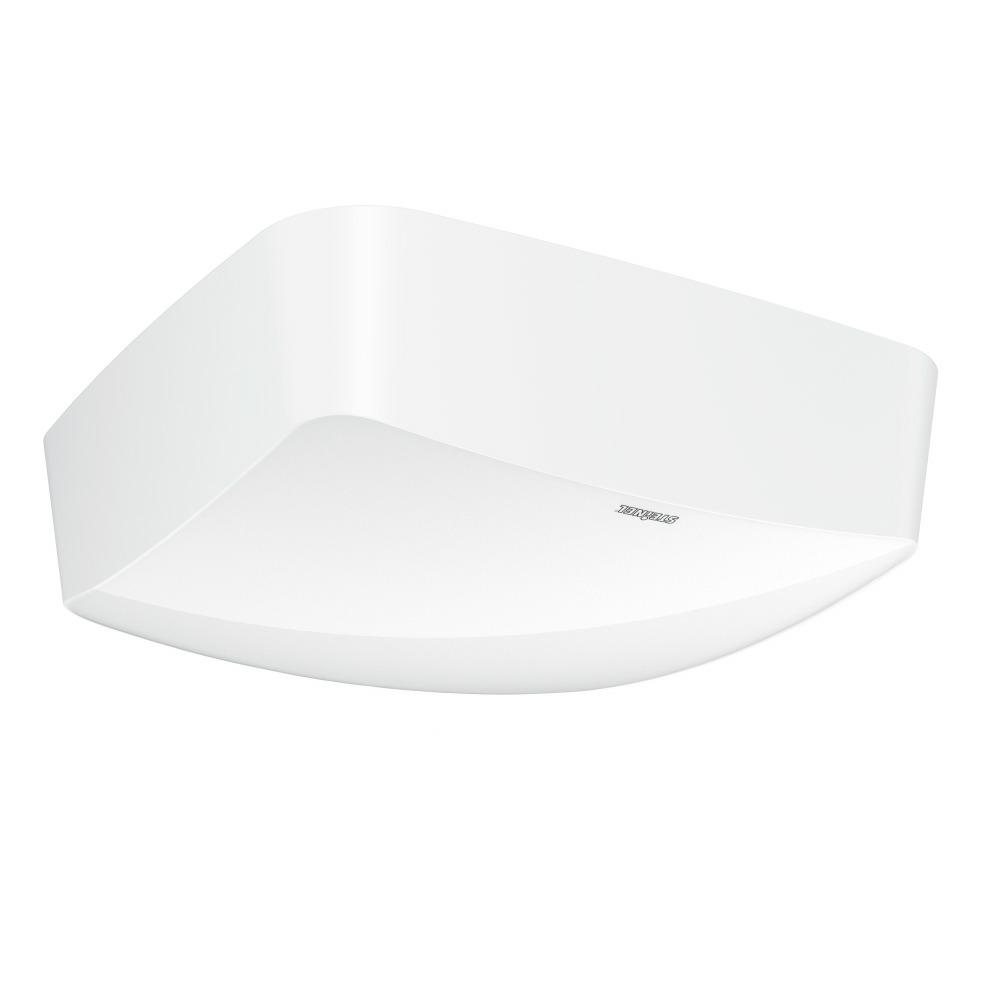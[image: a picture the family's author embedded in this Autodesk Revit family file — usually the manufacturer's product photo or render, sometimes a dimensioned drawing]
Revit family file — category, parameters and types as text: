
# Revit family: truepresence_057916
name_source: partatom
category: Electrical Fixtures
revit_build: Autodesk Revit 2016 (Build: 20151007_0715(x64)
units: mm (PartAtom-declared; Revit-internal decimal feet)

## family parameters
Cut with Voids When Loaded = No
Host = Face
Maintain Annotation Orientation = No
Part Type = Normal
Room Calculation Point = No
Round Connector Dimension = Use Diameter
Shared = No

## types (1)
- True Presence
    Apparent Load = 0 VA
    Default Elevation = 1800 mm
    Description = Type: Presence detector; Dimensions (L x W x H): 45 x 123 x 123 mm; Mains power supply: 220 – 240 V / 50 – 60 Hz; Power consumption: 1 W; Sensor Technology: High frequency; Application, place: Indoors; Application, room: classroom, lecture hall, one-person office, open-plan office, high-bay warehouse, production facilities, conference room / meeting room, hotel room, care room, duty room, recreation room, dining hall / staff restaurant, changing room, kitchenette, sports hall, reception / lobby, WC / washroom, warehouse, Indoors; Installation site: ceiling; Installation: Surface wiring; HF-system: 7,2 GHz; Electronic scalability: Yes; Mechanical scalability: No; Mounting height: 2 – 12 m; Optimum mounting height: 2,8 m; Detection angle: 360 °; Angle of aperture: 360 °; Sneak-by guard: Yes; Capability of masking out individual segments: No; Reach, radial: Ø 15 m (177 m²); Reach, tangential: Ø 15 m (177 m²); Reach, presence: Ø 15 m (177 m²); True Presence reach: Ø 9 m (64 m²); Twilight setting TEACH: Yes; Twilight setting: 2 – 1000 lx; Time setting: 30 sec – 30 min; Switching output 1, resistive: 2000 W; Switching output 1, number of LEDs / fluorescent lamps: 8 pcs.; Switching output 1, floating: No; Constant-lighting control: No; Basic light level function: No; Functions: Group parameterisation, Semi-/fully automatic, Lighting scenario, Manual ON / ON-OFF, Neighbouring-group function, Normal / test mode; Settings via: Bluetooth; With remote control: No; Interconnection: Yes; IP-rating: IP54; Material: Plastic; Ambient temperature: -20 – 50 °C; Colour: white; Colour, RAL: 9003; Manufacturer's Warranty: 5 years; Version: COM1 - surface white; PU1, EAN: 4007841057916
    Height = 0 mm  [stored 0 ft]
    Length = 200 mm  [stored 0.656168 ft]
    Manufacturer = Steinel
    ModVariant = No
    Model = 057916
    Number of Poles = 1
    OnlyDefault = No
    Power Factor = 1
    Product Name = True Presence
    Product group = Sensor-switched outdoor light
    ProductGroupID = 3
    RLX_Detail_Level = 1
    RLX_LegendID = 1.1
    RlxData = Q
eAHsfQe8HUd99ZVluchyE3Jvz71fby/Se0/v2pJ7ky33Jhe5gFxw7wgXsKm2Y4xDL6YEQglx
CGA/yR+hGpKQ0PIFEgjhw0ACIeAkOBR958zOmIux8JvH1fPc+45+Om/+87///+zs7rl7dvbO
7s5orVnTwr81vzYFTfNvI2egXIN/rrrrsc5qcpjn0GqtXAisRoT5YxLXrPnBzHmtQy6/9LxL
Ljv36ksuv+zoay6FdcmVyzfaYAZTt1naurJ1TWt5a6h1PKzlrauAy1rnG88+raiVt8pW3Ypb
BSL2bY2h9R1tH7o7ORO+NWv+feac1tGXXHTx1YsvveTqq5df2Royy5h9Zevc1gWtc36rNba0
07O2tB5a+sHM9VvHLL/q4hmbmRbMcnd+lugZrfWt9ydY+Yn884r76XGvfg836O/517S3pYn4
5j6t1mJYLwMun3v77hffe+n4nrd/a8G/vmuHcWf/9Re/+Gj22Rnj2+60/oJ9tl4wfv9RF43/
3V98ecGv7ztpnNh634cXbP/Jrz1K3P/eh+fffdddw13xIy4ebY64Nmd//Z177HDQP73r4GXL
90TesMtFeyOuTcSOsJPsD232iTbaHmGf2B+0PcI+sT/0c9ld/hH6be4Ic+2yhtlPu6wR9t+u
l4ln22y3ax1NDP23fOvbw8Wun5nP/rItt77Oz+W7XLTJdTft2HU3fcB2fif71LWdjY3Ycbcu
tLk89gFtP0qby6XNZdBmDG3G2Fy3vuNcnt1u413bkP7xruWOYz8M83P0x9i2n8Y+Zc38kTkn
XWRst18YD98IPjN+t1/op822nM22uuKN7bY5/bZ947fLNbbtj/OThy7X8M3mjru+sezqj1lH
2wezHZzt+kZ+sR/021xjsw2uG/0/WfaWR4HhLvtRa5vPumwTw7ZnAOtZ0OYRhnWW/M4TswAX
Q3sDW2fp/tHe0FZY8qi1MTAbYA5Bm3EsN7E267SZMwfYFNjMgvbm1mbJOIL5Lob2FrbOkm0Q
tHm0oM1yLsD+vABgDkGbcSznWZt12szZCtga2MaC9rbWZrmdBe3trc2SyyFos22CNtslaO9g
bZY80hO0eawmaPNITNDmsmmz3MWCtusjY9gPgjaXMQTsCrj9SHs3W2fp9gvt3W2dpes/bbeO
tN12oL2HrbPc04L2Xha097agzWWzzhKHbwPaQwBLxrAfBG0uYwbAf/ta0N7PgjY5xjrL/S1o
H2BBm7xineWBFrTJI9ZZklu0WbYtaJN/rLM8yJbkE22CdmRBmxxjnWVsQTuxoE1esc4ytaBN
XrDOklygzTKzoE1esM4ytyU5QZugXVjQJk9YZ1kCQ8D6QGVBe6a1WdYWtLntWWfJ7c+c+cCQ
Be19LGgvALjvuY+HLWiPWNBmPOssGU/uklOjFrTJJdZZLrSgzbZZZ8n2GTMGsA2CNteToM31
5bqz7FjQHrM2S7dctutiaLN91lmyv7RZHmxBm/1nnaXjJ223DWm77Uyb24hx5Ktrh/Yhts7S
9YH2Iltn6fYpbe5ngrbjBm3HJdqOb7QdD2k7rtLmMlhn6fhMm98j1lm67wJtfj8I2vw+se+0
mXMo0P3v3/5sk0987uflqoe+etPqRdf+z4Kdtx5ZtcPrb1r91EdeOjx3p8NWrZp30+r/OWTO
+Juu+OX4S//fLas/dcNOjzz8q/8aP3XPW1dfdvOxj6z+zyY3mfuWT/zk8hWr5m51w+qbX/7L
T5z1+bHxhX/5ktXZ2OnDRx4zd9UXTrtl9QOr73/0r5441LT5q5+X3KUtLvcf5o6Mzn2oNczl
HvndQ0f//onXDXO5x5/wi5GH580zyz129n9zV7a43F/9rBzd9t79H2HuX12xwrTD5X7kp2Mm
hss98cS5o8n+Jw9zubbNR02brW0XfPSsc0Y/+NUbVj/YmTn85H37jQ6/8ObV87b94qOXvmmj
0fe8/ZbVS4otFnzpw98emX/1rau/975TF3z3+rERtvm1jzzwSPrmO0c+dNVLVh97/H8tOGfG
0Oie//fm1b868t2PtP+saeetcz8+/x2Xrxhlf/5mt33qiz/d+G85+5xVT162/gIu94f37Lfq
1H+ZNczl/v1PN1r12Bbjj3K5n3/42+Mjj/xgPpf7ybGx8R9+77YFXO6qw+8cf/RjX3mEy/3a
rKFVPz/nBwu43H0/sN+qdM5HH2E741esWHXs+qfWXO6pn95v1ed3e29N/x/ft/8jn13zktXc
djfusXh0TX6TsT/56cNGuT3o/8d6s4XxN5Ya+0M3LV143uc2M/amP7tx4YcvPHIVYxC7EDnG
bplhFb0Y4eQ3LWS7tG2MsdHeQrZLP9pbyHZpo71Rtkvb9sHYrLt22RfkrqaHfUGusdkX5Bqb
fXH9Z+n6xvVDf1w/TSzbYXvsE222xz7RZnvsE23bjrFt+yaG7XE9GfObfysXzkBlPWAmsD4w
C6BvA4C6RU2jb2NgNrAJQO2hRvGcaHOAvi0A6go1h74XANQWHiu3Bnis5bnCdsD2wA7AjgA/
3+lZsDN8xC7AELArsBuwO7AH4I7R/JzH+mfCaYU7VrrSHUd4TCHccYbHHh6H3DHLlTye8fjm
jnfuGMhjojve8zjvwGOwOyY7naLPHdu5Y7rBHTJm0UHJYzV9PM7xuLn4ecJ5WO7nATdeefcb
P2WOS0/84k9GZr/568Ptk78ycvgrPjd/3r3/MjI667EFd930pyOr919v5KEj9jWff+n/HjHM
zzfCOAHNmHbY1irEMC5CDvPcZyw5XtgIba+3/4Yjn33zCaMskTNK/9LWitEvo83Rey8aZR7j
Hvj3B0fGsAz2hfnsI9u/G325foNjRlkyfiv0ke0xnstlfcmFM0cXXv7Dkav/aFtTPnrvUyP0
s35J60MjD524jclfM3qIqW92YDLK/rPOvC/8bJkpX771afD/aKT5/EcjrztkE1O/989/MsL+
suR6sH32O9ty62a9sAz6uRxuD/rZv4vhZ8ntyf5z+7JfXCb9bM+VXG8um+vNkv1jye1F37E3
NtcEWLJOP2PMdoZNP/cP62875UhTcr9d/MEvL+B2op/lqfXDC9gP1lmybpaNuKsO/Yrxczvz
c5b8nNuH7fz435YZP7cTl8eScdxerLNknduNdZasc/8wn9uN7bGkv33ZTPO5W1e37tE5bxmJ
Afbn1qt/OHILcDVs+i+/YGfjH5//2fn0vxfrehl89LNkHrcDtx23A/NXIpb5LBlPP/PJMx4f
17OgzWMn6+4Y6o6jLobHTx5PWWfp/rljLOvuWOuOs8wheMxlnDv20iZ4zGXOM4/F7jjMY7A7
HjOW+TxeE7R5fKbNkm0Q7phN2x272R8ev5lD0GZc9/GcdR7TmeOO6+6YzmM8j+Osu+M5j9m0
hwDaLHe1oM22CdrUDIL2btZmSR0gaFMPCNp7WtDmsllnuZcFbddHxrAfBO0hgDpC7XB6QXs/
gPt0f4D75ACAPmoHbZbsP7eV0xGuF/1cb2oJ/dQS1rv1hLbTFNrUFYI2l02bJbWGoO36yBj2
g6DN5VGHujWINklL0OYBlzbLYQvaIxa0R63NklpE0B4DOsDBwCHWZrnIgjaXzzpL6uC67s9i
LONQ4DCANsvDLWgfYW2WR9r6UdZmnfbRFrSPsTbLY4HjgOOBJYDvujPnBIBtELTZLkGb7bNf
k+2P77pPpD8noj9LgZMsaJ9sbZbuvOgU62McbXKYNktyljbLUy1ok7+ss5xhQfs0C9r8nhG0
TwcYx3+uHdpn2DpLLoegfaa1WXI9CNpnWdA+24L29ha0z7GgvZUFbR4LCdpcBm2Wm1rQ3sja
LJdZ0N7Egva5AP/RZg7/uXXj97KF8Qjr6xnbfbaSX72nfTz2uLiZsBjPbU8f85yvaWPlQta5
LVnnNnJxzsfP6WOdbbPOY4mLcz5+Th/r1B7Weaxzcc7n+sdP6HPxjGN9Q+vndqGPf52PJX0s
uY1Y8pjk4pyPxy76uPzZAP3zAPq4POdz/aOPNuMOABjHvjDOtUEf6+wXS2qni3M+12f2izZh
VgC55AT5wHIRwFzWNwPcZ/TRdr4tYbs4Lo/xB9OFOMY4H236uDz6WB8DnI91F08f++/qPBdw
PtoEuU0fY5zP9YX9o4/1uQDjuuvbWB/jXAy1n3Hd9SOsj3FshzGHWh+3OevcZ9RC1z/nc/3j
culjfWuAcS6G9Z2tj3Fsiz7XP/aFPtaPApjr2tkWtT2tz+XQx3Gpi2MefcsA+hjnYvayPhfD
PB5HGOdiWN/B+hjnYtrWxzgXs7f1uRjm7Wh93FaMY91tK/oYS9+BAJfL7cI4xrjtwvWnj/Vd
AMa5ZbLulss4LpO+IYBxrg+s70oXfIzjMoeAowEXx2UyZje6EOf6St+x1sf22A/G7G59rq/0
HW993M6MZYzbzvQxl749AC6DPvaXdbcv3XrSR21lHPc54xhzIUAftz2XwfbdNhiCzf7uA+QA
49bHX+fbt8s3BJtxS63PrTtjCutjLteLvv2sj8ch+ljf3/rc9mC9tD7GcV3pO8D6uM/pY93t
c3KAPtYdr8g1+lg/COB6sM5twrpbBuOcL4LNONa5nViPAfoY53znWh/juO0Yk1gfY5zvfOtj
HLcvY1Lrc9ucvjOtj9uPsYxx248+5tKXAewLfdzurLt9xBjnOxs244bw1+3H0+mCj9uZy2D7
bhvANPunQlmzgrgZ+Mt9Rt+pAH38y33GmPmswOf2K31XW99GKBnHmAVdPu5H1oetz+1/+u60
PuZy3zJmxPrc/qfvDuvbECXjGDPa5SMHWDedRf8cT+hzuZvAZhxjxgCuB/WEvjGgAzgf+cP6
wXQhznGMvtutb1OUjGPMIV0+8oz1RdbnuEjfbdY3ByXjGLO4y0fusX6o9THG+VZa31zrY8xh
XT7ykfXDrc/xmL5brY+55B5jjrA+x2P6brG+LVEyjjFHdvnIR9aPsj7GON/N1jfP+hhztPXt
aH2sH9PlI5dZP9b6HN/pu8n6eJxkHGOO6/LxO8D68dbHGOe70fp2tj7GLOny8XvA+gnWxzzn
u8H6eNykjzEndvn4/WH9Iutz3yn6Lra+9VHyO7QUOMn6hlA632nWN9P6GHNyl4/fK9ZPsT7m
Od+V1sfvKn2Mcd9Vfi/pY/3FALnLXH4nTwOuAugbwl/nO50u+PaxPtbPoAs+xvB7yrrLZZzz
nQObcXvjL7+nZwJnAfTxWOd8F1gf4/jdZczZ1scY57vU+rgM+hjjlsFl0sf65QCXsQ3+jgLL
gHMB+rbCX+dbbn17Wh9jzuvyLbT1862Pec73IuvjetDHGLce7DN9rK8AuFzmjgFc5gsB15cx
WPRdCNC3C/6OAaw7DpFT9LF+CcA4+ni8Iaecj1xzvuthM24Mf+ljjFsu+0If62492F/6WHd9
5nrQx7rb9tzG9LF+GcBl0HcwwLrb9oxxvmthM477iD7GXAHQR07Sz7rjJH2Mo+9qgHHkLeMY
4zhO7tLHuuPffrCZy7xrAObSdwjA+p0AfYxxPtc/9pk+1q8DGMf6IoD1lwD0Mc753HbmtqeP
9RsAxuX4Sx/rNwL08ThEH+s3AfSl+Esf6zcD9CX4Sx/rtwD0xfhLH+u3AvRF+Esf665/9LHf
rK8EGHcQ/tK3EngpQN/++Esf62670MdY+m4DXFzb1m/v8h0Im/U7rG/GL771q2+tXvNPa36F
uZsHLf568/ddv/z6z855/CUja9716FPfOufxN6751b27dYZ2ag0dMXf9H9ixqWmgddqP7x47
7ccbc/O27mpc+Os1c/HprLUb/u3t2NXYDNjE2v9tgI++eHCCoFkrZ2yGWZ2YrDoG3y42ZSNb
sghrHucp+CLzOPE3wGfOf9H4uw9aOHL0sm8suPf9p40DI78oH3na5m8N+HwccSbm37ZZOP7W
S19kfoO4btUu47/8kxeP7H7hEwuczXh8Po44E4PPx/GZiXE2Y6w9zlza3ErOZlsuhv6uPox3
9XO8q58m3q6LibF9MH7bZ2PbfprlOpvts4/sB/vAOZfOdn7GsC/0d9lmvax/pKsd47e5xs/t
4bYbt7fbntzeBHOdzfXi526/MK9re46wXbutjM1c9At79eltaGznR7xZL8bQpt+2aWy7LLdt
2R/jt/0x29n22cTYdTExXCb/sc1N8ovGgZFZr/rygu32uxRzUo8eyVb984I/G79xfOyqo0b+
9rynFrzjGyvHuX2f/PrMYesfp9/GjzPetjPOdhj/xC/2HWe8tUdoo71x5jP3fZcfNdJZfeP4
/yx/ijLRYhxjmOds9ovtsk34R5wfbYy4vtkY0398PsI4u9wR12frN+3bXNMHrOs41sGsr+2b
WV/bH9OO7Y+z2Qdjc/lsi+vCbebaeTx9jVn3f19SjfznP9w9fsqnTxqnPfrdG8cJ2vTxM9ps
nzm0L587853O5no4G/GmLduOaYs22jBt0UasacvZXAdnsy1rs29P2y7G9s34bZ+NbftpbNtP
Z5vlsU22wWXTRjsGtG2fjd/209jnvWH8UWCYMdZ+1NrDrHfZJobt85i+ngXtmdZmub4F7VnW
ZskjPXM2BNw/2jzCE7Q3BmYDmwBzLGhvakGbsayzZPxmwObAFha0t7Q2y7kWtNk26yzZPnNe
ALANgvY8C9o8/90a2AbY1oL2dha0Gc86S8ZzXbcHuL4E7R0saFMfWWe5kwXtnS1oU/1YZzlk
QXtXa7Pczdosd7egvYe1We5p63tZm3Xae1vQ3sfaLHkuSdDmeSBBm+c5tFkeYEGb5zSss2xb
myXPiQja3H60WXIbcj9zu3DfEbR5DkabpdvXtB0HaHPbss6S+4btkE/MJ2iTe7S5fZlD0OZ2
ps2S24Cg7bYb7SEL2tz2jOF2cu3Q5rZhnaXjA223vrTd9qHNbcY48sO1Q9utwxaw3TrSJjdn
APzH81eC/3h+S5tlakF7I2uz5HeD/2i7OPp4Dk3Qnm1tlrkFbZ6Ps86ytKC9uQVtfn8I2i6/
gu3ar2Gzb8zhd8m1Q3u+BW1+T1hnye/P1sACa7NOe9jWWY4AjCGX+BlBe9SCNvlH/0LA5XAZ
bG8vgN+FMQva/J6wzrJjQZvfq4OBQ4AxC9psg+Uia7NOe7Gts+T3hKDN7wZBm/2kzZL9nAkc
CsyyoH2YtVkebkH7CIDx5ATjCNrkAm2WjDsSOApwubR5rGGdJZfF9Twa4GcEbR5raLNkHNef
xxnGErQZx5IxtI8BuN+PtaBN7rDO8jgL2uQA6yy5P2izPN6CNvcv6yyX2JL7kDZB+wQL2tzH
rLM80Zbc97QJ2kstaHO7s87yJAva3DesszzZgjb3K+ssT7El9z1tgvapFrTJF9ZZngbwe5AB
p1vQPsOCNrcX6yy5Lbn/uB/PtKDN7xHrLM+yoM22WWfJ9hlzNsA2CNrkDEH7HIDcIA+WWdA+
14I2Y1lnyfgxgPv+PAva5AjrLM+3oM22WWe5DGDMBcCYBe2DLWhz+7D/7PtyC9rcHqyzvNCC
NrcP6ywd38ghF0Ob3GGdpeMM+eFiaF9k6yzdcmlfbOss3TahvcyCtltf2lw/gjbXh6DN9SJo
O27Q5jJYZ+n4Q9vxjbbjJG3ylKBNLhO0uQ7sH/eP6z9t7mPWWTr+cPvSx+3R/a97HnP3/GY7
53g1Y7vnQ09krnP3PObu+c2YN8y50aNss3s+9ETmOnfPz7Zzjk3fuuc6d8+B7p4bPZF5z91z
mrvnOnfPge6eGz2Bec+r3/nGC1YlW95d/+zuG35r3nn7a9euuu+ksxbsdNX1q7f85rWrZr7g
sPm0v3DNDas+89RF8+864mn/J+h/0YMXrPrU5dsvYDtPvOfWVZ/6u/vmb/lf161Ot9z44+/H
Muh/6eJXfuIL737xqv/51PWrH3zjVZ/4wTeuXcXcH9232SPvv+qGVWzztbtlj4y+von/3D9t
8MjSd9+6iu2c+81rzT5h/Ir3vNjYbOe9r79g9CHcP8D273nvrcbP+PLaG4zNNt/8zhePrkYM
4z/4xguMn/Hd8/v/++R/mv/Vf7x2lO1/+6kn6h2Rz9xv/t3c+cvRbte6jDL3o63dF8x58AJj
23UxuQfv9OoFR/990877b75u9X4LFq36r0sOXDXrS0tW7zo0ZzXt13xwzuq3X7HE2Pd+49BV
O59xnbGvXzL0yI8Ounn1QZtFq155+iGjn3l547/9J5ss/MJ/NPFHfXjJwtcf17Tzqhdft3C3
HRab9oeimxeSs8zdJUIbcx+uabewzB2+tGQhl/tKLPNDH5xj7K2xzPY3Dx01/Zm/aNWf33yd
8R80N6vZFnPv3PyEhf/82CbGv9dL5iy84p6mnQ/8YvHoKRc28V+977qF37nhYNMOl9/8+80c
nvXgmAmsD8wAZgEbABs+AxuhvrHFbJSbAPTNATYFNnsGNke9G1ugviUw1+IFKIl5wFYAz8O6
sQ3q2wLbWWyPktgB2BHYaR1jZ7S/CzAE7GrB+m5doH93YA/Axe8Jm9gL2NtiH5TEvhbOvx/q
+1scgPJAizbKg4DIgjY/p34TCZAC1PwcKIASoO7Xtk4/MR9gHMEY5hELLIZREiMW/PIRJGs3
xlAnOhYHoyQOsViEshuLUe/GoagfZnE4SoI+nhsQ1Plu8ByA54QENZqgr1urj0N9qvFWLDOf
gX1z1SeGT71q5fw3XXknN1+L5RuHXjhcb/KLEVfSP+8LPxph3IOP/cj4H9/qn0du/umH57Nk
3NCbP2Hyjj/rqWH6WdL/2uI1Jo4l6yfftuco2znkOztz97RY0n//y/c05S/OPHCU+SzpL4Zv
MfUHjz7JlKzTzzrLz3zzzqdLtjf+qttM+zu/4jbj/8iTM0bZZ/Zz79tnjn72zpmjr9rin0fY
nyXxa0ZYd+XJhz81zLjXf2e/YeZ8+2eHmO3AbcE622Ie2+H6sbxnzv7DbI+xjOH2Yzy3B+P5
OdtnyfaZx/b5OXPM9kYO7V3gY/v83Gx/+NkG/dxO9P31NduPcl9EL91h9MPfa41es972o3/5
+idH/uotW4/+9D9+NrLdd7Y168eSy935X+aZknUun3Ef/9bbh5n3vv3fOrzT52eZ+ouWr2fq
bHO9rywdZvsszf5BP7jcNrjC9q756++acvFB/zrCvvz9TouGuez2BzYYfvjJtw+z5Hp8/F1f
XXB79q+mJM8Y10KbbHfFd747zM8jxDL3S/iMbfFz9uExfMb2WXI9WHK5jGf/Gc/+kE8v+OmM
0eXb7TbKdSBvuF+euHy3Ua4befLJl204+ta/3s+U933hJaZ8cqs7nv7c7M9Xv9xsz+8tvMO0
Q57RT35xu5NXXA7befWPh0ZY/vAj2y445hu7mDqXt2Ljp+Yfev/Wps7t99pfdua/4cuzTJ3r
xDrXlXF7bffUCNvh9mE7LFnndmOdJevcTqyzZJ3bl/nfPu7Vps7txXavmLWBqXP9GM/1Zsk6
81hn+amZrzDl8Vhf5nE7sL2fnn2n8X8M25b1+2bNGf3+C54a+Um62Sj3wwNvGB95HcA690dT
HzF17hfGPzH/1cNc34vRF67f9a/fxKwXv5dcH5YPvGEE7Ywgn+W4WV+2yfVjyfViW1yfP0Zb
K9EG+8Fc9oMll8+Sy+XnXC7juVzmc7lsjzHcrmyX/WG77B/b5Wc4/LXWA9x5wyxrs+S5A0Gb
5xC0WW4EMIfnEO4fbZ5LELR5TsHYOQDjCdo8vyBoM5Y2S8bzvGNzgOcXvv1x5yTu3KX7/IT2
s52f8FyF5yYEbZ7P0GbJeN/+cx3c+rvtAdfT24nbjOA/bnd3TsRzIdrunIjnRbR5PkWbJc+n
WLKf7tzqufrPdeC6cP3d9uD2oc2S24xw2923PzsidydgZwvaPK9ineWQBe1dLWjvZm2WPOdi
OzzvYj5Be09r74WSOQTtva3Nch8L2vta0N7Pgvb+AOMOAFw7tA+0dZZtC9o8PyNoRxa0Y4Bx
PF9z7dB268DzMLeOtHmOlgPufI7na7R5XkebJc/vCNo8t6PNkudzjKXt4ujjl5mgPWJtlvwi
E7QXAmNABzgY4Dkdfe58jvZiC9ou/1DYrv3DYLMvXI/DAbZD0D7CgvZu1mbJbcHtc6S1Wad9
lK2zPBpgzDEAPyNoH2tBm9ucfp4Luhwuk+1xv3FfHm9Be4m1WZ5gQXs/4ERgKeDiabMNlidZ
m3XaJ9s6S+5vgvYpFrTZT9ZZsp+nAqcBp1vQPsPaLM+0oH0WwHhygnEEbXKBNkvGnQ2cA7hc
2stsnSWXdS5wHsDPCNrnW5vlMuACYDnAWII241gyhvaFwEXAxRa0L7E2yxda0H4RsAK4FLjM
2iwvt6B9hbVZvtjWr7Q267SvsqB9tbVZXmPr11qbddrXWdC+3tosbwDWdX9uxDJuAm62oH2L
BW1uL9ZZclu67cTtdivwEmCltVm+1II222adJdtnDvcD2yBos12CNtv37c9tyHHbyrc/3L7c
9myDoM39RNDm/rkduAO404L2y6zN8uUWtO+yNsu7LV5hfYyj/UpbZ/kqi1dbH2Nov8bWWbrl
0n6trbO8x4L2vRa077Og/UcWtO+3oP06C9oPWNDmMlhn+XoL2g9a0P5jC9pvsKD9RgvaXAf2
702A6z/tN9s6y7dYcPsyhv9mNIU5BoNVk7pvi/uOuevh70yAbdKmj/X1AfeZi3O+kmE2bhYs
xvN7Th9jnI82faxvALC+LeDinM+1x+VtCDC+ABjHv87HePpY3whgnbaLc75jrI+fbQywjKyP
Mc63ifXNRkmbnx1nfazPsT7GcxmMc74trI9xmwKM4eeMY4zzUTfpY9uMZczRgPMxzi2fPrZD
H2MTgL7N8HdzgO2eCtDHOvvgluXinG9Lhtk42mxzKV3wMcb52DZ9rM8F3LJcnPMdxjDEsa+M
5fJPApyPca5P9LFf9HFZLpf2CwDmHwowjstzPsbTx/o8gHXaLs75Trc+frYVwDK3PsY43zbW
tzVK2vzsTOtjnVx08VwG45zvoK647WCzTX7OOMY43yLrYztskzFndPkY55bPXLZDH2MXA/SR
79sDbPcGgD5y2/kYTx/rOwCs03ZxzldZHz/bEWB5s/UxxvloM5f1nQD3GX20na+G7eJ2huXi
6WOM840wzLa3Cyx+Rr2jjzHOR5s+1ocA95mLcz7XHuN2BVjeAjBuCH+djzZ9rO8GDAEXAS7O
+fg5fazvDrh4F+d8wwyzcXvAYvxyuuBjjPPRpo/1PQH3mYtzvgUMs3F7wWL8BXTBxxjno00f
63sD7jMX53yjDLNx+8Bi/Aq64GOM89Gmj/V9AfeZi3O+hQyzcfvBcvH0Mcb5DmGYjdsfFj+7
lC74GON8tOlj/QDAfebinM+1x7gDAZaXA4xjjPPRpo/1NsD6uYCLcz5+Th/r/N66eBfnfAcz
DHH8PjKWOAdwPsa5Nujj95E+ogPQtwH+bghEQAE438aw6IvpsnGu7r6X3TGJjdsUJeNYT61v
jvWxnlkfjxuMY32x9TGOfvryLp87Hh5qfeuhZL/Z39L6+D1ne+yb+57ze0sf6/MBrgd95CPr
js+sM44+x0nG8XvAGPc9om/I1kdQsj1ykbnMc/wjn+hjfQxgHLc9/WOA2/b0MY6+RQDjGOP2
z8FdPnKFdcc1HjOZy7zu7bcF6txOhwFsj3+5Dw8HjmAFvhn463zXWB8L7jPGHMMK4hjjfEda
n9uvrB9lfYzjvqXvzda3EUrGMsa1Rx/j6Dsa4DI2wV/6WD8WcD5ygPXj6EIcY5zvFOubbX2M
Ob7LR+6wvsT6HJ/oO9n6mEv+MOYk62Oe851gfY5jrJ/YFUfe0Xe79W2OkrGMWdrlYxx9p1rf
ligZx5ju5ZK3JwMvBbi+7LPzvaHLRy5z/R+0Pm4X53ur9W2GksvlMk/r8pHfrJ9ufYxxvjus
b571MeYM69vG+lg/3/q2RsnvxpnAOdbHOOc7y/pY5/eH9fOsj3HOd7b1sc7vFOt3WR/jnM8t
l8cztsllLgO4rejj928ZcC5AH2Oc7zXWx+MofYy53PoYxy8J+/Yq62NfnO8V1sftxL6wHy+z
vj1QjgEXAMsBLncv/B0D6LsEoG83/B0DGHMh4HwdW7/I+sZQOt97rW9X62PMLdZ3MMpDgIuB
B6xvDKXzueXSx1jGfRBw/WMcY15IF/rH+iKA9fsBF+d8L7I+1nmsYf0+6+P6Ot8K69vH+li/
1Pr2tz7WL7M+7gvmsn6P9TGOfvrcPpoJ+1DgCuBqgP2bhb/O92LrY53HPdavtT7GOd+V1sf6
4QDrV1kf45zvButjHI+HjHmH9THG+d5tfTNQctns2zXWF1sf664v9LFN1t8EcD2OxN+jgOuA
9wP0cRnOd32Xj7GMe8j6tkfJOMbc3OVjPn1uPcgpHl9vBG4FuAzmOd9N1sc4+hn3J9a3I0rG
MeYlXT7G0eeWuwts5pOjbhn0MZd1l1vBph6sBN4IsC/0HUsLeClAH2Oc72Hr4/GZPsbc1uXj
8Z/1262PMc73F9ZXWh9j7rA+fqcZx/qdXT7qBOsvsz7GON9HrY/HAvoY8/Iu3xJbv8v6GON8
f2l9w9bHmLu7fNQT1l9hfcxzvo9Z30LrY8wru3zUGNZfZX3Mc77PW98C62PMq7t8S239NdbH
POf7nPXxO0kfY17b5TvJ1u+xPsY432etb7H1MebeLt/Jtn6f9THP+T5jfYusjzF/1OU7xdbv
tz7mOd+nrY/HNfoY87ou36m2/oD1Mcb5PmV9PG7Sx5jXd/mon6x/yPoY43yftL4M5enAg8Af
W1/d5Xub9THuDIAxb7A+5jnfn1lfZX2Mcd8Zfj8Yx/qfA/zOxPh7JvAm4M0AfTzeON/brS+1
Psa8pct3lq2/1fqY53x/bX1cD/oY8zaAy2Cf6Xsb8GGAPuaeDXCZXwRcX5zvHdZ3BEr6WH+n
9bF+jq1/wfoY53zvsT4e55YBDwHvArgMHiOXAfT9KUAf484FGPNugL5l+Ot843TBx2XQxxi3
DC6TPtYfBxjXwd/zgPcCfwLQN4a/zvcBuuDjMZI+xrwPcL7zbf391scY51ttfVwP+hjj1mOZ
9bG+CmB7zL0A4DIfA1xfnO+D1ncwSvpYd9w9zfpY/z8Ac7kvlwPcj45/3LfO53hA7tHHmI8A
zKXvQoB1x0nGON8nYDPuGOtjzMN0wXcs/jKO9b8A6DsOf+lj/aMAfcfjL32s/yVA3xL8pY/1
jwH0nYC/9LH+ccD5LrL1z1sfY5zP9Y99po/1RwDmsn4xwPpfAfQxzvketT5yhT7WHa/oYyx9
jkPLYDOOMW5fcn/Tx7rjAfcvfaw/BnC53I/0PQa4/cZ9SR/rnwQYdyr+0se66zN9XBfWPwUw
7hT8pY/1TwP0nYy/9LH+GYA+Hp/pY/2zAH1L8Zc+1j8H0Hci/tLHutvO/B5xG3D93Xea33P6
WHfHiDOtj3XHtRm4B7y5Gfzpe8PX3/jTWx5+2NBOn/6PJ0769Zo1H1rz8V+veeo/fv2/uHn6
y09cd83I377rzL/92ZmPv+vRG84+6/E3PvHVLR86fEbrvj06913wkLlEitbNv7tXXDq24rLv
jbFyl/Hwj/8t30+nPqvh395Oz9rO2pwb4IPmFvImwn95a2t5Mu1tgaQ1a74/c9PWiTdcet7l
KxZdee51l1x20bWPxzOa5lYufOGeR40+fsbyUbJllgmebYMPPff85TMZtobXpXi36T9c0XyR
TrrjHcPd9haPz13AwG4/7/p0MbQJxrAdZ7M+eyWXgUXgNxJ+5nLQr/F9DjrTfHFXfuZnj+67
4Z3GPumO3R5lHHNhDzsbMcMuBrkjLpfLcm0yp1keFzirxXa/+9XPD9NP++zd9zR9vG7mbb9l
r7jrMuNnjLN/u631WG25tmg/e9yGLbQ97OJou2Wy/2vzd8e4dpnrbC7P/ZvtDFOuWfOjmeu3
Djn65KO4w/k8g+5/G3VV7vyvN4wRXS5slHgR67zr9tInfmGAa11jrs7PLp5BTeDVLWJZhz5L
LpoT+NdcBftNINtpjeE/sBJ4G/AY8G2AA5stgCEgAsaA4wEu9wpgJXAXcA/wIPA24L3Ah4GP
AY8BnwO+BPwD8G3g+8BPgJ8DHKSvD2wEzAG2AOYB2wI7AkPAHsA+wAFABGRABQwDY8Ai4HDg
aOB4YClwKnAmsAy4ALgYWAFcAVwNXA/cDKwEbgPuAF4G3AW8AngV8BrgHuA+4H7gAeBB4A3A
m4C3AG8D3gE8BLwbeC/wPuBPgQ8CHwY+AjwMfBT4GPAJ4FFgFfAY8EngU8BngM8BjwNfBP4G
+BLw98BXgK8B/wD8I/BN4J+BbwPfAb4LfA/4PvBD4N+BHwM/AX4KPAn8N/Bz4H+BXwK/Bnjh
ZAawHjATWB+YBWwAbAhsBGwMzAY2AeYAmwKbAZsDWwBbAnOBFwDzgK2ArYFtgG2B7YDtgR2A
HYGdgJ2BXYAhYFdgN2B3YA9gT2AvYG9gH2BfYD9gf+AA4ECgDRwEREAMJEAKZEAOFEAJVEAN
zAcWAMPACDAK8OLPGNABDgYOARYBi4FDgcOAw4EjgCOBo4CjgWOAY4HjgOOBJcAJwInAUuAk
4GTgFOBU4DTgdOAM4EzgLOBs4BxgGXAucB5wPnABsBy4ELgIuBi4BHgh8CJgBXApcBlwOXAF
8GLgSuAq4GrgGuBa4DrgeuAG4EbgJuBm4BbgVuAlwMpDWiuB1ktRAq3bUAKt21ECrTtQAq07
UQKtl6EEWi9HCbTuQgm07kYJtF6BEmi9EiXQehVKoPVqlEDrNSiB1mtRAq17UAKte1ECrftQ
Aq0/Qgm07kcJtF6HEmg9gBJovR4l0HoQJdD6Y5RA6w0ogdYbUQKtN6EEWm9GCbTeghJovRUl
0HobSqD1dpRA6x0ogdY7UQKth1ACrXehBFrvRgm03oMSaL0XJdD6E5RA630ogdb7UQKtP0UJ
tD6AEmh9ECXQ+hBKoPVhlEDrz1ACrY+gBFp/jhIw/3R81vF5PXBhJrA+MAvYANgQ2AjYGJgN
bALMATYFNgM2B7YAtgTmAi8A5gFbAVsD2wDbAtsB2wM7ADsCOwE7A7sAQ8CuwG7A7sAewJ7A
XsDewD7AvsB+wP7AAcCBQBs4CIiAGEiAFMiARZ13bbio88DOizrfXLSo87IbF3Xet3pR57x5
iztfun5xZ8cfLe5c9eJDO3M2OKyz6/sP6/z3ssM7X9v7iM7c1pGdWT88srPl947qvP3Jozv7
b31s58CjjuscdP/xnU//55LOay84sVP9aGnn+led3NnmkFM7P9zy9M7Xnzqj87VfnIXzjGW/
hflLz+zUD57cebBY0vne3kd3Vi4/rHP9Dw7u3PzB0c5ffWh+55ffLzpjJ6edjZ48qLPT6gM6
9z+8b+dTf7dXZ3TeHp3P3bBr59TWLp3N371jJ7tk+058+Lad13a27vz3ifM6e906t/PzVVt0
zthq886SlZt2fvLrTTpn3jO788V0487t39+w8+UPbNDZ9vZZnUcuWr8TnzGz8+SZ63VevWJG
5xV3tzozL1oztudXfjX26dN+OTb8P/879uP3PzV2zHU/H2uOAfob9hYQp8XpsBnq3ztxWpz2
Z03YGeK0OB02Q/17J06L0/6sCTtDnBanw2aof+/EaXHanzVhZ4jT4nTYDPXvnTgtTvuzJuwM
cVqcDpuh/r0Tp8Vpf9aEnSFOi9NhM9S/d+K0OO3PmrAzxGlxOmyG+vdOnBan/VkTdoY4LU6H
zVD/3onT4rQ/a8LOEKfF6bAZ6t87cVqc9mdN2BnitDgdNkP9eydOi9P+rAk7Q5wWp8NmqH/v
xGlx2p81YWeI0+J02Az17504LU77sybsDHFanA6bof69E6fFaX/WhJ0hTovTYTPUv3fitDjt
z5qwM8RpcTpshvr3TpwWp/1ZE3aGOC1Oh81Q/96J0+K0P2vCzhCnxemwGerfO3FanPZnTdgZ
4rQ4HTZD/XsnTovT/qwJO0OcFqfDZqh/78RpcdqfNWFniNPidNgM9e+dOC1O+7Mm7AxxWpwO
m6H+vROnxWl/1oSdIU6L02Ez1L934rQ47c+asDPEaXE6bIb6906cFqf9WRN2hjgtTofNUP/e
idPitD9rws4Qp8XpsBnq3ztxWpz2Z03YGeK0OB02Q/17J06L0/6sCTtDnBanw2aof+/EaXHa
nzVhZ4jT4nTYDPXvnTgtTvuzJuwMcVqcDpuh/r0Tp8Vpf9aEnSFOi9NhM9S/d+K0OO3PmrAz
xGlxOmyG+vdOnBan/VkTdoY4LU6HzVD/3onT4rQ/a8LOEKfF6bAZ6t87cVqc9mdN2BnitDgd
NkP9eydOi9P+rAk7Q5wWp8NmqH/vxGlx2p81YWeI0+J02Az17504LU77sybsDHFanA6bof69
E6fFaX/WhJ0hTovTYTPUv3fitDjtz5qwM8RpcTpshvr3TpwWp/1ZE3aGOC1Oh81Q/96J0+K0
P2vCzhCnxemwGerfO3FanPZnTdgZ4rQ4HTZD/XsnTovT/qwJO0OcFqfDZqh/78RpcdqfNWFn
iNPidNgM9e+dOC1O+7Mm7AxxWpwOm6H+vROnxWl/1oSdIU6L02Ez1L934rQ47c+asDPEaXE6
bIb6906cFqf9WRN2hjgtTofNUP/eidPitD9rws4Qp8XpsBnq3ztxWpz2Z03YGeK0OB02Q/17
J06L0/6sCTtDnBanw2aof+/EaXHanzVhZ4jT4nTYDPXvnTgtTvuzJuwMcVqcDpuh/r0Tp8Vp
f9aEnSFOi9NhM9S/d+K0OO3PmrAzxGlxOmyG+vdOnBan/VkTdoY4LU6HzVD/3onT4rQ/a8LO
EKfF6bAZ6t87cVqc9mdN2BnitDgdNkP9eydOi9P+rAk7Q5wWp8NmqH/vxGlx2p81YWeI0+J0
2Az17504LU77sybsDHFanA6bof69E6fFaX/WhJ0hTovTYTPUv3fitDjtz5qwM8RpcTpshvr3
TpwWp/1ZE3aGOC1Oh81Q/96J0+K0P2vCzhCnxemwGerfO3FanPZnTdgZ4rQ4HTZD/XsnTovT
/qwJO0OcFqfDZqh/78RpcdqfNWFniNPidNgM9e+dOC1O+7Mm7AxxWpwOm6H+vROnxWl/1oSd
IU6L02Ez1L934rQ47c+asDPEaXE6bIb6906cFqf9WRN2hjgtTofNUP/eidPitD9rws4Qp8Xp
sBnq3ztxWpz2Z03YGeK0OB02Q/17J06L0/6sCTtDnBanw2aof+/EaXHanzVhZ4jT4nTYDPXv
nTgtTvuzJuwMcVqcDpuh/r0Tp8Vpf9aEnSFOi9NhM9S/d+K0OO3PmrAzxGlxOmyG+vdOnBan
/VkTdoY4LU6HzVD/3onT4rQ/a8LOEKfF6bAZ6t87cVqc9mdN2BnitDgdNkP9eydOi9P+rAk7
Q5wWp8NmqH/vxGlx2p81YWeI0+J02Az17504LU77sybsDHFanA6bof69E6fFaX/WhJ0hTovT
YTPUv3fitDjtz5qwM8RpcTpshvr3TpwWp/1ZE3aGOC1Oh81Q/96J0+K0P2vCzhCnxemwGerf
O3FanPZnTdgZ4rQ4HTZD/XsnTovT/qwJO0OcFqfDZqh/78RpcdqfNWFniNPidNgM9e+dOC1O
+7Mm7AxxWpwOm6H+vROnxWl/1oSdIU6L02Ez1L934rQ47c+asDPEaXE6bIb6906cFqf9WRN2
hjgtTofNUP/eidPitD9rws4Qp8XpsBnq3ztxWpz2Z03YGeK0OB02Q/17J06L0/6sCTtDnBan
w2aof+/EaXHanzVhZ4jT4nTYDPXvnTgtTvuzJuwMcVqcDpuh/r0Tp8Vpf9aEnSFOi9NhM9S/
d+K0OO3PmrAzxGlxOmyG+vdOnBan/VkTdoY4LU6HzVD/3onT4rQ/a8LOEKfF6bAZ6t87cVqc
9mdN2BnitDgdNkP9eydOi9P+rAk7Q5wWp8NmqH/vxGlx2p81YWeI0+J02Az17504LU77sybs
DHFanA6bof69E6fFaX/WhJ0hTovTYTPUv3fitDjtz5qwM8RpcTpshvr3TpwWp/1ZE3aGOC1O
h81Q/96J0+K0P2vCzhCnxemwGerfO3FanPZnTdgZ4rQ4HTZD/XsnTovT/qwJO0OcFqfDZqh/
78RpcdqfNWFniNPidNgM9e+dOC1O+7Mm7AxxWpwOm6H+vROnxWl/1oSdIU6L02Ez1L934rQ4
7c+asDPEaXE6bIb6906cFqf9WRN2hjgtTofNUP/eidPitD9rws4Qp8XpsBnq3ztxWpz2Z03Y
GeK0OB02Q/17J06L0/6sCTtDnBanw2aof+/EaXHanzVhZ4jT4nTYDPXvnTgtTvuzJuwMcVqc
Dpuh/r0Tp8Vpf9aEnSFOi9NhM9S/d+K0OO3PmrAzxGlxOmyG+vdOnBan/VkTdoY4LU6HzVD/
3onT4rQ/a8LOEKfF6bAZ6t87cVqc9mdN2BnitDgdNkP9eydOi9P+rAk7Q5wWp8NmqH/vxGlx
2p81YWeI0+J02Az17504LU77sybsDHFanA6bof69E6fFaX/WhJ0hTovTYTPUv3fitDjtz5qw
M8RpcTpshvr3TpwWp/1ZE3aGOC1Oh81Q/96J0+K0P2vCzhCnxemwGerfO3FanPZnTdgZ4rQ4
HTZD/XsnTovT/qwJO0OcFqfDZqh/78RpcdqfNWFniNPidNgM9e+dOC1O+7Mm7AxxWpwOm6H+
vROnxWl/1oSdIU6L02Ez1L934rQ47c+asDPEaXE6bIb6906cFqf9WRN2hjgtTofNUP/eidPi
tD9rws4Qp8XpsBnq3ztxWpz2Z03YGeK0OB02Q/17J06L0/6sCTtDnBanw2aof+/EaXHanzVh
Z4jT4nTYDPXvnTgtTvuzJuwMcVqcDpuh/r0Tp8Vpf9aEnSFOi9NhM9S/d+K0OO3PmrAzxGlx
OmyG+vdOnBan/VkTdoY4LU6HzVD/3onT4rQ/a8LOEKfF6bAZ6t87cVqc9mdN2BnitDgdNkP9
eydOi9P+rAk7Q5wWp8NmqH/vxGlx2p81YWeI0+J02Az17504LU77sybsDHFanA6bof69E6fF
aX/WhJ0hTovTYTPUv3fitDjtz5qwM8RpcTpshvr3TpwWp/1ZE3aGOC1Oh81Q/96J0+K0P2vC
zhCnxemwGerfO3FanPZnTdgZ4rQ4HTZD/XsnTovT/qwJO0OcFqfDZqh/78RpcdqfNWFniNPi
dNgM9e+dOC1O+7Mm7AxxWpwOm6H+vROnxWl/1oSdIU6L02Ez1L934rQ47c+asDPEaXE6bIb6
906cFqf9WRN2hjgtTofNUP/eidPitD9rws4Qp8XpsBnq3ztxWpz2Z03YGeK0OB02Q/17J06L
0/6sCTtDnBanw2aof+/EaXHanzVhZ4jT4nTYDPXvnTgtTvuzJuwMcVqcDpuh/r0Tp8Vpf9aE
nSFOi9NhM9S/d+K0OO3PmrAzxGlxOmyG+vdOnBan/VkTdoY4LU6HzVD/3onT4rQ/a8LOEKfF
6bAZ6t87cVqc9mdN2BnitDgdNkP9eydOi9P+rAk7Q5wWp8NmqH/vxGlx2p81YWeI0+J02Ayd
TO/WrHnntzdunXj18ksuW75i09np0KazIyAt+DcmKmcdvPy65Rddc9lFV126fMUFy68cWnzl
hededRUciDr+kKHjTzhu6IgThpac1Fm6FObhi+COoijNahhLr7xm+dAVVy6/avll5y8/5+rl
V10N56Jzr77mUpRxZBaxlr/8rBumU8yyflfvrFhx0fLzrjz3mvMvvuqiFb+8eMW5l16xfNPZ
Zczk6wn+idpljsIlmwXbuvMlDDOhNbvuQujm5skANlEAJVABjDPLiU1vGBozNmZwbBbI8Jjx
MRNiZiRsOmFGwoyEGQkzEmYkzEiYkTAjYUbKjJQZqekOM1JmpMxImZEyI2VGyoyMGRkzMmZk
Zg2YkTEjY0bGjIwZZlflzMiZkTMjZ0bOjJwZOTNyZuTMyLkMw5WCGQUzCmYUzCiYUTCjYEbB
jIIZJZdRMqNkRsmMkhlm55TMKJlRMqNkhmFhxYyKGRUzKmZUXEbFjIoZFTMqZtRcRs2Mmhk1
M2pm1MyomVEzo2aG2dOOh8yJIybFEbPiiGlxxLw4YmIcMTOOmBpHXFpsd7/JjU1uw4CGAg0H
YpPbsKChgeFBbIgQGybEhgqx4UJsyBAbNsSGDrHhQ2wIERtGxIYSseFEbEgRp6bPhhax4UVs
iBEbZsSGGrHhRmzIERt2xIYeseFHnJn1NQyJDUViw5HYkCQ2LIkNTWLDk9gQJTZMiQ1VYsOV
2JAlNmyJDV1iw5e4ObgYxsSGMrHhTGxIExvWxIY2seFNbIgTG+bEhjqx4U5syBMb9sSGPnHz
5TYEig2DYkOh2HDIHsoMi2JDo9jwKDZEig2TYkOl2HApNmSKDZtiQ6fY8Ck2hIoNo2JDqdhw
Kjakig2rYkOr2PAqMUe2JCI3EsOrxPAqMbxKDK8Sw6vE8CoxvEoMrxLDq8QcVxLDq8TwKjG8
SgyvEsOrxPAqMbxKmuNLc4CxRxhyMmmOMc1BpjnKNIeZ5jjTHGgMrxLDq8TwKjG8SgyvEsOr
xPAqMbxKDK8Sw6vE8CoxvEoMrxLDq8TwKjG8SgyvEsOrxPAqMbxKDK8Sw6vE8CoxvEoMrxLD
q8TwKjG8SgyvEsOrxPAqMbxKDK8Sw6vE8CoxvEoMrxLDq8TwKjG8SgyvEsOrxPAqMbxKDK8S
w6vE8CoxvEoMrxLDq8TwKjEHp8TwKjG8SgyvEsOrxPAqMbxKDK8Sw6vE8CoxvEoMrxLDq8Tw
KjG8SgyvEsOrxPAqMbxKDK9Sw6vU8Co1vEoNr1LDq9TwKjW8Sg2vUsOr1PAqNbxKDa9Sw6vU
8Co1vEoNr1LDq9TwKjW8Sg2vUsOr1PAqNcer1PAqNbxKDa9Sw6vU8Co1vEobBWskrNEwK2I8
XqWNjDU61ghZo2SNlBlepYZXqeFVaniVGl6lhlep4VVqeJUaXqWGV80JSGp4lRpepYZXqeFV
aniVGl6lhlep4VVqeJUaXlFIzHeX/QR4dDTKhtJoDkqjASbQKIARAHMcNodSoxzm4G90w8gG
M3QGgC3IbaUzAGwEnQGs8zOApG3PplBC6osIqp82Jwf8qMyKoo5L+M2XFa6iqGKcjVVZ2ZwO
wVXWNc60cpwHNedJcNVFWeNoXNcuDwfNrCwyqFzenJolbRy36jpPC5xbNGeMcJVRWpVlkeJY
1Bw22lkEPSrLOqqbU8+knaVVXeZILaLmPBSuskYvcvQiak4vk3YOMS4T6EtUN2dOcKEO8cRZ
RnPmlLQLqCtOo3J2wxyc4KpwPoFDeRQ1mh4n7TJLsdZRhTVqTv6SdhXVJVQduUVzbgVXFWU4
WUXb9jQpadd5jq2JozGaN8e5tB1hfcuyxBlrI1lx2gbLc2h0ifMee17axolNlEd5XVZ2FdM2
FKvGuSdOPez5ZopNU0MVsxi9aE7D0naOE0dsiKiEjJpjbIp1rNMyLcsIK2a2aYoVqrK6QGLU
nFOhE1WZ1hV0L6qz5lS+OePll/A3FjLLKC8ghlhis2fRC/QfO6yq6+YEBI1FZV5B/UvsjOb8
E9sQK5NhA5WxPfnGTiuweyLoUF43Z+hJO65ACWy1DOcaZrFxG+zDvo6w+lkzuojbBciFwQfo
FjW7NgYnsNGx1jm2jlnJuI2TxjzHikP2m9PZqF3XZYSNX5R5syUw9gU5sI8iEqgZx7RB9bwq
Spwn21PZqJ3h5AljD5C+akYFEb4aWDzOeLG5m9P5qI29gdPDqo6LZpRUt7HhsWzs6gKkNkMw
LBAdR19rKLJZxbpd5FFRZTg/iKrKiHuN3VgWOC3EtkE0N0TdTrHK2PZlCSE2p3I1vnhRhp1G
loPXJgrjjLKu8PXMs9x8qeo2OAvWYF/gE7NtqnaN7YuxTppi25iTwKqNDlQ4qSOdc3MGU4El
3GWI5Cpy41TY8hHOWaO0xKY1Z2UVvlT44ufoCfamOSWq2tgyOLdEYxWGK1xtuPD1x67A6Qa+
H/ymVfj6o4sgfp1hbzTNowM4juC7AA6aU5IKe7HG4cAQFQQ2iSAV2qixx6LSuvDdjHDkyvIK
hyZuiQpfNJy3VDhM4etiThrLNvqDMzJ8pUB7c64JF79O2Nk1jjHmNLnE9xiHA+wIELE5csCF
9cFBrgQNwAo0D1eEnW22VY1448LhDd8NnC9iR5pTRJ79COFuAxzaJX4SP4mfxK8X4mdGvhI/
iV9fiL7ETyM/DO4kfhK//hQ/jsMwzHuOkR8HlpMa+XEUqZHfgI5gJX4SP4mfLnvqsqcue/bF
aK2Xl5ElfhI/iZ/Er0fi1z+XPZuf6fST34AO6iaikdI+aZ+0T9o37bRP813CnYcyEeHqRYzE
T+In8ZP4Sfye/aqnfvIb4JGhxE/iJ/Gb1uLX3GTQmzsdpv6q58TmuzQapjsdNNrrHjFK/CR+
Er9pLX7NXXG9ET/zSJkA73SY9GTPJlG3+Q3kXBiJn8RP4ifx69FlT4mf7nHvn9GlxE/iJ/GT
+En8nv03P4389Jufnm6mp5sZjdTTzcxjOvV0s/56upkue3b/1iW7GZ1q5KeRn0Z+Gvn17chv
HU940WxPjfw08tPITyM/Pddaz7XWc6375ze95xrhauSnkZ9Gfhr59e3Ir3nPw3M92lO3OjyX
EEzHzyV+Ej+Jn8RvwMVPv/lNR3F7rnWW+En8JH4SP4mfZnsO5L18v08AJX4SP4mfxK9H4jf1
T3jRZc/B+Q3u9wnVuvhM4ifxk/hNa/HjJUG9yF0vcp9+Iirxk/hJ/Ka1+E368WaZUc28zOMs
L6OsSJJ46p/wso5vdXiWm9w51sTrbaMkScsiT5K6ypvXI5VFlhd6wkv/iKjET+In8ZP49eiy
p8RP4ifxq4uyTqOoriOeO0Fi07jMcGqUZEWe8myNriyu6zwt4qqMeO5EVxmlVVni/OnpqCxK
cEmirKM6SpugLK3qMkdqEUU8+0ReVtZJWedxmkSxdeVJWpRJwrYL24cc9SRHTFbY5RVJLvHD
FkzbVZnWVRonUZ1F/OWm2YxmW/7mT9rWE170hJcsSsuqv57w0stbHTTyWxe/vz0fbUI4EjLD
lHGFm1jjKk9Lqw1JXmZFUcelbnLXTe5GIyV+Er+gxG/qL3tyibrs+XyIVa+XKfHTyE8jP132
7NFlT8321GVPXfbUZU8Opus8xzg6zTJc3DXXEtN2hMu8ZVnGSZXUZnydtuMkzhN4kwhhHIWn
7QTXH/Mor8vKXtlN22lU1jFmFaRJnNnELKqTOsviuKhrcyk5bedxgXF7HpVJHZkRfdoukjot
UwzZqiS2UWVWZXWBxAiXOZsl6rJnYrZ91C6iIq+KMsaDrGpzxTdqZ0mBPYLL7dhuGvkFNfLj
7qjaesJLr0dF06E9jfw08tPITyO/Ho38pn7Cy8TEj+c1Zbv7Te4854OHp5I40al1p0P/DNh6
pcvSPmmftE/aN+20r5L4TbsHujxTNCV+Ej+Jn8RP4qenm007MZT4SfwkfhI/iZ/ET+KnOx0w
LSTFLwFRlKT2HpAySwvd6WA0Unc6aL7L75nvosmemuzZP78dauSnkZ9Gfhr59WjkN/XiN/W3
+fHsR7f5PfP3s36sS/wkfhI/iV+PxK9/Jntqwkv/jNDWlbBK/CR+Ej+J34CLXy+fbqYHvKwr
MZrqdiV+Ej+Jn8RP4qcJL5rwogkvmvBinkXzm6dZ/8bSc631gJck+z0TXnTZUxNe+udyqkZ+
Gvlp5KeRX49GflM/4WWyD3jRb379I1Lr6nKoxE/iJ/GT+PVI/KZ+5Dex2Z6/+3SzyYufZnuu
KzGa6nYlfhI/iZ/Er2/Fb2Ijv15OeJH4TbVIravlSfwkfhI/iZ/ETxNeNOFFE1404UUTXvRG
I7wmqMzqMouSMk7LvOSFw6qNd1r35YSXXo78dKvDuhqJTXW7Gvlp5KeRn0Z+PRr5acKLZnv2
z0QaiZ/ET+In8euR+E39hJeJ/ebXywkvGvlN9QhtXS1P4ifxk/hJ/AZc/Hp52VMTXtaVGE11
uxI/iZ/ET+In8dOEF0140YQXTXjRhBdNeBmsCS+9vOypkd9Uj9DW1fI08tPITyM/jfw08tPI
TyM/jfw08tPITyO/yY38NNtTsz0127MuyjqNorqOeMUB48s0LrOyyJKsyFPOl6Iri+s6T4u4
KqPausoorcqySNOno3CnUVGXZR3VUdoEZWlVlzlSiygyD11O2llZJ2Wdx2kSxdaVJ2lRJgnb
LmwfctSTHDFZYZdXJLlGfhr5aeSnkZ9Gfhr5aeSnkZ9Gfhr5TW7kF+qtDprtua5+N+vndvWb
n0Z+Gvlp5DfgI79eTnjRfX79LHjdfZf4SfwkfhK/ARe/Xo78JH7dAtLPtsRP4ifxk/j1SPw0
4UUTXjThRRNeOKWnzvMqT9Msw7Qe80Na2o4wwacsyzipktrMuknbcRLnCbxJhDDO6UnbSYxK
lNdlZef0pO00Kus4K5I0iTObmEV1UmdZHBd1bSYRpe08LlLM/InKpI54uou2iqROy7QsI/yY
aaPKrMrqAolR0kw1SttVmdZVisXWWaTf/PSb3+R+8wtV/Ho58tN9fv082uvuu0Z+Gvlp5KeR
X49GfqFOeOnlb34Sv24B6Wdb4ifxk/hJ/PpW/Hgto2pHVR1hnnqWV3GScpgHF26XKqsqK3Gh
pJb49bNIrau+S/wkfhI/iV+PxC/Uy569FD9NeFlXYjTV7Ur8JH4SP4lfj8RvOlz2lPhNtUit
q+VJ/CR+Ej+J34CLXy8nvEj81pUYTXW7Ej+Jn8RP4ifx0+PN9HgzPd5MjzfTrQ661WFytzro
sqfu89N9frrPT/f5xSWeMl6auw2TNp5EXmZRFpdx3NzMiKeRF3jueJTyfsbUPrM8rvCsc9wd
mSVlah5QHrfrmA8xj3CbYxbx2BrH7QJPTY+jPMMtic0zy+N2lsZVhbsbc9wFyetSiEqiKs9x
g2Ma5ZVpK2rXdRnhJsuizJs7HqN2iaee417MiE9GN/dYRu0igqco4xJ9sXlZUuDOSzxQHfdH
cqZ7HLUTLj6uU9xWmZuThaiNuy4TdKOOi9g8g71u4wZLLBu3dBZ4WjtvzqyxQHQcfa3TrFnF
ul3kUVFlaVJEVZVyFWvcrlkWCe4OzSNEsxN1O8UqR3lRlil6x07U7aSMMtycyce344HtxhVj
lesqSas8y80tnHUbj3HH3aHYF/jEbJuqXWP7xhnmQ2LbFM3kSHSgSrCli7LIEzZftcuMuwyR
XEVunApbPkoyJJbYtDX3WdXOsTGzHD3B3oxDFT9d9pzqS4r9sDxd9tRlT132lPjpsqcue+qy
py576rKnLntq5De5kZ9uddBlT1321GVPXfbUZU9d9sQFanNxFNe7M1yBTnGJtLDXS/nUvwjP
9aszXIRurqriumuKK9cFLsmWeXPtFc/bw+s9zXP48Hw+0xaupaONGheqo9K6/G9yZ7dKXJfG
ZXJc4q7xytDCTuOs8jrH5Wdcfm9eBFpiVJxgPeoSF79xLdwkVhEucZsrxDXijQtvK83xIlK0
F1UxzwL64crfdO6jrnrqqqeueuqq54Bf9dQ97tNZ5Na27hI/iZ/ET+I37cRPA79pPzCV9kn7
pH3SvgHXPs31XNvgZzr7JX4SP4mfxE/ip5/8pt1IUOIn8ZP4Sfz6Vvw4++S53+mgkd90HuGt
bd0lfhI/iZ/Er0fipxsdNNmzfya5SvwkfhI/iZ/ET5c9ddlTt7jrFnfd4q5b3AfrFvdeXvbk
rYa480+3+fW9WGrkp5GfRn4a+fVo5Kcne+qypy576vkuer6Lnu8y7Z7vEupvfr0c+ekBL2ub
QNJvfo38NPLTyE8jvwEf+ekBL/0mTFPRX4mfxE/iJ/GT+GnCS9//hucrmBI/iZ/ET+I34OKn
y56+wjAd4iV+Ej+Jn8RP4qeRn0Z+utVBtzroVgfd6jBYtzpM+je/ZsioNxoNpDBq5KeRn0Z+
Gvn17chvYo83m7T4NYkSP4kfZ+8nRVHFcZJWWZnxtIguvOYxxiso46zOMuvSrQ661UG3Oky7
Wx1Cvc9P4jcdfsPzXUeN/DTy08hPI7++Hfk1r3b3f497pff5DeRozkcAJX4SP4mfxE/ipwkv
004MJX4SP4nftBY/XhKseiR+U/+El4n95qdbHXxGRNMlVuIn8ZP4TWvxozD0r/hN7LLnpMWv
SdSEl4EcFUr8JH4SP4lf34781rH4abYnTo0GdSQo8ZP4SfwkftNO/DTfZWA1baJaLe2T9kn7
pH090r5Q73SY9FVPDfw08CuKiDSgVOo2P26GKqrLJKNwFqXdMlUVZXGSZEUdVzwIIKrO8ypP
0yzL08I8NSVtR2kRl2UZJ1VS8+QzTttxEucJvEmEsMaVxKhEeV1WUWTunEzbaVTWcVYkaYLb
KZuoLKoT3FkZoxc1f/dHW3lcpGWdR2VSR/zGw1UkuNssLcsIT66xUWVWZXWBxCiJbFtVmdZV
isXWWaQHvOgBL/3ygJeJzXdpNKyucDdyhq8UaD/BOx30kx8OIhMdSfVbnEZ+GvkZiZT4JebE
I2rjPC+X+PWL+Oknv8EVp3UtphI/iZ/ET5c9ddlTt/kN7AhvbSIq8ZP4Sfwkfj0Sv6m/zU8j
P4381iZuz+WX+En8JH4Sv74VP/3mJ/F7LpFb2+cSP4mfxE/i1yPx02zPNMWstKiKOQZe20FX
/jC2jcRP4ifxk/j1SPz657KnbvOb9tos7ZP2SfukfdNO+yZ4p0Nzi4QebjaQQinxk/hJ/CR+
Ej9N9hxIgft9V5glfhI/iZ/Er0fiN/U/+Wm+Sxg/n/0+kQn1M4mfxE/iJ/HrW/Gb2J0Ok37A
iy57DvC8HYmfxE/iJ/EbcPHToz1DHX09n/2S+En8JH7TWvw4uOnV2/ym/rKnRn667DlZAZX4
SfwkftNa/DgqkvgVmvCiCS9RjNcQlOZJ/3iDQ15mBV5SUOqlDkWF58CnUcbzZJwx6KUOdfOa
j7SNN1ngTRJpVdegC7cO3lxR5lWC+3yjOCvNqyWSdok3VGR460UZx82bK5I23lCRVFHKl1ek
abNZ4yqua7wKI0vK1LzMIm6DfXldR3inRRaZd2XE7aLA+y2iPMP7JwqzP+J2luJNGniVRY5X
Xpg3V8RtPLg/z/E2izTKK9NW1K7rMsIbNYoyb15vEbXLusBTrCV+fXvZc2ITXiZ92bNJ1K0O
AymMGvlp5KeRn8Svb8VvYpc9Jy1+mvCCs9LJXlYMPU/iJ/GT+En8JH667DmwIrc2EZb4Sfwk
fhK/ARe/ZgA3iXfZauSnkZ9+89NvfkYj8T74vEjjHK+O129+WVynRVo2v3RG7ahOEvz0WMdF
HPE3zLpd40P8XlQlRVWa39Fr/MiIHyvx+2SdZs3PmnW7yKOiytIEj0OuUv6sWbdz/MyeZDl+
D0U0f7Cs2yl+5sS2L8sUb9rlxb66nZRRVldpiZ9Ok4RX9up2jJ856ypJqzzLI/5yX7fxO3WR
pPj9FZ+Y30Ordo3fVOMsSlP8HlowcdAnvOiy59pGP9PZr5GfRn4a+Wnk17cjv3U84UUjP5wa
DapASvwkfhI/iV+PxC/UlzrosuegCtgfsl4SP4mfxE/i1yPxm/qb3Kd+5MdLziXudcI17rLI
k6Su8ub1SGWR4ScBvc6vb0aKEj+Jn8RP4ifxm/BsT4nfHzLaCilX4ifxk/hJ/PpW/Kb+Pj+J
X0gC9of0ReIn8ZuW4memQsZ6xEvfT/ec+uueXKKue/4hqhNKrtRP6jct1Y+HMIlfr+91CHXG
i+51CEVwQuqHxE/iJ/HTdU9d95zwj34a+YUkYH9IXyR+Ej+Jn8RvwMVP9zr8ISIxqLkSP4mf
xE/i17fip9/8Bvcu9HUtuhI/iZ/ET+LXt+I3semeGvmtayHpx/YlfhI/iZ/Er0fiN/UTXiY2
8pP49aM4res+S/wkfhI/iV+PxG/qH/GikZ8ue05WJCV+Ej+J37QWP46KevVah6kf+U1W/JpH
ktVpEmdFGdfFhCd76ib3yWpNaHnSPmmftG9aa990eKXRpK96NvcH4rVURVnXZVIkZaU7HUIT
scn2R+In8ZP4SfwG/Kqn7nGfrEAMcp7ET+In8ZP49Uj8Qr3q+bviN+mrnhr4DYoeSvukfdI+
ad+0075K4tc3bx5aV2Ir8ZP4SfwkfgMufpP+ya9J1E9+AymUEj+Jn8RP4tcj8ZsONzposue6
GolNdbsSP4mfxE/iN+Di97s/+U3+sqfEb6pFal0tT+In8ZP4Sfx6JH79M99F4qdb4yV+Ej+J
n8SvR+IX6mXPXo78NNtzXY3EprpdiZ/ET+In8ZP4TfgBLxK/qRapdbU8iZ/ET+In8etb8aMU
Ve2oqqMorrK8ipOUwzy40jQvqyor46yuNdtzXQlIP7cr8ZP4Sfwkfn0rfhN7smcvL3tqwks/
C1533yV+Ej+Jn8RP4qfLngN5L1+32D3TlvhJ/CR+Er8BF79eXvbUyO+ZItKvdYmfxE/iJ/Eb
cPHr5WVPTXjpV7F7Zr8lfhI/id+0Fj+Oiqbf2/wmf5+fxO+ZItKvdYmfxE/iN63Fr5kcWWVp
lZR5XZRFnjSzSMqsLrMoKeO0zMtGIosiSrIsSssqz+vUqGZe5nGWl1FWJEk89Te5a7anblaf
rPhK/CR+Er9pLX69HPn1z03uk36pg37ym6zWhJYn7ZP2Sfumtfb1cuAXqvb1cr6LrnqGJmKT
7Y/ET+In8ZP4Tbv5Lhr4TbsbG56pkdI+aZ+0T9o37bRP0130S6HET+In8ZP49Uj8pn66SzMz
57kebqYbHZ456lEdh72knZAZpowrzOWKqzwteU3AuMqsKOq4hJ9XzekqiirG4/PwyLzMJZZ1
HacJpnzVWWajMGesTqOorl1eGpdZWWRJVuQpL5qjqTSL6zpPi7gqI7vAtIzSqiwLPJXPRWG2
WVGXZR3VESeXIQ+z0mrMSqvzIors8rKyTso6Ry+i2LryJC3KJGHbhe17jnqSIyYr7PKKJJf4
YaOm7apM6yqNk6jOIh7Cms1otuVv/qTtsozyIo3zwu3ZtJ3FSYwdVtV1kpvMtB2VeZVUcYmd
UVqSYIdh4mAWl3Gc2t3B2YFVlOYRpg3aXRtXoESd51lSpmaxcRvsw76O0gjp/EUpjtsFyBVH
OegWNbs2BifiqorKJE/izNArbicRJiSWaZlGeWXaitp1XUYl6IXpiSYoapcgR15J/HokfqH+
5Cfxk9j97kjXKFyjKVAviV/SLqokTtMkjqLmAbnYQmWWQvJxdplCNpuNVUV1mWQUTswMt64K
x/YE6l7jONy4cBjHqUSaZZB4pwsQexx/46RKaqPAaRvikSfwJhHCmJi2E6gQRaGsrL6nbRz9
6xh6ga5lNjGL6gTnGzF6UZuDedrOoUM4C4AM1JGRnbRdJDUUAKqFFbNRZVZldYHECGLXLFHi
l5htH7VxnpdXRRmXEGIrmllSYI/gpAvbjUONOMIpI7Q3rlNs7kbyozb2RgINruMiNudpdRsb
HsKLXV3gjI4buobaQrVBkDrNGn2v20UeFbjPICmiqkrJnBq7sSwSsCaPEM1O1O0Ueo8Tj7JM
0Tt2om4nuL0AZyw8xcNJnXHF0Pu6wrlpnuVm19ZtcBaswYkIPjEnBlW7xslFjPsVUpwYFEzs
1V1+oYofd23ZriucHWf4SoH2uuz5u2Iw3QRS4qeRn5FbiZ/E7w+/yy9U8dPIb7oJ20TWV+In
8ZP46bLngF/21MhvImIw3WIkfhI/iZ/Eb8DFTyO/6SZsE1lfiZ/ET+In8ZP46YVG0+6+P4mf
xE/iJ/HrW/HjFK51+B73ZsiISUuYYIwpbkWCaVBm8kwVYXaTeQpqXeWcy1S2MZkdM6FTzEqL
MNMZromMPhTz/G0niZ/ET+In8euR+PGQX7UxDzYp8LhrzK6EZjQu3OmEOccp7ocq7POwOQk6
wjTnOsONJ/xRrsL0VdyIxJnPuN0mb+7gw3Rk3PlkpiVjurKJwv0zaKPG3U1RI0XPLX69vOzJ
TpRtid/zJ1q9OmGQ+En8JH4Svx6Jn2Z7auTXP6Io8ZP4SfwkfgMufprt2avR0iC1I/GT+En8
JH4DLn69vOyp3/wGRQAlfhI/iZ/ET+Kn2Z7TboKOxE/iJ/GT+A24+P3uZc9mgmbNhwXiUXY1
Hh9c2CEdJm/meMwcnjHbPBQYk1s02XNQBnvd6yHtk/ZJ+6R9A659uurZfdCX3czJkfhJ/CR+
Er8eid/U3+nQ3PygNxpJ0PwnmUr8JH4SP4mfxE+XPfWTn17npzcamZcvmZf5POOPXuenNxol
GV6FVOJNifZWddzLHmc53q2ElzPGus1Pt/n5j8Cer1GrRn4a+Wnkp5HfgI/8ejjfRc93eb60
qtfLlfZJ+6R90r4ead/UD/wm9mTPXs53kfj1WoSer/YkfhK/aSl+zfvrI7xXvcBr26V+fat+
mvDSP5cZny+VW9typX5Sv2mpfhwyxBK/KC84LKr6Vvymfuhn7wbUSx36foKMxE/iJ/HTyK9v
xW9iI7/f/c2v0k3ufS9eaxvRTdQv8ZP4SfwkfgMufr380U8jv4mKS+hxEj+Jn8RP4ifx031+
024kKPGT+En8JH4SP4mfxE83uesmd93kXuFZx3hJeG1u8o/aeK5xEidZWmW6yX163eTeXC/V
g60HUhg18tPITyM/jfz6duQ3sdmemvAS+u9vz0f/JH4SP4mfxK9vxW9isz014eX5EJfQlynx
k/hJ/CR+PRK/UN/qoJFf6EL0fPRP4ifxk/hJ/HokflP/fLOJjfwkfs+HuIS+TImfxE/iJ/Hr
kfhN/chvYr/56bJn6EL0fPRP4ifxk/hJ/PpW/CY28pP4PR/iEvoyJX4SP4mfxE/ip/v8BvJ2
ht8nwBI/iZ/ET+LXI/EL9Te/Xo78ONYs25UebN33Yinxk/hJ/CR+Ej+N/PpezH7fKO/ZPpP4
SfwkfhK/HolfqBNeJj3bsxky6gkvAymMEj+Jn8RP4te34qcJL3qZ7bON6ibik/hJ/CR+Er8e
id90+M1PrzSaiLD0Q4zET+In8ZP49Uj8pv6yp0Z+GvlNVmglfhI/iZ/Er2/Fb2I3uU/6N78m
Ub/56Te/2ZTKoqjiOMHbXcqMvwbTVdZ1nCZ5nNWZeQcMXHVR1mkU1XVE+iAojcusLLIkK/KU
hKUri+s6T4u4KqPausoorcqySNOno7IoKeqyrKM6SpsgvFqmLnOkFlFkl5eVNXqRoxdRbF15
khZlkrDtwvYhRz3JEZMVdnlFkkv8JH4Sv74VP438NPLTyE/iNztO23lcpDgLiMqkjsy5Sdou
kjot07KM8KJCc9qRtku8l64usjiOkua0I21XZVpXaYx6FvHiVXMOYU4kfvMHmWWUF2mcF+60
Jm1ncYKF4oSkTnKTmbajMq+SKi5xJlLaMyScrZRZlMVlHKf2XCQrcG4SpXmU16k9r4nxDj2c
1eRZUqZmsXG7jnmiE6UR0vmTUhy3C5xZxVGOc62oOa+J21kaVxXWOk/izKxk3E6iKs+x4mmU
V6atqF3XZVTi3KrMmy0RtUucGeWVxG/aiR/Pfst2nYIveHdjjfPrgrzBDXxVXucV6Vw3Z81w
4X2OOMEv8VZHvOSxidJtfn0/GOS4zY3f8rgqCr3LVu+ylfbpXbazK5wh8XQlKeO0zEuer1Q4
64im17tsudoSP2yEyQ6uQs6T+Omqp656auA37QZ+1cRGfhwYSPwkftgClEr95MfNUEW4CJJR
OAtzUkxXhYt6CX7TrHEBrtlYuH5X5WmaZfhh010QxE+cuPAWJ1VSm98d0zauGuYJvEmEMCam
7QSXH3k1sKzsr5ppG5f9alyhSXidxiZmUZ3gV9YYvajt9Uxd9dRVz7rCL/J5lpsL2nUbP3CD
NbgCnZe1uSJctWtcVY6zKE1xRbjg8b3qkfhN/Z0O5H3Vjqo6wjWrLK8wG6FZIaxdXlaYmYCv
S90M4OoKcwIyfKVwsV/iN5ijOZ+RpkZ+Gvlp5KeRX9+K32Tnu0xs4PcsVz25QIwF9ZNf318J
lfZJ+6R90r5pp30THPg9i/hpvovP4CrkWImfxE/iJ/EbcPGb9FVPiR/GuSEL2B/SN4mfxE/i
J/GT+OlOh4EVubUJpMRP4ifxk/j1SPw4qatq4/bLpMhxc2YV4+64xoUnXOCGyxTPwShq3tJZ
4QkXmJKDiV51hnsuOcKq8LAMPICCc79wp2ne/JiH207xxAtzOypuUzVRuHUUbdR4qkVUWpfm
u6ztAC//2keuEj+Jn8RP4tcj8Zv6yZ6Tne+i3/zWLgrTRTAlfhI/iZ/Er0fiF+rIr7lbbxJ3
OjzLb36a7Tko4ijxk/hJ/CR+PRK/UEd+mvAyKILVy/WQ+En8JH4SvwEXv16O/HSrQy8F6Pls
S+In8ZP4Sfx6JH7T4bKnxO/5FKxeLlviJ/GT+En8Blz8dNmzl6IxKG1J/CR+Ej+J34CLXy8v
e2rCi8RPr7LVc62NbOptfuaR5VEbTxlP8FLBOi5i89blGi+Lw2sNMzzCvMD7mXnDW43XB+I1
hHjweZ1mzQsL63aRR0WVpUkRVXiLnInK47JI8DT0PEI0X0VYt1O8wBBPoS7LNK8KHoBr3BYX
ZXgFI1/YjFc0G1eMFxjqudbmUdfdz7WW+A2KYPVyPTTy08hPIz+N/Pp25LeOX+rwLLc66De/
XgrQ89mWxE/iJ/GT+PVI/Kb+VoeJiV8vR34Sv+dTsHq5bImfxE/iJ/HrW/HTE170pJbJCqLE
T+In8ZP4Sfz0YGs92BqvQ85T8+O80cUSb4Gu8et7EfHqN116kbte5B7neHV8w4i0rQkvmvCS
Y+pNkSTx1F/2nNjIT7c6THZ0NMh5Gvlp5KeRn0Z+Gvlp5KeRn0Z+VRKnaYJ55UnK38lxeoC3
sWC8i9empDi/bVwV3rSiWx2MbGrkp5GfRn6zy3ZZZHmRpnhpU1TF5MQgj5oGYd008tPITyM/
jfx6NPLjIX+g3uenWx0GWMQlfhI/iZ/Er0fiF+pvfrrVYRBGar1eB4mfxE/iJ/GT+Ok3v2l3
mVbiJ/GT+En8Blz8NNuz16OmQWhP4ifxk/hJ/AZc/HTZcxDEqtfrIPGT+En8JH4SP1321GVP
3eqgWx3M1H2+SyB+xp+0XZZ4s0Cqm9zbSZ7VWfz/2XsPOEuO6mr8rVarHFc5j3J+6q7OuzOz
86RVzjlLK6GVBKwCWuXEogASUZKFEDmJYDDBWMaANLv6YzLYxib5M9hgzB9hbDAG2UYm6Dun
ukp6LCs0Nd/bVc3Mmd+cV7fuu7e6uvu8Pl0dm6zEixt0q8Pzd6uDnu2pWyomOyLUyE8jP438
NPIb0MhPtzroPr+pI8YSP4mfxE/iNyDxW/O3Okxs5KcLXiY7OprOeRI/iZ/ET+I3ZcVvzT/b
k1OsunWCNxdXZWFMUxd8T7Ge8DLlzhlK/CR+Ej+J3zQXv0Fe7Snxmy6jQYmfxE/iJ/GT+Olq
zyk3cvt/FWGJn8RP4ifxG5D46YIXXfCiC16assI7EBL/1jfTzdIqx2PPTV4WGU9SQ3UzXCre
FFmZ1lXCo+Z0VUlWVxWejf50VJ6YsqmqJmmSrA3Ks7qpCqSWSWKvxTfdvGpM1RRpZpL28nzT
LUxWVsaw7dK9iqFA3RSIyUs3vdIUEj+J34wWP/446gGJ35q/4GVi5/wGediTWy+d8/t/HXXF
kK+Rn8RP4jejxY/CIPHDDnbpZA0XsBQ1drDxZ3eboXS5wc48XmJWmqrWOb8YhGsQfZD4Sfwk
fhI/jfwmLH4a+Q1CeGJoQ+In8ZP4SfymufgN8j4/jfxiEK5B9EHiJ/GT+En8pqz4cRxWd5O6
SfBgxryoU5O1x3ETXDdQ1XVepTkOX9rzdE2NiwLyOkkSg4TWlRm8eb1Km2c57NmeLNRhz2l5
JajET+In8ZP4TVnxm9gFL5MWvzZR4ifx4/WYpizrFLtX2KXKuVtEF84FY5eqwC5W7q6+NLra
k0umKYq6yLI8xzWt9unHWTfB1a1VVaWmNo295DTrpiYtDLwmQRgXadY1KSpJ0VTYTbWLNOtm
SdVgJ9VwV9Ul5kljsMjTtMQKaBOLFE9aboqkMk1iV0/WLU2TVRmeSI0ndruoKq/zpkQidoFd
W3WVNXWGyTZ5Yru60jOtXS/0YGtubdNED7YuGl58XXeLCj98/2DrNX+rw2oe+a1C/DhFXe05
iMOOz3cbGvlp5KeRn0Z+03zk1x69nMRhz1WIn875Pd+iNajpS/wkfhI/id80F79WwwYjfhr5
DUp8nu92JH4SP4mfxG+ai9/vj/wmdr2LBn44xvt8a9Tqmr60T9on7ZP2DUj71vwpv4ld7/L7
2jfBiz1XIX4a+K0uMVrT7Ur8JH4SP4nfgMRPTzfToz2nzkhR4ifxk/hJ/CR+E37Ai653WdMj
tNU1PYmfxE/iJ/Gb5uKn611Wl4BM5XYlfhI/iZ/ET+I34ZGfzvlNZcHr77vET+In8ZP4TXPx
m/QFL23i7zzgReLXLyBT2Zb4SfwkfhK/GSd+k77TQdo3lfWuv+/SPmmftE/aN+O0T3c6TJ2L
MvsFa5C2xE/iJ/GT+En8dMpv2t7L/myCKfGT+En8JH4SP4mfxA/vxCrwVgA+uB5vayiqvCyb
tCrLhBcL06V3OnAx1ElTmZzCWVZuydR1kqfG5FheNe/1RZTe6ZBXvGIAi6LCCypyLKAqTdsX
V5guXlBh6iTjuysyvh8AUWmdNg2WWm6qzL5FIu2CfUXTJHilRZ7YxZp2yxKvt0gKvEIkKe3C
T7t5hoWON1kUeOMFT8qkaRdvbCsKvMwiS4ratpV0m6ZK8EKNEq8hsEFJt2rKEu/dSPKqMbap
pAuqFzVe8FahLy4vNyXespHjRSa48oGt650OxSrf6TAT7nHXbX7PNpKaan5scIzbPOGNRDVE
TuJn0gxvDcL7Lu1LMbnhzjNIPt5+mSW5VzqJX7s7lHWh+HiLUlY3DfaVqAx4a1NV1KZOqySV
+EEua1PWld2hbKC2UG0IdZPlrb433bJIyjrPTJnUdUb5aLoF9jcNXoNVJIimAjfdDHqfFGVV
ZZBmboAbvEksyfEWqgr7EMb+iptuCr1varxvrMgL+66qpgvO4jVYWBf4xu4Y1N0GOxdpjpe9
Yseg5M+/nuYjP/5qq64ea63zfP0CLfHTYU+rV3qbn0Z+BmNsHMgoDLW1xj4fB+uQyawq7OGN
GmPuxORQzQqD6lW9zW8mjPx0tWe/gExlW+In8ZP46bDnNB/5tXfr9Y/8dKfDjDvFt7JOS/uk
fdI+ad80175JH/VsRfN3bnHXKb+VRWSq1iV+Ej+Jn8Rvyoofj0HWXZyOT3CxQl7UaXuiHq4s
K6q6znFuE1dQ6ZQflsBUFanV1W+Jn8RP4ifxG5D46W1+eqHR1BFZiZ/ET+In8RuQ+K356100
8ps6YrO6RnCTbVfiJ/GT+En8prn4TfqcX5v4O+f8dLHnZMUmtjyJn8RP4ifxm+biN8hzfrrg
JTYRm2x/JH4SP4mfxE/iN+Gnm0n8Jis2seVJ/CR+M1L87NNP8JQyPd5MT3jJ8Sy7ppyw+um4
Z2wqNtn+SP2kfjNS/bgJk/jNlMebDfK4p8RvsmITW57ET+In8dNxzyl73LN9Ettz3eg36Ste
VnGXu8QvNhGbbH8kfhI/iZ/Eb5qLn0Z+kxWI6Zwn8ZP4SfwkfhI/nfObcY+AkfhJ/CR+Ej+J
n8RP4qf3+dV6nx8vBrHvcV3pI+tWFd4Al6VFiffL8kQKXt6n9/nZtxgm3aQxBu/UbdIyTfhy
3qbb4GVAep8fn76JtxjneK9wVqR42TMXTt3NcrxysDBlk+PVwuRSjRcUFhneR1ziXYNV0Z7N
M3hxJgiXoEzq1oWXRKKNBq8fTirnWm3n/HSXO1bMdD30qZGfRn4a+Wnkp5GfRn7TVuSeTbwl
fhI/iZ/Eb5qL36Sv9tTITyM/vMGZNKBUlmWd4sUheFlIzmuo6KqaJsXhCrw8JLfHyeDCG6Gb
LEn8wTHTzXDcoypzk5dFZu+xgitP8baRrEzrqr3nGK4qyeoKxzmyp6PwLmncgFo1OOzBwyWY
Xp7VDd453RRlkrjp5TgGUjUFepG0x+tMtzBZWRnDtkvX9wJ1gwMrCQ69tE2VppD4SfwkfgMS
v1hf6yDxe7bRz0z2a+Qn8ZP4SfwGJH5r/rUOE7vP7/dvddCb3GfcUc6VdV7aJ+2T9kn7pqz2
8SDSanyZre5xx/JdWTSmS13iJ/GT+En8pqz4TWzgN+mjnhI/iZ9O+ZU1rqbOcLKwPVdY4wJs
k1M4y8q76gQX/eOcZpPWPPqD/YqmKOoi4yXdOP1IV9ZNcIqzqqrU1Kax5x2zbmpSXt1dmQRh
bZRJUUmKpqrdWc2smyVVg8vETWZwarWNynFtPc6y4jpxnHNtXUVaZjj3mVSmSewZ2axbGlxw
n+EWBdzC4aKqvM6bEom8gLxNrKusqTNMtsFV5nStdJODrepOB9y3wIWTdE2BE9xpk2FxF7rT
oajwyzAmjfWU3+8f9ax12HPajugmOjLVyE8jPyvKEj9jdzySLi7tKmo857+q08ZKftLNTYnd
EVxnhZ0GiV+eZFVdFO5uvaLChW5e/KbOKb/Jix8JUHXrBPd0VmVhTFMXrZDicj7cApthDzWp
7W7ARDfCint+Dq1K/CR+Ej8d9pyyhz1X8zk/7hBB6bD3gyvaK+wDYZdI4oclMB0EW+In8ZP4
SfwGJH5r/rDnxMSv1bCmxq1QOc4k4Gj/5Ed+Er/pIHycB4mfxE/iJ/GbsuI3sQtedM5vugjW
IOdD4ifxk/hJ/AYkfjPhnJ9GfoMUoOezLYmfxE/iJ/EbkPit+cOeGvlNj/Nvz4cISvwkfhI/
id+UFb/VfM5P9/lNk4tbViWuEj+Jn8RP4jcg8dNhT93qMHVGohI/iZ/ET+I3ZcVvYiO/SV/w
opGfRn56woue8GI1Uu+y1U3uM/wmd13wsqpDiFPRp5GfRn4a+Wnkp5Hfqt9lq5GfRn4a+Wnk
p5GfHm+G7YDJ/8DIbyZc7anHm03FUd6q+qyRn0Z+Gvlp5DdlR34Tu9VBT3hZ1cZ/pvskfhI/
iZ/Eb5qL36QveNGzPXXYU4c9ddhThz112PO5DnvGequDRn4zfZS3qvnXyE8jP438NPKb5iM/
id+qNv4z3Sfxk/hJ/CR+AxK/WC94mbT46WpPHfbUYU8d9tRhTx32nKqHPXXOb6aP8lY1/xr5
aeSnkZ9GfgMa+emcnx5vpsebNXjzcZYkTZPwiAMkNkurvCpzk5dFxmck0JWnTVNkZVpXSeNc
VZLVVVVm2dNReWLKpqqapEmyNijP6qYqkFomSe5cVWOqpsC7KpPUuQqTlZUxbLt0fShQNwVi
8tJNrzSFxE/iJ/Gb5uKnkd+qRj4z3aeRn8RP4ifxm+bip3N+M13oVjX/Ej+Jn8RP4jcg8Yv1
gheN/Fa18Z/pPomfxE/iJ/EbkPjpnJ/O+emcn8758axmUxR1kWV5jjOb3ClOs26Cc5xVVaWm
No098Zh1U5MWBl6TIKyNMikqSdFUtTutmXWzpGrSvDSZSXOXmCeNafI8TcumsedRs26RlhlO
fiaVaRLu7mKKpWmyKsPrGGqTuqgqr/OmRGJi2rOtWbeusqbOMNkmT2xX7anTlT6yrt7qoLc6
/IFne8YqfoMc+enZntNlxKiRn0Z+Gvlp5DdlR37cnau7Sd0kSVrnRZ2ajEoHFy6aq+o6r7Cv
2Ez6nF+bWOcGF/A1lSlNVUv8JH55lduhheniOssG11kWYFnuLrU0Gvlp5JdWuPS2ciTB5blV
nuRplabt8NZ0MYw1dZJxhJu5C3nTGhcAY7ycmyqzVEq7TcorexMMfPOEA4s07ZbYEqVJAbol
7YW8aTfP0rrGeLfAuNgOb9OuSeqiwJA3S4ratpV0sf1KMOwuq6IdAyfdCpcCY3Se5Lhc2I66
k26ZwFNWaYW+uDxs+zAWx1XGGDFr5PcHRn6xnvMbpPiRXlW3TozJqrIwpqkLHompuriYvcB1
6jg8k9Qpl8R0EYnpOh8a+Wnkp5GfxG+aj/wGedhT4jddxFDiJ/GT+En8JH6rfpntKg57Svwk
fjrsaXIKZ1nZw2Wmi8NueWpwF3+DI3A8PqcLXnTYs8IhV1zbVOLJDTw21uA4K47XgiBNlrdH
dptuWSRlnWcGR8vqjMxpcN1SVRpcJlUkiOax16ab4UhvUpRVleGgLI+9NjjfkOS4SomPcsDD
G6wrxZHepjZZXeSFvZap6eKRDrhMCoeg8Y09JFx3GxxWTnH0MsMh4ZKJ9ZQVPy6J5z7np5Hf
dBGsQc6HRn4a+Wnkp5HfNBe/QZ7z0wUvgxSg57MtiZ/ET+In8ZP46bDnjLtAR+In8ZP4SfwG
JH5T52rP9gLNhnfN4sreBo8PLt3JPFy8WeDwM646bh8KjCs7++900Cm/53OwNshpS/ukfdI+
ad+AtC/We9wHedRT4jdIAXo+25L4SfwkfhK/KSt+lCJd76JbCicjohI/iZ/ET+I3ZcVPF3tK
+CYjfMyR+En8JH4Sv2kufjrsOVmBmM55Ej+Jn8RP4jdlxU+HPTXym6xAS/wkfhI/id+UFb/V
fNizvTleV3tOy7sgJH4SP4mfxG/Kit/ERn467DnZ0dF0zpP4SfwkfhK/AYnf1LnNr9Z9ftNy
NBci1hI/iZ/ET+I3IPGL9T4/PdozRBRmSqzET+In8ZP4Sfwm/IQXPdpzuoijxE/iJ/GT+E1Z
8ZvYOT+N/KaLYA1yPiR+Ej+Jn8RP4jfhkR/lVi9yH6QIPV9tSfwkfjNS/Oy77tIEr9cry6KW
+kn9pH4z7goYqZ/Ub0aqH3fgJX4z5WW2utfh+RpexTxdiZ/ET+Knkd+UHflN9i533eow4wZ6
K+uwtE/aJ+2b0drHQVE947Rv8vf56WrPlUVkqtYlfhI/id+MFj9eCTndxW+QRz0lflNV7Fbu
t8RP4ifxk/hN85HfIMVPV3uuLCJTtS7xk/hJ/CR+01z8dJ/fVBWo1dlviZ/ET+In8ZP46U6H
GXcBjMRP4ifxm9HipwteyiptygmLn875rc7R2JpsW+In8ZP4zWjxm5kXvOhOhxk30FtZV6V9
0j5pn7Rvxh31lPZJ+0zXcMfPamBal2WS1kVWkRnWVeVl2aQV/Dw2QldZ1mlqsjqvcp9YNU2a
mSLNmzx3UU1ZNVmSNI3Py9Iqr8rc5GWR2UdrmG6Wp01TZGVaV+2jpuCqkqyuqjLLno7KE4MD
ElWTNEnWNp5ndVMVSC2TxE0vrxpTNQV6kaTOVZisrIxh26Xre4G6KRCTl24GS1NI+6R90r4B
aV+sb/PT5S4rD3pUdwrnlU7iB3Uva5NmmUmTxGRO3as8g+QnNeQ8dzpaJ01lcgpnWXlXneSp
gbo3ac23mqGtpsBDI7MszyHx3C6kWTeB2FdVlZraNFaBs25q0sLAaxKEtVEmRSUpmqp2+p51
s6Rq0rw06FruEvOkMdjfSNGLxu5QZN0iLbHrUiSVaRLb+6xbmiarsqpKMGMuqsrrvCmRmJh2
tyPr1lXW1Bkm2+SJ7ardh1jpI+uimaLM0gJTbHdrsi5mGhPFDkljCj+TVVGbOq2wJ1L5ZYiZ
ybGAqjRtZ9J0MTOmTjLOZ+b2a9Ia+0NYarmpMjvttItdL+zoJJj9PLGLNe2W2LNKkwL7Wkm7
X5N28wwLHXNdYOnYmUy7JqmLAjOO53fVtq2k2zRVgoVfVkW7JPRgT6xNrqDpfpcf57HqNjX2
jnP8pEB73eK+sUZ+GvlBOgoOQN32V+In8StqXAFRQYidaOamxO4Ijjhgp4FXO+CJoIbamzag
TdVKftLFroiBBjdpmdqDFE0Xex0QXuznlDicwT2WBo/RhmpDqJssb/W96ZZFUtZ5ZsqkrjPq
e4N9mKo02GUqEkSzE003g95DqqoqQ+/YiaZrqiTHHguPb+CIhnWl0PumxoGZIi/sfk3TxQ4b
dpmwI4Jv7I5B3W2wc5HmSZbNlAd7Svw00vt9sbfHNvGzsaVGfhr5aeSHI/wSPw4Gq5yDdcgk
9Z2HJGqMuROTQzUrDKob7i3W3QLD6LyADGMcn67597hzmF93MZBLcMImL2qckWmHspD2oqpx
dgYHShr2flIjv1Y1sQODgw041lMa7BLZtuoEezpVWRjT1AX3a6ouzurgqEiGwzMJjnrAJcGJ
exlI/HTOzx6O1WFPYw85J12Jn+HAUuKHA/D2qDpe3Sfxm45CLvGT+En8dMHLgC54WfMjv1an
n2vkN+nDnhr5TeMRrMRP4ifxk/jNOPFrj1Q2vHws7A53HfWcLoNAaZ+0T9on7Ztx2jf5iz0l
fhI/3eanOx2sbOpOB3t/hy72fF6ud1nNRz3bC2V0ym9aXrujkZ9Gfhr5aeSnkd+EH+ypkZ9G
fhr5aeSnkZ9u83ue73TQyC/uuwliFkqN/DTy08hPI78Bjfx4ALju4u5/U0IU8UAV3B3XuvBw
QzxrJ8MtgaW7P5DPPUrwZKMmx+N22rsITYVnD/JhR3jIUNHKGp44hIcd2icR4QlFti08NQht
NHigYVI512q72FOHPXWxpx7tqaebWY3U0824AdYDXqK5x31iI79WwwbzdDMd9ox5NBfSN438
NPLTyE8jvwGN/KbdbX4a+Wnkp5GfRn4a+enRnvE93UwjP53zCxnt9cdq5KeRn0Z+GvlN85Hf
pA97ruIBL5RbPPBMj/ac8rc/SPwkfhI/id80F79JP91Mhz112FOHPXXYU4c9ddgzvsOevPxk
Nb7UQeIn8ZP4SfwkfhK/+MRvYuf8NPLrP9cluz1PqsOeOuypw5467DllD3tObOQ3SPHTOb/p
Ip4SP4mfxE/iNxnx4wvmp8i7bCV+00WwBjkfEj+J34wUv4RPHsHN6hXeV1rUUr/JqF8Ub3Kf
2HHPSV/uqZN+Oumnk3466WdFUo944dZWj3iZYo94GeTQT494GeTw6/lsS0M/Df1m5NCPmzCN
/LKkKCkM9TQf+U1a/NpEvdNoyt/UtyqRlfhJ/CR+Ouwp8dM7jaalwK1K9LxP4ifxk/hJ/Ka5
+Omcn9/gq3zmeXASP4mfxE/iN83Fb9KHPXXBiy540QUvuuDFaqQueNEFL3mSVVPsgheN/DTi
e2bE55eFRn4a+Wnkp5GfRn4656dzfklaF5l9/7LVxSovyyatNPLTyE8jPz3fbKo+30wjPz/a
UfnMCFAjP438NPLTyG9AI7/K3jaRN7kpi6rAq9NLux9dd/O0yrMqy4o0L5v27vgsz4ukMGWT
F2lKdaq7pioyA1eaJ1XR3r5uEgzJsjRBmdStK80rtNFUjUkq50rqJsFue17UqcnaezcSTKyq
67xK86bROT+J3jOi55eFxE/iJ/GT+A1I/KbOq9z5hJ+q22QGalylTamjnjrqqaOetUkz/CSS
pN2FxN4B9llLHfXUUU8d9YzvqOdqfrC17nHXxZ465Sfxk/hJ/J5L/GI96jnpU34SP4mfxE/i
J/GT+E1V8dMpP3+aS+Uzp/50yk+n/HTKT6f8pvkpv0mP/NrE33m0Jy+6qbp1YkxWlYUxTV20
5w+rMi/KLMM5xKROOQaW0MS9DCR+Ej+Jn8Rvyorfaj7ntwrx00sdpouoS/wkfhI/id+AxG/N
n/ObmPgNcuQn8ZP45VXOI+lUz6ppUtyeg/tpcr7dma4G9/dkSdI0CXkHT4b7fHBcwORlkZE+
dOUpbsDJyrSu2leLwlUlWV3hvp7s6ag8wZ1AVdXgNh/eHoS8PKsb3EPUFGWSuOnluOenagr0
IkmdqzBZWRnDtkvXhwJ1gxuJEtxq1DZVmkLih4Wadesqa+osxd1UuMWKC8cuxpU+sq6ebqan
m/2Bp5utefFr7/zTbX7TRZDW5HxQqIqhDv6WrViLRWfZAn4+tfLfb5/idyuIjfq+Zyz/ZgH9
KW07y1Y8ZfNsyO99rOdy/Bc770uL02/BNglft+aEPo7vYLrrnty5urO488LO5fhcQg+x6VWd
CzoXdc6H94LOZfjm/E7SKTpVp+mknZIRG/iIlfy+BZaze50MebDmLkUbF6KVVWV1Md2L0AvE
bXJIp9dZuNLUup0Xda7sXMLvtzgBLVyB6Gs6L0ZG+uyRjF4ZW/UwpSVoiX1hT67pvKBzaWcp
PEs6v3nqUnxybq/E98ie42tLfTuzr+9c3xlibS1XrnstMq7C0rsCbdm4TfOOQUzVyfGZYu6T
vrLwLcVSzl6Kpfj0Wh9Yr2bZljbtzF4FD2etwtfv8t9v0++E/SP+4t7x0fO2GPvdL6y/00le
7vw/Y9zz+ncApj43oAcPIrYH3APMsXljY3fYst2S4Je94mrUV8HoP+izTbgP5j7X32bPFfAs
389Zh1/49XZaX9RR1n5mW9W/jer2xVlzp5UdqM/CX7tIUJm9rDO0Fud4g6vxq7t8pd/+GCKG
AP5xm+n/ZnfW6sxZNmuTlpNjcO/qvuqPmvX0Gpsof4Lifn78a963wvdo1WXb3ub2y+/s0+kc
CuvlwBVzb9/90nsvG9/z9u/O/5f37DDu7b/6ylcezT8/a3zbndaev8/W88fvP/qS8b/986/N
/+19p44TW+/78PztP/3NR4n73//wvLvvumu4L37Ex6PNEd/mBt969x47HPSP7zl40eI9kTfs
c9HeiG8TsSPsJPtDm32ijbZH2Cf2B22PsE/sD/2cdp9/hH6XO8JcN61h9tNNa4T9d/Nl49k2
2+2bRxtD/y3f/d5wuevn5rG/bMvPr/dz+j4XbXLebTtu3m0fsJzfzT71LWdrI3bczwttTo99
QNuP0uZ0aXMatBlDmzEu18/vOKfnltt43zKkf7xvuuNYD8P8Hv2xtuuntU9/at7IRqdeYm2/
XhgP3wi+s36/Xuinzba8zbb64q3tlzn9rn3rd9O1tuuP95OHPtfyzeWO+76x7OuPnUfXB7sc
vO37Rn6xH/S7XGuzDc4b/T9b9LZHgeE++1Fn2+/6bBvDtrld4j4bQZuaRJvl2g7cxPgY2tyg
sW43bCj5R3tda7Ultx7rAxsAzCFoM47lhs5mnTZzuU+4MbCJA+1Nnc2ScQTzfQxtbplZZ8k2
CNrcWtBmScVhf7YAmEPQZhzLLZ3NOm3mbAVsDVBrCdrbOpvldg60t3c2S06HoM22Cdpsl6C9
g7NZ7uhAm5t5gvbODrQ5bdZZ7uJA2/eRMewHQZvTGAK4NffrkfZurs7Srxfau7s6S99/2n4e
afvlQHsPV2e5pwPtvRxo7+1Am9NmnSU23xa0hwCWjGE/CNqcxiyAf/s60N7PgTY5xjrL/R1o
H+BAm7xineWBDrTJI9ZZklu0WVJ3CdrkH22WB7mSfKJN0E4caJNjrLNMHWgbB9rkFessMwfa
5AXrLMkH2ixzB9rkBessC1eSE7QJ2qUDbfKEdZYVMASsDdQOtGc7m2XjQJvLnnWWXP7MmQcM
OdDex4H2fIDrnut42IH2iANtxrPOkvHkLjk16kCbXGKd5QIH2mybdZZsnzFjANsgaHM+Cdqc
X847y54D7TFns/TTZbs+hjbbZ50l+0ub5cEOtNl/1ll6ftL2y5C2X860uYwYR776dmgf4uos
fR9oL3R1ln6d0uZ6Jmh7btD2XKLt+Ubb85C25yptToN1lp7PtPk7Yp2l/y3Q5u+DoM3fE/tO
mzmHAf1///anG37qC7+slj/0jZtWLLz2f+bvvPXI8h3ecNOKJz/2suG5Ox2+fPmWN634n0M2
Gn/Llb8ef9n/f8uKz9yw0yMP/+a/xs/Y89YVl9983CMr/rPNNXPf9qmfXbFk+dytblhx8yt+
/alzvzg2vuAvXroiHztr+Khj5y7/8pm3rHhgxf2P/uXjh9k2f/PLiqu0w+n+/dyR0bkPdYY5
3aN+cNjo3z3++mFO94STfjXy8JZb2uket8F/c1V2ON3f/KIa3fbe/R9h7l9eucS2w+l+7Odj
NobTPfnkuaNm/9OGOV3X5qO2zc628z9+7vmjH/7GDSse7M0efuK+/UaHX3Tzii23/cqjl71l
vdH3vfOWFSeWm83/6ke/NzLv6ltX/PADZ8z/wfVjI2zzmx974JHsrXeOfGTpS1ccd8J/zT9/
1tDonv/n5hW/Oeq9j3T/tG3n7XM/Oe9dVywZZX/+erd9mks/2/pvOe/85U9cvvZ8TvfH9+y3
/Ix/njPM6f7dz9db/thm449yul98+HvjI4/86zxO99NjY+M//uFt8znd5UfcOf7oJ77+CKf7
zTlDy395/r/O53T3/dB+y7ONPv4I2xm/csny49Y+o+F0z/jsfsu/uNv7G/rfeN/+j3z+qZeu
4LK7cY9DR58qbrL2pz97+CiXB/3/0GyyIP32Kdb+yE2nLLjwC5tYe+Nf3LjgoxcftZwxiF2A
HGu3Yx96MZIrblrAdmm7GGujvQVsl360t4Dt0kZ7o2yXtuuDtVn37bIvyF1BD/uCXGuzL8i1
Nvvi+8/S943zh/74ftpYtsP22CfabI99os322Cfarh1ru/ZtDNvjfDLmmb9lC2ahshYwG1gb
mAPQtw5A3aKm0bc+sAGwIUDtoUZtAmwK0LcZQF2h5tC3BUBt4bZya4DbWu4rbAdsD+wA7Ajw
+51WgZ3hI3YBhoBdgd2A3YE9AL+N5vfc1q8MrxV+W+lLvx3hNoXw2xlue7gd8tssX3J7xu2b
3975bSC3iX57z+28B7fBfpvsdYo+v23niukHV8iYQw8lt9X0cTvH7eahzxMuxHS/CPjxynvf
/Bm7XXr8V388ssFbvzXcPe3rI0e88gvztrz3n0dG5zw2/66b/mRkxf5rjTx05L72+6/+nyOH
+f16GCegGdsO21qOGMYlyGGe/44lxwvroe219l935PNvPWmUJXJG6T+ls2T0a2hz9N5LRpnH
uAf+/cGRMUyDfWE++8j270Zfrl/n2FGWjN8KfWR7jOd0WT/x4tmjC6748cjVf7StLR+998kR
+ll/YecjIw+dvI3Nf2r0EFvf5EAzyv6zzrwv/2KRLV+x9Znw/2Sk/f4nI68/ZENbv/fPfjbC
/rLkfLB99jvffOt2vjAN+jkdLg/62b9L4WfJ5cn+c/myX5wm/WzPl5xvTpvzzZL9Y8nlRd9x
N7bHBFiyTj9j7HKGTT/XD+vvOP0oW3K9Xfrhr83ncqKf5RnNw/PZD9ZZsm6njbilh33d+rmc
+T1Lfs/lw3Z++m+LrJ/LidNjyTguL9ZZss7lxjpL1rl+mM/lxvZY0t+9fLb93s+rn/fk/LeN
pAD7c+vVPx65BbgaNv1XXLSz9Y/P+/w8+t+Peb0cPvpZMo/LgcuOy4H5yxDLfJaMp5/55Bm3
j2s50Oa2k3W/DfXbUR/D7Se3p6yz9H9+G8u639b67SxzCG5zGee3vbQJbnOZs/K22G+HuQ32
22PGMp/ba4I2t8+0WbINwm+zafttN/vD7TdzCNqM69+es85tOnP8dt1v07mN53acdb895zab
9hBAm+WuDrTZNkGbmkHQ3s3ZLKkDBG3qAUF7TwfanDbrLPdyoO37yBj2g6A9BFBHqB1eL2jv
B3Cd7g9wnRwA0EftoM2S/eey8jrC+aKf800toZ9awnq/ntD2mkKbukLQ5rRps6TWELR9HxnD
fhC0OT3qUL8G0SZpCdrc4NJmOexAe8SB9qizWVKLCNpjQA84GDjE2SwXOtDm9FlnSR1c3f05
FNM4DDgcoM3yCAfaRzqb5VGufrSzWad9jAPtY53N8jjgeOAE4EQgdN6ZcxLANgjabJegzfbZ
r8n2J3TeJ9Kfk9GfU4BTHWif5myWfr/odOdjHG1ymDZLcpY2yzMcaJO/rLOc5UD7TAfa/J0R
tM8CGMc/3w7ts12dJadD0D7H2Sw5HwTtcx1on+dAe3sH2uc70N7KgTa3hQRtToM2y40daK/n
bJaLHGhv6ED7AoB/tJnDPz9v/F12cP6Y9bWs7b9bxp/e0z5ue3zcbFiM57Knj3ne17axbAHr
XJascxn5OO/j9/SxzrZZ57bEx3kfv6ePdWoP69zW+Tjv8/3jN/T5eMaxvq7zc7nQx0/vY0kf
Sy4jltwm+Tjv47aLPk5/A4D+LQH6OD3v8/2jjzbjDgAYx74wzrdBH+vsF0tqp4/zPt9n9os2
YWcAueQE+cByIcBc1jcB/Hf00fa+zWH7OE6P8QfThTjGeB9t+jg9+lgfA7yPdR9PH/vv69wX
8D7aBLlNH2O8z/eF/aOP9bkA4/rr2zgf43wMtZ9x/fUjnY9xbIcxhzkflznrXGfUQt8/7/P9
43TpY31rgHE+hvWdnY9xbIs+3z/2hT7WjwaY69vZFrU9nc/n0MdxqY9jHn2LAPoY52P2cj4f
wzxuRxjnY1jfwfkY52O6zsc4H7O38/kY5u3ofFxWjGPdLyv6GEvfgQCny+XCOMb45cL5p4/1
XQDG+Wmy7qfLOE6TviGAcb4PrO9KF3yM4zSHgGMAH8dpMmY3uhDn+0rfcc7H9tgPxuzufL6v
9J3gfFzOjGWMX870MZe+PQBOgz72l3W/Lv180kdtZRzXOeMYczFAH5c9p8H2/TIYgs3+7gMU
AOPWxqf37dvnG4LNuFOcz887Y0rnYy7ni779nI/bIfpY39/5/PJgvXI+xnFe6TvA+bjO6WPd
r3NygD7WPa/INfpYPwjgfLDOZcK6nwbjvC+BzTjWuZxYTwH6GOd9Fzgf47jsGGOcjzHe9wLn
YxyXL2My5/PLnL5znI/Lj7GM8cuPPubSlwPsC31c7qz7dcQY7zsPNuOG8OnX41l0wcflzGmw
fb8MYNr1U6NsWEHcLHxyndF3BkAfP7nOGDOPFfj8eqXvaudbDyXjGDO/z8f1yPqw8/n1T9+d
zsdcrlvGjDifX//03eF866JkHGNG+3zkAOu2s+if5wl9PndD2IxjzBjA+aCe0DcG9ADvI39Y
P5guxHmO0Xe7822MknGMOaTPR56xvtD5PBfpu835NkLJOMYc2ucj91g/zPkY433LnG+u8zHm
8D4f+cj6Ec7neUzfrc7HXHKPMUc6n+cxfbc43+YoGceYo/p85CPrRzsfY7zvZufb0vkYc4zz
7eh8rB/b5yOXWT/O+Tzf6bvJ+bidZBxjju/z8TfA+gnOxxjvu9H5dnY+xpzY5+PvgPWTnI95
3neD83G7SR9jTu7z8ffD+iXO539T9F3qfGuj5G/oFOBU5xtC6X1nOt9s52PMaX0+/q5YP935
mOd9Vzkff6v0Mcb/Vvm7pI/1lwDkLnP5mzwTWArQN4RP7zuLLvj2cT7Wz6YLPsbwd8q6z2Wc
950Pm3F745O/03OAcwH6uK3zvoucj3H87TLmPOdjjPdd5nycBn2M8dPgNOlj/QqA09gGn6PA
IuACgL6t8Ol9i51vT+djzIV9vgWu/gLnY573vdj5OB/0McbPB/tMH+tLAE6XuWMAp/kiwPdl
DBZ9FwP07YLPMYB1zyFyij7WXwgwjj5ub8gp7yPXvO962Iwbwyd9jPHTZV/oY93PB/tLH+u+
z5wP+lj3y57LmD7WLwc4DfoOBlj3y54x3nctbMZxHdHHmCsB+shJ+ln3nKSPcfRdDTCOvGUc
YzzHyV36WPf82w82c5l3DcBc+g4BWL8ToI8x3uf7xz7Tx/p1AONYXwiw/lKAPsZ5n1/OXPb0
sX4DwLgCn/SxfiNAH7dD9LF+E0Bfhk/6WL8ZoM/gkz7WbwHoS/FJH+u3AvQl+KSPdd8/+thv
1pcBjDsIn/QtA14G0Lc/Pulj3S8X+hhL322Aj+u6+u19vgNhs36H88361Xd/890VT/3jU7/B
VeMHHfqt9vM9v/7WL87/0ktHnnrPo09+9/wvvfmp39y7W29op87QkXPX/lc3NrUNdM786d1j
Z/50fS7ezl2tC59BVy4+nfXsRnh7O/Y1Ngs28ex/6+CrrxxsEMTrOO0VoJ0x+HZzKeu5kkVc
13Gejh8ytxN/DXzuBS8ef+9BC0aOWfTt+fd+8MxxYORX1SNP2zzXgO/HEWdj/m2bBeNvv+zF
9hzEdct3Gf/1H79kZPeLH5/vbcbj+3HE2Rh8P47vbIy3GePscebS5lLyNtvyMfT39WG8r5/j
ff208W5ebIzrg/W7Plvb9dNO19tsn31kP9gHXnPpbe9nDPtCf59t58v5R/rasX6Xa/1cHn65
cXn75cnlTTDX25wvfu/XC/P6lucI23XLytrMRb+wVp9ehtb2fsTb+WIMbfpdm9Z20/LLlv2x
ftcfu5xdn22Mmxcbw2nyj21uWFwyDozMefXX5m+332W4JvWYkXz5P83/0/Ebx8eWHj3yNxc+
Of9d3142zuX7xLdmDzv/OP0ufpzxrp1xtsP4x3+17zjjnT1CG+2NM5+5H7ji6JHeihvH/2fx
k5SJDuMYwzxvs19sl23CP+L9aGPE983F2P7j+xHGuemO+D47v23f5do+YF7HMQ92fl3f7Py6
/th2XH+8zT5Ym9NnW5wXLjPfzpey19p5//cT65H//Pu7x0//7KnjtEd/cOM4QZs+fkeb7TOH
9hVzZ7/b25wPbyPetuXasW3RRhu2LdqItW15m/PgbbblbPbtadvHuL5Zv+uztV0/re366W07
PbbJNjht2mjHgrbrs/W7flr7wjeNPwoMM8bZjzp7mPU+28awfW7T13KgPdvZLNd2oD3H2Sy5
pWfOuoD/o80tPEF7fWADYENgIwfaGzvQZizrLBm/CbApsJkD7c2dzXKuA222zTpLts+cLQC2
QdDe0oE293+3BrYBtnWgvZ0DbcazzpLxnNftAc4vQXsHB9rUR9ZZ7uRAe2cH2rs4m+WQA+1d
nc2SCjnkyt1REvTt4WyWe7r6Xs5mnfbeDrT3cTZL7ksStLkfSNDmfg5tlgc40OY+Dessu85m
yX0igjaXH22WXIZcz1wuXHcEbe6D0Wbp1zVtzwHaXLass+S6YTvkE/MJ2uQebS5f5hC0uZxp
s+QyIGj75UZ7yIE21wVjuJx8O7S5bFhn6flA288vbb98aHOZMY788O3Q9vOwGWw/j7TJzVkA
/7j/SvCP+7e0WWYOtNdzNkv+NvhH28fRx31ogvYGzmZZONDm/jjrLCsH2ps60Obvh6Dt82vY
vv0GNvvGHP6WfDu05znQ5u+EdZb8/WwNzHc267SHXZ3lCMAYconfEbRHHWiTf/QvAHwOp8H2
9gL4WxhzoM3fCessew60dwUOBg4Bxhxosw2WC53NOu1DXZ0lfycEbf42CNrsJ22W7Ods4DBg
jgPtw53N8ggH2kcCjCcnGEfQJhdos2TcUcDRgM+lzW0N6yw5Lc7nMQC/I2hzW0ObJeM4/9zO
MJagzTiWjKF9LMD1fpwDbXKHdZbHO9AmB1hnyfVBm+UJDrS5fllneaIruQ5pE7RPcqDNdcw6
y5NdyXVPm6B9igNtLnfWWZ7qQJvrhnWWpznQ5nplneXpruS6p03QPsOBNvnCOsszAf4OcuAs
B9pnO9Dm8mKdJZcl1x/X4zkOtPk7Yp3luQ602TbrLNk+Y84D2AZBm5whaJ8PkBvkwSIH2hc4
0GYs6ywZPwZw3V/oQJscYZ3lCxxos23WWS4CGHMRMOZA+2AH2lw+7D/7vtiBNpcH6ywvdqDN
5cM6S883csjH0CZ3WGfpOUN++Bjal7g6Sz9d2pe6Oku/TGgvcqDt55c254+gzfkhaHO+CNqe
G7Q5DdZZev7Q9nyj7TlJmzwlaJPLBG3OA/vH9eP7T5vrmHWWnj9cvvRxefT/9V/H3H99s7vm
eAVj+6+Hnsi1zv3XMfdf34zrhnlt9Cjb7L8eeiLXOvdfn+2uObZ967/Wuf8a6P5roydy3XP/
Nc391zr3XwPdf230BK57XvHuN1+03Gx+d/OLu2/4nevOu9+8dvl9p547f6el16/Y/DvXLp+9
xeHzaH/5mhuWf+7JS+bddeTT/k/R/+IHL1r+mSu2n892Hn/frcs/87f3zdv8v65bkW2+/ic/
iGnQ/7JDX/WpL7/3Jcv/5zPXr3jwzUs/9a/fvnY5c39y3yaPfHDpDcvZ5ut2yx8ZfUMb/4V/
XOeRU95763K2c8F3rrXrhPFL3vcSa7Od97/hotGHcP8A27/n/bdaP+Ora2+wNtt867tfMroC
MYz/8Jsvsn7G91/f/9+n/eO8b/zDtaNs/3tPPt7siHzmfudv585bjHb75mWUuR/v7D5/owcv
srabF5t78E6vmX/M37XtfPDm61bsN3/h8v964YHL53z1xBW7Dm20gvZrP7zRindeeaK17/32
Yct3Pvs6a19/4tAjPzno5hUHbZIsf9VZh4x+7hWt//afbbjgy//Rxh/90RMXvOH4tp1Xv+S6
BbvtcKhtfyi5eQE5y9xdErQx9+GGdgfT3OGrJy7gdF+FaX7kwxtZe2tMs/udw0Ztf+YtXP5n
N19n/QfNzRu2xdw7Nz1pwT89tqH17/XSjRZceU/bzod+dejo6Re38d+477oF37/hYNsOp9/+
PXMNz1pwzAbWBmYBc4B1gHVXwnqor++wAcoNAfo2AjYGNlkJm6Lej81Q3xyY67AFSmJLYCuA
+2H92Ab1bYHtHLZHSewA7AjstJqxM9rfBRgCdnVgfbc+0L87sAfg4/eETewF7O2wD0piXwfv
3w/1/R0OQHmgQxflQUDiQJvfU78JA2QANb8ASqACqPuNq9NPzAMYRzCGecR8h2GUxIgDf3wE
ydqPMdSJnsPBKIlDHBai7MehqPfjMNQPdzgCJUEf9w0I6nw/uA/AfUKCGk3Q16/Vx6O+pvF2
TLOYhXWz9FPDZyxdNu8tV93Jxddh+eahFw03G/5qxJf0b/nln4ww7sHHfmL9X9rqn0Zu/vlH
57Fk3NBbP2XzTjj3yWH6WdL/uvK1No4l66fdtuco2znk+ztz9XRY0n//K/a05a/OOXCU+Szp
L4dvsfUHjznVlqzTzzrLz33nzqdLtjf+6tts+zu/8jbr/9gTs0bZZ/Zz79tnj37+ztmjr97s
n0bYnxPT146w7svTjnhymHFv+P5+w8z53i8OscuBy4J1tsU8tsP5Y3nPRvsPsz3GMobLj/Fc
Hozn92yfJdtnHtvn98yxyxs5tHeBj+3ze7v84Wcb9HM50fdX12w/ynWRvGyH0Y/+sDN6zVrb
j/7FG54Y+cu3bT368//4xch239/Wzh9LTnfnf97Slqxz+oz75HffOcy8D+z/9uGdvjjH1l+8
eC1bZ5trff2UYbbP0q4f9IPT7YIrbO+av/qBLQ896F9G2Je/22nhMKfd/dA6ww8/8c5hlpyP
T77nG/Nvz//FluQZ4zpok+0u+f4Phvl9gljmfhXfsS1+zz48hu/YPkvOB0tOl/HsP+PZH/Jp
i5/PGl283W6jnAfyhuvl8St2G+W8kSeffvm6o2//q/1sed+XX2rLJ7a64+nv7fp8zSvs8vzh
gjtsO+QZ/eQXlzt5xemwndf8dGiE5Y8/tu38Y7+9i61zekvWf3LeYfdvbetcfq/7dW/em742
x9Y5T6xzXhm313ZPjrAdLh+2w5J1LjfWWbLO5cQ6S9a5fJn/veNfY+tcXmz3yjnr2Drnj/Gc
b5asM491lp+Z/UpbnoD5ZR6XA9v7+Xl3Wv8nsGxZv2/ORqM/2uLJkZ9lm4xyPTzwpvGR1wOs
c3209RFb53ph/OPzXjPM+b0UfeH8Xf+GDe188XfJ+WH5wJtG0M4I8lmO2/llm5w/lpwvtsX5
eSPaWoY22A/msh8sOX2WnC6/53QZz+kyn9Nle4zhcmW77A/bZf/YLr/D5q+zFuD3G+Y4myX3
HQja3IegzXI9gDnch/B/tLkvQdDmPgVjNwIYT9Dm/gVBm7G0WTKe+x2bAty/CO2P3yfx+y79
+ye0V7V/wn0V7psQtLk/Q5sl40P7z3nw8++XB1xPLycuM4J/XO5+n4j7QrT9PhH3i2hzf4o2
S+5PsWQ//b7Vc/Wf88B54fz75cHlQ5sllxnhl3tof3ZE7k7Azg60uV/FOsshB9q7OtDezdks
uc/FdrjfxXyC9p7O3gslcwjaezub5T4OtPd1oL2fA+39AcYdAPh2aB/o6iy7DrS5f0bQThxo
pwDjuL/m26Ht54H7YX4eaXMfrQD8/hz312hzv442S+7fEbS5b0ebJffnGEvbx9HHHzNBe8TZ
LPlDJmgvAMaAHnAwwH06+vz+HO1DHWj7/MNg+/YPh82+cD6OANgOQftIB9q7OZsllwWXz1HO
Zp320a7O8hiAMccC/I6gfZwDbS5z+rkv6HM4TbbH9cZ1eYID7ROdzfIkB9r7AScDpwA+njbb
YHmqs1mnfZqrs+T6Jmif7kCb/WSdJft5BnAmcJYD7bOdzfIcB9rnAownJxhH0CYXaLNk3HnA
+YDPpb3I1VlyWhcAFwL8jqD9AmezXARcBCwGGEvQZhxLxtC+GLgEuNSB9gudzfJFDrRfDCwB
LgMudzbLKxxoX+lsli9x9auczTrtpQ60r3Y2y2tc/Vpns077Ogfa1zub5Q3A6u7PjZjGTcDN
DrRvcaDN5cU6Sy5Lv5y43G4FXgosczbLlznQZtuss2T7zOF6YBsEbbZL0Gb7of25DTl+WYX2
h8uXy55tELS5ngjaXD+3A3cAdzrQfrmzWb7CgfZdzmZ5t8MrnY9xtF/l6ixf7fAa52MM7de6
Oks/Xdqvc3WW9zjQvteB9n0OtP/Igfb9DrRf70D7AQfanAbrLN/gQPtBB9pvdKD9Jgfab3ag
zXlg/94C+P7Tfqurs3ybA5cvY/g3qy3sNhismtR9W1x3zF0Ln7MBtkmbPtbXBvx3Ps77Koa5
uDmwGM/fOX2M8T7a9LG+DsD6toCP8z7fHqe3LsD4EmAcP72P8fSxvh7AOm0f533HOh+/Wx9g
mTgfY7xvQ+fbACVtfne887G+kfMxntNgnPdt5nyM2xhgDL9nHGO8j7pJH9tmLGOOAbyPcX76
9LEd+hhrAPo2weemANs9A6CPdfbBT8vHed/mDHNxtNnmKXTBxxjvY9v0sT4X8NPycd53OMMQ
x74yltM/FfA+xvk+0cd+0cdp+VzaWwDMPwxgHKfnfYynj/UtAdZp+zjvO8v5+N1WAMvC+Rjj
fds439YoafO7c5yPdXLRx3MajPO+g/ritoPNNvk94xjjfQudj+2wTcac3edjnJ8+c9kOfYw9
FKCPfN8eYLs3APSR297HePpY3wFgnbaP877a+fjdjgDLm52PMd5Hm7ms7wT47+ij7X0NbB+3
MywfTx9jvG+EYa69XWDxO+odfYzxPtr0sT4E+O98nPf59hi3K8DyFoBxQ/j0Ptr0sb4bMARc
Avg47+P39LG+O+DjfZz3DTPMxe0Bi/GL6YKPMd5Hmz7W9wT8dz7O++YzzMXtBYvxF9EFH2O8
jzZ9rO8N+O98nPeNMszF7QOL8Uvogo8x3kebPtb3Bfx3Ps77FjDMxe0Hy8fTxxjvO4RhLm5/
WPzuMrrgY4z30aaP9QMA/52P8z7fHuMOBFheATCOMd5Hmz7WuwDrFwA+zvv4PX2s83fr432c
9x3MMMTx98hY4nzA+xjn26CPv0f6iB5A3zr4XBdIgBLwvvVh0ZfS5eJ83f8u+2OMi9sYJeNY
z5xvI+djPXc+bjcYx/qhzsc4+ukr+nx+e3iY862Fkv1mfyvn4++c7bFv/nfO3y19rM8DOB/0
kY+sez6zzjj6PCcZx98BY/zviL4hVx9ByfbIReYyz/OPfKKP9TGAcVz29I8BftnTxzj6FgKM
Y4xfPwf3+cgV1j3XuM1kLvP6l99mqHM5HQ6wPX5yHR4BHMkKfLPw6X3XOB8LrjPGHMsK4hjj
fUc5n1+vrB/tfIzjuqXvrc63HkrGMsa3Rx/j6DsG4DQ2xCd9rB8HeB85wPrxdCGOMd53uvNt
4HyMOaHPR+6wfqLzeT7Rd5rzMZf8Ycypzsc87zvJ+TzHWD+5L468o+9259sUJWMZc0qfj3H0
neF8m6NkHGP6p0venga8DOD8ss/e96Y+H7nM+X/Q+bhcvO/tzrcJSk6X0zyzz0d+s36W8zHG
++5wvi2djzFnO982zsf6C5xva5T8bZwDnO98jPO+c52Pdf5+WL/Q+Rjnfec5H+v8TbF+l/Mx
zvv8dLk9Y5uc5iKAy4o+/v4WARcA9DHG+17rfNyO0seYK5yPcfyRsG+vdj72xfte6XxcTuwL
+/Fy59sD5RhwEbAY4HT3wucYQN8LAfp2w+cYwJiLAe/rufolzjeG0vve73y7Oh9jbnG+g1Ee
AlwKPOB8Yyi9z0+XPsYy7sOA7x/jGPMiutA/1hcCrN8P+Djve7Hzsc5tDev3OR/n1/uWON8+
zsf6Zc63v/OxfrnzcV0wl/V7nI9x9NPn19Fs2IcBVwJXA+zfHHx630ucj3Vu91i/1vkY531X
OR/rRwCsL3U+xnnfDc7HOG4PGfMu52OM973X+Wah5LTZt2ucL3U+1n1f6GObrL8F4Hwchc+j
geuADwL0cRred32fj7GMe8j5tkfJOMbc3OdjPn1+Psgpbl9vBG4FOA3med9Nzsc4+hn3x863
I0rGMealfT7G0eenuwts5pOjfhr0MZd1n1vDph4sA94MsC/0HUcLeBlAH2O872Hn4/aZPsbc
1ufj9p/1252PMd73585XOR9j7nA+/qYZx/qdfT7qBOsvdz7GeN/HnY/bAvoY84o+34mufpfz
Mcb7/sL5hp2PMXf3+agnrL/S+ZjnfZ9wvgXOx5hX9fmoMay/2vmY531fdL75zseY1/T5TnH1
1zof87zvC87H3yR9jHldn+9UV7/H+RjjfZ93vkOdjzH39vlOc/X7nI953vc551vofIz5oz7f
6a5+v/Mxz/s+63zcrtHHmNf3+c5w9QecjzHe9xnn43aTPsa8oc9H/WT9I87HGO/7tPPlKM8C
HgTe6HxNn+8dzse4swHGvMn5mOd9f+p8tfMxxv9m+PtgHOt/BvA3k+LzHOAtwFsB+ri98b53
Ol/mfIx5W5/vXFd/u/Mxz/v+yvk4H/Qx5h0Ap8E+0/cO4KMAfcw9D+A0vwL4vnjfu5zvSJT0
sf5u52P9fFf/svMxzvve53zczi0CHgLeA3Aa3EYuAuj7E4A+xl0AMOa9AH2L8Ol943TBx2nQ
xxg/DU6TPta/BDCuh88LgfcDfwzQN4ZP7/sQXfBxG0kfYz4AeN8LXP2DzscY71vhfJwP+hjj
52OR87G+HGB7zL0I4DQfA3xfvO/DzncwSvpY99w90/lY//8A5nJdLga4Hj3/uG69z/OA3KOP
MR8DmEvfxQDrnpOM8b5PwWbcsc7HmIfpgu84fDKO9T8H6Dsen/Sx/nGAvhPwSR/rfwHQdyI+
6WP9EwB9J+GTPtY/CXjfJa7+RedjjPf5/rHP9LH+CMBc1i8FWP9LgD7Ged+jzkeu0Me65xV9
jKXPc2gRbMYxxq9Lrm/6WPc84Pqlj/XHAE6X65G+xwC/3rgu6WP90wDjzsAnfaz7PtPHeWH9
MwDjTscnfax/FqDvNHzSx/rnAPq4faaP9c8D9J2CT/pY/wJA38n4pI91v5z5O+Iy4Pz73zR/
5/Sx7rcR5zgf655rs3APeHsz+NP3hq+9/mc3P+LwoZ0++x+Pn/rbp576yFOf/O1TT/7Hb/8X
r8/52uPXXTPyN+85529+cc6X3vPoDeed+6U3P/6NzR86Ylbnvj169130kD1Eitbt391LLhtb
cvkPx1i5y3r4EX7L99OpqzTC29tple08m3MdfNHeQt5GhE/v2VqeTHubIWm9Zdd+KZ3VZi9b
8KI9jx790tmLR0mOOZ0Nls3mF0/xwBNvJ/37K9tfyql3vGu4397sS3PnM7Dfz9s6fQxtgjFs
x9ust9PAJHAShN/5HPRkfJ+DzrG/zGWf+8Wj+657p7VPvWO3RxnHXNjD3kbMsI9B7ojP5bR8
m8x5Zp7mdNjuD77xxWH6aZ+3+562j9fNvu137CV3XW79jPH277a1Fqsd3xbtVcet20Hbwz6O
tp8m+/9s/v4Y3y5zvc3p+b8NvGHLzZZx1a780q31+mLu/K83jRF9LiyMdCHrvJ32ssd/ZYGD
WGO+zu8uncWNPQ9bEYt69Dka0ZzAX3t465lAttMZwz+wDHgH8BjwPYAjls2AISABxoATAE73
SmAZcBdwD/Ag8A7g/cBHgU8AjwFfAL4K/D3wPeBHwM+AXwIcfa8NrAdsBGwGbAlsC+wIDAF7
APsABwAJkAM1MAyMAQuBI4BjgBOAU4AzgHOARcBFwKXAEuBK4GrgeuBmYBlwG3AH8HLgLuCV
wKuB1wL3APcB9wMPAA8CbwLeArwNeAfwLuAh4L3A+4EPAH8CfBj4KPAx4GHg48AngE8BjwLL
gceATwOfAT4HfAH4EvAV4K+BrwJ/B3wd+Cbw98A/AN8B/gn4HvB94AfAD4EfAT8G/h34KfAz
4OfAE8B/A78E/hf4NfBbgEdEZgFrAbOBtYE5wDrAusB6wPrABsCGwEbAxgDe09jZFNgM2ByY
C2wBbAlsBWwNbANsC2wHbA/sAOwI7ATsDOwCDAG7ArsBuwN7AHsCewF7A/sA+wL7AfsDBwAH
Al3gICABUsAAGZADBVACFVADDTAPmA8MAyPAKMCjOmNADzgYOARYCBwKHAYcDhwBHAkcBRwN
HAMcCxwHHA+cAJwInAScDJwCnAqcBpwOnAGcCZwFnA2cA5wLnAecDywCLgAuBF4AXAQsBi4G
LgEuBV4IvAh4MbAEuAy4HLgCuBJ4CXAVsBS4GrgGuBa4DrgeuAG4EbgJuBm4BbgVeCmw7JDO
MqDzMpRA5zaUQOd2lEDnDpRA506UQOflKIHOK1ACnbtQAp27UQKdV6IEOq9CCXRejRLovAYl
0HktSqDzOpRA5x6UQOdelEDnPpRA549QAp37UQKd16MEOg+gBDpvQAl0HkQJdN6IEui8CSXQ
eTNKoPMWlEDnrSiBzttQAp23owQ670AJdN6JEui8CyXQeTdKoPMQSqDzHpRA570ogc77UAKd
96MEOn+MEuh8ACXQ+SBKoPMnKIHOh1ACnQ+jBDofQQl0PooS6PwpSqDzMZRA589QAvZP22dt
n9cCF2YDawNzgHWAdYH1gPWBDYANgY2AjYFNgE2BzYDNgbnAFsCWwFbA1sA2wLbAdsD2wA7A
jsBOwM7ALsAQsCuwG7A7sAewJ7AXsDewD7AvsB+wP3AAcCDQBQ4CEiAFDJABObCw9551F/Ye
2Hlh7zsLF/ZefuPC3gdWLOxduOWhva9ef2hvx58c2lv6ksN6G61zeG/XDx7e++9FR/S+ufeR
vbmdo3pzfnxUb/MfHt175xPH9Pbf+rjegUcf3zvo/hN6n/3PE3uvu+jkXv2TU3rXv/q03jaH
nNH78eZn9b715Nm9b/7qXOxnLPodzDvlnF7z4Gm9B8sTez/c+5jessWH967/14N7N394tPeX
H5nX+/WPyt7YaVlvvScO6u204oDe/Q/v2/vM3+7VG91yj94Xbti1d0Znl96m792xl79w+156
xLa91/W27v33yVv29rp1bu+Xyzfrnb3Vpr0Tl23c+9lvN+ydc88Gva9k6/du/9G6va99aJ3e
trfP6T1yydq99OzZvSfOWav3miWzeq+8u9ObfclTY3t+/Tdjnz3z12PD//O/Yz/94JNjx173
y7F2G6DPuJeAOC1Ox83Q8N6J0+J0OGvizhCnxem4GRreO3FanA5nTdwZ4rQ4HTdDw3snTovT
4ayJO0OcFqfjZmh478RpcTqcNXFniNPidNwMDe+dOC1Oh7Mm7gxxWpyOm6HhvROnxelw1sSd
IU6L03EzNLx34rQ4Hc6auDPEaXE6boaG906cFqfDWRN3hjgtTsfN0PDeidPidDhr4s4Qp8Xp
uBka3jtxWpwOZ03cGeK0OB03Q8N7J06L0+GsiTtDnBan42ZoeO/EaXE6nDVxZ4jT4nTcDA3v
nTgtToezJu4McVqcjpuh4b0Tp8XpcNbEnSFOi9NxMzS8d+K0OB3OmrgzxGlxOm6GhvdOnBan
w1kTd4Y4LU7HzdDw3onT4nQ4a+LOEKfF6bgZGt47cVqcDmdN3BnitDgdN0PDeydOi9PhrIk7
Q5wWp+NmaHjvxGlxOpw1cWeI0+J03AwN7504LU6HsybuDHFanI6boeG9E6fF6XDWxJ0hTovT
cTM0vHfitDgdzpq4M8RpcTpuhob3TpwWp8NZE3eGOC1Ox83Q8N6J0+J0OGvizhCnxem4GRre
O3FanA5nTdwZ4rQ4HTdDw3snTovT4ayJO0OcFqfjZmh478RpcTqcNXFniNPidNwMDe+dOC1O
h7Mm7gxxWpyOm6HhvROnxelw1sSdIU6L03EzNLx34rQ4Hc6auDPEaXE6boaG906cFqfDWRN3
hjgtTsfN0PDeidPidDhr4s4Qp8XpuBka3jtxWpwOZ03cGeK0OB03Q8N7J06L0+GsiTtDnBan
42ZoeO/EaXE6nDVxZ4jT4nTcDA3vnTgtToezJu4McVqcjpuh4b0Tp8XpcNbEnSFOi9NxMzS8
d+K0OB3OmrgzxGlxOm6GhvdOnBanw1kTd4Y4LU7HzdDw3onT4nQ4a+LOEKfF6bgZGt47cVqc
DmdN3BnitDgdN0PDeydOi9PhrIk7Q5wWp+NmaHjvxGlxOpw1cWeI0+J03AwN7504LU6Hsybu
DHFanI6boeG9E6fF6XDWxJ0hTovTcTM0vHfitDgdzpq4M8RpcTpuhob3TpwWp8NZE3eGOC1O
x83Q8N6J0+J0OGvizhCnxem4GRreO3FanA5nTdwZ4rQ4HTdDw3snTovT4ayJO0OcFqfjZmh4
78RpcTqcNXFniNPidNwMDe+dOC1Oh7Mm7gxxWpyOm6HhvROnxelw1sSdIU6L03EzNLx34rQ4
Hc6auDPEaXE6boaG906cFqfDWRN3hjgtTsfN0PDeidPidDhr4s4Qp8XpuBka3jtxWpwOZ03c
GeK0OB03Q8N7J06L0+GsiTtDnBan42ZoeO/EaXE6nDVxZ4jT4nTcDA3vnTgtToezJu4McVqc
jpuh4b0Tp8XpcNbEnSFOi9NxMzS8d+K0OB3OmrgzxGlxOm6GhvdOnBanw1kTd4Y4LU7HzdDw
3onT4nQ4a+LOEKfF6bgZGt47cVqcDmdN3BnitDgdN0PDeydOi9PhrIk7Q5wWp+NmaHjvxGlx
Opw1cWeI0+J03AwN7504LU6HsybuDHFanI6boeG9E6fF6XDWxJ0hTovTcTM0vHfitDgdzpq4
M8RpcTpuhob3TpwWp8NZE3eGOC1Ox83Q8N6J0+J0OGvizhCnxem4GRreO3FanA5nTdwZ4rQ4
HTdDw3snTovT4ayJO0OcFqfjZmh478RpcTqcNXFniNPidNwMDe+dOC1Oh7Mm7gxxWpyOm6Hh
vROnxelw1sSdIU6L03EzNLx34rQ4Hc6auDPEaXE6boaG906cFqfDWRN3hjgtTsfN0PDeidPi
dDhr4s4Qp8XpuBka3jtxWpwOZ03cGeK0OB03Q8N7J06L0+GsiTtDnBan42ZoeO/EaXE6nDVx
Z4jT4nTcDA3vnTgtToezJu4McVqcjpuh4b0Tp8XpcNbEnSFOi9NxMzS8d+K0OB3OmrgzxGlx
Om6GhvdOnBanw1kTd4Y4LU7HzdDw3onT4nQ4a+LOEKfF6bgZGt47cVqcDmdN3BnitDgdN0PD
eydOi9PhrIk7Q5wWp+NmaHjvxGlxOpw1cWeI0+J03AwN7504LU6HsybuDHFanI6boeG9E6fF
6XDWxJ0hTovTcTM0vHfitDgdzpq4M8RpcTpuhob3TpwWp8NZE3eGOC1Ox83Q8N6J0+J0OGvi
zhCnxem4GRreO3FanA5nTdwZ4rQ4HTdDw3snTovT4ayJO0OcFqfjZmh478RpcTqcNXFniNPi
dNwMDe+dOC1Oh7Mm7gxxWpyOm6HhvROnxelw1sSdIU6L03EzNLx34rQ4Hc6auDPEaXE6boaG
906cFqfDWRN3hjgtTsfN0PDeidPidDhr4s4Qp8XpuBka3jtxWpwOZ03cGeK0OB03Q8N7J06L
0+GsiTtDnBan42ZoeO/EaXE6nDVxZ4jT4nTcDA3vnTgtToezJu4McVqcjpuh4b0Tp8XpcNbE
nSFOi9NxMzS8d+K0OB3OmrgzxGlxOm6GhvdOnBanw1kTd4Y4LU7HzdDw3onT4nQ4a+LOEKfF
6bgZGt47cVqcDmdN3BnitDgdN0PDeydOi9PhrIk7Q5wWp+NmaHjvxGlxOpw1cWeI0+J03AwN
7504LU6HsybuDHFanI6boeG9E6fF6XDWxJ0hTovTcTM0vHfitDgdzpq4M8RpcTpuhob3TpwW
p8NZE3eGOC1Ox83Q8N6J0+J0OGvizhCnxem4GRreO3FanA5nTdwZ4rQ4HTdDw3snTovT4ayJ
O0OcFqfjZmh478RpcTqcNXFniNPidNwMDe+dOC1Oh7Mm7gxxWpyOm6HhvROnxelw1sSdIU6L
03EzNLx34rQ4Hc6auDPEaXE6boaG906cFqfDWRN3hjgtTsfN0PDeidPidDhr4s4Qp8XpuBka
3jtxWpwOZ03cGeK0OB03Q8N7J06L0+GsiTtDnBan42ZoeO/EaXE6nDVxZ4jT4nTcDA3vnTgt
ToezJu4McVqcjpuh4b0Tp8XpcNbEnSFOi9NxMzS8d+K0OB3OmrgzxGlxOm6GhvdOnBanw1kT
d4Y4LU7HzdDw3onT4nQ4a+LOEKfF6bgZGt47cVqcDmdN3BnitDgdN0PDeydOi9PhrIk7Q5wW
p+NmaHjvxGlxOpw1cWeI0+J03AwN7504LU6HsybuDHFanI6boeG9E6fF6XDWxJ0hTovTcTM0
vHfitDgdzpq4M8RpcTpuhob3TpwWp8NZE3eGOC1Ox83Q8N6J0+J0OGvizhCnxem4GRreO3Fa
nA5nTdwZ4rQ4HTdDw3snTovT4ayJO0OcFqfjZmh478RpcTqcNXFniNPidNwMDe+dOC1Oh7Mm
7gxxWpyOm6HhvROnxelw1sSdIU6L03EzNLx34rQ4Hc6auDPEaXE6boaG906cFqfDWRN3hjgt
TsfN0PDeidPidDhr4s4Qp8XpuBka3jtxWpwOZ03cGeK0OB03Q8N7J06L0+GsiTtDnBan42Zo
eO/EaXE6nDVxZ4jT4nTcDA3vnTgtToezJu4McVqcjpuh4b0Tp8XpcNbEnSFOi9NxMzS8d+K0
OB3OmrgzxGlxOm6GhvdOnBanw1kTd4Y4LU7HzdDw3onT4nQ4a+LOEKfF6bgZGt47cVqcDmdN
3BnitDgdN0PDeydOi9PhrIk7Q5wWp+NmaHjvxGlxOpw1cWeI0+J03AwN7504LU6HsybuDHFa
nI6boeG9E6fF6XDWxJ0hTovTcTM0vHfitDgdzpq4M8RpcTpuhob3TpwWp8NZE3eGOC1Ox83Q
8N6J0+J0OGvizhCnxem4GRreO3FanA5nTdwZ4rQ4HTdDw3snTovT4ayJO0OcFqfjZmh478Rp
cTqcNXFniNPidNwMDe+dOC1Oh7Mm7gxxWpyOm6HhvROnxelw1sSdIU6L03EzNLx34rQ4Hc6a
uDPEaXE6boaG906cFqfDWRN3hjgtTsfN0PDeidPidDhr4s4Qp8XpuBka3jtxWpwOZ03cGeK0
OB03Q8N7J06L0+GsiTtDnBan42boZHr31FPv+t76nZOvXvzCyxcv2XiDbGjjDRIgK/mZErW3
Dl583eJLrrn8kqWXLV5y0eKrhg696uILli6FA1EnHDJ0wknHDx150tCJp/ZOOQXmEQvhTpIk
yxsYp1x1zeKhK69avHTx5S9YfP7Vi5deDefCC66+5jKUaWIn8Syf/K4ftlPMcn5f7y1Zcsni
C6+64JoXXLr0kiW/vnTJBZdduXjjDaqUydcT/Ei6VcHi9/N9e4Zf28iGPafJr+jm0skBtlAC
FVADjLOTSW1nGJoyNmVwyuiU4SnjUyakzDBs2ti2mWGYYZhhmGGYYZhhmGGYkTEjY0Zmu8OM
jBkZMzJmZMzImJExI2dGzoycGbmdA2bkzMiZkTMjZ4ZdUwUzCmYUzCiYUTCjYEbBjIIZBTMK
TsNSpWRGyYySGSUzSmaUzCiZUTKjZEbFaVTMqJhRMaNihl03FTMqZlTMqJhhSVgzo2ZGzYya
GTWnUTOjZkbNjJoZDafRMKNhRsOMhhkNMxpmNMxomGHXtKchc9KESWnCrDRhWpowL02YmCbM
TBOmpgmnlrrVb3NTm9syoKVAy4GWBC0LWhpYHqSWCKllQmpsruVCasmQWjaklg6p5UNqCZFa
RqSWEqnlRGpJkWa2z5YWqeVFaomRWmaklhqp5UZqyZFadqSWHqnlR5rb+bUMSS1FUsuR1JIk
tSxJLU1Sy5PUEiW1TEktVVLLldSSJbVsSS1dUsuXtN22WMakljKp5UxqSZNa1qSWNqnlTWqJ
k1rmpJY6qeVOasmTWvaklj6p5U9qCZRaBqWWQqnlkNuSWRallkap5VFqiZRaJqWWSqnlUmrJ
lFo2pZZOqeVTagmVWkalllKp5VRqSZVaVqWWVqnllbEbNpOQG8byylheGcsrY3llLK+M5ZWx
vDKWV8byytjtirG8MpZXxvLKWF4ZyytjeWUsr0y7fWk3MG4LQ16ZdhvTbmTarUy7mWm3M+2G
xvLKWF4ZyytjeWUsr4zllbG8MpZXxvLKWF4ZyytjeWUsr4zllbG8MpZXxvLKWF4ZyytjeWUs
r4zllbG8MpZXxvLKWF4ZyytjeWUsr4zllbG8MpZXxvLKWF4ZyytjeWUsr4zllbG8MpZXxvLK
WF4ZyytjeWUsr4zllbG8MpZXxvLKWF4ZyytjN07G8spYXhnLK2N5ZSyvjOWVsbwyllfG8spY
XhnLK2N5ZSyvjOWVsbwyllfG8spYXhnLq8zyKrO8yiyvMsurzPIqs7zKLK8yy6vM8iqzvMos
rzLLq8zyKrO8yiyvMsurzPIqs7zKLK8yy6vM8iqzvMrs9iqzvMosrzLLq8zyKrO8yiyvslbB
WglrNcyJGLdXWStjrY61QtYqWStllleZ5VVmeZVZXmWWV5nlVWZ5lVleZZZXmeVVu/+RWV5l
lleZ5VVmeZVZXmWWV5nlVWZ5lVleZZZXFBL722U/AW4drbKhtJqD0mqADbQKYDfidjtsN6VW
OaxwWN2wssEM7QFgCXJZaQ8AC0F7AKt9D8B03d4USkh9mUD1s3bngF9VeVk22H0o2708uMqy
TlOIW161u0NwVU2DPa0C+0HtfhJcTVk12Bo3jc/DRjOvyhwqV7S7ZqaL7VbTFFmJfYt2jxGu
KsnqqiozbIvazUY3T6BHVdUkTbvrabp5VjdVgdQyafdD4aoa9KJAL5J299J0C4hxZaAvSdPu
OcGFOsQTexntnpPpllBX7EYV7IbdOMFVY38Cm/IkaTU9Nd0qzzDXSY05anf+TLdOmgqqjtyy
3beCq05y7KyibbebZLpNUWBpYmuM5u12LusmmN+qqrDH2kpWmnXB8gIaXWG/x+2XdrFjkxRJ
0VS1m8WsC8VqsO+JXQ+3v5lh0TRQxTxFL9rdsKxbYMcRCyKpIKN2G5thHpusyqoqwYzZZZph
huq8KZGYtPtU6ERdZU0N3UuavN2Vb/d4+SN8xkJmlRQlxBBTbNcseoH+Y4XVTdPugKCxpCpq
qH+FldHuf2IZYmZyLKAqdTvfWGklVk8CHSqadg/ddNMalMBSy7GvYSebdsE+rOsEs5+3o4u0
W4JcGHyAbkm7alNwAgsdc11g6diZTLvYaSwKzDhkv92dTbpNUyVY+GVVtEsCQ1+QA+soIYHa
cUwXVC/qssJ+stuVTbo5dp4w9gDp63ZUkOCngcljjxeLu92dT7pYG9g9rJu0bEdJTRcLHtPG
qi5BajsEwwTRcfS1gSLbWWy6ZZGUdY79g6Surbg3WI1Vid1CLBtEc0E03QyzjGVfVRBiuyvX
4IeX5FhpZDl4baMwzqiaGj/PIi/sj6rpgrNgDdYFvrHLpu42WL4Y62QZlo3dCay76ECNnTrS
ubB7MDVYwlWGSM4iF06NJZ9gnzXJKixau1dW40eFH36BnmBt2l2iuoslg31LNFZjuMLZhgs/
f6wK7G7g98FfWo2fP7oI4jc51kbbPDqA7Qh+C+Cg3SWpsRYbbA4sUUFgmwhSoY0GayypnAu/
zQRbrryosWnikqjxQ8N+S43NFH4udqex6qI/2CPDTwq0t/uacPHnhJXdYBtjd5Mr/I6xOcCK
ABHbLQdcmB9s5CrQAKxA83AlWNl2WTWIty5s3vDbwP4iVqTdReTejxDvMsCmXeIn8ZP4SfwG
IX525Cvxk/hNCdGX+Gnkh8GdxE/iNzXFj+MwDPOeY+THgeWkRn4cRWrkN01HsBI/iZ/ET4c9
ddhThz2nxGhtkIeRJX4SP4mfxG9A4jd1Dnu2p+l0ym+aDuomopHSPmmftE/aN+O0T9e7xHsd
ykSEaxAxEj+Jn8RP4ifxW/VRT53ym8YjQ4mfxE/iN6PFr73JYDB3Oqz5o54Tu96l1TDd6aDR
Xv+IUeIn8ZP4zWjxa++KG4z42UfKRHinw6Qv9mwTdZvftLwWRuIn8ZP4SfwGdNhT4qd73KfO
6FLiJ/GT+En8JH6rPuenkZ/O+enpZnq6mdVIPd3MPqZTTzebWk8302HP/nNdstvRqUZ+Gvlp
5KeR35Qd+a3mC150tadGfhr5aeSnkZ+ea63nWuu51lPnnN5zjXA18tPITyM/jfym7Mivfc/D
cz3aU7c6PJcQzMTvJX4SP4mfxG+ai5/O+c1EcXuueZb4SfwkfhI/iZ+u9pyW9/L9IQGU+En8
JH4SvwGJ35p/wosOe06fc3B/SKhWx3cSP4mfxG9Gix8PCepF7nqR+8wTUYmfxE/iN6PFb9KP
N8utahZVkeZFleSlMemaf8LLar7VYRU3uXOsidfbJsZkVVkY09RF+3qkqsyLUk94mToiKvGT
+En8JH4DOuwp8ZP4SfyasmqyJGmahPtOkNgsrXLsGpm8LDLurdGVp01TZGVaVwn3neiqkqyu
Kuw/PR2VJwaHJKomaZKsDcqzuqkKpJZJwr1P5OVVY6qmSDOTpM5VmKysjGHbpetDgbopEJOX
bnqlKSR+WIJZt66yps5SkzR5wjM37WK0y/KZj6yrJ7zoCS95klX11HrCyyBvddDIb3Wcf3s+
2oRwGDLDlmmNm1jTusgqpw2mqPKybNJKN7nrJnerkRI/iV9U4rfmD3tyijrs+XyI1aCnKfHT
yE8jPx32HNBhT13tqcOeOuypw54cTDdFgXF0luc4uGuPJWbdBId5q6pKTW0aO77OuqlJCwOv
SRDGUXjWNTj+WCRFU9XuyG7WzZKqSXFVQWbS3CXmSWOaPE/TsmnsoeSsW6Qlxu1FUpkmsSP6
rFuaJqsyDNlqk7qoKq/zpkRigsOc7RR12NPYZZ90y6Qs6rJK8SCrxh7xTbq5KbFGcLgdy00j
v6hGflwddVdPeBn0qGgmtKeRn0Z+Gvlp5Degkd+av+BlYuLH/Zqq2/8md+7zwcNdSezoNLrT
YeoM2Aaly9I+aZ+0T9o347SvlvjNuAe6rCyaEj+Jn8RP4ifx09PNZpwYSvwkfhI/iZ/ET+In
8dOdDrgsJMOZgCQxmbsHpMqzUnc6WI3UnQ663uUPXO+iiz11sefUOXeokZ9Gfhr5aeQ3oJHf
mhe/NX+bH/d+dJvfyufPpmJd4ifxk/hJ/AYkflPnYk9d8DJ1RmirS1glfhI/iZ/Eb5qL3yCf
bqYHvKwuMVrT7Ur8JH4SP4mfxE8XvOiCF13wogte7LNonnma9TOWnmutB7yY/A9c8KLDnrrg
ZeocTtXITyM/jfw08hvQyG/NX/Ay2Qe86Jzf1BGp1XU4VOIn8ZP4SfwGJH5rfuQ3sas9f//p
ZpMXP13tubrEaE23K/GT+En8JH5TVvwmNvIb5AUvEr81LVKra3oSP4mfxE/iJ/HTBS+64EUX
vOiCF13wojca4TVBVd5UeWKqNKuKigcO6y7eaT0lL3gZ5MhPtzqsrpHYmm5XIz+N/DTy08hv
QCM/XfCiqz2nzoU0Ej+Jn8RP4jcg8VvzF7xM7JzfIC940chvTY/QVtf0JH4SP4mfxG+ai98g
D3vqgpfVJUZrul2Jn8RP4ifxk/j9X/bOAzCKKv/jmwoklIQSFCk5VBSE4c28mXnzKJJ4gOgh
BCGAdMIdQlCKgNLEBPCkSLEjqORAA4bqHe081KAU/xpQCCgihxQBEVGaCorw/73ZjXKIGuMS
srvfVXazb6e+nZ3P+/7K+yHgBQEvCHhBwAsCXhDwElwBL/40e0L5FbdCu1z7g/KD8oPyg/KD
8oPyg/KD8oPyg/KD8iua8kO0J6I9Ee0pbSE5Y1IyZXEgfcl1YQrbNEzb4ipeSjWZupQWt3VH
MOlrEow7Qtic/7gUZRrZUgjJJOPehUzuSGHRqjZj7qTLhmYKaQhp6dxguq/JMrgtDENt2/Yd
g0XvDYuWMW3f/mzDgvKD8oPyg/KD8oPyg/KD8oPyg/IrmvIrqakOiPa8XH6zQN4ufH5QflB+
UH5Brvz8GfCCPL9ABt6Fxw74AX6AH+AX5PDzp/ID/C4ESCD/DfgBfoAf4Ocn+CHgBQEvCHhB
wIsK6ZGW5VicmyaF9biONK4xCvARQuiGY0g36oZruqFbBrUajBZTMT1cM3R6wywpHF9MD9c4
E1I3bYMbuulb0WTSkKap67aUbhAR1yzd5hT5w4QhmRru0rZsQ3LBhWDkzPQtJUzHlDatyAxv
qBHXHMGlw2m30mTw+cHnVzSfX0mFnz+VH/L8AlntXXjsUH5QflB+UH5+Un4lNeDFnz4/wO9C
gATy34Af4Af4AX4BCz9ly3A05khGceqm5egGVzKPmihdSjiOKchQIgG/QIbU5Tp2wA/wA/wA
Pz/Br6SaPf0JPwS8XC4YFfd2AT/AD/AD/PwEv1AwewJ+xQ2py7U/wA/wA/wAvyCHnz8DXgC/
ywWj4t4u4Af4AX6AH+CH6c0wvRmmN8P0Zkh1QKpD0VIdYPZEnh/y/JDnhzw/XdAs48LNNjQ0
molcmMzUha57kxlpNnKb5h1nXOUzct+c5bpDc51TdqRpCO5OUK5rUleTmDNKczSZurfqumbT
rOk6s0xKSfTOWa5rJtcdh7IbLcqCVHYpWspgjmVRgiNnluNui2lSCkZJlrawvBmPTBM06znl
YjI1M7qbY8k0m1GLLXRBx+JbzzRsyrykCdUpP1JFuutMM9TudckprdJyBwtMo6xLgw5D6rbu
zsEuNUqwpH1TSqdNs7Wr5ExJO6QDp2OV3PSeotRsi9mOyQ2bOQ5XpygpXVPYBmWHWoyWVgch
NU6nzCxbCE5Hpw5CaoZgJiVnqunbacJ2t0mnU5aOwR3LtNwUTqnRNO6UHUrfBX3i9o2jSepf
3aR4SOob2xscSQfgGNTTtrAtQ23e0YSpvjJaUp2i6hyHep4ZJq0oqGul+s4czaLONC06Evo2
9ZIKP5g9i9ukGAj7g9kTZk+YPQE/mD1h9oTZE2ZPmD1h9oTyK5ryQ6oDzJ4we8LsCbMnzJ4w
e5KB2jWOkr3bJAs0JxOp7bOXqln/GM3rJ00yQnutqmR35WS5tskkKyyv7ZXm26Pynu48fDQ/
n7stsqXTNiQZqpnwNf3+JHd1WILs0mQmJxO3pJKhti+M07GkReZnMr97C4EKUsUGnYcUZPwm
W7i7osPIxO1aiCUt7zZRtVKLCpHS9pijq1FAIFj+QvkYYfWE1RNWT1g9g9zqiRz3UIbcL507
4Af4AX6AX8jBD8Iv5IUp2Af2gX1gX5CzD7GevyR+Qrkd8AP8AD/AD/CDyy/klCDgB/gBfoBf
wMJPRZ/8dk0HKL9QVni/dO6AH+AH+AF+foIfEh0Q7Bk4Qa6AH+AH+AF+gB/MnjB7IsUdKe5I
cUeKe3CluPvT7KlSDSnzD2l+AQ9LKD8oPyg/KD8/KT/M7AmzJ8yemN8F87tgfpeQm9+lpPr8
/Kn8MMHLLwWQBFo7lB+UH5QflF+QKz9M8BJoYCqO4wX8AD/AD/AD/BDwEvA+vN8LTMAP8AP8
AL8ghx/Mnr8XDKGwPOAH+AF+gB/gB+UH5YdUB6Q6INUBqQ7BlepQZJ+fVzKiolFQghHKD8oP
yg/KL2CVX+GmNysy/LwrAn6An4reN2zb0XWDO6Yw1bBINVGZR51KUOqmNE1fE1IdkOqAVIeQ
S3UoqXl+gF8o+PB+7zlC+UH5QflB+QWs8vOWdv/9ddwd1PMLSjX3ewAI+AF+gB/gB/gh4CXk
YAj4AX6AX0jDT5kEHT/Br/hneCmczw+pDr9HEYXKsoAf4Af4hTT8FBgCF36FM3sWGX7eFRHw
EpSqEPAD/AA/wC9gld9lhh+iPWloFKxKEPAD/AA/wC/k4Id4l6BlWmFZDfaBfWAf2Ocn9pXU
TIciWz0h/CD8bJupy0ChEml+qhscJoVhKnDawtczjsNM3TBMW+qOugnQUtKyHItz07S47c6a
wjXGbV0IoRuOIdXgU+eabuiWQa0Go8W8TYZOb5glhcOYmznJNc6E1E3b4AalU3qXMpk0KLNS
p6OQyu9P27J0mwtpMWFIpn7x1GQblG3GhWA0c41vKWE6prRpRWYw37YcwaXDabfSZJjgBRO8
BMoEL4WLd/EyTDqUjWzST4ou+0JmOsDlRzeRwiqpQFsOyg/Kz0Uk4Ge4Aw+m0TjPAvwCBX5w
+QUvnC43TAE/wA/wg9kTZk+k+QWtwvsliAJ+gB/gB/j5CX7Fn+YH5Qfl90tw+612wA/wA/wA
v4CFH3x+gN9vQe6XPgf8AD/AD/DzE/wQ7ck5RaUxR1ca+JduumgvGX0D+AF+gB/g5yf4BY7Z
E2l+Ic9msA/sA/vAvpBjXyEzHbwpEpjcLChBCfgBfoAf4Af4IdgzKAH3axZmwA/wA/wAPz/B
r/hdfoh3KRnus1+DTEn9DPAD/AA/wC9g4Ve4TIciT/ACs2cQx+0AfoAf4Af4BTn8MLVnSVVf
V/K4AD/AD/ALafgpceOvan7Fb/aE8oPZs6gABfwAP8AvpOGnVBHgZyPgBQEvTKcyBMKd6Z8q
OFjCtKlIgUBRB9uheeA5M9U4mUYMKOogvWU+uEaVLKiSBHekpMtF9Q5VrhCWY1CeL9NN4ZaW
MDRBFSpMqnohdN1bucLQqEKF4TCuildw7u1W3dGlpFIYpiG4W8xC1+jqs6RkVNPCZG6tDF2z
bapvwSyT6k/Y7vehayanShpUysKikhdu5Qpdo4n7LYuqWXBmOe62mCalYFRRwxaWt7wF04S0
aRZrwC9gzZ6FC3gpstnTuyJSHYISjFB+UH5QfoBfwMKvcGbPIsMPAS80Ki2qWbGkrwf4AX6A
H+AH+MHsGbSQ+yUIA36AH+AH+AU5/LwCrgi1bKH8oPzg84PPz2Uk1YO3bK5bVDoePj9Tl9zm
wuvpZBqThkGuR6nbOlM+TKlJ+pD8RY5hO8L1o0tyMpKzkvyTkptet6bUbIvZjskNmg7Z4cqt
KTWL3OyGaZE/lJZWDkupcXJzUt8LwanSrjL2Sc0QzJQOF+Q6NQxl2ZOaTm5O6RjcsUyLKc+9
1MhPbRuc/K/0iesPdTRJPlXdZJyTP9RWKwZ7wAvMnr+kfkK5HcoPyg/KD8ovYJXfZQ54gfKj
oVGwAhLwA/wAP8DPT/ArqUUdYPYMVoD9kfMC/AA/wA/w8xP8ij/JvfiVnzI5C8p1Ihu3sC3D
kI7lLY8kbJNcAijnFzBKEfAD/AA/wA/wK3S0J+D3R9RWSVoX8AP8AD/AL2DhV/x5foBfSQLY
HzkWwA/wC0n4uaGQOqZ4Cfhwz+K3e6o9wu75R6hTUtYF/UC/kKSfuoUBfv7OdSipES/IdSgp
wClJxwH4AX6AH+yesHsW2ukH5VeSAPZHjgXwA/wAP8AvyOGHXIc/AolgXRfwA/wAP8AvYOEH
n1/wZqFfbugCfoAf4Af4BSz8ChfuCeV3uUESiNsH/AA/wA/w8xP8ij/gpXDKD/ALRDhd7mMG
/AA/wA/w8xP8in+KFyg/mD2LCknAD/AD/EIafkoV+ausQ/Erv6LCzzslmeSGbtpCl3ahgz2R
5F5U1pS09cA+sA/sC2n2hUJJoyJbPb35gVSWyhZSCsM2hINMh5IGsaIeD+AH+AF+gF+QWz2R
415UQATzeoAf4Af4AX5+gl9JtXr+HH5FtnpC+AULD8E+sA/sA/tCjn0O4BcwlYcuF2wBP8AP
8AP8ghx+RXb5eVeEyy8oQQn4AX6AH+DnJ/iFQqIDgj0vlxIr7u0CfoAf4Af4BTn8fu7yK7rZ
E/Arbkhdrv0BfoAf4Af4+Ql+gRPvAvghNR7wA/wAP8DPT/ArqWZPfyo/RHteLiVW3NsF/AA/
wA/wA/wKPcEL4FfckLpc+wP8AD/AD/ALWPgpFDkacyRjumNajm5wJfOoiXNLOI4pdFNKRHte
LoAE8nYBP8AP8AP8AhZ+hZvZ059mTwS8BDLwLjx2wA/wA/wAP8APZs+gzOW7EHYX/w34AX6A
H+AX5PDzp9kTyu9iiATqe8AP8AP8AL8gh58/zZ4IeAlU2F183IAf4Af4hTT8lCoKvWp+Rc/z
A/wuhkigvgf8AD/AL6Th5w2OdEzuGMKStrAtwxtFIkwpTGYInQtLeBFp28wwTcaFY1mSu9S0
hKWblmCmbRh68Se5I9oTyepFhS/gB/gBfiENP38qv8BJci9yUQe4/IrKmpK2HtgH9oF9Ic0+
fwq/kso+f8a7wOpZ0iBW1OMB/AA/wA/wC7l4Fwi/kEtsuJiRYB/YB/aBfSHHPoS7wFMI+AF+
gB/g5yf4FX+4izcy57cmN0Oiw8WqB+/ptmdohroy3FfdoVgu3bG4UDYBt0mYti11Qe3Kaq6a
bNvRafo8mjLPLFhRSKlzg0K+pGn6lqKYMckZk7JgPa4LU9imYdoWV0Zz2hQ3dSktbuuOYL4d
csG4I4RNs/IVLEXRZrYUQjLJVHAZrUdRaZKi0qRlM+bbnymkIaRFR8F0X5NlcFsYhtq27Tt2
i94bFi1j2r792YYF+FGncs0RXDpcN5g0mbqFebvR7cufnrgmBLNsrlt2wTfLNVM3dPrCHCkN
y12Ta0xYjuHogr4M4btI6AujwEFTF7rOfV+Hig50GLcYhQ36vlrdoUtCWpZpCO7uVtfo6qPv
mnFGqyuPkq5rNl1cOrPocmPer1ana0J3HCYMy9BN9/LSNYNRQKLggjPLcbfFNCkFE3R5UXii
uxDTBF0clgP4+Ql+JdXlB/gBdj9Xui7hvEwhegF+hmY7hs65oTPmnSCXekiYnJBPo0tO2PR2
lsOkMEwFTooM9zU5dG83iO6S7sPeJrqN01CCmyYhvoALBHu6/+qGY0iXwFwjeFgGtRqMFlMr
cs0gCikoCMfHd67R3V/qxAs6NNO3osmkQeMNnY5CujdzrlnEIRoFEAYkc7HDNduQRACiFp2Y
bylhOqa0aUVGsPPuEfAz3L5nGo3zLMcWuiAQ+6BpGjZ9IzToon5TUkNnNGQk9uqSU3d7kc80
+jYMYrDUbd0dp0mNOp7AS1+1TSM61dGSaEvUpgtEctPLd6nZFrMpz8CwmeNwdeVI+hqFbdBV
YzFaWh2E1DjxngYeQnA6OnUQUjMovYBGLGqIR4M6t0kn3kuHxqaWablfrdTomqWrhgYi9Ik7
MHA0SYMLnfIVOA0MbLWiv7L8Sir81FcrNOnQ6NiknxRd9jB7/hwGoQZIwA/Kz8Ut4Af4/fEs
v5IKPyi/UANbYc4X8AP8AD+YPYPc7AnlVxgYhNoygB/gB/gBfkEOPyi/UANbYc4X8AP8AD/A
D/BDQaOQy/sD/AA/wA/wC1j4qRCuy1jH3SsZKWiJAowpxM02KAzKDZ5xGEU3ubOgSsdSsUxC
o2B2ioTmFJXGKNKZmgqjPrDMlesnwA/wA/wAPz/BT93yHY3iYA2bprum6EpihreJMp0o5phT
PpTtmw9bBUEzCnOWJiWeKKecQ+GrlIikIp8p3cbyZvBRODJlPrlhyRSu7C5F+TO0DUnZTcyL
ot+Gnz/NnuoghAb4XTlo+WvAAPgBfoAf4Ocn+CHaE8ovcKAI+AF+gB/gF+TwQ7Snv9RSMG0H
8AP8AD/AL8jh50+zJ3x+wQJAwA/wA/wAP8AP0Z4hF6AD+AF+gB/gF+Tw+7nZ0xugKdVkgTSV
naTpg22fpKPgTYummaM5Zr2TAlNwC4I9g0XsXXgeYB/YB/aBfUHOPlg9L7zp429vTA7gB/gB
foCfn+BX/JkO3uQHVDQC0H5/kCngB/gBfoAf4AezJ1x+KOeHikZu8SW3mM9FTyjnh4pGhkml
kARVSvSlqlMuu25aVFuJijPqSPNDmt/vV2BXSrVC+UH5QflB+QW58vNjvAvmd7lSrPL3fsE+
sA/sA/v8xL7iF36Fm9nTn/EugJ+/IXSltgf4AX4hCT9v/XpGddVtKtsO+gUs/RDwEjhmxitF
uV/aL+gH+oUk/ZRk0AE/ZtlKFjkBC7/il36+bEAUdQj4ABnAD/AD/KD8AhZ+hVN+P/f5OUhy
D3h4/ZKiK2w74Af4AX6AX5DDz59OPyi/wsKlpC8H+AF+gB/gB/ghzy/klCDgB/gBfoAf4Af4
AX5IckeSO5LcHZrrmIqESzfJn2k0r7GhGyZ3TCS5h1aSu9deiomtgxKMUH5QflB+UH4Bq/wK
F+2JgJeS7n+7EscH+AF+gB/gF7DwK1y0JwJergRcSvo+AT/AD/AD/PwEv5Ja1QHKr6SD6Eoc
H+AH+AF+gJ+f4Ff885sVTvkBflcCLiV9n4Af4Af4AX5+gl/xK7/C+fxg9izpILoSxwf4AX6A
H+AXsPArnPID/K4EXEr6PgE/wA/wA/wAP+T5BWU6w68BGPAD/AA/wM9P8CupPj9/Kj+lNYXm
YGLrgIcl4Af4AX6AH+AH5RfwMPs1lXepzwA/wA/wA/z8BL+SGvBS5GhPr2TEDC9BCUbAD/AD
/AC/gIUfAl5QzPZSqq4wbYAf4Af4AX5+gl8o+PxQ0qgwYAmEZQA/wA/wA/z8BL/iN3tC+UH5
FRW0gB/gB/gBfgELv8IluRfZ5+ddET4/+PxiFCpt29F1g6q7CFN5g1WTkFLnhqWb0nRrwFCT
tIXkjEnJ1OVDC3FdmMI2DdO2uLpgVZOpS2lxW3cEk74mwbgjhM35j0uZzLClEJJJxr0LUWkZ
KSxa1WbMtz9TSDoKi46C6b4my+C2MAy1bdt3DBa9NyxaxrR9+7MNC/AD/AC/gIUflB+UH5Qf
4Bejc83SbU6jACYMydyxCddsQ3LBhWBUqNAddnBNUF06aZu6zgzvsINrjuDS4Tq9N5kyXnnH
EO5A4qcnWlMwy+a6ZRcMa7hm6gbtlAYk0rDcNbnGhOUYji5oJCJ8IyQarQiTmbrQde4bi5g2
jU0Yt5gluW9co1MNPRrVWKYhuLtbXZO6Gugwzmh15VLSdc2mkZXOLBprMe+4RtdMrjsOnbVl
6KZ7krpmMMey6MQ5sxx3W0yTUjBBYytheXuCaYJGRpYD+IUc/NToV2iS0/VCtRslja9tdd1Q
Ap9jSctRl7P0jpqpieo50gBfUFVHKvLoXQppfgEvBpVuK9Bvlu7YNmrZopYt2IdatjEOjZDU
cMUQOheWUOMVh0YdLLRq2arTBvyoE4oqrkryeoAfrJ6wekL4hZzwcwqn/JQwAPwAP+oBhUq4
/FQ3OIyMIKYCp+0OilWTQ0Y9g3yakgxw3s4i+51jcW6a5NgsMAiSi5MMb7rhGNL1O3KNrIaW
Qa0Go8XUilwzyPyorIHC8Xk1uUZmP0kWGkPZaXwrmkwa5GXV6Sikz54JqyesntIhj7xlWq5B
W2rk4KarhizQlpCuRdjRJFmVdZNxThZhW93fHT/Br/gzHdR172jMkYxsVqblUDSC94To7Czh
UGQC/VykV8BJh2ICTPpJkbEf8AtONfd7lCaUH5QflB+UX8DCr6jxLoUTfpeweqodkhaEyy/g
LaFgH9gH9oF9Ice+Qgq/S8AP8S6/R1yV5GUBP8AP8AP8ghx+RbZ6An6kc0sywP7IsQF+gB/g
B/gBfsh0CFrI/RIgAT/AD/AD/PwEPxXU5WiUfmnYFiVnOjplx3mbaIYLSrjkNA+GLVVKp0Mz
XFBIDgV6SZNyLpXCcmiyDJqAQsV+Uaap5XXmUdopzXjhpqNSmqq7FKWO0jYkzWrBhK8J8S6/
dINH+y8rV8AP8AP8AD8/wa/4gz2LGu8Cn98vQyFUgAn4AX6AH+DnJ/iVVOXnzdYrQqbDJXx+
iPYMFjgCfoAf4Af4+Ql+JVX5IeAlWIDlz/MA/AA/wA/wC3L4+VP5IdXBnwC6ktsC/AA/wA/w
8xP8QsHsCfhdSWD5c9+AH+AH+AF+QQ4/mD39CY1g2RbgB/gBfoBfkMPPn2ZPBLwAfihli3mt
XWyimp87ZTnTaJZxg4oKSt3W3arLkorFUVlDk6Ywt6k+s0p4k1Q+kMoQ0sTnkpvegoVSsy1m
OyY3bOZQFTl3KUsXtkGzoVuMllalCKXGqYAhzUItBLccW92AJaXFMZNKMKqCzVSi2W3SqYAh
5rV2p7q+cF5rwC9YgOXP84Dyg/KD8oPyC1jld5mLOlwi1QE+P38C6EpuC/AD/AA/wM9P8Cv+
VIfCwc+fyg/wu5LA8ue+AT/AD/AD/AIWfpjhBTO1FBWIgB/gB/gBfoAfJrbGxNZUDtnirnPe
5aKgKtCSvO82U9Zv1YRC7ijkrltUOt57RXANAS8IeLEo9MY2DL34zZ6FU35IdSiqOgrm9aD8
oPyg/KD8oPyg/KD8oPwcQ+fcoLhygys/OQ0PqBoL6V0qm8JpfOttcqjSClIdXGxC+UH5QfnF
CE3YpmVzTkWbmKOrayKYVVMwnBuUH5QflB+Un5+Un7rlB1U9P6Q6BDHEAT/AD/AD/PwEv5Lq
80OqQzAoNX+fA+AH+AF+gB/gB59fyJlpAT/AD/AD/IIcfoj29LdqCobtAX6AH+AH+AU5/GD2
DAZY+fscAD/AD/AD/AA/mD1h9kSqA1Id3NB9VUtAv+iJa0JQZQGOJHfNsExp6pLbVLgBqQ5X
LtUBc3sipaKoihDKD8oPyg/Kz0/KD6kOyPMLHBgDfoAf4Af4+Ql+xZ/qUDjlh4CXoqqjYF4P
8AP8AD/AL2DhV/xze6o9Cs1hVLlY2JZhSMdSdYoxw0vA+QwBP8AP8AP8ghx+/oz2BPyCRQ0C
foAf4Af4AX6I9gw45fZHIQz4AX6AH+DnJ/gh4AUBLwh4kbagGgisoOqboXFdmDTtuWHaFldO
aqIup1BxaXFbdwRTVnPVJBh3hKC50X9cymSGLYWQTDLuXcjkjhQWrWoz5sbiG5oppCGkpXOD
ecPzDc0yuC0MQ23b9pVisOi9YdEypu3bn21YgB/gF9LwUz8Ox0/wK/6Al8L5/Pxp9lR3L/j8
/qjqKgnrQ/kBfoBfSMNPgQHwowG27cMaBbBYDg2w6eEOm4l0pkGDeSpiZhvCgc+vJIDLH8cA
+AF+gB/gB+VXaPhB+fkDPCVhG4Af4Af4AX5BDj9/5vlB+ZUEcPnjGAA/wA/wA/wCFn5Khzka
cySjiRlNy9EN7rXjMoobEI5jCt0k86Xrp5MOBQWYDmPMoBW8TdygyutCl79g9vQ6C2H2DMpI
UMAP8AP8AL+AhV/hAl6KDD/vioAf4KfiMQ3bdnQaXtGQylTDItVEvmAaUlk0xDJ90ZcGoj1V
z0jLcizOTZNiWt3Zj7nGKLpVCKEbjiHdkFOu6YZuGdRqMFpMdSnXDJ3eMEsKGqa6Xco1zoSk
Qaqhhqq+FU0mDepyXbfpC/CuaOk007K0mDAkc78ertmG5ILTjNQ0Y7dvKWE6prRpRRoC+7bl
CC4dTruVJnMP9aI5rX1HgYmt1d1WZ5jY2pIq+NrRLEE//IKJrYs/1eEyK79LwE/tEdGe/jA7
XultQPlB+UH5QfkFufLzWi+LYPa8BPzg87vS0PLX/gE/wA/wA/yCHH5ehvkHflB+/oLPld4O
4Af4AX6AX5DD7+fKr3DxLhB+ZOO90oy6XPsH+8A+sA/s8xP7it/lV7h4l5+zr5DBnpeAH4Tf
5YJRcW8X8AP8AD/Az0/ww+xmmNozcJQi4Af4AX6AH+BX6AleEO9S3Artcu0P8AP8AD/AL8jh
h3iXywWQQN4u4Af4AX6AH+BXaOUHn18gA+/CYwf8AD/AD/ALcvgVOeDFu+L/TPAC+F0IkED+
G/AD/AA/wC/k4FfkTAewL5B5d+Gxg31gH9gH9oUc+5DpEDhBmRcCy59/A36AH+AH+AF+cPkF
bS77LwET8AP8AD/AD/AD/AA/qollUVUANXE9VWuwhGnbUhe2zVSwsGpCTQfVDQ6TwjAVOG3h
6xnHYaZuGCb1l6NyfWkp1HQwhYoYoK4QVKDCpA4Suu4tXGFoVKDCcBhXtSu4qg9AS+mOLiX1
mmkI7laR0DW6+iwpGZW0MJnbrbpm21TegllUQoTZbufrmsmp06mShUUVL5RTRtc1qthmWVTM
gjPLcbfFNCkFo4IaNpUhcBdimpC2TXU3mCmk4W6KaXSpWw4VeBN0LL71TMOmKhsmFTKhyAe1
ddR0sC5Z0yEUctyR5vdLSirQ2umGY/huT1SRyCHIAX6GzqlqENW7dItiqhu3yQn5VP2SM7OA
dICfdzjENSI+VVHijpQ0VlJkoKpNwnIMRxdMB/wIl45hO8IdUEqiLVGbQC256eW71GyL2Y7J
DZs5Dlf4kJpF402DymBZjJZWBJYaJ94zyxaCE5rVDVhSJTFmUhUqQWMIw/0VS00n3kuH6o1Z
puXWqpIaXbNUBou+C/rEHRg4mqTBhW5SsVcaGNjq5+8EufJTv1qhYVpr+PkuBDTgB7OnyytU
84PyM0hjkyHDMhRbHRrzKbFOmOTCcs0bDmluZphETUGi+lLV/EJB+SHa80KABPLfgB/gB/jB
7Bnkys+brXeh8kOmQ8i5+C7mNNgH9oF9YF+Qs6/IVk8vNP8nxR0uv4shEqjvAT/AD/AD/AIW
fsoG6WjkjmcUrGBaju511FMT55ZwHJN8mxRBBZcf9UCgQupyHTfgB/gBfoCfn+CHan4oaBQ4
kAX8AD/AD/DzE/yKP94Fyi9wYHO5FFxRtwv4AX6AH+AX5PArss/Pu+L/+PwQ7FlU2JS09QA/
wA/wA/yCHH7+9Pkh4KWkQayoxwP4AX6AH+AH+BV6djPAr6iwKWnrAX6AX0jCz539hGYpw/Rm
mOHFpLnspF1o+sHuWdIoVtTjAf1Av5Ckn7qFAX6hMr2ZP+2egF9RYVPS1gP8AD/AD3bPgLV7
emdi+61EvyJHvFwiyx3wK2kQK+rxAH6AH+AH+AU5/KD8igqIYF4P8AP8AD/AD/CDzy/kpoAB
/AA/wA/wA/wAP8AP9fwc1PNTwSBuHdeLnrgmBFWA47plU31Z5Uih4n2o5+dWMWQak4ZBNXWl
butMFeeVmqRiQKjnp2bfpCrGJtUV5pZOxZ5V5zgaN6nkoGXY0qTSwupacqhAocWpHrFNtQaF
5fXmGVQ4ky44Rq/M8TZRkUjahqTyw0z4mi6bzw9Z7vTFBKvpE8oPyg/KD8oPyg/KL2gh90vw
BvwAP8AP8Aty+BU52hPKD8qPKjiry0Ch0rYdnQqHULEQU8VQqSYhpU7mCioeYrp2MmqiitCS
M1ZgHDM0TnYPYZuGaVvczbGiJlOnaiPc1h3hzTmmJsG4I8jOwX9cimpJUwKqkGT2UOYS2p/J
HUk1p6VlM+bbn0k2ECEtOgrmtdcZmmVwWxiG2rbtO3aL3htkWGFkevFuyjYswA/wA/z8BL+S
WtYB8Psl9RPK7VB+gB/gB/j5CX7FX9ahcHl+P091QCX3kLNyXsx5sA/sA/vAvoBlnzIiXcZi
tshxp/69GBrB8h7wA/wAP8AvYOFXOOFXZKsn4Af4weVnOxRNzclZ6PUVOhSAbZgKnLYoaHIY
Bf2TT1PqjrL+0LhCWpZjcRXSTe5H1cQ1Ri5OIYRuOIZ0/Y5c0w1dRXcLg9Fi3qUMnd4wSwrH
59XkGmdCUpi4wQ1yrXqXMim2nrysFCdOPldvk6XbnHyfTBiSuR5ZrtkGBdxzSlGgFA7fUsJ0
TGnTiiqA3LuiI7h0OO1WUpS5arooycF9i0wHyltQncM0wyIHty45dbeFTAdL0C/DMPSS6vL7
udXTgdkzaBVdYZUplB+UnwtlwM9wBx5Mo9Auy6F5/oWjSxf5TDMNm4YjFGdFgwbAz2RcOJbl
y9azBAW6FcAvcFx+RYefugCE5jDK6RS2ZRjSsbwgpXA+SoHlNEJljjsMKOxNGMtdGdMq4Af4
AX4wewas2fMy+/zUgIhIR6MfimgXNAaiIRHgRz0QDMAG/AA/wA/w8xP8it/sWTj4eRkmHUqF
MsmTQNb+ois/wC8YwKfOAfAD/AA/wC9g4Ve4gBf4/IIFWP48D8AP8AP8AD8/wS8UfH5Qfv4E
0JXcFuAH+AF+gJ+f4Ff8Zk8ov+Dwv10JCAJ+gB/gB/gFLPwus88PeX5BEtxyKbgCfoAf4Af4
+Ql+MHsi1SFwlCjgB/gBfoBfwMKvcMqvyAEvUH5QfpjhBTO8uIxELVskuYd4kjsCXi5lQgzE
Nig/KD8oPyg/KL9L17KF8oPyg/KD8oPyw/RmdB8wzF9RfqEQ7YnpzQJR5V3qmKH8oPyg/KD8
Alb5FS7VATO8XOrmH+ptgB/gB/gBfkEOvyIHvGBuT5g9YfaE2RNmT5g9f8vsWVJTHaD8Ql3l
Xer8ofyg/KD8oPyCXPkBfpe6+Yd6G+AH+AF+gJ+f4FdSA16KDD9Ee8LsCbMnzJ4we8LsGahm
T/j8Ql3lXer8ofyg/KD8oPz8pPzg88P0ZpjeTFLlY86YlExZHAixXBemsE3DtC2u5khQTaYu
pcVt3RFM+poE444QNuc/LmUyw5ZCSCYZ9y5kckcKi1a1GTN9TUIaQlpUq5LpvibL4LYwDLVt
23cMFr03LFrGtH37sw0L8AP8AL8ghx+U36WUT6i3QfkBfoAf4Bfk8IPPL9RBd6nzB/wAP8AP
8PMT/EpqwAuU36Vu/qHeBvgBfoAf4Ocn+MHnB58ffH7w+SmvprQsx+LcNMmzqQbFOtcY+TiF
ELrhGNJ1PHJNN3TLoFaD0WLepQyd3jBLCsfn1uQaZ0Lqpm1wQzd9K5pMGtI0dd2W0vWjcs3S
bU7OTyYMydRwl/ZoG5ILTuUYHEP3LSVMx5Q2rcgMr7eVa47g0uG0W2ky91Bd1+lFT1xDVQdU
dfiVuT1LKvz8qfwwt2ewKEYoPyg/KD8ov4BVfmo452jMkYzpjmk5usEV6aiJguaE45iCxoqy
yD4/74qOaVAAnxSGbQgH8AP8TGG60sLQKM5SUpylRVeZ6Qu1NKD8oPx0QaG3wneRUHiuMJmp
C133yltDIxlrOIwrhct9gby6QwHApJdNQ3D3UtI1qavIXkbC12RKWOi6ZtOdSGcWXW7MG8ir
aybXHYf0rkW62JW3umYwx7JI8nJmOe62mEb3L0ay2xaWVwMzTVAoMKlzZlK4sKu6mWYzarGF
LuhYfOvRvY+0OEUZk2KG8vsV5VdSfX7+hJ+6vITmMMPgwrYMQzqWssQIjYLZLYpTJ/MMc3TV
E8ECiWA9Dyg/KD8oP8AvyJWfP82egF+wwBDwA/wAP8AP8Lt0MdtLmD0BP8APZk/DVOC0hWsu
MzQyu5m6QVn8kixwyj6HgBeYPQWZXCm2yaaZG5RtTJKdley1dIFIbnotu1KzLWY7JjfIWuZw
deVIilsStkFhUhajpZXtVWqcLL3MsoXgZJRVtldJ/gZmUpSSmsqBJm9wm3Sy9ErH4I5lWm4s
k9RoSgcKkyITNH3imoQdTZJZWSfrJSeTsK1WdAIWfqonftvnB+UXLMDy53lA+UH5QflB+QU5
/Pzp80PAiz8BdCW3BfgBfoAf4Af4wewZcgE6gB/gB/gBfn6CX+BEe3oDNKXKmqXIXknTB9s+
Zx4Fb1pkfqaoY++kwBTZeWGmA1x+V1Ks+XPfYB/YB/aBfX5iX0nNcfen1RPw8yeAruS2AD/A
D/AD/AIWfgpFiHdBSmFRIAr4AX6AH+AXsPBDsCfAVxTwqXUAP8AP8AP8ghx+MHsWFRDBvB7g
B/gBfoBfwMIPZk8ov6ICGvAD/AA/wC9g4XeZzZ7e5HhEewZlFgTgB/gBfoBfwMKvcMoPZs+i
qqNgXg/wA/wAP8DPT/ALnDQ/B3l+Qanmfg+sAT/AD/AD/PwEv5Ka54epPX8PFEJlWcAP8AP8
AD/Ar9AzvGBqz2CBI+AH+AF+gF/Awq9wPj8ov2ABlj/PA/AD/AA/wA/wK7TyU7hFIXd/QuhK
bQvwA/xCEn5urTudUXk927Yc0A/0A/1CLgIG9AP9QpJ+agAP+IVKMVvkOlwpeVWS9wv4AX6A
H5RfwCq/oma5I9Uh5ITexRwG+8A+sC+k2adEkRNy7Ct6nh+iPS+GSKC+B/wAP8AvpOGnIiGD
HX7+tHoCfoEKu4uPG/AD/AA/wC/IlZ8/4Ydoz4shEqjvAT/AD/AD/IIcfsjzC1RAXc7jBvwA
P8AP8AP8kOkQcgEwgB/gB/iFNPwQ8GILXdqFhh98fpdTjRXntgE/wA/wC2n4hWbACzIdQk7o
XcxVsA/sA/vAvpCzeoJ9YJ+hGWrg5zJQd2yb6Y7Fhboy3CZh2rbUBbUr24hqsm1H1w3umMIs
WFFIqXPD0k1pmr6lpC0kZ0zKgvW4Lkxhm4ZpW9ydWsPQuKlLaXFbd4R3qilqEow7Qtic/7iU
yQwySAjJJOPejZvckcKiVW3GfPszhTSEtOgomO5rsgxuC8NQ27Z9x27Re8OiZUzbd4K2YYF9
YB/Y5yf2ldRqfgh3uVj04L2PcAWkA/yI7rZj6JwbOmMG99FdmJyQzxzCuenjqMOkMEwFTlsU
NDnM1A2iu9QdVdWMtiUtmjSSc9MkxKv7gs41RrAXQuiGY0iXwFzTDd0yqNVgtJh3KUOnN8yS
wvHxnWucCambtkGHZvpWNJk0aLyh01FId0DBNUu3aehiMWFI5h4912xDcsGFYHRivqWE6ZjS
phWZ4R12cM0RXDqcditN5h6qO4a46IlrtBnL5rpFe/QOa7hGJ007pQGJNKyCkxSWYzi6oJGI
KOhDOhmTOkjouvckDY1OxnAYV+fJfeMa3aHxEPWaaQju7lvXaOhFAx1Gp28yt1t1zaaRlc4s
Gmsx77hG10xOnU5nbVHvuCepawZzLItOnObvctxtMU1KwajzbWF5ewITe9K3qb6gYM/yU+co
NOnQ6NiknxRd9khxLwflB+VH6LCUAPXdfwE/wM9yKAJCEIh90DQNm4YjZHGgQYOKdqAZQQ3F
Xl3SZSO8yGcaDUUMYrDUbd01UkiNRh0EXhrn2GTOUCMWSdNoE7UJ1JKbXr5LzbaY7ZjcsJnj
cMV3SWMYYRs0ZLIYLa0OQmqceE+oEoLT0amDkJohmEkjFmXfIIuG26QT76VDhhnLtNxxjdRo
wEZDJhqI0CfuwMDRJA0udJNxHioTewJ+UHo/h71r26SfjfsK5QflB+VHFn7AT4lBYSqxTphU
fFcmCYc0NzNMoqYgUS3VaNHRLJLRpkUYJh2vF38ddyXzHY2EHCOHjWk55JHxSllCuyUc8s6Q
oUSqoy+S8vNSkwYwZGwgW49t0JDI3ZbDaKQjbMswpGOpcY3QyKtDVhFO5hlGVg9qAnBKdh8A
fvD5ueZYmD0N1+TMNMDPUMIS8CMDvGtVp9J9gF8wghzwA/wAPwS8+CngpfiVn5fTv6X8imz2
hPILYgUL+AF+gB/gF3Lw81oqpQof+30Z7rB6BosIBPvAPrAP7As59hU92BPwA/yQ5odMBxeb
yHRw8zsQ7HlF4l0us9XTGygDl19Qxu5A+UH5QflB+UH5FXpiTyg/KD8oPyg/KD+k+V3hTAco
v5KdTVCSQQnlB+UH5Qfl5yflpwzAjkbZ/4ZNUKQJVSg7zttEkxvSXDucUgJtX36gmveI0cxG
0qTpdrxZhIaguQfVZEc0yZDlxRrNOESTHbozEdEMRe62aNYg2oakCQ2Z8DVdtmBPmD0R7Imp
PTG7mctIzG6mbsCY4KXE5LgXTvl5Geaf2c1g9izJau73HBuUH5QflB+Un5+UX9Cl+UH5QflB
+UH5Qflhas+SN7sZlB98fr9H7V24LJQflB+UH5RfkCu/Ips9LzHBi8ItTXiGqT0DPv0B8AP8
AD/AL8jhV+TZzWD2hNkTZk+YPWH2hNmz5Jk9VfjJZSzqAPgBfoAf4Af4AX4lD36F8/lB+V3o
68LfXj8pzJ4we8LsCbNnwJo9C6f8/Ak/+PyCBZ6AH+AH+AF+RYGfKjAfILVsAb9gAZY/zwPw
A/xCEn5MzTxCyeqC6pVaDuhXFPqViEruhbN7FjncE04/OP3g9IPTz4UkpnhRd1tM8RJgU7z4
U/phihd/yq8ruS1IP0i/kJR+6hYG5ceZZSswOEGu/IoMP++KqGkU8El9l4Is4Af4AX4wewJ+
qGkUlIC7FPQK2gA/wA/wA/yCHH7w+RXc8PH603xwgB/gB/gBfkEOvyKbPRHwgoAXBLwg4MVl
JAJeEPBiMi4CLOAFyg+K7yfFV9AXUH5QflB+UH5QfvD5wefHdMfibv1ll4vCtG2pCyg/KD8o
P8xvFqjzm0H5FagdvP6kAKH8oPyg/KD8/KT8hJs2YUrTsC1hUel02x1HO5qpC5MLzi3dtKU3
O56bpsUsw5ampeuKTo5mCIsb1KSbTFje9HWDkSTjOqNX5nibdFPQNqSQBhO+JuZIRsN203J0
g3tzNxjtTDiOKXRTSvj8AL2foFfQF4Af4Af4AX5+gl/glHJXM/wITXKDaCx0acPqCasnrJ6O
oXP6STDmHULS6IDGrDasnrB6wupZ8qyel3lia+S4I9gTLj/AD/AD/H4LfiXV6llklx/gB/gB
foAf4Af4BSr84PIrcHPh9SfXH1x+cPnB5QeXX5C7/Iqs/Lwr/s/UniroRmgOMwwubMswpGN5
/YfCNi2bc/IhMkdXGhigKdl9APgBfoAf4Bew8LvMPr9LwA9FHYIF6oAf4Af4AX5+gl/x+/wK
Bz9/Kj/AD/Azhaks6YqeQkqd0nMon8ZU1Z1Vk6T8Hs6YlExdd9TCKc+H7AKGaVtcXT6qydQp
AYfbuiO8pUWpSTDuCMrr4T8uZTLKBBJCUpqPSg+i9UzuSMohkpbNmG9/JuX8CGnRUTDd12QZ
3BaGobZt+47BovcGJRIxSjXybso2LMCPOpVrjuDS4TplU1GKleoctxsveuIaZjfD7Ga/MrtZ
8cPPm/mHNL9gAVJxnocClZXooUfGG+HqxZPRTD2fv/hx7rz67A31r+wFn6tl1SOM/l24inc7
GW+cd9dzF/nZU2nfOgUf1Kyr/lL79/5T21T/vO8vfHUbf+WprYf2W6q9Z5jnb57+noH0fI9q
Uf8qDPP0ppae9K+35176pKeHeSyP8EiP7rHVEjEFS1zUXrAF9RqR7OG0Hv1VcShtI422cqm1
NNrvX+kTWq78nz3JnuYX7U3zpHsGe+5Wn1dK8dznGURLD/cMoDX0X15SLX3xvyrJtKd7aEvq
WO6jMxvu6ePp5xlKLfd4fjjfj57V2Q6mz2ntqIJ3Qwu2EzHCM8KTqN6F+15L3U9r3Ee9N4i2
5S5XwfQYtIzwmPSs09mzC16tgi2VlNeIodSLP37rfjuqMHdLFTwRl7j6wi7RdmFTwedVL2yk
vz9Tv7isZT0qJf3vB267x8P+7ms/ppa7oo/6tPeKv+MIZtKyyfRvBv2LctdLSprgvnrvJPTL
fmMYvb/EFf2rbe4mfE9q3d96xP3WAr/weVS0+qDge+t4wVK3u3//dK8quGepZu2C5dw/a1zc
QO/D6OHtkh8/LOz3e3mWq/zjcZw/fziivOfW+wYNH5zS+77e9/5t2N/uu4q+wot7Wt2/Cx4/
nUopwkiCr/nCJQqW/N9XL3P+t+2nd9XdPy/dy+qjuAz13fzacbkbKHi66Ee7Ka/1zZvy8poW
fHzxe/pRJnk8ifSvKA911N5H1YHnd5zf44m7veVtLd3v/aawm+ioP/b82RMRrh7qOYIekdGR
6lE6OjoqukzpmJgypcuUiSlboWxMbPnYMmXKxZcrXyEuLj4upmzFShXjKtHfcWojYWrNiMjS
tGJcbJlYav2dj/O5nvjSEZ/Rf2HxnvD4sIj4sPPrPNXdQ1WXacH17wkLj4iMii5Vhj79S1wY
vY2k/UaXio4oFUHff1h4fETkn/SoisntonsPqZT52D8q1zZeWbulFL/lz3em7b32vsffPHZ8
3Nx/VrnOtFq03/rXJ/aVbt5n6HjaWMKFO/H2WVg4tV8V/z+7V5/Eh/1JP7/TUzYijI40It7T
zHPe0yHXuw6e0QPoAfQAegA9gB5AD6AHfk8PhNVJq33Szhi6kD8z/2ifvRufMSMqzXnn1q8G
HW793p4yp76o+Vi38543Y0+9c/c91XtOGNvrwYbnPdnrz3ueORlxeMiHEQlNt5zJPLXL2f1o
q/OeCRXm/+3VDzuM2tJshnV13qLDpyZf+8E95Z/8sMWoLR1SD4vojN9zYIVaNlrXBx+bN7vi
q/2nnbRLza406cDhrRNz/n1iyq15NUedzm7aM23yjdOb/rX6TZsODvi+89ffZ38yWN7x+ezt
4oWTCxokHklq3G514zvLzyiTeKhj7v4UmTow94CZ/9rcH9bmDHnls++v2vHYgU326YgV1W8V
bb5u3/Pbl89m7pzWoNZr726vOWzT2s/e2nd167aftOBndz6451Tz9e1G9a3TOPfGQh14IReK
2DRz39X3rNnEOzUd8r155OZzucf2Ha++WXuya8ycBnfvq2DmbW+yvfX2pgcHJdIWl49f7Dma
1Lj9+zVqh11X/fNS1TLfyRo646+epOsqPjvrhlmTc7JH59szHqDDzmv6ysj9K4Y89HmFFtXT
+ny9uuZ3Nxybk1fzuZuvf2Lpbes+nXNwyphvSs2d9dkSuWBJvWnH/ffVhb2rP7v2nb3fdxvT
KnvOc+/1K7Uh73i3MdsPv/V6+Vr95iy++V/5u659OD7+xZjD14RneDzhW8svj1jh+SpJeB4v
PzxiatKBFPneTINkd0aGJ/LBuw5mn3pvxNbkTyo0nv3WxzX7Nk5d+nWpudMaTqqWtqf9zcM2
vX5nhZa1Kr/T6ZucheUfmtUscdTg44NfSTvd+ckPa70ronOpy/7wY8TpRyqufTv/3WY9ExZ8
t7z52UPLo8aOrqVPnbX+m48mn8k5XKPutC0RDbYsW32k1ZLHlqmLo36E+y1tLZd73fjne+1P
cbaVbZP7tiejVWKiOpoI+4Pj1Tam3P/W5r7HXt+Q9u9p29uK3RXa1Lpqw/QP9rbr9DwfpL6n
Bk8uvf3gInmu39nMz9/a8Ob6KXvT2nd7qP6ua9Qm/tBjzJLrN/TPffbdTw/WW78z59vJzWTF
12t8vuTldUtezsnJ/jq18duTyy+PnbZt8v9+Q63UN5Q6fmr35Hey0u6PTvJUTHYFZGQ4vYbv
3C2mZX31yPOb9j743Pr2NXK++2REU2fM3Qnm+rXZSxv1/SRx1LLTS+58rV7OIjln3/QNYYfn
Va2QIJcdr7ukcf4f+6LC6uXMqjvrSE7d7Jlr8jY/5jl73lNxf+rBhpmP5/R7c+eiO7KXttly
8PoxOybSY0fLrMq3ttYX3Z/Vqcv9yrQR9WKNfqXSw3bPSRpoR864b1H19FL1MjdnJYV5IiPd
Tk5KSlKvK+bPMmceqdZq2umRZw8mPLl/U7udbyz+IfnwW/tTN8zcEa+uxPZnJn/d+3i3F+o8
0W1L04Xq55Xz6O36tbPLv5r+h35fQzb1XWaMaD915rrJ/ac/+l6/aVlnP4zbN+Jsy4V3fLZ2
0nerH/hk85Jzk6ebtdPHp8Rcm33V6qOt8hc39v22nox4zfNVK3FNeAf11akf1+bcDE/p0l4D
TkZGuDq5xNL1wlpv4pvo3+46W+lKrLh5771T36uxcMp5T8qoY6t33Ts18+bld5y7s0KPqvH/
t+/wVVtaf7Pw8x/ojrhu/b5Bniy1jd/7qFA1ft/M6jdPSf36ePr0hY9UWnSGbhUHh8pFYw7W
3993wJpTE7fO6rP8lnlxE7eFq/MaMXrKtG1TG20tRzv66Z5xTXgr2bG8FfFU0qHEDE+ZxMd9
5/XEQe8fpZ8YmDEuw+OxHpk06WHx5rqc6V9uyvz8zX0f5TW9adaQa8/MzT9Ramns1F6bZ+5I
3XKoVpdmzWY0HXHXmpU3z+x8qvU3r83fUz73956Yp8JT60dsv7rxgRMfLNU/XFHz9bFJZw+k
dprUvfPqFZuGfyhyXt7d5a9Tt3SZQJditYx21eYN6X642vAXq9F+vBejKDUqeXXkguoLvXf3
BXHKXuMeBZl/3Nf46zoowyuZbNPqNNAHD39zU9/BD6VO767v/Hb6hIlf7z3+3PpGaXvbdXtg
+sLar43o1qdu97mvj6E7Sf6nFXrUtBPMob3pVvJA9sByGe5WCvtUYfz61V9nL1paYWn3heun
vdDhzJlFt59ul/DtpoM/JK+4Jb5LpWpTZ6SkR6Z0EVVrqFNSdyo6pRtLjQrbnTFQK5N4oLND
l2FEFbroEq874156HrolqqMI6x0Xl+I9kLC40t/9a1PrvNbDp649/Oa+u3ZdQ9akjelfn/mS
Lr/q8+8ZU2Z6ozrnPXVLrYqd+Nfjy+fVnPnC9v7N9B5qM4V89H318FvZA5YsyJ6VdpLbEzPG
3j1lyDsnn3n3rwdzmJ3z2vxK+csfPFLx9b+2mPv+gmXjFmwbOHmuVfpGyzO3QeMp006dqjY8
y3dudO/wfl0zhnhvHZMzyXhZJjpJHUhcxWT3eMIqJSW7DfQunm4sVfJj9emZ3z2X/tmJSfl7
l03vW7Va3pbsBpXTbj3915s+enjDfU8dnrTpkWabqk5/NOab3vt797nVTrje2nhi09pl7vZ+
86n6v65+tHp2uc5nHm01d/IDz5Y64MypunHf8Puat6nZo86pLR8sbfTG9bdObhrZvwVdhx06
t+iXEF8to3N8cq9O6aNiiGIZtIfl418iKDd+v1zu9Un7OzvbfN+b5/Ey9EOjn2D4KI/3JzYu
MYveq0dpup3EeBL/VMl8jyJc9A/MGaMGr37hgdh7Bo442q3nodUrjq7dv3zzzNOVag6741xy
j13Vz7WvueWR6XccevFwszJVPvNu5Fefww69d/c/zzYLH3Kyyk47e+bul496zv79oYl9nafF
io2z27f+obXzfN2zhzbdNfjhBDM6s3f0k53/npp6zYSEsOYp1w7p/tmOTl1aKLcEXZV1S40q
+KENUD+0heMrrU70hIf5biGJ130y2Peja15gQA+LK6dM+/QjvHrHnckflpKzcvNja+akNepx
/NiM0ctGfNmgUZ89+R0emH9bzLe9jt/ztHb6hc2jO81/r9fS7lb7Di065LVu27lK0q+eoMdT
8+br1504y0vtTHvPGt6/ZfU2K9oeOFjh7b4nn330XJOD3Oqx+OWJOyceLWcciJ4akRJTLqlu
dn1jQMq8VvUjbvEkLdl2j9Zo600LaCcNEg/T11f+1PjBZVKcD9x75Lov6SvLaEWDK3o87rlu
nPvHpET61ryP0ollVidmhYd7Ho/KvC7Fk3zNW+vXr529Ny21+XlP/R01d9W0Zr+VX/WZhCb7
8k8kvLa6yaCbJmU3sHq/91yPm5N7fFH/nur9Dr65Pnv1idmTd/i2eMmXiEPHB+qZbx47Oqj/
9G4PtnbmPPdNxtg/19Knz96wUH923azj9XaPvrXftBn59XMtT9b7N9ZP3Dr1lljP1tgamf/w
JHbqErUxvcWwqZlJHk+X5K0ZD2TV+KxUq+j0UtXWbsi6b0H1Q4Nppz5sR85IoqXo0bKF+6Ke
kj30c4yMVF9lpCfJ0/nZ7LScvml9+k9de2Ttvn/vqtF0aZP7l/Z8YW+PL2rK8R1nnk5t1/Tw
B1FLx5Yf0HDmD20sa2TPnhlLsn7c3MV/VHhqw4iDtcrN37HnxL6+6VPrHm7+wMITn1f4v06T
Jk2d1PFma2iP64eOynn+wKK7U6pFZ9HvLip5QbveVRbE96qW3Ktyi/Co4fOGDPkgs3ufXnQ/
TAij85s3+IEXr8m4PfPNZUMW0Jhf7vJ4IiPe9t1crvbEuUdATCg4ksjksJS4FBrCJClHVBh9
HpFXc1HN65/P3fpc/5zGnZZ+ra7PnXW2zFw78+TcQfRNnpa7lvRpXT+9793uT5F2cKlH2PER
h2rOv3ZM9p1pi/I2/GtN741z5jzz3axmda3U7qlpnVJTO3XYnZPzQd/Rb0+JmVzu1gWWZ1tE
UkRKbJl5Kb2WjU965bOY2uNyF29Z3WdFRJtX1EA5tlWjlPKnaIRy+JqIKveUt9wBit44Q91e
WiWqQ1Av9NbjqT0yxn1Vf0/0VKrZ6211mWa0Cp8/wxPuSVTNnlO9Dp0cUWvhxpz/zu985uHR
x0Z8cXRm7rdbmk04l/bhf0oRK45W7tO+UtN6W8emveZdw13tx6cKj2xcffavc++7q97cRXk/
5Kx69MazZ1+/edjY9nc9m9O3b/rsvLzdfe9eROORN+fmWvE7qmWkhy0Ij+/ycIsJHSd0Ts5K
90TFZXadP3jjqJbP999BN42ojGHq0hw1KmLIjqsX9hqyJFldn8rh5rkt8lSku98k+prUo3nl
GUnuH/Tdxr0fV2aGe4l6dhAUwzxxUWrhKE+neQ1n5x04elXn7c0fKnuklufB6uWtth9t6n3i
vKdpo41vjTgz+bvOI55M21Jl74d3dNicX2lEdIZvmz++1Co1/fQ4Y8xH1ae2k5O2vvrtoyT2
GyaObdOQq4d49tk1ed+2Wx2/IPqphLBe6gyzOp9skdryH1EZ6XGdo7MqJyVEpYuy97/Y/4Pn
M7MuuD5rNIqoEjGVtI7sULbNHtpdRkQiPashmffbCS+txmHex8TSnsQsGoWGh49e3zMxyXuN
RkVGeTq+XPae9hX49CeW7jxwZMW57fyb9K+nr7tj/5fHvrx2/LrB2YuaLexerVPzzcvf218z
7bVevs0VvNDAf2KTFlf3uOfvt6x+bsP2D6ttqPXMt6/vGdum0e6TBae2IHpPy6xqHTpHz0uh
06kWNSG1Q/rVHZ9KiNvunlzjydsGll8+tfGdapi5rDyNnivSBfriPWU7qKuz14EURtekh8Il
1MM3evZkXDeu4AbqCa+T5UIwsbQnPIuWSbwxwxNTerin4+Fd+j+6vZL9Pl8adfUXA2vNni/G
L9rSrMucffMX1dv/7VVX7Rj5aPUmY+otbXm93p1G4Q1LuxRWu/E+Krw3Yvo6/uTBvWdizntW
zTyXX7HZAzXmnXn9wNozN07fPLAc3Sm3ld4WcfsU+tGlxHrer39LuVumlJ16y9TEbjTKDOso
okqlRz/fPzqXbpr3l7o9bPcMum9e2ysta/AiGmnWjaa9hIVd50lSr9dVTPJenZEXDFxoPBOX
QgNRGsBsa989yRNXOa5yWFiSJ/pw9MNDNu5sOfwEH/rq4ek7RqTl5OwZ2T9n+LQR37YY2qfL
gz/el2jTHs+YWvGnx39WefNfru/QJn31d9sHXdXukw+Xj/7hz8dfGfmseqzJO8KbHmi3usqC
6HlJ6ZHpWrl69SNSyhHrYksvrld/ZNa2xGXlkuqXzop5hb6h5feG/yflpl5Kc7+U6I5XThEJ
YtZuWDb0haxc2l9iRZ/WeTuR3tFjEhHO/YOeaoe38qghS2KZfhHJSfVrx3hKpRA7wpIrdzwc
VeVQXpvHjdNn/v3fTrVW73HGvjv+QN2vHqkyZvjZ9qmnCragXsOON2mxL8bpUWvLP/Or9D1+
bavdbP/p+cceXnv6hfQjOQOUqj40Kyd7EJ3WXelNK63/esEpOrmX6Ue2LyyVAKAokEKjsJZZ
CWELFAM8HbM8w+b1HrIzszttvjN9Wzun5Z5KKZfLUxxSO+OfT8ql9kSPT+3kZRDW6dFq0qLJ
Ge5f9BSeWLOXkj6J1Up7SpfK7RDRyxORvSeJbrrhceU2vHV7Ba3vsCeuHnPPrvUHUn+4pu7D
X9y32mn2/Yhh+ccmdKI++PFRq9a66g9VmNDr+yZal5MjHvvh+Uor9LOpIx8kkV3nyLEV+9L6
pH04dWr31H2dmmxP7XiywZ/CV8WNT7kppdyGfXRF1iNNGquuyJhyze9PbpEe2Tl5QVRGu8ql
qyzw1LhxR7f7X+xEh1QtY+CMB+ZlNd5abkPupqS9arQ5fLh7Rf6kwn23yWUvH/zx0BLLJL6w
J8qOp7sjXYyRM5pGhdWP3hee4Yn97E8DM1tVWb0jdcaIk+1fXGKcGfLI0ZMjOttvLF+XPefR
HZ1OTbjgFMNOjviq2to9/247IHXhhnVrevf+5GjbkSemZZ0bPXX61FkblvJn1z3Xutttr6W2
7Xn40/zrIoaErypdP2YbvaoTpAHKB7nbErc/GbYgakK1CR3/0Y5uLBM8mV0812R1IzMD7cg9
vfmDH8i6JqPvYi/Fc6LptOnkvDf9H0cpSRVz6SvzPmq71+6NiZ4MTwbdLG8kkb5Tqz2w3sTw
KVNzX/yiQvn0Yd3+dmBv57EfT/3bjUenVBljnY16KOmnYY6n1BOTjtdfVeadTs9tSn2x/x36
a8OHTSx18tFv4/KOt/7vyLztnZYsrj1z5+RR7Wks2TZn6pvl3rxpcGz4KrqN7Ap/c573ayuX
RF/m3DdvukXJnxrrUqISq2WEvSqq0JV5ba+UsIbXjGvTJ3z6qqnNR22Pi5JnX3zo++caHt94
sPyOkV+81D67T4WzKRX61tRqtBs1YFLG8Cmt+yduStrfY49LCTrPcDJEuCf7xKe+P0qHt7pu
sq8DSFCMC8+i4ai61K+nxT3qNxpDF1j4S13vWPfhe5ve2Wftndx0fvW3Fp73DJz8+Zmux6t8
P+ynb7b60LsWlX26ZyVr1rpHm9R3Dua8XOrkWGvD0OoDpHP6MbN3uxFr33rjo2knDzUdW65v
y+H7Xrr19pRhGelRG95Pj0qPHBi2IPof7XpVm876JcT1bzEh9eEWE19tOLX0tsSsbeETY14Z
m5sVbbXZR3ef1P29967/fGGvEUNOb06osb/8CyOnD6tfs2yPhs+tX7Ol03UPNTz07/gD69Zt
WD97377UDmfeeXR9pcZHBtee9n7sF9+Py6+yRWS/+vKpXTUf1a5fx+7+vskHN7zUftO380v9
J2Ldv19t1vPhNtfd2mXY4xXmjd/4Tzl9Yff2D3c4taTByY+qfH5w7uqDcxfMfD47bPMC3/UU
6fZdmyzfneGi7sygDlcL0BUVNjCX/sgKu2bK1A37XuraataZf//f9nZfHBtYS8Tl9XmofNWG
G/qcqPLdqR97M3rAkkcb1Vvnaua+fftuid9Va/OYv+yrdvqDuz/q1Tr/ibULv3c+3pl6dujp
Ww9+kNbp7ZfafTBj2PykgTOTV7dID6O7+bZqmdWmRKQsWFYuot0yK47u5vWm3lIvVw3sVX8u
i/Gs3t54vHNm1uB+uzq9ndd3yJBDR7u88G78xqebdkjf2XXgZw2v67k5+d5PUmrPbvFl5Ib/
ZqUe2Lql5i3X5dfwzBr+eZl3D2SJh6dMz2yyw1nRbv5tW5OPvrl/5GRz45vzKzbeuH3O2yRe
6j6xYfnotnd3St/3SdPHeiz4oPaC2euO6svVL26Wr2cS1c9NPSbVznJf1VN4Io1HiRJ0QdK7
DLrBZFX+slzuon1txg04cPDQ/Y9906TKI/c02d3weGqLZqXnbLLmH56h1nMfY289lbl+wLt/
O3H2ppiXJ23K+3CKfrbyx23HvPd/Q6zT73RpuadG3TMRLybuSr9psLpt9tsVkXJtikJe0rbw
XDO2tDn3zXK3Zpnjzowbpzoppuz+Pu2emT/r5de6J3b6v43rl9Zckj6/zWRe+eN716bVvjdr
od70/i9rrxvQq+5U8W34icPLqq/8LLJ9v8w2PVbGHch/Y8id+ax2XoulH75a775vnt3ers7E
r6OXvaIfq3Paeapd05F3Hyv1r9hH+2zR29g1nMd237zoXKulAytUfCft3MnHR3dKOPNFhdYD
4jvcse/+mR9cV7nAvBFXxmcqjUz6SYPQiDY82RNZWQ0o4rw9UaV/9J5OTe76bu6ATw/dcP8T
tV46NrbWDTE5//7hoJU6Zm6zyO0bd/1093ro5h+u772pevtH+pxaGvPqteeunnTeY+wbcPLU
F1sb3Vn+yfEv3Sg8u2KWTd7VyqoavyAjPaLLw649LT0sOS0uPazP2zR2jUtpVzmsS0aTTP34
gne2jFqx9MX7q5x4ZYDqspeaTx61c2u55mOSDhx+P6F2nUH2ypWf1638cc/khD7Jne69Z9x9
3y/dlnDti2/+fXbpO1a2aHDkb7E9/3L7n/pPrfPd5C4PMTn8tX+0qzNz0szl3avIa8c+Pq/z
8D697jg2JH3umOw3m3bu1pW3nLl62L5bR0y768zYJDLINcmu89T2jtXPe8z+xyd0ypndqa1V
pUWHb7MHeZ7wXnBlyT3gdtOEca0WePtLPSdmVCztWZB4I32orj0aZjZI3HXPTU/bT05a+thz
z+9sPfatt0aMfW/cgXlrUjttePnp4fPzf1y51L7znttm6rJNrWdX7di4sPx5z+7s854D3e4Y
e/vU/n9/bGvY1jkjGrU/nvzqg8mrv5y8TRHtffqNTn2mUke69SnjZPvW6WEpdPdLD6NBSeXo
uXX6bqkauTGv3VPZW3TniRNVN+YtefWVhbMWtqvdIHxF/7NxDa6p1+Cxjvn3rgqf+UWp+jvr
NBoYGz9iSpvcLqPCu+x8e4r+4MN1GvXYck3YwJWf9Oo8ceazq/4SFv/Bnjua3rstdmSmvuCG
BkerRh04UjVy1qAHzciciYcXVM7vUX1959TU5hvyK/UaNfj00wMnfXeyTYNmm6qd7ZOijEtd
3vigfQ/q1slhh+cuatL59fLXW+c99w8/PTC2fwZ1BDnG3O5Iqjj6pyE6DfsUUehnn+h+SNbh
Vtb7ncqOfP/unrVE4yVLmo1+a/AP08u/s3f4/OiJc7rectNW33IeT4W8czOO9an61lNpH399
1ekRc64+4F6Wx0Y02tJm8bUrbu7138QjbWYl7qLOTJn8vgg3y92yL10Nzem3TLaa+nWmJtVP
fJ8MieGLze3dTuSH/f3mtEcX85bVP6m06JtqYz56dl1Oes4gY0GLpt9Ez2342eSVazpXfX3y
w9k3vPPZS6827/l+ws57T0ZOnHgy6sCqnoMrJcxoNWn2rqpLltX+OD/vzvxGLbO62MsSPmz1
fmyr+PhFrRpq/xm0q3zXrm+XnvR5rH5N3pdl/q/quYyuf7k/ataDA8ueaL75icF3f3RkxJrO
NR9tcnBojLXu0LTtG8V7gx+YN2lv3rq0PaltR2YPqlXm7NrP5tVqOOkb/eU3+m8d2+uwrq9p
HR4+0EdsT2LZn4Dt9myCR1ly3R99WFK6Hf0quTifv+7untfqrfeltazReLvdvdtDLbNrz5yc
1iA+YULqj51bauPxsaW2NrHW3bjqo7XPtT2Wl3r6qlnn+j89e+9b/b7yHG7V6BYaotAoeHGS
iB/SJD2sdzsaSyqFGqWGXb2jMxckJ2e1S5hc59/LR3/acah8dXDd5+qXOzTq4REW6fcHvsx5
5Y7sE+Pb1Uxa88rx+D7Jd25ZMT8vIf/BlVHL83YnN0hcuXJZ1KoZ3Re/X3pqk9wV340Mm59U
+/iI1zKHkRPkT/13RzX48kTUxJn5IyOXfzLo7YTcril1buhVu+GAB/esfH5Q1cgD2xK2Ri3N
H3zb3GuX5l09a9Ci3EqPvPh5bIsRp8U3nVe0j9/63Ziw3c+dM8euipm1Zv/n731aftvd9339
FSfLmjk26WgC+WFzlB+W7prqERZXIfFHozGNFJM8kZ47m6sW+p8+XrCj4/xeIzkNbvnS8m2m
37v+vtX3r2ljVT31+tw3smpnqGXcx8kh1Su8NPjsB13Szn0cvabxqHxW4VNZben4mlP/+U3z
+0u1Sn611zWZXSbQv4yBZe8gg8ZTLSZUe5h0yJ83PNk5KnpuXD+9d1R05pomcskDy1ueuOrA
zE3r2jtOo/Yf5vX/dHKdUREd8j2vVFq+o+rTvRLy+0c88RBr0LjlnlcGhPVbdk16mTf+siOh
9s7MDwdkDtyzcuJnUStem/9+mYknl9V8MGzkg43D80aGd70rvPbJhwY3WH5kdfXXu47M7P9G
18z4rf8NGzkqN+FE1PL31lS8tnvT3JWfvHFb+Mdtslo0umOtHPTSivD+a3bnPvFIm1UrX8uc
uXZW31N5676dGvbBcxv6Tj1CF3GLc6PHvyR3Dv9mptXi1XxxJmKxc7rK0SnxTXPyvyr1l/6j
Dyd2Ub3cZMJtyr5S8CB72ftxHtXFYWRroT4fGHXXjppNth2+6dHVx8o2G7Dxvu/6t7Xaf5n9
0DUxP7xzY8FqHk+zaVvGX33P5j43DRhdvcuxc1Vajy1nfBUjPIdb117l2UU/+cW5lroTzN0w
fz7ZbJU4r70iZkppy7N9Bom7G9eMvv3Q0xM/j39Ln/Vc2y+OLc9uFLO/8uFFMSsPJ25fPH/z
ni7f5g/u2nrY56W0lRHHtpXv3iRj1V07EvpP2VVmfkqDETM6T9yZtGLl6xldbk5s3baX/W3m
u/lvJyTG9hwZvrtrps5bD1hdo2mjsMpHF2hPLx+zNq3h69+G79ywZ+Xq+KoRnbfuuXXxiwn3
H8lKmPiB+CLq1eafR+YvmRU2YMCCBtnfZZpHR57cUWba82Gy7ux+ZTeXbbumIjt+47PPNcqZ
tzV5K/X2nBXx3Uauf33P8Pmi+eFJj3S/eU7nGnWXxla6Xe//7NHRD+7Z3nl4+zWtR+Ve/2Jc
88d+6mm6O0SSxWuZZ5TvrtwwK8O6ZvKKeypE33dv7KP/GdFm2tgGk7pteLLXexv6Nssxf8j4
qbMjzrS9eu13zSaenlZl1cZZ5z3rv34j4ZVn6vW+9faB41+M2ZW4Ld29QYTXj7id7rVkOEi6
sf4DLfq1oBvFizVefit78oNLzJ0vPLar28bZ+sylCfdWa39N0qIWjY42m1i/xTdT1y4c0KtB
48zKHy9o2LDzHFa7YaPNWe2rJcXHr0qqXef+qANvfB8W/9DghA9vmyGT0xptjcq2ZocPuObz
2Hu/fzte3VuXJnVtsfRg5L07B0be2uafkS32D+7akoCnN94R27pL/dh4q8234R/3COt7w64y
8Z/FNmrzfNj9R2pmPT31u3Hfha+742jjcZsab1xXMTFhy8qM+86E5/XXPy3z7oMN+ket+su4
FvrSF/a0qd62190f9fguqYE+5eFmH6Wltr4/O3krv+rUuX9VKP9G4y5jO0bP0zM77Xxr3byt
28cmbRtd7byn0/Tm7/Wf3TYvYVH129PO/mvgD2FTWiX+2KE0uC0d8/QMZSn2REZ1Le2J/Spq
/pCOizNPDn1i7v6G8/bkNd53t37v8natx3x1ulyzlIwf1/Q0m3V6Y+yO0/Or/Wfsf2IrVDrw
7rmOrzw/5rsOw14im9D+LVVo0P9FuaSpuVa1cTmWZ4EVQ1p521X1aPxfifebkvXVuy27zOk/
ZXHHrY8NrXlPty7Hc2blPB/Vt+7pt0V804zJw7ZqsffefKzB/N2xA947GFtt44zr1n0btTKj
S/7oHruTmg9YktvlRGy/HRV3Dngws2+DGrkTT+QPrh+1+MEGYlnC7uSRg3bF9u/VoOmq8Lr5
bSeM2/nA1IyJawZ4Vh65+dhf2ialfxh5YNLs/ssSvij11Jexr6/6NuzdSi8tKde158zr/zMm
c+SYc4n9X8+4b9P87mv71vFs/T58p+fDJVkrT72Q1aXx55HNu+xZ82p6mXeXZlWKr7R1z32H
V+sdWqw47xnct9+kT8gds6bu6zWvy296eHbE0q36/qN3WBtPtq81ds+2PntTXxpRpf2h1ucq
xp73PLDwi/3N26bPzf1wy5GZryUsafZ02tg9Q2fVm3/blPAuSb5Obu4Jq/CnlPKqz8NWJ1SO
21V1Af1OnvqiwjPPPb/9mf8eG57wdp+0zV/3aT167rUnW84Z41tNLX661tbyZdttMO6aMvZf
4f3Oe8p1ckcq++7c2ujWWeVyRenFScTRGuv6VaOBM93vM1IGJpZOXhieK1pUSUt9t3nrvPHb
b37vhmqtU6ecmNDp8ZdzXs1+9evX/zN5W/tFu2Kbr/9PRLfnX9vz9FaC36dVexAs4w+srnbq
y8hvdyZNvnfx2r4NDkY2z+tc/q45t4XnV0qYdCJ8y9Y9XT+NfXf+9s+ivt5V9ek6vcqcCt/S
6PPIO767p9SiTHvFvj1d3o+tvOGH3Bdy//NZ1LzdUStXJ6zpuiy+xg2DGyz5Jnpxpa1JKw4t
q1Tj66jJo48uu35e/gKr2qhvwnd+Fr2KODFuXdf5b1ds9ElKz87h197x12ozp/TIbd3/hzCZ
vFE+u/btA6/wkTln2LL9s15ecbTmnodq/1BnxBPX78v55+qaNY/3GHrt03uenTVk9YamV+2Y
KbvdmLOlTfkb/jlLPz60SguSxIOPZA/qbnV6vXpq+57j5516a98X8ycev++FipsPDfmnta9l
+Z5/P16+9Td90+rS3eiVaelDhl61on+l1ml3XDVsfaclAw7OL1Pxjay952Y6B/+87tm2MXc3
aZa54eSO00OPLtg7/P/Ze++oprZ1bzgEYpQoiEBQpG1Q2CgRkV4T9qZYqAKChCYoEHpVehLY
SpPmVnrboIB0pARpCRpAqVJCjfTeQwkdvuX5vvvecu55733He74x7h8uBoOsldX4zfm03/PM
Of2Vmi3546/ROSeMjHzMaB08mxc3tdkkpDskjHiaSurjj27t3pA0u/eC9lJr7EyXm8Oe3AtL
6ecX/3wTY6chonLVhz08VJun+rWuEoWD3JFj7XUbif7ss8Y4xXUC+uDTcE/RPsf2piTHpKmw
OLtMmjg7+4JgPU1La1gGQneHVywp43uutRtUIQxmHhB9xCvzbZbG9Q1Xcv7c+AYb19ma1F8v
2GAcnKAUXdzSfb2wg5d3cp4MT1zjPiLNSVEuk67+6JXnQedRehdIoFMk5tMgaDUHyCHuIXlY
beBrJ6UmB2kwEaCicy7EmEYxt9zUCjrduwRc8i8b8vK+RmMDF2v7yLL1QCh2TU13z5jdMjHX
HsMrqlrNWQ38AlGIRiPg5W2dKvwbicgEmM3owYucUxQHr7BRu+xrW8aRoQk5bqXSGcN5fC6m
OQWdm9VFHibw7y4wZ2fq6Vx015fT0b3zMEfAhRNU8N5mCiNmIooUvMHD7aYk03Ethipc+egI
fsBNKkokjy2XOA1zfNoH88JZWCTsBpvua+EdV6xMcmzQ+AWQmj0sZ3+eqSUWvjvIUpWeWbUA
KuNKs0GJhi8JYPqLSIREeKn4jfGqCkwmfBmS05+Oc5XIQ1TUmcEHxr5xWdCrr9Ycgio04nfA
ZMy7rVWY/UI1fA2LY4PPw9gw384xrO8S8QH8LbQySSWbzzyy0knkrMJr5dJP8ug0dcMOaTVr
Nc9eP4fEHps7bHs1J6DfGrjbbAySx3nuha8HmN5UidIRhpiYVFc8MhW0z+bnZ6lzkpvpXbQ2
sB8eRghtyGO/hUYpSeqyZH8O+mXC9+XZG0KhyZNxOizC9yTJHlva3r3xqY5THo+aPLU6OHq1
jAPuFPsWFDuwHR6QLz4cO79+43qzHMLs8vOZst1iGTvJxnVJlbEwgEW8WKlxpZOfUsLPbZuY
yxwxx3JzUiqLFmrOFJAu9GpKyb/po8slHctQt1Q+3qjw2E8lp9zcJG691o80JhSnipnZlwwO
cHQYTVmP1tknf7SJbzD9vNMAp/HZ8EvHktZjIjapmuwvKMi79EvDs+mi5kgHOyhfoemthwqu
PIO9bEZPq3iRpuF5SKNG5O3jm2SasGZopyzL1CUd0Tct7Y+P4u8XFs7aseQL1pnx3C0TOV7S
rMhSftstPQmkxnilDZS+mdJ37ba+h06qXH39dTpAOZxc6pmU2NqMZE5tRsgZaVnkl4nwM55K
zElMTC4yMuDGFJozHxdwLEaUh3J7Z6DufMqxuc308kyuqVeG6KmcQp+Yfm394Tzi6BlJ/82Z
+Qy5utuSUlbtSxpXVdwdiAJ3SJ+PUu1j1tRIIt3uIsumJauUC2eNQsI1h7PyA61JTW8BF58J
xAkaBcRDD7SDA0nrfCqLrAgviUlL6wsaCHl0cIP9de4JaDKn5KUlTd0f9S9iBALxJ9OOWSvG
9YFirfLELGLUwt8UPc3Er5cvIrqsanwB4KulbxehpEHU033/L7FEZkSVRmzNfPgzkq/3gq/b
lO/avP1SZAy7bhkp2kyuVyevWF8NCEBF2krZ2AJXYW05KQxtReNwm4exgjReVBhRT1gMmgDo
ZUAKrHQIEMJDsJC54FPwcCcBBLfJE67HW++D1Uxd3dAWqIEqUkM9KnHB6p4aClFZiSPUlopp
9jPGb8AcTcdduQbPEPVkEyGJ4T2gsAE9tG4iHIfg9V6GOX4RF7+n6UxKsQggJYIFv2dyaW9D
NiqzUFGApbUSRNQtAtTCCcgU3NUAKhUzkPl2eoF6OroU5jj6tBS+BprTQJ96aVr2npQlcS1S
O6CsQ2JOoPnZi2m5aKaZ6vh74smNaXas/Cypd+2+KzBuDsV0hwaXlbp/2AviDP9cKslDi3z+
2dNnSExMx3/TUz/EXIoi6Vs/6ep7ASkUcgJaGPtspsgOZX1ul18glNCuYYN43TWho8L3IC8x
WYjl1xKWdFNn+MvbxWOcb7Gq63PP5bChDl22N93LNn1XRaIuvaQ/k5SQ+xgxmZiVskE20Jbq
ZmPTluAgawwkJYWsmIqJEnURgB8KRDmjepDaFhSiPpPrlYLZJbpXZ9W3C4X1krKQXNiFjPJw
Q8v2My/vBfpklZjarJ2yY2UJ6rdATuRbXUptYNom536/cLZTJ+lArg9wkrVIEvJirkPTBT15
p6612fTSSx1j3OQ7ZKi30e2Cpn4MmOUzVgwoEMd57txHZrScvi/Jux+H+r3MJY5gUNYhq+7n
hxxNyNPqTv/a6xhoh+YhK4fy6VljtmFkwL/QNx7nPvbFF/MiPqydBtwLIOYhnD+HAiKfvNII
IE/CBxCaTbPOpxJ3rB4vfModsa1Y4vB+bWIzRYnKHcp2sGYziQgczey7D2NzyazLVDNhQXfQ
wb32keAvcAjhywUMeGAkE74Zi/BJAZNR8LCFb6fDIm/DwTKrTCv+TjBHr2r24l5XPcH0dUhF
NfvYOiRxE/x9CzyQjlPzDu9ncB4FzSysMsYfW5XD+4VVnQ/MSWul8D3wocDp6Fo879tzXpWN
eUTLMB4iSGoV1nqGrSoeUmFULab2hZ0bTDaDgYdlSvky68qw25mIii3gqTBn6WFVW/F3eEHp
eRhmydVHzKBydp3JgLYBmRkw2WF8sAkJSyepoReDAb/+MsO73FKx+zAO8g5Y6J4JXMicsACq
KwOpaTG05RDPW9weJulwYHLjcV1lOdb94Ju2Ku3t/o22L++MFuwvntU5a0QvLZ07vszI/vpT
2rogstaQJPFAE/rW2mAt/JAh4oOU80WKZhGy72JqlGV5lNr+KEPSV5utCBGgse1Ek2KoRipx
btaFPKYq/ZzuS9p/WNOGUXXMVCeWS+EAGTvTq1nVZWU1sjLZrdtszYFV/VcSFqhGshDFb6Vf
Smk7Aa2OW+vTcqz42279GXAxPskPs+bmBTAHDzIvh5VKg6VPcf/IhQE8l8KjRwNRxsK8kpK/
qkTzwVk0BPOLLGRbmcs68wuaCpI/vjaIZ7BOwVg5jKCeP0c/A1sLirvGwkvh32COPmBB1xIr
obZV8ACEUMcqx1ShNRpkVcaFAxEy4dXwmG0B04F5mBUCS4cQ9O45lt4YJuOtEP2gCG/gcrhg
t5W8rR0KIfm2KxFRUbnP4OgEsxIUyhRT32Kqiq9wgXGNqjo748JKL29tQ5K9zkf5RQAmeekb
F3rBSjA9AZIYjSvTqXUBYgqY9w6DK4LBFrGHZ3P0DW7RVsCzjUpBwgCCI+GeNyTDB5HVX5VZ
NgcyFe4dhH+fZrEo61EI0WcbGYfUkKS5wILKfnjM7mHj+7AUBpfeI1VrZZKBby8KbUpj84WE
xeDgkCoCeBRVR+gnlfGCZqLjrO5kKQTrcF6Alub4gQO5E9MEWG0k6A75ylcupV6blS4O3A9h
f9Ow6+O5pMbIr5ZFT2UW6aHtMEYjz7VN9laaeI4K0zahrW1u7Vp8sq/7r2cPe6rrz7Ajg7O3
v2T+q8iCXTORr8YnOi3ZuRDImuJ8FXbbJD+By39rQsDXGtf4ke4C4uSFtsc0T35TofjoyrvX
R7RNfDgOxCocFSn9+iYRtrabhcEjmdJsznhnZwQRhRhbBXf3wUwZrIUPwGrqs85WaCAZIzGs
6tzjFYtok7BC9J2OJqkBsW/xuOl3VwGPwXMrmfCFH2QP4P8TSTBtOqRiH8/mfISK7odUkHjK
+87hnYsHmAgmPUCEjXfsIFV8ETPA3jTJnaPCHKtOQDcFRVpBS7dgmDRS+ndQYu/DUkQWLSfT
FFEtpr4dxWAtPTB6BlONqBwlVUUu9cH7IxkwdZazUHE9S0XwoRe4FzAckkV452OSI7ubxUMC
FYqoV2p0vjwIH1hgn4VUDKwCcktMRGQXgofHgRrxKJE2+1JewfGqkTVIVS2eDQkyFyfoIXin
uQku/WAgc3ATlmuFeJcJR1ihMYV4V4GHOAZUKXwVxjYNywQxSlPUJfxmBQX4nJxmOJrycuiL
rGkxaeT8nfzuYeFPiusvFcokjgpXtLTGBnTbJej/VvZA2JuTPhafo2lnxY+zaqaORWcPTZvN
pvTRf1yOagJSaoBz/Jd+3neAlndm45vh10R8nmJJbO7E8P66pPL+geKkNSWSTVtqo5v3F87E
LEHgf7SvPwHlIYryEHW4xAWBcvhSA0lLV08BwxfL1DQrDR5Wx9sE4ggAwzG6swUecWKiN+DQ
R6SKrVIxhrY8eCk72zykmKm5ITMzfuwOJLrMDTGWB09ZcjOJ9AVr2cPq7CEVxK5SMTUST80K
DSz17dwPVGGO/sFk70iGnA1I0Ywb2jko04O8BIdUeEWRqug4RCDeOQen5jjSzvWaS+cYF8ee
A8ggEFNWgOD9UVLg78dWdZllfFY1mKBMLwgVLrivmcmmNeyqyMD21h4mUZQDivCqaEmUdpYC
Cz794ZRT4QLnhOwhYXV4Nl4gni/l8wQBxJgQOnhYxAdCQCkwlKBMohicoCiT9Ex/vDXi23mO
M4lhdcMIKs9i+6Pet7pSIS+EXeqzfFVnyM1ALcqh6kSHnejn8LCCbzwfkgKa/S8AVJjuwxWq
rmVO68x864QGJ/d20ppg7b9KGZCm3huIcKtPCPeUdB3QD7U8LOMPeTjp+BlE9cukMrpXF/2g
RJijhwKqbtg2aHEL2xVu/cFvABPHx0U2lUnUbsWomd3Nqbv7sSApzjTsG1zoHd5aCW/3Beaa
CcL0K5MaxhFFuKpMNa21PKAMrkbNIpCE1v3cDkI4V5byykLCdoI9Wh5CKmuX1sDiR6iZlDUa
pAJjJYzIhNfX4J1lwYIjQCcVKq4FD/cOnhkhupk3CgoVFcPapqGIyX5Ar8rboEQ6QRGu7LwB
JMJDHNqVCu++CRXzAnq/A6SishI8jHbcBmwc1gdofFA5bwMKrS10B9xtZbLA3gfvHpiEOZJR
V4u4AXdvUmpFIZjsRczkqbHoh0TYYOu48q54VQCyUXIPTEbrobXG7gWPtJ/BoX0ZnJ0H4d3v
clStBY+t1NC6YQjgBYcd9xiUgUlAzPfnIXX4wPFMdC7K8mkmuiEWJPaUkQb+/pi7D3imr19I
2sOX14RtkjeHGVoLOzyRDwQTodwFQDFR/mOexWKg73/mkuBoWgPtDb3cNjK+KMcm94ZSKQHa
fizHckNZPyY1hZ77NsgaqYpP+NTW2xaqXdvlDlQ4/ZsNOhHg+fxr84fBI4lbh8SJfOzeDeEG
pV+pgpWXQ9zOkaI06NBvrW6tZUIjtiJDE/Ql4UVb5eOeiF/p8g7yvx5051hHl+dJc4xlwk/V
u85D35qiKrwPcGFV4+p4Z5dae0huJjydUC1Gdr0ATUAhfAl60oOwZ5AFZxIBi+PJ9Dh+BiG0
uN2uA3fIxCICxWXB1kJoE7gNYRSSJQMWbfiOSlwDoe8khYFdQWWFFiRTBNDc1YiSNaa1TUhV
/yhqJqyfVEfoEXdFIbjtIQ2o+klQhT2TpZuFuQxOKND5PFNzZlU6yXQMJ46ggwWH24E2i1VW
dX47BtgzNV8w+Wk1QhkEFBnqQSoBpQwi2G/EotWCyY49isFLqzhBIWId621IJaAGK9/Chx2/
wa13qkhq3pCwClPUsPMFGNuAM4PzjJXCkkBVTz9Y3E3wO7BbKn6PhCgSAMEuY1EKwSPV8pSY
5xrl5nNfeAo6jA6kNlp8odcK8t/vU8wuNiQHG5k9g16j2Vj50DYrHo0tOc+y3oDzeUYYO13u
Du3/GFOtOTZBvSz+Kveuq+FRfu7DOEsNQUHEeSBd+m+3w5iYdeLGYcs6JVztYFJk/Q15YE7o
Cfffkh9+HkNmTpSAaimtnfRYoSWrxx+GxIvMy9yD9ELeeRtFyhYHforTiS+VZgN8CCtgDKCY
YxGustHP7DT1dGU90Dx5VzQABhdwQvky1dS8IMtMC2/B6FIxslrwgpYFg/B3VVvpwTNhI5m/
Xq2I0UNj3BDOgsrjZVwp+Nx7eLY5kK4PEEE9Ple1CMk2SceVwWOFe3vvDMJ09R6G7fjhZ0bc
EPZEK7RlJmBXuDtIUaQKgMrscYbH6AkLbrrg1Cxk+uACp8OWBEyFXd9+QdSoUbmoTGqDcJkt
SOLyGUdf0o1eWZwg4kCgYV0ol8RVCt/6Ycv4fRC1wWQM9fQG7mHPqJUroFJ7UBVoPYtM9Fuv
WMGjQFJ/iheVxYJUswy9RwWh8d+4RiH4Z/0CF2yTvYvzwjZjPUukn+v0YlEeJdJmR4kRNlMC
c+beWo5mx6CO+nE1soWqsPP8WYBAXGRVkbGNsLZ1wAXUmdFlHNkHHy8kLw6vs/71+RApPcIu
b6yMHqFj85CqIQmfSTmiWYmRjP8mC/63RkTKT9XdCGINjeSvaTcwrrG2oT0nD0zbD1/VmICa
iYlpmX68OZ+c+8WYyCgS/ylfRDGyqq7i+JbQ/MTs+rXcoSfCEb+ucN+9rq9DaKhfPYdGoR3d
TPbLp5kwDeNVA+aoiqeQSkIlbgMnC5apyqxK7B9Xuy2miT5URQA0vD0kk+UbzFlqESp2m423
MdDqDFPlTiw6QNUZA4gcQFKy+1TDB77BA3AVvmYsJiC4NTBkFgOpsCD9yT4ISERJHcyxGl51
pGorNAmpB7rCKpM6gc250P6aeg24PfAhpBSeMjpu+gy4aKkE0J+64zA2xy9sgbmWblyAdzMA
qdxh7BxLFDsgVej2x8pbD/TqyQ7CpRe4DxudAbe5IbOMV4yp5d4qpH68zzSgUcEMPmxyOgwg
lvrHwaOK+FUIwQVnCoQsVkLfuDDbjN8uFbCzxFSaqeNbC78riyYt5Mnr2MGL8iNsvvDM2to9
rNvDszvPWZBS7CFT/o6zkPELjpEmPBISk4K2dJyPpNndl7yCroZbUY0vCWe7aHcn64KcxOQX
+rECQZFCnzyGFASTfw2D1ggCBWL/VvqAz0DMiH6+UodMCRtNzCE+10fiXxDZ4hvJzTmCEcJe
5pofXlaxcFjyNWBWLjMvPPAQzLDD85RNC8VIGzkaUi9HCfW+Danis+GL9JjUfbscsTVBu5a9
MkHe18bPZysnFDsbdsiugRUNLHjded70Gr+NWOBeyuMzEPDrxNUsrDPFkOC9zqpOkJp26pmN
NLxz1Ti6VRD1wwkB3LdC6KfxqlVoiZvFAUMrpMZrmckJRmMiAHa0DrdFIMHUKyEVJmfCGr6D
wiBhsQgZSGUNg7Ir8qawIgqBI+qJODZnahaPV9XjwlaZentzxqsADtVUZh5SuwqbsboBs09z
gepJh28z3ol9GDY6DHgjKDSQfdj6BmSFvsGk9n/Y5f5oeyrQcWQWQFWE/UFWUUgpG1c/qpIU
BtkGhjqAv9uqPk3DBz5meQWpoHLpIZzx18hZifsUNf/G1sJRXsm32hbjngXyFlVZQp2qrYVO
pscUzzwJnyi8C5OW1irkkAS27cYAmbxJ4V4qT0Fz5T5jS9LkRRMJvyVCHR+PfBfNdM+jopOP
85h6zNsXOHp5Yvls3YGZSTINGVF0AspiLdPgvejuYE36+4EdLJeW62w3fPYehmU4hhpx75GQ
rGlNBSJHL3vbnIURjteU2KKku4Z3fl3QaqrEeUVUfj/1sVa7QQ2+k0Ie5A7Hm85Gx62xWbtW
hRX32Zatb+VesKvfhmazhg3wu7KI9DixbNltbJtuGknOgdZ0rnIevbz7mBvSx2qBa9DvA5n7
fwF5DZ6rhFRmd305p4hi0+p6g/dz3mDsZPDzW4QQEsEjZqcjV0Ae9FiTyI7sWai5qnMxLtkR
DhZyQ3v3wbRL3NDqK84ogL3tRxHQ4GGSmsZmprh9KRx0OjpTvTYYSAS+Ia1dNoEPzDM5quBc
uRn6Sa58KeDmI6U6PMAj74GbR3FV0bgqIureU3A/0Hir0HGYs6q1eJ3peDyEACjzajjhDiTm
JkJAY4SB7V0jkIJVEegwSfTCPLjiZ8ZT0PnIgO6qgpt58OxCUIcE11geYAnDH2x31t9gebYJ
CV+xEuB6hxd3E+cjgI+EnQO9GN+OrIEdS+UpUVoaH1hVbjikKtg65I9m7iXW/X5ZOnz5lom3
tZGyjf32G01iqI8jOzyvZZLT/y5hJqOcP7Gkx+qJW6mgYMTTbqjVf5DOH7vQtikz6PXmm7kp
B0r2MQXh/DEejYc7EdNyJaE05Noup44F/aWfuNTBgf/wdgbPutwLlqs5qXcdwqvKfrFolVjI
F3c3F6xOYQzojw6T5kRJd8B3mMsMTbgjimQIKPTe8KS0l1F9DSDEjtwx5eHGdbzzk3LdEh3a
khuxT3PDJjrfTFB0MxW6U9uMZOjxC5hIxkrpbuOh/GtbKSQxNc0DvP/8qSNVFxg/1k2osgqy
Gceqm/iuHrUVa9G9E+znZw9zLmFfg4xUs3ONeoH7B7l6vMCxCDcpwPF/GNnxlj3oFaQK4G3E
QWidzKq94K3KKrDK+O1EgK0UlAEP7wOPGO7H3QNEPfoAdSOBsXN/EGA8Kxhc0q7ApQGnzYnJ
tYLBWRYoCxuH5U4zta9Ca/UsffhWGJy5GOsYlPHW36B5YqirOfudaY1OZ+Re678zaknPnJMv
vNhzLWkLmH9B0RnzmVgY8uZhnUNJm6HBzHkWz/Bw4+FiB6IvU28712qseO694ABcA6ECTP8G
GxUPRIWvWd1r9w3etD8jeYHFe7L3cki0sG2yuKTKegC1hSO8ZOjJQurdudsR1kvQgAyGThp3
NpeyWbfmusHuF+SdVxMPzd6wacA5JVy+hQw5AmWL/8nGKD3RHanVHa5mpK2PCY8kk5CizUhN
JX5lo4fRl8MtWdp1CI0DLHadwEDFJ+/5/+zadWyiXrDN35DIIOU6mRVXqvl2KxzeqBRqSpjy
kR6Q8zZuC9d5o2/oQWGfu8C5VVpe7a0J1AovNOX4hRQa+1JOfZxUOGjMKyi0UGQekDJF0Nhc
zql1EAba4deiP0RQpqxM0uoabZzx1sWESjxQz6HMliNt4LIfUqT0O3dGJQeFgPITnTRcseAg
72k39qTSLWxMc0Q6r/Bi2q0odHf73RD3QgvhdRhfZo1riRui77fhCMJxJkZSJhbtCBjChXpc
j/UNmEv8IgQXFmkPyb5dwSC75CYN0M1LVK6j1TNsCuCRt8EHuEo8ClDk6tthe+BhVYUfXB9j
Lgp9m417xFkBz4t3riRVVVXirUXsYxHFuFKgUCSnvyATDjjIMMBzOxLSE3KzSDE5swtuarxW
nOzq9z58GyrfYWVw8GwL4OjoHBgOigB5bo5+M3tMoOlhu0MN2Q8lT4kMtxwufr+RNHipn44T
0t1hRImzC9R2jif0ooNHhxmCMhMGZmH+2pPSseJW4r5MdWBtCz/qpYILot943D0luFJC5mx9
iqSMlkuz3K8n9QjKmkTN+MhemPT2nLV1c5uzMEmz21Diz5o4hInEZfU9atrv8jLuibBOrFDH
o/6TjvG3Q9COyQbe8VSXdAuRz27us/0RsynGfG80ymjQ6U3AKAzbJ5HHzWwuM1bBrZXf8SX0
5O0V3d6V74ROsZyTlC9mf+DInDE6c42esXFU8oqqU1fNgxU39wwNtywn597Jqp7JV7b+rSEe
jmWuDbTyE22OqMpnMxesBZJbnMVuDtd7evvgySVFTQ7Xw5byoppQdV8KOC2+wXyj1qqj1FpU
jRPh9JTgJv3ePARnuyO7hJVXrmSURlmkUb1qfyrdWjY/ud6K1yZsMqifF3neKzes+y1FXX8h
T8Egva3zDZCqWT8XeF3ceA1zgK9uakwTgietbONrmypSSPBqRDHMcZnJ1x+3NC3YPMyshlnI
FP9yehvs6q92CCQ0RlFVdXiXjDD2C0w6yeC9ZpwaEIyhEEU5qk/HbjOWsnPPA45YFePDNBnI
gpXUAleMwBW4jbZqUn5YpLZXS2GwjgoTRq7iUDUm58mkeJfvFlPqKofG6wGVcWuf58jy58jz
1p6D5ZVSZD9G9qSWfGHfueI4+Cnl4quWDu/T/IPV8D6rkGn4UeMNCKm3jgEJEvQLAlnmiVHe
TaqKKwaPBZESwgl6wnmx8nhxGk6+rjGizAroIFK9XEmlKk+RnDkOdBOOzquelVJN/SxDFmea
fF43+UbMMbJgbdPIQaGh62ejf0uc+RxeUNi5EbFv2KstYR/J+A97yI9uwgq9MK50+aX+V/Ku
i6XEsGOWcN5W2hSVtXXuBKT+8VKDCNNkUuob81+LA4v5P3n/6CIPicy7XX+0U7aUxI55gkZN
iUWuqxTMrrmLiKVCuvzFi0TNzgnrJ2U2Oz5b2pwBV67Pj9N4eG5HGoO2umO09d/9VqNxxShP
lnMtH8apXXTrnLpndZEnfed0n1HFQbdxMqJaXCaTashkmNenDezaiuSJGb2rCW6uwfvWNxaM
5PGM9QGyKmCSBKiLqHBujav6M+3nml350my4SwJC9NPbHbezDyXyZHXPN0dNxrrIRYuYXbMb
hZ2A7DsTPsXQGA1pF9PWsbOnssO66028n1Lhci/41yn8IMvcce2KYmVSn90HWk4ZbyHsErUu
qK+rmmvhI3Zyj2GLWr/SgQSppOEl6bnjsK1lWEt/hhc4UBYscjd3HNr7gXaZsg7Zf8rkVWAp
oJs7vsYxsI670zWx9tW47oLPSzUM0DOEwsacrvs3ioRZ6/TdPyN/6Ih+lX4A1nkGlPk4JG7h
bD19Ng86lDIv0ncprpGW5Euz+d5J1Wz+wWNu90bXYUHfQb0mSThhPyqXL2M/ihgIqkN/g+3h
/YM31auqr2i/PZMhID5mD6YVZ3qqN6DBWu1LbvK4ap5hzDf2ZG+muSUJK+tCkyhb1c9cstps
fjmkdWt3gL9Ujn8QUVYm8k7CO2x7RkmZXP1Hs7A/3C0vzVd0bFJ//wY/aUOeWfBmKYb4sGq+
5C82NnjYj2qj/+3GMNcxfUvpd2Y3zyElnmae404Em2HAFf7kruOXh4pJSSVCW9H8Ztsk8j5A
xtDWP/TFhKQe8e9mCPlVP/VHZGQhbWvHB3bJh48w/PySMc1y2lOR6wGjpkJ+s9FOSJqBD1uv
ePNG9dbmoykDY3Ph08Y1L0d50VoB6k9f2qfXhLibaVfelr5Y5uhyrsl8Gn59+CCirhvoZsZL
NefUn57KKtiCzEYOjxP6N91M8sfLjHXGywDz728G36RBGghgh01IHZhMBpPbzU4nrrkKoPG+
I5niMrhafCDgPRzVBDfdZ2rfrso0gx+JQSYPwNvVPD2nkjHVbAJlMtVcDbgyBdPHMPwqlWuV
qc67WswQMuWDQ29n6IkXLUOl8D5pVbHigY/PpCHc5CuPM8tke1TlSwb0LOzrszO5mGYr5qGy
D5kicBFrinhpDVLqvj1UdpSJ0ovSsT/lOyl059T1lgibh318Zi1snz+PVuN8Me12nhSP6Q/b
xoHyOYi75ECljD/K5cMjduOtnRW7dWL193kSTn+Zto9wuykaoyhYH/+3KW7+t43348srZJ0/
uaDkySDm9RZ4Uon0JzcMuWCnWn95abcXk+HXF9NlC2iHTfXF8UN/fljlpWShC8ri8MS91zFx
SevEKDnnWQ8531Yh+ofqMslj7iIkrEinwTvAjv1q+LJPPJpf1HylLea53LOtauMSxogZmrW8
Y451wCrCL6/jEYXbiIkX0xwedW0vxD2SnZtR3yJMuqN4vCzcF0h7GUu8NRTStyiFdSkw130R
l9pOATcZcOFM8o8a8/IFZRnTVfMK0AwdgeJ54jKAfXkAmYVE1OB9ADr16C1XMoNvrSYJfmzl
6RUOqc/yY+B8BklKeVrNpmJ50yT23qgspCHTQga8AxSgVYKvwGmO1As7ffCdRahsLOJg8Qx7
bqK4lP2Zjk1IRI530rcz+ajZCob2M9KYah4gvjAaRiUX5Vrp2KfX4jsCXZgG2C4He/4ohy/h
qsfNpe1/uTLpGyIZxQbUCwDVa59zxG+xsohzZKe8iqQYLnD0FhZqmhHPTqXqWNs30i96Hhit
rcup9P/eOKR1KZdd3txku4XmZBS4zFN1yiLdTEwBE/Orat9/2Yz/cgJUyewsTxP785gQjavs
9dK97OyrsQE8Ozgl0fSkfB+jS35z9A2KDsehaEXAIwdNckdQJO3mrMOEikBz9p6knHs4P7ev
3Zoo/3WJCV1ut72k3KsJnd28Hrvd7OvFY1er01o6mycvjfJv+2Sc65hRork5AMP05jlHGKOe
uE8KvzR1IGKgxS9nefV9ilWuGNu3RFSGJ53K5jK/cvmlzkZwszjKMV1hkJte43LOcyH/2iYQ
7BV7pezli1ljqqU5zSER25zFgYK2qFminkk+g3XxB6gSFX6tF5CZUVLdGEi+iEiCX2sYgMz2
wahc6YhMnuHgsU7Q7CZjSgW+oyqzrpvKYr+Ux9OtTJo9AT1gTPkuUGbI0A5F6snXUFkcGaS9
56FyPPQoKcZU9ox2FvtVpgE3wY+VjSIX1s/IxZ6R3sbdIUfXButc0RjxY5SMZOvjWep81FtB
Ukqk6kTYUke8TC5eVEKHdXzwVdizoxf0sAgtPVG6FBUpEU4u90R+1Yg1CjxMYJoYYnbGx2eJ
1DXnKXezcav95/78v7TX3/09I8EOT6xWeeD/qYFnUjZ17FSrseGa2aMmaWwEAnkrjlaOzFY5
Y/GRZ9RfRFnwpYVfECe5q8NBs709KHp3lWnsl+YPu7RDuUHvR13N4jsIoTmbdV2uaVu7yyFG
UVpB/ZYXko+NIxrUdepMUu/XFelrYK9HxaflSKwvZq/hinfNdBHhmFy4NPOWfnJWUUE4Z437
5NNYl1THJWzSqfriXp/dzD7rLjfHYQwG8vJ2eg1K+mK6VVn4PIwzosx8vyv/nMaVE9B58Yrl
Xy4m9E9WdvGS6Liy8KJiqDK+2H+bMUPbGjU34GZhZZKvhIuYHAk+0MF5krcZ0xUXocq4OQg9
9gxQQdo1C63o92NYEe87UywTq4uZhlYwpd67zdfzHZWKuk3exOlizp9ZsdG2BtGHXfvYh8m6
w0ypjr7Ui6lNEgeoGQuPZJsVMc0U9ojujuX5guT3ALH7gGUvIIFnkn834I1XL7Iy/C0Pv/H1
8cLmq/mTlxbClnR40LNvLF2vTjSwxVWa+Jo6FCMdiEW/qryR6tXy6NVS07x9Cvd3DfVfHzjl
+Dn7QlJWjWC+nU9i3W0VHddPfJc62ykxjR+6Ddce8Kp0lkTJvIqjbQJNymY+J5TRNWP3VuOK
se6nvCTA+9pLPAFlNyDxvl9odVVSXrmXmfNV3KUDm4Q+R06UcD8RWXKrE2vXNDvrZzdjLFak
U+dTnWopKim/CstoDBt9T8rHxASoN1jNPG/54E1pW3kfviKJiXEzLmANs6JUXQm4bezgadi+
YNTkIMlGvfzS51Q9IRl2sb9n/9eBqgrHX8WsWwIbA0tSGfWjRlEvTTa+cQ0HH2CGVW3gUozD
LXcg9PiGhgnjYYvewF8gLx+m56fHRbqqPpDw/xJaGYWjJ1ANhnf+YMXUbRkqF2rQ0z+lD5So
qdGrRtUfkqPH/4w8/5dctwtN8MqUI1vgN+UKZ29DOq1PLdUf436nZfOUnUT/pAghbPFsp0Ni
VW2cSeqMBNKex2ESmA9Qv4bseEou/plW+j1+rk7RlAAd1r/wEzrI5AHuQrF6yUODDuTpuyrF
xqSka84P/KWjEtMHZnKn76uM6oa4tf+Bvv7qU3an6MBkBF1NzRmU+V834T84A2zCI6mE/CU1
2mz0HiOfovWjJksfFQtkcMD1xAMzdvHQuefsz09Aao33VZ7Kzg/gjGXbbCX3XFdtNjUPafd7
lEyI2WYd/LtItkk1r5dOdUabEe8PIjRfEcE+2bBt+eUXUlipAWC8SS/Sr8exy/JFgGUIvdqW
D1EzMdV9jAmeGMjgEpoUIyztwp8dn0ViTkDa5KWv4WSHNuzkh72XLMcDQEfZZfo89VBMFyg0
CyjmHE3/JQSIoHYj0dnymncnA8e/y+ctGLeH6CfnvkMR7wCeTFIf14LyDdgWTiUWtpW4qmoj
MaqqTEyC7KuZsb6lp6H2dbp5QfsaKYtntjJmwZISlaSX7Wg3lQTexqQOjZrYOx0ttPN3Osjg
QMmjpwLtc0J5Eg/8MiZLoz3JbpPWyjn1gvsRKyE8v0vat64vj4o9yz31PiaqkPUpNFRJNznt
FhuefeAyXGiG69XEQDdpXYSNPCBPXp+PLgtVo2ymXBVaeHII++S2Ip9q1mxts1swE/OHSQEg
wKRdDZ0xzYldqXbvZFfkJQq0RjQsUu3/VOH+Z00MZrCHpvC/cKMOHIuEzpQRj9uvORyM84lZ
nt61ubziJvZa1++mddKeyVtfCSXGCSdtm9AfM+8Iq1zBJjloZrBveZIciOXNXY8sd93XgOnR
79yesJwfuVpSNnVpEVsvZXRsIspz/YjHFus9yZ2FzEBgN1VvTxnPb77s3i+Wji85GJQ22P0K
HMHV6epU+3byGhd5t+w9wUh3BrBPtgo5Pcd+by6g5TBrKtRdnRyW+TI+cET1w16I9vZxbNo6
Ac2/MVpI/HQCmjZTIK/zww2CXBhiVps+ZdRk5ZrN/eGTLFWAsz3q1jq+qqALo4lYQNNOQAwa
2OUxNssT0C9dWHpIAY8s2fME9Jcd8cCq7JPSvQdUmCxfRcvsuRYGmjbaTQkb6KU5pq9To/ki
4KHxcZSZ39QEdkN04G6AyGTrzsSWwdGyH/KMaP/CunGEw9Ho/Zg1myC9+45FKow0hP72ppJK
xgmo5yMwMdgDRf195cltTXqqMUJr7xHFePq+osG+XIfuktyRyusZ7GFP3GhMd7PxDtVG2hB7
Vap3h/rWr5SoWccc0w+MdSASo1z3rZk1CYyNo9xtR+mcz82JO7buyMUkUf57jKHTHmVOVbqM
zMg/WUQP4sxXeP8xffKfdYGfx/4nIsDUx/E/8bV+vtNPBH4i8BOBnwj8ROAnAj8R+InATwR+
IvA/HAGGk6GTE+RtCOjfLQ4HVL8BP//TFoeDVbNm/rvF4fh+vCYTIzDP4//azpyCnmYG1ocD
/1g8DvtjeThGMBMD4xkWGBszMwMnsDzc3xaPO32G7QL7LxIccqr6j9yf4uM4BW/J3/d49VdZ
eUVl46dLQpK/eT/7M+vD5z74xSuyBg+MrYPfxGe/fUfu7uW6KvW7iWfI65weYYASNbSxf141
LaOuYfT4jwmRX6Wf2Nq9aPYKvdM0tU4DXgCYc/J/vdn/9+HHUWBe7f+w/fvF5N7c/A9f/9z9
icBPBH4i8BOBnwj8ROAnAj8R+InATwR+IvATgZ8I/ETgJwI/EfiJwE8EfiLwE4GfCPxE4CcC
PxH4icB/BwE1ceXUY8/wTzee7Giy0B/MRb0hbGF/cdVq3gt9/qd81TWCtn6CrIcTNfnQW1uf
70wEJsI6ffSaQ9JZ7BGHjh+xPOEoqfsE9Iph/9fUbayd+IFk9gnoCuOWvvzicacl3U7z+DZ0
PsuTcpRKXO6MOYxl7VabKziQxw6l8e8J8GeFdxnTPYB5QBWQGyikOnt6yTKwQIWtF3YaFxQh
omw51HbcPn8C+gr6v3+WuLhI/e973ZNIiRGhRy7aXTq73dsrOv0s73J1nofEyEhczxekPzZr
LnOpCXhO5BxT6pDkaNfynbQSNvzvoPjznH8KAjyy67RbtiIi8I6h3G7pbs6ne6pNm9fvnYCW
XcRXpYDZ4FiTTIHqbBt3rHvuESqgtecEdHA58iAKucg4+yDhBDRItaQC4wD0+G9VEI+bJ4+n
dPdxe2/enYDoslw73Ni+c1hZ3gL9vgTDcvjCBnZ1IigD6pq2fjiauDIyfIqE/QdXQduLgFUn
y6qJ1b3HmSpPMNijqKaj5oxthn/8ajNlz0OjDClR4bYUA94cewJHewuZxeqfgtHPm/y3EeDe
d0HmGOQHjQJzyfN/kYH9ty/8J57ovWo3PnRkLNPEb+4htBGS6+/lnOq6qzHZi3i6X1frdTQE
zYgjN/BYP9u2PC/zPX00QzR/MHe1j/X69ehD1sa1xdFby05BoxnXq0vnDwgM0489tdv4rlqc
LbbxsbQtcZhd613IIPjwWHbZtLYcvqs2Or6EGVvBN1rKpr4f2b/xePeRckOu9zhl50ZIiWdq
sYFzINctHrmMIqpPZWBrI6W2c+3X+KCYRGD1bnShacGqFvB+GTd0CgP5bx6oBJXfcjyIE5gf
XeT8GhgDzEXjottvEEQcH4n1cvUWmn7V0k1bu5c+pp9rN3B4+QLL89Xcupcm+yoKwxmFI8OV
2MamWPegCKQgdqjruH2J/4cODwIGh5RnHCX1I3/Yi8OIv9mLQuwV6NltnWlrZR67ehX6MIX4
J+OkX96GNF/0zWnd+qpK3enxvfT81GjN7MgkYDjG8mjuYSo/OwUdB1iG1gYnQAXIvseWQqe3
H06HHIjOdQHPSI45OB9wHDFwBTmkqXcCgkqz0gWCIsaAXaT+P9r9cfLv/3LyUXSBUiz2idIu
oDo8gUusWfMWS74Ag0pm0ArIo5Q+4iDjokK+h6JKOmJWE3igX8YBKFDT6IbGXG/z2cQd+uh7
4B3dKci4pC1a/KH/gaPRsRaLqcJbj+tGynPR7FoHBlXe0ScgRw5+y6yYLxl04P8qV2j5YQP5
45DLwDwEtt4x0zhNQxd1YX9NnqmulZU0a2Q3w0h5X1fcyAlItSXg9v4Ru0H2rsk3lu30bLPX
lvssKvPd27u+r7HM7Yy1jnlcws8aQhKVy/gtjYZVVs6zrBT7yyvXb/GQnb7sH+7mrpIZCY5p
6frFR6wStadUatHlut9jnzpvxrV6d/01+/sL2vbInxcyak0U4Xu1M/enyQbtubApIsWlnTlo
5ZsnVjnmOv9G/ITx7pNcbBX0ajRmz7q1oDGq3RW2ZrSC/r4faEAvYexvnhpglPT3i3l5cOEE
hNV8RTXxDmzDbUvs/vVZq2H03aTwUP1Y9/R2gF/DjNWW0+r3938CjUMd1h49AemnuJR81FOM
39a+tbOoEI3Aov2SDjOXyU367MA2F44Lwv0ThfS/utUnnfzDTzRdnBn3iLGcbvWqPXf09IAI
7Lp+mUtESXeMesRSMqJDX0KNYhxar7/ZzUEPj944vTiUZrjXNyy7Qkkiv+Rti3LJOGu9pHAD
4dVVKyvW7bLVRXTj6rX1rp90OReeHaZ0dkTh++ixw1agrpBWLqFWe9jDv6sFRPSXLeJC+FF8
dkdqn7imEfzWFgnZXPyS8PaDypFaLocYvwEybO1DzQuPJ8RrKX6a/DJ0zlZ/n/f9WfQ/2ZDm
Ceo1Drs5VlyfHdfMU+q39qWdE2q9zLGnViSMLilYBBYWGKntC18nGJJbmlnt/ysU/qnfOy5U
HyfpvD/wtTzECgyK/VPv/Xc3Y9iT5CC3t6tpptuqzs6uOhNyyJS81XOycKFe2Q8r3SMzsfeH
ifw+7ITJ/MpVaSdlGdF90Xaqz1N//2PFWNZTO7JK+YMxnAGtbjU2B9rf8ZbrLl+UnH9Pd9GT
Gkz6Mnv9sTEgk5p988Qd4nlRZc33CUI15l1X/2x5qbC49ay521spbM95ygi0sfFDrdkQX02x
aGi6Lvo7GgIq4EkMaL2SpTgg6ZFap8wM9eNR/ctA8DYwi6jXOjihfUmzNV16iGBnR1O8kbEY
75V6MXdn73XXMDQlrp8Y32odeOezxVVqhk3ro3H9nVvTfMJYdAPbSPheQqP2WJxKS76ku9PO
waVCjgZXszrYM38MtfyxJWHbmBAok78nxFxSw/JC06xusXY/IR4NPyoRrRMmfnwOom36ja+N
xCElqyGZJhk2bUvPio/avIKT+2qGPFmfEduDuNyWLg9va6cunYAav2byPRmt5Omj5n7WaZlw
/khf6KkElu5zlVGde+L9enZMUBiBMVNp3nG2H2I/VIrAT9hte8wp3hKW2FEZblw7+h1Vrkz0
ooEziBTx9MgB4doAR4J10tGT+vK37ZpD1u1Hpd7i3opzwFIlWH7ekhZs3jepfGRIFGixt088
PdDjY2Vk89HnOLNjArsOGVhykcuaoU2pbfs8Vf/oHJnvxlhEPV9Wy9fs6Q1DlNz7Ud670gqH
RVFN7W+GCvZfaNSy0dQlB3lovDrlB+2aUpeUpwDb0cPc2GjRs2iQZwxfW1l9cqPDklJWOTrG
Q+HFf9UV51X3HjxCPqLF70SegO7VJ2m2zVzHBVCn72UgniKzfeTrbgVYZBjNDUUfn4Be10HS
k5XWLTe7SU7za9t+zWma6x8EeNsCxX0XankXxs3dAR17O3d1hvFVdDx129jQwJhJNEtkm+Li
zF8RkGQgsF2moLNZHjfS5rZ5u2ntyNj9ka5r6Uc9Zaeg2ICp0ZUZqaJ3MScg+eJeZGOO6vzD
+YkOylh2x6BMA9G0HtlYJrCKnm/qeI5V/+jj7LpUGUD8Gi6wPDJf0qHtLvlgd8KZ6FFkrHeY
eJ+V+M1wNmP/eMJ4Z0D/+DcWp6AIpQ4jZLeZxkQUca/u6DdibShoq9Dr7lSleb1BU32o68i6
xhPs03ZGol2WCNzhyDKq9m5MYePXglU61GPs9+NfdBep/iN9Ry5RQSVTArwpgSw7AccF7TIx
uv0rS+WHAYxlmr9HfUZqtj9N46MPFmN7VNt0f3e2CIpJMpPbqUozOI5nuT2PydhftXWfGh3a
1t23l8+bf+Jhs9VpL5oTmP/UEru1Cx2Yv3gCWlEHTDN2bx2JagEmlBE/YD8BdeH3TyEP9LGD
GccBrN8kTkDDkcfkE9DmeBA+5rjPki5yAspg3DqLpWcBLj3ycJc/0+YEVMl1BHSeOdIRI/9R
HnFZ9wSkAv0/vf9h+gvJ4QClb+SuMvYP/tjckBd+3LZBhKRaybXlhWNT1oga7kVs0awlPPAo
2xCbwxhd/GJ/OhB6y0RybcV06uhXHukteSptP0PCz9ziePgj/8IFlvrO0JRh5P1Z2O8FSxWX
uw+9QgqeZUEv2GzzKTrnN9Te/ZK7aiSwMDof2cyNHT+0H6o8ChI2QnokQX8DBl13Ig3G+qgP
Jo669lo37Q/ir/B5r0YEdPUaL/D8NuHtvjKQt8jRNfwpNiAoOBcIrQZ2mIkNNTEb592/z5d1
aDeM8q59GslA5y/yJzAzDHzsjkxhVgn1WB+e61/cwyZcYOit7yampGBV00pdjmwr/VRWwqC/
C71llev331OWtR87AaUMYGIm9AGlV6O1WRQz9tVJmUuEsI34HMp73FmjOm2xgOnSzj+Ucrv/
fX4/X1Ymju1gOS/W3ahnLb1GlKbLKFLhj07QTNoTEuN1rL+1N1W5ZXa6LaOof6u1Yfa23K8L
c10ycYYDUaSjRusS3QBnzQt2Own4Dp48b+ZvU/uXX1D1yiZOQN23VikbvoqvWK6nSiyqZvkW
rahYrdCB4wiHHZUdKk/8VnpO9evdIkxd51COcrLTKrO1yjeki8N37TLMiv/9Wb92g9kVo5VG
Lc0RKGfxr9v83wJ2nrnelKnFLiRI+2cErrLc/UhaPEPI3heP4NFsiQhUKfqcXwy4L28qBaYI
fZHpPMw5fbQxo5z8gF7tFXHwxxhsi7Xq90oKY3okUrXl3p/bI89uF6xOflH0CTSUn2n+OFXf
rBRQvZ8y4ng3DFhnVpLeqG+1/Wzu+gWhtqVatCRhO/AU9dlRJwZaGdWPTkGz8RlrTMwCtiRZ
Re3ZAU8iNGjMNNrBPrcSffl5gshIwd0+xaPCQei7XO+yWeG+E1ADVXyiUwtLr1Lxjpl43M/8
J6wYen6FHNA9fuM7UaUrrl98+KBqEVoWM3DdMJeQ/xHT9HFlT3nEiP8Zi+r38gGZDmOgSNqq
ODKow9BVLt9mMvXiQWZexTHhULqWbdMYr5jCHZhhsFi9Uxv4RopxrGnpSVuHO1/RhCsbQrd8
unCcevCRI+Qbob/kTU2WUg5pMk1yFZPsRcbGh4z1KnzewGewyRvUb60eJ37tFi0grBo7QjTD
Kf6vlBLD68lFulzEMn+XuS7X0ko95euB9+U5iwXtorb1JZeNqryxXyMHOU8l9Gm+6rAQdJc7
AWWiaX7KRnYil9eq3i8zJ7CnsdwvtxbukjhUyiVuOzdGOe56o5SvKw16EIIwOV23zBD5+bmV
gBjIcGN9M/xbdyDaOe6hfyRT1U1lOapeBBjNp5q7cq9hy4pV9a2XTFW81E1Mq/jUdLOcLbOI
HwVWcX/ncvxTDkR1Eix7sKHIM67HMD3loNcBUhMtbHuKxBAyAk+QVVG+XKu3PtzvVXCpwmC4
X6nFvhag6LBy4umbC4SvtrtEC1ssk9SKpHC+beLHrNnHC329q00FXKKVY2NZqo9kc9WOmRzi
b10fTL0/WnPKfCipcnG3uc995dmWGjonUprCtkpdWw0mr1mEK9n2FoRP7Fx8GlTvorjb4DD1
eCEB+TGH+thAco0CKqtNyYlR4lFp/5g34ZYrop8LLhG1Q6IoNNcBw5aMJocIlybAGm65C9AW
phL0giwWCWnFrnwSK/4SbC7f67vsZOrs6VkpD7eMHKffcvE/2cbNQR2nmlVqkypkvXZrO1Ys
1SKNFZ9taeYtlel+HPussuZm2ZEywNJh7GRDgyYMzxNGtg47LltE5K8dFSuPSNBXgw+ciksO
01djOBz3Dgh2FDX6WsH8G4ucEtmcpE/5h/SdSREqZGcoddqjiDjfnFbWchT3dNWMbNLcSll5
ND0gOR9WFidltrbq4x+8NvXExnYwW4RVkHIgK1TPhTDmNDD0d5eYjfX4/6nJ/77fDPS6H91K
M6BvEHePVUtN/v6E/9sji7MOybZpWgN5DnLVFS3pttuL9mF7jzmefmxJP7USvfnRp6vMK30U
s/108nPZyPIqSrSw011ej5TjQGxPOOcQdpz9cX1N96v6Vwh/sffF6VxXtU4sf8W9euIWj1bd
WN3DQo5RSyMVDdr7pPKm5cL3MdadIxRBu2XaAkSoaDtshvFOzntSFK2w3U8IqpYVnuHf9r2K
2fF60TMEh4FK1kQLuwtlWZ3Kq0INLKzB33NUdt11tU7OdXUT8pil7A92UAqtyQfHzDfoEAS2
2FbbkN48E0Gpqa9NaXWMeXXTimO1qP8gPOF9vpQKxPnl3frwNsqtW4KAe31O5iA47suSUcfV
1vyXgc8/LUlpHa4FSurl58VgKfW509DQ996RszsKSS/RaC7dJLp7BfqNVtCSX6n+fqjRDV9J
V21qkPiUlT6SZnLgei85CJ24bURvnB5bvNclXGQG+BS1xblGz0QqpaYw3IE1OYFdIjEXWFNS
gxZFGzBrz4lylATtLrUFqbmHa2s60lJHmYHPFh0Luhdmn8kkAU7d7RuarlWsKWanFxH1C+uz
Ti4yM01BmKgHRb91YbEUzvuQ4lSljSVjEeGGUw47N8w2O3xNqyA1uWMpSWwCW2U1ppvdcR7J
18ffwUULes2/t72l546FtSYdoPIrOgHfcY6s8yChwuuHoh3AAIrW8AFzyOWsHWnCpPDqykQ8
Ems9W5Si3NDCorqESWP/GFFr6WwXfijXlE3M5RJSFPT3p9igDzLz1xX4XB3j+KX2grsl5oY2
uM8tjX2qRylHKp/9cC2mdy+doHZg6AR4hXMo5aLrf/X3lrNteiZGWd4IzLjvPGJydNx6RDK6
aH5hF6am2cEitra0ubx36VPljlMf6/0xdRVj6/SB6pCma/n0hb6tRZvpbY6Q4Z59OY/IXLKG
hctRX62f3XXTcl0stVCPOYX17dyV3W42bOhws6WrLX2iA4isHnnE+sXXPNwQd1E0bkQnBA7v
3Cjau5XJl57Sa/Dq3DX/yfXLuiWEjH2RB30eKgdxetecbqh/RJLCInlqnfJrsQ9639cfqoxv
L3sEtkYrPSW0uZ6dI1BWnK6dgJ67qFLLWgnXdwcE6bIIYDpZjwx1Q6cjhaSYaLHgv0jjA6el
8sJ6dg3KSyeV+X7/rYkwsmyP808cMXCcUNPgG+lZVvNTiuetCZpm7K6MsSY/LbP+Xk3PyxFa
ZYz9P5RlKGSZRyx9My7Ueg2rG0012lGdnXHqyEhjv1RroPllbWGjWqbgoCLkc9d4KGTbJLFv
9/cP5Yr7AQ34cE/iEDrWR1b+/ozHtqfHGqJOrLimbtMIraiTlBHzBeAB/1w1dG1x2HOeSA20
7f+UvSszzvfATogn006t6di8ShsQobyFiqFjqJVBcoJ28W3g7q3jwkma2KPL97taDij7/oxf
P/YMxJlOVSqx5Y/V6sxSTkA3DEO6WhfUv/KpaZlOpOdGjQ1VVpfPEYa+53EcZ3fv/Nk+mNjc
NGqKxdrxm9GeHvV8t8ot9nowY1GzmJ+23aToLjmbk2asu8J/42zXCPR3kaxnN7zV9mPCqbcr
VVpefyV93JHAQEPytgD/djAjScn9u0nvsl+2dgtxZNkWZ/CQ9yxtsVYysn2l7elRhIvTl+K8
3SkFlXGl5fQXw01sKtmzBizLB3zGDsauq0/6WBnvz4c2Oeojb8mNVWzYDW7rnNIGOpXNFEQC
m5UhJUXNl9gN+TQSPzVvW39PL+f9br26BP+vStSGl9ShKXJHmn+ovHl9pGmz4bMDJVNV7cW0
K77feift2DHOK7qELAnvQz//4yUpcGot4PCm6EsbkVrzw/bTvr41omdfr1aQ7G1Lj/r4jGJS
xzZAW+3dP+TVvVDTIFoZ9BhWx70oW16rH14utxbF0WUfdUtasZu/Wht1kN+QU6ONVLaUHPQi
+0tWI1pcK1hTAgIWRT9g1pIadgfCtfmSKJiu+pGx1AiHA6uj8r6QdG3u6SmjFu0HkfGHFP03
b8fN8oF2FY25xarLnm+ntDuA+fgsCv7BPvf4Bn24p05yrUPu/6HuzeOayrK1YUsb7RZL2gJB
RcDGKhAQEMOgjFoFYmkAEUIQCFigzAQZAwSCQ1tMYopCBMIQhTKBBIIIIQQI0YKADAExhACZ
ZB6TMATC7Hfsfu/33X5/t7qr6vb7e+/HP5Cz99nk7LXP3mut51lr9UG5cp64mPtTCrs1z76q
g5cazRQWKbQIZXpP9giqBwowRNc1eChJRYAlVH3bm7YtDt39U98GL4LAALQr4+PHh87XbMy0
0HMzFCVxc42Dh900vIp8U9HQJU5KQhL2ZKMuWTjRWqYuyOGcvEiLqqN2oVBfNQOZF9MaAt8W
C1bc63am9T63qcTvIrlomJxzbj0Qv+qnXqjXp3EbdRcZBws6D+mkOVQUFbTOn8M6dDW4fe7q
sno0Gzos54eLCR6vsc4rrJypCgJ+d3LXIWDUhMNN2WJDaaRhljFrR7RzhTBVa8ekEF24Quz1
VfSTw6jsXry2OduYndJt+o5yOMEKmnOuZpExGzS/P0OjAAV55avFOZtouLyhSePes93KgaXJ
eZZGhD+0SMeEcLcchhOKTJIOjMy5c0qSJHKR+ws0QIoGWHUDSEH/BpJL0kXX/vtQoUtTnlUz
Ni3Yv1I+7pIrOyy0V/AwcPpZZC8597rnLlB2MfuQq4OJLdgJ45v0g2fSVJePYeI3dAQIuXDV
b+48onyBk5vz3A+SzeXRPixlLbrK/6mpwTES1lAtcX4xnxkScsubEFxYpAp7iynPL/64y+KS
A7SyFZllH7h6QlkvQWozdB6RiD9Yv0wKih3VlhaF2NdgIS7zqHz/RnWNlz+4h431FWCs5Nlm
q3Vjg9wCdV7vD5SAa7SMnAQLpLE3WbkcG9XZjXxWe8MSu7z+OrSq4JihfFxGyYSXyOGGxVXd
isai0qb29ErziY5UtE1x4utx1vnZqa4HR326BXgGc+Rhjq9vYx4Sv1fgb59CLynvIcMG00RG
M+g7Knj/Fdwk6DLdV7A86Kka8V2fU0iNb5vjQUjH6tZPMBIPaZ1xoZlrWDl1ABRI3O47p9Fg
HDyKdFlWcW7vLylbneq6ZBaO7JXc3woVlxfmwCUuN+iMA0X03ByjQ+iK6aHYxMJVKTQ2Xa/G
iW5mgXxG9wSQmy9G7YQu8wcNQ/kMlKYW8Zg/NTM7tngHfbhBD1O+9uHwu9+4z/+u7nt8HNql
nTFO3M6Pu8bW9765iZeR4Duv31d6j/QMcTcmX5xXYiE0PDmGQW461SNEBswsdPQ2BBLh6nzI
lpuaRyhftP9e89na0HmebS9Lwhu1HuBilGPMmkxPT2NWtt3YsU1Gy2wvWkqGMWRUon6kpEx0
yNrQJnD/o9/1bf/3m9T9y6mrA2l2UJPKFlyQlCWF3L7NJR+SrOE+uzib2BfZV+pTpeI2qfp9
Xq5o+3ABt2p3QdZ2N1+yeu/bucKNyBhKGWEy+Qz363mXmZWDXpO9DGUdUsConGIu2yKrMNif
6HWLnuOKqgOUUd/kpExw0kvnhI+73JuvSZM/7tK+IfSQYCnSvRlwNHpDc+XZ9Qa0p4G3vgvo
pzuNqVQT5KFsv72tTu2ODkn3vgnmR0YjoZOZ8k+7u4lWeHI3jeNo5T3Vw0qLtEnc7+M2l0IL
d3YN9GqezotBKuZWeXekykYLTDe3nj1fTmBHXUyYQD0ftDRqI4OWs9yKsJENfnwiO0tx9cx+
H4/Z7R7TcjvXD7Oe39jnSyEPn7u4ttMm5qgap051k/C85YlWls9xsTN4U7luNSec0u542om7
z/F81ey+1kYfib1i/fNyZ0Sf20PfFdKOdNQTL9ozGzj7HclDYrxsVuaRt0qRG/a3HrTRnThZ
pvCFvoy9BmtlXikozuOcNfCQSNognahBizj+mfipTpwu5XVjLeBJc+WZO1DR6RVlP0A2zC7D
I2OuBBEt7IYxlr24Qn5sOg44QP7i8FbOCd0XgCnoO+wt4BlWixgJpMTupMdK7Vw5n9Lor0dz
NoKK3rSrER9C50oVHDs6U2U4Kpl32MDmG8v08rTOyVj+YaTbaihH4/SUPQ/YUaMvjjxMD8ps
abfqK4DO4RXA7Yw0WQkVOD+szewMbujg63wOxWEjq+ACFNY2MTvlmm6SSumUdgPMmFWEppmk
ocGTc1lgtmRdPnbnnW6Td05T5hjrEPLB+nkXdSa/g2DbO3jr+v4HdjOMDtMH3H7LPX3i1eWP
uy5N+U8m7azcJC5QjSdAu/Nw7fpb5wknN+p4DJqNfvRlKxroKcrL2FNQ1kdNHqmTE84CSt5u
to++aclF96BNUMCMEsPcrb9voQRr6/dhmHJo1fi1VcKpEr6RXYMOLk9qax+47//AVrBniRBE
ysc1+JZhwWDE3fh8LjQ0OMJ41jPqalealLFlgbDYqj7xUwwKtp7MUxzl1Ku08K8gZZL8ujNV
8YDlQj6xsBRvM2FvoGWwxG0xR37cdX140O3jrgfwzxyC+TZU44FyQmGPjymtnsiavWIw2ssw
DcG/1AnZ1qcq04Qtb3Qrwb0oKRzmI3Z0fW2p7/QT/qt8abfvPBPpmC91NP3QQfCTeRDlNAr6
onLARDasXWDp2IJLUq4MHjRxdhoaYUO5+9KwfaC7Zjp579cqWw8k0NLeVu2X2g8OPlOKrXwn
vEhDNKd0f/83zeCbXHLZW+IEXlfI2/eg4J3QiwLuKep+/PkGLZVODiFrhOg+c97g2DZbuWO3
1EZ73vQAWtza/OToOr2+JlppNeDSwZBFX/+2mRGcV3t1ALQbaA5Iu6yjFv4T3RzjCjmnqvHN
ABKwTe/49gkFSyuecia5LI1iL11/Iu9PHcBaeNr4go/98VH+PjmvmhX5ETZdVpNi6fW6hFNS
9IUYIhZIfTnQ4X0iqHne9NMd1BQoT3nUKp+nXHJStGeJFLpxb2FUuClp3dEO6veQskl+/EZA
PyPGJL2MrW4oXu7NcLovVAuHaGww6T/xsE8rbgBvnSEUFVlLCMJbwIaHW9txFfy9fBCUPq7F
S7xLMGpgRTn762Rsan9/9JB6ftWV3rS8namzJ0W7X/U1CCMMGEptIx/chpjEFdZDwi3AdO6D
mSF341vn8tV1dXonfvQFjnYbWNGYwNeqM0C+d/VCZe1jynElmh2o6g4C+R17Y7qVlpZ9SOIA
1Qd8ZPiYkgmXs9vKkatoxTM6xGmS4P1LAsVJHB8D2XwHPRbgdvDbqOn0V/UZREDjwkTWiWNc
NKiepM9cpmlXzmtyquIPGFjODBBWl6Np3xzEvqL5pm7erFw4/3bC4nqJXvuk/fdSgDEA5dU/
1R6nws7ur7kwliJH8bLz9ASezz2dpogXHwD/zdK76O7n7+vvrHJmqUJYkrijF8NwXnp9/u7/
fqb8ls9/gMc07GRvnV+7mrzgcQ8mvbNSMr5l0I9afnRg+n+Nowa7euX9SuGVBZNMMxUL5fFY
Uo8DBs4lWJXjyvJ+uBE29ZZzCilTn7SmdwmY5IlgDLHxxc1LuQkEHLKbyfuW7IPamT7tJp2e
6vSeoM8WUXNosU8YIKVBFjnYcDAfa8s+6ibmFQsm7sjLNzWoz8WWdbwdkZw5ch4C7h7zDTFX
i1s8NG+HEMGoQmGGs2R3i8Q7izchuoyrVA0TVfLBvb2OGaTh0jdqNNDRLN+A0TTsHaUvQ72f
J9JYbnuLShYbgz7MLB/unjGZNcK7HLLaQasHqJctx481tdftzw5YcZjy8Z9wdkz+IsLs84xD
Hwqtwu0YJC2/WZJHCX8Gi/pgiOueQzIOyIOc/hynRl5ppO3E0jRc3r4fozSqBHVIbI4jX9M9
LSq19YeZ7oNcup+kiJogwYiGgbrSEaG9jTAVX5GzxEMi3r0VSnrOy5N0Tg5ktdP27J2wanKd
cxW8L9FKQqvDlKex6f6fJZrWyYaQU06lbkMWdFveETNN3VLtK/36t4cJVvUkPsQWwK//U7Hn
3yLnX9/330snQoFbbbt7A9Hg+0WcenQLkwgncktRYXx1vnoCoZd92q8VuQy7tl/eptDa1Zgb
hdDOVz/GPjSToYo9uO3zVWPO5VP6IeXJXx47aDs6scjdv/324653tZn2Bmk74gErV0Cd8XxA
pGhhTBqILMreaQ4Oa3cM9SA2jShYsR1GP734TbBa6Pk7FHjAlRHsF5F6qydPquzuBjQaSPId
JeVqzsnL5CyIavLT+W6iWnOs2H8Wr05/nG4Et5fcuxSyHV6fnwUvG97azz2WFCUFYQm3/G2R
i3amyK2X+zUsKj7uMlmPnXyUVNkC1hFJY40fdeRtswzKNi88N2kmWopnOVskFSXjbXX0rLsF
womAfbpSkJP0Mk6xN9na6+tGt735bVZCbEKVMbcvetMUbp8c0l8XlLdv4jztKkKfShqwP7uR
QyyaIlM5pD6r7bLHi1zBvvGlpF6JUiBOXPMz6eQsypptv3wxG5YvEbfd7vS3PpPQgLjqHQ+S
ONv1HOC2UHxw4kuj70cxSWt4zeB1HTnEi2j45Ni1Er2u/ti9+aAZvN4Numu7GEhBz5W78Tz6
6pjAriOTyci8d88+2cRdsSDXijY7P7z5rPLlxrFZSJ9iWZRRpj/d/7ToGKm96/yT7dduCSq2
BspjfWA4/Jy4YmNsGr/Hsa31byoLQDaA5Fkpn/dsp9p105Zb56sOyAh8j2I5JajYKUWBseS6
f+rbGaMOxyI748lQh3DXPCk7tz5yJl+2lRl9QTdJG4c4Oay/1tH6wVFteAxAoQdiThNQP4vt
XLefQY8htCxfzESzLpkZHDcn6UgT8OF+t5zazU4R63UzFXLFu0XpTciQ+577viXSUWsWIftb
ZTujvN21P7+vpZnmlTqyIiKC0MZ2GUCN96ULFhd+/bvx3++5pzIfFzT8EHQJhc3MBq/jDD1w
9dinn9nPNf3pw/fTaZnMN7RMIsM7r4c7GA9AiLz7ecxxSc7nX+fjPu7S55ngtDe+H2ypsdFX
/qDkT2Wl/BjWAs2wuZtgVy4RbuyzMdtvfVWlTM4I+77gxwOdWoUo5YAP3TuNGhGzIKPNF7PP
lByr+7BPmI6ynDec+oyfWNtOiu5tBOziIEdbBDAfNr5aOChSPGambLaj79064ahsa89wyEiO
VrIufcfZ37jC+SnKEMXEDnh2DBvFlsnm8Gfztqd1kvyeA2BjtZ0LZW2dshy8HeofSFksSVov
megRnjhV2JxxnOWOwasm3mnRystfaA3Ol7KNxK0jgN9B6TH9PaiQr55OYNX1DHO0sHbnjm1j
tKqQbPUr1teuHy0CxU+wTnbBPrgBCbStFNGkoFwCOkF/vPvB96Q/rRwZYbqOBRXoPU5IdJnE
GTthoGUAoyjDxPaCTbCw6Ns62NvuXp5X68yiv9WxzITu4VRZIE0AzPWKX1mvlYXv/AfYGKrG
f6XKxG1Z+kiVoyPbqrNyWbqPf2deE1VZ6pRkjwpskGDpYd+EAyXWk7/pCzxM0vBwDK4exUSa
hh94VWKBIEzmFDm4aPAmbZOeQc21vQ7+xb0kj5f4By6V3d7neLAm+QttQbqIL1p6qyvSIF1C
IzRPcdbh3YzqeV4L33Ucunp4lIsW7m5ibQxGTsSmFkG/t7zcVjX0KDFUvk9D7YZr0ms3JJIo
ATwzDSH9ZCv+MwdvjInafsIkNrmfzUf/eOswLr9/OYt5feXIav1YMKOrOLXjXYyFcTsd5t5n
m/isqrY5Ov7KwCncpLYRz/KTXwdSNTbm1K4SjLt5uJg/FrCXkmTk9n5U0DUwWmXsWFTlO966
MxV50f0G3U8ztRGdkFHrVELQTS9Bndt34nes/ZNRlRwpdqT3Z8+Pu+7375eUplSqaI/ElsoK
bwZc+E/j7Q+JW2ClWNoyVg4C7GbV8Cg/RNqSeVuO39nHi9PYz4eD77rzZ1iIH/mLqArmN/eG
/QuyjJlG3hm52TiWU7K/vh8P199Lt73/c7h1uqUc+/S412CTk4CbrDvfPfxI4hIMwPUbmvqM
Rqhuqgwuk130RVTZPjaaYbtAFeLaa01mLXfOsasjozs3k0OUxzS1kjZKhXKPeNugeOHg0VzQ
Qj0U6VK6t4waYnMRgPvYIPU4Ar+e6rCz+HGX2RcKx84N9Z/MpVKwleKds6IQpVgKPLMrxLzi
8vI6gPf1sz/hfaq3V1BTCiGDGccmUX18lpCeM2B8mRxFSbZNeNyotFXb2yYvq0kYYZkZLa49
6JpnhVOkl/wzqxB5WPgjZJ2fiC+3OgS7ed6arwixeABChP0JXxtHDvsi3BlawAKPcFBI5KKi
ePfmfE/kuotwdZHItXwdmpF7dlKzzdS/MnyfFhVrZ+SnGUgV8hZkch8YXYye6ktuyg4VGf8L
7WP9He2L+k8y+bf/aSLlJYPxrttNVTs2P4Qq/77xFVS9BAUWoR6EnQk+xjQbjraCTAUMV4M/
KRHyMeVR9zqLsx1i/KM0WoIwFgzXId4aggiYxXFhPAJys+heuAkJx0NPxx8evRXRpaopOiSs
U84oG++zXumKW7bd/kF/Z2JOoXPvQ6taqoCb0cttLihxsQUMwz6z0PsPOA3cBSd1tkvdOSva
inyWhoVjEg9sHiDEGHiLli7ri0s52hAqnBD92GPRaG477IbFK2LfIsvxK41o5c0bc57dTx3t
op7fGUs5coQlNR73DbgFw2/Wd5Tkb+665plNTDY/Ng8OQtbARYJlYXPBMz8Ol7eTnvH6p/CY
P05REr3Xc9LaKhk5WbGWA9FFhl8whmSlxxgmiXfHMq+Wu4koEO4Nr87gunAEkZzPgQ8X77CN
t+btaWr3Np2+TNxctG4ArcAPhRddGV+fqfJhljDeSj7uWkQEEazPuHooXLGOXckQONl8j4Gn
2a94bTPuQWy+yqDobl6oumNuEAXJcTCZCD94dMS2O66cSphku9rXSI9kK9oc0RMpPhfL6PB8
XuLr6Tgz7enyn99V3bZFsmBzsJ3LckGUDTXR8ZBsC2JemN81ipDpiKVUftcbjmqUNX/Qq1BP
L6y+sQDBth7UGmeDW9lKs0eUp4m8vJUve8MTLvoE8rXidd6LWJdiWwdW4tEO8Y0pBvnY5LdQ
uPU7PbU9+H1fcoPH+ay1fT8JCEDy+hFsQZGGlt3smGg39ecJxRyYtc4juGf9bcFjlgPUlPR5
Z4nf0CIEHlCvR1NMadwX5okb4A1uJl8pQZsYjwQ9DbVF9tmdUUBp6qTi8lJTl4FT5MLvW6P/
vrs+W4xlE/sdGgemqeCNIILmTaVm2s/ww2KCLoW6FkQ2SddbhjiiMjOzFCWM6MunmsRO56/1
nypAAHDWCyPr8PemzWr562HcNLnPSdFD4+g73kvrPDlWKAegi5kXo9Rs/Hy3lbafXTdv//bx
FbK5bqm871yCbW9JhVVL7icHHJGqEaikhbDzdjdkxnyQiLVGmS4gB1DZB68SbKTmnVEkcmm/
9h2p1eCQzbbi5B4Yq+njrm3ndxWT6/Rp8ZCcGgGgeq2GdU8XMmbiYzYP5daR/Fq3ose9Nu8+
izFIb+oZ41OXQckLrLPdSX/glAV4UF2RtRs/+lp3XrQVG/x4fDrwCdMD3s9t2GovMRahGIo2
K/m1++218YZWFh7zwcprf6m4QQvodWDauL+hRebvcN7egkDfKqSb5l7PzIG455mbGTXcVrbk
L+gMjPYj2cPrHWs/aWj0Ovcr/rU/mZ7oMIrLcVCc4cVWCZc3awrsLqxISeWFizMUEY/Wpnd+
tUw61MltuMWC0iFHpJzND16fG1b0msYpjz6i7Usxf9IaP9fZt1Sev92lm7p5gVQ35dmj68vF
mYXvWcW9iDw5RWCRDxQewSYYxMOFp+9T+8zHpnNfaWZ2dH0fq/ZYgKy3KHmE2dy+HVc3Jntd
Jd0hN5G9cVhM4rlRb5OoYe23IzeBj48jZ7C18veerwSOE93IDt3bi6RAMmSm1CJ8ggOx/rjr
h5LxxB/3z4WtKI5XxTilgMd2HvoiAV0ssXqp9uOun8M85ZJ+irLvukRDCQwyu7U/rzlrsC2X
YYHfSyQj++N9VIblfmbF0FRvkFWkmT7y5nxngV7b2xIRSH0b9JvIPn/kzcVsa69FLTz9uOsD
eXfj9MicXccarGx76sjR/93xp9CRStDClGhpM41OUCx6n+741KehJv3XPhS/HVgSs0aIhqCv
26q0KVTkmzF0+jN3h6n3yT+KOL7bx+CMAdM6u3UMXvsSAEa5grcdjpp4k8FIZ6VYdOAncObC
4BBCc+pg/SJpxtXWCekxkBVwDYMf3D7LjLW0+e7ES257qbbxsePjwuFGrB/cC5m09bAxXrZ4
tso+3D+jroQPAswMI/H9d7eWEL3C3WebwwJ5eqPqmTk+wQHaQbd7YIK+6UUIHkZ1tY3ftr6Z
NNO0FDXzxqtqMsp1VLD8prPGCBaHJO591P2Yv604uwnhp0rbcVY9r2mqZpWGRhtWc8qyp62D
3Iwv+FYkZkXio+PEbNH6FTgbjg3YOaXCvb1CGykOM7E/dE6NKk0oQbqYG7xAl9s5i7q9H4Ur
0ARJCz6ZBWybH2n8IwNL5wpyKa9e4TSNyEWqupxsbHBj3TSJab3FE4nvb4c2Wy3YpMpoDi/j
3tSYHbQPJERI+VGqmitG1v8vNPPh37dL/eNI/y0ezx5iGUDSyfaPjIHZqxxkGgngt7xxfKNF
ttEuyjGOMa9G1MWJiOm5uRaRkhWwclXFzFolBy+kTFj6BCpz76zojqPDbvVoIdRqtwqqFY2W
bcC9zJLkmdPuBEDL5opR1cefTZswjoHDk9oVrZo8/NPs6tGIDV1RvmhxN0+MohTqtJJd5wV/
FDOvzyd9DmyRpnIAGEw35I7/4FmJIGktvK2BWATkVqrunm/vYWPr4RMsRTHLLsPF5vRu7iwt
IJ7US4E06de0JJnRkz+P23CExbA2SRBnEDD87Pb18yPsKhhJePTUa3JUn59C+Ewty36A7WbJ
WWKfWJoZS3b2Ps00/z6NVj9S4RxpwbJAmai6EdJ2OAcxgdgfNLK7wq+RzsRVr4jVIpKhuACy
MzWkqxrc+3EXAgp2alYIt5vx6d1blWVXUfyFX5Ab8fFOGZNnjriPRRUg5qpkz+ox4XY7wctB
JU3MoRavP+ajD5uRvTrncFZYk6YrJQFja28ijB1TkD9vEwIiluVLP/Dy1mfvxK7wGnyTOkjb
JCDedXczF/bnc2EZtpcWx+om+mdXA8Dvqxc0UXo5PnJJz6P9J2yuvH2UedVnVKsGbF/c412V
aUfdbj+WTk+Uv4ePfjUetftUQZMarQCmqHh4HG7liOxGRjjaGQNY/UsD9YwOjVMNcoSwm0tT
L0ksJ4y22SVyPrTdbJSKfXR4gPsBv7fulp2FzV8LQF+nFi8egz/IyAACiEopuyrChin+qRR/
vrGzUwnGr9a+VeHlPy7J/xGfPpsI3nQJCVmdrSGJaHrXKVAMIXJBJEiTjZb94Lltn3MQSg4W
e/efjxopmqME0BABwR8YnXgupoSTQW/brxgRPTmOj+KomBh8Fljnr03f5Ofm39PQMpk9oWRN
fe/5I82D7bZg6thYwoaWNKm9yYG5bgq8iVlLr/V3nvfZPyX2Q5YNU7eutpGQq0tD9Srl6HQj
nWLhkVOfhz9vy0BqElanjNbrn1okiipEVZfskraHpzspGjS5fVRzzYhw5XR8wGJVYHDMTp3J
6dPAqYYKY+wAtr1VQGm42bHbBNJ3wZY27Fm03ZEE5kYwUbA0uDo28YMn8ypOwRJziwPx+jM1
C56Wl75IFp2VpJ8cSvfTZiy1XjaP+NmgNPEMyXj7ZGDE2JUSXnzzd1ssqn8eWrToTzg5sa97
2bBf+6+HzGIEJxcRl3H5EhA1sJMOBojrCGfXxAurUm+C5ULQeSVYx+iAATE4VTSbyKfh43Rl
sxTfdOAYlE/DxTyfJO7HnGIOe5n0a2pZxsDe15wila0mSm+zwE4ymz8bWGdwVGIGyWC4NUxa
OFetYeWmPEbNAG/2eVsJgIN7JKyYUqjdWWPn2XXfk3K10WhZOpO/NiRt3czxWlK0+XL3qKi4
2ut5CJl5rJK2SNHUpqCv9wVSwZvVs54cPKVVPvNZjP54RsS4S1pKu9fxELI9amjD7XmKLVJm
6I4DtqXxIOD9f0OC2NH08opVfRqjpvUvTf+MG19v3P4DL735na6Xwdk7KS6EU6x6Ys0SAWvr
zjEKyV/Xk/v2QUWQeZGRdwHB9zbLOq0aVZC1OfQD4lcs9kPUgbkNp4WpEX0gsiVYDtHXMpCR
vdDovNlzBvTsv7j/M3Z/NNMM2lq1x421WBNBsg+eH/fATTSUDmOC09LkcgWJj5cy6BHiMfFB
79XbdH1XdqQ4F8/CeRPKi5dBCMUOjiBgaHE3Q+L4uOknMQAjcnNluPd5aak1uFmpsAY0DwTf
w0VRXB7ps+8Qud/wvfnnzx+3ntyjoOXvH1FtUrSfaPR3BKCKTlcuFcilCIpOnu8crmW5ZVJW
e8Rp2OL1DBK3JBAN9zt7GrwFG1dSurNZ5mMY4YbFBXqFDce5q5Eg5lYJKd0bvtr02TyWqS7a
rNiiG4n6wRX5DQFqoQoySAfV56KrBtvSKG7KlJJRXloelsOj2DWyjLiU2bvNSFDllNJLfQfL
rz98P8DRkyyTAzceX8pVow02HrWaEoiAMqSh4tqm+jnFTHRTrPo6lyJer4JR0OiCjAA+ZgaI
cysVkIU8ubUhmG38GSFCqye7vXIfEKCmrhtDREjLHu+0ow0yop0YrvfXRLCVV2YCuWOktwJz
9ZGfqeq6Z6Mrv+6BEUq56SKIq1Onwp3/Qkj/3Ut7mwvQM09msZScj7valz6///pXDign37Qm
eaOu5rNisDO608WlKioaD7JNeF4h5FjpaknDaPnaM+XwiBjDcXTohNebrrGn6rDNCGFd0YuA
SWfrFa6bLsXmlnxEvTljKaWEPcIKlVQmWKwuBm3oN5wU7qTSgi868ec8u447zRy3GH0Ysd2M
xbNkoC+VembmkD/PX4WtOu1BOFZGMZcbSC/QeNYS9xG6Xt6nIUEYYWjAdJ0nyYUV6c5vf+6B
K88qc1HfNp1pz1+/qdweufL91B5YNazIgJZNCSFY2PHNbAkN5TIaJHbF5jRgzTtdgyPX7iUY
ezkawy2bChaHC8xNc9KAWJ/KFf30kPXPGMsq5dp/Li9VOSmfRwvR0E00Ou9jSmwv3uFDba6m
yiZPqFUcxDQti69swywP9aa/0l2EImw8WfNQQZIJRCVSk57M5KmctJ0eYjYTfQuoG1gFaTDO
glkh8t+GuIidfminanx5f1zUk8K78Gn3aUQXJDvQjJb7gxr0t2Z9kzpJXjWgpQsG1pzpBy3g
K5pmeDWEKRGabDmT4GaNVaPNAWdyGzfp+PlL7yTxMCgIBT9SLHwxa84kRtvTZkOUCZs364e1
wcWXjY9nxMdtHWzrAEjviJ6BmOMYbSElSjOsd/D+2ExiyVJVafx51nrkCNlkOA9j4MU9goC7
GE3nkRqjoMmIegNrNHm1h1/jaC3kNvjnB+eJHI7EPZ1nHRLbHfqzwrVfuYb+r3bbl0EKrSyg
iiB+kSJ9VTeyVyzh0bw8FMD+9HAX4WRrJ+p19jTpkcDrXJi69TLEzbRHLX0ygGWtFztTvCO5
41kZgDM8OczfzIfW/yVAeaUXPDKX8NTKSOJZqnkKXS3XyAOEYD8ACMHQAiVaA3DcFzMbzIIn
TvTZAhWAoEjxxJYoHIiczhsqjOYfg6BaZzH+1on2DDgR8BvNAda10H0gmBgcAYRD94fbJorM
H6cg9+djY4mIcHDij/LhBGnAJMuxlJFGujPngi1vHTgbhF2s77+gsyXO4k35Opv4iZIoBUYb
3GPbqfnbrJZdL2rMv4tiPnSA8D7c5j5hCXsD7gRBtfy4qXitANGeFzsTRXZrF4VO72Pb1aSq
pjrS6ZjgKLSt/U6NcjlF45QFRvvaTkIcLP9SCpbBjCTmmdh6v+EleFtDZkQb3JxbHgWLwrnR
pHc+RSkDrEcNEBf7Q2vf1FLUynCaae9fRRoTadv5BMK2M3jL9foB3AjW3dpV9iLaN9wcYd3a
scAapZbP7BAYBOqyg7EXoyBnFe1PEPWpJye/vM1RWKtqUdebYc/yQKMHBfxzT3E6jVHf9ofd
jj+G00w000zHBRJrAb38kHXyBd1/oQJ+ploEp//0cddB1BfCLeVn0KTjVoFUG3myRtPYHvNf
Wo6fOYYfVF2QpLoXPxNy5eFiLx/jdTWfq9X59gV9y5Qgwmd+ZnjHg1cRzPWu/jjVF0FDimCW
Q4KBm2OBg9U29it0ZIaL9fYXAMq9oXNnH4ScHeW3CEKKtog1oODCjrZ+o4pNZyW7/89JbVZl
izoTxHLwshoz6OMELq+NubV2vJ8TcVeq4Wc1A4R5sjd+CCfwY0Sd+u1unoGyF7tyBKKiHzDt
0aY/gyntPexJmdChC2wmR5OexWW1eT8/TnOgfePJL/Qfrl9t9KBcGicXuR2P37S1qxgOJi9d
l0+rMW9eziDPx6uFXx/2bEDKlhp6UpTnUlfpzwDF6PRlQwFzLgWK1tBItWxuf/Bx15HuPrLE
Elnrx6+ZkuEkbZ8itN9E3qPOEjLfZDeu/pU1bOlRl2FWRpwLONi4EiubQcepcP2jnnd+D+QB
QEeFRe15FVJl4Ht6bHK2buFsSL7URfmsP79nZyql3lBZy18dZXU07qhbZKjXYymsxgsKmMKt
7ZiL3b8knt95/ff4pXVEi60OD1uslCvbWx2mSsIqDfIXNqogPZSM4OBVnXQS2A7iVA1G5K+e
OAJjiKstyaGB9ActYYbeo+ql8PwlhFFFDxbPjLBqMvGhq7tZN2SYsIymf/iOrpTAWP6mKfgt
Y2QHWxerfDimdZCa9vDoer/LJMBFiUx0I0imlhmYgNr1pp07NwBEsFdoUst05TBEKy/mDjNB
H1ZuTS9bNS1OLox64JnbFQjZxTux0MviSBnMBFohYpJrg9LWhwZWumKYEVzWoRSVSauZVOwd
lYLQaCthftwTaNPa9rOZGyANm/CrfYYBXFxSGWmCq2jjt6t+E1miIr9Y0ec4O/Z0ph/emrjt
gSpAPwT3Uh06aEYAwpWhpkT1xdmUxKUx9k9tOnzjVCoeeWu1XdPX+8RqnyZx+MW2rH46X6JM
tgrmKwFnkKcpsPtRNwNwsi83XU6yPRCf1VYU0ErpTMst/tdpom2c3ez0+gkVG/gSt6utrwNv
FrKgnTLs5mA0fPbM6oAakdbcXBAB0LR/bme0tZCVjYxE7hSnkoxoO+N2xq6J37kY/m/eFj8s
5nG5pbsnc6i1ahbQnxsVHbpD5z3O6kMVZ9JK6vOwPyjvS1WziDcZPR0H8PQDExw2gjBhAu5y
1LcLiNXEYn1XTwKqIf1eute1aXRt5HSV4QOvAHY090mfF+sB9Yxo0jmSPtBOOG1XTgHHj63o
ZS/FtyispbHmilAwEw8z76yaGIcrxp2jk9a06mWD215k19ZWtp1p0/nYTXvUCpPgq5lk/YMr
T2mWzHT6o6F7H6L5eWar/skvgqoRKnf6jIHV8njRmJVva9dBBc0QtryxZs+++Mvrg+W86sUS
o9oiZgVvpGe08ZCDO/L7CePvOD6B+Us3qjdcWUKmIqID4rqhs/e7IVqIJltlHlYyQXzCiAbe
eGM2uD0uL0/a+mD+n4nmd23nnwbcN94KBsiDadLX+oLlid67lnZAOOH6B9Jbzlmxi3GPN/xh
ZtTJ2k2oP/p44nWAK75xbcmz8fQtF3yovmfI+DiYfd7DgJp9GAjP7AvXJNaVy06+4fLk0gW0
P5sqwyJ8DtZLqmaM7VGr5EqtnucmSOexGm+bFOHC29OmS9OMbnGKm8M2vqHOdKKNMlVtd5Sz
eJbU3mjH9XbMB9SEPNnFgCWq6ZTk3g0bM2OU0uI++04iGZRdu2x1A0mpFkTPUQA8c+udQqVF
0U5S3FfZWz2zTR6CYRSEushOa1goZ74VCYdWkghiW6R6nsxi93KooDbx7TQn1ENgoeEHt7wa
MSxyW3x15hXgtprQaYQ0JEcCAYOw8LiwgsP2h+KOUqPj00QOHgZ4dHlcKQXnK/WLSxIvS+5v
zgsIXjniWaOyzlE3OK+zIy+1bSDaixgFDxgkiQgGN4AIrSLaO5/K3PadvRHqH3eVmyocWfUe
6VhguGTiQ+o5Epbi9KInjkrCPv7M+4H0n0n2t7X9HiPmBvxm/M8Tm08TzfHpqpJjA1WmTSTr
B/fUCeyzmr7leHJ6AK0heAFyKBIQcVPsYut9EJAuZ8D+kcX7pkyVu5sIxe+CXFxZl/D5Dk0i
twkjKMZXL606gOGECVoA6F7LFM3ED9Wqe3Kso6mdHP1wZIPy+EDorFKfYoMMHtblzvJFMk08
aSj/xoFRf6RdekiqZDp1b+idqBJUL0s0NuuFGCU9r7gdS4mczK0TXTIwOdwqI6W/CneBdPU7
ldJM59lceknSZxiv0+PCpwcPbBRLFNb06qpBEcEFT8nHm8KhU86uG/6FhfnUWGwCpsQqNfWu
t3tqqujQ8AmNZ79tcv9H9Za3byO5xMdPHmR2jGLlpZlO10jpgXi3GnhEzDHN4p0jj4jeqjVg
cDfjMMQ4fkv69mRGnnrGZlf48FtOfKSgj7pYyTJpe1gFCVe19j3ZF66Vh2MM45LSZ2oOqXc/
OFrv191+7ngGvGHViRBTdKzncJTbpV7+OQr8JhTM9un1rPFiuM0QyglVemiY+nVfrWAC9sxX
J3N6yrz2Te5ucqhqrHJuYU5kQUzLWCtgTID82fHe4KC2rjxcPqEc46vPS9fLJ7aAodx60Kl/
Nqv/Itbln926a5da2DcOLHKox0IM+EBid0jWcON55XIqoEQB4TGt97vDrS+ftxfWy6pl+wyR
Bml0V07kaj7eBefzyWnjym9dQlh0b1obfKj25JRSTm1iJLlcssSq1EhxeCC/wgXV31ttcgnW
yO4Nj6yX+14AU4ixiMjOahHfjAiX5ReGOgR8TeAEiibTl/S9iXTs0N+Jm45ZXuMiD52qS+9i
mz+5bTJVYBRbljqv7bapxSe3zR/ujJVBDVFWFle4W6HDcXEwEtRc/5PbJnF7S2bkHwpRD7dE
YBHv96cErlyaCvgUKVHUyjVfeeS9OvtmQOrlmQVS3Nh84gkkvYgD1GSn8HpDHJDXheElH+PS
avCnMFgk4Ma2cEOX3QpChccatDnFyxoB+qaqRaWNAYZeXi17+lpoEbs9k0qLZT4KnfdUDwdz
HIYN2Oor5YCSNHc7RnG8JYm/Yp3Tnqmwe97WwXXOrWrGtT3Zrz0HzldchJxotnBBhYatP3AE
xip+WP9y7rF0PMg8s7DRRX3CjUCwHrR698+F9mtbf/tGJyffpn7uTtXdAsdJ6WjP0mvuRii4
L6CLbeLdST0k7BiscUqQQLm9IyVavhbdq6n5fwBH2bGn0i2v4g2DgdyVD3JemooGCyDBFEJJ
ZYhW2mPWMMGfYGQF2ihke4FtGW+lu/lLyyyf/Mf+oJMJ4mHDUCadACMa7NCpp6je8GhePoFY
V43zFc0S8tObEFr8w3aw0YZ7p7yao0cmMu4qjQIxBV8XCakRkwVYU9lXxre9KJFauukVQ6Lx
UKaJfUIwDq2jzoya2etsG7v8PwCa/7WC+oV+13heH1L2n5PUEYYTbwwO+4+xdhLCEnDCkEE2
OBYz740nd5msLseVEfJFk9LdOtSKGXl6ffIluHSi10YvIVC5hMgxPpCHLjhSa2u7WmPc6pyr
YWdVcooqNWaoaDfd50fi+0szt17OKscltSKPbrb4B8n89q+iyzmmK/rqp4C4icIQcnu6pTr6
LwjaoQ/pQUuwyWfglN3rfx0BMoeaCmQj1jM1hJH1sq42gmWxt9zQx13pb2tsrOBVxqvY54ST
NBAEpPiXiNe/8HTA5f/W1vVp2M+c4DtqdzZTz0Xhw/kZFIrW6Y3Q4I3bj7qS/WIxz5RBCdGj
45Qkn0La1XsJjkVZI5igKruODpYOnl4zXk1yDg74lP0BgbVz9CF7nIXPP/5SkkTPjvUPc8nx
NkWZYIM10drwCWcJ/1Pyh3Dv1C1v1pbJneVHm/YwPL23rSol+wWbS5nz5d1q7UUJgj7Z2mY+
YEeEqQEs3j1Rv8h34LBzrCA2pcJXkE/QbnJojIos2B711bK5mrZ6D8jJ0gDk53zs3VT8vBJO
AonAnmqVnvgIz57CU8urqRnxT9j+iTvoIrmfh4q819uGV7V6yASRPt+1FzNZ85wFL0OHbOxv
ilv3q/+byZ2g29Y+qmBYCwGvvwIZhyX4+vFL1UX5EonDoOwNyhTqbn0NYeUSfkcoUP06SCSg
Qe2WBmY3hlpI2zDaxk0Vzu3l8s5YgKGJRoYty73CVZSn1qCxBGf8OBRQupeOWjtOJUe18FTQ
Cmbyzu2lhk5dNdm+44gSUUEW7LA9RVE9aN+5Xxb0r235rWb2AZUpM4Khwrl93uEKa3aOe1eF
dQQqOhtmlpjgj44tXjRCNWjT5mrZkwXG4Ng8gh4pDf35xaMFoO8Lh2MURp86UmYz7aOD1UPi
N1PcCKFBHrD6ZUY5Kd2yKG9dvOjLVHSVEcpKUAkX9XgE6bsPUAPrUv4x8VeqksRBUaRJ5vXW
BOzBqbjitbwakB01DadlABmjKgpbIEagy2f/jQrrr529f3u/I13MqhOFKpM1u1cry0Zc6igM
ZVyhAxM/iO/kGDkFB3VRBCe1eLH4aZwe7iTZhKVo9BcFbntK03vp1JiperXjJTchW5/hjA/B
JDJFhu5tEkUYacVFiQ/wFkyGqGAImHHYwWg5Z7cb9atZvRZB0JmXq97zhVaVrcOndwpeOEQ5
mpYbuwga602gINBkGiEUAorMS2906AzCvMk78YtP+1uIJr84yK6tPOD4Uhu9GI7AG/D2jOpv
LJtx5FYdG3NgIPBEQKA7J1JTmzU83wfwTz4lkLnieBUR9iiVtZZMCHtUmIbB69kNLAUReL01
dk3ppCE8D60N2Hxpn2y+vbedAZtPVG+M8aMjEwZy/JwxtLLFIaJGi2Qt4BNwBTsSj+nTe0ur
pcS28fIGtlYDH3HX4qFJGwYeS9G926c3P9RQC/OWV153YwuG7feb7WTlWJWvOLK6V27vCOZn
OHDoIcn6M4364/PLojcHsJNIyGjPOiuyHHt8VNx06pPB93FXjzKRemg+IVHw2tCUOWfXjctE
qA8sDAFBwaPcxxwCkNxCXlfSOHHq7wYfQCwNr48qGMWnNsnzMDZBIocErXK/64vt4WBWQmGy
ApZe0LT5oXkTRKj6qqBOYHK+0L6XG38DpNRmWlMy4Ww6mZQuHiqZwCStU7l8uY2hxDd3tFM5
Y4rfReTehh8ox+kWhtnA2uioPKw90pVjwlp8rfdxl1PxZxu/LJ9f0/LbaCZ7XlSGeFhz34MQ
e0fYEcZMQ4dqbzd/+O3Z0MH2GjsQBGEAdWUYu4Btu4H0iba7NdZnZwtIi8fEAfupwewaY1i5
IizTPtIzvWJytm8qrVSDHrw474QLXoZVMTXOO6VjWjrHs198Pzv2+ZHjDpO7e56TV2/HOCcr
XBKZxuj7C3G6gAp8jOEDMZrQwzexlGz7Ir/+ztS0ZagQNLxmoZeyGeD4zljfNK1Udc9uhmml
p8RqllibEAyYCgQCkg1xAQE/J2R3f820/E/vo1SlGOfzMq69xuSgxqJe6Mhcg/IL++93DOxA
y2RU3UTDGNlN7CKkmfQZQUBA+tOvncwL7y4qZvODe7+oTyYEYwbelJ7ld+tH9jOPDmvZP9Zi
nod4pi44oVuUfEp0cMEitTJCEO5ZtwGW5lh9Dpt89QP6zEbmI30h8k1aidiiWDVug4FKD72V
oEPOhpZgmvph2KJ1bjbY60/qvzhzvxUt/8WBdqklimz2uLZVybu8ae9qp6oRa1Bss1P/EUdX
NNWhoWOxyphTTcll5oDHISYwGm6mNogySwhoYptVJxb1LFv3ZtSfdluZXuw0mKSq1EmWb9f6
5xUP1NJ8DYfzd4bPigQklO4zZdU4qWVvKfsTiL5PXRKf39YyEH2scvWx4B/MsXDHrOPjYSHR
vL5oB2JjY29xkYpXCQ8wxzZeFaKAJJPxcvTHR2L+NCFpxwepRmV6uigqSodn3xH7rS46YenF
k19B3LH2xRa9jTNyF2sbni+TX0XpDzFHk2iRPdrImA9zGFN9IAprNY80YTpNF1iAUeUimdzy
UBK8vhrfBwGQ9OJ+jja9B/JTwHhQFJe/1FwusZaFx6mM+a+UTQihj0JUe1Map8JveedlcE7f
aOthVE8ud3NUAgGa6EDj5l26p2EZ5atNsaS8ttliul6lRDMY71GT9QKICPDrvO1JgaN0f1Jp
D5Jsp9HvBPWvGqy8Q6irOQsKM7Wv1+TCk2YrIa57hL8srH/V8hvD5NStJfxNv5uizKvxEqso
Rfs+40cJr2qiXpHi9G9QnHD+SflSW1tEfn5qan7e3YsSy8QNSXG4md3xMyMkA/y9ltmosEGW
tEB5tpCJ1G4/FCzaOCUxQVS1mM7bx6UtdK8RRSMH6ON6LyazW5zyE29N6jlUl4s3NAsrDeFe
C/zWvjkpK3YrfoaW7VStnqDfi50ipgc/+/L/eCzhv5rEf1N7jEmY9hVObRNNwYsVEfO5xbVq
b1NvLQgGPvS2BgZyiJ0rKcME48ry04Bz/4s/3pxVZT0wuweNiut6Y3mgUKzOJ8GDzcNAEO6w
HMQJ3yQjNHkvD+sWrzhPpuP8yBeak0wT0JBGwvt1xKS8t6TK6YFCKBzc1Zx0JUnpu9tQm7X2
En0+lp3YD7GGtph97fD6F57qdzup/+vxlHZEI+I3wjUXnISGpsiAdOkFx+ryA87yPu6K+mQh
mSVET4w3JnmvuOFfV2o40ZWYxpyS8VtB0Szh0FIc5xQFJGGdeNnYVVJlmEA+b1YHPURpE3Q0
gkzLOqiZ2MyA4dSSME/gXZMhN5+93OSUmClL13Ak9UV80FxzMhbgC2sDadGH1w1dW3vpRpL7
bfCevOOi+cSu/CNeBpnBA8cZ3Phh9ZoMBM3ZajSMS5hQ2WwPxPZ/wiJtxFX92rlV2mVzFthM
VRcVVSlBhyOa6jnwCYts6gyusR5fld27UxcALY5YJeeTKwHmHALci6GFfIPju7aTt/e5WTq1
Cy6i6sK9LAnBfzOOBohpy7cmA4elLCNxHzq2WybDzSM/0FX1KgxPITFUcj08XK3UeFUSBelr
ojXgN2+0kFb+bh35R1V1eu9U++7wJuVvx73y1yH7XeufZr3SIyQpMQqrtKPo1BGxfNdD7INy
P+d8vL97J7B1Tzf6jn8CJBnOkz9E3f2vBfQvrv4mDcZS1FIfbfXiebAqNip4sME/+4WfVxeT
2UlVFvkNleQTGuYIiX2HDp39o8EUsUg01qO13T4iPGi0YoHcp2D9KEnxcjvZa3wuPgp6X2DH
dd1aiWGDhtkkljHw/RfZJ3ofF8Msopthtd3e+hFRe1SvjaJisMrWlkyzUFEXhDUc5pkncYgH
gbu9GtVG8/Ip8ERrc/H3Mf/iAf//0zzS1drab2R4M2B0uKOtgwIpGAh3PsxthJeJICYu1sEl
vv5/o6v/tfgnrwe3IkVV0DZ1xZlc8R2ue0fq23ayoqtovmF2nRvjhDOaIyA9SYn9bCN4eVpB
lPttGXgHVRnRYsf44KNiUgbku7Y6eczvak8HdZn7ACCCT9FcpDfcptMwY9PEknzqFAYO3pv8
SxP3D3ky9Zofq9d6YR8OowUR94p+6ZZ/ft1GS9OvFmCISiem7vIu0d38tz70dHBeEXBBK26o
h5kJW7YbSBjhP6Avl6UbjWG3ElJSME+HOjvyCZG1sHAtTGX3prEnHcI13uwLp9TLH6IlnFiQ
nQ0ipnjF8Dxs7eMJmSFXq8vWtgSB6RVs9IhsCyTZ3RpukLHVNU05aximNlZN0dKvl/indb9t
6WwUOzQ+xf2NiH+iJr7padTi63lswYbTn2STOTmTJWfrim/5+4iEXJaYRzoplO6RyRc5os6p
ZW/1zvLchRhvVwQpAuF//FOf4X59qJc9bVpufIgWeD63D+43xN8084ODPSOGV5zTslJyEPyl
J7ACwOpSAhAtEoVn2Y0pHzXcTVHOOjSsU2XHPh1sbWOGC6I52qQIFp2a5UU15hWRwBT4JTSm
Jnyagk+wVy0Yo0sBzUMjGWahLAmzRzBtKOiaVPk0nY7qLWOmf5tOvRWDvY1/m06LYRz9eOId
+XuKioAB+tttoN/iRdmz5K+TRigHYpm6e1/+0XE2pDd5swmuV6g0Yt0ISbR4F4mcPZpHsbnK
WQ5jTxIZGvaZwWXbBtbfN4x1Jkrtyn8624JDnzjHO9x3pl7EECnrjh4kooFs3Da6QuwFBtUJ
F4R93knKX5/BWjX4By6DeeIv/vDPl9vvabXR8s37pBVJu4Gs0JD38/GSWfe6zSTYrJ/4reVW
puTVwuZGFWK6ziIhEfc8GNt4zfJRM+gOcg+dWF9VU92YkEhqzLAPf/oyLj+xd4l1D5pikYc6
OuZUShZx8X028GlzIJf2PxQVGaD27NM1bc7INzjaOyAu1G2eeB0tiSJ22gG1QSxSWCsYUfrO
xPWDD3cSz1u0SSbOpwyxuBvF4eg1oxPLkeapkZ4Zws7lz55BuBtFhQXYN+QTS68SMEvn04Sd
i0JlkrC/1spxaiHiJzWfPvtxp83zH3cNFfmtn7AOns16+8JY9vicg4vo0tCAxXbTtTts9jdZ
hKTjvm+JAq4HfqJ9n1yS23kN/HRcOdZnQMS0Xxrc591cYfljn9TSjk3c4DcWrYe9NpeZk5du
2L+TOCTQK7nrPk/z9nlPQR3B0xtqDOrcBn+vZAK40lzFK+yTmj+WVM1F62yRX5uvrKRM7MY+
LxL5DEw/2fF89qGqIvlU7cYZish7NSNgSbjvMOw29Qq+rzTiYBXSvm2LemKUWCHU6ZvmNl0m
Ct4b2eQA5Ux6l56rZ1a2UmW1j2wmbq5vH1N3Ta601kpOOEN/+tmGsSWw/3kkgnek3yWf3tcf
g534OsnCMw1gtjWcAXJJP5g174kssi6itKbKpI+cJi6M4yvoOjEJ0Y6aLpLpNWH2l8f7V7Im
jlU5YukzMmmITfaJ4/0x6RN7q0pKE/sk009QV19PlVYoaOdsK3svlc7V2qx4/RB7anaxg5xs
VykmWDdepK7r/hDVx6b/uLGTEQvXtW688HYr68S8M7vgR8xOBirENSlW0L315LKFUgxs/HFV
yag/3p4TBihUHYHHpTGQ8dgqJ+UaHaDuCX799B7M43LeI4jUy59mT68j+3Q8Ohj+DyI9xFbN
+rZYKP6PMicSvxiD8WQ9yo9jPZ8D2aMIgRs59BG/11aWqOeFueOrS4mvRdOS7esCO/qI590E
0/OicdnJFWtf01uIjSbJvoWSz4TkHryOClDuRKxhz5mrO7VJvmARu/5m4pLk3fJXLec2RKyH
Tvz6g+3Lg0vVNutdd4hbZ1l07p4CDYy3+7LeUlxh252ft31cwhEzK07DDQohio8tD/eKZtUN
5wsf76C/qjfSkyx57atEt6o9yOf2Fwgv0D+VLbEwSeq8Nz3EqbVEr1nXPEDQ+285Q3k/IPT5
5ATsYeITjhMFLLubdPf3vNz/7J49PTxPxNf84YPPyTLr7MzymWN1Jt2WPMuCCFgFQJcy5ti5
9uK0tG7+Wb8nQA8pySKd+yBOyijC+oVMBFwqr4nhmnTzW4EjvKqfEyyapAWT+Dgko9PSJMG/
4dSfgsd9CmgaBd6HhjlnpxQVEqatD1gxcTeITLuZtIVbXFzior/UxcRFPflzZ5ja7ELcT2cv
/Nff9d+s0//HP9m3F7734ItMb/XSh3566kDGHfZmBOCLJxv3Yi76U7Bfbr2QzKnMw619TF0h
2YDhsoHKv1SUBXOZIYT7rlsUTXEXEZ9IKOrUb3hsBp92aXEY5IQakNICuriAmwB0iua6Bbnw
iYMSnwseH7+zmacK1UxcG0zoeWAcK9N7S05Abi4GW31wD5t6r1qYVBlsMN1g3c9ngaZK7Tg6
FIiRCEga5oIWjkpOUIRil0/KvHpRqajYWAQGh7NCiBeo2HPG65vdzO4rhBrreYTsjVhkjd/6
ZB3ErTc5A2Z6Cih48iC11JcvcXUKysjVodjtLA77rVyWXUwyhXoW688sfnIQ1LE4iUDpB/NL
sY65VvQ6wEOQhk04KQBIKrRgagK7vK2GFhfTbLpqN5RK8zZpCt0KseYxI2L5nX8n228MJV2K
NxBCaVdxERx7loRhBHENcV8/BjOWrVriHBr0uzfZlw2fvh9VBswo5/JQB8kzuOUVmoq06ErP
berOLBtyQfc/JPLrfv+Wci9/uLPiNeVPUptWoQaNoMh2FljvNiBos7DxsIyKC5KdkjieBid9
PidlK1ptSYew9jO17MsexU8SH1+a6TeKfz7almGXYIpFMmqkWxjkRpVuOk7busHfIt4ixmWY
g9rRyzJZL+Erul999uu++i/32lOeQ5xxNzIJCI7LW1TPb0zAWCS+2u8HHbPZV/tHQiUifdPC
IT0JlEsaHRJJ1oh3XcyodRPerQgqUEwpUcCwoDsRUJcbFFSvTWU80T+rVVHsW2eSRJcmufE/
7qKt3bs8awWmqr0Xrx8vtvyOA6VklszGK23nVASXih50dM7i305agodHxd5O4b4D3P4x+tDY
+/0I19n1jrY/gEeDuZTroulHsP0EIM8sZBfOMKZ8wp8PcQnxjbgiCbdzfjGz6OBjEJ5cqwAC
VeYaPrHdePCw8BuadftT8oMQ8S3X/QGucw//H+rePK6pa9//Vql6ioqlTAoSLLSgIFhkHgK1
grRKQAwhymhBGQKEeUogOJyqjNGiAgkQDTVAIkGEEEKIURllihgiQxJmCFMICATC1Gd77n39
njO095zzeu59PffHX9lrb7JX1l57r+/+Dp93ZVjjZuPwHlYugJKhtVtubTfzXiWqWU8KcGjP
CQwOIZ0ZLBwbX/lMrqNjNqsuNG1lr1EdLF9qWzPOSJgPeC8fAZ2NaNlXaW9ce7qyEtDQhXV0
ZA8FRPfZqq/3LLn5gMv66k8UC7MMLkikSzdEE3GPJnsBXkywwLZZMjfQ/TGI3j8OCPFemBnr
ig9zDkCm0G8M9be8OwHjr7oeOs5nXWRMM6LJU2PhqsQUZbea2OxuSUJT/saVaT/ApAM5AALm
yaWSFXVQvtNC1OMj8QyRiBvTsjHUrCnKBRQ/Tt9A2GwMnuvYmZCZcnb1REJVfe0iClB3fhcE
pX1MOnQ9xYtnjZvkjlSVLoExOFZ6BFKeiOmziwgGO5sErOucnURuwlYS17fc7E/ISbM/Wzkk
cFvHtI7FTVF+2wGpuED/KPN8rJWbpCziRLYsJ+xNyHaHTa8gU0olEtn5dwcpYBPZCFtUfF1W
ubLehf8LGqYO5RPT62PsHnkK7UpnxCYSfol+zW+Y9uLoukvZb/Z7u8ZLx9+L1g6ryAkapw93
IZ0iDGukXSdTZ+q28sVS0FFU39YRRj2L33Y17LzWEo7Xv30gbS+q9ywozCgFNDlSXkHlLdnr
fn2L5uSIRBhkr0RQVd3mYQDiI2fP6bcRgKox1Ntx8OjCC1wKkO/SgyDk9Fw4CFUj+oEo4pnB
E3MavkO/FPAJ8Z1HV4zXv4pyqViDHzEvZ8tYNrps5rcHv+ec6ZyFz2y+Dn6QEngrvoKJ2smn
vxvyI/CS7nGn14UVPn7TFxSaNA+Yfb5u9wntMqDyCe0y9iRTilUzdVOak/YDPBb71L9iudya
HzpjYGxfEmPv4yaGvhglLE/vje49k7LLHj555kLFrDlLeUtQ9gk60/lQixKzt5y3UneAnJoN
kMyWvxtpxFBast7CP0yb6yyNH1mOPTPinqKlseq9MYAxlcMV3a3XwhaPuSwS0Eqq9qZHHiw7
DbNna9+yggYr07TyDtZO3X+tFZSpMZoye4kw93pF88tEjblFdErKba2No5jtm667ftvxYn5j
44i99DvM32xtFqXZHpBaAmm4DQe37tkFEZ0+A2eflBAEC4BNe2sSpbMAX6kPGOyW9DUSOvZq
+ijW2tifaU6ZAG0bndgOtiRPpb0JWVcwn+9bBcxhAAtzeqRgu6QFwnHtDUlckr37hIXhy6de
HJOyXXuDHwWt9e31kJwpL7cvXVIic1f4SKFfjDbAZ3nXC6GsKASeCl7fKob4xZza+eGP8DbJ
3lPX4rVtc02WYYAf/Vqn/fR7BXlA2SpqnXBqrUoi1i/eOnW6l/FuLKplxrt5mpYS389wXf8E
C3wyv16yonDFVH+bfYblKmAenfIDVLNR6PXcLP45EW3i21PBG4WvJ68unx8Ta245NWG0hNL6
8ss12xPpNybh3a44S7L/0BeWl2F2jbyyGWN7vdKrR+KWPSaJeRKXjZFrMeKzlFKM9xdx1Ngr
ky+xT4RHTBkrdS+DJhqvx1YsR07O9M4k8fesfgiFF695HAUFwgE90qgNmaEaYly6/bTCC6gp
CYIcXYxBXVxiZQy1RjJdO8RbTlHTi0NzkosH7ZeNrOa2XxOkeKdtDwXWYJ7gY/9S76uCtHUh
+jxl/uotCpBTPP4+FF+7eaAX0CKlNvc8n8R4nmy1YhdCSz1uaL2rtxh9ZAv9bceTCV/K+MeE
r4/AIjfKQBnuXlU0WTrNeGrFMAtRKwtfvR5z1gJa8Kf0spbJVJBOt/HZ4cdH4AlOFzvkiZMu
7A4W4SBhea4QpTOWXvLcbnrSovQRHztVuNWsoei6XRhkxM5t6z46Ril1AqsfiAo9mcXPANUu
JcaYzl0mLD66qkkBu8gmK/mvW7yW+DPLB/TZI/6tNnksaJKohalmtFjUBbF3SwgPMXaVGJcR
auSxchS2VWKU4v2K8LD5Id6yRtTQqtWvoEmLy9nhJxwchQfvXNZaqrNz/g+gTDbNtgfqiqgB
aHcEZGz5GfZA114GaaVm7GkpFn9Euy8fOreOe9auud0mvlK6sD6KnNEG+7U3Yz+JedciAZyM
/t6yUGr4Wsny9qVgakqdRQFXK2LP6dnplKiapvkhc0YszxjMvjjvlaT1BtAdLN5XTt8175Dc
PQLaqLTj3KMoSITMH8Ch4FCrK2QCdy2pSV1vANApm8HS8Tuk1dQXtsUIY6X8EsnWSXYJD2WG
Y2LG7l/SzzQC3v4mHCDb2jN9KVsZGwnW6JSf627MDAAvk+WtaZSsFa98qT7fkz3eNCePPTdz
+C2mUrlL71ub+KGM7hnyKWOMnwGy6FVZlFXbhIW5dtjSVw3pgNoNTJBYw77jLcdrmMQ+8vl+
OeBKjErDETwPZdgvHEiJc21SQ998xk0E1PwCtct1MOGCKUq35cDTDNZ2c9leVoCBmj6g/Q2h
9GzEz6YXi+Ue/LFp8a/s2V0DuFP4Ovkg5dkj+kOJlZa4n0FQJaN0/4gQ2QMH2RE8dA7u0LGa
vUUmhRLRXJjbV7sFloPJPtP9ndcG4p5p7Smmn9oORB6wE0LNzcKNxrt9fF3KxIP4R5uFfFiH
E4Io4LniyDvt0ftSwjG6cyy1uzYnocUX3q3uUXm2eQTnH9CCqEO3pOcvcd1R+iT0p+xJIGf8
j0JH/33Rwn8Ym703mOZ7Gob6zELws9eCbbAKpWIPu3JSfwfdXiAkle7OHmRZW50cSmBByZE6
jq9YisYQT8O5LCMcesPOVXVCVTRGAjKich2RvmaJb9kv1u68jJc6TudXIbcEf8l1NHVUQmQ8
dGInsOv2HWRZay8GuJJwtehmVhnVNZVQAn/V+l5EZ4yzoEqA9EhEsurJ+FiWKPRqoDf75wZ5
s3bLQqpb4ZNZSzqapzSomxHnTfyUham0TqD1gT5bPPMpsfOAE1xQgBjIyyM8dXNhnn1iqSzb
SCqf4MLSlpNKqjeK7nkfyOcNFWSVI8NnPT/whEJRpwftSTcyBMiHUngGxCS1knbL+oWRS6UF
YZij0Vv+c86Nf3H684EsOcDr3+mzud0oxCarAVC+OxNqMd54m9sJj7px/jYCnmkiGxG0cbmR
gSpbm75+9eB+xusJbOblNU8nhTVeDQ3selFyCBfXkdbYyTZWMoEcWh3NqIIH5y80gTccOBHf
nvziH67HHzUcSLHQ4h7n2UcAiQ7YcY3d1//owE/tJ1osjrROHXm24HppNJ6CHPR4qvk81tCa
TNSzcWMojZcut3RBFWFtk3r1XnQ/5NLA11/deWDnR2eD61snZmwk7p1d78snkocGBzq7Fn34
cYL8j8o812DixDoxmKhT7eZoxnN29lq4mbIMUXLie5rvEfIHAs0Ln04nfni+8HyxvIlpKTXk
KnvRHY0nSbiQu38RPrJ59V/1+A/2yU1OtMeX4eYFpPQArplr8G7wsyi9O+j4dCrywBbdtC1k
Xb/KzEvVH3B9aF6QNzDA+3p8u+l2vwO7X5us608OEdaqwJRAANzplLyfl2gpJ3wXjtI1qYQQ
ArgxIivmFOZYpWOM/RfHNovKAAAvCUFvRjOUtMppNbRgwlCAQ8rzi3VD8G2XajKCIndhUL2j
hVigqRCMY0lO+rBr5F31yhNOVEOHDt6xdWHCaQlyrnStE4Hu8nCv2dSGDGWeTcz1jRzr0vVD
n0g7DhtLjmroXQ/fzubnw8DPZVerEBXIyUXc2Him/mmAzYNco2NwxRGRrsEjMPszVgyGlRto
082cefNB6+z5TthMsrnUb9+cKz3iR07+ljTsZgFv/WUMtgzq/tMM8/w5QBta92cIFLT6iDx8
fH92afLyVYjP2pj5dH5+eri4U7docNy1DL31PDZYxCRoimGX1oMOW2DiYsCkQoNdnSqAVPC7
ywAYtrt+/cH8+ZycO7VW2PaPRc2aQuQxAgqfUgYA5x+GUZ9qPBoPCAyfD3ixWVKFD/VK1xsi
SxCYy7tE2t6yiHNl7LKFmMQgmF0ixR3IY/L5bce0xOGVTQ3KL4aLyaNm7+5VtIfXLqcHjRdQ
h8uqs4FS0hl3rhXeCxkCtctr752DGUtkWsfkCUrFB81kxkromIVegFyWAO8oGvop7QI4xYKY
atyLlH6wxDcke6XCsh4SMBW/PPO0m9IX2z+ZXGEoLkHzwEqglLyWd0aDYim8dG9l6JOH0yWs
+aApYgWiMNfMid913d0Tfkb8c6DOpEiLtsmQBik5VGGH5qiCOXm8EjHipLIDip1u68gCmG7s
WxHzY+4Hz2sRW/SlVKiPcLFJo9uVlL4CyIBR5iKBVxr9LItfLXT7jBUfFiNZZ+hVOdReAKtT
9hi0bXGO6hTm4Dj45eTVeCkSCXGx2cpa21ucxd17P/N8Jap3VzkMZtckbKB4l8wh2oA6LBVz
QutJ3fWrDgHRK9WzgDPk10sVOpKH7gcTNHKyoZX+2r2GAnMKfQVCS4tZc//BRsqATsQ3tSH7
J+g/P5olAYuUjY1LGhbl36pvaH/L++h7bZ1zIy5db9JTQCXvKsOlG+pHQVKjfn6im+LP9GVB
Itbpl0a6U8QvO6f4dCTPbp/HNJEAlFrv+HfjBztb0Fpa2jZ+lchxNIyr9AmjE65Z9gmjE/Bj
a9qyzNsgblUWsvdGaeSZm+v1zoj6r/ovV8JLeOp7vukCGK7I08PwNqxBgj5uPrr/TR2QnNTR
1cUlBW3+YG11pCC68KGSmhVypDphu6SmEpCW2HMXkDdvddJTf+B8NXqpuhRQnCsegwVI4i7K
B5kANdNWvcm07c/6SBWILja5v2Qu+C0gpLX00RoebYZm5wxLHQG7tmfVqAz8sl379KhoGTve
AABVpaSx15K5sdlVEX0+58Lx5O3MI6WBPh/zNihpiaZbjll+CiG/7Tic5r71PClfUzkphMIu
s7zfyMf0Pujkzm7kPbjV0IPSXrg959pRZBaxP0QKdruTkUrva9rxNMZa/Sc4CvFqErGF922y
qEn2oUxkDgSI5TrapsKfuSnNGF37dp5TORH/NH570ue7kjiXuwXeNKUltSz0Gf2Uu21v2lok
UuNI5ab5dMH7bjNIuewN/77S5G87UswAtR1UJDPledJloQajtjGtIMXpSqBUeiLUYow9n7d8
M4dX5xbDIHHC7NRDcBUEblrt8+MbK/wri6dQATHtGUoWiUr34REzKOnDmDWrUwr7kvExW5WA
Nx1VC220lQ9f1/mxHbeBBlZAzDvVGtFF4ZcIekbxkmGa6ibX/MRsTzdomTsp21EIjCc+zGfF
JXBi0kA1eHn95TwNpijhJrDsg7Uexog5mC4q0LNMfoV87ZKjdRHBv47d0p9/L+FZ3BkRqRGq
2KJPIemxEdLJ+/DU6MAo4CEFQznBs6OrB0IyOxNCEVWg/PZ34VwTiexwjXyuRrmW2aPj4oSg
hRbtFGadS6yrJOaoCijjw1C26vESGXFkT3MXoddFpaPjEgHdEi25AqtNiY5DadsFR3+i5ORX
Mf+TkrOd1asRNlRRMzzBdX9Twi45GM1vAyA5iR9uXL6y8mJidMLYOndfbYZ/ReAJQAlOy/Cy
qdzge1THR3yp8GMSbq9iNTmVfG1qjQbd1tNnbHxXbrpNqb8/yVW5umgCfZW/hTwr5ORjBWJ3
+VvnZn5qlVahe9YKEt/Q/ei5xTOXqrceClAhgGC76Xys7Efe8fRFRvaIWNF+/SwLi7X/pq1s
t+OvS8fbSSx0z4CWVmJU6eB2SVrd8wjYR2j8VRUqgRE/WeEMf4o8YGGOYylhc5Hjrn0dt97/
wSr6XzTvvFEIt3Iqyaw/8duO+M6HTyFC0fNKRIW+MP34R1w2VsnMh26XhnuWQF1RHJpKphmr
wHyMd2ILtawqKMh552yPVepTvw4hRiw8g/Bm+sDO2sVCzfwa04oWHdVCSEiolg3oIm6MA5v6
jPn7nfjvyb39/e8GWuUDUqJsbm8ac8t4iVh2vLSvgZps6stbMbB8ICCUlbTBQMdXdepvyclu
iNpJ2YGOAzRf1RBvT17Zx0dgt4yqRdFbnpJoO72DxPM9nLdu4GtJMG1JXLppbtnb7LJbUs+k
W8LaSIN9pn6Lne08pCH0AmsUqGQQ2nnwMnxelryFaT04ln1kwS8j2ae9wO5QJD8amQ7ItuAf
TuPC+dJnvWBmktcD7jANlFi0AhC2CbU2A/O8UfiJgmsN71drbiU4CDdMLnBXPBdE+sI4T4Zi
qH5jE98M7pREosQM5hcJN1xD0u4eyF3e3PSBymlAX7MggrB2U7+q6HyJSrcPkO0I2nSW+yei
BX81dv9G8sjmZ/viFCahFye5eUwv6J3ekwi+X9h419DA2loKtfnpw+gJU9+3dOXVxc7Z+46q
G86rdGRPI8B4j8wFnWNcfc/wGA7MeT4qxDOx1jpQAePRzGLT1tkJ5aZYrrtUghA4eBV3Kho7
ZVTDfHzebF7/qz7+k48KNYFPS0I+TM4/KQ3w7wYlkVcGgu+uTZ4+E1rf+HGLJkERohe5dwYg
Q045XYI+D31COvP+0eKVokTZ6XfhvBibvPKs+ONLnFKap4neaAbI6t6FfNbFJPWGRa6reuhb
aloeLiy80wPQGINadjtvbL12RIIqbR9PsbYDuS/NJPYRq2wHIoC90QWwN+oEAHsjdnOfEpwY
BcFSyzMpl8y1U2Ql2qKIe8q6Zb0GrnRMnamv54uT/VvXBOV8CPml9fEGKsC9OQ/Yj43J6fpZ
9Fcp9FveW/tFiN6Po+A1YobP9gU3q5QQK3IrKaSyqjYgY6gbxjKwJhfPVenavTvWmUpxssZx
UvP5Y2feMTmpq+yI0V7+diXk3UUZ+Mekyd7QTNfVmB4yIz7ZtPtOcYg0lJxS+vHSov1RO730
QqfVidYO7mqQVtVo7VLyW4oHHemfSmu5S8J8p3cH/MNqOcdtRiMoz1tyXGsLWnyJKGjciPPL
KxHfmmlx8UVZfNPfyXy15S+efYmiBiH6zCmE1ParDpuPS01dHtjOI+i6mfPq0ygzY3B9EjNj
VykhYTmDrifeVfMaIG3f9jH2ODsxUqPMqUyFtwPPzUX93a5PYn8ce+QUMYnP4KvJ8Vd2H85P
baAFq9zWO+Nzrs4/RpbbXAWvUo3PggdMFLSddp/yOVijADZtnhybH+aQ7dIjY70s79stw6Ml
ETXyTDUi9sQylG9xdxPChNNDbQBT/etRd/mSM1Orb+dzIKaivkFcD3eaYuOdrluR2upFl97w
8F+uGA8F5ZEke6NPBYLxzFxYGuH5219VzO9w2b90siGmVyLlvmMqr4N90HrmGCt2/EtAvkJf
4OLKcHtDOl4FUA9n7m6X055TORJxqz5Y7br353wfdn6X/BzYgF4EdqR/Oxe/sS9Snr3Pobu6
Lz1WrLNP9fiyYybqmBhQkH/8T6b6v797OjC4zvyJM5fw68jVxnX/lXSDNNkV5SLaK+qf5s8h
SqIiYwJm7vt1n0UONrKVJGvi1uMdRRdk0LaShoRHXYegSluuiCt8wiP8BflQ+Pi+HB8krqxz
QoLgp7PsimkxX2KOV/mAb/w4NB3eylojHPxstsoEvMEX1NEFBWXYavlU2LTW29vFEPcRsU/L
0451PSU/ABTAmiA9d+v3UZFdZvnEjUmKjgWslbBMoeQrMEc7EWFf/Wb0QTl3wJ1s09MRXP/T
4NpDtNLDICVtnVGS8OVwsQlKPYAXX1c9H0j1oq+3nQxbo5auzmT2bf/p+BYUEBGucu7K6FC4
8xBeedhTZS6RkI3v3ekYFAudjOYNbAct7rttpRowFTj5hICoYzNWNN20rsqjYVPiTinBmZfm
0dIzCVYenY3jmmyU444qe0ScRyY9n+91PKJarJ+u1xndPPaehGNNUXT1ZVdA4bYZMaLnFIrB
+eH5j68YoKQKJw4tmkHYnmSZHPV6V/dI/FJaGdt17flxGpg5xu8tJdqgYW6ThPTTMifQenrk
jD6rLOKl2TDUqajswzSHpShZJ+MeH+krdJZNcIvfeo7VeK8lc9WWwaeWNzFQ9asqvrd4zMID
oPSQHgukEJC5h1xe3wNWgrNnEmlaR/U3favre/pIxwGXzE85UxJYp4G1PqGyAzCGy0196Zvn
Kh2Na2uVamLIW7EjCMahSuBGgQwOHdN/psBIXPEhZkEfhT4SY15O2knSZ7Co9OdAiGwX433d
wAJoRdFa9HnC/DeYDn8UVltnjLzCrpUvcZw1bPOgoN8GTQnOdE9vl+GLx3pd1zLxOdIb3lfi
3McTjO5SdABRKKh9ObtmxSpviwMq3R1AX7/58RojmDRZ2KE6UKWybhecFPb52pi2UEnrkMF+
UCjDt4dCD92bN3jY59Mzyyur/4YKz64HaoEGgA24s8v9/JvpyCmbqrM9pZQpRCOHhtIbxCHu
oY/+izfHf9CeiHX+ZEQ2F0ieuvKFCod+0pOtV9/ZTQ37nPV0Sr3LG5n1JBer6Fpq1B1vUAFK
u3s3rYU1suBEoNU9Ayo7WnX9HmzbT9t2RBqEL8J3hQ10tVfNQIK+FLQsg56G0izEUgkgbwym
EPU45vNe+cs3Jdd/r3O7LKyFqT9uH9n8hr1m+B113RLVHY1RQ9gnNe+J/b3j/402uTsnT6rJ
qc8j4yHPktHKkHY6tVfZDXk3ewkGc8Vp6/TfC3BVqvslOubNuhG/bVSqMN5JFAjod2oMeWRg
TpSTViqmUIhVA+YPxlrpYORvO0YOeasOE3DBWOiMV7FNN5zAxh7U4IKwZ53ezt3WlyCf2C5E
idy3A5cxX4Vap3g+bM0M17g24qI5Tbbd1oD1pbVRgHoXJjxRMieH94+dFMVkWxOWzjyb0zzj
lHWujHH/WYSt5KIPbktzfoBhdq2DQx8v6ZbIGdT6dCudoyO7/NRre3MxdeVOj7jSlyrmRCEn
qCE3RyVxenUOah95OK7BrrC+KPJFcOt7S+NfZ60qIcoABITE8iADHJeoCG0EzdFnc0vc7Tpw
/aqHLkh3j1n9if1eln3SkHTDgSoHN0flFqJ23pID+tXtbJqGwnxah8L7IWmlmN8o2Ag0RlB1
RNRrPw1RjZw3PlSMOTV+rjNun8IfPam3qS8whUWT58I3rMH9DPAMeX437Kde9w6ZiHVpCZ4a
xI70e/yvXrV/pxJ7z9E420lP6o5oce6TcPHZqNWEL5Kpd552Mos0ate4zqgq/SKuikM3spSI
KytaFrCRFf6nf04BWQUWY6J0oJM6scPQBMe+XvAZIjQ6Dxcxq3YsjSwq2dbujOWElEx9NIQB
xtvR/G//edf3jncAxQbiL+RjIhcN7tic5cFXfX/bwUcBmnss2Ix6eSYiZHVywq1PeU9JF/x4
HaSM+bDjjgJQCVjfbD7W9JYyTvOBHqXX0aEvnWIzVo2piy8/OPIxeY3vaDbLHJbPoSWHTdiu
W4KUn2TfvRNtzRVKapO32IPCL3F29lP4mtNnZn3CE1X8hVB6ohPbhIqpKRh4vugPEEPEg0NH
DbdTvZ+R62Onk6sG6CLC7iSNulAJqLETgMJHoJsWb97sresHyAu6qymVb6ha09LkremuYotT
7BfELYC9Q6QNPi8YAUL2xa7sF8s/Urp999wx67RbJRv5YB/t/D5wxUyU6479KiY7331ts/vQ
ump+YIV9pVKEup74VsX2rNDJEutjNeAhGet6qtKCnzwx80gMU9qinoA6b15PrWW7ZX/D8wBR
XqxNl0H9cKW9diGedHiq+AUJFzSxN2Afyd62Lss4vnfXx2Pp9UsWK2Kjns0oX2fXgd1xT5ZT
RAc96JCkNaaFI45lGhRaZFUy9FF13unt0WemyLTNpvGrDqGbkJGuA2l3ZZvOmXMA6LHz0gdA
Hpy6vA2ge9u043yvfbs4Kw3QQsCBIBrFCFsrz40A4qaPzJSbZ8ZIop5QLLHQ/nzLG4DAU1cR
L7uqcpvQHfrwmVe1T+egwLlzgYMq7y0b7kayUxvSVJIf7qp/X+fyEVLiBjlcYMtb+RELuYzO
MP8ksS8g2r3TZ+0jib7Gx48LXw3r5qLKigAMwnp2fFhyrqRXK1jlJVBnXjrspjoXDbDziDr0
6Q0/+eVNGj9/97XHCxl/3vAEnJnZh8INtdNte7g3iGMA6Knb8Qt5UmeG5bIjUzWY7oA6Tsy7
Kzt65Po/n6//PUdYRhsbn5r6mJRYUwGsbQwHmFaYchHrNUbhPwT1Xavi0kPX9WOWj3jfJaS2
ONz8pXN86eH+dd2MzZqF93mEGRs/hY7Naq+03SrU2KHx3MjeMc4wKAeBXt2+wel8g/2lCRDj
rXn6PuMX2xndAt/DM6hYQEs/vIkAMJboodcv1JU4brsvVfDQ++IWDVwAEGDlSpi1uGU+7yFs
Y/jiQK8Dcv8QsZQvuDaYB+O860La6bo7sZXdQtlt8lonn5AcEsmAa0qISVrgooM6wcV9aWST
oIk5eYvIWKcxD1PXJYNmcE4pp3Lp+2ZftdTnxIXjB5yKLcwTTSGJA6sKtM+xjpYDzTAT+7rR
7h1PzJAP6xem6TO0rDfOPueE9ot9eCwkPWgwI3eKsvp4MeAXUEptOCwJ5/qnhObCaDsUedl2
wKgXEEgX0BH5cq976MjLS9CO5vxAbOjkFk7brid+V1KfaOx2zFndiqbOVVKv0gipEK2A53Vs
+HXHk/PvoVH2gLPZtD4dOREVpOROd8W3ToYLzY8BUsKXiOxPDJy6zqWAn5HH3vILLDh5W5iz
93OdOfNJ7k4DuyPodYNRcHWhcd3aV9Ur6gBmyqXnVCQxZYoxwQQykXp/nM0hCVqJWQmP6gvQ
mi8x87qzpJVUFRV/N62Xu1NIK5UTXeLaQr/btk7NFfQi48rnEY3JcVe7V3d6h89X2OJDPaYr
Ln5Y9bhhhgruidV42GkHKBaRmVpftxqkqJXd+Vp93tGytiC+oTK6VLKlUTxjWe3E9hGggjeu
VFRvR8ou9IibOpBXE0OdYVMZGwSFJr9v2h+0Goj33q23E3pMs2irg4MfDHtFpPoDF5sdXFmm
sKOl/v4B9a6J9zD/ZOrvvzJzvP1n2+boofIrIYdAfnHiHyh+73TTbQSMeJ7SRGWZWEQwDG1x
hk7h7yOCpk5r+YBkdyvubAZxhpEsgulU8mn6hOl6KDVZ1QwwJtzjJeCyjzXEOl10Apl84jvd
e797W/1PRjDHORG2N/cBSc8i++QY16YwquJCu729zp2B+Kcuub+G4ILQObUxx5nDJboh9MGI
pgSbJHlbQLFlmHw8feaed7Zi7KXRwYnXjbxadmO5WiAXkwEnc2M3ETTb9igwiQJHLHpVIWuX
WlAGTNdU+4LDtxoUcrwfL6xTkjwnhR/ozeGU+/F45q2L5HCouxPxREATJQ66Vd4Wurx+9TDs
RW3cc8sIUnLTyHzLu/iuvanKYyHqcQU2UEA/KYQGMTaxE8heXwCuWPZLGlN+sOpVeW6jjWWc
sI1v88sz9XkoKNSS8UgfN0MR4Gv7ljdWvgMrZDBXAfevETrX/6qoSVBYxqDCAzmp4Exbpvks
fREyc6pk4rObv3sRfq/x38j9P6pFeHkqtIC3lFT4eK6VSQ4ZcIkrz6dFnYApHYYfZ43PMJw4
EBXIHI6CC80WimWHCE8++/Bx6DVEIzf783A7xWCeF3Np3x5cTHRw2t32ToZJjO5vOxCkQG0m
r9cdamKnHogL6HTeNQGMxh/9AfZ6GTGfWgdIsnNMTAaOKsdPjTntjXdIpJeomiNvaG4kfBIJ
9rOnrV+L3BdXy5gdXw29TN4u6TjbzoIoDga49OhcoIyWqBs5b17YF/Mszns8w7kKJjDSnfGk
uYFCE9ExdriSwY8fygF4HYNnzYtuz7IwnPaSS7PiuZko83z3HMDHbVSaPDRzQC+vru5E0rpq
1x2fpZeLqd4mp57Fy/j9fGIBamOjZqqJocXeXS9gha/xcu3XNF8Lc562pG6X+bZzioaW4/p2
76y1fhNzq9yTPIhHX5syg4FCcZg7ZjxX1kwGPWDi+gWrlB+tpgRx0JKWI3HW876E3aoLsT52
gHj7QEnrGBeemnjEuK4uJ4INCgSVdwRSQnU4xjeseR5Bg8TeLgf0u4NtSadEsxkmETaXRiy+
iDsnEpVVRE24gFvzpehAAbGUkKyiOzTt2PWBhn4rWuCffzclNZrRuLOHjDmvhuRJb0SaDmbY
vr8GQ5afQUdy5QUdiaNxJ2Zzj2OjjzcudPy2I25Hraf9mcJujNCkYknl6U/eBGLJwXDBWwBG
XJ+Rsv0d3CuCuPdAZTDJIlWTblQCcIchgKq/P/B0hW0PHTMo1yhW0/dEOlqp3xaN2lGcUWHj
M30PvCirJzwNthYMtuyf+unUeoxmFn0ZGMRTXE7SyIGmEQSSbsBEmL/RmqqHRwrNq+d9zeNm
gpccRCOoOoxVK24S861HnZpR8stw9DaZ7y0/Mv8wtXMdqdr3ptKv3w35tcogqLBk+sNoF+EG
NgOpUw0N5Jk6JLvtmPsvJtwfTcT/tvaDHFfc6dFZG51r8wZxngKNM449U5ROmBUuhdJttwl3
vnmTM3HyYfm5UIpJrsJhuM/bfGrtQJ5pLxBgNYMiAMDeXQHY2uq4YCWRZrRj6lEQG3D6GZzc
Zecc2rMr84O1S7RrGZ+caaQVqu7MIdaDG/CfXC5Ub8AfI3dhqrx9jyOs9wY7MT/NzLnTtKv4
VnQ6uDWtcTF+dWb3vloUKEyA2xC7/GRWaJ29neX0HQ0PZm0kPNt65eYJpA2KP9naVjffLVGd
3nHxjweb0lYnM3rRydcfm6wDfKcMld60essgvKLJCGmQggeC0y24+h/uEjKVFZjvcwo7Qb/t
+OX1yCN8udfSduENIDZVMs6OF/oFK4u9H8UsvWFUWDiN6G5zDbBFZBYrV20WUC+ct6HBTCRy
0riupzbmuFPRMbL778svyaYyy3qP0TRZdaGyfizGRi5Ho7QEjP5+bjp3jV/exw7qhJW7/vCG
HU+grpwFw5Ifl8f3fsIAG8R2k0P5XlEwVxLr/Gm6A0+y/iis5e2OiliFGts3gFiNQGA0Ml+M
1XwZI/8B+c1b6TbqWUblxjtvTRMqrI8sVOcYmsKUjCeMRuf70+5KA49RFNAbg8dWX0fFYmqS
2X4059lNg1FVza4hsItm/QlcwCDuo+GqbGdk/BDc13ml3V3As1AV8XkwEBr16FY8oBO+BbEo
Hs/f/YoPpJgfFybofshvEao2uYFLJh/p+hI0t5m6nbUEzNdqSg6T6EfCt/cjDn43KXfHSmYR
wDq0tlEsz6SlRqkB2BI1pb1Qbtx54/skxKH+eJJNU7wRNzofi8nP23v1j2auOlDhy38D9nqo
EEk7sYWNLjdQOmndvDLAUA0pWVdqQSEdTaEjC1zV6HAhMR3t2uWGBN5oXex3rVUUR7X/WeN8
hvV+fqZPJ8mzg8pj3vcOGI9fGKo0cyJREkIYyJSBr1Xe/d6Z/wfjP3KH1rOj6lblrC4IUTW5
hb5GDAaxsPJXbzrMHe44R0Zk0Lp97FAGxaDM9Gmyrg3M8Sh2O9uWHRDx8ttQ2yjBIWiCy8hW
elhIVHTagjfvVAjZNsr+jPtAlZpuSF4Rz5cGaDLuNLn+6UftT5hRqiy+a4tbPO9EYu/uOKAa
NwBAzIxn9j24xgNCof7klJlfFZe6LVK839f2v1xL8LuN18CG83tGyyjVnXMn0kNIedgg1uHc
ko3rzpG/N0y/1ybnB2lZbotz5bf9tmNMtuf1ld876D/bntuuLHYlJU/cSZQkHzjTg5sPtOjw
2UMOJeHvl15z4BMn2GqJuHK3iZNSMXi046Yx6rtI/aKvYw7kNoH9VPF1Tgeej+n3ZlQ3oYqc
4RHqurq2ixDlcW+JkhIkXuz64vPa3zv1ziWfWC9SKLWUhEteMgETd54FHtiRQdc6mhdHJ9vf
MV1DZCUVo/5Swvr5e/KeAPVwsyzANbTg7UIbOhUqvAQDYv3jNwsE9dvR4dWLLDg55nNaRLc4
JJeKMNu6bWgBcORqbIopWF3rPeCE6sJuhoVhbEsi7emUmrgXzgCRP5puVu2osckoZ39m/Azm
8X54W9ZTAUidq2d1OOsHpgyUCwCB4R8MHzF6NWLHL5EL6e3UhzdQAaLQLkHuqem01ZBiUA+n
bd+1Z3H4SbYb3af+AKOh8GTTUIOvec5Dn9iWynUqLBZYCWMWdw3MCF0Zox+o3kRLru83TF6y
uMBwL4Q2LJmDugesbXuSTr8ruQt2WsPDPB/l11rd/BB+1SGpmoDbLiGD2xMXVbcI/jtob+H2
R7zIg2WUSCwGkYBY4sZEX2s265OI1+vEKk7N8i1hsTkiJz/Cam+QeIv+F0tnE7VtP3W5fl8G
fV0v5vPc+4p1lk8axBbq/nap8vPIa63SjW5Yhvv2mprGD1PhDj60GN/Ji+Tyxm180EFEIiJv
+8PE5Rj+GPF01PLLtE3GZbpzqC1k1M6ndf1489vXLSSMfiUlT3Y6qhqUc+RhsDSEXhoWHuNN
zlsScARWsTDA04wSO73dUWsTVMLRtTmXV3xuYjXc7y7wSi8hPOopmWhjRJ+ONFXwTkINMBTz
ayyVGoR62to67T+FFxhY2A5ii0gCV/7ulLRbP99AnLgyermFDgom8mqJeWuPjwz/3oz6/61t
jI0N0BUMvAU4ikrTpDr/UsBr7zBvJxdpkQhXs4jYE29E93ZNpLjxa5NMlMSrDOTp0/MKjlZ2
ghpyVelHyYs5rnd8Pnd57RVllAIKzlv7VXUVOu3Wup1SRs94UyA2L8vujlGLmoHBtOqGqHbv
DAfLuyMe1vPpJ6eZnDTrBOxUuFvZiDfNiaUy2hmz2LMPXVunKbbFDxo+7bArL/Fc2pwsppcH
wuyFXuxAnbnTEXQLBzv9UT45PkJDSiqLtrtd6Or69hWwPA/lfoJKTjK7W/Dl2p1w003Wz+U8
56Ty4Vl4MBkg5KoaOrUfpScJTWXAuoSibzUskSgqiaWMW+XTvbNpWAeu6gvdCppAM2IyoEzv
4Gj9CYhJHgvUZd/VMbw5QGp0YviULTij3x/kJ0uXJhrOjTn0rLXUm24sO0XoUIcvs1Or0TG5
geTtbxMM474TETnvot6Pb2GE7xEbtS/kq8JX4kUnz5BwceDU0PnDJVzrR7cQaZShFdP+je8Y
/DPlLYe/DaXI6oc/dH4IX5X1vY8GUkSY6KroZ3fz1x6rtfuvVAwjKxwzvL8fCVzkJ1kg0pGw
EkFLz2K5w3ZdKO6ZIA8bLeDU7s8babETPIlyIYeFF1mLBclkqltggU/gBAoyMw/jNzgqT3Aj
2pw7GpNFGZzJ5Ztb/698NPO+ipuPigPX3ZXoH8DdsfGP8/EzTFzOMM2Ge93TXm15zhPRk4gu
g56FYY6nyfB4mCo1iWiH8t/070hYhlro8eeV2Y5IUxg1cikx0gDWuXg1PLPNjKWbkauNWAHB
uwbpjnZN5hI3lY4tjwtfP/vHs+3Y8Rkyrm47Z9Nq7XzqgucNn+XIFeL4plEPZilz/9TvHf+v
t+38civCMgu21d7g8qX/pJBUcOJIZ1MhVuu09yBD1ZhCiCd89VBxHm4nkDux7rnQNaSQZDGQ
BI8s0bogXP1I141Ikox97LUtAkeJHcYuNxcNzt0y/O7T2TUPpDq+EtSpFtPjvEwH3/CiTv50
lU8GLBRqtynceWOZ9+2fdo+7enYN37HT0DgnqIrR0NGKuio2/L6zjhRSkJmOHG5SiV/mqs27
2aWWpUl3Pv/hX/1N/856efdlzZGfmGUR4dhX5Tb6orJYZ/1VUImjGdR8/uo4DPYMhcA6w5FC
Jg+tOPIW6/r8cMr7pVuxCzkPUmiE3CzVFZ8VHzTlVLKvkfSjdl7TXYI/GOKYzkSrwP1q9tf8
Q4d3vuuN29oXOm1lLZ348Ny00EQhjZmDL8xxzFANxgJIDao/zh/MuOefqlpX9vHOm43cBdPO
IcLLOAMVmXWltFmPbOgglSjN4GlelT52Aj7De+N6w7bOSs0o5ins0uax4XnBu3DHOO5MVoyR
9Gl8ne22OjHD93t8HErXP3Dcqch2+17ASzoHC94M41CQ07YwYULFBMysnyt9tPtQwnQJ+123
Zfw021hz1HbFeSPm6KznhE3pXs2KZiSzAaQ7mxvOW6LTAx0FCCanCuL5c5vNxoI8Nzz2nuiM
b3ETORzMpAexIxRKKsZ6AR/Y8onB3X5BRI4ZPGQRzqr1CUwhr4TJCIMjP4A76d0G2bLL0LOS
0Q9vuMabQmrIy2dd1NRaRmAjZk3NPnzZmp8nM45JjFEsC+rLy5bGChkRX9YSgpbb89X8Ma/U
bCKWr064/tharOchSP7+w2iebPawJ9WMYoYZy3KMkl5h1Gk5G/1gavDhRfjCxcFrs77pVTTW
2S2zlLi6CpnV2vTuzm6Z00TQaTwspKBuYVTYbqLixfTtb2DG52MdmuL4OOYG63V0dSH78ZT5
8eZ31c4HrDuNB/CJeT2XSTqCdP+joOv/cG3/NzXMjk+vHb5vOjFyia00nfFomsJu31GcoLXL
Uqs+eYN+C63llVe0aJ092Pg2jxCx3B4j2l0xqGnL+HZwCeLJ3lGz/Y07BxXkRN3OHUCjjdOi
Ba4s42/3HWSjTn4cqlgv0QuIAItop5DcdUfyixOikX5CxFsB8SQMND4o25lp6zLF6tjTR081
ue01FipJRptPko0BOQGPuJltUroRJB5jXcHd8Rx2SVT8y4k1asionsJi2NUEiXNvzFk2qlSK
Tlx4oScgfHEq4qZPSGLOY1jWr4uiO+uYmQbSMXqMR3fgtzGj2naoifggVgbPFS8K+ai8fvqr
ejlR0KPtAPHY6CfCSs1Ke09j1w2ytAEIFzeM4kJo3lLWCBbigWA4p1w4Wfr312rXo9GiV+/X
KA0+3AYfRFnxvtiQwyjI7H1FM8+MD2SiEXRopafTzR1duePmYBFzFT7x247CzkrivKcRoHOL
sNLQ8WomE1TchWy/+0SeD7MxMeZYSz7BwVFpLum1/ZW/P9un7X+Vbf57//tP2v6kPMNgvqDb
WzPpLixvWED4lRDU2RONqzLORa9WMrirNxr5Su/gz3gbrTvJxgM2cl/qnggv3yf3A30Qzbmj
BcpwG0zJl72CfTrL4qrL4oCNxo/MCokP99fwrVMdCQw8OXCgqdKJHT3h5pz8uGlQb8V1fPb2
8njASES9UFQaAFN2AQ28qtDWl8xx7ye8HeMpTueT5ja4dld+6lVF9S4aXML3HTk04ptFN54k
T5XYe7F9n+TAtMqpePckm3iyFA2zCBjaox7ZHr6k1AIy6RtVU6ih0hgJ2UhR8WUW+afpnJlQ
68KOPLaFhIcEpGidHlBawJvKUFfaFwd+uf5Pxub/7P439Nf21Nf79pxKeiViw6t+vdbE15hF
979bOLUY/PG+epxacEPlfUXNjSbLD6UM93UbB85jjT9N45AKWaTR4HVfw/owWw3Vxco5fnbP
AM3RGGLaiFYE/iRyL/5PV/7zgyFbPSlzuOKkp6H1kFrtLVKwsi8J0dTI8BZ2tIuNlcajypvg
yEaIOxDK7IAO6pbdXbppVgugBLBxiMWcJ9FjleFTl3iO7tAKpPqx1g6xMb8pVDUfbz6TttQI
aNQ6o4Kv+xflVjIEogq/Es/MA+JG+cCJttKeuH1VQT82UuodYwcY8cFNVXbZUrE0XwwuK3q/
v3bkoAMrwaAVcSRuVGq+W3MSOY0OAEUAhc1JbKKkybTbHW2sGopFnM6rN56mvG3ZJ+5jBPy5
Fk+w5tXSfZEilsdTCyamjqLy244zjr6A9bvHacomJiI83PxDVo2poc0PryqdoaFqcqqZaPNR
sCJE2QGqKPkO/MXfD83/0u0jCYtz1y4xsh4GCmctQnBGXoBwLSQWkJXQ6/x2P2wswbkIWstR
W5qbS53U8WIq8t0GuC4q4NFADFqtwXIlAdC++RjlveWexPwsClAx+XXIeFOTuD08IvRIzH0y
5vTgIw6Me4aIJ+rU8zyUeTBY0ma3aijTfR39nfUR1ordZEBux3o8dbuVzZZuHxio/Gha3hJf
F3fiRxIivZSW7w4ZAGr6tUNYQHrusQUuBJT3uf9ERSFyV8yPtyAvtZDYi0h5w86OQgZ5LWpF
w1jLEWaagItwA0UQaDA3zbGmkfy5fQt/P/BHtcoUmjjDbBt0hce74xTnEs+3jYPqsA2zeKrR
0F2qeEpKXrlWD5Qm7LRONhnssz030vVhVDffoTuNsRxmCMgmT5MyM0x90oOEdyuqN57L/15t
3/+QJsZffkqosJGSOl/VE3qpeyW/RL+Z2TSUlwNkA9X74SozHO1WfyHl7XlzdMc+laauRAZ8
+CG/z0aU6Xmy00ZNt7PT5Dy53OmUsDV7e9+jylFGFZhNTtThgFJt5RTWCB/GAke4vnp7LU0o
QAIkbjpT2JIfIS+sG5tCZKjalsOPE1yLJhibN9JsHWdSASxWRBf2qQRt49mVfNbMUsPVJRP9
sNdditVDlTFyIDEmiqB9lSIxv+ugVlj0GQ7cGNWI9Am6w2RqSyHuA6zyCOe2SiNHUB456FQp
O/quZJqIA5DS1w7uR2nPn8BCA6NysnCY/Y4xVurx/FcVuuSpJWl6dIXMkljhwEGrOJEAQzBw
r7x1UDT6De7EYMltVXr8E2Qa8ZmwN2ES+yBNimgh62iwmar+Ke+uSvcQbjz9qZ9b3XEi2dYb
5Z/hccKLJGTGtgCKqQDpfvWo5vW/nyZ/tP1vJLt4gYIS02L+LKhfVLub1x+/CKjoMgrRuyY4
TzIHyiGHuu2G0Dyv7MEpbblf9RSmBr0FY/PJ+ITA5tZ3VbR0RDqaj1/VLjh3jJyiuWkFN7i7
vEof6rvnEvx3PbM9sMKuge+vaQ5cHlWY4sZv3ykB8vqDgsahCJ6miGa6SiCSy8TKXM0ZcqC2
dqD/TtVkblzmhxXPJfNUA0+Ip+8RiAdZiKOCza4K7+ZjVY0Mo0wHSGiHpoRkmDNsvbCuuNYY
f9M7N8anK3u4InXSqyeEa3a+MsYkab4DX3XW2QmBHiCzVQRl6QHVidrBaSUNZu8+N5tYfepk
eORIFbZMEq6fmFtbStKddGH5578iUYUlb4dX8ZjD0gpIf9qys9ypysrK55Vi/5/GBir9OxWR
Qoq7o6mbs1Mw4Gc0dXCq/L+LZKVqkDd43nJnh1Slbe1OlXhsdtDFcGze8GRDVtllsWZZGlPR
GJUnAZcyIbEtSWJFu0gHP5NCa9nNCXvrl0fFYQWF3OplSnc+lhFrjbzczrUlIKaZOYH5uMXJ
/LQ8piOsG3QoH8js/lWN+wBUYT0voOz7KcZ1YqVQX/tEn7CvxvZybfdQNYraqbieoqi1+MDp
oWwIbIEgB+66ZP5ymo/mRwzPs55Qh2et7UoQJ0dEV4ZIKxnLrlWQ2I7GDeN5Z2fXAtDfmZZ/
ws2mPi/vE9ieHMWYH4D6IkGYW/gcxcm7VT7Mvh5Xpp2ffsDgvWvY85BVm6FftvD+28kTk+EU
2YCqc0cLGnNeu26OTyhvYfrrCOb2V//d7P3L5v9nUsLvfelf2v6S5UVwkPMDOQM1UXFITDyo
Eh8YyHJN9BPAoPAif6Yv3Fw3pY8scG08cOt1gKxsculn26dzs+g7mAmfTh5NS0Xd7sbPMJP8
UrgmsSx7aUBIRjf2RleYOuG0ySSc/p/ixlrAyT0xP9fq+U/BzSAWgAwZtRnUORBfAfe9pkmR
tXORutJrUIfNFZN17zVbN+Q9b+SB5bhJC0x/C88yv3wq2ZorgZqYR+tNZhe7FjfYfd/phtAO
YOMoyzxQWgkb8zq//tTUShu1g5zJEifERHRU7Db2YTldKHD+Abhn3SJUDQVAlRjUZ2CsU7K6
v2Zkdc8a5E0yotLyWkM4jTbFUFQLOsc9MQZHV8enMXyUm2CciMCy/N3+O+xO+lZhA+szM6o9
aQggTD1LPk4C6oQ7Ojif0iz3fLn0DQ+dO3+A3/YuMeS+65erjrUL0LO595WnPQyAOSUY5EI4
ZlBjVW1REimETNbj7PT8eKCrcel+dcI3W0HBl/l8bPD4mCenKg1DqaXPjUOjw4R0MweYQ0c/
y7nbBB6x22SUoHb7Xtv1P7x6f7tjZwVpbP2adYl4InVx89aV53+796+3Djl9kEPDaDK7Vv6y
21jhSG21UJvK1bJxZFSYI1aZI1wt4XeGWg4HsB5GraOpXyITESXuvMhYG3sbETEqrBclImxE
eHhu/Omzgr/+VuBzs0tkknTk5HFc2PRl3m87TPEiI86DN/w8ONGArqQ5zcyN4RySlnTy6yFx
CbKBQG1y2Z9SBRtjeDtivWfL+/rsJ4wVoyVfELYEam5aqN7BKRLdJtcXptsuKsWLoT5+Ns69
7mtXvvyxLfXHl8qR6YMgyVhuae0tZmk6kvtztKAr64bfHQ7EPBQ7VZaGe4lZsdN6kkeHuI3u
QQFFkZ11Yf10iLKbMxRi2hJM0ulWBDXKTf3dD/hfvqmVo+gOqAs4AzgLwlVFWZffOZ+MJrJJ
7a32lWcHCPWUfPb9XzuSDPXcKXRCA8SYrzq3nuzulEMOEJWlkSn3FMWvsq/JsqY3GoWuwUHB
sry1Dyb+FqodH5I95vzI2tpIfp5knApzgA6zI5og7jKrPKYDdAce4y3LH4GbaqgProw8oqkh
aMpuZSFJSpDDdddmiEFvh+hKYKaU0uCdQKRyR4DXipuzfzuM3wY8C+Qwaxk/VlX0iZVoCS6E
UiHhYBIefoyVAehs2aXqCn7bEb0voXtfohv+zfw3cwrc0e6VTYg/4BfqaMH7Tdkjd35z5W+/
8y9b/4PxxqVVhbCQuj0lpTxwsZrCyjShnBj0cddnKO8x+H2O0wESTpcc1lwZzVjPy9I7pY25
jH2gJMHj00gjVxFWMtW5AP8B6sosXY9mLuYqmcFM5hwcnG/5FnY/i5IrtbBc7n/Tzo4wSA41
ufVr90M7/dgs7d50csDrUfFAF1hFSMXp2sKa2opFlKIRC2/6R8LrIng8i3XwNh/RgYCHQ88+
rbjmBul0ukC2ScDnohMAqOKgYfdAespdickptcwdOxdRWwWhFqdOnXRD8MiBdfNwdyhEuRGQ
DicA9sKL/TqT9hStk/WaK2dvNZz7bYfQIpovGxzwcHB7eokiwmAtaO6CJZiJoj/+vokzF6CJ
FyjimxSCktgiQiy/bynnWahqTGh6pRTzoZEZsQfnHyybfVSKIzMhZo5mSc7pswsAUs39ldFW
0S8C14HkPYOCgLE9s2+AalcG3SSuHkwvWYuWQC5Jdee4ORi9t93gUrKteX0JZnFpcWovo/t8
8uB7y0WW+e6EYyVqUeI8TvaSiKJzUPsuEYiqLtdTlrZadS/9zlz43aZ/WWztM6+VJkG/Ryzm
yzC+RXFPf5L1y5L7Ef2L/cXqwjLZycHd29N6tCiAOsVMhTfTlQWC9WYKedwZUzdx2MzfYev2
N4qLcqeu/00fFHmcCnfNkz+r0VwOfFzBZ5Ejzpv46lJqtY8z04iCZRiiwxUVMc6dW5UAOkU2
QISHfGy/zoTWfRfjpScMatTeuJm627kvJCJ4Alzo+TBusL1nfq2kjZsxYdO5UQVPJIuhw8Rk
qAnMXWZ9M8xS55WvarTkxbM5O+XwUPWzhQ4y5wzWJsklXBIIKHjIZmkcJrgsu4erzFV03v36
bzr6f8PG7juTLTlUYN5VIboTMCdC8Fh5nhtx3tnLlPfwhh/pONl20LOR0+1J9tfVDcwnUnmv
vp8c4R9pWx4a2zZKYa5Mq3/QSn+m+X1L+nx+xRWI2xgRLc2oQYhds4U+FGIpCRNdF0zeFSiz
E2ncKRDM+eGtd7uHeBU7E9PjhOz4OViCwris/imAnG5XcU09EAWacFNxuvJ32RfN28SNQBb/
LVx5uT0OYhYwHR9ntwjC9OXHRwdNZJiAlm/J1X01jzK2rGgszDfblFLolXE/lPAzvQl6JtuX
tY7p/p427v/gm7JyxOEl0blh6XrPtGToYDgiYYwuzaPrb17/Oft+nvJkDL74KkxxaO8Z3qnj
q5OcnI3cr7/M6glNvRopyTH6BpEI42eWw13ojz1JDPFoifXKoV4mujJQPFA8e/r6ltJa6B3q
YmrKotMpHBJeXe2dYqOaXpq2MMhheHcOBPWRDUe9izvnfO45X9oxxr4foNrU8YzyYa6/yrk3
eqKNiAPW5/qODhlRG3zvp73GwssyzMhesqmCGmejBHk+1WbIuTUDBUl/mcDxjUAQJV28Qduf
LY7nA3ZWnV7XnzijESa2wzHddeFz6S9ogNB8eJSHHWegL9dw2M0Z5sTpDQQWwwdcbyj8QSuV
rWdiogLd0YbxQpkgD8B78Ph8FndJQz3ZIjW/UGFFLZq87HpL5yQHOUSoh5gTRYkEs7arX4a8
QX4eWXwDHV1IeROe9jScZU+z8zA2xBTmwIwHDNgo6upJOL9zlAGDzt+kfKguMEx14gCVD6bC
hp4o6uhVr08xsnkAXaskaWw9uvd+lpfFTdu1OcjJ6M5EmSU6Vy9ENEB377QrbSXN74faCY1R
YiUR9kPjxo6+E//q7fqvP/tMVl70vohO+nO/hn/Z9m1uTdzhniQgC+WUSXRwhTjg3edfjZ+P
uMS3LVrIgbTQlaHosNEZJUUtalvaWzLg53fevPJy+K87tcvIGruiy/jVm2eVPDHkh4spWxyZ
h3DuJHCwdukLiwZYR46zN1ML0AvIX0wg36sG29UhRFEvC0Cnorh7DVz7lIzR598HIqruVzig
DMgBNI/KoJliGlxnKvC42PvPHcF1ulk1y8mGbHr1M4jJeW6YW8adn+8E4s2N57qdoY7MWKgi
xJT7yQE7oL1T+Ncd+7/ks5fL/0Pdmwc0dXXvwjihVsUiowNgpQUBAZFJGbUVqEqgNIR5sEQD
BAlzEMLg0FYGMVpESALEQg2QQBAhhBAGFZAxIIYwhSQyj2FOmPE7/lrR921vP99723vf/sNe
OTmsvdc6Z+/svfbaz3ORhuqlnugxaOqt3TePt/XgToXu0muBBxZNpMTGndAaT8HvCeC1DgN0
FYRsLMzjyz0nY6sqLi77zwER/5s5PdUtz2h2Vj+QoWxSm8HQ3rgjRHiGZ1F1LRzRSYR5YdBG
1WzaN5ZvRI4eYl+x8l30MR9nU5yZC6IY6QmE3CekdLXSKDMbYyIaRtc30gXR0+iWAJAuPJuc
smvyQxfuAjFq4gLD7PqlSnOm2N+Ns6pRRa/diCY9p48kZoq5QIO+y3ME0vx+uHJ7RWsG9p39
0jXc6Q///zf579v1dr5zadbn+WBHXNiDPiXSQTUXuqV1Biz1IHNp0941uQlmKO6NiIq2lh6y
+JELqrC/0Hp4y3GDtslPpk/5dqOims+y8yFcPQ2XDGXBBTv/WZhHZB2ZDp6q3oLOeMCl/tCY
Pt1DgTJkBKD+UIVaHeHsgyvf9YO0JSaq7cMnUGvPPpOZ6npRGKSoJJDOcyL40AKBPOcPh7W9
J+Qcw6JfLwDDmixrfZT9gAcAqJSHafmdK7BvXpP/dVz711lYNfcy7elwfgi7S2pg/AAnt6Gv
LBJPmdFwZo7EENF4MkMCYq9CKCHkq91zjbKCwVQJm5JciudhHbqm3yKiPPXtm1LDpjnrMB21
Npd6ICN19+1KY3o0mUD0NYvsQ9V0X9rn+TzqE/+s6/TAtJznkfHAuGZgZPJt6gV3wgDEEhk3
xSWVN7IA0slJCMRtRO2iiGhFxIQ3LXXXMDtibAVVY26XVlqwgJACkIJN3I+ow+X6VxzoSChj
hM/uFH3q5PYoNnc0BVuBR2r0DTtQEz0Gtblq1HfIBn8Y+fiD9+U/wM76XuMJJj1niL25JXpR
qZk5scKZPUFanb7grlrC6p0FgESdixZ9KI/nP1FDw7OBmdjKxdJ/eUMTorLWTgeWhPpoJ8vv
9DG5EDjYhUPhnV/Q55Yh2P71nR7Z85fsLRfIFWt8sJbk6pqb2hmogW8wgGKDNErVMJyhWxD1
NNR5KhkjCyP8OSSAdJbXiV+1w2a2vhE5aGsZudXSTkILxkhF6UD7uzNYJNsaSZu3+0dMYOg6
YgQsUJ+aPP0DD/y3X9oEX/ppkHlrtcW/yvRH+sK+IxpnecwQteCzA96YexKS7hRtfigfYrwC
sWRoj05tEu1Wyql1SzV6aX/qKjghz0sf1mxnDIHIOq0nBuaDdJFLK/oeMUQsPTSjVLHMDDmU
svP1a78DxRbHI463XiVVrXbne4fXpAsc6d2avQPgITo6PAUz3ZNBnjEmeESwwNogW9Znbtc+
cBp19XkvK3t6V2x4pB6RdsrQ1LFQEiw3lEP6ZAIZI0QtbD05H91ETWhW0sVOMs0cUT7gwrOW
QuyQUVpkJju9zXL1253NH6jbEP++MN22J0PR7cya/GvdC30rT2PS77jR6bytAoWK/hsLIfUs
ROjroVuI1ZrKhQUNfjZep2VeSm8Mj5qvQ0edAc3S28A3XQiBocVIc9H4bAT3sHt921zgfOrV
VJcrTuNNNOlhRaVSmEk4Q28shgKq53erTodO7ob26+uVtc1RSh8LNeyQUXZ6pHvSwXxccW4P
NRZZMWN7NQ+s7WZmu3ikUmqMNI0kek9b+F+2Vk/bL1gDt+HwbydRCn8wiSqUAGXnAwebaJY3
QFetn1lJTmv7MiknrQuC86hZFrcamLE+8z1xQAqd6worlBZewfWTaiCSONsQgJd3eIyDn2h6
rT73VRf4ycdp6St1ZAFbk6CmXMv4e4GeXGq0vMnhc8pHDLktn4aZ9lq9LoSEgBLo0K9pkMhV
cKgovIrsWZmOYqFtF4CnvG1p48H9ufAf7Gic2W7HiJZxHL7g7704Y2v/88iy3bYl/NkOO91T
8n5BVfesa3sk3J8xJJR9/eOh/KbOmLpXxVzMD+GKrVLdNVQzdwRm28UPGrNFPDx2LvNWQ8vu
NyKYtUw8nPw5ogf1oMg5AKSvbFUwrzvcQ/DwXurCxAezJKR60Ga2rYGHFX2yhr9YrtRf/ZrR
t32f3zCn00ksOrnjxCSX7DceJrB0Tf2art03ZR+nVh6oXCvZIS4h5UIo/TKkiG9o3Tq/6qp8
7lnBDzd/gN2OuHIFFYBg4WzBkq1mksxuFcIRIOGTIf7/9ojFB+75D0WtaPwdK530K4v2kLwj
8bK4BV9wkBpiGCJu6ZbOGX9ebvtGpMaVL5dV2WwvCRmZYX5jVmk96avL/eYqM/FJSezcV7su
+ywVPJoEGarGZuQp6sWtpsJApXSQVDdRKb6o1hsXuVIDcc44rPyAMX5Kz3cAysngk4rezvNt
gS3jptDYWLROde2TvR8EZre72zwryBldMkBAtCCpdN1OmuWyEjYnJWXpcyCDf36cQS9Ymuit
SfDAvCj3tG15pckmoq76uT2vr41TXv+pBB1x8I/WjH9j4slmztxBT9ah8oCvFKjRaoW6pSYu
B1/uCB+ZC3rWvE3njYht93KSaUWh6V2pfGdQoNBCAanRTSzBnTxoop2TVWXcR1qiSQIj/9Jq
Z9sSHSXfEn0cqv/p0oWORevGKObQ9ghEgh625Po9tDn75fQYdqpZHQkvd7MzCzn79mex1Tox
s8Z4qlUbYrKf8JWugYq/6S6lvNEmk/xYBH/CuYAy7zQ2x8AS4jRh9uImXhhCGfxI9pwQVzCC
2Zp77e3boojKK64ryJ4OutVzNj5Ute5lqBxfSSl9LacQlwBgP+VDRx7nVVsCW93CM5B5T24H
da9aaTGzsT6DjrMPHoT2s9GgMmdhLi+rsjK8DH13/8RHvoL/wZyloxIXn3yyq2V94eWMGjke
+2KRQvFlsVukHGk+1rF31vn5x/X2EoCZ5FHCERWC4dv9v7UPWmHj4tnHffXafrf+XilqBchu
Pq38lh0IOYKNIINafqZ4tEG0JAIHg4BwYJNFeGZZdejd0xUJhAB0doeuoPUexgXOztIou307
Lps4qXH9Fyf8WbAc3akQ4Z2RgiEggHRxLEDMnrNzqtd0l57ftqthGf61F0fvvx7BiumeFB59
OzEcJfPrY9BSDeNYEjEfRiScsf+gdf8kcfPR5YrZm377Bo3aJ+T0qxACpD/1gXF2DAE75ME1
ibAQMl8XBlEL9Yh8LsJ2V+Irbdz5xYTH+YGD5QJNlRKk3THXlxo9U32NrTlY71njIc/yqwII
SGtkTZUeIG5ilbM19toH3uiodJye5uWIma2SQr7rH4mACWzPttwq1jVociFEjlK7I0dFn39w
+4b4N0bAM0sY8WPcvVO5JpzViu42PnJ5wvne0plP1hRPRNw6VWpMXisH/zz2oHy9PcId+0lW
3hdTagwYN3P5QfXTzFW6SfRRFbeHB4s56xKBWVVY9Sar+Oeu+i7EfA9PEwYusnxRsLtl4fR9
E9yK/NDzgcofS/ZLOt9Os98spCFLVfj9t5vik/lAeqo0wimrUviw3v+txaJaIWpd+tSWL8rM
q6sKzJrylGUOOlN0LV6C4xPh/LFMzqwkF31b9lzrLpTjsz5NiatBgcRVcmFGr48dtKU3pqoS
QlyrwwhCgLNqt3q2lm048c+F/yDTWHdqsJ1Y0tWmCUfsdiJOj6eeIwUt9bfo8Yfs02wtrakg
WuzCs8fXPqhvh/0Ym3FpBhxn67/Xa3hRWLn3CTHtPD0EDNlf2vGjN204Fq9nrGvvScV6DNr3
eXio3PW0AFl96z1YeKN9QX6CeaR5nSfN9xyXN5lzE9NPD3hcNiO/nwB0UkVqtIqrbRNL0uZw
0wf1/aPETYOTkZSf/YxpRF+5FkJXm06Cj5hQFPnFyJTZiowXVi0jsp4A25RfK16c/OkyKui6
RZPzglpj1/KjA+QfklEMq5xHrjNm4i41WhIyxxiNMkAipOpsEdPE6671rU9KkopP1lSl0avX
cEmD85H11/0MD8A84NQ+NJ7i7p0Sf99eysYldA5iZjOxmfSB13yW2lou0KhhA31Gfa1B8po8
ZtBEh3U4DE7LgtpDgltWBzqGhX1nTIA1DdS51V831ymDZPCjei4pxCLDmxxDVB64G3r6A32/
iX9fEOQqjifDYmu6P0+ZGkvQVO3wI1Nso745o3++Z6zg1EAnAFEGc2g/BpkyT05052RschE8
oA+eojBHgOOTDOYIECRqxDfsUml266fmTWpIjep0cMupz9aSCS5ZY3DSBWpSd9SxbPxtidbG
9R56YcneqoRHUTDECP3C18xJy1pvLP+77gzPQcIZ9/8xVIWsdKXH6sh0f4j/iglMi6oXm5bJ
TUlnSl5yILc1WRcYk+Zv7F528jtUnthc0cKcdAEYfn98kfkzjBmopExx6NBwzuzBVHo0bY74
Ax/+3qsiIh+9J75Ns0ad6Qn1bwz1uxK3Kl28fhNPtLengG6HT1qu3r+xt/QbX9zyGxGDlQs2
lOV0LlPgajWPnOJiqmhohcr6jKjD1l+/r3/zs7lnTZfTHZbCOhaEX6wETx7qTFBEdBMNFwUH
21iv84uWCOo2oEamxFAKpXeeJRKHSDlEcR9SSDnXpzRXEGp45crBdkG5+dBZljtJYEDCFlxh
Acna9B4CibUwc7Ymf49N92tl2/f1/cMkUdGQoMHSdBV/g479ekL8oL7CnlXH/dqIO4IBrwUl
YxtL4fySapl+hicDpMPlD2dL3wRw4rX0NWxKljx7HOdsneMWpNnxSU2L3lOSQ1AmN6KV68t9
iyl+SurrLz54DJt2ysGKfJz89A7Y/QzvuDVU3PS0gWbvpwthJiX7MPmLvjbC62o9j3x0EWL2
J8+RXOpwC35X8g7gOpRQjFCvKopZEICXhr2OPP17//59/TVEsMsk52l9LX6Rrds6yzy+Y+vo
deSxudaqA0OR+rrwKFflE6ZHNbY78Fw5+BvhobzATQmpLwatSNUTBhPVHfZznxXO5ABgYLrO
7O6QCp764S4L6RrZkvYCX7C4GS6YTVDsjLnzUuyb/zHpgCDAFFj0dGSb55M8u1MtQY+qx0K6
fbumhp4KIk8h+44Yl4WPTslP1KYe/ORsde3/PxrJO0d9LPbo5uo5Fu2Kr5V1CZV4qSfuaGXx
iflODL7jcrUHU0HOPsPkuDnPbA89EdOkN8/RsrTSSy6c/I5lXDYTqqh9gGiKQgdL6LyrEyhv
TuatPo8uzT9+f5r+VXM8PfrHByTm2GxIja0rC7EIbySVWeOf9VKhRbXhPpTQsetHD8XNzvk9
aHbRa69nPI8/GG9DnfMJsKy+WuF1CWzJAvhZU/BfnHUu5CoXLWmsN908fPqDyv5ZYkiIq6ZV
h04TQ8bheSHmerYDLT4JCJQROeP/Q5RnY4KFYVJShL8cECBcDYNmJZopDcFjTzQ6qjj15m6H
GAH9La80kESsKqmKXT5hWGFFi5kDhVSH9ZfoibFxNy04uGhLjjPKpB2ZlNvb1XY8MM86XLOf
C6T9BGKEAB5fLDpCPua9x2LdgDOPtyNZz0GNIHGZwvk1d9HScgyhpgk+io4LhC+dSUnT0m1c
nvr8kD49KbqBW0XNucgyBYPyLJRwwat2fTGi4PfKNqS/cTK8KlrhajpKo5wa730hdmUR0edD
Cw9pyScdPNLi9+ChC7dgHnSIA4WY5ncbhNisFFtGnYaqj9+fTNfzPRgKrTG/wk91RPOhEmI8
AKH9SeevLT5MJ3EbCym0mub2iaYFzgoK1I44u3ykVCV/b1GEQ4DJ6g1oWAiXuoh+aiLnV9Z4
3z6ZzI/UNlT1Sp/ZL9Vvow/to/WhY2Q+3bD/T4WPj2LJAhEyt4LMWevS+RVKje449kHidbiy
gAXG+ShSO/tZpp9qMX9+8cM9v+23D2L5KbMykyMp0hqokNb9SZysARo86vh5r/dNoa5G9zXj
nlbsmpJXh6ebE/Xak1AaNSTWokpdQ8o0tHMGJf+twA5If3TZLGGAnE4GD1mnuqq5cVgubTM6
h3DsDv9LPAymvhwxYe9TY0yHQJpIDwhET2pcDI2P3Lp07X1N/zRpB2Hc8xnWl9sZ8dS7pK02
aYYPcqs8tIDNUKurSsmi+p2FmUHCI9r7WyZEv5xP7lePsBp03us9FpaIsuudjOR8MnyfJuVC
Eou2qsmnFljauNp5L2gN7M9+7wbFm3kvegqSniHkJ8fyqrnMUDOOQVx5SpbyvsGGzP7U81Gn
IZz9C2JW+Q1ROY8uQSSsbpUFTU9YRJsRZ2b83oiICZ56ftBnN/T+5RzTG5p1Z3rfiNzvjjwX
HGHk1haOvt3mPTeBzAjBK9pGJny7i9IeVe00VHmWxhb4oq+7L8F8TbG7wZ1RUacAPrHKNyKX
hLzpgDOFv6k7kk+WbqJpPU//rL+39oaJ9wgNI99kubSrcz4yF7P4y/4vXkWHO3DKkn0T9FKJ
+QO+vhe+bQ2EEekMqfCMXOzRhYxmUHaMUPGx9o6N9v2p8PEdTLy3vdaBAk2OTHrIaO4ICk0r
K/UG0vubxSC6kfT5tYehpce8BL2BtTQBqnMOkWeBumxWOmRqS/HbJZaSsnCERpNf/frzDwJ/
5lNOZE3XlychhVe1CAM9GUJ+2yS89LYz2dBK/hBY0plsbEwqD4/r57zA3zZuvt2jkOU1vcul
bxKpqzPst+ZEcqAeoZEq8Dd1uzMZy10CM8fIlXAPrOHykcOfy/6pyf/dXzrcCSuxMYINXoih
ayvID/K/5Ca65RFa4SnEwbCrQfv18lp5XTS9svsrycovdzSOtNac63Z5MW6k3dhI4EqvvRyP
1yPgjXtWVXDtZevVZnGFkQCqxQsJu/dGH88iASHC/Fm/bDiLyUW29zJ1zyt3Y0kkmcr6pMOF
kXv1dZvyMDW+OFtLZ6YuSBOcgVoiBPq6U+39UG33Vx/vNHiva0P6G7HVRCuMbONx27PX6dlD
EElzfM0oa2XZSG+cBT2C57JEyjjwiZ5MrDopyislY+h5FUFVqJTdpis2MwucAayOjJ0rCwK6
ZzxjfYlPm1tDHNW7+GujRfeFRHe5MyyUac43cIlmzqYB3qVlwpilZQTETZJpMhzR4MkjbPIK
V5hypqGU44wMaOLS8+X21u25S6sCSBJsEJfuF9SGrKjbF7jhhT8VPj4is+PReCKJ4Rgh99KX
lzKLFDTRi/simH2pql5EaM90T8zCwP5zr/K/phICTQsCvSmv88H1rNnJ0DtM7TmLIz3Wnd1Z
fRMfHvH+VItlEZO8mNwMe9362CM1NTLz1g/F/n214WM0V50wnyIhusPcHDRmaNF2Wol+vUz/
xes3Itv13HfNlKW5NzXfupXlSkPgd7tVmhE9+FwuJ9QopIVue4P2p9b+d3+pkAQGBTOkmFJg
W2RKypzlFjffT6D306O0JszGS90wjxdvnaRwyu3DK6DLRF+WbdOKVG+HNjcybuXmdw83LNt0
R85MyGD8mjoH1rIzSfYET8mnv82cg6/YwUyOX/Q7a9zqJxF/6FxXkH3LGD1UxjZG2C+jXN/S
e2/2xsXTG5o2hL9vgbYpn/rtbaciq7ASnCwFRBxlMJ+MEvE6NaE6E87l/Zwpe/9LFs6uJpwI
817EEFW8tw0pdDOC8GtI8x0K0SsXnyZoB3SmK/LToqrNSnVWsOrabMZcZ3uuje1aEu3ulelf
Ldh1qtmkKTN6Nq/GteAkGIMUsloaagrEuT71tRT9ibMW1EFfGzZnYkf+CKMs6rugcyT+lduj
VGiQryVdbyL0TseTXLfC8NgFGM52IAJ8GHd8wy9/Knz8gdkvh53yEOvuJ9jWX85yj/kaXoZy
Cegceqi+Zq2pnB4/4lpi1Ll5Q0PUfcSnr6GtksxQL28aU1zgqOddabsa4orZ9n7nZLu0ldlt
IxQtTF+FCquRcqG5gocIKXfmtGdO684MovcqY8Si9Qj52U4ZLBQ+ksfBPICjpbRBpI6Qg+1Z
7FgCy3b1Yqfln9r1X/7l1n0C/y4dvkkgJRIWN+TNWVbC5NUYZxyJJfT0NllUngyyr7S94XVy
b7nmjMINwy3RgzVa90qKmzHES2AJrko56gAnVGUKSMmxmdlcumEqwInofKaeY1QaYOHb2yo1
MIbSd6opkJjg5H/C14lavii+rZXt79hKq0gz4AeAnCZZbUUrAQII2PX2HZ6SMXhmc8C1DV0b
wt/Yq7YaOyPnvcpGJvecV+HPoSxeUXbi/aoSrEyjZ6OLdpFYOAcq/SSoYVJQaGIQwshPw0it
BAQdvEBTiLhrsdWyurpamDJX/VTvUWEgrt2r3HIhbjQOCC1u/3WtJXYs12d/ScfjWd+aRn0+
Cz4oMULEZhZVr367JzLsdH3Da31TnOJZ1nDDoBf91fqremIKX/7bNfvgMSJ/4ixoFB++6fHV
DSf8qfDxO32HwcTJvrqOU93cA5G8tvlDcsCOvvHK6sDr7jo8b8Bu54teQndh4ckAil6UbgnV
58vW48Hs4LPIOO9Cj/gAhS8O55x+15BNXrQyju6VZrvFvJK8y6z4aAWvMWRBPtiYSL0XKk+3
IxjzVFzlyl+a6ZsnZPm4DJFse06dDArksrsdaXZ+IOM+AJl7UagytyKhN+m+mHFG7+k7zf/E
8oghWbqruoZ3SIWr40Q4QQGpgZka9uwWSJlzu4aNguSQ/Wyd9lcEWG9jT+o9/w41g1XXyltQ
UysMup1dgL8HZ5lKEX2fnvh+w/ZD+zsfUHYfur1rvrq7nuKK7YvEwmNjV77dEx3ud5lVfGq0
95FBkoQHv2zNwppmFuVN4HNMVVt+jORJBYh0fr6h5r3w9+UJiXya1565echUxxlqcqzJqbGz
M6CfP0Qs1S7MyF7oUwLgzb+Z48RDAeLThvZJqjjECSEqek8K5aauoUI0cTEt2tGXX7fou2Sq
EF+17BlP9ZMJm0el0SMinxUpiwmcQiYV+AmBcWW2YwZ60i7WVJljNvbRxZ/85qkDy0EthEF/
d7zxSg7AjhH4OFRDY7SKnJ3Oza7LaI5gTdYm0e0zu1OAREBYZjxptARbvKeTloDz4Jph+yJY
Nm/zAGeqnxoefu+oP5E+vp/pTg0RoLfTTi8QfrDsWF+ZGkdBu/Gv8tnP5qKGh0SfraN1tsxv
VCSbxLoASdC/t7YEbQBJjZ06YK4uIdHtuTZbS9OaYSLy40u0PH8uTgSFlXl0qBWYqNkVHbtg
r2QcN6xHHI1d7+tpqd7pvKHsHyhsOlDuF3zw1CH1XsIwsQfEMfW//Bps72cEvpcg1RQRlGBd
tyu+tcWd5DgoNplm2/TiB7qunEn6ejXER0GRMTPwtfb990b79D5cROp/e8Ul4kJFVuEvAflt
iTpLdMcs59kQ5hRIrp9794r8+7vfSbvVhjOzy2avVxZPiRVF7WeW6sqBL2Q5M+iJ2c1fkE5S
3GkwjvSq3jiWDIHEMwEkwpS4CNZi1nPZtLYpnPzOOcVnGvtr91B9U8tht5dDfC9YYOECcxxo
wtSYREFOg4Lt7W/k7wEPA2BTieWHjL1oprsoCmX9W/5oKfauSR9TnqW6uB7hpDGfG4eroFUw
WeOyIcCcD5dCqY5G4+9Leu4nNveUHyrRzOmwdc0354b68khjx1pR9gVnI5Icr1mk6NkOWpwo
/ypp8lOYK01fw7UTu7uHHKlrP7bLRGUJdWPs1zZslg5/dWWl1PSEs89V5+r4q7hb3l1Ufei6
ttrBI2v6hivt47VLZ5R67k4dilxoMN0pWI2Iy1/Uq5DHIAchIAgkWgz/rSsGM9e0dEFqYeFM
xMcYJiLy8bNCn97nn5D68m3StjgwiYTBA7XSUYiF+Ro777axxvzBjLjrH/6KPl0vNKDwDe8z
1MR40WI55TqrF/DOsrTkCj72zNfzFkz17tf5n1JSCEZhzhlcXQgqwGcfx0ahH8DDRn9cu/9L
70JHUdr7wry7FlBhozyHttrarOHo7EPlkuNTjaITVF5rZZDyIHPatG3nlvcGHFgK6oBP7aYB
CAZZv7DjNEdXkmXcCuXRTER3AYbXTxyOvn1wW6ur/lHCoAQXm6EaC2xBvx/U3unZLFHaatmi
W7oXVaEBkHAVha0HLesbMoaXIridx9wP0Ew6SlSeyh8K6Lfjphy4Y7pPHXrpu9GSTgrTTZ3e
WZG9dmIQ3A2PwXrzxbtRAJs21z+Re0e+yAX/QzeaG3A97V01/5ul4ld5651Zmj/2HOdGKaS/
EjTxTyj3NNRmDC/LHrvDbBvllMsuEL4Ito5MKs+D2gA8A7mM53Su6ficwlFFZiWO6nf7oEQw
wD5gR7VQSlVuy7OXYnqeybLCxK4hv2CnMBUku1IWr989/WvrbnOpbI2gk2FV8kfALtXeB9qR
8a5a4nPc3AKzMVjk1Dcs9vgvMhaZ7XM0Gu2rLD9OVpWhReCYAaRkapjIqaNipFD3+hrJprS7
nh8XHfzokMWW5h4nStp2gMhz0swGlGcoJnQNMokhcCRsW+pFrssnYyEM+3SNQ00OuAeP1+GD
nJR5G8lRjNuBrBVahvHSNevF994HXrSuB0cHszxHBfbi4cLlF+VmJhwd76VW21VwIP6+gqtk
Admm0WSygZjexuGd0gGb8G5t2VU5XTHyjw77iYhKCCK6kQsyyvu7awKMhRV9TF04yrrQFdIX
tn4MIPcs5OwNhfTkJdW4JtpaOgGBOW0I1XhN97JTOTz/J62jSxc/jEMdvkWCdS3dBKA9WADN
wKJF5qgTHr/iAg+I4Am+AXmK6usadtxky4SBtXXG2T6WbX2ezOUodTo+9ZO690/iN2krQCRI
LqWRX2YQCR5pCdclq1syjJ3TjDP7MUtn7Oem5stOOazdZppKvtyNG+kdN6tfdM1eG5bd//J3
mv6jC1u2ldb50rt5KrKleXgd3zVO1phMBC+X3Gyu7/ekLnNAVCEw4SSbR+jQOXQSm0HCftET
yYDIN5np8bmE/GQQ/q7s5p380XMkhzbaZ10OSJ/Y/PMM1oxGbbQZONu9nD3hBzaVPfHbel42
knXTEzqZfkHf/FHQPr8B3wQLy3atCJ1FQtwa2Fw3pJbS3Q7izk1Y+EM9v2LwAqHxB3cpahil
RjSwZo6hwCbZlKiSJa3MvmvnH36UjR/drza3BV0mdmTM0msYVoylQmRzXftqUl06E1T/nA6S
kJ+Kuyhu2Io7T8kO8iRe7iEo5WlfHttvN9xNDHzMD13SaGnY+UGUTtyxQ8GNLul/06e7PoVi
O+64MLESYpFzlGK70qqf2X/3Uv55ddEX6HqNlhYK4igtb3isa6GMQyBmGghiMOtDNQqSp098
0FE/ytL/qptEjUO2dd+f0rAsyf8FwltW+CrNzhB11T4PwMz7dMfiyL1SUlW/56d69j9GpOdR
8saCTGrjJTQ4Jejo4svun9+Avrdl63EB+eWsVlhCF/tHr5gXbXquqU6ebLqnvqrPGn/84k9c
CwrbOf6+hviYtE9cDoVy3F8JOlaQ98LYZgaUc8390/eafpM+xbXfwGRh+Z/AoMPFeltrvWPf
iNQGZbbww43v2nFOT7RCs/JV22x4RSPLxlHRiLwDHLBwYL9Ka1V7fOI03Wal+bj2w98p/Y8u
iB4P0Xp5IlTmcxfLmiqqFLem9mmbYmWBWcJX8vz6tea4Z3JpWqbTiT+utvqT5Etuc5hVdAqU
OZounIA5TrF7SCfQ92X37cwaycthJTVKjzI13LBjz3n7g8y0Tc8gyg6pxKCDaqRaag/f/c14
ZxNY8Y/m64MdsTj9XfK4pfBiJktrRp01kop5QdOLfmG2b8eNEUFZgLBDv80rTEYJw0F52rzK
BfMYEHaQj+aibLJJp/IfLVN/b/XHZlNtul1+PmQ1gVqvIKldADMimMtL40f53Nupqyip9dnB
08+tbq2Et1t/evVR6VAMrhSZkOU9z2K3WoFWqEomp2qyBraWXtuofYfTuE2+W/MQ1MdL/F7f
i1dCmG4dVSCTD7sMoCe3muXf3RdSb/4DmnrKolcMn3AWbMb5mTDcZMEa6Mw6krM4Rj+xq31D
1z9Q2BzXj2wnRUxDo68QYR55z4p1QRoYtCVo1flBH5Sz9PrLlq/XWKstQfgMb23eG5GdRa7g
83PRPlBWVPRyVs9W/geO/GU8Kctsf89B1ijFeLK7o4BEVmTI73xGTMGsT1bwZE/gHyEemUcr
0kVrdBdJT+tYM6S5Bb6pzizibGRCw5kH7zW9c+Nn+nnbQlgM5A9SEG3JiSs7CEqR4mM9o3yF
Qy0Nn4xnW79aHLQXSpitnvPa/9lf2MO25Q3hv6yk0Tz7Km7Gowdng5BuhX7yPJabQK6LquAp
eUMx3HAsxSG1A26gdIXJ9p9gWFtmYNYilq74zClAPfLvyl4geWOwSiRMJlyvLN1N1KzJeT4S
1KCKhaPjPM6ocsR0V+O7TWWKKY33BrROBLt+yZBvucM/FeyC/4nx8PzpX8038cnA3Ycg3rJN
xsa+xelyF3Maq3wq9pBu7VdTT7fj9EkxspCDQUCy9xCIYTIYNAVG5uCvHtzxez++8+eH5cdS
+RzHkYSDmV8ODAPQdWRmyYI8hgCW72FCwlwrLB2XgG03eT6xAKkvFfr9Aj9nrBuGk++I8NEn
W/cGCK8rvd6ocfPm8CyfJQOeIXtOnj9Cg35d+Ogi9GzUkxjmhAsRz9HoWTpjiFPz6+er4x7y
Xc4fiT+gh4nPAtLJGCBpXzBCceAX+f/DacpGU/6fCHsbcgilsLjMcl0LbzRiUz5aaUHt9ZQp
Ssa8TcM66RU1jV8YmHOHqa8J6tlLhbz8MHKhiM8jx8PfiGzWk+/HHkFcnJyyAQOZo6uGgqbo
RObs5p9HnuUOwI2IPlikWSdRJ288De2Bz6HYKcnxentoh1v8f2fwp8nt0R3uGRHbn65q60hV
fnNw5h6zIwl1z7LWV+HrzJY1cgICX7c76a+cI+Zlv+5sm1/N01dKITa7YidcYoXeREws+qcz
InIG2uQr6eGLAZ6OhFzndorRmtJa6XARM1wobWVkYzJ1n6zI2/Z4KNOC5DenW5MgHzDEOMnu
cCKwJOQqz6eyCxGRoxneKQuf77/eahh0qTdoU7nwtqW5Xl4RvJnUMowr6UqZb5WroCpN1e1M
/s0VB1aC3oJl9loY95xuZt+3kloxGJIfqKZLItG2lxwKMJA64RsRK5p7GLDONS01yYkle8sa
cLfV0eKzoU4NBQB8P5HT4EH0HEjZ/nvv/s7dwIWPBUuwsHYGwVl3Nk+A6Lq19xmc9TwCHoGT
tR8BDrofzRrcXt4abVHHXLLrCDkUb2MJx7H11uIqyCzZq8iVtTSZw/un31euO93Hl6hpzlgW
xhPN9PN8IhwSNkOZUv3MHGbs2QjkyC8Ht197f/c/UNoTcZIGcVEa08r3MUhlwrnxNSkd9OUj
OCl48GCrKa3ja729760CIMm2+4LJs2H3iBDLJj6nkQC3mQS5gWXWjkrjfxYOCuye9qW3TJlO
wQqy4G7D8xBcMUA2afL689+POlu/EOAFHSP4TdOmuxnboC2Vr6YHoUJty1Xw6RN+mbfyZJR7
kZkLqRc9T7+v/n9L0p3qkZc/KDjcUFdHHTOKlLjNJcVgpmtOto1rBcYuEHjeC78c4lwowupo
XL2K86jJzoinOUX5Go8CTL18wwN8cHcEc47FEj77Zv5hzwLwQhusWFtRu9URcqaQV1NNLYi2
F3JNMWvruuIzN8J/a+tWdQGh236efAlZMZkpjdXSXXsE60gCjsCmRuDme6aADAv07A3QKQXO
Irv/vpuETwlNIlydH2F8YrCeVMaYMIg8F1q2oj14zJ7H2fbBu/gn5n909E/8Qoeazczlab9z
hIn1ZD+3OtpZa2wE+CZIW2uNEVm+JPptMImZ93rW8PGsVxbFccngBShq4sWjRITyAFWk8eJG
E6IgEB2wLss4h2DYtPLNnogwXYq7bNhyJ7Y5Ex5BJpXlT/rcb1pIocEQw5HEvMiHHw7FG0r+
QcJhGaJVfLTF8M0YfZ+CgYkxW2/HYuWxUZJVLYFYGZwxEHE63TULgJekO5v3XGXVIENcTRX0
ODYjWASbUIL/6WH4ww1ja9YJ4Rrm9Lo3IhIBAUfjyP39o0sVAumQQz6Ulk4bh+O1Pw9R4S/m
+l70YPs0PL3D7Xx1VoI76ffOtiydjXj44PWGonfCv/4QoQHE/wtVSehOhvYMSKS+4i8M/ol0
AISazehQv7maaqfcrnz523QsLDJudIkn2cMsIBJLYaaCdFNT6r5PmKR0PWnrE3RUmPd8aAG9
WCkxN+xrdBoZNmSWPbdiegrOq+mU1k9UZycW0ai9JpVoaT6Dw8nqdeHPFbV6qs5DOXz+WZtw
4BSlyW9Wiid2bIH1NHamavTtkehOULNv0/G5xx7J0mDQi0LxQW2Qtfs3+MFRXDCNZlz7kpjh
nZZZIlBXMmxpBQf6Dl3N7JnC2AJn7bX/2l+arzSd94QqKqdEJhUPQduWoxhUjAV+/cQ6AqK7
VD6BuviTm9n8QWe/xPV93kKvOO9yyvTckOLYE2/B2ZZafdiZyNPvnuEm84AsIC56fPUQD9XR
sj7tmwa2nQuP/rqGFsQQHv7B6idnt9DtBgdEScP84iJfe9t0HhvarIlfpyxsMnz6Tsk/sgTi
3S+9tW4yrG5m28C8s77tOqkPz6diSfeHYDZaPHacd+bgtfPJyqWUAx2qLodbCBM9+CE1iwLX
IOMhH0osghM5zJ6xOUx/vWF84WrvqFBgYnv1WXwgXhL8RJc0o8B2rqIF4qlnN6sta4yJxzLs
KmNd62MYnUvtANcGFkgPek424vaY6UY+Bl3bUPRO2HFh3HQ8v9Vky+uo/VhgxaRbqj6/MOiE
C67RMtBIsPcSDptRtE2P1Z248Ff+bn1mnSfNzQcN3fTzKfIASesm4GK1UVTs4Iqjo629/KrN
QJTD9viWlhyqwrGezIAt0qqVbuYv6D8PDiyNTQWJtUvJHyAKV4OimXzb3ZovBWsXEJN7tING
k5h+hucaaptqyEdj4hCORGx2eiu7Mj1laqKlYk/mdOExuKzD0iKlBhnoaxP+dvyCx6Tgfzrz
G5LGbu0xXlEAVVnpwGRhVPqCHrnwEVxo3DBeKRu00tPw7DsDecREfLe+tN4XK21Luy3z1AAY
vonFKZso1lj5ZPux018ceufTPy0/dp53xt0+od7HZVj5W6Z6TxyRzY6+wPQBYGS/gtiN1fNn
L1WvXsTc2ezbLYzevBhSNGnJCNdgvtIZI0Rq6/nzbYzXq6Veb7TjmLIJDtv8amA83iBv5Z6Z
vnBw7YSSp6Ar0Upda4axiL4t3tiqj3Bv7J9c4txb/jG5yHNzNv+NyP5EjEep58CL/MGtDdc2
lP0ThR0p4wmZjgW0q2YlKhlGZIRY4S2IWxMTNgRwvDXes2/YXTkanevWHibfWxMmM8TvOR9i
ZECIdgaVX1A6mtVHfX3t8ukNs1XWPxvRW7B62sP2EIi7lrtbMJ6SgRMmfOxIytr04dpHevR7
mXP0J499o7Jye8c6ZcrWKgKPa/LQvM6HEj0bWt4Jm/cttyyPz1tfW1T4EXajbExivuIUZO37
1uh9TqJfB/91/EsiWx0ENexTUr3+6KtdtejPPCYLCJc4Qo/SfulBbNSF0OG+bdf6TJCio6Pa
z1NTo/c0leOqU/n7BK795SWV5khb5qxrwdDC9e8XNLl0M1IoosNVz3vaOS6rzMY6Ds6Xbwsl
5iwMnXmCVsW2W/UPor9f5iIsBy5fnsiTLosvNB4a5Nl0x43hkfDYyV3Zv9q+6wxjnZUw2tAi
JeSfDEoKF7a2TUEdY6Z0BxxriYIUdGiDcya1dAdxhFGaaTaUacfumB2Kd77lDYOyC3lFrnWU
aHmBNrsrhWr2RiTukoTXO4/+afmxMQ1dwZhhYlDQHLO6VGdMSTBeegefxc7Ag+zVX0Mdp2vp
fZmP9bbV1FJjE3yk25AZDEk2ATiYz/8ACF1UXgDtODZqlDjZtAs4w+Lj9CDxJuJ/zrAAC3W/
n2rAM1vkDA6OYKSnrz4rmXREfxY1GXsTNkx1Fce41i1pOC2dUXn4p6b8t3+5Wb+0h88+ZXSg
l8t/m8ihH8Rl5pCo6Sr11eRBm5nmL0wPq2kkGN5UdhjUt3k1q2RkID3T8rxAbmU92c1EHUjz
Hp7qEQ299s7MLbMeSoaWobFACvmDpulCfNqtzCHXlHxLzoJwLQQyhCFPuFUtwUhpFcf/YDr+
dt8ZIsFAXBc3HkqLvy4xVyBXmRlUnjK/MjeF+vSTRvy44FLw3KDbYIC41i+jOmHlxGBUcG33
tUuVFnudNKyf8y2mTj5t3mjLuzb9h+VFtKMxKZE8i79OhtpY+1Lp/tpPVFPmanAPArVWLACO
6RX3w8dR19r6/dIxRs+v+MjaXoY7GwaOHixuAhkPMfSJBXD6/ZYCLU8JJePRFOGZ7zlZ1Cju
xSvbmQcDeEAq2fSQ0O2sW91TarY3q6WN6Wl6JN521S6j88RvKTGH9pdcXf5RbnU3KcD1Ng7i
CEC9qGZk/w/Uy+qsMQZ1M2Llyh5tf2GmGoiz3xB6RLF1/37pqdfItVfzWy7+fpX7B9Z/dHg+
/844IZT6beRXu04MJ1NzZoj+Hp5dhQa8nzKMRzJU0DEHt7/XvkMw7k5shSbvScsMs97TxBiH
HlGJXVZVvzhYvTLD5Zt6HUqT0skHB7bSdeETDKmhqSu4YJYWuxbBFVMAImlGkI63p1Vk3yv8
J0rf7XUwLjiwoEwNcWO+EbmJwoHaVnlssx530zUvadLP68O3K+RnLGCh6ctuhVljUUB4Iv7B
G5GX668/b3pvrk8/kXHQOsfObGUehHNyPzi0ambDppTq8qS0p656KHNFnz19f/Nv0meauW9E
yJVnF/deX4R5qclHriffUlMowHr2YTclRv6F+UtvU/CRSZzRej/JIpJE95BSko99LJ9HOemo
94S05FVoG3Hx9h0My52z4ocR2w4kFF+espIdGvBYzCzXipbHPVBfWIgIm2+pOfzsJcjarLwq
9NtBdKDXqf3agXkHwy6b4YB4npTHpJJ6gPx8zyxzpk579TcLfXgMOZnFXW27ro4Lc8gCxvZo
Z05x9p1WbZl8dptXhjFaxzUG4Jp5HCLVGhiHcCaqErLjclLmLb82ufY7b/3+wsd3iWiVKDH1
EJEuA04DrIQVymLUdkNbuCw2pkB7ClRy98rh98qP0MlWBeE4I7mX6rwUSmBe6AlBJYII/SQ+
JMIG0rn47KfIo8EoA8/PUfp6LHEp+FJ3xeV6NIwYNOU4NetIMDl8+eMiL+8r/C+TXlg9Chc1
7x+Ij110uCcRqiCx3bRFbsUGjUeHV3Kdc2WtX674O73gldl2U+zFQ21e6XC+xEaWBky5Znj2
pRKjvrmQ8t6gjpZsdRJbIZ2rCPNOy7vk4ePgRMkRkntqautiV1RXbl4kharQEbgi63Afwv8i
ren7isL10jWJ1ybbezEPc8MWlt0O5Ua98MbHeYmC/kIOTZFtCi+MMw+d7pVe6AzSVmDI97QV
pc+MojUTAjuuLkRFfIp75RnCotJa2N36N2t8QrwPkNGhZUsZKS9IqoYrAuBAu6yWX+xB86Gn
ffIjnaFkSOAQu72wKI5EYtr28wD4i5XKkzvVRwJKVLPU4tl2k7ZN9n7mbVoTAAoyQGCowRKf
XMytXnm50/E3533q2b7LG+pb4T81Lq3CdxtjG8DyURwyWu2WQnnVLxK7GpETdbyI8mnmVYDw
c8itoKgotYmYg9dPzpfu4awBs7ZNAU/fP4f/pfSxPSjsYJUDlVr8gJrPJatQCd5dp5IgJtXO
FEiQqdenZ15VnatrW+rr3C+dV4MsYhtUuC4tY01gA+zYFcP7EQ/xFzfq37TH+Ap1zyrZdCKS
ZJrtTf8ydTnijUh+HaMuI3tJK3vpjGLqLd9GQ/vEin2jD9RrJLnsq8v3qy3GnwzlYrP6cUxT
Wc2P+rHcqPC/Tiha7fYO8THKmwm1osL8XOhPdGkUBEAQFpiqRrEB3oKMTRJr+0MuOBzqgpck
q8aQvu1y+lG9RDh2O9ewvOLCtx/yd396ioVHNMc2k4fasip9o8+/CpGdWiN/Icv1W36sxP7e
OY471WvSwHlANgv2QYWC2ryJypVxmlBnmsTKa8jDf/fMv0Yr5v62/V1gO4bztAH+OvQbDvWh
d3kOhVqCt+vCS7mWnRR4sm4GwiIbQ9r2amcrtRY8CWP0VSQkSEhe8kkktYStIUNwYUlRK0fO
RBicQHwSTIZTEuQnzzLNKYWFV5ypfXP24QDdUGc6t6lG0nWRcEbv2q82blZa7vNFIUMmJfwu
OBQOnpjR9dU8Mg8GKHzcjBttm96IMLkA3/DDy/kXIlvsBgeSv2uNPhF4IhiFfYAJh0HLxf0M
BHbZ60MMZIZx89OGjxrePzISIZ2JU/8yTzOpQtPTma5Hdu7sHk4kKxcxXV5z42DG3DmR2Mnb
pb5lk1coV4AM9DTTy/D9OqjEUw7IisGurR8seHccHRunZXfQmlhFpapThkFfvppvyOzG5lnZ
+yWqmnxjubAZyXLWvnHIuGtBCZa3Fz5q4As2weBOPshriS7YFvjvr8I/67MRg/GLU89BP7uX
gSpxeXAH/Rk1QiQWmExggP3NzRwNXedSdyMXw4z4OUR7iAH5i5HlUjjzBAzruVLqhY+R+CBV
6zNwnsm2q6ut/NQRipafJvS7VWA5CQDKpKVJyK9a3ATiiaZKpQnl9ve5ewcAWMijXU7mOkIh
34NNMUXEbhv4ndu+dHd8I+IaFTutsGW66aV92pdRybWqlY+xmn0XTteL/ZUB9i3uGqjpSf9M
vMZnnvxOwgsr0f7qHqSSImP/KekrniD3UlfMXZc7j8OlxbbrhkcNMfNqf+KgTEEsH7plGLlD
RrO/ekHoWd9JmUFuKx7NK1H3rUAuQjH3ony765sYzLGlyVZXR9lT0l6EyEo8zQLHnthz89qv
5opuEjzsXqBEOejsqUmIl1F7qR+l3rhgjLu6UPDEt2k1VKl6S/UIpjRg7qpEhdAzeWZg9CBZ
90Aew3Uo3tHhgRdAE3CWFR/aP7lT5nfu+4MLH3sM/+2Ed2GPM/QnsircdmEKdaEgK6w8N5cu
yxTmbwGIGvjjYUZ2fXYTuABdgBZMxopA5sbU188mKijkQAe2Pn1f855Igxu88oqlyT49+UTx
UEVNp+evjtVGg8YdSha5Ck+AUMWOQoAf0KsAnt7mDKA2/k+k4g/Yxt9r/AdIPr1PHQDOHkSG
ofvZ55TXmV/3fc/v9kbr/8hpWn483Bfng7/74fb1jsTx2Ex2AX0RlF+j1d/EDLliQBT2MXrC
+0xrWxp2N44mki75GKH9GxVVS4iD8QceKJebpV1Q5YgLJV/t/vl3/vjXXmOXutZDnrLWsFOl
2YclqF3IqqQdMBNXgB/er/UXJh2JiHy511GdCjUb6thrVwCtMrzpNbrUQQIOn3AyhOamWV0p
GTWV8Y+NxTJteZzUkll8zfkcktL6z0+yrNoKI7gRcVqPiXGwSBo50LMvWza2kdtX230oord4
vJE+UDDvy8kc5pI9i8zojg9IpEpaN0aUcfhXu7ccMLjneyxhsN5aomjVwBu3eFK2m6Ktxasy
V3JNjS8v5ynDByIuPiPHGFa8kJG4intMxMx2N//wA6l1CGCin1Wl2ON5zb/s+2AQ+50/Ny58
7KmqLXtLC+DCee45KkIupNqKlD16MtiCqoWDL/j91NRSvTtoxPfRJeen/fI015JZmSkvhwck
4TjVyhdSWx/Ia9gJ2qhQ5MCi6yyqKsfMlqXrXkAKoFcNL00KSR2oiHuWq3f33Hz6/s5/pOTT
W6uSLimQ7Clt9m3ZdsBast8fBB6aZud/k3UC/xP29b90kqrxWOpYfdeqMseGV5U1Fk7Gm3RE
xDsIal8XCp+Fh5/1EQrSQcHlBnF9OS8pa2BrsuHablbgCcMIjLiprLblvzto005jT6Osuc6R
9ZNZ1DnxrEVDlBuJMb8auf5SyyLSeejg0jW2TEmyXwy+ybKbatVFcr09hXGzrrdIvK1Svmx9
qx45vaSpf5Pqd/wLXqbtJQsVg+95RExG6IOf9TwUWyTD8TJl1vS+mQiwSPP/6Yx7k6RxQPGE
M+ukBd0XaslYjYRaVYYDyYlWuc4PcjALEY9G0eFnfK9ioIqRwRG9yEKPStuBK77j0QoGg2Au
yU6tEm8mCSDHeFj4+TxWXD1oPhFZH18mtONxZfWPDOnRH/XB7eCxU1I24Sx9lZRF4jXUxV+d
lXmSVTjWJ7Ndv/15Rg4hr7aYYqyEzWSC7GcQzrFopFL23S+zzhnz3LqGvzr9SoUAS2BljmGN
Q0LnwJL9zS4AhUZIrCVqTiTt9b/7/o8+f+SMT3ZTe6bJkL4aHSrKGc1koYbF1Aim7mYnTzG7
I1tkbkQd3Y5vNQRRfZIj+blmWv313OQAIh6hfrEPohCFv7/v/ZG6vbhkFQqCRGmBe8USPbtj
RCvKbjqVV2tEXA3FE5kyJ7RDVhnwhcJl39yI2+Q3Ipf9SvR2/1G7/0HXNuUDENTqeuX66Saf
hxbq8QetkhIRMCNWjRNMMy57fVINHfW5RP9DOJJSvgvUfgUi5dxSXZh0thag9zSzWTjD2zB1
a6Qg93l82RPfY4tUXQi6osALE7N8wOdp8xSv+848U3i9qvUrA06zM/UBRkLeKHImarWWFrRF
LGWl58aX1za0/Cb8axYF3lTH3i8LrSbZYcnUfjQagkwRKn+d4RF1TtTyr4xWiIgDvOGJCJe2
pUts1E0FmQb7jKlD3uWBpn25bjX1GZ5cXLq5yUlRjcCW+PURObWwmE7ZjlVHerQLlWakbaJC
9eCctB8uQolr3YwyObU1cgtUwyzUSmN6YOV7bLFcHZlr0ln9iuAR7f6DRKxLBMSBaHLY/eKv
9kZtcZvcATbaPSZHDZY74RFvGBQr8M3BEpcPwQvHntG0TQZLx0Sfn/715j//+5E4goqaZLHe
277XnzOy+tKX7xRkjxmXV4IdKH5rR2WgmUJuptnAnMK3hDvM/ElXaxtiJC2rvj90SSvD5DDs
9UYDjk6emHRCeu7Qb54m5+8xkGa3CVRShEea1Rvx2B02oyrF64i5R1SKqen6XiC082honX0g
18907ZJExYaKf6aw+dPSBm/pIq7vdJA6U9yOVFg0UTrMJp44kbuwdKy2bueVQSiknBzY+NzV
XXUhqTLpiY5hMmmZlHjTs9b0co/M2Q2rZX1Z+WZU4qxzSRApQyk40v08gxBFgNcTaqN/Wq19
sWv7y37nyujTfes9JMGhYwwZPR6Qp5fdmJFP8bh2/uiGmt+Et7tGINoQ9XScYtGLmqczYeXa
Yz1TyMg73I7yiTp7479xqSRTiuEDRMP1mvu0HueCQxU3vxDLsohub0WneQx2V6jZ9myNCiYU
xpfrUU8cEsdxD5VPFRg6xixr7pGeBXKVjMcK+auPd6xsnZhP4CD1ZZQM9O7ByAJ+ZJDtK0Qt
BRJabs+eCBxdOoN5/aupW9zdov01/SvxYp8N8Sc7u2RLJ+VfvyCrzJmbraL2J7rTl30bsniT
e64VrU5EWm85+G01Wa0gGRYvJAKMDxCAkrj+8MS/e++PPn9kbzriQzbJMuNUPd8jr4qW15Cm
JGrxzbpnVNBlLXW7y0ZRWRzm0oFeAIaGQU/ut6tLwcOwAksaIQqgg5+5qXr6Xc2bLp/qbFf3
cskMQOnxbUD6ej8+uiVhColi2HmYON/dUTuS88ulS3Pq9JBsCk9h+6WBLmIlACBjKOaFvoML
NTkNkn2n6B9a7ogYDy0eqekbFtOPsOkut0ZcGi20p8p2gQMVV8lR33hSrRi1hlk/NUvBg3jz
CUqTuOE3InxLUiev+qbieyfejrwQ7PwWCPObqhfLhidT9lcAWSiGUJsX5e5Tvm27VUZQua3Q
yAB7P1C0Ke6XUUyBNVVa0y3DczXD5JsLd//ddf/X8h1EpOdS0kiJFVe3VKfhfgBpJ+Xx1Z23
KNTI9Wm6VNNANP4kRKfus5ZfxCZq2WV9fV4dWRRnku9YuFk2f5QYQ8WwJ/zHRFUCQr0cexek
FgjPa6cGitt724LjDFvCpvsHeihyw11z3+wEj9yi+8L882Od9ylFEO6VaOmGZ1JxVZiEgczp
/VvvX/vV/h3nxrWpR1+dyn1FIZ1kmh2YbHlWTwut6tZwo95LhEErC7XM6O6ST7/wue9aa1iY
VCExThm0Ao2vGJ6n3gv3LOuI4upKTzatVBioTk3emPx3n/7R54/saZ+h8hCke9EY158zGc2L
iyhF+TWdFXuNYZiZO5xTeXefT71eonl8g/4Ofz6zNx5nYdXIn+QVAng0DwZuCDfq3SJZ+gtc
13s1YUYaFwrjNBGLUsNhykVNEKIHw2aGKWVRtvv8iC+BTc8LiLfHQhugHiNX21ooMj4MYpRA
4fAXMRua/pnCVidBXeusxmiEfI/0CPqzhHvk7zikFdT9XvuzEQ/IWz4rBfnYCazO6xXvkaoG
5u/hxVIBfJBjsqZwSRNI42o6vWG1Izdg+mgbzapf1LjBwyMhMXcgAlmg4YIGkvvUw48NWZnq
rCRKIyzBSQVB3nEAlB8x6DE8dqHvSP6DM7rXNrT8JvxrsLwRH4sZ7W2obgJiyeXhlwB6RQ9g
d+qvzDASUdBtNWtQpQamELF9QBy/C8jVcPmlp/zpZLTQ6gcMBMJppTI4OUgyN4woaCyNAAJv
qDoDua+ExRotwxfiSq3kSjK45gV+tikxa1EI3dTS4X7iGnjmptLykcnO533D4sLPqxfa9Yb0
8iQmos8M1OQnL+tP3rj49Fdzt9oKXrCTjSKOcNoDYF783FGafn8nfsT5gRc+en4JWLwluqro
y6WhfvJNu2l+llP+M2ys1HddEAqAc/iy55kzzpV+RSjX68nXfvPenxUfmUW04/gYsHVuQwqK
T75uFqXSiuRibtpGWrJkfnvwGDF3nYM4+2upumwZgPFe0curU8pyGUZysMtOfyMidzj/6btG
bLpRfil0G+fg/dsgvTbLF3T6/MSutKxWkF5goOHaA2PTo0etYnBRXP0dJejSjJh47J3+WuYY
iUrQmvEoQcezwLM3zp1+p+sfWlpkOe8x4QBA2TCSTu39Wq5QaxQP17gIg5iGXwuat22ZXS2Y
LDchFUIc6MOqJQTPEa/8LbuKLChyo8B+79eHN6wGJtn8Zf23k2wWzeJOgicw5EfatoxnCNUb
lEwjgGm2comi+fAFP2+mvR+u24SUVUvvfUFSXDv0B7Ps/1v7vsB2VC8jjd6zZ2xTeciEkw8t
1IxnR3UlopaGSB2+Y+KWUePiIjRXD6RQHs1gJLjvw6Im/z/qvjusqWzrO6LiOKKOIkUUcGAG
VARFetdXiqMUGQhRaQ4oJUCQFiBAQL0qRYgMIp0ojAkkFBFC6Kg06YMhBBISkE4ghNBC9zuO
CqNz516e93G+5/Ufzjrh7LXPWmefs/de5be0nmCYvlDs7CzJS1JEelw+AxW+qd/7VzrBrcJb
UVQCAIjxdqJios3r0iSS/RuBKV3sB4PKE9sZHxQlvKfDy3Vg7GDWSMmEbLjLwq2yE+wBiHbi
Meva+nyt8qXYrhAz670q2nK2W1Rv5B8uNhwYDcBFGg+KLnPcZfaSS6T7k9VXf9oStab3/0Bs
cK5SWmB6Jei7a5YZl+tZ90VQrdFRkcf3hi15v5LmGlWlm5DyrsvWQeWz2hziUXZAqTDt3j8h
OUXtIoqwypA7Jqddmz2EFLh63YsA4u29wPMPDJdtMlEPBO7qR367GtPg8CSDsSjq4g/dX1jW
k4U9IFg3mWXBx/4Pd/81/GvT7RWrmR2IVqnLtenWe8xHLg/FZZjqmCnZzOoEx0jY92+9P+JT
JDfgZiPLgqYFpqIznEVu848bXRKccsJPQpEXflq33apOHWuLQfmKDfhiWAKm5gExojdyW42S
E2fk/IuuMUscyA1ehIPqo/hmRYqXSQOBGsSYhfO+OPW5lj6dnCjoRqXO0eGGciEJjZaYJ5Ch
OVzbSPySGage+SU9UKBvjjOXCrLcKjzylSJMqdlkomKzzXApeB/lLvfE6FaT9iWp7MGXqRDV
yhhoQruKRXWiF8xsODQnQhhSBhgN/CGlgVfqdhkQr9Hjmnu2++BNGbCJZNmTuTqwdgcI8/Jw
H2a5tXrnxzHPq+AjRe3SIP6KlOr9pc2w5+XLavKRhKiVjJqmPOTA6jAMMJq/3BV6IFd8d+jy
hU4yZBGZm3YF2m7GagtDloJNGpNMGrb7fa64f3O+0QAJl/6mrabVLWka2HPluhTj9OqR3zEJ
Kz7K05nVLDa8cM1dBnSxxdSnoTWt3OAW4ipkusN1jMLEVuZZX1SsBuIyM/ZDXlfyJmvrzwcj
Dk+SEwIuVtomEf0XMmN1Tep1Nx8L+Te3+DX9ZC/+M51f0nbgbti8X57Yz7VSvO7plVAgeYCC
XxksuXFba7dPKVyFIgAfoOyxgcdgHGq0uy+WI8LQU6ELp+VOrYm62VZMaMHobvutM6TJzHDJ
zff2/DY3o2uJt0hGVAaY37rSu3blB+LTtEH/dunRQE/80va01R8K+O5/wVRboLvQliJLS35+
5PVcRBssvp7sHXn+fLGtuyatutxhcA/H2C342M3b/bNLSZTfuCAu0so/kFVa4ul9FI9JXTUQ
k76QFpowJ/kiMhIoZOV+XVjtGVfZppEBBPA+x9bEPGL6laTEs2nljULOxSZoAHm5wA3/wIao
NwbWM4cYgg3r8vlH7geF/CE1z83+ifbyinmhaqPYiKHKXDdrS6N8rdK54oC9g/tM3D1xaaf5
Vr7n+pQTW4yT0ik9FczflYwkotrG22DJrTo1d3Wc+HEf1PefDhtGaaE0QiE2LKYZ1sGubTCz
XZVi7Do357ZMm4o16ax+pbxzvZPvmjvqrCpjmpTraV6Ld3iB7CgT9Cx32jMT/65i+Q8DlmeI
xGKdN1JbcRLxpQSOAkaSVo9tbFr2gl8Val9n81VSW9HD/DyM9Ia7wh4TJP59rkHQZd851ht6
sTgsdMtFb6uWezAocZcsREryuL2jJTBmnHEK16EzAUGAcm66PF+TGQjmNo1I2p3JW5zhAOCB
bxOWtmCPhBJtsvfvW53L+DfhqJ9OG+wMLXMKqT/WGZMRvxCRbpAYFN8mq3vrB4Qqos0TKQTV
8a/l9V7r7H9LvMuuZ9TV9xq/pINN+YON6fnYNkj+vqu/9BSbB3pFGLzic33j3cMQFVfNw/Rg
ySqFdxbq6quIhr5JytBSDBls2z/lWEnoFt6yM0HNCwispsVNiMCWqZl4mUtUdX24bjUXJeu1
lwyRrCw2J4OKQt7f5zIu0QXjhJNwxmkYmuSDKFWxIhOTGhm7Gn93J1s3JsotlxLkwEB8DCXH
edp8dUzhUOepDQi40diEQIq1oinYx8QJI+XI4K0o1wLAwjXnrvcfv8DyXLXIT8qko2GDwglC
Q8iGqN7OE+s9n8Ze1IIzclsEWNrhy2ZpbikKvEWLCTjYAHzhpATyhKGBXIkAK7eRzVfYYcKk
Gre0Pc3xL/XNYQjgji55HCq6ss7pq6SORB12UuZC+LgwSqkuRD/vsWMv8L3DyPVTdOvYN7bR
pQlLiSoaGudN0qSrcpyphWhbd7sjL0ujh+c5vfy/r4sM5J/8FGlzu1WFX3pXJsHzHkvnZHjm
DMm6WUeQ7TfPnNh5I8saK1FTOmOCgJkK1JXLdx8MWW/9B/WppS1vuGfUzzNvaT8GeeTRfpUv
Gpaw6a7WpbkhbWK9xXA72zIcT1vExGR0JaAe52SVyGPsl5IT0/t5d89M50r7eKKa63aNpZP3
WVK9mfGq7XUIXP2smK8/yrcGhaLRtyBvXclJPJAk7T11vsqwrLGAErzjgIohnjjmVNdSCW1H
Duo9vTr5QVBKZeKi3KROxq4ZSt5ozmCzUBCVDh9FGTaPdcx+E7rSIbHpaZCSmbW8tQK/gIFf
/NwV8UefqejfnG40/gA7fzvLlFi4a5AyAXmDNWybVjiKp0bAXXIrqVuEZ560uUOT2a5ZtODT
v/3CXCBq9mSnaK/Er8wyT2s9X+t1s20qZuEB8+AUR51VUmaqx5Krhk8vjLzmHI5fcL5vMpFw
292YlOe9ZLpHXzYC7hw6J5FoJzmx+dkag6+T2DxUcqRYz2IsaobMzy/WqzQ7uuI5Vzdcelf1
8r0aIY5SE12Knbd4rcnqnj/qWe7TP7uEv1MhJ51eQLUUjrRrmCwtPBlVWw1mecj2L1Qye5NS
+ccewJCCrvRGWKWoemEPKT8TT4so6hhjA6GkVz7T1f/Ht8NebYh2cSn3wS45Z3+LvpJjbq70
cxL2s/MPELiweVw+P4fnJJBkppBQZ73y9CQT482qy3vmsFK8EgSfyhvBaFdJTJ7gP84vvfno
3K5riVk9dcVgfCEziqTn3QpNC+qMv28E0Reti8Z7EnKc/C/tsRoJqDvZHK6VBJezt6OHzk9A
EKfRh95Lz/MtotTtqHKPGiInzwC5hD39ehZR2pqvV1w9DZR7mnuhEMhL9/Xt2VzkX/5MksAK
ho5eju1k9xB882S7cdpHcFcEOj9T47853ehSS9ZA2d/nyhShlg8nZ1Qy0pk4Y2pu4hyO5Zkx
k+c08UgvnrximtD8MDcarDW87SpTaJQr5TnJWmn8dTtxvVeRec4zaJ+taVD9k2s0jlmmB2To
IEk7WEBwVsRDchAT+m+WEOuNvw5qs63o3lBq+TmOfBZE2W20zP2ef/w0nGhc2ovTGsWWbf7T
PmLT9nInj8O1Q8TT5Ybw5OyIG/BcuL2KOqpYlwfsf7ohXSFWexc9LaBGQ+gMgdN2CwrYTm5O
hHymhk+XWLSMrSizmZlBm56Imp6zr13YNGaBiw986Uo97IvuzL8NCE2yFw+4/hbkNd5U6uFZ
W57uMBrnFA+EzCBr4EPa5377zv51uufVEU2Wa5kMuEbZp9sIYvSKrZ2odQYxK7/0JOLKs8DW
kejChV/7cm4ba3YRb5cr4S0y4lnUdgf6pGFAjMkd++74Lf/yVu1WwfQIFT4ZT53LSDlgWpfP
AmvjifDcKImmQMCf80EbezZ3cJ2pVX1xO1XI8tpmkN8VFBOxlUlVYdFC9pNdvD4zfXQVbvCP
mnLtzwIpHt7jkUftK5HtfdcYtench87oe/ulPlPrvzvdmOGLLwjwy1mlu3s619xbHJusofOW
ia1OGFGP6QZ6+T6VJKXp39p/0L2Pd3iyNUgH2najhzqrb40DsGluyD9a6xUIvt2/YLTSfle3
/TpGTj+9VphcumiHN2eSoq1Wbp/ceevU2qVfKcFbcbDDX1tgdjMjsckgBnu+p5DLNzen+WTM
P0ZHtv7+n7NCv+dmM+7q6wgWuRfbRZEdWU3J+4GZYr+ClcGC4fKjVlhKyQxM+7wqOEPP5rjk
b/Tn7LegyS5I3lJwOK/+59r59HX5J1MSQLzl3UJETRGmNLFAVi7R7dLvfpkacMlKp3SxbP0s
9dXzPu27kBh1WREhjW6jOoIdEBf9ijTtjN7tlOPuPE+RwWlVonGVAILJDgA3xPJV9RAE7qRt
WRWZMZ4VQTadhbgO9flJ92EGex7wf5RS0j6b0Z6f8NLmADs8c0Xlp+5L6kYKLLO4SBUoKu5b
9H0Btj6rLTpnKjYu/SqcRVSBPcZ2Rq0M10NcxKUri6cXhLRPOV74XGN/Pd/olCGvgrsDFl6O
9PiWbEb1dHfqyOQ6KFldXh3cywcecY7Q8192aI5fGLOAr2SgPUvyh4JvgGKfr3Xncc02XUhk
AlzP0ks8Wmy+FC06ILIyQ6nBWw0n3TGNM6fnZNGB7QluGoClJD3L4aJ9y7VePD271v5rJULE
MoqUeqcbq8Nw7W36Bk1Jc0PB1vxP7HzjV5lHUaH8dOKsiFLkNiNyNrkvXWVXi5GCWBNEFyzu
LRayJrIEOsfhuMuyUHO49HBGtzIOT0xqVg+sDiqp6DwZ8cTCbb9V1LjGvlb/qnqgkvOEIdNf
aaWhd7/rWvsPxGfJpKmP4pzKSbRYKKvVL/KAQXo/Vo/IDwCq/fol80qBrl36WwgRZeLD/Ugm
Va8oYtGBVdfd4QxYqMY4jjqkCYpvZe2OzA7I2boXQ/lnyZzs5SHis5nlhhxdf3xOcjLeBu0Q
KJgxX8qDGj1TxB4JHGft1KYwEXO82Vib1JVSM2GIpyR3foYHEfJeTF4hH29qocpuwNqeC4+a
dYv0PU92M3kXdvNTz7gnE3VPUOcxY/jVK9rBS12+UhK1aPRvzIeBq/65Egy90lR3T/nswEcP
vvugsv9w2Ohm/gr3YiRCMeqCtmOzdYXbRIoKjyRtsi1AkrigQ92aP3LrcRuqSk4adjadcGlx
QpCPzKq5h8CHzpeb6Rz+oWCt/32QA75bNc7f0uD6gCF3FN3ycEx+7fZL1cW2wYybgggD1qJS
qteM1jmcptmjkZKcx4YrhmQ7j6XlBH5xYem/jIQ1tl8LcXr4Il0iUiWpUe2BGdXHGou9Rtbu
rumO0Fo9Lz/FY6N2jZw71k2cxFo24muCda6O+Ktg34Iu2exMxC15HSq+siZmZAXxspLQ/Jmq
yBeKgXOCA6+qwsszyiPAXuIDnCmekhF6DhjviYq7AUFSldnt153ZLLC9yFtQUn/loZZHa1ze
E5u2Bzmu+CxKPw/cXaVw+uI/ht8N9MazA1HOsrQMSL63YkPXwnUvBQDViU2I4H2QsJ6B6hAw
3dRz2HcSG1shY0ugqXi7QnENOM0V3L3AHYz9aM+sJLSr8OCrhyORj1uEtvs4sxeRQzUkzZ6V
4h6h+UlXuw9yvcOpsajlvMOp0dcTO+oB4NRYSC65HsHKJczj8vZ+MziSUjx1vWipQjnwD/hG
R+1cHcyE8rXww1E9lrFeAxuCqdmY855HC9HpQDKQpamYJCyMLfXVjKA87/G9QlecUls80q9X
cdHXwYokD2Zx4wyQjHisyXPWHPP+WeG1B3SsR+3ybRHHI2VX6oshTrnXoPOAR7/b8mE/iwKK
SA2fB/cMobwcjDKT/EqFFIaX/DNzspaFQ+f7a6bOSmWscflaiTMqlrJ753ROlEp7mDAv0ZQZ
otrulIvNDbhcQvTZH2KirR0iA2Im9jpa5tYIFlZICQX7iiXkyXOMikNs15cLV7ZdvneO7Vlc
eDKbllhuUjGJKUZ1kCx4A33RqCpxYc3VsK6Z7kEaYtQD0mrPPl/MLzbYdPCcPfvn7X9CdXyv
wU/jn/9JFDkQ6Pu3oOyhduLdGhsRdmjYVGJFT+NrHNq+UMokFlV1dR9F4ZI3GxlbVsxOxnsw
sw9YlxMPJ0w3K2eTUhxZtVuLFzbdThbpLoQ7Cs0pT9YXC7KcLGMM2ycgCtQjmBZwaYzOj4e6
ej+MC7ODptRCXwofEf6qPr3G5frIpUVwQ1CJez8Faj+Q9V3A67teA26rPnMPU1wKLnerI/FP
ehJS6Rn3NBL2Lb0F6UTqBl5Jvf/fx9hG5xl9ISsjT4851HY4xZ+FzoR2kVjIaBcR1Mx9m5bo
y0rqtlIIYx9FeIqtNVnhKBrmXCqosfxQAgiBXo//kr+beScvWHcgOGzBj7R4bdxNZzeJNuzO
VC3Er7B8Nu9AiDnvs2EsW1AwKHTV64IyVcDoRsmlyK9KaJ86H/LfRfk/fkXYarGqomWHqlpm
jY5O8AHrPIUJS/y3GUsDt46VXB5cxEenHiSpSJXkMTuOkRW0hjSgxV57OLrPTxatySXsQib+
hDUdIF53AJv4vyZEysglzGE8nfN7Bsp1Dh87fibSgbVSXrNSaW4SU9Xc5nVkcaz9WpuO3297
1x/CB2afLdaiHsGd8gAQYOhhNtU7SAzYSFhEwjKXPPkefFnXJI9iSY/bOQVVxyrZaXltWWnr
5tf2rUOsOJRR1/K32p3H5KgN6YEzrvSHJ7N98XeT5sjCJG0kAyItmLsvwHb152KgGMv8gbOs
nZ4tQ1SE3EBtjkw+3rmzq4OJ0iXByUrVy7GbKR8kFOFO8iYWybRruIwIK847/V6UZNHFUqBV
OZQxJ6ELh4s35FPZoPd9jwZFWj0pkbLNuxOdmheRYxvPlYPc3sMt5rX0JtYkw/RV3ZVMFcEI
n4h8ftFSLvnZkkndHlDD87Un+0udRYpNpMqv5Y23wdZYC3JBsro9Lb4h7V3C23JI3eqdRa0l
9ePCPov9M8ll2UCh96TZjoymnFwCIuSc6hqXr5W4xygS2bpfU/MNbDRRg4wdU7+DFggwjbaj
A+umvCke5kwgZaRDTSsfa2Yb7i3bnDk6a9DebHNeklgfzc+5pXLqo9ybwlcuXJ8YmlKoLjlG
SxwjGMcEFATsI+H6jMw4ZgJn5bc9rn1sVF5Ts3IUujB+T1ZIQrKb6CWXsDTOcynkI48Px/+P
7vrN29Wfu53ttkoZGOPvqaB0JzrgRSuJSfGpwYs93bxCnmZwBndgR+LE/sHLnMu/zywdSIta
Dcs5ZlXKLzZunKC7HPL8hGt0PSNbn9CA+kYho1RFwzVbXKwEE9BEAWpalZS2EvvSTvt9kAsw
pPTQcm8ur7Ij3XnpZr5nGR2+eiVArFkpmdo6Heh7+qnPB7eKkSlDSit+28hnivk3pxuzdH0D
HXPMBgejaEKw1uBdu1qxylo5gEf9MPpF7161V/Bo47D6nu3XM7BVQsod2o7u8LegAJKO7HPb
9TnM4C3o8j3quCfgcJelJwaZVUwue9eNZWA3qweYcG32z99oGwHiJt3j3MZwwBc2uhzW37Tk
4b5tb8bS+M0zIf/mxr+qn7YgfbJqppLz3DRfpTngNdh7w+JRekrOC/RV+oldlbrLVDnPnrKC
EeD7U87uiefKPK8KfZcu9vyjkJvsFoZeZ3b4n+ob+tF7Po3R0QSEe3dhG3WXC18c0OInBBSq
hTFK+JBPEp5NDJJnO7zynFEE5CPD3z8y+Hj8JDAyezGk515Uahm+O9xBw2lRTyyY5e3ivXrq
au6XBFcDgYRZ7cehxlMDVeElhobV/U7tzPJ+0spWZIfVCh5wsigtGpPd4dBk796UJS9wCrsq
K/dgAL8gMxnGWK4NXP6V75stb0EzFR1yYwdR14ey7oWV+u5SMlTHBCmS3H+uDz8ynz0vyeA1
D3kv4zc/MvsJ9rDplGxo27uiFzNGx8HTb0Euju2p7otY+pa2SQ0fSEWRzFMVwqv43OtuQTLm
OGmSgG010dMOCInj+ZMP46PSPj9uEPd603ZRh+nMxqHGn/IMuclasdhOtKejzMnh7mLQQzEz
D1zVoMutztk2RbBx1e+B5k3weNz1Y03Vy16HSp6v9RhpTCxhCS/LvUmlJi6B0blDjnpATFNd
uBTyuHldww5UG+XUAqpBAIFyRiUl5f7cOr2kfQAuD5iYXySHrDH5SonNfIiikXZocryLP9mU
4R3pDuSMBWUC9vP77Cnb+PkX9oiDY3HHWUg5t+KwySvDIwvtS9ZsWkNa8LaQc+siyzoqxfsq
7YLMl9926O4uDbBzaaelab2rnsgQXgjg+XFR0ZF0tzknHQXM3RoOUGHORNPVPqulhwP88HUm
76nP1l3/HOIa0J2p5nVqLLtihzsrGuYg033A3vz1aPxMzfvsY9/yU7dzopdylLlqJXLR8lpE
/TCcs/ZwS+esLXo1gw/cZ9yx+ktRRAnc3LB1Wifb0TlYa3RFYgUOIJLYbX8w0pw7wFzOgCba
6HkojiQ16uyt9p25nHtAEDCms614/ULeS/uN95g7AVfVD9lNzPWfhNJshuL2jPvlnZywSuAu
ORjUg+7boA/gVFBSmkfI6ZUz2mHTMq1vQVRIjl3wd3x33vP4T383+hbx0C8q4Qg2cCKSj8tK
H13U3+c7h3tBCJ7ouW8szTcTDkw2O+cwt/S0Rbzpu7ftPTKXRg8/wpq78fMHOQATyeHFwUFT
m2De63ZIBDnlBdy+OyfrG1Tv2ZP4J0hZwGx9fW5WnuqZ6yIEfWe2xmkPfsf3tfvyga9uXjtQ
eGTi8SvKXlYnsT+nWQS8yiArQuNjwToC8ua3di8eZCpe7k62eS2Vm1r/ou2ZnVYR4Y8VFYD3
fn3tyZkt/8/rTAp812CbDLbG+HH6kF1TgIdns/fc0pVbYg9KapoVUlgxd3VN7lpUkSfHuOkm
lQETXSEm6ww+cPpk5vkHodhAoE0LYEUggdrcNyyKxD/+XIkzwCgpOt3KqGnLz2myelevhWAN
9sfAbJKKtIOR+ErXfSiNA7C59qGeiETwW5ARnZ7B3LdQCk8/OjPQJm6P2HQoZbevkr+ldDhN
Gcj9UQCTlNQdOxPq8xHdc29BOLOp5z98RO/RF7fSyguQdrqe7t+mle1c8hCPsZpGQOsJdoPi
P9hBpm7OeN+lKxO3SZXAYmA5s24pweavx1BQ3IRZHG2gMcTh0Zra/5bY2IJtZxAi7lrg6+GY
MO6xaoo2jpSla5Dq4ETycJtbcOZ93jmXWZcHq9lDTfLW28PWhW87tNbf943ZFeWA2/LNaifH
BHBbUtC0d25Lqk7bje8DQ5y83SaMVE1u6IkJlz5qS6HR60utF9BRMC7v6TUOXyux4/uW1Vj9
vAZxIQ9gqAvOpSIh7vDm4lL+KdoWJ+8LZPfOoTN+I3k6vzm4Ji0oGQQbwfOfjmJZNln8mmsi
744oHC2HloLrAExCZzTiisjSTNcrvMFw3B2bTIwbxRj2OAKsMBqOJ01lzy1Ax3fefL7W9D3x
6d7Fp12QLlgSMJVtVGIXnyKkjy8I8EqjJgCG63q5L+rlB4EodaE+kCqb30QKsRkkowiEgTDS
ZelBZ4rNycPobibm9LiP8e9T3khf7oQeTV4vxaIlNgUlv8iUNq4jmq+OwoZf7WC37faiVvdh
9xZepVCH8ESO0jnnuX4hKTcgse2hQcP24A+iCn/fYQm7OqaJBcLstORppxnC+4nDRHQ9BBVj
P+/LWg5JR0jCXPZbHeiTasEMGLGOe11qH0uvTD3SUJNGV+C0iNoe+uFfn6nt35xuDFMDCHR9
boUNFdUlGqOt/Eab+3zUFauX5N3V79n0lP05SIVnL6LF0SyuOQpll8BWtZQ2yYMUK8QleU1Y
hZzjHrlYkT5of6tzWrfN3NWIF5cZz5I3772UwOY03Rz/N/f2df20w7FpIi7YcjA/fFFbVltm
gSZpXUcQp1FuII4seYFCU6PUn4gEq/hyjuILmJbnTWswWsURRdyAwIe/8f/pOSlxeoNah3Zn
VFBfEAxJwlbgBdQesWqrdmgta8rizykO75Xz6Yvwj8bcg3YGqyePEpy6pzykZC1xZJWJ0QQ4
DqUS7kLygOIyVtk1w4Dv01O92tRFJb4ZXcKRDT7jsqxD8jpSumeaQGZmFU2b5FNR0lPP1ctF
fbemHEiiFoy9gxYvNfuZxKpeLcG55EXTBupwyEPGhz88+poWzKKgfi+Qy3BxHm43OH5eHR6o
u1oYoX5HqTE20GI0S9jld7ZtHqpMNZ/AzJGYe4wZVZsxG29W5XoexiGP1AO1rgtD/usw2mjQ
JKVRpBRRZ7YDokk2Tao7B+X2lb94C+rhffForQuerYjcMR9mGYvNJ1I61/ZU8Z5IwBL4Slfl
0Dz7lfSBO4laGr53NSDubQZ3UhR0X1SFB2UQ7cI1gh593JitcfrqiM0NdISbegulQzF8lGOW
ciM6Up5VA2dip27yLl5iCj0tHnwzmOSrqehA65CfqCObTR8/WoR6loa+zz+1LqvSVDvMLG32
RH2lfG/6jqhYq+mFUjP9yp6JU3/OXXh//adekVwdCvPVuxyshjQJ+59eO00HmI/MjaKK+OK+
rH0X9M2ZMZn0LpJaIWnazXSPRXa+93JjjFizaXSsY2W9A1Aiu77d0/5ir/hhWsdKj2wSbnK6
vUsFS7KGe3gzcewVOnP10taMUTy+q02N8QZ+bbEvEebgaKfbSrYlTbmSxK95blor8k442OU0
O7ac6+H+Uz5KhW3bpU6JJuwZzmGp+kLTJOkcvUNhjHuLNSkqSVomvKwgrEVX4p0fi9gzYFJM
WMC8MnRLd8i6av+G2vjgjz1CrBZ7RFMwn7bCXugh+sSjTYK3jiXI65RN/Dn+irci5aeTMh0L
Q32udiQVGCQF22dqpJ2ITzepIdAGsX+g+SUpZ+TrwjF0ecOANtDXDuUHAonH7JGX1wbyxQP/
pdcc03p318x4w5L1y+79CHA9WqWVggoWn2j/VEdWDIj73ZVTvoXZQ8CcWj4+pqAdxVBnXW1a
XSr6b0P9n3UAAlNV0QHPluPfFVmWOhP3+P7cRtipjiv1H0p2mZswE983SJ66GTKkDaXTZf2v
9+wvMFO7rFye4bYIZTOcCQJDbYaB3r00dKhwcUNttrqQgqYUuaysC3sgwCm2O0eaOIrMJgAB
/4rNptoDt659GJ6bXnfMNIowItHpV0kCl1prSiM8pdsUKbok+amzh6Qx+lgglUB653J5w7gZ
cg57Gx72R1WrZ5mYxPSxZTF32KEDm77YQFf1Ok6KCAs+mskySvKxQiMki5RWR1GRxraaZScI
5r7h7tA4pLpiWUn6/KHOg+vvlEt/zSKuJ8hAhZfXSOxwc1/3qCi2lRGudLYWRdD9c5DrepOv
jBJZcFOXoYmeK+jWhJY9+MXj2b2fWOOWC8UDTFReQoiryLo4SotMH5Txcc1uY4IhPDxnFKKt
PpN1DjtxM/ip55HGl3WNmAASgiwkEVQfim7Y9fke+DNsSs2lleO7LHTsFVtrFDdLLX7R1CgQ
j4J6r1to4xv2DiIaXRGXxRSxLV4RsKO3zugAduLaqQBueqFtVEJikXu136ThEj8cp8nhQGNA
L9zEwc2/EwJFvYyLB6ZmxpMuwWXQHd1EAExoOQ9EdRRbKUsSnHIl96Wx9lgrsKrr/Nb2jpSq
a9WT/ZmCKTew3fcCLqvs13bwRempcrKMwvu5arj1j/+6Pv9CbWh3yxPXl5ptfKtqZ0/Ou4An
1rYLjQlzaQwAfG/p1L/kYhDHoMljLCv27uD4RYfsJLbf04mLq5r8DeudKU3RhI52p5ybWS5D
aGY5cEruZbLG29TZUZlLYlN//pqtN/nKKOClRbh0iRoQxscTy7TT+maY5cPN1PDZi6+wXMJz
5V3r4gA44Ol62PPDEC9HPVHsxdcFyV1ABEB1Wl0wR7TikFHddgLUZ1VgnA5PLDPNYK1oyB2d
6xtSKildefqX1I1PTDw5i//SNTCJAgcAnh9TRdvqhzd+1fqCRSkAATbd1LoGnwM27A4pOPtq
P2/ZNzeSEAG+K3JlgXjR8lZ0JZAAqDmICPclGsKuzQfZsV0jhcxedseaicWnJdSW9zDiSXig
oPp3OxPVArvjuKhNqm6lnsGQjsIoVIZ11MoSxHcX2ceg0fxm7wdtAQUn+wi+t60W2StmPxH2
9ZCI+spvCIb+pYxyWIt7cFRpyuoJ1/163t1A9WcTBDQUJ00L2/b7uqr/htpY3BNBs3MAHNFA
EXZvs2oDa+y2nSTzD4dXODJC0Q/2aLTFfZuc40qwnBYd3n0NKpTendBQlT79QmW9y+UEFhBW
uzAlCQ4YRsuJMf3NfYtTiqYI0L7AFRymeRlFULy1sVoy6zz/L1IiC7MH8oFika3VpfE+/hqF
hGN8NB+gcp+fKsUOebn01hWcDGZwXzcmoMaUX2zm1rqL9LvoDvddyTBX74g2Uezxq6NcLD2+
sSl9etOxg096kqMsVDXg0EQMXPCGgGGrf0KkdpMJLcT6P3/i/0nQbkD3NcgMET2WffSEZBvK
Dkavxp5vwkjOFtDa8zAlFTJItS2ImXZMtu/NwC7Xg5edczWs3wxC5LNbx/DEiAxLVM9V06lb
PKfzdpsEtR2ojNm1j1kAGGrOjMQ8WegHjpW+QvMhVz/GJ9zUzjlgo7jLa7bZQiJ4Mk7vNeEn
to6ZnXxgz+wFI50tvppsGJ+r6LDW0hjN/nz7cCV2Zvm8r+Zb0NVv/3tG9QYdARdX/XxEvCsu
FBXHgK3TyjPRkRw6UblSc096m45haUD8ymCWAfNiqcSqko07xbq1CqdNxt1QeL42Rqe5u4LU
bW5kMn1aoR4n2LbAlBEulfvqm72jHhE2EM1l5US3ZvOLkXYsL/Hs0NeefVLBJYn2/VtWQ9Y4
fLVECANXAtQVThXlxnqNKB1zkzxKSZrNw/RT0T2XM/iz8wjqPuUxxNnEoxwz9JO+a7pLHtaJ
0OVH3DWBN/EFuSqWFvrf60K0r2Ljnrn2kWY78p8x0QTE/Z8gkomx6rmHNSXrMTkcffKLWvYE
Nb0eeeX4/bX274nP/GfGSCDAGxsnI9CNL6uNfWLG0Y/WNQCwaA2/KPYVCLQ1dVjoHDFr6nHN
sszDZaRobNZVMxPYtBK1uhieymCHh24xm/Esd5FMMKIUTuWY3Kco70oPUx5CwkvKwXe1UQ52
8cVTr07ol8gQrS0mzBTJhk1A5rBz2Nxv/ITXZzwvUdSO/17QCJHAFc4RcKNECekRKF7CMyAw
QbG1lq/5gwq+I3U0wnqqhzZfhWWunDHrmuklDb0F3atrepWTyWZfbZviMfDf3f3QFyId+GP7
uFX4aF5hXkFXPJpi51sLJPjly3N4lkM+U+dfTjeYrcFnw3TLYLxeONiH1AtbWHqo2ORuMgZj
+hUyV1iefCdHfLEkLz+OPXhygVPQLCMmTY2I8zy6enST7PO1HonJNS5KrBZbv5QiWS5nNEnl
chOWiC0vkyHUdW/RmAl8ndnu/zI/AUgQPE9TT7UyISgoA4ihxwHYlMY1Hl8tsekb0asFzOvF
RVX1mFQSOn9mPIzrcHyAtiq3Se5g9jCDrObwRupJjG3UnEXN7+7WeFpO1g4FCG1iR+qayO9A
77Ekd9/JJEDLU4p0SzFHWoSvB3NVcX8sSfxCeaanStXBiGlGKdxHM3jCDZoAH11hneBLW2Pw
nvjURvoPljMHutN0G358iX5Ax5qmtk8PTghSkOEtcWxTpBPA/OI/nrop91CEYYxqWX1ZR4Af
zsd1kZ96SgRb6452CR1B0WUtFzbZqXIfU2kHvfuUaXm6pu4/0RMrdu6ryzPKaizQDXxw0wLx
45iF++SOILcGl7DSW2XSyrigeMyqoNa+1kYU5NX2fR9E32NNkT5bDk7dNTY37kvQuzwhOpZK
BusLwEfn+5LyOZt/WLwwJuijfXYOJlDSB33tRQjUiBarMUMjgGi8GZNavorPVPjX0w0G1QpH
ku1PJsMMuDVhqaS4uPQuFNzetC53etO9IL5xcE+kmpnufPAknK4EnzZ8C6pQkOdqXziXsdbd
Mbba/ge9nim1O2ZNnPBXxwSRGvFxh1FveGRLZPoXbJy5SqNpDsfGNUc58GndFuQWA2rCFnLI
WvOvlrjNIJQEjVk1uYkaO7Mcpe3tL2GCSljDQ8220EFQDOynWREfY9OiMzFG1n2RjzH9y/As
Eiw4ZEfnmsDf4McSUBDYjmt6/G9QQ+F0cMAeHbZ3dfCOAQA0EdOElfl1Z7SddFmfA3TOsTuh
3VNmefLa52vw71WytwqQmuG3lczkBVxdt2MctOSZ3SNs8YMmr/iMe6wqOXF3LXe4cQyCxsuy
j7tOjFnIOSXeHk9Sqr1W+lBiNhMT7pLYJ0WBptcYwsNCp03i93K/KG4DIKxLTyNLZ0ILiIB1
ughfVnTqNkoh7qtLqoIN+fiZcfRUpAe26rQiu7DO03drsuXi4yOW4qTNppf8U55h2b3NyDsJ
jIM5J0cJVmg08ZEtEHToNNkSpGRowDVfvr9WJmzPaEfleWJAnGhC1rxGdzWjw6MvhxEO6x0k
68DIh4ZH8DgE9qEb5QkF4ZK7I2CAYqSgcxo2tEvcCQXVNKdoL7/64bu1x/J3xAYXd1eGL2bb
KbZcyHyZuGScXTLTrYpyJwixgdgO/p6+rUUjt5+YOd5OPt+xrB1Y/iIsQoFVk+WMJ86zC7cf
XeuZV8Vnf0f6qYH08AQAIlAGY/8muEPh2MVVRWHpth1nMdx9qgm5Rjpadx/90qdn027zKhGj
U23wanvQGoOvlti0Z+X6DNXNHbbPZY9J6zXnyxjFVqJg7kX8PAAlnWitQDhPrZTsPtFQOWPB
IRy0NRlzZV6yyFxhfce3PiVtcfEpez1a/jJHZAwpri31prEmbC5tQiWCOI8u2BHWRroYafJA
I97U1v+1r8OTu/IsXyIqgDg/8RYkrPDgM8V9h+6IGoA0O/QAGDUv8k4cSV1Z7mnrmh6abiWO
w7nlCd/2/4P1wYB7celp0n0LKmJfaKbkDFrFp+v3mQNFx4Mt9ZqoCul94TCDV7uDcTl3gWrQ
5RUKcqQ9LhdrXntlwVFG4grjlxKWNJRuTnqf6xbo9+hBujmxe9vhcfhhKhuVYBe6LIXslNL9
IO4vrRaRvB259RZD7XKmAuDHzBLjoOLFRFxjunhlfbQ855Y44qBLglAB8jgLH1t3v7q+zSvb
bKWc6jlSrPNj0pUHIZ+p7a+nG3JhbxIPcnHX08xzO4ZcRXCHfvRYaUGjxZN3aYertpnIalQd
J6YOLdQTFWZLkPtW/X44tNaNcALZQCrpYKQHb3srWmoOBdXqijQTzG3mPeatkGd0KdCpAUjZ
hc/NFqE9M9ulp6/sXU85XOPxtRE8RxeH7CHyLwIb3Frv6CQeAIPHgaFSPm0YhKs4dZVyzpXq
WXyoS1AioEXMIdcuqD5FfyU4la9kTcwtgT45deHFTl0LQWVz3A6lInQOaRo7vWm27dwMuFFs
oo49nI68RtGhO8/vWXh0/8Jaw/fEpxbgf9g8wMNTgh0hzqT6qUzoNXoYZf9cG5NkT8w3aRoP
8DHpomUJ+EL4IhCtYnAxdl2aQ0f/m5zojIWzqJQc3LOTK/zjy2ygZpmX93Uya7Sse+ANxVyX
WWpgWv3Oud9JKQ186DiwpTfkvVh8vkz+Qmd6WbyH5XmcVOCdCBF0Eq2q0kVmPsSAqxvUzDRW
4Ox2BJCNe4zyXMy4Oo89R4ircdzT8ofet/8PfzdmEFZZ7GaautzS1HytaROY0hogJUmbuhhL
WnaS0Y5UN7rse+Ry1FUuC+cue0ZOA6hGGuY4f9/Raa3XE0n4uTzjhPoOm31kqo9bHeaX6gAv
fk+uO0fHSTDm8VykUeSNGq2q3oVxur1xVWJ5UZ4dK6iyQXpwS+Iaj6+XiMwhIsAqRQZVke5V
051JKGlBYMdXlA9x5wDps2UjPVnL7YMHZLaVtTZF9mS8CWDIqFLeglC83iEfRd68paRhVCFj
KhY7ZBDMxfs7L3jR6HUN+cvXD1eEUh9Y91L2KKKE0Ae8uurj58pyZIFyPAJzN/70IXrP6BPr
cb6V37C4TNTB8snKkK6DOsTfzKoMXa1cENnqv/Ukj+TfFV4Zaqdi67mTNbYGEHcD9Ovt8l/Y
GQ76XjKLkeK+I0lUUircTlrn6uiCwFL+fv+Hq4NF28wy7vy4P5l38IAvGPLgVbufiyPvbNd0
sxcq8pYCA1myEnz4sHbcJe4JtcE31WYIJ2LMtKXYuMFYn3dZZih6Ii1h/hH/8gf1yVaeLBHT
HxokhVv67orHS5p1JXb8GBrPXrzmB3FO55JAoWJRVFa2ZBKzYCkWiCkJgPz8PE0b9yGkJGH+
hurzjw/ib48be4mOIQaHbdJ33FJ3U0LGIiYqkUWr1NDn4Uhyw43ocumn9vy/uj2J3kMjl0Rl
I4MYXUS3tyBBvhdrnb7LcSjfN/WigLO0MOHerV4a4CGCDF7sPSjKzzmS/pA1mEJrDQi0JShM
mN64q4M+dP/RWtOvltgz21FYo+RZV+AZ4M9iN52TZOBNWtHNIYHepoAx7LLvHfFgrezpGCDg
GG/yEtW05V9rkgJl0p721tr+QCuVcGYzZQ1+qhQbDqRZADYhXjVvxeZyG6H9BVTcytFmeiUy
dJVa1BpeQd530yxkjcEfxKd55v3TXo1xvH6/1GNBRbl5hb5NdHL50xPuLsVvQYoncxE5pYk+
Kni0NJxlweIWK0BazEzcdeGoEwox6XezhaTfwNO5yVccT33aw//qLHQXMQnBUBFQdS7pCw2f
Fa2Mw5Ih7ob2V2tevQc9vzH0kK5RhxmW6T5dbLhgJCRjTnvQtLRvfoLGWoVhB7ZGDJy/TipU
ewnYUcA2wuXFed4TqxPmLYoG871rOenq1IcC2eeNG0i5JH73ozVwmbA5Z1xC2NKjELGErh55
ICgnxV9bxszCGBsBVvLH1ngZNRD3NQX5mA7NvXj60a799+JtzCsTxije72FDfDEuthqgWjLY
hcrN/VbnxH73133t1AHLO/mKzQpWY0qtfm9B0xWOzgsam48+/9jlpgMrMCV1t+v2dxNVIlpj
S+QGqgM8XPYO6tQFPbWwFlFMnGH8PHusoXSO7Jv6OM4kGCqfd2yFdpJv4iODr/e46Rb9lxmE
j/YFaWUntrr+KMlLIigz0f0Se1WDWLvDuW2bBYbL55f02K9sHjEnaEVi6Y0jMtmrkiye82tC
bwpPMWUZMfSKYuUNyYrGkVZwFFD95A0XHVMkL/m4wso0m3N3W2XqnNxduOSYTDOqdUveWtv3
xKdIc4ThqWa4uv9Urt6rqOnfRsEL5bgChJR2+/OTtl/69YgwLgZgFJpVbpXM7jO4X1eZ02f9
R1EK8LuiFDz17sXFRYtak0NZF8PfghJsfrhqWY/OSBtgKgXvONrTwGc2WPUzMd1r90uWHVA7
R1iDpFuPc+wMV8gi61w/cPKjjEqcN+2Qqpbf1LWTsE2X0s/373PWHlR2hCQj+sePAr746x8v
/Nvjxl6Au1FE9SybfuldMyZCaH5XRgOL5W+FG2WvSrN4TpUEOXukT117ee8stmpQUQcMbOdT
yz3ZwT23vj/1sd9NgqKe0+6mYS8i1RPfgs6Vel23yUHDcJI8R9C/llRcuHr3HN+31xd+oO7f
I4rVuEBmt5bKpyB6OFcaJz9y+HqPwtFky73JqQZE+mjUdERsOgPl6fhzHeC3vSfKlwsvrk32
xwVyiC6hbFZgWxiaCIq9siarPeWCtZxSlGFRbhhY+zDx8SKeuNw85huwOrlnqe0AOELTvk8q
rG96kJWkZl1e+WOsntZbEPBhMfz8w/e9RraAjZyL9zdTseQ3nUV7qLl6Om3FJKrmKkon2L5V
gX2zmMk/U6EGXvlXW/Dey7xnv7BzBrRnsKPOmOgbZxSHN5Lvr2UUemS+Kx8B2KAQqPvC2JdU
ZzJChxNOXhwqKTCW+GWAGoZuHy22iXFvZvlPWC1cFVZ4wlS7rI29i++l9L56Ueku1WxD9gYL
mOkcO6WcQvRMKhwt1eViisLTgurXnPEAQunubd+U3HKXhTngnF/73dYfSJhp8rdKVHAIrt38
y5qW/5bY2M782xSo3PxCBk1RdxX79Lo9sXT6zAV0I+hBqrG8/e4HE7upoay+LnWlnvxqou0w
D2etNx4pRP9QTXPdS1GNytRaQQLSfmzCzgAY8xNxRUR5f+E3KUJOiUdzUmzYznN22ZYnndFR
CWG85mvtv16idhfmshvdMpoh3X9pUcaPCjfhKhOOWRKCcD8I2/4+fSHCkhK+CIlojXky6r9H
rCemFInuPy3buyZwfll/X63jke4rBKAK7jOfpMpfwjwrm7dYekNKe4fQXrSEaatOtTYaLb5d
cWH51+34tYbviU8dKr7tYjiXUU5DAcncMLCmLb1Zu8npYdrpLx3HAuLdNxtA65jNMZqePcqq
MXsEE1UwTQOq4+WUwd6CpAzravkODIxVlamBhip/sU5zST9bTSLy6dYl1RgCeeQcYzT/1OYt
p/Pfgr6dXQrA317S8b6cW6ef92h0YYYsnhNRNAPhB3BWD72XkGfTIsZZZabFr+gWYjB3a/b/
dMTE2SFxCSSPDByyJby/bwvHTdaO8YZaolzpUIRjPMH2DwHFJOQ96UrVK08Rz99z+fu/G5s1
/rXrmVpebHPLj6Gpq+lUEZ8wrgajPnf6BeA/e0MnFV97I4ZGond2u0U8ohaLkc1H5+yQ3TzD
IR+75TmAoLqI2aIs+U9xgp/P3cVrBLc69KTPh5yt/B5xTd1A2kqqBoPms6I9PFkaQMTgy9+C
kDvmPrb+eo88ddMvsLXYdxlKOGyZacH0lI4nUUXnBBACcebnUpeEnYO/GTAvWUqsGtlau+gA
JUch0C2ta+LyUKbP3/U1HYyJiBc8wrF+1Zm4gvdgkS2ASFDWK4kz6XBXu2mPODtHIl75TrqD
FoPCwS8/N5pfa/+e+MyJ/48mwYJ45WZVXnsqRRn4JaEiYDLFdi1JcWxTl59riq2Wzc0uSGIx
1d0dqkrNd2pqQnOPW74pp8XPmADxLZEpMJ2gaJMGvt289QdThi3b1S70zumVpNlFotI651lv
qEQdWMLW3g+ifYfqcDEi3mp+GBurJy8A1ZAxqc8JKr6X1Wjr2c5z0d+o3YXsb/VmVxCNBB+k
Rz5eODcU0Ayu3ZmBc6RzdG+OhXxg87eHjW2/ty4+ZbZlTBNKny5br14bpepLu7tU7MT31PFc
n3fE6kdXBWX+RjK5c6JA86AfyuWFXXjwoaMX1vr8n+DLGpyAxOZKmHSrvd0VS/TiXJBt8nbz
wW+r7T2xL2jedU4pYY+tlo4dACMvWD9fa/fVEoLoJEvTgFikPC0eQAENubxiKjbuzMVo90pE
pAua20//ktWVwGKmRKOhWowuP/DqFan2NVn3tfIXjJDn3UoVEzM5+rC7aJQ8a54zBiR07EYY
M/OwXvkFT4dyepQUWZZ7JWms23DAFHgoNWSt/XviU2OuxT8azgvaodJik+QOHlS5J0x0DgtX
tsiNEV0pvUiUq6OlbRIIEnWOPBMfxCrMtUJ/nzXJ/rkW15NnbRZ3e8+UmdLyM+A1eEFX8ild
fAv6wep48yugWqR/pzZQykwDlXG1C8stHOU1+iDcNzfGAojZ/R7n7yQ9OxxanDGyH+EDhs/U
KhtaAcCDYJ3DCkSs3JtcrynTl836A4ZGKQqSxtNLF4vjOP2sSyFXQz/T0V9ON5iUobTMDIYf
92qrZvZ35v6UPu6drLocgs5WEZNXHLe6bF9wKV+vCIWID4Gf+tjDJl7rK0qHW4b5pQWPsqc1
3JzjSWKU4CO+878buh+/bDCt81xOxEmrNLC5a1FZ2nlOM1UAF3xI7mPrr/j4rUKkurlL98Ee
hKj5fLopTR3zQx1xUB5mRmMB6I/6wHCeTkm3M7KucB5BYI4ZEKmtsazVw/zrCe67Cp+g9iPg
Fsfq/MrtSr3EVhRAITbxQnatWgflcxxJNrkmXc5q0Qunnwp/pqXPpgJY8LixjokxmNVsI7eo
H2OL7AGnW+KJNN7zX3rPsC9OqJBV3vPSbaxgok2gLduNft4Yl4BKAxwTsk3I+e9iX9t6GIe1
5HSR7Cvdgs+RC0ZZKzk/+msHLz6VjwinIRhtfVEcKjwj/HCbz8oZY0w86nGEmgAtdGVEivYb
hqCPr3egv0irmE5nLuYImM4qWBhBlgLj+pAnHM5+UEEErFhEW48ufYt2M9z+ld2AS7wvdJXB
UvVpE/8xKeSVcYx6c7nZrym5t/Q8FH6DJn5WV3L9s/2ZRj+ebtBr7tLf/m0i97hWoMHLPAhi
itBk+K2DNk4+jxXUCaTurXzkBtqy2cewqTS2VWWPm1VuuXDhTIDySgPymh1Yfg5svn2AGm+K
YbmJG2M09OXQKDtJ6iQNo3NI67/e5Rr//7OEqKiXoEKB9RneDPZ+YaKbYQDyqJTO4UMqT+g9
P7aa8A3XyAsY5+kurGjN3Gtt7DywLsfmSZEF7wXMEG0Yf2fen586pExIuGVLMZbTA4DV/pKs
+qkZ1sZn+6LtQdzqS6fKMNnNP6h/2cQO0B8p5rAPKebxQGJqbqXJeUqho1ayak17n+xVe5f9
VOtO9kipF7+kmP04fnxHcAtvTHSaF6RmmS/JQ8+snJAcLqGTSW8qhvewZX7bi2ozUZabqi89
4TBAttBebMiRcBxxzt28jegO1SBBaFtuflDLN9Njv2BpxY1RTWSHeE4/20V1BigVewJADCw/
paEl4IV5Czpmief5o9LjmBzOOWFRROb5C9aeCd9wbP+fITjX1fwJtdGpYapfq5Oeok8UVLLV
2n/w4kKKvHZrTPtoHo0b0qm4ztFluB0v4SPmN48GZyQyZx3QdhKa0wr6KREG7g/vuwrAQomw
JO/FI6Gh8zdm1lt9rdTmKTspKem2Q5RGrA8EsLNpLivWNSzQCpVcu4+ulmRpRpiJy57q/JP1
x2Xwxfm8gpJ7rCanhVd1fZVNnSiXBij4Imtp8s8ZT3/o41Mo9eGMH6nHvecGL5d6MST120bm
R9vcqleK7l9Ff1nYKBCIt0J9p3xBSaydvb1VkvJMi3KtYrM2rCOToilgUK7IRd0TLz+vyFSs
8J1Pj4TFY2Qan79iidHpGiIDKyUD+5/8zr4OjskvyiM4Vt41aZ/J/h+tnAXBZwBo2ZW98A/P
+QQe39IDxAa7ZTCV2gSMbxcplv9PGFAWqSTvPT7yMcqZ5ioL46a+ivbUVVEN89eEb+ZKBy5X
woK3ogq2q/+30bIxCELeirhRrCnT2RNlpKYJj+f2Zb9Pvr6yxn6zrbajQ8pwu4LvldXM/cln
CE+aEAHzJ2U741fYV1w/n5fXmn1NhNJU7+3OLrq+MkNWR024G7yQsEes7kE7FHitez95rUcj
9dR9zc6bI47U9hPk2Xoat96Cyv4CpPHpJ/kfRWAGtEypTEJv+1btLYixSMZJhb7mNmfXUOOn
uaWeDNfWOhUp5AnwyuWCb9oWSN2IewbuSSXGsRm+c8uqBUCmRfrNJW91cnYXPdnyd0wGZ8iZ
qm9lxqpJKlYE0jFQqAd7Oz48Rnn3zI64YIsBr7CH8m7zE5cIGCD9KZOQ2Uf5YzN8YvhxRzas
ZayPcVfJAHXc5PXJPq2ifC+pBDSHM3Xzcsh/GwwbM2nm3t19JNfDR7Lt5LFW/8paF//ylRLn
jsCsFdzVA9vW+9gZSAgwxfmcaKpDp2JlouJklzgWlfLAGnI96uK/3c//4f9TXrebYWYV09B6
qmXwUG5aCvC+MnhfXFm75c22O9+ChJTfgn42cpFYnneoE5Fz8J3LxF+eKljJDPlzxYs/mnz6
fa1DBz9501A37pAwjwm52vOlP6pbNs8avc4dLeN48KzQbHZcvp0tebR6BayjIJ8BxL75LIdk
q5cOUjtU34LyVGRRWuXudxL1AyFi4WX+lypay98sneKqy0CFXL1Olyi+BcnKOx63v0ZWDBCA
6MN330EeTly9tOXjRnuHfMudBP3sBogQB2bWF64Mw8fQ6PmR1p1L3qck3oLSch7D6xRoeOOp
fEHPOWVrL4M8cIPCZJkCRw+8/Cjx+po2/4bY6CJ5uB7c4OuoE7DbdFG1iV6sfs+ESD1uw567
8fTKOmdKnQPYy4Zp+ttAJ+rgAOcZw3ypoLZ48Cg6L+zPKDDrDb42Cih6etQSD50Vp0zByLT2
ZVv8BbZ2NQSvN7IE/nMW96ZctBr3CDVwlZ19ZkRyt589VEGbEiwZUEkDsBA+E/rTj6yVD0++
3js4SVPdpuqRRT1kMCxbhG42N7D/yJeOjt70jfXVGeoJf+KLdykYGa4sDanMuaHjg5eXHj4S
NU6/GDs0iY/VGo3W1kyxvQ1k/uUEgS08OC5oYjSkYbfCb8g3WL1hnTMkaG7B2KIcHmsm1k2y
A1J24kk6361VRLjQ7UN7C2p23+J3mxBguNxFLSlEU7V0sHbW6dM3+LQkCIuKSM+ZFHVcXwLF
W9TMBKONcybsF60w9EeH8ud8pqm/nG4sV2dz36wHlOwr3aanAKkHUYYxNppXp+uqdniJLl2F
QrTrDBvwU5uv3F/jDjw8qbgjjINvQa5u50f6VfwGoB7aPXcbbdlLjE+qQa61+OoIl/7W7IZC
rNaybrusmbyF2JuadkkiUfmYzfKjT5a3Y+2NYvLFfX23i6LoU95j6GsYOzIw/2jh+gZxcgZp
JXYZ8y8+cwl8GhBQ9s/6PUFnpC1FxWaj7OAW5TqZDuOlFx8sVFo7ahzFVZAXTxtO11vTfWO0
Tbg/JtrhhUvdf349QWFBYIydJc5vQdLFUzxd3qT27FEr9mTp0UHTPTYOSJVg+ERKDFSbfn1t
f7ptF0xpf5Hv5IQB4jgVRzadAPPzc0/nsg27i0hAaFpkI0fRcIDpNy3gjzlajLlGC12A8q4H
dP3d0NiQi0ezuTlWWMPdojmBJTyvMsFdpPmYDGzZ4V2YZz2B8HMDK3IxZPVmn1aC+EkFycrG
E9s/xsOBQNtqlqIdmhvzR9IScMjDvJVaJzn9MqnawpZA6WLJn4vnRBysbe8f2BLyd/f3Ff2+
E7mYeini4DRHPRRlRD9a+ez1U+byI3S3TFvMXXsJ6TJrgp4Hp/qs2vOPMm0CWf98jOKSmvoj
GKywx1MROoqGaV/9pS74ofTAlllWWUYzrcTiqolf5W07dnAOkX/h9OjHph+On4RZriMAYxJC
I8XPpreu5ETC0K/4Yr90NCUoLKdoMUiZu+0bpYvY4WcnZrP80Z50Px+DnquC6VGC0j+PKjQO
ERGVRwJMGCIYtIAJ5kiupHk8dty1bWrzQX8d8jNFGxfV0ymRVqbmbLcDYsVopq+XLC2XS2jf
+WvIB9lE5ictcEU+7fYw56ICP3sTYFd7EaPJEJGDgu1a643+arj5TDfA6YZWwabdDu2SP/Wu
LpAdcvl+YWWbSFYSemuKIQNbZLwjSf0KySwhKSCqbyc/+BXKqxwlvXxFen3dK2bMaorUgY6p
TWulHzCpL1dg+bmRde5/p/a6ce+EieayeiksdaaP1iHXzT2yEBtnQs/ZpHPorzf61f3Cs3kx
y5lwZfpFhSe20s2A36AehVAcD7Ct4fEu3OUNDeCHQU21+o//VFXZQ+NcwgQf1updk/G0OGSn
9oniVspJu1RGbpt3Vhg34GJEcM1NFz+NDP3sl1rROD2bw020RJhBsHtdBCy34duytcZ/EJ96
9v/ZVEkQz/GSfqfYHpqmZLdHz4tb6KxfwCzfSnfBomWx03bEneghfHpFVw7dS6fJdy8M7CnZ
yWkxh6MXZxWmNu9WVcvWp/VN1HWbAdAm2fUYB+5c2UNwCRDCeUAz5INMSlOMWasu+k8Eq+4G
u/YrHmmAaaPRLNsfKj0u9cMB3o+Xfbj6r4cNOSQJyR22uf+Pu/cOayrrFoeDIFZwEARFAV8d
G1JEescRxHGAiBiRjqB0CL2ToIwFUCKjSCcISgmQiJQIIUQFRLpIr6EHgqEnEFL4juMI4rz3
u977OO/z8/IHZ+2cvc4+a5199llr7VX2xkyduGqaU2GBv/lCPCMEBaR3BbYVDpXK27zRVeha
tFNdTrQjC9n2TkdH6pJuQFeH4vhldtjontD1Xu124BWxdtW3OmzfPXOlLweowiu78PvHd+Tu
9vhMQpYCLTNalBR4FAu8I5+N66tX+RGBU4TLLrsrSRtyZkXwZkULPfNTNBSVMPTqhDnWySvP
k/K6zwbNmi+2DH8AeGRhXxUYj258s0on1798HlTdhbnOuFX6Ug0aW9AMFmbUkB76qBziKXVt
jvB6e06bP9qi0wxWSupBeTP4NV2EvuLaf3aiq5V2Wrd4xUrGZusFU+9R7CrBJV6cUtmMXk5B
JX195T7RFy06tRmowv5/XSFi+TVP7TJvHp8PibGSCON07S2xG1V0NZbr0DGEyOtmHFbfyZNF
MY8sHseB14tn8vPkfznRWkk54cpK/ILTw+ROlXvZlPESS1H5JeTznBcKW9NK3Qz1a+3x8tp6
4JL9y6v8/C+Ab1rkTXndoW80xdWulMj2lL9pH2dIHC9kn9dB6ER6WMmrPspm2b1uzGEOZlaP
crWHfh5oQ6uXo7nZqNVdHzA17MXB0ZZp4PR5b9vqSGbnpJCd5gDjyPkSwNO7TByuxP/j114D
yP7oQBhX1OB23VyX3CO0AfA1x9gb0VNjYIZuVVMQJWVzcPqVcbmQqI1xzFCc1mc+gW5KFbYP
RTkV9xmugPY8e+a0ApJuPTi3wYiuiReiGw5QPNQZLq47Efmvi8AjG/tX0f4E1qudFj4bsTro
FGaOEWACPqLTjKKI9o4XZ8B635787Xt77nJyq1Q7GOXMhduep2hOH6a0FJQRe0zf5pNYvbu9
avUFsWB9tIOCj0VO8kmaFFYuyFJY0iKc7l7+7sRPe3Vd8n5JtrJ3UMmT909X1Kt6G04bwl0E
dBLKX9Rt5iMXpVu8p/f3l2A1bhtXvJd1pRPMhEMiZRmT8hu8XgTlNL9Q4O3uyMqpMniaPjim
Y9lrXqATwu5cC4Fdz6fV1reFtG+MJCFPngjQHOqbSOmXzIu3XzwXLJa0uQsozBFgaeOHzuth
8zyfGl5cASU1VuYsfVldQqJJmW4YXmslNFVPm3VpMO3oGjbWJW2QDhQ3QaMdFiHT2xsEabwu
egwjoDxMzxT47Zas1Zv7gYGf8O24raPl12iwdM1sYueLdsdlsvz2CWSRJ8fh4OixM35Hyw7g
+YkVhd6TmiXdEZpyQi9Wqf2pur0anBj8xgVv3NRz8GpXNatJUwozfOqQ2r1rb6BANpWPiEXu
uWySbtj8qeCXq4h/Aut9T/7hQELQ9nPkzNsG4IOJyyzDfo+TckGtjAcqKfJiniXcoAXKzKgn
vtEg0TgwA3/9jI4Ao3jGx3FelyAXtuH6c2BLcDm5zzmWV2BSaAUEaexSEdWHW1huTMikvJX6
/OX6HVZwWeDK/LWnQF4Wx8Yu05BlfBfgfQX37N1wuQRch1GNadwxal6ieLwkX05MxEh9DJW+
oR4iO1t5Y3I9V/7e+iZdVSYnWzBd2P7npAs1CTj/BaYevM8rn8L2P+H3mL3PuNLyKFmkjOZt
vk2dXc6qYUvsXIvA2B5E3pJ1Jr4mdtecHbpfnddjBeSDdyOSbmiqHHSc9bsbrNMWrBHsWmAr
RigaPZn18aX5Ygvu77f7o/xyRwPbyQcNLzvZygiYk9vXI7ICGps7lrP00t7ewPWcvOU5f+OY
XX4zjn6zOMCEZmdVRA+tWaNNW9GMeTQ9fN+JVtWA6fEAWhDr2vIRAFfRQOQXeY1fX5g8+Ijb
dXkFVGI3YsZ8eTVuDfcjtN5c3oOcpF71nh+1BMwgMk8m5ALwKO8g7+re7+92ArJFGopsTa6q
sd/lvZw9q5N3oB0O9dsr3qgLn9WK4v2DatohqzRdkZOMYjsshcDsiG1G2h12wURWm9jRE5v3
HpiDxu/pzXSHUWX7j3WpqCN7ZyWb6all1p+o27BXpdvBC1GdF16ixiqg3c6y7Z62VWDBJ37a
IjQibZJpMUL6vavQeCjSzPONGFCXEZVbH2wEfSY98An9v/z/jZZGgeUnbQJzxyuzkB0G98RI
wcrM0Er0rfYDebZ3TdTLaLOF4qosn4ACeuqjn1aHsqm+uC8yrjdyVgEH8XdCJR8gVl3Ku63H
yr5/ZfF00mWMl4efIjalnfueM6GjtxZZz1W4ivoDA5tTJh8gBCbNReoopJJItNk0tWgQTAqT
DDQzHhoxvpVPHLc3QcyXX2Wfv2a9SuYBP7T+nUzTgSljqHq9hScRnofZClfa4/q+Pysn2lK4
urWxQIx0t4aZ+kVhuT+R1+eC/ocT5IK26TSwJZWTsj0iGjz6j3WWjhKj7gJJnXqe8Bk2/zGK
IT3tjfML8m3oNL0Z1U9ccOMxomXft75We7zI4hLaCMhr2wBkVOm2sW0BdTpn2hUY4GqsthY4
ArVECxNfhLB6g3Pag4Itwc9OfnbTAGLvzZPEXcnMfa02GoFsBZydfW9a7jFE+dmTTU/RYJTy
7sEqWfM2SEJRpFd/EG0FFPJ87OBIHPel0FXG/nvg29b9g6iipaK3NAaWSHXJE0XMP5K3Sthu
PX5NTz/YGdN9r0RMukGaugGyOhhHePJFaBX6zNJ1N3uq87K6GEnPlCC3u+hdba8+W66P5pju
1jLXmM5OPffy39/Wj/VrBLqkMHhxoxTg/jmcYc/o3p40AY4WKhHrbB+CD9ADqwixhm9z5q/H
7l8lKyKlpFDbfOAprE81SgMcT5jkPu+NIggFiHT6MtjpD3IN2V41AMajl6sYfwJfORL+sz7l
IAG/PYUqfpqbFtu70QgRleLu1hk7pJvUUG86dvr6Voufi7q9o7y9eTRQTNm88W70RhmqkYHa
iC9dZgy231Zst9zHikOCi8WfKg5VZ9voaLSa1ZSAoYVbaieuwRLL7rqTe8EpDQ124Yts52tt
9Jefc55x7A7xkNO86MLmdzNoYXFmO3WqsxAtFNsOdtS2tvdHLmcajbSce52Bnn8y2Z2xr7pI
1lcaGEpE7KjsZ0lpPdvWWt/kZ8JxK8RsjqVfA8PZE6AQZ1MIEl6sbUwPzbfg9V7CFvvjUP7w
wT3LCppwaE1Pbc7Su3ObV0c40ZNjedXW0+RF7iKFjLc6VzBNq8kg1G+8MQ7NDJDcdlcF68gO
r3s3uwLySj8JSLFHX66i/rjABpnAwYlZv2vu6R9z4RXpG32U4iSBrDqpllHRyvmxNRkxNkcI
WVTKhWp8/wdz9ok9T1aJ3Vw2icisasC95jGuWAFtamjPZzAsL/QfAsydTO8/6qjgQz2wJhj7
abu8meVicEIOc8bu8iryn8B6KWc6S1vbe2nUuBBO5ddh/uqw5+B331OtSEScsRNhnhvGK1Ig
bra9cXHM1A5GhoGFktrczGuKV7c4IbtrnuEzEeCt25MlSEhI8q8aC4pcagY7FBHklw+ov22V
pnFVet9rO9aqLNPscQA9nzGZkCEBTOSgWmDtFt7+ORYFSDxVwZtAd+9K+L266XI/TaKSETNg
p8ea4ugaz44eHoX7DOt7yTrD7CB8suMRhcwddTu3bFjPnb+3vsmoY51pAmQlNZyLvokYopAp
w5m2DFbuNXO2hICutsvZ9LAk7UbKcvFYgT2h3aZZM2XLgdVxuLdS/2i13fYwWA0qBDWe5lEV
I1JsD5NmrR+XHhis2ic6JPW4pwnu2VlAnJRxRA5z/Gy9ivrjAhuUA3tsdIJ5OpX7ymh+1y7h
WDCRCebLi/jdsjl1o6fNq4HqWZKzSBtkoPsMOqTnj+3UVVq53HxKK2dn4LeVWQTDXuyHxWWm
KZAox8Ib2kS1P9p1mS3Ffty3fA8RhE9yRr7hVNFaxfwT+M8quCD52dH2UiWPVk0nx4e6DzI5
w30cPPg+6NTXztpowjtFxTSBKtlCyvtMXmcgtlv0KnqpBpUIGAbaD88lvzqEFzyJthq19ews
MW/bzZhXiThIdkzavhUXXHCRad307hNdHDeSry6YFhlcOFGQTnAV83fsKujpRr2BIIYHBDS1
LUwTe8WGFG7vCqYdHs2PlWMYBgkm2MArAUPJwfV8+Xvrm+a97qJpKc4TW+RIW2QD+VcSi3ZQ
wzKbVSqN6lIWaijLGVS8bufAEJi04bTW5xE4xPqcxe+MejkZUqY/HKPLUU6zrMne4HyBueGy
uaCAKahzO4Plxr2P7f7zic84P/JRt9p0UsZYgvHLCgiqvndSGBELbkQ2bCLqHI9WezbVY8G+
DQMKREwsiZFXPaKB0oJqgZ2dESU+XSbqBKP+4iyGxL4S5ju/UnEIMSavDQw/A6i/yHnflC1f
cWa9CdPUa9EX16dWchk9ajEmlyeOjJCLOKDRqnXS9nsbMEE8wXNO6efI13xLYb53NVTaZKZ0
9n50oOSFZcYtDHs1VU4CkWKJpZCmqLzjvNmM1Cbe8ICF3gHR5fdMy+AQojK/6Gi9RCA8gisi
9BNJ23XIBWEGVj/v7WdWB7yufy9dXSKb1Qls58jEPk7R99rnUIEaaeBTDaQIMPhk538RRxYB
k/riV+z4W/PbJjXWlIEvcelqV2WJLlVjRl42IBo3aeqoqHricVJBQYyTGvqq4BXQ5Z/X5Bg+
UvtrphHgwv5mejmDVmDVOWCnS+LENhvERRkrWsDqpz90AjNdk2V9f03L/dvN/TA/cIRaOEl0
eMWEFHhGBFXlMcIgRhTtieXfQ7pCAyz4T9qgrfzeHIG3Lsb4qYb4CsrBrH9eEzT56O3Po5gY
iirSiOA+QfcGXn+tofHHfgRJs9fV8FSisjzzxW5DIMdZ6Hp2/Gf1VZD8/Bhvn6psVsp4PctA
xj/RIFt2nDIq6/A2nrUCcoeomyw4eZf7+Cl4G3b7hBz/tSGeNpZ0TsJvBcTXM8QNXlBqy8Gn
esB/SWFv12vglwKqWmfVZ8BmQQ+1PlHFcVddzxtXCmRPBFflA9kTCz9gdIHsiZexTizKzu2S
4wHZRs5BHlZnZ4NpBjFPP2ZwcaIuw6MAr92B9Wz5e+ubNmGjLIu7NES5XfYZAJUmp2rRvsu9
qs30gWwV6cG2yNqoElgQrZ6ovJjef1dCGMg782F1mM39k16xAwNE3pkgdl4JxpJCjSuqJt0o
Gu+4vjv4Cemqf1Agzp+sLAp4igWbwavCVFcxf2CAewf11qu75WDyWwqx1SxdnzDtl0ElDHO4
qvzLbmnJorJBk0AWZotMEa0QMszLP+eukrqbrz1yZ27KxcK9rcsyiu0byfiJ143pUx2gzNJD
V5de7CJ4qLIzcTYkKLoiXyxuy+5VxD+B9Yu5yfy8zkXv2VGb40AFyPhAc1oc7cjZNBuY1tWm
7+3KCxKm+4gWeZ0BynwWDYNvjApH8UL4Rasg1rbm03Ot23LabQUj93U67pHTZcoCBQ3GQgjj
ubWaJ4TsH6Mhck5lV19Pk3CI1L47i0dzVDTVdpb/RZZErGpgiAryaJnFG1TK7JnmVk8N1Ut2
I3AQX2yz7nm8c7zF4FNt9oMH+XPQNtE+3/mZNGDHI1V/bZVdz57PrW8zRG6QDRyw81cKeP2B
dwWU42x6c4poYtML372t6P02/tbepEFLSk+bWaQRfpqGigCm/LPPlwdtJkzeQwrSsJsXmoSY
B8+3SwM6RyI2EjybWh5ycFZdv+bW7SDsR8U3jwgvogOFHeJTV3F/XICTd7nAVod9zk+nv4+l
j3JUDJmiP5pgDthWnzbvzmnxr8sEw3kilzeOL05mahyZdt+ylkKJeycVXkEFHzExxvlRD4+0
SAf1jY2KpWwzauaUra6IOmrtx9I1e4nvmfxgLFZ1Q+8rHv2HJfT9m1DqER/mWyqzUeEZifnp
HXoMj/mDvIdhl5H3hU7n+kTGm3sMtpOm+xszK+rFjwIphE7OTX6sT3CRxVcU6DIbead0R2RT
fLGLHVBB3aQ2I2oFNMzuPLzvL6pMy53zAZXG7+7u9rwGn97OQKahXqAdJn4Rp1vXySfbjFSQ
CShs/aBHS2qIzTJB+BUbHILHbSn9iid/a36THKODMK9HjVcMvNkXsrEHd+MDY+ENko+pzH3G
O6l6Tu0BRTWZYNxa5IwcxToy39mtCSYHctA+VuqvzoVk9XotFe5RfZ9WaToCtzUHNFjLfCt6
9QFkA7f5327pB/xhux453bnWU7Fy6woo26p5cgWkYlM9yi3pfRJTNCVvtozypVj9TNac5Fpb
0Tl3qDy3pbudU4Q0EmdCwL+WsE3ckI3cKgtydagyXllAL+vCY6eqCRbKs5ovQ885rOfKetvL
/D+brhjEJUD1aznImYQ3Ej9Gmf/t1Pu5jJDy9oyOWa1clWzLTJOupMLprfZV8/bWLVaRPYhD
4Z4aLNqrV812C2ZjOZ6Gssvo141pgDeR8cQ8nUM+9RMpQJGsR7EGJRWSfWlt4Ah5nk3nq4Bg
0bLACQrt1Wb1w9Q7Lcqd3S+MjKEJ3W55t/kotIqSoKX74BPrGfG31jcu4uIqYx39ixsdaNm9
RnONyezUa0fO9ViCo8vFOlgX2PnG9BZxzf0n61cvz3e6Q3w65LewS6qsjfdghEe5m5nvriF+
M1VTi3Tvx+TkmCCBDRWY1rWvntMq/g8FVBlkCyyOGIV7UQzuaZLu7rfRPB3EFvG7q9THRvBr
Yz441yMaufJDP9PEuXM523Qu6d70MgOWCdfNYU5Eij3cXfKuFt3h36aLNehF/uEjRr0BefkZ
4dNx/fp8yZyp19ZSHROOsrMfs4wXhXcmcDyw+L4FuYBxfzE2+eCQ33Ar0vcgFuV7ZmPXYpCd
XQs9dYQsKdA7GvRALSFE3p2NM9I0uf5Ed/S+f59okYq78qt0QSeKSlRHa36aekl4gd9SqsH5
v4iZJA2/seQ9I2nYL22K7q0m8INCNeL8hsVSYLt7UUF+Jahmmumla5oP9/639sFv2hI6EITW
71+u3iTht7zd1ReYh0eBeYj5zSnI83iFyXJ2uz1zNm772irDdZZa+XYWKsU/5McC67W5+S5P
vpilh9Y3xi35WM/JV2yTX3YqQFkuoZ3ifaq7s/Z8Th2+/kn9YC2ZzGzRHQ28vyo9tcXCubmB
vf/e+dkpmMMJ+GO2cdidYMPX08voyMw+CjV2CnAKtQj9TB9HRMgFx+m3mJ2ZZPszwAu9W0b6
cVF/N3b3B79lNdethD9yx5kDa+LJJ7T1S/E/HBsH+ujRAwYyKVkgUWCyyd69olUa0A6zpoaE
8rbaUxVNCuoqhH8xn06dRQgMjHfIEYWKiPyihzVryt9JQn9T6+lMmnefaitlyl3raZewQLgh
4018KkNiBG7AtP7igTDdU91JwUqjh/M3lB3y/FRSsnQTpUEo15c18/faqJ/59vn4TcKENtxc
DSFIHTwjDW9dwF8AVBa8jabcnsct0rzuAfsGbwJpMqpbMbCJ7NEO+ssvaiKe7jDLJYgJLXld
J1JFsNFB2I5RCCD1aamE2ARGPpASMKH0VD2mQwvwnoRG7l9CP9/TD3zctqUpRTpHWWWoDd3H
VHVjEZ8lODPf6YK1c4mbRLBTSCI15KkQLsTu2h32Cf61jQCgfBI0XLns3qxGPaz4TXzQB3m9
c4B39u5r7+YPVpQt5UcSqfrS50poip4H569LvlzPoK92Og3gEh32mbHiC+ZRLSoGMVZVlxDa
1d1x370EFlAskc/CHdjlIyyZoJaC6Soa6QhZCl2VhmLLCRjLKGsqqoA9KXlt/PI2Uy54jcMh
KPHWPMBGAioQUfDKbqH3Dbouoyi7SHadS1PWV3uYAy6r/OiottVpwLUmnq2qpjcZeaD6xfDa
kzCDLMae+y6fhev1PPii9U02kNvlWBNLDamZ4R0Eshn0wDQUXRvHfGm/CL5rZThn+zrRAudf
CD5O85sypr98a7169V8WTT+U5oxZ2Q/Aihur3uBFWYG3vMEz+3deq+HVzC7RHtxV3oejSGqQ
ukwjCEel/VcRf2CgYN94J1X3mLkVVoZY3NDmzNgXSGaGRvZHxLTtez+VE8L2zQtLlBX94KQC
h+L2J9xfJdWWcD7X6pLnlSpnC9yS92UcTYhiTE99aXkn3pJX0uPgNgIZ5yc8Dc2tucOc0ftp
Fe1PYP0K/Y8Lyxeo9QUCozNWB7EpuKBbiPxkDbiSIDIypood1btzhk7aeyfgEal32sssZ+6l
TN0feTbeGq5LpxP5NTOgPLI7GgD/ZII+sD+Xv/QXFZxWkpYfHEP0ZE8eITlWDT8FdkSMMPVs
rb9lwVhPNdD6ptl7S6p4T4qGbbHdJnirr35iXzlB86RmJFfMnLJtKzN1Joro1kdD8zQ9T6+i
nwoO/TwGx9YQJ/FZL8NiW7Iv73Z4kvwWZurDRgNKgOhFJXVdqEF1sxNDQtWIfur/xLTd+GRs
ivhw1OjuRYYZv0XOyCu85n0+42Ynwib5oAhkTmfAwgoodgCIH+xYZdCGN14Ntm1qqR6eRDdW
cbFrUz7AQA5hFv9z5r6qafOPtiOXHCywevv+DN+9JfEzXz8d1xvsLKibUAmlwZ55cm38YjLe
DvPgAuFDWfevIr67uY4P3rH317kes98Dp6FLhx/n2gB26BRspPEs6LlKoRHa26PZfjwT6rGz
ZLkLRVkBjWq67E6v49ZXMq9zjz2ZTRFUbAzzte/N1Pg4O198JqmjKT4r096Ht6+EcGp3knZR
dv2yqv+cKzGetej+36cG+aY5fNOyyIiYEIIRbX/5CjEflbblzEh7R/SoYtiC78KHvAOYWMFe
9nlLrc93BAJUD0a5UQJrJ2Bkyf4QvBVeJ2s/d8NY+VxmRS1208EV0DsRgqYU0u6U7yrKDwxs
zB6rVTPP9YhShVOvv4ALWXEZeNvjR0oKW8cBQbiu9egK6Fhlzvwpxf2rRBaYj5nO9WZ43Ijq
vxeb00FTKmoa4bLwhqT0tkzdodG4/YZFlPi/2iRbH52cTyJO+HvmM/ZkwI6l7lH83s4gIC4f
n8LXkUlcnQkIqPo9oqAqCyYIeOsJbrcYbDOWl0KoGWZ8WLx3PFyJDe7NyH4PZIIgl5+32bTR
E3/6jfrtRCI2e1Eh1o9QNFiL1by/d3V3QX6O/KsdXjZF6kjAnoTjmaqcB+IRNqhCphODWcRp
XesUMRGR3izTK5a6yqp/C3yjFUJA5b3x0BgGakTdy79Bs66ANHcDoqyT/qo2c5MjjSYapim1
MZ6ZirNeHSNsKn+RiVG83A54qxV6kzWrrwLuW7Gil/JRFaMPfr8cw9p1LzzVDAmTY/DRObxX
0X5gYCNuTJZ/7LZ0MPglhdimqmha0NMza92PqN0cME6NHgl4lUaEt9HKn0IpXcAUVtZaJbUw
qa95+POSjXzAvcDW0rHSQTHV2qaOLuNvI8VGl/gBa9TAKsKfwFfy7z/s6QcC3B5wllLGCnmd
mWXNBPd0QhF/JlmMHGqjyQ01CnoCFpNRpc9i38TDsUXDb5snmF3cAi69xHgc4XSrXVBg7AWg
Snj3TF8GfL/CqqiktemimRc0BX1Y95aNeLJo1mLQxG547IsjFadq7vbtMKgPnxaalegLXyYf
gB9V/Yr69bwAgb5xGvMtN1jMJXU5XlwBGQHREZqjJg/opyTMM6rdLikpirFDXSdWQIqXN7av
Xp5L0CewZo454iQIuN+/orFjof3TOhCY+2Gv6y/KHw8gdzzD+VI12t+7+tLKlB6lz23ArqL+
wIAAUjAfb/I6jxTeQ4jt6b5XTrS456l59F+KT1KMs+nve2g4GtUAgepeZNhCrMY2+IV+ppXD
KaAgipnr8YcmC9Qry3Yr35wyXuNVM38tx4hldM0J8JeJuQKszz2rCJ8Q10fSA4Fv+UosdWVj
rLw/bkJYP4QRcumeG5roskfyuy/O3Hw+N95PtCqrEWLlFpMVvRzjDaf06GZWb8I2KZtR0N7E
sUg3PX+8zoMnTiF4dIdrB5GZSOHkPoZCiUdMxEdkp8zKfDirkBE+zSfzIWzhLzac2nSpQeFE
wPteZUMwNEFYI+aBLIX25qMVOlGKj8yX455+jZxvHCHrS0uO5gfS5eYBoWv/nR/2t6X026w6
KRRUOx/g9lFccFVXQMzGkgFDULWEf/nj0YLflyxwgUjbcQVciNvHIMKStcdw3S13j2UWCerX
NU1sLYVFO/dPh9kRmriG3YlirWVq3Ut4XICIEDexxubOxjN/kflDH9QsJm2BRdryDYVYOxF/
MbgYFXpK6Bwzu5oUe7s4HYikLMg1RUaeqwXK0GoMrFJabN40tIx9lCJ5hTY9SlPAO38oZDTT
T/Gp75sOkIJKNROprplZzWxFUUwD12DoKtqfwLpJjlH5nSUdBYFfkbOqfHT9D5Hvbj622QRh
wiVrDs+U9FB5Tp8tmYbrmmTOXw9Vu9WNOT/CSHLVwKgLFmckP9ALKuxqRcUDSbZAr7RcT9/0
qrvSiRPDFOlbSWh9zpbBtZ/6KZgao+1LvdTUgm7CdbMhwPa966jV4TF7CbX9dXjjiFHK7VRz
dEhpJjhflvbKW2s9+V+3vi2SkmsXNYAwWlLT6rrIOg2dAJy4AyBAMu6UAZhmttLxCqZBX1lU
+/s82mK+ZPXIRpfVQTZvIEdbQLzaKl/ETwucucc3pVsfrMwo2J+SjHF+65p8oNqtH7xJFPFH
34kdn+3jq7g/IuBdhIOZnWkqoPpjHekO97XsfyuZmW+rOLboE7cCkh0Ls14j6jzTq5pqxbUU
Bizuj7q7i8r72Yc6mam3DO5jmQhl4ZByQOGjUC4Qp48BYorKF4gfL/GV1JGSGuuAb+mJcaK0
fUxgOfHPJbAE7U5uUyEiolMOQHqoqqXyViTzs8xURH+yh5CyFUmqkqGmmUbqHCC/376V+32i
KeDjU/wmOoafWGcNpFSY7sk4Rf6LA5svTILdjo7luLbxLWe8foWCTy7/DtM6Bz/SkX4wRpS3
g59Y/Kb5KGPf8YtsLYuBv5D+i8O3BQtwqpucVMOq7kUR4UsaiU966O4UQBZOEt1jQlXkKU7R
dOv/7fTL9JHqNI4LoZ8H4rSayoL4l0wMuayAXNOra55ceXlkWC+9xvHFo/K0qlLYOWuRVTnq
M84PeOSoitFFCFPEIG5ZDK2OFVDGIRhvwAtbY6wfBBF7rg5Ry3Nd6zNZHHqzGk0of2ecB8Nv
rlQ0RExK3X2z1oQ8IFp3dANqBibDqR3wVBtXjYE5HHn4GevT8T+aygG0/RI53C2nLGL25NHM
skoHarBhzmA9Cz2AaIxXms2egSbycNsSGnhF26BYLFHIMHP+Vah11wroZoAlZvBWU2P4NPne
JjCOOJk/jqzd+jkQ4mOSKxVXr13Pi9xaANtMni2blBxrPJv6B+yM10HVh7x8/eHTg92dvnCv
zFf01PLQ9Qz4uvWN8jJHaQYxEdiTEuxdAVWaNedVL2buxDRyzXzosTzt4OAbBMvMGDaaM83g
+LA6AKcVLINKNwhQQhoXwfUyR97PHpzjtDaTW5I0BBfp6XZv6lzt+gMDzLhpftFeIJlsgp9a
rCpTKoeQKa2BjDWoAaZsmNZnwjiGoaqWVvaTxap+cwluEDFJVOpPp95XH3CZb6jAARHOYs4m
WM3+3FKCHP/MZ5xPx/+siYJbyUfwNf1xjfEuCd/pwfe5RFaTVAM8YfPkxJGek2j1cSMS1bcS
00ChzRUCVao3L3PXB2NJwS2jwze7H4LhkA/4nSsgOLQqzA5+VOroX4TcgWGXPHT5Xlhl+bLM
tJuAYA7pHsBYnBSiWLS5lX5o0E0PQnyVOTrMHk2Ohs5z/JG6ngFft75xwoJU0ppggUuJGlP3
lpCb+Ycfm82ZHkY6k2VcjeYMQdOrV+W0ZD8pamD7vUiXo5PaOi/qVl2/J3Z/76bqxPod71Z7
/cAAN56lkcesJ6Xf6uxHHMwb7VwBHXr7ZO+aZyHnY4wZsIymO5NnpY3mmveHsmONelLK9wQt
Nw0FvwMvrad9s/7kKb2WBt+bsjLzPXs32BZWAk5fJc0kGl707XG31EsO+S0dMU5H4+OSxc5i
miht6WYoWG/Yoe+dsR0Eyg+et1nGPOSVMo0DlruuWNhrpNjYDZllZavIXochg5uyKyCewalr
jf3EMGlhoKIVsLLqPqwtM8+ZcbNdftkzO+fYzuHz8hNxXGCfmvyP4cc1n8KPGcIzgIj8CC+J
iijZNZgbojcpw/avR9Z+4aawniufW9+WP1WYTdXKqWrS5c9khBzQ0D+ynX/xOjgMkEKzi7RD
sjYpfb4aSH6OVItIMF+a3SHWMooVPISYVTgGVCFYPf8jA/LUkSkNOypnl4K66G+BVzvpdlTA
5WTjKkmcGCQYwXkYgSowh9FOgfDS5Jn5loo9bKIxIvZsPfdLrdWefwL/MssTzUP1jzm7ORgX
qZUu9Koj78UibkPIGVWJi8+fO+J8I0OYch0WChItEEMRcuSloaAl22eX1H+BxVaLE54lSA/9
plXDGyVaaI682Y3o97ievP76/8uWxKJSezDhGPNKGlA2IzoXMEvHigO7h7x3+XbNa+IkmpjQ
HT5bNesWZqyVFM6NLE8/GtUNa1tcAPL0IIE8PWL3hfz/GlgHbN59QMr9AsEtuVrsSD2RGnZU
BdIfWRb1QVz1/ycM+Ovb/rbVk9MqKoO6RB8ZCl4BTS68pcuVneV++ci2wikiBGWj8U7j5efL
cmCwCtHzulln5gom5hInRatrPIG8e3u5Qj93+KGPHR2x4fTkVmPnngV/pXjP6rp4C7F1U3Ro
wT+3A4zVq+7mJoScFJ/xqqnYsgLqIHvMTQS481x/uZ76r7zHWFrQlmhgsQx6WFl5BvHEkESb
aM5r0XTfc/y7G7c2Zo21I8XEmbbh7Gd+XMyEEDrX+YUreEE6pj0rnmVmS2pmm9zUvL/7YAzC
i1+cdqiTYpEYY5ZDDKcA9U+F53SjyWhDfx0vApz3fQuFdTMrc27D4l+0bS6ZjA4bldPY4RRC
AALYRwF70/zDK23My9KLv5pjLnqaYCX9psmuZpCiab9aFKaR++p6pvyt9W32LZ7gwJiOUWXi
0D3LdruNmoeTP360uSt974TCQj9fktPKQL2pgTd97yNiZnXVVglmfKsRnePZ5c/nf+gjT7CS
rVU9+4kwjwZix+6sApopIWwuzHpNeoTp+YWHOo+2XCAcaVwBbUPR5mWBkKMPQADylzl9P/Jg
nU7ELTW7KR4mPat7swcc1kN0t3Xa63zVyKn/tt0Jia6SSLc+5EEdfs8+uYa3M75R1KXMBn5i
S+8h3HcPqtsGrS/e0WBg/iIngzZNxj9AX6ZQO4WymalA7fYujdOJE0VEwBsS/dSZSLGIABJG
wCuDpePLTvcJe+tCL0yaFAcFWe6lVo9wv1TXmGOZ1cRulfabHnw31DTlhwYirN6e//TwOYT7
oDJqwccG0X7QVj9eCHoFZHWPOM/hsaxqF5jzcE8+kZCteOmpPWDrBwoHq+2p/G/mzAGC5QSy
2qU82HmoX/BSpGVFPVGsAd9gWlbqiHOKKEiXKvu1mnXBrcoIItDGJ6fni3LKLGvh+C+SjXFa
TqVdDMSmSB3uQiw1mO3soIuq7+/UXrsFZ2KlE8ui9bZ5ZsvQsGSdpm3uErCt8tNahx8Y4sDA
utPfUsXf57F09+UazTnP8Py+Rg43vk9lIknD39/WLkSBao6zGgkQCLvyFeXrw+Y01bsNYm62
TD8SOb1Dryo/Jj7D0Ssa1pbgWBJU/AAMFQGEAkp/kB+QWv2377/+Hq8KBifsk+xX4hdhGaU6
CQYFwSQCh+du7FQ5N7Ycm6xfYkuAXnJUyUPAiyV92NYyTYi4/rThTL5nQ6oBPD053RRqSazt
3AbPZdsxSPLbju3SkImMxmz7ISzqWrPYK27DvzizeXLS3rbqJc+9Bz1U9UF9wvPXNUC4LabZ
kuqnbNxbPJky6wwjGYFLxGQX6IAN9HMg9Rpfvw1yJjUd0sgjEeHdC3T9pkhnpkXEqWfWa7gd
BI/m0cAY8iM2Jsp4eLRj5AttY63XDwh1tOhl1vjIVWaSlShuGvqvQJ0Sa1Q4k942aKSReqxN
FwLUG2KcmZDldVz52POj9iQAV/e9OYiyg8e57BDyp3SHmCWP05h9182oq0kXU5pVFBDGUF9v
MyNNt6t7jnz3CbkptlSGZVzsE2wSxTbjPECsc8vi2rZQjLNAA4nE9eV9Iwsn5SBT1fV3axj5
oAJmk2nkvtpZu0pdB2y5D1lDj/FuC2bC2Soy2m2vbmtbbjWdeBJ+9GThX7z4GPUdQrfvFgoK
4V1+kznaMk9o5TWIgCyOhvn20LBT5sxS2Kbl6/ut/+r/Pzx09CRixhtTGY3AV71chsJmN+zv
/HntGs4T2boxZMcYcNts9wu6H1eY9bO1kz8wJMzQnbAwOMgwUGU1vOS5obVKCnd57+PqrOUw
FxwMwb1YU8RgtIZ9Ub/gz34/JbbfKCWP4X6JQMVH+CpwGfFr3KG6edMQUfajG31aj0wEe+Yw
tqSxfy7cfv+7pynnvH2S+KiS4AS3ckPBLnOBFl6XjJSQBu8Zfehty6Z7J71lphaVtRsNjkXe
lWOYMdyr6W+WDsOfQqaPvZ2qTCeQTVSqxEgSgFdJnfsnooE0Ck7DK6AqqFMbBcoEfIEUnUAT
C4ChNFZywpbwDurcBsRRRwNx1O9WmfQ/Apwp9cgFK0P1Nt3MqsqgS2y9HG/AO2zn2jXkaZiF
xsxdcNfqAEZQ6P8ddUclONbIJXw5SrWDhuUKs05dpRjQ8yTh75K1i4GUXjv4MGZ0TzTgKPns
7GqHP4H1Xqufkggu/CeSCHLQZfpVgWosSfLGmfMVFVulqm+Vyu/rkdctkg17oAst3hbQECNv
2KC5ewKlCh9kDyIjfPbOg+LQf5RoWP3RUOJMYIpdanNllkCA7Zj60E9EcVy3sJ9VN6z9GOHK
FAq2tqC7zzswZ4wsdkKXXuwlzOJY3B8yCM8rCsQStgiv58O3trjLk6BIiM/eXu/lYHNIBrEm
qwXQYjb+dQPAVXhC3Em1Por5mpDqQPhS6BfWkW8d4v/Jfh3VFjk1VOnW48spKhbIB1brvNrl
FwaCl2Oz+nszmweHnl5iW/yCgh9V2LaekPXepv90KTLgOShLZZwIYHe2Z9E7sbi5PG3dfBGM
UaeArvJS/9OxjkgazncWqn6J1DXSYTzK9WzBv55qfJTPlgC/4JZ8rgnfnyjP9pf9LL9e2XQZ
qJ9bQ63DEwYYSP2SuapuwN26KU1QN/ImU69qejmFcNsL22FbD3P4Ip5+PQP+m5bw0qwG5iJ1
f0d6C/EupHnOiUXYr8C7hiRMH28ZJl8LM27zaG9dAXVv5n4Vunb2B4bkKX1eCqUPnHc1JVZU
b6PCkaj7Ll8IB/KzgyGWGeRTqdXp2N0O2DnyPGDQ2fQVvev8M3IDFpct9+XC3jgiIxy49Rfc
qWkjTKlW2Pzd7eNf4f3vmsDnGwX/hbq9WyBQTZXGIsx2WAs0aQiq6zceEcyjUYieI+YMqTbY
+V+ROpHUvlEzzx50UFUyI1lHYyQwDJwz1ba/6eWnkTluWZhL0C315GsZsPQ8RwhQ6i4CmFiK
j9vBkU6zUH4C2fRWNDCxzGoQ9VzI0P/V7XJa9o3KwrNFi/g/zBazxA7jTvD8vnYlbjzDCSN2
IU8cgxqOCV8Bab78P6ON3uaboCpeEPEMEXlR50mINZkGPn+fbbMAJzuwduD7ZN20yqB9rvm6
dehKziv7gZ+/+FuvjRLP37kzMVtbqK0NL0uQoBOuAFVtA79zVduPzpCWFqRWvI4vHjAS7Zwy
o3tJ6Y5uetB6suk+6XREq+/CpFwH7TINxUyNbvwon9/27VlOpsca12UOwLN2bv7r7k8AfiAb
McdqpKYwyymPn0DYFk6aR2Vwj2O6M5qEc8Hvmi/1odXp984cWTqx5bMm+gXh3wICE+cRUuhC
3iUkFNAYmSug/Z1aa3jOPc+z51hnF0xoS102hAfm4czQzq9Ej7XOPxTEXR58FWFEFekFMuxU
IcXqslv2d55Yo8CZWJz+qjXnXCbZf9RGs2mdCeTPXutNyv90znJgmjeFGZEt0wHnQd3bkRrg
0VZy5lxYWPYuzMFGokAWZaJVRpzu7gH4hJ8KPGIeP9oR2E071o91QiA28bO07g98oowjXASS
NeupXk5evpsnipl/JAc7b7vp9B76lHw1dq/XCmhKK8b6U9f/6X/nUYxuZHZUOhhbbda8AnJY
V7mFJ9j/iqhVNneYRgrTJo3wwBiovhf6Px3h/8n+zpPV43MiZxTlLaN6wWmEWBWgwKLW6p0C
0Vi8aup6cku0FxNOH2fRml/Cpz7rZ9GlJFYfehEsdel4iXHAvePnMofuHbiDKPppe9x31wxB
PEFLAcbZgffHPcYpbwBNy8K5gn6qobWR+IAUGSHACBB2tZKKj9R8uGe+WbGdimfv6WVuEtj5
OVBSRhXloyF1xv+2ppEfEPyM/hl23oZwWoWQptQCxp7pQ2KzVkC5O5+vMuJ/BPCE+NyZ9VFs
RECjFm3Z784qbF1DF6bPOKlhDfvwGkTBYKvDmRfDrF+unf2BIWGG1/FlsKFkm3FRpbM8PMbs
/jq1d+F9ekVrC686WtVsBTQECI3W62n9yinwnw5F4MD4dmTWUI++d1hOUepEzLP2T1E1ogAv
JRVNaoLeCijB/VVKCH8I1Iw4mNz00uPUgf2fbpdToPSpLkznxQONNlO5FVDyzKtwFo8TJWv2
EcLtzXXNQybAricXOnQ9bd/Y4rQKuaBKVa1DQBFCmku3Tj3TWkPsaAmdHQ28S8mmLaVbWI1S
336t1qx1/aEgwDogr/nUh6ePGmS2XGU1nHdW4YvkjMLLA8HTRi7+tBfTuiugn7S+fJE+krle
l/uY6sv7Y6qvhIkEO2+8VJBeEP8TQxnNn8MO/xPykeRO5JHWig3I7OGnwGJR+BMv8eJuShOY
H0Y4yzS8tX12PHEysH8FtH0Kxhmxhe+vp7I7u+2AJlNHKXbK4N7S8Obd0e/60d3E3Q60WW9l
+nEgHPbyoTv/9gGKhXZMJlh6LNWUK98kJt6+MpsYMLHXDW9Dk4qOfOq2PdflcmV+d0POQ7Mi
z6OZtUZuUmCH+Tbz+sV4btiC7xCQWG5IjFfpdjxhsXGgt2t3Qv+h3KDSN5lwBZycfnh8RgS6
7WILvwbs3RaA+xzzFt6maTmxxzMijoajUKiUZj7R+Hju7V7/aku/Xra/vqabKf0KE743TNQJ
6zslqHf5/eyUbmLhyJLTXItoSns2Kn6+Ourn3UKVGrlqg9NB1DfhpQsh8bcvNrmE7DhXJDtI
O+A2QjdLZnU7ZfYjtCSmnjbaK5jm1U6NeolUnhNHB9Xbuu1L8l9Ka/OuDNYiNZd0jBF/wQvN
lNwldjhlNvHF5/XXZX6A6nto7pcmblN56fXr8zmXbmKrw16GQUR6bUvizTO85s2iVUL5aQnH
kL44yI2zARbkHS/dHI4XYBeSz0x19ss39/vSMBZyfXgZUbiRBSLp7Z35JgeKlUN8wgG1gZqX
IJCIvtml94UissdNO+QlLFTBr4ogzNyynNbuAps2mX7UJDo7wjHjYJOsbDeHSG+lz/3BqYb6
2p5gAgU81qJS31DSThXOedNyDK2e6Dtc1HuHprpYxD+R4YRQOoEI8VEnqQZfNUdFHWvBejgD
1QUdTF3vOkkyoj0dUYtQ2MiNzlEveIPdtS58ULzoYaOLTbB2rIErCnZOSpuzq4dJnb9eDDWC
64+JBfSjgKCRLPvGEE0RZT5zcDXobflOaszYJqernVVD5Z09jEmD8Dv4wDZMfPz8VJVvmgvT
8owqw32L+Gh6ssFGL/0wOXeGe8dtTGfRqCeNli3Q2SrRIpowkXHYEa/tt6zqA+HrV7Pck/KS
sH5K8sB8Nk+3Mg5rskKMAZ/OkzzXQ1c7cJeX4djxgONDE7YSFwN/ZH7fRWD15I8McFq5ucF/
I+8oIwHvKxXGrv/SUs6BKVZMzMZjvKIWVkCzoC/XsI80r1+nLH22LFvtQ7FfOxDCAd3t+/u3
cVqZ754L0c8fJvt/WjdV1c8ze6keipOF8Krd1kAS2XJs3vRMI2lAKTX6p08PhSMCb8iySQI+
fb3EqBPX76jzOlFKXuB0sWHp4Bqv4yzrR6GfOn713ybWsNG+cMriBQfKsdvusb5qXZBtf3Oh
qoD5HZxdwvgMsZ42JGlonABHQdzU+dVvbDglbcEHfwoHvD3tnwGp2O//Cqhjm+3Iuq1il4ce
DbQp8b1KDizTv5dhkcNv3DqD0YNgLDMbLF6gkcxL8dPAomYel5CJ1/hJN0s8SnQGd6fXpMPW
1b3l6qRqolFcBKq6xeM4QWFiwX8ywbZIAPB7v1gZlForiXtvlNTgxZuUy8rDFornRM3aG3a4
NLxF+EoEnEUEvVDjobZsS+q7d9My3XibY8ds3uJs482szvoSUWocSqqN1bBzu1Vb4T0zrdbn
3q5+v9W1FG1XfeB8hF+q6hLUBK3+sWbeLiMZip7fJkFRO0tkrL0mpzhNwUC+FmqCtytJG815
2BTolJE13yIjw88v6h/HVef9nswZ/2ZS4cWuN64XEhNJm0Sdm6lmRb45ZtVYvQZvc9qca4vo
MeRS7QEnZEpGdtbP+0DBvSVubaXoPnTC0bTDwLIcpCMDLMu0/T/Ztxqn9EHj8KTECg0xZyGP
F7aPrzbkeNiUZMj3RvoEzKFpy8cNL8JitOk4bWNNdRmBW7s2DMwgY6fkPZoUykT53TvMex84
ZaVRmeawznYnpLb5W0yFUy/L5/z2P94Has8jsobOnLGLLPLGPRAZe2OJ0zE+EIKmOaJTVkB9
G6KGdujzer4IuOl1sWZQvcGPt4Hfwk9ue49yW6VukV1EWZHVrp3bbesr6lrmMNakof43NdXo
HOPc/jQHdJ+HekZCNlJND5xgc6qvRzXR/UMDnNPHVd1Z9my7HG5hZJB0pR/VNil0bAGib0gK
ZyYP8Fe3TCb1wlyUnIP4vRo1FH9SKFL4MPlIstLwzLVSXFVZz8UggY7BOHTcvJE5OOEYKvSr
FGUdk6pNbZwHacuYFdCdq3s3rM1pnpASZzo7LehSSPlBS+RcTuiXG4NfzfkfqQmsx0NM0nl1
ikb7/Bsk9uqXGwE8IXkBpUmGUx79msAOAdcaM/4kcJ0t8x+PNePAFGk+pSohKP5A1YppkKq6
oXpIsP7iArRySauR/e8WrEgLsCvd4IxSMrgI+mvOSNsz0hwnz7JIW4+/hx0Cqv/efgQXzX72
m8O/eVqZihi+pYAKl72mSD7F/v7upVgyKtGYmmzQuAsXo+0Xl5FTZLRLzw8hF+S+bU/ZMmLO
9rlrh3KSa4v8b62LM13N+c9lx0poaTg5YE2jow72cUvMJuZZdlVV1rQobXvNZDJrsxIknXr+
KHW5XGTVdkY+AYX6ELQoyXi2uW6IuPtFdLX6RAxh6WmpZ1GDs/gBYgyuO0GiO4q991JeC59O
jkd/kJGetl88Uq/+rWFoLPoO4T0hHF7QCQ97+/MTEFD1Ro/+e+PAEUnhe/iSeHJINR6YzLKl
Id3iFC/RvjofyAMY0h6vkI2KQ6ktdPiG0zg4Bt6iz9JP9e7r8/glj7BHcaHh6eMWqLSHU/FE
OLoNlWETKYirrH6Ek2sTWJw3Eui4WLkULM81P5MexlQcuNVU1Vkm3e1vKhgdydffry6WYYXB
OuICR5jUngc9TRZesrPaG56DBPkTyvWVdBvc2nDXcXI4U9+x6oKLjqoPdrbJxIZ7YRtbzOll
RSnsRB+wWx9TVt8CFRqacmImNmBGMVyYuM2PvVGptP1m9IjbkvisKV67EuJGLSVYuJWKZ5Ta
F4Kdymb5+/er6aeXLnJX9qkYzHcnxPRpXm6WlbQfGDVNaTPFu2WhEvBEtYCh4BaRoeCXXcdj
p6QmggMG3jQP9T/QEcybUlfo12EIQIbuBqOCmqPtCQUDeJ1aVYbGT+b7bXZchKlcm7GPaTD6
7d28U3WH4piOqtdOnI8vul29VhwjPgJ/1wwpnyWF4/UYoOupdlYGBrq58/q4eT/kT0ffFlXk
5cEiTR6aolw7UGN6Oh7hOh6kjAjHBKeSi+CIY+gIR4r8UvaWim6GscuHe5w7nF1YnJw6zQuT
HvZCmzhFEwUlAGFVzoiPj8IokN1P1eI+4EV5m/FuDHrVaS/OyWGpFM6/kOSIz3QSzIo4cjGj
T1Yj/S1lDFPFN5hWQieLz9CZGuJX9zuxIpewU7ZXu9BtkxB9IckOvRbILm1aXNzH9fXZNvpb
hLCX0q4GwZo+w1hIsrRRY/qpdsfp7oQZT3JGn5cxVnAy0S+EcZ4nfN3rwk0IQOoDaT4pi4Cg
91OYtdbqWUBxk7BSbz3t2AQYSlRb2Ibuf1tAVvv+WEBHR9J0Mpmj/Eh3/+4CWu76vewiUbdM
PkYwnLHOj+JPAr8yhZkzIRALtYDLCRl2sGsT0SRa+tn0Zyedv7u3I0ieWgcoov0LLLAIGVDz
QL7L6YHLS4lAuT4C/yCnaunh5X4soUIVGTp0Q1vr06PglvGRTq9+uyhwjJbvTafLS5hw71pQ
z1kB8SrlgbFPJh6wVRaXX0nt/9T7y/8bZJYH4AuyN8WeJ2D6czccAs791qFtNWFVSej6oPlq
ZOcFEOi2QVHP2FTmG/y9ip4AeeN7qa61VPG8SiZFaG7ueAZ6lrIk4wrGn9hM4qIvVAyKim2l
63THt4QLUi0md025/kKCqr8lqOeXsZHbbY3sG8an5cEF++uAgfh82qt/Nw0ex22LeqH0KM/O
rL6kiHq8sLqJmIbzGbFZXG46FAOkP6RGi1ZuOHpKtk8IizbA1r0Z7wrwyyDNy5fkYESPsKXF
DleVDgEBrU/SqFZ9G06d+kndFfv0Q//xmcnb+b7BUQjsnHx42pGG4bq3iZb+NMYV3bqpGwrX
n1WDDUSvuBMf9O917OxcaIabvnfoVfY7kNJmgUuWjd4FodSbofv4pgzPngT8urjLQn5RMNix
g147dCsso3vOv0u4SBgvAPgY5yiKtlt48FF0/CYRd3bP6/j0oBMfTSY4ZdignDKC9PSCTvA8
LlYo8vJ0SSa8wPjOJWTEhCdaQd0oCc7IQc7eLx8F8G7C9bcu/ttX83gK7HHPb7RXhEVG6v8Z
QSaJHFDCIlpty4eHAWJM6CoveELSG1oBpx5SNVA5A/Q1uetclDf+w6XmQUAFhPYjNdSTDTlk
/0lPOIUrDNe2t6OjkshqAGLJ9vT9W1s0MlteQ+rs0lMxVvpNzcOwEyciHwNq5OAKSGCCthCi
Aq/u4ypdI3eV7q1iEfv4BqWFPZ6dWMp75p3cbPsberRXXH6bxgUJiLm2sRyd2SKjr84aACyu
JL6RRTZYVZX9dAVE5KRXBgAJih80At7d2fDFV+F4gwCL0enfyzAjblN73R9AXfvskv04RWXd
PcqEbNq8rCJSWCz+bg0t7ROHJtOkFzBDVh9oYgNzW46BQFokCAvcxpycqrcSgseX+j6I7Ome
vuk0DZ0luOyG8aT4G2EprhpCLpQcu44H2HQHYRhSR8xI0GM87eDQzA0UoBtfT7bzUdtuACl0
1TzgkJREGb1poC67YKV8LwYC0cWLOiIp6T1cR25YqPxroiPPfTJCuMhS+tCDPGvbFop/XmcJ
xErMuZCV+qv/Qd0s6f1qFV6ywDRYPDNInFdUkczbsUO/iMwyyFEM9iWXQOCqApCxaa8GErcc
O4yo2N9ew2a1sd/yy79OxsQ+V7IoKLZ8LJh+XOudHEtqBfRHTpXuw3yETmmZ7IfqQPvCP+8W
Q7iQ3HwTp9w+dMktOTDx0YnnzxbKF5pgHTLPck1wokwLrKfGfluDw1JnfCFJEqryFoRoz0RA
rhMNnEQFaeviZIEXnAYLV3V2dEj0zM6wP9eS/yzDcQH8R5G+KNSLdGryywfNaVVGyLgdRGMC
S/OdU8/2rz56UEdPDCZDpBDusg2ImizluaG1duoHhpwnGrGYxRCmZBWb576L4Bol8kDxgOUk
OHMJeLT/jaaSp8wssEhJMc9p9lTVm1CBwHeZqvOLOVnvkfnurrAg4cWpc2VIYO+ZkD0cQwec
Ft6qS2XNyjRZ8R8OQca1sO1fc/su6FPxUPgtP02OKq47oZ9I2u5MPiVCPzSUBKcThGY+uFuT
TgPYM+FVu4EQGCnkIiM01n2N+C+gK4rGTSZjxq/1Zad6uYRvWJYeWAGdYx9iN11h79j/x33Q
Jt0jvzTLSkMexKdbE/FW0F11cQuQi7So5n471eUDHFXMelfMZBBg5EEBa8J5dWndBI5loGyS
QGCJ18FMD6u7pfDNtJTHBpfCKxKgJvV4pxeJflTncjFpPb1AmzY5Q2gvpk63fLfAlrmJ66/1
GvnnIovJbfkh4KzpvYtYAx1+kYyjbyOOVU9PD3fnG0Ntq05sz//z5m2gyslaS2Z1Z7paC0Vw
aEcGIlzI1die80wVTij7FV6mW9quQba7Tc4voiyp3tgq4cCBw85P9jtfbqOqv8ohOXe3u/Y2
6F6owcXHPvBFU/vxntnoUjLSzgnInt13/xpCL8W0SENlnu/JFF7XAO2L2PFcYjIwRceX0Y2L
ccMISkmA05xQozLm1emv3MrZcVP89V+wFFiyGXXLDn4EaClh6fcvE1cDJgGzeR/ebs3ijSsg
Qh/3q/3r0H7UhvwCybipaWp5ySySuXf/Ojd0ygQZiCifB76l/aAvd+8+kro+mryMzL9Qrgxh
/d4M32nKfdb7+/s2lSSF9HYUb1IzP9Uf9+LhNcse5oVWapDvcZRjBuWSj1lsWnjcfKVeSw+h
dKtxHFuJzHzrgbAclsI9HhynL7OUooN27ByFdGFHZPJsWwYTytiBLpVNcLurO+P/i0+whs7u
smiPc6NvUTa5+47DVUWYVNKwkZib9W7Z5m3iffsMh+wEqiwvTF2/7RtPmcdnvY1LmacwmSEE
h53MfzsVth8m0yfVapd+zQjpCQ07/zcxGUDiHBut881r86V4N+vwyUMgRt3H7izUNz3b3EFq
QR0OK1ro+y2MWTjZXqT+Klr/cmkKuRJ9/E1LdhwFUnZuuMF3MX/UlnSU5dJm/I5L27zEk1IL
WAeBvQm7j9bBBiMNwDp46o+kW56JOfPgN+YSPKc3LLiE4HzbfcfqoxZaFGzsHCozMOTYjPjM
BvUhhIhVHuVfz85ISSnwSiZJSAT5ysxSWpwaci5WyZmlxVH05SoD0g4Afxy1wGSom4+tVB98
HXUZC+iFNF7MvLS7Q4KP0IysOthpBRSNhvZk2L/yTcjKITkBdysr6n76sJWRgX+BawOu17cm
Q3yhIW/bb0WakrubT2zzw5eUjPndietw94OLLGa4iSzbRb546IT1mJ0y0gBKWOvLQUSZZyX3
1X/czbKYQ7bY3jOvMcp0o9hF+Lq9qruDF268quM3L+k3/0ZKDRyBZlf5LDlQSOE52Fu/OCsd
eSUlMseo+MArPFOnnQl+747rLbEwGibEwrLuYA6wQsphoxbpZXSAtASbY3fubJ1Z9zCdF+MX
3mHYRB/47GYFrrVTwgzPV/P407SH8OXXeLFRob85NK91/aEgnpCAJvoUfLE+KIggqNG2bvNG
npbZ1DqkCUWsgPw5/ubAbTCpo0BK6NtwNKplrxBn1dhCU44XvoumGmS5WPAvc5/NfyV1rdcL
rmpOb6C8CXd+cVL3H9CGh4akYjKnDNL2xp5qf0axs3Yyt6t7XVuNExnH2+HdUMfTsmg2jvHh
iy/JuypYMa8b3RbbXw+O9VW9W+ART5aScZdJC07OLskY6sNgA+LnOzxLy+Y/3Dit8u+0aAUf
UQpzpNdoegXU+cGqwuNVmMVPB1dArxUFjqyA6uPE4C+2fOHn98U84Ob3CaamXAv+uUWD8vJU
1t+EaqCrLUZWbXFmWwwzaBk20aupsAiR8ysoXojIxsf325LsFhZnbFtI4dOeNtkIdbm2cS5t
r9OtpxFJ9Y2XwmJQ8P+PuzcPaCJb+oZBGVzBQVQUWRx0wBVkV5ZER5EZBSLDEmWLA8oSIOxr
IEG5ioAQHUQEhCiM7BCRJUCEqAgRBDIYQtjDvgRCWAOBJL6tIyh673d9nne83/XlD7pOcqq7
6/TJ6ao6Vb9SsVSZqVfGF0YWmeiNoprNWOoBMmOQa/QE+b3h06ESx1Glxv3tEdyW8TI13sN0
WrrrPe2ZxhyEQbYJw0oriGKmFqhTNE4ZLDKYm35BVaOAdkE0BefFKiusAED6SiPJEZPIdFs/
wq1bvrY5N8YSUuSeRM6yMVtrCfr5YmJihspbXpz8rhIQ4ru4IaWwxMoIbr4bX8ZFZPdgWnfz
DOPghd8WUqiYQwAutikpmmnaCGmgqHZlpeg8vVa2YDNN0VO1mtBA6mPrS70DsL+rXP4FUXGi
9Hnr3SJ7ZysignAng9WbpCkTdcoJWCurD0Hld3cyW7ZpnqVMz9xrX0Bkh94Ki4+yai/H3IJn
+x2CygDGdUZ4ml3bTWiH5KDsjQ4B2l6aP4Q4ayiK2yeh1GtJUO8ZQMblM1iIocT6riwkKV8Z
5G6A3q17yherZuIcRhjaIOHqIUdNyDOJhGfeOGQRsbvcp7feRN3ESj8gq95EVUzcTNVUz+b7
uu6PHrGAIK7ZLzFLGEBpXVgEHLSf7TY4chpSLH/VzZPrwkwl/j+029AHJP4D2w0yXdPVmM+3
GxaA7YbJf7/d8B8Inda+gt3XRPg1nVEyFAgmT206kQXGFYRjF+MmQd+r4lPcckeRXNXSedG9
e06+f6x20F/3TUz9UrUPUJFQe9BxdqFrymQBY/MfoL2AEzTeG1ASO4QIH8+BZXr1urKKQLJK
xWYnrG/3rqbNs40SC9BJJTZy00SA0O0Q4IUa3UuUKPF4JpIUS/RPLXs0I71TvF7TjapqPZqU
ZkvN9p7LY9YwdTNS5IMouoSTL+VOJPBzrU73YrI13ARyBl2s872q4OXmWb3qN9p0S/Li71al
BWd7qXOIptHTPx9eraCwW1Vu3MZ6MY5Fz8uOQ3RkwfPKBpH1ZgacQXuHJ3Whra2WEgGTuz1s
mdKhRYDWnTMIcT5igVKH5lFl6q0zMerKdLIp+zpGp+7YHmJsXnTpVusXXVIUeGEjQkfTsS3Q
CBKYxacp7Q9nijEb7R1aeCo6E+vAbdpg+Jg0IbTQ17zr6Z8z1hr03188e5ZvmKiROUOGO0V3
DtrbO1BUVVW7Lso8/WuwDtKVrR5OQOI7Ccife09R86dPH5p3Lxrbv68o8zez9no1G2ZXVjDB
Zz4Da588KS64SqrGc/FJ6cXehuzn5SPdRL/N+2qeNhQZUJzPPs9zqLloLD7M6smSx4KvlTmn
P2GzfnBjs7ub2cmE9PFgfNZFp7K82Bg31Q1KMsAubWQzIyIjLx5z8sWLnzWODkCij3Cr3Tc5
edgnmucMMkpinE1IeLC2g1a9F5ynLHM3zTkFnqZA7sm6aX3/r3v/67/zdEZAGfYiMCVwWW8E
3sZxHf7wNa09DvJ6IYIJhDTF+mKnCDf/nzHdmfXkkaTjc0mgrnlS+hz7wsfbASLB+UE8Qyby
iV86sBJ+rjucGQWP4hpBq7tROxLWf+2iMgJAmifpNsMpTtaM5HzrbaSvdENGV0WFPBA9/G63
cfyf7Tbe6DwNn5g6UbUD2Aw5uJ3js9FRePMMCMPV7X1o03wrjTQ/ej/uo+f84YkL/DubXQAw
+hvWHOHqDMheNMke5UtbesNvQ43C8GOdEYgBmoxTqWcQ/3SVansVzImdGY49vAuLCaqatIvX
HfAK9DDx7CCXG1CNtonksScKF010uXd0k3kZGDU/rK6ZLxC+ld6wwScsLD5joPUpZdLt4sDF
jjRq4jbHhHHrvExAqQccU2n2tnK7ybtuRpuXnfSQuF78aC7scGC0EelPxDyiMaUlLaHoRoIu
GNwbnrpNHpR1AEcR1wPdPI0V9l/9XBTGHnNN3jwWDD5enbVvVm/U1H/qMQNDgxGhyDgHSnuV
6Qs/ppjY4HfPlwZEcGe585FLoZkTqRc9ENW6GU1q0vDcbbyX6UU+vQMWef0AyteWDlJ041iA
BSHw4vfcdVeH4wkqqvNHX0jH+mZl4VMR2lpX86bplTvONZ6kyDT5VcXPMW7+vEJrV59vGsKb
PClll0wDIeHAm3d1yNLlgXws/zULUOOoIhnalgPp3LKSj8Odl3t9g4Q6ezB1pusBoQLrhm5J
5/pkCD/btSwGEBG0KZnhGgWiSw//FX57bPm7d8Qn4bcI9JgRGGJkxqw31p2Jkidqstt0y4h7
VSy/gsLOLl9wMIm8NWvlh+XvWuOcpYTDhVfw30Kv/Qt3eWjmQxTkVoMCldk3UsgtSz6IOvub
34laJMvmAJXpFGiFjiby758JWSng+9bhxOyhnOkDPfLxc4hVIv8kFmlVSB9pBztdqWNvh9T5
Lqi8u5qOU+kp3a16mqoq+7Ei95DBbwSsrb0At7pYl31Q4y4aNOqePV0H1WuUXyX6A9zsEjyh
qGsGsH5f9p6L5kNk6lVnNIbT68VGsDp1gK74A61n01q/Oak5dnwlQnLYT93Q2QRXpEZqaMuH
g6JnGbxtTGPxrqz0jussVbEfjkolefN6oPsX7DWIcRhM6fxVT9qMTXdNQdc9iyxMMj5MD5bR
OHR3kp8JC2Api285dgkIpgLcCjaKu6eh9dGUXpnhtvw6qNih6qhc+5FJ/ekTMTKyu1Fl2sGy
7PslVve8gutAmfWyG2esJ0mHRnKGE4q7SRTPCR8ROG8MOXmrq17ZeitVjTo9t+8ua+zFKt+n
gLv+H9YXHk/mlx7Lq1+wdX7VseCaqAqq8pDIjseMO2YPCEldgS5I28FST/QJX7JR2u2ndKJI
v6g37UZNNhMKaRNKef8c3h1Ww1xtkD5H6rHO0XPg+SsrbGga+UpBf2C0awu7BKf2RuBeVsi/
r57x8bn/a2kgjvDiGwEjhkIZEMuNgWOmst0/1gGEKwIN5svie8h4kjOae1zg45yetzKt3M4K
+Mr598BymYOKb+qlszv8MMCv0yFLAZcN/Doxb3+d9H/qSYNlbSUrvMSLwzH2STLYOGglpnaj
zrAPJLi1KouXq/0z5s44ZOHyoQv/9AE9R+CSC+pw/0hw6CxZqy5U7q3Hj+We4SVXcmWO/7hL
YG346AmSQZRdEBMF875XMytMr06HUZkUEHzarcq0BTDtma2TZjKDkNLBta+FpmZeDzicGXgj
cFkLMd6s1gZODF4MdzCjqhxIn6lzsegjRYVJc2eq1My2QmXqa4FQ2i2UFpX5d/cFgMTo+fuh
w6R6JyWEc9x+jMplKJd4wJltiYX2jRLZWbqjVOu04LaL2zn42Xp9F+c2xEAjq/4eT0GlwffQ
S96lUbMqb7NJM4OfNS71SIhrAFDg/nbF/qlF43oWiAFKzlBbepW4BjwLbFAEBQra5R1IwTEz
bpp1CwjIhebCJAu5PP2LE2t+qZ/Cz5RldyTUlwHxPHnQk20vUtD4CbNbpi8W9pWe5JeI+a4r
G56uzElKrW0wmmjINyO009wvObQkpOIjN1ep2RnzVagcFtNMoOHmx6PtPJQHCcu88wBaRLIs
+CvT6cPXQKYTFHQigx8qQ9u+L3WAmib4yP3Dt98wBbz450AZDOVSJ/b8Az1ZeZ/vRa6ELMsj
XKG1cX4hboSKDPIuAA/NCz97uvzdO+KTF2TyffxK0Oo+Pbw4u/f478F/Owo7ABAdDzLJTPsR
BuirgD7juEs6L8OEnpwsz/PFzKdu3NHzT3+HJlngHJN39mz198riD6p05yQkRtmPCs9xEJfe
CGRsXrkHsiTsv3Na0zbcq5+GiXEye6NH74UT4eMDryqrS1XpVZhIWGZOHTLZqF76spO3VS54
w7mnddRH+xue5cfAx40OaercoxcZeqi3RxAgYVUGBn5MXcLCns1J+laGcp1b2vGvTgG6KOA8
IgA+WHbqwkZZWGoUsFddk32Aeyids132b2mpascYwZU5T3oQqS/qgm95OZukj+JnfqnEnb1R
k+faQiIM6Hgg6Ah+BrNngo8nosGOG6bWtoz++CrNhtGasEnZ0sEoj29PSR88RewfYUHr2mPr
zd0g7GIc1Fq1veUlCwS3vyC3cUcNBZ9x0JN8y+vqPdN7TxqkGAGqtxzk61V92WG3YI0daden
abalTPVGSLJCufeLOqrhcVXkmvCdayKQgQ2jPdUTr/1kYtD1RjZJsXoMOaAaorq/Q/lWUoGh
8Vb9gu/X3xSw3aTR+fO86qviW0kPXEVgkK72xSJzF6cjO8T8ZNez3FLryvUDHSMcKPD4qRgQ
oulFvfv3XkS/rtFe3ynqHH++2Y1RNl4aa26DsB6ZplktiskAuQxy+9LuMrdQDE4Cf6tbu7Fr
NR1kjqTi580eT6YNPsRdojjU1qtqTLqQyNYvS9sb9crksoY60gsDBnft3DMxausopdSCRIdZ
Wsq4jGh7GeWn9ZqA9TSYxluqzCAFZtZPgP+qqmNXVrz+hSt2RuM2/Vr/K8452m/oXeauztI8
FBBw7szfPwv+9dBm3Tz186kDzb3gvRpLWTQfen2LlCAuTmKIqquPFwpETro9m4LfegtAGLIs
igiyuMoG9FDSEPjB7xTnowHE3Q9fvuu1IjT3P+Ar24nC7WvCG2YDvjJ7NHlClGW6jgVg0FYA
mU4m/zLTKZ0qB9TpfUH09XYjbT/2ouJa01zzERKsKOqB/itzt4XLB5cFXkH8f6sAq7Mzh1pf
F3aUQ+SQFpX5njy0pZ6qKS9DOLe0NV4yGnHqQZynMzHWl0CDYw3NqKqq4IPvE3WFmmasZrPH
IWHx9BCnbvJ9b/XOTfodC/Ko9g4t16gTZ6jKeT2DvbDUKgQv8na9enuWAkXcoM4Aef9KHvKo
YJfVI4RO/UDBhEpR8naHfsNzATN+BL/TCUP1UXFjJCesiITDkDNmU0BE+vONx9bkF2tGj7dq
3YAvqvo4Swr76BIuOQXQPNz03fTJwImZV8YvTJPr+Un2LnbTYuXOaXaVXfxUswVCsE/DNL1z
fD0E6aVQJyE2waDgaZL4tKKrMP9scSWLl9kyefxOnARQwNbS3UxHvQcFACiLjj9vuafe1trG
xydBnf1bihfnnVhimopmYG1Ep25flbXJFlLB4XXk/hO3cgm1pxrLs0Y184uifxht3pcKbWKe
rM9xtu7NeFEdf/0uXhzYhFQW98wIv3s9LcFpY/aKByPJHh9nl/3urA7Jr+ZGEMlAvvk7a+Ov
Ts6dxfsmfD7Kp/wYbXDFeb6thnB5Ox9n5iPX3EehR0m4chOaKAAQ6PUPQtAIthRG8h+BexaQ
k1n15BjLtxADSy7j991WKu1fPwaN2cpjze5pzEqf7UDkwzjsPdJd6T7+nMFewEc96p3BUcv5
WTjQ+58Fphgz4nRLJXp1kD7DjXzfSuF93mrpFX47Rtm5rvMcBzDvWOyjD6J/RBnrwLqJIkdm
C7JadM61wzS9JadcL1HDGXU3bOZy5ybM+vKtt3II5MSq9vaQc+Q/Cf3QRWEAPMbVjnNOcU4o
wL2bpGhhk54y4WAPxLK3BFbr7ThfzHccGOBYFpr0pOVxJBCGuqn1bfHXv3slIG0NNXjePPOk
fqdJgaY7UOzatt8ygpHijLdWNTTuTbPNYImD/O/eZe/Z/mxBIijijcAF+qJhDvrA6hlFzlb+
MyI78RzffM2w9dQBXiiaqZHPzdm04oZkH/i9xLFFgJzONtLUI/BPrFuwsZ1vBJyKMAMXUFfp
csQWTT7FWbb2KW9DhR76kRsvrRkce3nFpb5jdOMF501eNVBrWnVk2oiH1azqFhOSxtygFwfm
HzvjEZ1m81OKVnnajfYdvuFAOMGiX/z41nmBnrrKyiYPpQvw7cWeHp6uVPhsYpOe77ixqW8W
kCmj9uJFHZAsczz0ScDIjlfkLZ6Pfbp2Dg5O0M69zMqObUxvu5GrkpVOVmWcZqS5Lt6CD2zR
bwoVxeNOJTt475zLbtuJuTR+47R9UFyo1riMngeviFDM3UIu9wyesMyJvqMz2VK6xaKbDTpp
wJMur3n4Qr/14knefWS71x9+RwM72w4xkF4uzAV4MsXLmJZDMwSNLSTWkms2b7zZo3SSeUBC
rvoBSVSpsyElPLz0ITMHttvQujy8ligOWCvycvWq7Y3KY0JX3L1C7v3QLdrFt/c/k+/NJEZa
mTAiix0TpjyzMHpQFk3Vc4wzhI/IZNILfTGHFT+aYQC5Gia6h8JA/KE1tqDt8fsAWjGfvgK3
VhB3JwwSw/gtnTKr410k+1aLv7/yDN9oS328o4lj9FCrCHBZH5jkozM+1ghEgkp+gWSVYYbF
RyY9fBWDEnKowArluFLUlfhqfRlbIzwWAqdyEeHx4Y0zEVx+p4V6WTrzpYrJV3DwAcBJoCwA
OImcTtzuWDoFn4b2r2H92p4MTRbdS2Ve6jaZcmrJ5whik/5Zvr24Vga1p9/5uvIstND/jYCW
Lblf+NCMCoZSAgANGHVi8BlXzJ6ulPULW4I4rOTupnJ9za02mE3b5IZeZZoAKPLCH7gBCLXd
NbMaJExmX7nYW7vr49ypD92+PYpGPpde66NSD+x9jvqCrJ+tBI4Zfbp9FmYcVQAFEAwXxoPi
qW+n09mVUq6cTl+7yLSA5IK7hq5ZkzPCDJjiv2Zj5R+YwW5KK6ZCg/BaXBMcMdWElDrmPqbf
L3RtBlLUM0AIgDFnkF0AyJSwFN99z5Kmaatklpgs+rNmORga/4cJ3yMfwC2v+bNah+uCDUW/
EfAUygpZKeYXtgCsJNs+ACvJTw8FYCXlWnE8geJMxz8eM1r7LChd1pKELi35bPfrCy/y39ZN
JPjx7tpZzVJZ6GdIlkDgpAX/BmNnofPM/PxlFKsGxYR9juy/wojJXbgMS9+djts/ty/8epTs
z6lkJiXVMg3VrQL9CisSeyB74UDGHSqO0turPoqVN6tZE9a0HoiKPVrXW97AW3QuMmZr5AKK
3p7gLSPM2vFRXDu9NX/KqQ298GzXsb+exGrRhQLrqaDb4xHgLEaCoezAHSD/UHpB0s7fe1zV
3pdnzr7sNuZExpKF0v53jw5wFLsQH2hddduZjBFeJJUCzrxjHyc3OI9iQWcyi0/y9KWzsTHu
K1Bm/ndX/K/gEsTlqXFs0tjpjHkWpL1DoGXvh9tyHqkJWsBjeVF+lAFNlBm9KPD+x1Hibzuu
DFP92nWZBYA4QAxva5OsPXRkknUjEkss3/VHaf/LWYhmh1UpnehKTXQbc57gHzu96ZTUvqqB
ExZE8PzgPLlcdpvMVtm7G2ffy7b9PBWACrnVTzHF02eDkWfwfA0498/zFWElfOmoKqsKeha8
7VLFGwFL+xm+/56ODyPyP6EkF7zwoNShUZQ1gDJNi/Sbu7P/Yxie1TCRZ7DfGZaZ0Fkpr3Kw
PHFXy0fumP/Jhf7L+gpXWEjbWGZew8Kok6+buGXc1Rf+XL5FQVwYZIFnTYaJKi0EpRHi/LgJ
vGOfCv6ftt+m+o36na04E4uK9GQVTXlzU2TXaR765haJI0dB2YOEG5rIuQlWEoLWYt+ZPn1c
MXjXpK5hTbXIeGe5WUmRNjCT4Bmp04IJ3X9JuVo4sLqfI2p80IL1RmBdZ5kPDl2UAxQ+2LLm
pKWMjJiH7AE8IzFGho7OrQrndv/y0e9teZS+gFBnMcRhGaWDvWYs/Zhmj7f5M31NK4H328fj
nzP0cqkgt02SOGuOT2n21GfI+19wpf/GLpJzLoEO2pkykWaAL7yaoInaS5PDvRT5x7GlmxWc
F0EuuDQOBHT2eEOwC9oauJjV8kDJhU9cmiuRQqz+k7ju9T7+e7My2XIXJRdm/izYITUxUREe
zXtctJ5PMqzNnlrVPg3T5Tzsk1pEvhFw5ytXrIsZ0cb0B8i3QbVRuAwGDfwKQeHcr/v+L4kF
Q4KdWFDnWNciPdVBAtHdMbuLg82AdF5fE9WoSA4LsRzdjW9krQPUtvyh6cty95fG6X92pBEz
9WQgSV17KczBHrOpkXkKoHcFBXC7ecvneYuUnD6INi4nwVKfVZ0rn2KovVXOzi13+JYJkeAj
0pB6mVRLTyIEExEL46ivzwbcT0sKr4CArKZCJSKrPCNemCitMjw5TapcH5wTdRplqLofmHzr
Vsq+cvJ9dZgaBiMu6Fp8PMoBH5PvSfw9/uYx/TNtOkEzE7UKLdnnsDE/1920SIbDJ6fBVQv8
bNQ4UB/pCEzo9QyuqJ8j2TOLpio5b0UnqaROrT4Y8pcgQqjZnGz8gXYjjBv6N3JNOlx2dM0a
vQ0AtEeXJio7qN9k6sJv6JzNm1eK/aUtkeCyBOPuIUz4DIAu6MIts98TegHp1Ys3tOlU3gWk
Ub3/A1B5KW8EyjtP+AXT9WPobCUuPtcMmHE/L3X4po+Abn8WmxD8U7EPCxJLj5fgn8E7AzNu
z7JQUkdj/ZWVaLMaDGzh2lUjoZDIZNR2Er/AHBvzS91Nl4/s67csK9W14iE+t9/7Le676QsD
J0kgI5LpjQQA9C/i9TdZKEKeM/VZR542hCxf6/+CkJGfr7lxKLZEVR4ZIKKkyELnFgHFeo9r
nq7b/7i0r0Wij+iiE2w7s0hJu9jI6X6sUwObhShbmdSEswb88kphr5ICj2vwDvXh5e6pYRE+
8UCFH/vQ/U//uiGhQJ9HhPY7vEQ7YiMLuZV7d8ctzlOmt0k6/kBiHs4NbU/iECAA1Nseof+d
AJJ8H1B6JbABk/pG4Pwf5Fd/9LxUmFuPk5GO4GdRVdn3pd7fB3B2Gjn5dIX9NIvIWtC5M1xF
5CtWHfs0pOR/dxP/v3MJV+hcg06bYEVlLi4EFfe+evlGQAz1yEVq+cZE7xR51Ti2zqFSJZmw
Hzev3TjiJ80Z7bmNLKsDwrWnj3/qyV7p1PjaYahboDu9UPYTDiiGqm75mWJ1y04eTvTHGm7I
1fFb21GZQ0pnytuJmWrSv86VdzUZc7qr+GoDgYQbSJY2EW2KcP2VBRRLjfVE71VApjVsquP/
PG9puxsfuQaINRmP52iCj+w4/H4gdsflFuuHXSasBlC8E/OykyrwojMo//02N7Z7RdZew6PQ
k+WT2EDQQZ394MM7GMuj98+JH+YAh3tdbvQDKNtIfi5R+8SG6/Q6F9dhUtERn27jjFPSJmDt
vsSik4bkfb2Tej6+mKTrf4j/i2mu/kaAES5dOtrrgiwDQrziJy6DAg+hoPpPS2f9m7M4jiF+
x5ZuQhDnZzycLZ7E32umn5DlI6V9i9Ugqgu7/bEfdKnvN3gEyyP10Y6S8zM0/EBpV4+P6hA/
qgHXT5lymFr9UV22gJ0VrJttgZ3jQNr+SKt60J2sm8foZ86oWw+lhm2lDBecKrBapKt47Vss
OqYwtnIY/rMWzAbreiO9OptzR4ixcCTU4bfx9SNYX7XFaYFwmagSvmXijVdJQP0CsHEpHyyJ
bRDeOt7BSkjMPt+UksfPblJxm2Nzofvf2gaon/KD9WvI63LYzN72O4q8JDMo5ykx5C/RVqkG
dtvrSen0+GLps67OZ8vbRw9aYvoEfcuO2wYmxtw40EkIxHnA/cr5VGP9wdUaKwfks5ZwRSJm
5DYDi499I0CaErny9LMebz8QEpw9XWRWEegfY20TeXuYasIKelmJIWxeN9gGDSqmNuL8WANq
3MAKS++XuheWz+DMfIdLjPkYl3jn6nbs1jI4u3eP7LHljt8usRojh/suMpZnKA52lOTPVKfW
er0CdM3stocw+dg48M2dq5dlW5XYa/1GwMS9z+fiHLO/0IDBP7P15a7pP8Y144YcnDqZ9KYF
RK5XF+uqL7ZBaDpkme8d8Y/xQpsznFHvTQp9k+jDJTImVe34SGppF8YL74YpORD9QEyM0hfr
eP36G4EAtfPTqOdAdvLfXnlB0CmgtLSfY9onbTI2phuIjVs1gzqrp/82WgeOF6l5IxDREjD7
RiDugv6AsBCQQ/dS43h/GSmTc7rnu4pOwljnfuJjUgqudkPDe9nkKvPsDWs9/JXCxafjFBE7
Y5Ez1Vgx7lFhfe9k0pTU78yd5cQeyehcLzozyRdbL3zhk0FZOURvi79oylL2UcFuB4BCDv0f
Y6V83HPtVgYR03+0vUsCiX6uxpMbqgm1x9YL9bv3zmX5BxRNac9NlSluRR+K2LP1vVEHcKvz
GEDB4eRoBX32wklumZHUFdSjA1N3j9BAWdStQfkCn6w7H1/v26FFk/O9Xo7soFW80xxU1m4Y
8QPU2Lwd+oQcCAertvODJKvC+65BMuYPEKcW2VM7YWal9FEPRUi/0OGZa6Spjv4RvDbqAX72
DLZ3BKgKrRXygfEt9UlMYcMD8Jm+WFiLocTkj/cvhv3tKu82u6QN/LSBA5Fz8ki/1rJcYBLm
YWvXFg3Xq58fhAReYmNFkqXh4qpMSPaEPKg/dJXgY7e9d7hx++9Jp+kmhd2nTnWfx9ZuKH4v
hFxi3qWX9/I2tLFmNOZEYAdHgNe5sKn3I8A629EzgKYqjqqjkzz7AOvs2HuOf3H4wpV3i49P
fn9AHTXPlwf76fU4OiIBrSb+yzMXjNmEl+0lYN0tbojzIhIjEcfPhyxdaZWAVqo+InAe0M/f
omGtQhYP0JXwha94ixwD7a3cwpOhjUtdv+WjjMY0keGKzet/u552ZPHPmP28K+zhNXUoZ7Bn
oGXGzqIZQS7XMrcG31u3VHwXSM4tGEQeaNIp8nDQUMBnsjXK/cbclYCpe2LGq2Ag4AkB5tbk
m5wKm68LRB8Rv75yeFaYbaFb8MTvSjor+dKu9awKjer0tDEmxfBGrrg827pscor7MJ6AKNub
VnoXq6AKCrS1IzoxVVs2T//tcCzfXRlqV2qyuudhP0N229ZZ7jDGSMM0CMFngou2dxzvHSSA
3M6OSUUE2dAieGXECCH06ktGpq5Uh9gG0bY8rIipizRxq34RWDXH77um9+KKKdF2yu/v4O6u
ZA0VXc6xYs7SlO2mBe/qKuVYkfph10yt0ovMTLI75rOo0/Kgpqcq91aO02ct55ESfrxR5mIA
jItegb3xcc/jpHORoDOJbwRk3ajFxYkwFsuEc/+uqKVKueUr3AZV5Nzsqdo/x+cWxnaqco57
PF1iFVwlbe6hC2ngz5W347MezUQCGwau2jJAxZ5hdz6wuVUs017Dor9y2u4HslT7WXdiie8b
Pgr+Mums0GS1vysgRvfJNXoTYm6hwzmGI7guac9ksHHDHfpbG6ow2JxVTpfMAuuIVyzLusGk
/h57wO5GzBuBYeEezLTPxMm5U2dsTBIP2RAZSIWz2VycKHivfMcywzviP6tGb7zIOI+d1v5d
dG+/AXuyp/scj2Zcjed0Y2xuU6uFWwfB1ljNDI2tJr1s4pna7PlH+t0art0aEnVdwhMso+tM
hnX6H+eZTH93pn7/d77vBflhOrfL26p3SFStgR8UXBqDxnMHTSncc6rT6cVCTh133dNl9jH7
GoEwrHH8eAd34uKRlSPwWYtG8eCpJJmwp4jz/H/pVv2HzWP2E6xGgmsw0bQ1IRg2cNSDI3jw
XjoEZX5EE8wPcWVVNQv6hCydXFCIZ638JOxoQnkXfSJqwxkCi12kxneUT7zCAeV2j7+oA6Yx
Mxdw2uRV4cG3t95c4vuWj3gr0mBQw8BQhNY/yG6/jtUj5tDOlaGB6F0/sFIbwHeGViW+tZlg
v5ZOUe0Bvbg/ZEnYVY3TAbCYAcgNMyRS3Dp94Fm57G0xy0Y4RkLdMhqX0RJA4cMuy94Wt1pi
+Ou4Ygm/8nhoMCFjpK/2BdTgBffV66FCUr6Wnris4w71v32ZFt43+0t25Uvc5lRG+inMdLUU
/5g+zbBt9MXA6D2RX2kJg0qiWQkKnbOimcrskZALxzTCegY1M4qFWyuvM/vVgg5YVxRXiXEE
z74fgLUWo+djPCsciu/soS5Y54aFe+5uy8o9AVJgmvy8h/X7vXOVA7L/0EjR9i9GxfuNjZnA
hlYt7bquHJAPrS9Un41G9fVDE+pX4bJbSrai4xyA8JMcTwwME2sjCnj37lsIBd3ddkHi4vJ5
v/dpViTdGmR3NtCzmYYaQ/OvZviOP47eMSAmSBVPYMGAX2cseP1c64W3WtadZbZvmDgE0fDq
WbnIsk5ZgqCJuuYV9EyX3J+IUzlagHbhvizjBtWGYNYPtTCJUVZ7RR01Y/EgfIR7P7Ih4nbd
tGEZnDkYdTlpCICn0nKX/2OZ6R0hpOCTkuhVj7i8Rd8pKvJy73SgA2AWji1Kl+OQrTfzAv/B
U4o2Q/+mBntx5/Lv0n97lo4t1Ey768ytep4+muqpFghu8KeiHAEwmPSHLaQB6L1X07rECQkZ
WmsPo4l/9sIFjfg/cxYST1DygSrdB8+oBd0+uXrp3fSDdq7IMKEeEXoSwtCWWIWZ6mAQj2zG
1eqWFNXi1uzDOPzmqB5Uss1h6gpz5Qh81vrCeWw6agJBwDVeLCJXC6MbtEJ+VIhJTIbe5m8y
Y7pESWJjNnegjtnsWj77T5Dzr2wgidIyQFTCWBKIOPXkJTcklm+yf9IT96z0jcDMajcSp+yp
YskyxzdMFFrRraasMj0AVKmkyDyTqe5OTO1a3HCBfmRCbg20yeUgg/hqZp57P+HPZSHPRSNV
dM/UsLaNzwFeqx3m/AY5wMrqHo4P6xtcHTTE5uk7mDkQaYN9kMkL8ReW2d4RKyv9DZ3FPpys
xY3JR87//qfKib89EGrjEQYldjs3dtzSRLfcJNtJI7WTGauHvrvxu/5k1MUp/fpBvKryDgv5
2MvizDpKPMRt8o2Ay/bDIpkHjfvHLPGyuSm7+0M830uwVnN0U+IOq27D68n81LY21/A5bWog
kSz0zLM9rSHqFX6Dd0SKrbuvTXgUAD1a+KwA0v9d9UrhP2tJLiDAaSZZqC4AfFr2X1Y8+r68
mbDNcRDmMLgo4auonsHvO9sARF3Fe55AU6VS3COGULziO1j9lrYI9C4l/+WL/HAmV1dGBu7b
wbN5/gw7xfsJvOtH8O0NydBYRVEq08VaFBuzvgl1zLp7mePbJQQvHaW9nNXcy7UppeODsZnt
iwe2mnCOby/fMgaFqi4WyO8eOjR2sEw+uK1o4zpM90v528uybu9rMgGMqtjJX98aVTH25NaB
86nTl69If5//JOhsr72DW1OhlLY1nyDnMC2odH+Z7x3xiYNDEbU/Ky9ZJ8fQzIBcV66oMz12
6tbJY18BE3uj2KhSVgO21iYxXBrAu9UdSu8ll29v9UNHCG/zXDQMhJwxuljUbsrl23Q3TsgH
lwWbhBrwsqc2ylRW4zRVqqVxqUTPRNPFWYjj4v22JdNXcJWuuc9R8hAaaVtHXuwM+8NOn5R+
jsB1VNAOa1FOczlUlPbC94ahrCjJzbnS/jo3JGPlYHzW+kK/h7ZPadWER2JYfDnRrF3C1W+h
rmxo+tkPUiEXF3AxNuKdLHrlfWPnMUUoZDB0KTgRyNPfoOt8EApRXYTI2w0puhzUkgtu89nI
wfYcA5SiSH4GoBRpyiHZrQuXiPn5huCbEjmf3d83+IHdHLjV42oNbpsSYDA5bm3lvR7YgnLf
TU8BSWCipH5qArxxRczzrFmO79D8I4MPO/LKdlkijDHPQy/amGSnBLUI0P6iIC0HpkHopkDp
c5OIZMWLbB4E0sicWxiNB2zxO59YHCuXbQzojcCZylhMS73qpKFATUW0TKEV9mobpsvjctLf
Mqa7h3J95tPvuD6IopO9gm07FqXBWuAj25Oey4pEYzrcCcP3knd1t8xxNb3hxOaNh3uqZetF
f2AGrYvmZzY/ymEDuyvDmFqRByHvb+btdjJBonSo18cDFAlEstr90UPqF+J1n7vhIuXiGN0I
r9+iXyX2bz27X6ht3BgNxfTQnxx4xVxIu5VpyZrF55CHVmtowe0DCb+LSsDCWT2V5ILF5NQY
/cFQ+afv71FAUDTJdYIr5dzDftA+65rrSUbnvCoFV6/6iSNUO+sg36FQLk6vxDPbFtePpk4f
/+T5LJ3k2zqullhIsG/AvhwSZ1HoQ/kz7bJlcP9ClPth4oNBTQzSA6aKZ1iYxzkTaTZE8N11
H5Ro4b2zZ3CVL4liIwtlM3B0Q4sXRzBCV+TQHLlPnZVZgB/hwMkASNuPHzjeDcxK54YTeSBr
bGZqwCbyVpvD6dfZM4tbHWcMgjNDLpL+ds+0WGnzqHGklUxPc0zvdD9QbFhZhh5TlYXtOx5F
sJNRA0W3l/VziAkyeyxKZVjXAJOhseJPZdkQ/5gMD1rYkS2kgJrOMr27GLeqeKC8sIbr0mN2
7iPPbh1HIY9EhdrmzQ6MltzdUhdsaneuaO7CZ5W7l3iWj+ozHWiDdFPeExwfvAKLerkHQMh5
5elhRQnPxqLp+uG5jWz1HmAuK2pZklF6R5xkmkaV+f71wmYhSyyrdgf22Plr0tcXaKOy/2D4
Eniuo6qc7npEwlG62lHZHpQ+ir/R8CfSeGC0GbFe2GiJ71s+bvyVEQsLu4XYQ5n1cWzk+1Vi
X240Gna23980/wqN//Pcn44ceAOw7YRbFnK1WFkOfcrqplskgLVj/ur1XiDuq4/KuV8NuqbG
macBwNII/b5dpz95va6M3vjaKSlC52Zf1RNOSQh7M+C8/bOdzwJL+G3Xn0agqD6r6lnZMane
3j2daidJ9V27YWl5XeRr5afQjd3b8bVJWFOvE88WZXZkHaATUPLaSFm1g36Lx1qX4hEFcRgJ
RAOToV2inB2eTZWyStIuXFQ+lbkNfPjvmrPAvo30Y/9DXoyMDlNuTDo6Z4fx6+dDmFvJMiY8
o/ECCIemiN6r8mL5eYjp0uTJYee6B/XdUqtpjouSj4C9rDvlh7ImPQ9UnluIb7bjTsYDhXaX
RFhm/BYJ5Z1ZVfMFNcLzQCB+ULkcnUOSwdULK88op5OryxaROz213wgEXd5/f1m2SsVcjk16
P9G6gI7P8sndTyO2yx3gPj3XEHYEBHGe9PqVuVCBwtgRuZ1PMvmHN4csM74jVnrhCAwxZSgk
2iwtPhxzt+xgwFeq7R4+XnrU2KboWYciH3mubKCLDrPZgrpwCL3D/uBMYLdefDTVhl5KQyKD
caMedObTgwo/aBlq0Y50yFdmYbdYdph7LiKL92XNoScvtDx6L44g7qGq0cOm1woUI6h0xbls
d6CsxL+NsV0NMyTN1PpA2muBPHbOx7kIHw/SqgOBg615ru7mXP0GE/PeFIfOu5Q0YHvyR62z
9KmO311GgVXiLJnKBPbbu7KnL8c9XWaOiC4tZBOeWfDK/KSCsKqALpQyAkXWTh19lMFauHMq
X59Dlsc1CFuELHN8u8RGJcZQ/PaOeOdt8shAnNXrsUUeDsiXPLwN8qBLyLKVe56qA56IOvML
icXkaJ/fipZcp7MsrPAGn1sNN4yM85UX2bMIFiUHycvp7+Af3KJ00gqyZs18VBKgcr2ypaFz
qtLQOptPLTO+I1ZO4a+dcSOk61NGlZuTKPFKmX8yT3DbfQAPFC/NSifOYwvXIxNGvYeDlUsd
2idldtQ1lGf6BxO3PkmMAQ/IumxDpp1SPxo05f6caty1j5jZOT/8eorB/dNFdEkc2qsrGqkB
PtvbA7zJ0Sr+udO/yuvexWdQb9HnQlrUlnr9iyOA0tO3cEkrnTmAnuSGXlj6XazsLbid5/6I
i5S9qhXm1uTjakRG4wrs0ZHfDYyIxTGiDb0JuosLcTDqIWTnuB46eSNlmVvIyqfmaWKC0hof
EH0iKNeThObUHs7i75UA6hgVm170hBYz/VgMV0vzIpZfbR6RLPzB67x8jm+P2CgyqplhJLGv
7JQaULJCn+UKlkEdNHiFrbpye/hW+Bb3M9ePdj6Zw5ttQ/Lsf8zkTvw8vCwj4HnNtbYutWgr
nJthcZWq2kK0dMVz/AN8u0p1iaZdca68aNE9QGrokWWOd8RKFfhrAzWsBTyvvs6DiS6WkwZV
5VdDpQmcFIezTQq8Y/MMwcBBbA1NIfBHsbZm88byRCjtlEyi8tzC5ePeDxqHTIa8HOxJqDYj
YVy8bnnHhmZ0tNBsyF+ybKq5myafOXPST7giWGuYUHJ0qOchF4clIM3q60pBnd49FzvjOU7/
PjX+C+25nlGPqL5u3CZApX1YhrBgzbbEKUwLQr3tG2Zh+xLSwCh+SlfCVQyyQlGa3CeY/GG8
o6Lx/iiQ+ET7WeZCdG9tAX10kvBGYNuGsEaKlgrnp1IMnZiBt3lo18VCVAGc996L9+EE3yC1
CqzVbHV9AO3UxobTS3yCEnwf8B+5z5wt2DJFe+KpHSzDeQlkxBwG9Ksfdi2Lh0EUzT3RKRob
QwE/ggqP0UWpjS3cbq8Zk1Qg1eHxENWtoxZlqP0uoHztMtM7YuV0diXzwkkjI7XlpVkKFbf+
oA3y2/Xx0AHhM3979Q7BtboXC+wOJN7QFtPl6RfMjKqO+xFjYUOhxKboxLtWTzyDU+gYkTFF
Gf3b6W1Z7t5lDszGXSPe8GfpSoku3PDo6asFPhsmxw36bdv5h8X93wulw6uMl/S9nMnYCnGs
qiwPdGibaFTlAG45ReVRIllfxD5BPss1qKXUimdwKiZeDHyQVLuOv3JAPm99UUCGPtZyA0jR
ytde3+1+V7Pj4sGNNdw/fRf2Uemx9TT9ImKBwwClEKg8t+rYsaUrCErzXPJ782x8jaBuTXNJ
hGA+Yc1+tJoMRs9iMM/cT08cihbmN1zHwEEOToDmUqLKXeL8lo/6bpY6d1Pj6jFhdLJfgLEf
vrm7nzQU2jSMsycE5SCQsRRlCb9xH1MyXix9ZJI+EC6MXhZ31VGt9gE9qe97+BJoqp+1HzLY
XrqFO2Emvf2RgvhtnoMckHd2ihW0ODlp+5sl/+COwWXOd8RKNeRr16cRXMU75+PYFNDaWYIC
Uh1VCpkK4vgi+noqq++yexkeeioR+zQ3CZLgHXwVjlvTVGVmjABNgneByvb12JTWDTLJEdpt
+fkquWbQIuvAaxsp7IzsfqHX7yVaL46xeOHaJewh4W4GvaZWn549aGhDi6kkwNBdVyS1fnLy
yPC6dTlObY4Tjy/SycA6l2+xYPE1mVe8Q1aOyWetL9tREVtsfpzMzWOe5uXywmQVkzLQGdKo
CIknVni3g8AadLxCicY+t92Dc//m/eUr6A9Z1MoFwNr8QOmoHsrUSFvYwuXKxp9mzF7ZTJJY
MzuH5IiPnz7H1Av9I2SZ59sl1jaOBmO3zTtVSitVDb2keT3WRqIgMgnoqO8ahxfTq2UV7qjY
JnfhOtqS9YntNW9na9mysGurR8Ow29jQ9WpECexuU6oKwGtEjQB4h0bErzJsDNWyeYTAAhuq
EpKXVwUkiS9Ni/dnWJmlB6SIEvS6kjuyzRB5k5IaGAhJ8lAJFr95Y8xwz6hezbx1Bm9o+44/
l6/+f0GshlWk01KATCeuUZ5Co9cvqWPe97TQuxQx569HSr0a466HY0UVNqmNGkPQapBsAFlU
4QK0c1NhLWJyTYQFOYwcmerU0ghqsib64npRf/64FGNnAXJT2VcNxK9A9yc3aotb4yepoYF3
F+9H5EWWzHQNFsBKlYdILaVzu+mzviJABGP+vxPhi5b0C27nn2wy90z846LvG4EQlivgs38V
Hu82//TXpM0qT4I294pKoJvwZoTyCuLmJtSFPd7LV92+s9kNcq/BpPDGXRZPsLyQGz4/qXro
jcD29dCUU1bQZzK7LvhNt3aa2jBn5+8Aadi7Q5ZZv11i1YGywYtWaaTv8uVwr0dx7h1ZuqVp
asOYHtONMSMnIrdzATs8X7rcBJvdObfo0AWI/bEdnldaREattwxPps/rq8p20fnzKm4PNXTO
94detALcI/Y4L27fLWD7SvGTofqkpK7OIk9J1Bxsp0auUlstv3AksNETJQEHB1QLf3g6/zdD
TCNhN3gRSid7ZZLgmQkFfjKKidLlJQW25M4/JBRyzFON3DQL7fSshyBtCQg1UpGqJw/QS5Fa
O1rTcqLV+n2nG091pugy0o0Bb2bOe0k2rCZX5xpF1ZC2ee3PrpTQYHYY8ZkLmQVi/MNi7Y0H
TkVyfeiEsMqh523GV+ltU5w7zoCOt3gs/t+J8WV7h8LbZn0qbyQbzDp3EhZibF6zAMOyXjZ5
g9Kf0yBFl4oDI8lKIFDmQzrgOzkK54GrrhgtPwDBa9JWj1IPxEgDkYAIfipNjdA1h+zaRP7u
1rBPRlXnw6pchaqh6ibvG9FdtNtFMZDJYzF/yyLz7wT/yt8LbtH1xFVZYIXzCRxmCy0vOPac
Muf+K9E7d3qj9UrcTNHV0BwqmB4EhLzUdi/fi94aq+xJ8+xnTxB8pP/CLPqS+UaUo8qrh7li
ELknGllgmHkBlENXAe9SKVzmeUesVNC/tr0JYDvHmCFTM7eVRqJ0bDL7fvSXLtcdST83pczO
DEHqmvrsbO2YZHGRMV03NkiCdIm5SaqS/fyFgWN1oLAFPQ3/gCppdOVQXXMh92h2e6SGIrSd
i24XWpqrG00ZUbfMwXLcXyagalS/Qd2Su1gDo9ywLpBR9wvUtXlTWp5H2FnmdLOymrYyaMBn
EDLpvs5u5Xh83vqixdxWwSwHfahGlF3aPruxXm6I87wKfG+j/fAlK6AAizNeFYi98szAsOLQ
L9eZLl9CeI+POSmyA+NGiJHNuOQ4t3txIAoytHq71g6omFeUN1J1pycKkgAbFVoJg7nM/20R
a6+PXk6SOBL2nKlaNZSfwpBYRDfA8EAIUoNoYqBDXTSQPxrZwxw4rKpC9CW/JHC6a9yXBTwJ
sdrYgrtudYiyyBlzbLs6ToehOtDbNnaNFKRVx9bIbvAAlB0dqQ5sp9cUgu+vcmGZ8x2xcpJ7
NK2vOsLTDTDHn6x7Mbygh0IjciU7Tdj9O/b9/aGmFRbqLbSyONuLbWkIkyTSfqWAJ8BSZ17e
G8/RfgkKjHUwyZgur5KKUHhiHB9q14dP77PE4n/eI56C+lHNs/NJASGA5YZkpwXXHj78Nubi
vWCrRRaK4Le7Pc+XTO7PLmRYFMdGijHrLpn44eczv7s87PZHZ8EDj1Dr7FmdJ+Xim7F5Bacu
mcwtHN/7dOW4fNb6Mo/L2w01fQywoWY2u9WRik6a6JsKFS+T7IrwAan0zU3T7I7hxuANQOLD
RztqW7VSG9WnDryoaFRVa4iCJrJhG7dj/qTL76P5V4YDQQTiJ0vbR53rMGSh/JDPbuvb+2Dt
b6O/ZUD94kUSH0LQwhov82/J8Oq4tQ6ss+sO9SPXHz76U4/09eiuQ5mhyLkzHkBE8Pyy1Kt2
BLYwVP3uRsX84Ycddo1zVsBzx32twVWrfimVqLwhCpn/5W2etXNPF+81VnZo1cIno7MC1Qyn
9XWjTmVDaK9+3z90XWpxTNqCJ25mcY1R02yvQOlNiWzV5e+7v8VNy6I+kKXRAWvAEZFIkmll
NL8ZpOdrx7QMOR12ylV+MKnWPjPeiuxqEgjf4e3HTpXYTO4s2kV+L5RgSJKTl5udZy7eIxfa
c6N8NhTRH2wmFpoEc3ucFj9/uW/GgDKCf8XnUG2xyS+71O3qFj3cNkji+i5ulv9kXD5rflHe
QLXiw4UgRhDG44SkNndQEXtr8I0AFX4ODz683ezPOcW9dCuzp6yh8j9G4gjBl0YBoIa4XcsX
sosz1tVSNzo9nx2lNjfhpPEY7Vlb4DUteLnz+4Je+pb5uDT/J5yd6M1vBNzcavrrwdVXYCHL
zN8uIaQwm1ouEZDTPnOSn5p/eC92gR0Mu7fObGBz3bkBk9DCk4G+MqGwv4LMi5fFXPvrqKHn
gcFsV4rsJHKDMJAvh2OIc47v42JbbqBM/bURu/HBUSlQ9jnzLO59wtNlvnfEJ2F+qPvQkZcj
o7Xltba2u/Vf751e9B5uHsGWbIz9203S6TnhYC3z0Ex4LBnuPsGCxbNTIuRxL9eKjXiF28B0
uEDGSb3pOQ4usHThbtQBpULynIlB0IWCe7WDlEyvnVWGp8JZRuZsmtLJRQ/zYCDQPEE0pmVL
z5RhoadcMiUpg9EqPl5n34kH0mOE3ousr2npapRotaFFC6iL02r52NMWiMsOC4xfnAm6n6l1
eMRv4qhx87SSfgPDkg6WoyXO3gq76jxvzhAODFk5aJ+1vijg5KAS6Igxtoa+LcfAb4L5JJJe
Wq/Od9ydmGKTuq1ktmIGK4FVcAxMxeP7pz1G+GriH36GGxQaGvbYT0VVjapKc7VP/FrO3gbH
TR/fIb3l8XhjXfP4s3CeIvtFLcEU7XrqQagYOztD/JONvs/u+Jv4YBc9R8P70vRlcx0I2tg1
GAhzT2KUe80/NZA41HbJQkGRe6gxi0VffWn4LoVO6bqxU41/zOrCsmQ/bTp/sOTlYJ9oHQT9
6xhPq2kxiTUA5XTf6TIH8OI9q55LaTfNI861BH5X1teWpbYoBnaROLnM/Y5Yqf58ZR1/Vee0
dE5H+71yjxPu58MTE+zrmgv2MkcmLZ+VmwaXCOnMBL4GvJbPUlWykA2xRbMHyxza4hM1kNy4
9AFhKTdpN87DzrbBvvh4TnbmxcE5LGQED0ySy7q6Sh55tlPKlacR7Qn7SyXLuyhjVRbFFylg
adXNG5cCccTsaAfOEoGYmMKsAzz52U603ACo0/TUd2rkGs9HF/1+4Wnck/nFN9pMjZ104ix1
CtjHbyA4j1uE2K8cr89bXxgn0DCNwezQSfe40kFCtSucL2UfidvPDYlERFCrdJoQ/liai9Qw
hnUNC74pbr58kQ2G9VUZhFrc9hGs3W/Os0F3JdKnVu0rU4JFWjWPNg+izVtaZ/R5fsK4eqHW
ZaZvmFgrwsjNhCaRRRersomuYAn96vQuoJouq5OwK8k6PFTShtRe5qLv+OJ1/sGTSJudagAI
6njIkryr1iwUMYyTGpJ7qyIIXPJrtRwnjHOFuiY6SqjNPQYSpXDVUvV0BPKUTBclfxFps9EZ
wG4yW+b+6yyfvCxkgvlxYQdk8xMcehMEY/726jlAzrvIT0mqt/OU+mlQR5w9o+SNgHQHnElq
zxFzaCyDPx+UDRqdbVw4FV9Z/tOAn24EfBaxhdSWQry5fYtIZMDG1yOvj2r1KP6oNm872J4f
295Zrm7NWpyAPfpLGMHNuu6zpxVZIPHhfCjZdiQwz5RUJIHoo4jz5VHH7P0M6hX5t16yNio/
3l3k5zErhdMfdYOfhzrxmN6he5dG9V8dv8xZvy09cb9O+gEpu5TdTxqedUindnKwQWLajXFy
B70uZbUBb/J/AIlW9JrYMOjgFcTytQQRnBsUkOvU3AveTjwaOlbvLIGndXelT12RCdQdOqVw
RGNyEBmId4GbA+WVNfLQ29bVLvN+w4Qkd/YocYfU1CSoH4KiFRLQdg9tTQB8a9Ef75KqCjAy
keYjKaC9Y6Jnl2U8tsbUMsYrOU8eEmG/L0nm7py203Z0XIlC5fHqG4c2GQFJiduUD7ZdX2iT
A+/S7l5me0d8MteT7xdnFFHaY+GulDaFU42M+SE9vCp78CsUjdpOaiJAy1OmwFUbCbL6fhKQ
FzP8Yn5qFBzX1XFTH2KgTQcgsERLH9BnTFT93CYGZ70NAoPYqopsDEYGdOzCzxqGA5urjnCz
3H07ldsUbB2hIK1HLlSwt4TLewF/olvULdJKE9sCXTpYDjttezvTsPCy6emUzPneCNCxX+g/
BvpoQfdJ/VCdktxo00BRQWkX7yOAEY9sbq4cos9aX+bZ/E6E5KqlHr3WY8MvCUE2uW1lxZpu
bqRwXyDT6tLIBuz2e/1O89NQN3Mm81cSsS0CAczfD9E0a65WTKSatO4MM7zL2hFobh0ORA7b
Z3CBSi+xFlH+OpMuBnAku0m56Aa8fJjiiQhud1839dl9foMfSHK8yuGaGNDiogEGO+vLqKbo
dA1sc/HlDWuIfBBHkuOjQDR/QJYQH2wy9DFCfHcdqLNOSe8zbp+736IYYRuxL0UXKPC+evgD
y1tqpZrztQsTvpDJbos6ovO7mxQ8i6l1DXUrCkJQxtqzOop2PY0+llZ+4LaMh8+rpnmXfheu
K6gT1eljyzA1k+3L4By/HNJKvGyh5tq11n3OjaIP7K9m/9FTBaLFvCjSd+u6UvperO/dmndC
U38dWpWjBWdpmQPm6n4M3D6bRgiKSx0AstroqTbtT564E4695EENWhPkpcmabsn4UPv4RfcN
N1YOzeetLzJ+J+ei98B36ls9BWapFsIwuYseQTXmHBeSPqiq2DtdX/lKDdIw0NZ8kDab//AS
dM4xBFKyfKUjXgerT/3IDYie9O00hZCkLwtIKyvpRQeU2FmR08az9Vudznvzz7qsX2b4hgn1
STrKxGP2x2ZlT1Cgpz/Fa71u226LKVM+e9fHIdMiwUfTJ8bHH1hWrhnuU0K3Uux1iSKL5tqo
uUcaGz4Rf+VkBgJnOC/fBs7UZl6/+1otQYfeNswe4YbUIP7u1J6NG0Z1s2BPB07oVRaAtTPd
XDY6V6CbTcIT/ebNM4VlPZmeg10j5+t8B0npMx28ynQnVVD0jJnfqnBMfm3G9u0iaYUHj1Bm
DMGr7jK3txTnvEDaSL59LT39SzwADSdlEBpH1tyM7EjIyJ+WqxdTnVGWNFfwx4ynZc4/A0kK
fydpfjXdyXdkghIW7iBzFzCn5bAvRec/GZ5Pm1+moK+O3N8EqybY29V7dppy81sk3wh4V5dv
OzrQc9ULlNj2UPbSw0tv8XsPfzg9jXRrJ6wOC9LRpWTHp7nPyZsn6fJKC1Bkt2KR93W9PnT+
FikAm9ywhRp497d+fbJJHOmMn04XatKcKD63Z0VFuCC/raXUsjuMI7T9CTwT0s7iIABATWuG
IjblG/IR4uVfI7AyE+Ir41gKec8WNmUWPbUOT62H6cYSeCZizKqcgxEOrMap0G1skVcJm/Qb
9lSf1FMumY/DIEjsmcZpDRwhCvZyo1TjTHtbAy70Dzt+dlKMsyQmLy8jDdQR6vQyurFNcMmx
qj45JJPgH0ceXGhkUtW5lC5fNaUkLDhQvnkP6ZX+hc+k/2wWfNnkFBAJChAp4r7y6qms1yq9
e0+3KjadjEa40IuAGen+4aQ00jV1WtHCTcdzzU5MBkrZOJ2NsU2YDSgAwzM/Kxr6ge0bolbD
QOZPdrZnmJObds/Uevlf9jMLn5mbgJXeEl/s6v4YPNa5D49oyG3CG9Xgxa0uTlZ3sjSbGsq3
GnCT+j9eeN/JvjI86ytHiQtuC/YsOsCe4YuMbDFbMFxsYxvWoovxRiLvXBHnuuQscfojq58z
XKDdHMKLJ4lzKeC+fSnqWjqAcZgA+ln4wNTow3ba0Ss90ZG+d7OiTgQ4lhSdXFS2cc2yB7Vo
LPsrnPtA+jYMa1BELlzHez4tMeGNwMIfn0n++aP/orf/apiMWCf/Ulk0kxto6zQlZR0FLkSK
2WRroI98fAmRYJX96YYMJ0+i3pEnvvFzKUnPAHiMf5VL8fm9/Dd/Ml/uebAtj2kTsS8hvTfE
eZJyYie1Y3LieSdaVzk2oyuZ3ymJMAOyPwJXVvK9l1GvTco4VU9eOFJHxxcdwULQIu34XjSy
4zMkxJWzEki/EYMA6Tcpd6+/Tb/hfJ30Gzn9PPlMw86B58Hb9nPGrFXNaoHXLLMj0Bb9gvxy
wy91pwzrV6fpH2w/IZ8R2ZZWkOe8hcJsNDI3pYDt4vVrN/z4srmL78Qh9gDh4Kr9fkbbUoE9
EaYFz4T7s4bG0tN07qupMp3UxNZH5linOHPSn7BGO7MwYKSXn6JCb4J26IXupZ7/6vhlzgcB
5xHEPspCAkUmwqOEKcbS0w59I/DkY/BU4Qor3yKjesah0sdDQ7t3RhhnGSzamJxN301kLYZ+
VIfjX93Hf//n/gTa2fRfWsvY2WY22yspKo/lgzNSqGaoY8eVTndqsf10kGvk6X92n2tWQQQQ
LbXsDUt4s7XHQSHLks0TrCzx1jUzxgZU8PfqcyOpGMa4f8lvCGLy3domNwganBylub8CgJT/
/Ff9H91t/B7fXHC2HBmf+zCtvoHtUaxxqM2JnV2KTdoKIW0xnlqVNNRcn6sdG200g/QQM9u5
W1UrAwi/iLTwCeYfHV8v8XBc5HzH1ESzzm2aXjgVR1OWgdsmKb3dk7HZPt+9jKm5SdML7u1I
8DJrVqT2pK4W5huagF4YI+Dxi8cuI+60BXeMB/j7WG9LI/j/H+7eA6qprGsfx4a9IFUUcGBE
QIp0pcUZRSwUMYTQUVB6kRZKgFhelSJEBhFCi4ImkEAQIYQAoShFuhhCSUhQOoGAtNDxH18V
Rv3me/2vNfOuz5+ulbvPJfecs597b07Zez/7AXNe0JHpHKUgk4B8jkmYqwBcWsX0L4QfsrFw
tdeEPwAXBN0fIQpiPo7x7UhGSIRrm1Z+CObRV7+9wUGRxv6/DSaFx084VkCaMm8jTi2CQLej
IIf7M/ZzV1ZxEjan2RcCTvxFb36i05ahV/GaiYflrUBtbiuZN577NSTqFN3bT9GjXT+1W89a
QzmwFCvpPK4RSml9LtE1bh0Jq17vdf2Lguv6PRo6yJCCvAyKdrqg0SuSMivAnQK4v0f9Tf2u
MbBWl0axR+p0D61NwWpWej4uXt+oE3zmcN+Xyz8fv2ZZQAPiXUnk+rigMaPAqCPn0ltGgekt
POy0dbF/O7nTHq82CTAh0wfG1DgSgT5HLfI45DWjrMohF+wj8U7camKehB7WIx+/9q7NSt+a
1iXSIm81BYFLeyPw4JpuPlG0nrYoA93Y30UdGtcwJLf6SCNdHAa0Uz9wHRqG31ul1pSDq2g8
XeZ9mCrLnIvX2icElbAuc8hx6T+mjkISOnj2t5SdSzceGDyiVARtis9XPfDRdEOKciyrDQq9
8J8jxX/Mt4SLM9tOG5+SaEbu8ZOxf8mUa4zMDCQR8XazsK8WXBu5/HTz1AKHe2yDHMSJLSNw
dXRpzN3BeejNYJUDhc2vp0eZjiVXesyLeVlzGeFLj8ZXH4Vv7ulPVMzr6r1Kvl0HE/IEaadl
x2RR50YqiXqD6+U0ZM0nk1s9XGONEtteNGEOUxGtKnNLz7euMapsWtcgmj214XryuXaHnN0N
rMdZ/bPsklR+atnBX16mryTt6+qx6zfQXnFkkYwktZsmPNonHiW//Qab/64zrOoSMySFuRIY
EG9llTiUZxNnl4AY55tTKTmTAHcdTMuJvsLfDa4bNRuA/f7aa1FXQ6DyTf74jlDCS6hkIfyP
vvV5Q4hH9Npe9nzXhHJf/jLSdKcxrbHnVWMNTqdN9QTi8/76ukvzM+3urCbDgLwMK5x0ZLE3
ezPMXxLj1aNzvHjPlqGh+Efg2Jrs2SJxxwo0S+yCPlRkUlkWLHbrjKT+N/B8V/yxjWQu4WU/
jVyhpSkvjS49j1lfzEr9uUrs5E3YhMLp03JJ080BRI/E3t7otwOrDWzknfF902s0qAyuj4AG
k1/nl2QiPfGZ+O6lC5Lwmxb5rl1CHRr9qgHpxjRhUysQa17/vJ//4qXsE6s1/LSCfc4Fll3K
7j/GZAYo4DvyTtOXZ2c9+6h5tKVLR/enScYYjMlNSFi/n3/PHlD7FcTSHU3AEubg+VtvrWq8
6cnA2JL9ZGb1kTgjp5RwXAvbTD1z6VFEamSB+Kxq0XItvFVNPuQVx//kEnm+PGnP6oWfhG9e
AqslMkhEK9AsYjgBiQiyYiewD59Js2dtkCz6u53DVd/3cngHb8unWaafqSWokjMnflfZisoB
REQGTr+rqVL0WDc6Y0RRYB6YmNggygo9EhSSIiHQTDRqaHCNFXPk2L/bT1rJHGk9Vp/RCNB2
aLrhgJg9gtVxAARyxZV/Um1deIhJnnvPpHrZKFiRFwHTy9UrVsTYtc9K3berOakv49rYK5+u
EjyDtdiU6MIaBR2fUlys++3IpU9X//Xnj815ro9hFq4GHHjvmYwpZrd6+QYnhgyRvVghtItb
yR3mE5hR9+JMMjig4c218crFUM2PObTGV9v8uIyyqwaoLsh1RDMyO+YEHeksRJLewHrT+TMc
ZiHTt/1e2otucuuR0Udla/o2/T9gSF8XIQL0JLvGhEpYIqYYxHRj0Q9cjW7nylSE0l+3CyfO
iCoNQKaouY8swmdlsDowpXVHHq2ilXuAzTR+6g2tKknEsPhZyVkeH7imcgXKtHjKWpTPJnVV
eEb557NfduJ7oEi0Qy9o6YSk1erFn4Svp0L/ME/gBlt5YYOmgzO/tPjJirZLtxa+FCbA9EEu
KRbeR5DPUI8CrX+boUEjk8eOuAhgIzLx2dUbm2GOwlVZgfAId/0NgAXxIdOJOe1K63o+SA7A
u6MikVSYG2ngJdavPHnzTPknjbi3zDxsV3DWejpMDcl53EZ4iLzt37xQ5zWZ84FrW9XB9CAJ
J8jEnHKldi3fKTCSOPq20abLrDKtED6JmP/t12/g+b74Yy/BrdTcYzx3G2eO8xh5gt2t1ZYW
Sdgyz7ln58flNOKC2uWtZNrkZycG3VJ2S+JWUmfemmNCh+TPrLb2Czz7DsK7WbFY2RzZOllg
kOwSWtQWag1k51zcKtPncyHK6IEoTx/nLUp3edu70q8Xu1Rue3D16p9WELpMaQahjfrqzSsT
iw3ROOeAXNGuqvEjtKULsndPZgu7uRvKjYmSl/dnOAtZL8PfyPW1r9zfqrOqL7fcjFYj6car
Zl5PM+xLa0g+Vqyri+IlhdGpzuQ+MK1REZmUExkU76kdBTiTy8vx3/aRzOmpkDuxWsEn4b+5
Ft68y8OgRFZzPt5BPFIAU2zSnMtX2bBc7rpINtrrhwssvGpoDYRk1rc+Z2JytBoh011Y0iB9
3OiaBc5ROZuZXDthfxEPjrhHmsB1o0IKsTrTNfSNeF/7lkkVhonqvcXpSiBm3GoJq0wjeyTr
a9q+wJspN3xWV2+zZZQ3A7BpDlowUBgxNavbxXRm91QfqpOE1dn3b7rckn6y7Kk3ItNFsPSu
OcPiztUc9RHp6srcpSOqt74Ygr5B7k/FHwq3WLdN29mtqtSloN9LDDOqJTy4UoYUu7/3ce3K
qSuTTytoMZwfe/dd3R3vLDi+VH8aJX4N6nGe8Ay8hgS9n59UaQSLOtIm/b2YKyr7kshHjEkY
7+Mvd0R+4NL1qH4aNbzsnm0kQweQ0tY9OPinDv6k4tHN2acNIIEWNKFpq8Tg0qUXET0Aa/1L
js2e8S8Be7TGwgtNaP29UBfr0qCVaaKdYxfhViSg+syvWqv6CkVSHJWSbTjZy8NTyfGIJ+Zw
iL1xru3Ahn1B+3rbeaqTM9OClZeaaKgcO8flCQScYFT3p2CXT9V8bda82twIApNr4sJxmYj5
+Kc1gUg7lQhxndd/PyHno8LlwiNUq609OkwCr+oQ7bxZq3TY9Cz+LqSQxT54J/U+dWe2bbKb
yEUWD+Co2lhmBll5oRMT4bW4hOAVEzo64uVqrgm/5gK9q7zCg3GwaSweHJ+aPZLIXPQ7c/jW
U0Ok5/YYVmSsriIvMi7rCmiswcVcYKW/kPvLqLklfSQuxSBwSZgsnTOYbd4+TjGC2RU9c0bB
AsE0bpNpXEX67pjGG6GJUFASzKzMthigMpkRPi91/WrCKvx/IfzgsvqX4mxcrEDA+LOZ7t1I
ZaeF2CrW/IH6GU7oqRi7QrzktosxZtLnhRvGZfwt7aEihwajgQLKadi0tNrqRpBfY66O/PYr
Vby0gp40THEgJ/dfLZln9rdYkoyydG0fzN48fPwYwqIKMSvpJxvBidLd9yer1Wo9P5nwkRPA
xYT6FlLeMpCTWkf3u1IJ9XLdNaMM6E3v32TcAj9PQk8isxysF0TOQx37aFOhBYpHWbBtlBPN
R1dVvdRu1min0nSBddkgBA2mJ0IO6BGoDN2x7h7o0glCyp7pIrf36HCL7rvN8YVeXg4hhfio
HtaKJuvmudUqPglfR16bTY1Plxw3W75HBvC93pH0d/u2y97VpDaStj8wlB+gf1wZG114GY70
FG/tCJsb6DshnveEPpIEDbey7DnU1NrjjhNkEnDtgKyc+l46KrS6qvzSK7VfhxcJ2axo/Tlj
FC29QjBfqlUTSgR7XGlY8gly7OX+/bN2WxxHruK6awd2X3HPXNYz6mx1IA8uhyx1Jcosmk2v
PxPI9zqb1WQUcBZNTeN0w15Qx067JCE5HBnt0XBz8fo3EH1X/CFb1/pDC72XdUmNL+T0CKkr
3HmOZW1WVcjej3lWJnH9HL/jI/HYCZCuMB73gYvagnUA6ofcO/GnXCs82LbZs6jZ7QHOuIDg
uaRbCnsPUyM7WsCeE2JOgmLpuDzDzDp+M0XbwDfqNk9vK7IMTMzKOLGLsHv7qr/r8E93Yr1s
UL+LYMaLt23xBrAnjOKcPrARu3XN7ZqlkSzPcbs2+Oh2bUyZPPzR7dpzrpD70qqm63WK2rpR
qeZq0Qow7cbZSG+JLrQRJ4Jsc7PugSDnfqR/P3uqq9tcbSCkzndpH4dn6djqpZ+Eb/wcDWFy
YEd0vMy0VTRZwzTOFt2B5eyDs/Q3SGr8zctyTixcDPKYVpSXQKJ8I38f5YkZyg6qP0tRdMiY
G45IZ2yE+M6jqsXkrN6NEKC6pgFQw02qsKXT8k+NPKOdngjJ74ybNyN7Oi09vxZ7vhbfN97r
FrKNTtVB9V3qnNCr71p15f8NbrYzlJHXJGmYousFshCgklUWesteNxr7SBBqY3gnbtoHBrxW
cDfkukZ27Qscd94POF1BVBYpbnfdRuEPKboi+CV85Bvg1oo/uFvFY96uLEpE3+w0PjUn7s9f
hGGLOw74VoZgSk9cqTln9aq27+6Vzo8DQSIJMavJFBxZen+1Y7UVid5siLaqd3O+0mIgazzL
1Uun3yLUd+XKhpG0h7qq3rXFudClGdJsnHcIM39JaKlz483rq9f+tEK4YWFRlLq/41aVBOxg
bj7LVtKeGhnvlQknnVGWQMkjYQZ9nndMlaTet3u3ZcaMk31M6nGIReFMbuNV5derBdGZDzrf
Hd45bSSIVPDq6z/FGYaEncdXNHQugOkHVDwRyWl9A2zWlK2/y3HOxv6dJlVkz28p32L231yi
cO+YiepSdSpJMyc7j9NsOMMeEuzpkmS+TxQGF133Ly2CBRFf5DClSpqQCivLcilSuwWyiWb3
rGjz61UZ+vlM3OKuyEe1vWENQR3PtMgB+VrQb+17yDyjusW+ZB72DeZn3XaGLMT1L3UNIsPx
l8nqrsmN6nsTnaOnQJw1jyWQZ2wuY3Tn9Wtecm8v27/tDIsMYGfg9fU4i6VTIeU+q/B+C9OX
8o+NHapFDGcv/9tWqm0lOsHWFfGRvKxAK09BzwmAk6BgOipHOF4K9E43ZPAsPejhgRo8gx5J
L6vxn6tIXmu/IjW3SNYlOc28KRG6VEMvgniSevAx9nPvLRlhQXj1QqPKlN1VUx1JkYLynGen
g8HZ7Ok53LfxwZeO/sTHO7vwC09Hul6NsoQdp5MNYuwlkYCRscEBIJiKP/Pryz92KqUcfqDD
Y9didOcINWCfNonW1jO6XFQBLf+i9Dr+FB8l14gAhbsGte/1x/bHAUf1axrmUKF0Wyklx6fy
/MdK7rslTYiglZXBZTqj1emh8AZu6y9Xfz5+54jxz/Ogbhkccc2yzC1PuU0YyJgYGOtsQCE9
ZN91pzkuBQc/qjJ4GjrQPryVlH4EL9Z4l0+2o3qFEQl5j2Wxzfx1TlwueEnrboTM0YqB+c2N
2Za8RlNBMEOSQVkTd8v1zzrtDPafturZfFHb0qgZo2CM8frDt3AqEJMnXGmWpvNC+nvHvW8w
4RR/cHkh0Z0NUQHVGzbXswYJpV7ZlcsQZBIgYZdhBDgNZ0bwAMC090/JE1dGjMo5DEw3V9vZ
wLOAfQeMe7UyX6bIuDY5DW0Z02ce42SHVox8nKprPUeOVG32oAX1q8xOnfrAVaqovMRZ5mNW
L/9phfV7gmqZKgNTnrejDDh0Lp0LEG1jln53HXFW/sSh4ris7VRb2WQJ8nOn9zbVHUU7sfmL
oOpNCRgdm7drNE6cXMaFiZxxJX4rJ+iy2d45EafPCf2R7yUvmdxSLrrqTMjH6R27HBUjBvAR
u1gLVx/xYAaCpZdZ13Y8+ga3r1fl/3CAYEQqMXDGoGmnsy89ASXdPt6VXpboEPKbgTLgEEz2
Zp2X3b0QzSeOmxQzWYJ+ob+47JsSbbQ5RzJtaH7/W5QV5lLT04bZLc/sWrsii0d+jxgOG59K
zclTNSLxMH57/uyzXhtsVkDBWjbMzc9naiMwUZYwq67c7hKjYfCYox6sq+LZ9W/0/774Y7u1
FfLPi3Qt4qUtQq/4s556ygHkoVAgPN5x7q1xCA9exuO9a1giILI5kjja1wA19heIgIUvnvhj
zaJkL3aRLjmGr93Mpyg7O2FZWV4/FWIQpcdJFu/SdWtbkCjTl9odDGpBcRaeb3wbMuAecjYk
I9hEy+RNq/+swvdK/R87c8IRZGC6kt68a6mqeFrYQy0m0rV5oZPshWsex7Vu7ehYsNYQraMt
yPHNOZOnS/TN4C5SeAPt0tfaX24zF9fJzRbL52bGrrAhMcoLhvI1Na/QzQuLxPkHFHb2xa1H
++4aos/38/7LrJVMPUK1CDWqgbRaI9/dnP0Gva9++2+JHiM21uw91lyRfauc1ZLGKrHefFdN
1n7YXEiofaieZJAVkKvfjSmmtJg08vDqCHOiy40HNmb+3Sme97xro12jxNbI3cJrrYhoOlMy
9PDdh5VmeOdkQx5dKOk3J+bPi/WLXbVnp++/8EY1KmiGZ7Sr2FSV6TK3bO7fvwk3TE63bA+k
vLPhr9MydgWVIWj0msqyoMM9SV4HO5w+PwsBSd1W+AI1mzKiZzuf5RvfkiwmE2mXZIrBOc4+
uhkalyh5OrtppbIOfwrkeraGksfJjC41nxLjcnh07PXWqf/4QP3gmkLoBgW2Prn0rPqdUzWB
L1pVIjnMm4PmhKVLimWPUe7MiYBmNMh22BTnvtgKZIFMHKuAk8ZGr7Yarba/KW4QbIQG9ktE
dlCADKnOhVS9GpcqsMQc1z2biMD2bB/1Yt+5HHxyVGQcBBNSNNRcEeHYhyt7wLtmOlmt62cT
ON7SaWAFj+iggDj4LdGLM8uWm40IovS6oxNZlcH5bO4KE6ABH1BXkSodFjZ7Y3pVvS2nRuRS
DG3ViiBaRoEvODkxw2clvb3HYEJbnfqN9g7sPrJ08CXJw70rL1dlmwdQJ9FlHulYEkyq8C1f
reLfwrqty07DYQN5ng3GKnMFkhsbGpVFFYZGOft/gUsr7QGsoVnNV5BAGmfpAgFIaBV6LGc/
K2DH5oxpK59/RcHri2hQkrOYOGcVawQJkmiHGXDBVmkPQCmD07cU/m6CtS06I2JZlq3zRTUv
0jIQbyDRKXetoED1556QeQW9ut0KGYyQZQVn7/qXWkWS91KKX8gdll/WqbR6RTDAlIXcPTgZ
ZOwE9guFsCEhROSu8BtYx65Z5+T9bRKz7cOr5MfbTzZxPzWMq0MKKcsQVfw7hSmJLuEsResG
zYJhlk530CMe8xaYAVo5keSvVOyjeOO5Mo4M9lRVpSBunwpcJkYwFy9953PwNeAfSz9mJYkU
ueAlf3VSsbJOtqUXR9cwYDBagdjLjcAJ4N4dgCGvFANSbRVLvSx1ZVdUqEQXwUcecO/6+bW9
Fbl45QU/lv1DnOywWetcjoNbCKQqgz2CXT8NZA+s4wk5oCpzLbDoVRUGR85wF9ET1u6M7GiH
Rdw33PJ9j3+2MzuDC8P71eMvGjhuVsCHZvcesvD0NIL6jvDYJSwKX/pzbMwWXiYxC5w5RSx5
jxmnna14c3R4nGW4KakbMn3Tu9DnKfDxtVnXoQfAd2ijlme5dtoZBLsIaMgjkxPfQPIvRj5/
O1iVygcyaQDmPhNPQEzrYX3Q+cE+AKkjuH80Nfu6nEFgyLlsx1TDXxuT4hioRpbyLrqi9qIB
SV0gMTNsYQ7byGq4+ZzZGx9upFIE6XiZGLzf8uqwht4dgDnV0yZscf/00qPZBYXLxnGNHsWh
HP9A0epmkv4i8HihSkhdH++Vz6oqQjNx+JjHk4DKhnvnc3W7koQhfP5sJ1JGryVRTKQIy71v
WrNF7ornLtmxs2mSY7uSnrwlg/EGi0T+huDC6aXrD19/g9n3xR97My4T378Zpsxr9rQdMplL
Y1Br61hjnSz/svF1B0J4VcNza1hThMVmNzrS1JG4YOihLVZz8+qJL42t6/XUVktxdBwp0vad
y2wie+eitAtxFJOVC7+JnWOdY2/Wgm4QbWWnX8jNsreedY5SluwLXaAfRF74UsHPexSevzZY
52n4JEge8mtVKK73kEY87ONbwRuauSh85c9vxc6QoIf9hujmw7wjebzWNlhOolHpqYZGYQ+5
0m65gx3CVRg3M4JdGMugSDxsNk1zw/1vQPnKwUT0rpaW+bs77D6fh8vI/GO3CDMp/h7DGgZR
tvovWt1t6iqIp2M86L4MvIGNjJYqWaU5YEofwm3zd9OKC895Lrj06F3cCTZodUUtk2zv2SqR
RF2ygtvvBUnMHkOta2wlX0w3GYwM7xTATgBdJQyq4YA0d+fCAib8Oeq3P0T2qBwJPHCmJ3Qg
UbP9xuO3l3RtWq/Y4ohweGvL5HqbE58g4N7lF96Fd7J6DHwK5Dgb/MsSa0B2YbGAuktIQE2U
mJNAe9quznTBO8GGDGOjZmbimABCmVUtrw0WB9Qf7t/48Po3SH5X/MF4tO3nGykR3sdNekWK
0ktOv2zHzg2XczhcynXVdZcwXvO4dnd9dnJKFNJFu/NeFyeU8ijvalwS1+7E4YjhRJnoCRPI
fdcR8vN+Vh6HH91rKr2WkYsZvGQFdyl6/9ytIRgP4a74j/39ToH/ayd2J8WRXejgI6mtLbwm
i693hhT5mhcTiUPvskeHJ+NzXBDzszJIh6Kjzz31l/Jn/xxEwYmx0ulCh4lwUr8jrQKGG3v+
5UTmFU0gIA0VPBkbvguS+dr+Bz9g1S8WfkDobVtFb/RQWwHD9Falq4CSSlbwjqSZ/k7UmJYt
SoFsnSiFsgsPQ+70m18unLpp8jdPqjZMYtISHTDo/FP+CO5SLQQtVX5qJlc16vd2aCJqoox4
BJWjVVWv7K/JArkc7tm0qXEsLybHB1hFPy85aoVgUBsjZOBM0+djnGyu/HxAsT2/ij2uvhVn
/1sPe5CoH4RUV9Atx2uX2drdKxpZNBeokHr06eavV9ege2geKxF719SC6dOln/fubs1El6U6
V1dh6MAJQ2vOmBkalRS0ElVnCsmEDfmxujMcLaZgVWT7/WKETrOcfm7If3yMfvBF2aYcZaGq
GXkLOuVJ0YtIMXJjJvgYEQQVPTiEBeW3o2OKqjQcj1Pl+dqpfu68oJdh7AHZQI9/235TPmvD
6Qkn7dZOh4EGpm7apZ5KY6a8IhkFmYYQTHPUZJZZF/9fiDXmG+fxi1Ab303QeUu0vZOifLqx
AZPjIteBK/3A5bTH+Q1ctxgzVZynnIF4PzRnUereDEGUl9mPdV83+rJa5cDUXs/dL9wN3C6Y
CRfZ1+WLKlNHklRHllf6vg/l+vpl+WeN5dvORxanMmrf6cww/F3etzxisc4DOcrJ2lsRlRdf
/653NgVvU9yE6qRIIyIgY/FYF79FIL8dOGpwbtIuVIpb1pNeazrZbQn3b+cPwDdaKl9ECqJJ
IxSrqeX7kuppbXD/zXGsWkx3rorhU9JzJp7DKlttkb57Vxgy6EhkzMQZ5TkONB//nSqzcrdr
XObYscsMvPqvPfNLrstk2yW1KzqhQq2CSk847NbfKcqGv5rdOVSb24frJ2cOgHhHyT4XazER
pZqhW7mB1/9dz//y8YMvxS4cNtIQgkDctvJHi1fVA0W7QPo1/Rs3+JaXGQK0DyjiMlm8Ntl6
NaaxCP2Q127cay2qTjBmrKghZ2fcuors2jMKyTa+0IeDFpP5zR0NZ9R2rX3xZ5UsQt2VBjfH
pR69QvZ2wqSE5+iqnmInYK4pnNIP9uGKEL0XoHJ1yp7jRyQyuP0KU3CYsy5/z1qu/2NrwZrG
wnOTftYHTg0u2rvM6D2I0guybUsvY8dZ14YvD177PiT9F/XsTcpGnLVFQ02zm9vWaDJnYhE9
qIekTkMPZgfdMEOLoXNk2MOIhBSxMznNLEq6JcexVAn8Nyf8lvXX0lhOIdQJCqrun6lSYVAR
HTzKM+Zqg6IJcwOjJ8Trn6SAWGOHJyzD/UtU3rnbCLuAcV3INrD6xBgn9hTuKySzdWrY8qkx
ahLwbFK8tcUmPQbb3zUugnIceKhbiMwlGFV17HP5DNIvJ7N3YZkMF5WdOpFkkHDoqxcEkMhS
a1eOshIxldFFBon9uh44r/kmo4Vo/I6bX2AJGRKX3sd5SJ0jxnosieAA9hLolcIa4n8l/dhW
MWegP8uqfjHYe9lZlaKy1ExHCANSg5eZKDbA8yGuvGNt0c3l2t8qkEQDpDZJDLytNIYKWr5s
ZS2KAWzkteeQDx+57TMwBimClBmSmuWAE3/VqZ/lPLf2zIb2DFoywsv2Aq5sh/Vr9Iay4tgg
hpZejbrdOjERnuktr3pt9/jr3W1Gs1wDRJZzTK7Scgjz6tSNVde/KLkhk+OQgx42L7rtQ012
g8ajQjJQCOSrLVuGb0Tt05p6XxeROc4Hxloh1dNfPhnQDym87vadN8THF8SP0gi5zQ9S5ht1
24KSDOFhdg2zxA40120byTB6M9cPZvPqLp112vfL38wSLQSn2ILwaO/fSr1cc16aouOe2FlO
LbhE6YmO1nRQM3jmX+2ObZkHDm736ae+p2GvmL/JoiNPtcP2G6c5h7MX2137r1+6r6bdhzyV
R5g//W7XpgjxRA/WTnUNOx2seKM6899+UjOf0dqyhZmU3ed6YHx8RNBTF+JbrGG6S0tvxClK
U7TfePFpPVLqMMxhCAKpfv2a3abKo5t92KC6gqAfJJ5kmpkm0fdEtPwL6n95/NEXQm5915D2
+Wte7iC14Re9twW0GB6tp0nvEuY1y//MBrWHn6KnX4aeqiqblCdTo36vjolzpaNUGlx9Fkf8
1vurOWQaEvKm5VwiSkwGhwuJxjpdYJfEMintbxeUf9nf/6t/+BiOM+VU1ecD68BADR1Owx2Q
EHtgdc6Y8cGq1DsJMaa2+6ZQSO1iaChFFbKQ2YyAM8oPrU2V+MTEVLsHbG9Yne4iDehcYcnZ
apYEwc5xcvgM3BQO+t2plcmhKJvnpCL0jSJlDpB1Wim6appL8QM6Rw2/g+4rtxGcxg1btARn
vGiXCg+LEjuT3szimBpQoV0bDv3N3lXrAQtkZvvR+Us0Devk8DS/nePhglLwuXqTyw4gRZ0+
cN9gdxj3L++NKh5PJ/S2Ee3GY+ra/HEpT+aGpwxMjH30cc6zqMh2ewaCe+stJ0Nhd6ym8t39
YMdey0hIvhzvZgPCKT0nVJKaFIFn8uK2L0q7dte4AOi3MqIHXuO3e3kz8FVCtFj9+Z5iFUfy
baN6XZ7JW5f/8yPzQ9kYubiE5yYcIthGxiyYunjO7oy5Yo2cwClIGslUSYIF5vrzqMDhgZXj
0Je6v3+eic5nagIMazEhxMh509L+jI0Eb3yGDYV49Z0kOtanBnrE3gnsQWG1HxNwyOQExA79
597+H//GDv6RQ7iuN8fPvCQPhbOyx3dqcpd2Aw3uJa3AoivX3x6KTDO2/5fW6S4vPZcpgqTO
Dgqr6p6Fa9gHLinkg71nVpXbrtmk464Bk+66XGbFjigwzLPvJYZ7hy36rZcLkrUP9HCelZtP
c0jav1sjA0tIlEle2gLHK7MrVK+v1vBJ+MpcePOfZZLh8Wnfb1ub9/jaXVdLjNYdB5u8DOvo
FZhIoqIUgZ3TtSmMoTZC1T6oJncMaMBLmosLXbGCqkvh9+X7z2Fe5E1u2Fnoif/AlRQq7u4e
zwkfhM1kiSgMhgDQ3WndSaM38qU+TyHWzQ9NvVJ93+/zgeul+gXrpBw9+PJcz04okpra9lze
cf4Dl8/U3/nYz88I4/09fZoriwt9+saorc983CmiVX5ve63D513Gdt7MwCU9AHojxvlP6UPL
vxAxcSj+lGZyW3LMBsSujG1dPq/uYPkSPZI1eBUEppad+TUpJsQmyjN2Za+DMThCjhWsxUl0
ExF8r6beTfD1N3fw5yvqgS0NLkZqre8o+pUyNQ99oZTGYf2+HaPfPDc0/9uYrzVZ4Z03Nmeg
m/AOfaF7X3tWM8USvX1bN+x5WuHcDeTBVYWrcU8s6FDYHzbSji3dJDqAd3Mj64qjfQcSD/nt
VsgelSCFCbGI/Ted5kfleDfskmGnzSyMJHASacHv7/2OgfIbp9t/lEh33a4U91mV/gnsXZp6
M+08dVYV4FNqal0PG/Ji3zg1BTWAit0XNQnwcUkseZgXhRlzWWxOwwxEtkwuteQQSrZvqLXp
KisiFrwTiINPm86GJiFNIOMMhhzT+wg8N++CGuAzQHw1fOraKbEvDWglkx66xRrct5EYK5xj
PufHJmhMf+nBzd1BF9yLF8Y19+sZ4xdSb6CZ1LghVjdJ+ba/KAAWc2rpROqXcWQV8u+EHxwb
9uyjADnRBVMvy5RwNU0uZgs6IE4klb1BNR5Qir9w2N6e6TsCVTjR5oStMgyND4/jZVVBMrGT
t2irDW409HtVnsYormBdlJ4fvWfgI8oJ67ERMZ7t5LbyLWrAKsek7g88H2sNCXXtRCCmdTVw
tnd0ZIKP7vj5E87w2LZzAroMAdz5ifJsvDcJJtkvSjep3qRiVGvNyS1//ukuxOnNv0LV5SOg
hk9TsP0gna7qkBHrlfMXdpSu4sct7mfRKvWi7y7UHgR2bm54ozg866C6XVCnn8itPK3yksg3
gbyAaa0qQnt2ppXZOeg4GRhP+Kf3Xz+XsFrHZ+HrGVTQTWpau5EHKJPACUHfr4ftTRHoaqYh
uM/+zV4kG4VmYF0Ffgwv7/xisDimYIxGVqHF8E6rggSVioMRJs3Vu7qBlu1qDFp/3r/2qfrX
UbXky4tDNSHzi/mWucqcPHgXpEofWkiezm1aqShzabDKe0ql+DyXhJmfcu7kAwKKrAiTN0PK
P+m4KXrw7jUzmtZjL5+Lr3BSaezWJnKPI/N5dpO24gQlSKJ3o9P0xddKPsejGfvhtbpmRQ4N
pCiQLTBoxUO2ZZLsMCQZ/C1q35d/yLzHtfHgzB/kzBcDvbslE6GGj/OmRxGzDgr9livy6+SW
sgcZlEDOXOlprG0027T6tQcdS8NlbVc2WSJV+HzWhbMfK0S6Ni1m4lbK5xFNXpllJuI2w+wX
xCmcwKaWG4FBJ10fuHQlORfytfekCF5zSVDVa20ES5fR+so4fCyqJ77v+M91ZuMJP1L70Kse
5E61EjCDBPDsH2zUab1ypYoHIJaJ7uP2nx6gTRUQOblEU8Chs/nFC3eRH7gKno/3wYR3rP0A
cnPPJFLGnUvQzsfUSu+CGIVCBA5tZBZaUGn2ffbFj9kKY3VTt0xssI4IhSr7GYcrs6qSz4NO
weCcadufNkQ+QffNaNP0jxrEXUdaNSXH2IOEsLkFAx1LicPg8jduZN5pcPblXvuA0Kbo8pyi
Mlcz4hLN4vWEDHwXlRpkEwdSXKhFkGJ42Mf5mqt3+6eNxR4vIY/tPF2sDBKG1DbiklJKPm4/
7QqLXukiqy79sTXn80MhdJvib5H7dFKv5JknmMcmN+XJZYvwZT+Twc4y2qgbCLBHEf24NBwi
1burtxiu6JL5+n2WNZsJNwV7IyMkW5eubQX+56frB+nU1u0QcZ0uZgfGdBY11Awfh4pXq+p4
tlObOVv1eMj1s3d/FX6qUSYVLF6flsNnSQ0QIi3T1Hpaa+pPKASs9uFjkMch/smWvCmUTlDT
QjWedwyMHuQkUF/PNZQerxuc77lDCInMK33u0QCNG55TFCu//11Az2plP43A+YXvbJucz2lR
HEqdup37XhY0pj/g0LUYf3BvXp38gUve2RWjnhtbAA3yd70xDpr6IJudGHRZjclN1vUvOq7X
0KAyH5i/1XnZIpmTWk9nYMLYPW0iCw6wGr26bbfSVhCwzXHa/kozIpmt/qUcEwKHlk+Uv+yd
Zda+sS91fDl+87p4wMab9IwMQWMGiiL5UZJwdXaRdhHsoJLl37zFqzqOrR33eELm7anNzfIi
EPLAUNURpLcUMuLgricLVSk+KQypgQ6cDIrhIXCgIQQUBRBuNJ4wIF6/Cj4ZJd7IqqpaDsLY
171751ToSxmtUsddbTcJLpCeXydb/kmz9doa7a589t69eflSJBV6E+Oht5aidglk9G1/lfVy
YQSuRecD1yXvaVAL6Wy94WgbzizxSKs6TrfINYHVL2fxopKlyKoEWb+a7fnt4OcqP1X8P37+
oLGDS9wSp5ZikN3yQtuGM9NK3mkv7EiLBCu6wEub63ZUDt9FQo37XO/4e8sHjOA9QTXjLKCn
SX1a2Fwm6v5VqdWWj2KxTbdP59QWPM0A6UX4GlQ8HQQCgKpWWLGy2hjFiZuNvlrtgxIOXrau
s8jZMpM3ecvNQ5HgIU5W6o0pq5X8rMIWHmZedjeFSGcUgkNv6b18c9Q98AOXpUZIJHlxhLLe
pxCaZkmz3OzuXm8S4PQmP1hLxhluJ2eeFgZn3Hy0qvRG8Ex9qwIwqiJbJhL51JqY02eVTsMk
lKPC549wbL5nfR+Tpcr74I5XgUbOrT4zwYloWkIz6WMSmKvvVyv5LHw1Z8sKnF2wOZAVWu2M
jHDiNvh7J2rrXibFO27YtQLRNTbIgoKscZlsaZSkQ+gZ7rIQrQnceCm00CcWSxF8ruR3b9lm
BiimG9QmamgUOcqa3fRsINZ0vrihTEA1gKTuVMeg0uv99GeXFSjtwTyifUCqRNf1s4OnokiO
+29anaD7tvD4G9NNnGdAo43HOh7igGJ8/aDJm3onPum8Eej3qg2VlbrbfSSQl0eX5Kk2k4FU
mU3WkKMojgV4VEInd6QNg9It3xB/6eg0oSb5q1plW6qNB7BUjRq3s9NCNeSMJyDcltc/I/jX
hx+MK+GKjCYKG4xQFTbjqbCLlXXtikemQotYQn5AdlbrjuvDChhyxiSoIFcaWzKciMsON4EC
j4PorElr+IN90aut7wAzb9/wB8TgDgEdWrtwDc7qPRIdqCjwXhdkBJLv1p6iAy4mFl1atm8k
c5C1L1r+nVHLxlp5tmP+N9lHq7X8pAKHPAfqML5nfqpHAIFu7yEhiYq+lj6ioe1ynbmRtB5M
dHmHUqId5799/ilI2Oa13UJxsewVvO6KxLUyj6qQkYoW5SkHpItCd1oYcjJwfl2ytbqKZhL0
D0OBt9aIxJxLVwcDl7OSRyMn2LhyJbNvsfqGNesfzaNcoPXaY0dUZr0nv7oo/1xeHHqU7rCi
WrvsPvSyuG9wdOlgmA2cenqXo9q+ohVf4DuapqYJxQkDM9cBiok6jnrLwO8JGWNczBOb0PFZ
LoIOY6Z+iwj1EWS7FS4Tkzk3cIU35g2vK+31cfVyihM6f8z6ZSYzrpmg0n5aARYrsC7x7Sfd
1/MvkF3jfYjJNI1Dx3lNdRDPJ1wmbaoEcQNXG33GG/mo8wf33qj1CLf3nIx7IQIQDUtLStI8
34gR1wxeOa2tzlye6dy0di++xXO1/KPTOhG6Wz7TY3L2uaozejCXECc0odNqVVGHCZ3hmtGQ
HaDX9jt629GJqqclFxrTukIM+C+9pdBGP3LyIx+tNvZca8xZxdUqzct/V7+OFCEfv6OUwYoE
Bh3uJ3DdY0RoZC8eqPXcKSDDsle+0ncFJEqvN+/wMqIWm0leX63jZxVc38X0EdQvFg3jcqQd
gb3wW83aiy0+NhzKYch9N9E1rX7Ry5a0sh1Ac1IwWTXYu+kLS2rOp2U2NWHHQFwPxgzfZ3By
K9xqk6txwtoPEVY0EyBYJMHk5ndjz9cU+uMZp3S1dY6bRtiJ69gN5Q0s/yt/R8zfy/ewQXAB
4XEghVArtnfy2bhu8XzCnLCf9gcua92lJSiYk5kWVK6nbnDusMd7bGK0dI+Bioum411Brwl5
oxHXMnulUb0am0Nlf6y7ydVhj9bp5ASnyLxzQAQ5uLx6M84MGdBafj45foW8SGsR26N04jNa
JwAmpNAVYhN7Jc97ySr3qcWb94q9TGm0UQ2uCOZL9A49asTd9FqRjWp5zS49xKMbJWZQXY7X
D5JOo2CcwualNz9bg/2vpB80Rm4sqhsiqNpczF9a9NHOD+lHD7TTmC41dbmznuVSpWHUKsE5
9UqD9UfmR7UbHZWc2WlsOT5OQGIY8v7eLywWXFzbAxtM7/r7TC5W0gl2DvLMYk2LFwRF0Qjc
O+s0HfqJux7wRLow+JjptSM4cb+UvMx3QDGQyvyR5dLzvIA9h4/+lQo/y3mxWEUehmP+CdXJ
PmRV5ViomkAOwsWBdB5yxZVCBqfaFfsy6heBerCwPzMYbznIbC+UMB887+XcAoYlWJzmJD0g
9lSjJZYP8tpWNK6PynwhB8ezWt6m69GCHDapsKd1syx9T4VO81//Fpevpmv/bOLbS47mKTWx
6ZNPnzrNtYtLWDOOHYsfZrvkndYBcaJULfJ36PTjAAml8cGvJjZvoysicCNm+12KitmJ2QHP
WA3+s9Kt8s2ekN9uXOqEPczecNjVe/gFi5B0yjgW5UYX3Luklwu5d8SkfXHovtX9T1quy4Ht
dU6V9ROmTGdfxHjLjpRYRwm2MGSq57FCbb2zMs7X3Q5+i8f/UP6heHauHXrM7FunbSVoI+Kc
JI0CpvBQpLfjxRrCrPwZxbuPU03mDZXfUryh+u4j+eTuRrGVCxFoFnnyxKG1UV/EGrwt6vz5
BjKuJkgpd8wMc7gzIjMBWbRl0/BdhJDV5Pu6ftCcM9EHlKcDM4Kfq0dJ9Cdwl1//H3r8U516
788meLqNWtcQFcCcaLr85AYmBslZo2CISMbN7UEmTghhgiZNTKnhFO2NomowjeHZZogMbQhd
meFCrim6LifnolUinhFYiGBqOLDq8vJHNaTRzapgT6MqPFWbMc3mLu9gO1XX4OEemkCXCCeU
9qvo8r61Cj5JXznQ8//XyKp1262sa2Ptf3sn+RpvxfHfVTZrzSF3N/fmnVYt9pm8Yr0prl2S
UTHUT8isyqPifp3Y1dfXqOOxcm5Mr9mIMPCGVfNqx44XL+tafWSd50xdSDFxkCQ1d/Iwrggl
nmjfjQjjJgcce/jsaO57NyAftRqvixHXjnAOC1u8sOvaJ729+mwJUXYDBsy0JEhG4giCLS5R
8kp1tk9PeJxvfuodOx0HNOhKXq6JL/RcVOwfNS9L6u7BtRpV7lyjiP0WyrXyj063okV088UG
4H/gZJyXUcHRcfaARg5xUCdECRDBvdn3ZLtUTU/O3oKudmrWMik8hW/Ry/5whfJEEErnwp9Z
hdtfxndGC87soRbpRkhG+DZJNt3gIy9QPRzB4TQG69r+zdfXevZTSutbpgKRhkl1aCElVB9n
a0yN4JKYBuVsjfFTpVkTFK6I6HtCfFenrHFX2o0CKzrmZ4eQLpkNLwizR+4bJKxp3F4fXgoM
nfmlbXq0I6L3Qu+OYW2SotowJV00YXHbV7Fan6/5ZnPsH7VcntSz3Fkfm9Swq5YKVDxGNX2N
1kACUuX7Bq4ArSALXa62UlqpvjJ5uRqh3uiXspY2+4PGBE4zcwjpNaBEBf3mYlUXP84ekkF/
+llCjo/IC9LemTJpV0DQUMKsNMfwyD9oHlEqTz7Y+cV2Yhl9xV/SsKl/MJyWs60w/cjZzoVq
B60GNlzutAg1e2VBeqOOL5QmtPCB65jajCW7B8NmdLTizysrTqtS1HId7BeTMem9G/vXwP1L
6cemVutbfGDhpz1lrOzyrPwjIPJE/970bSwv9vBG0LR1XbpYIj20EUj1hsiHYEI+xpGs9O/d
mrvWpvC8JwbnFv2kCBfqruigMqYMyqhBNgqgzSdbjToMlHbeOrH23Z9SWnePfnZmZNH/Dx0p
R/sQkSVZ2d1Gnim1zTW5tuMeJjvEh2CPaK96dvMRtFp4fYxa8ke3ubCG7kXOuibMLRuIHTzU
saa1a2/FXE4Y6TR7BX3XNlpVVC64MyK9uYdwGn1cNTi/5eCf3Yk+XfW1i7y5z4SByfREv51M
ePh8PMoISU0Rjy6vxf29OeYOgjHsgVddB0Y9WBrjznjCM5VspcrK2fFT76ivsIz5pYjenk0h
FJSbuwj4RglPdZoT/vmxEPhbdEeEB0ioRUxyY8gjc5tkC5GUl001248qtPADXS/WNoUhMdUv
ykIRc6jWM2oCnzERqm3FevexPM4GJCXdtQJCFXbvNoieopH2HW+T7YJ3jZnu+HUIhp94Pne7
Sm4EVJi0YBqFHvYF05r5rnYTvTPmBndx3B5G1wD+S+nH5lXbjCKD+Pen39Yku1ul1xhmE/AH
hDPZPWOqdZqhc3ti3tjbzsObcJ3k4obgrjd4t93qee8qcySWD/BWrzWsOsMERPm4T7VUFr0/
kqTuzhQO9SsaniZ7D3CrjvNBS2UWb11yg7Ze6SDEeEBbIGE4BLvHvuS76Lq1Cn8OiVtwxqdL
YNpDH5+i0e9lYMEmPh2e1qMYqJOMaX01iLkbVzRE3BcLFy0joZhM5KEMF+HTSL2kFlPtEg5H
p7nK0vXY96uKXnPoN759F6Y0yk7jRC5TlFlAXuXZdTmz+qNnKJxUgFEl4YmDFI2HpxptAhOz
hxH+4qEWvz07sXr5Z+FrJ7ASJu906XHQ8r9aYHstuM/8vYGHnMm/WAY2yvok4fSNFKOIKP/w
fFZqi/aSqVNTOjfyYeS1bb1Y1Ei6lw8C68znP46fllM4iy2Bqlokl6lXxXONTt+gqfmNeXmp
Whb0YAoGulpnNH04P/cggQnocjTIeOLmF6s39+aZh11EDQUZYY+oKKtTHju7b90NRSC1Ogn2
kh+4umWpm0Ra9rva211zDUtqS/LaJ4wbzHvabuup1RIeqVtn35NMXblwdsu3SH1f/lGryrHx
znTxqgZoDCMp34Bfj6jYIbw0Ta3N+X0w6Y4NFuVuhdY0folLLCEb+KssYa3R9HHwJTe+tfYO
xmLv0NGnBgFWnNiw/JEF+biMhkUfg7Dq8Ul7vVdb0W9Te9D+7x0ve1BdEtMtacI26bw6zQ8r
CT5TNyzWavk5Jbh8gUZcsRVxlCTuApeOJWX1kUW7LCrqUaHLYlKaIfz5zNx5O7pGVL3yqQHP
e4WoTHh62r0DUuFwnyrVmqqD9w+uqn0hOaiLN79wX6U1xSh0QY1MmdnCGh533cWCJW5xGN75
yDhrKhbFVG3hN7xNmDH4HbGAwNCPLa/oh3NSy2Ss1vJF+O+t0sVUKQZ8jX4Nuio1gQj2QeF5
7xCXUhWfxVx8yYJMZFHBDKlIHtjdLCjb7g9oXqY8CihZ8Si2rE9OlXVhYxBosWtWb9BlhNse
984uQn7d91uLmGuT7b7CuyQdaEFcgexw6mBwFkY+uOy1D7tC8TNa6+U1esaskjQOb1ULwcYw
gxuybS+W6cEA0Y1CbSyj2tD3CoNn5XKiHnlbE2ZcBXoSZ+VzMcx4lMQQFi2ZZYZYGRRImLuB
uPQFq78+/qj5hBN2ImjQeLsVdpL8fjhCYsM9niecHRQ1JgUtmsOgfDUj+L3ZIluJDVBOAptM
Wmc5uAVbetlSrAgpST3wiETW0qPYsfN+lkE10loH6/EmIAG2R3yksig9OUhOP7igT/DRX/f1
p/jLRrOZWsp4y90K+jZ69xtP63bvMU62z1OXgR6h5+N1LlzxP7ss2oaolW9pJJzStSh4jB0A
69CNUyDNsD8a9Cp3lK8quenBoK0pIW0SXjVaH6er6OPINIvRYS3ym4fNe5yQEEtLjYdJIEJo
2KrSuTmomGQjaNmgHtEB1A/2pREn1zutVfS5xq+X8UiAKsXWSNRUsgiVucaYLdHHrf/3GiQv
dEHoYDWFjQG3SG5kVavXagXYTBrqcD4FlHw+XlyCjkBxHEXE2U81I5MbJcDYspXtQxaobBF0
IwNrHM7xM86+JRhQUeQ2nirn6c6C20a3ve0Keoj1yPFImleXP7UUd9N4QYwlk3sspEpkVlWf
jHXVCI3Rh/Iceyhvncr4wIW177t+9ssC744oPin2sGYC6TG+JB8U+WSUM6C3iCZ69jlcqQpZ
XpDt3Bg3qVrgVRAvdUDiTa5cFZ8ttcMiuVJvZEpqBuQzQQnlGDGCv8N19YatCj+4tufiRDlf
nEzanLFSnDFA4TuNrJqnFC+IJ/kxW2KMxl2+ItUTd8TpxHk09b3bReCrgStsNq/CcMidffZm
wCfIkxx+G1sm2E9H75i7je4w0Uc0BSzsEBLh1DqZmaYjI57wA7GYq33/vyncNSxY/MO7sP0l
6/EgC+XumhhPXOaN9+5eONy18ZbvAs3E3VC/0Pgph9lRYQimUgwl+uOu6i8Rbtx/tKpPlUeG
RRRdM6b0V4rdNI0YI2yqpQ9VacfYVXlNtPRctxM7GaVEp7+sWnZwnl+ykhMU4PAu4/spgEDO
zL1utZYvwleDzz9q0bdHG+9st2nqK45IxBcisIfPpJ9jiaZ2EtVyHfsip3Sm16svnK3WaaHM
9VYvFQ0kaYrdnV16sshjUIeWdOwrRxbsWL9xcPoG1YSTmerZDCfxVRFBFI01grFk0nc3jsF+
D3nt8OqzUtejM5PgEtd8iGWyVmWCXtOuGjZJUTwLddLlud5FMD+if//GMbcoQlRegc2N/KPZ
VUILovGRqE6URD5QN8mEhpLoQa1bc0H6gtT3xx9b7nMII4se2FHSfBorOyox7mBDj5R4XZN5
VOKYcwcBWlPMwL3t4BVe3neM/dy9OUi+xcC3majIWLd2q7Y0j8AIUnXvarbP+pKnqB4EJPoj
S0ZHWl/N/K/B14tERP0PuCYjySh/5JIoXfhh0uAKNem4jufCK+Xr33f6pzqz8YBfeHu2y1L3
aaRHISab12W4kL+mlQLyn9QMRvAAhA594HpI2i3h5j3ygk5E6ANjUG6NHGvBKciy0hdzwRoE
l3ebGVQZhtfO0JVcElIqiNN0De1OlHzfB6709ZRpAC2/99p4hOZz6XnWeQvy9DDSQzHLisiz
AgJI/frlyVoF7+ttAgufWZdibS2iWVq/Nso3WyYnwjdCUqe1XMn+b/Ul27AlqGKMSOtC2rT0
SMISQxpRwz60jggtnG3gLOCxRP/1y/6SqecvTc8NYMPn+RuMcT09rHMhOfwQTK4IaZ4iDb8v
tGNnROBGqmkBWHLpcMtoZdVxzVBGjvZgWbMj2ObKckn4pg9fVBSe9dy9W6AoavAtU1DbPLLw
WIWwZyi9J+ssJa2Kk1Q2A6U9xP3i4Jdv/y/HH3xLtogz6YThFuLrdryMM0uDHfXUhVeniwwX
WuYkVejt20i5ZnnNuDjgeK46qGjJd0TT8XyrNJYW2VEwMr741vTSagfKQ/OFT5+GyRTtegx3
kUHrMzrUx0EzasyXDYTu0REC1/ugQyMC4+8FQ1hzGC2UwPjMVZNFY+g2jhvvR/rgyNV6flKh
vTcT4jaSPOWllHUGM2ODIXtJoZD/TndjCdTXI/SgghkdhxcNX+BRw3NFfhF2cj2daY08olUq
ZB6xayKfbWsc3fU8LbVN6am2EJ1wVb0H9QyTqxy+AosXtSjHJd/gRzNFcsPxz+bNu8zbswPs
AcEOXXgwhcYJr4n+wHXVwGtiA+A7+L6etf2T6bHWKxd1j72qfNe8Q03deRzrGkglEEWf5Orm
AJb9WWcUx7dlvGvXCzlZT7Fq5guAG6gFM8LyQETWOIyk2ozsvH/pktqtdw9bc5/NeeLVdORE
92v6n6x4k01mAe2qBNJ0zq27eP3fynFirF3MqGpxSZyJL59ZRQ0xFpI5rcsHVAUBfj1zcDda
PgkWPEV+iV2ogSuxLB6G5sZCMNBZkuN28SUrLHVZLSJ4patcbfN3QH1/4gejY7h+R1sEC2f5
nC3wEW+tKsmOvD21XEIBG0J89YON381f2htTi3t8Gl3nuXnSncKhhLTQAdS4CtCJi75nFIRW
W1UUw5QmeWrGsGbirBVVnectdAxE+5qewl3HrO/bbz5pfTqDVG0tWZynCNLg1i0OWWpRPN7a
rjjZwrF2Wq1W8nMK3KWaPTI9ghe1jYyacQo0SmH9lJI2Jiu4I5JPb8xL/8/kQ+v46Zxs9q2d
bxlw3eFIECXnCp3AouhfIp9aMgY1P9gn/QZ+joCe1M1TGkKJ+2mxbGWI7AHlcer4JMetcuhb
eL7eOeOkPFf86NqSkICcjdWFq48eenQFrrfbQt7oBUtv/Fh50/Vvr///W9543K+ATvAppD1T
U/d8k++e42MSUTxfEhgIlqOISYrwTpRLp3r0pIpOM/tdb8f0Irp4EMUox8Ughw9cyMWRgdmD
QrAKkezI0oCWZxBDv0JiVKH66binjDT7EpDuUjGEGT6Hve828LlXcpuPad5Jya4jCOCRJk3a
dWoQrF0j1TGfHMRWhWQ3GBF6camMIfG8dAFGFDgxxNWiOEqV1gKBuDPl2VOWJJ/DAhTF7g5E
WnEZ3xnJ7wbi/0H1H6RY5Vq3V+TadJCspyGf64Re88BwEOoAJ0w2qeAIJ0xWDCClfBLlkRuT
PQl4eSALU9yVF5VxeSGEz7zVO9t4sU6a2+j6l6bXv5jqJ2SPeRgW4lH0tCOoJtqrVnFJ7WRz
tCSHWlYRsEciNs3hLSmyhj6FTwOca4X8a5DCcSOyhSfBdRUnr1Am168R6X2p8+c6fvRzUVam
SjQfbK+JLYLR/TlJ7rMdLBA5IEY84ZAJZTABRwH7pJcV81sunujQWlPuZI5lVM0+K6d3Yy3j
2tONOf7GrFHYqf4uwkrY1o3DEwRpalfCe7R+GnKHTcthY9ZYf3dxrPIkg/vkWhWfpf+i/XKP
NMXT78qYod8sBAnBuOQRrvmSjgjbQZcGM1h9oHEIMcZb5yA4xEIrtak9QKK8xNIPGJV7LDBS
AF0WsKxUBoTM9hyVnr8kYIk+TauiB49cyznfQOCn5WJsW9MOMycUFTh2X35TZ2TY/h3XP2m3
43cmoXB0yCrW84DweCO2aAwShzZjgZ0xGY34UIx9d1pVSC91bIfjkA9B3r9njEWKVPQItXfu
mB3sRA5h4zPg0OlwZOg6mUefwfrfDj86XSsdiXps/YqmJdHV2jAve2DZfn0ZBMuecEWz7Fu3
D78BWBGw3pcfvzW2AmnI4zFv28WAqrZJHMeuCYCQsspqBwQWE9zLoJBrm8Ohlvtn3O2dXI8J
DBJCKfQXxbrKkxSuu/LwxTttkU2S8knehahsmDszyI+newiDkutjzyuiQg8afvZxWK3xJxPW
J/RE9+flHbtaTLij+4rg+vvrvBmZEQSLj+woWhwLOHTw1ljsojeb2FT9ptW9uclJGJKdQY9m
JLq8KIaLlb7iIGB0Yk3lWyvPNapIRknJ+jJHwrFnqcIQES+WPqP2U1b0m1ZE6zfeKvIWAUbp
V6mTgUKWEifzQuGZRMOdCTid+kL577D8emD6J+P61+U48jqj7y3rqkZJmOHuZVnXVCW8XhYZ
zuEdeHqsoJe+LJN4iR9mat0O9ZrKJOYXxyzYdL6ZzpZsnR1nIKrSZWCwOKvgE5lB6u5dIa5J
bqSLyzn8FtwtrcqjFMVp9SOkKPgwe2kff03d1rLPcPHUtHX79NhdO3l3Uan4QbUhtgjbymrp
blab8JKn4UKlGzhRqyYkIXaTIbyuCY/rtyfrNbLeIWCihdNdua77hTlOazjjoHWpb9fg/0vp
R1+q2RHr27pNFpDQ9Hfj1lFTUQ6HqRHvlR1C6YWbx3UPUOW9ycXTH7gEg0Y9k5PyRP4/6t47
oMmz+xvHhXVhKUtRwIJCAUGRKVOfgtiaQCkEZCsoI5iwEyAs9bEsIVJESRBigwZIJIiMEELA
wZAREEMIZIDsGfZe/u7WivZt335931+f3+8xf3Af7tw513XOva7rXOd8Pmvi7Ks3ROeHPq4V
0wvUgA10dz2nywj6HIksK+NGiEz2+HXXpnRMMKwpTM9b+oaYh2D/ctKeepUZsK6695JtuOb4
Imlsz7VT/9vufxZfSFpnwKBNV+tNpArz2eJMpOdIiBUApSWpUgBgiCEOiSa22J2pvNtYMdq2
ik6Qs+w4qUOozKUhdfc+k5PRcl7apBW9YeYW1/Uc/UQHtOG973Bq2tyaDFVZHmgpJz6o3FXc
fMFFeWHgtLG+ZLrvmVezAnmGBrj84Dm9VlOUqJkoKOIp8umGnt+FP059KCbzSnLZ2SrzI0RF
z7OvfWaiYFlcoEj9SNk/ScQlQs7N6fWW9vDIwzhZoW+4DZhxslvErUAsm9XkQ9GymdLB618H
drwozwusvhs2npeR18cjZq5NdFS9rIsf/HV24llJOb5TIcOIlVxOLeppo6RoaFqMtR5Xa7QM
ST9P8ZRuXQ2yJ5xOjxBBrJE4wDWpC2kQ6z8+ORthzOjIZnTTXSBI5bi3QvcpmrKTR97PK02P
OQq47ppxThrtRaxlBPqXQSirttjCw0wydyVEe4teGUzglPFLnfnuoNV674Sl0pMOjxrN4bOX
B1xfUkyoPAqQKn3hf/XuX/z/ySPAn4yctFTDKhWlB35xFrUZwral4kzXQKxIjXcsl0c9v80I
Gz/T0TPQTqr8+Vlzy8wQAENV6asSX9Gmfej2lxtNb8pPao1rp3/3+PgkOXRXmJ20+2YPQ/6j
mmIdEjrMC5vVK/zs6cbBn6WwGzSCI1pnBxhUji3ZUwKN55MTzKE0UDPjKHQEnYRVmRhHCqsE
6bwepub6JziQWxcfnX9VAGNrDAic7YshoiazQcjFq6ofnLDFVcQwahEycoQ6e6UhUkXb5Zua
LqwnkJrja3xPb5GAPfRXqXx/CFb/J/OZt90f3OJ/prXfMcGhi+gp20/PILYXIDACLRd6ojPJ
WkywOG7N5W/9cdb/tcb4jG4p0jYibk6d03FyKSXSfRDmRFKQ5oWuxaUHuyziT19fue7UqmtM
z4WDHcacmliFxzwvsUU5KjQElUxdHCGe1lgTn1/Tc6LC12pdDFuQNp12j6ydmNx6+4KYxO40
nIc8jeLeFbf1xu8XzheKI/0AHSnWJTA4UVYeBXPee+61QTM+3DbCfuCtEBkYXp7WMtzN0dXZ
vk1HuLrShoX0hSUeO0e1qfUm0vaVCFia443MEzvffMJ1+Mk30s2Ic0GgxKifZZW6e6pCz+ml
7a8AQkEn3X+oobtOqLXuVh5C5XELKkpJFEWAILkoQ1NHeb6nerQVKIG+bV6/I+BDX6QXA9NN
J9NxeQuPLnQIXO6WH4UDub4MzYCJnxmYhQFSisk+HZG4eLxK3ITYYHRk9IdffobS7m2j3+a5
MpfsX2mVozr3YmnsnayRSDJrX+hdg4gMncGe7XEtx0wL3aNRE/5MUzOeoEsPApQp6hwvGCUY
O8VX/HA254PV7Nrrmnbi+jdhfFfhUnKGHYDLoOuWM1Ntm9NKbCD14+P+6iH0v8ybMu9TvqEx
u1KheaxOhTMtwxPjNQlQJUHV9cP/KEjy7tMjNOpRL8OU8dVdd1cz+CiT75lXEKQilo0HpxKi
MdGCdg2Zp13fph9YY9HSn5BurFQb7pNG088wsGicCR8H9XiCmLJjdi5aq367hbauzpZw57wM
k69Ij/cwEpYfMix/oInJEHLyjdd0RhYFVnB33tju98gC0guBe6X0BK1KQYLV3LRsP3/5xDww
MEVNt5355ik+B4dICHqp82VsbFKLDH7T8gfv/m+lT03dESpc7X7DbQ39oVfEqD0uXse4ONJg
BTE5zkNTTDcf1Vf3PHNM2/G6JClFFFNQmMe0jNJi7S/VXjaqaGUBiFtvNtrfvG35saCBI2dw
oNCKqvmGPStQsqLI0MWZN3xkoyLQNqsX7olIwh0dm38y+DbEnZdwp5i/3bI1h6xUDgGPhf26
1Lz5o4tmQ+1nJIhGsKX8L7kLyF/BVAxCd68KXK1og7N2aF9pvqwvSnHw5a7+1wYw+1dUjZbg
c7Y9WIokhTiCVFQApo1vhXJRq2lFtVW7mzcM3n7OsRXmtawTmR+ZQ+gUUeNhB4A1ZzwUV/rF
zuHr2RYPm+X2eKVbO++bG8FoN5qHZD8jXAa4ufgh7l1pwk9Pbeh5L/zxljKEw08mvWGLn9R6
I7VTR2dq6WFZiYXIngzkloFICO5HO18LAsO/H84h8JvY8u6DKiQuWvfe/oaW51GrVgGRUlCT
0BrhoPeq/2+3X3SP+pf5a+gpvxCkOte7K0H4utrngpAzjHLQuTujuPhAr6UL+3pfxNIKwoyn
NK3r81vZC51LBQlXA7A0SBhDys+NGFUXgHcHggxbhOvDc2GjNOs7FuKC1ZvetS+rOspML3Fw
YKmRKgqkHYeshZwqu/+up92N9QVX46IMFEvxTUZlZB4xQpwJQmKWDkmvBhyLQSaUL/u9FbLi
aYB5Gd8GXoY7zoxZnDEiLU2ZlNkDT6vflfy90Z+WaCqkXHFkSGfBTgRpy6ab2vmeb9F8rEKI
SKO5lSmahH9xcvjb/M4WKqdjUbInXLpTOO9qAGpZ+eYBdu9C++y1sOiNLmxVCya2TPTMaBYH
4xS6a5s79Np6BlnOxemY3t9zgiq+L07Xn1A++HVTgRMEnIcjXATVstzbCdW/YTq4fJJNG839
twmbRPhwXdP+KVwMTbOZ+z1XKvhXzDEIwJn+qlew+VQZChbCOZjml/098PJvkT46khm1zqtE
qi5OXtLbMEUtRsuh4szVBktJ7UfnKs4p7Lo0inxkN6frLjxxLbLhsbxJFiLRx2Zg8JhOv6i2
94FvrRrxEUQiPdG9si7SvXdrV/SGpvfCv8mFJUNZ6Xukie5F7Cday8QFT1ZowYL8Jg+9ibo2
z60no7qjZOETK/rVSUd6ei+1EKwJjPjHivOHL4V4DN4mqiMmuie6syuzi8I2HVmTLhgqqLeI
4CiSlw40/EC1C53guMtJ4nSLBwjG7ZpF79v8v92aKv06A9KNu6fRfrt5mGN8I51kJ8s6iRHn
ZAvetO6Uw7iKvBhGNcSIaJKtLH4pnXvEZ5lpDGDHkA1UMW6H4EyWm8HK02cwqbNNPOkm4esP
OdNU7B3wI1CYMVFQ34N178VEw1Svx7hbPK9lTnnFH+11wDPKgMsvLTZ26dDBN++6XbTaMQ6d
jzpqaMuzPTEopSDlOVKQGKbUfMYspLgF6s6fTrVqFz3Zkn+F00YtaG7L7wX7U+aTIi+nZ8pO
wecaFucVmsdALWETvgGHxRCf4olPTs6bJroRPbBZ5SBEmnBFeAIr8KfVZb+Vc63wEF/vlXTV
b6maAxMB/aTFjAp9kmDqY4T7TeIyAUFlaiPlMm25lJmlfcsDasHz82qsGxANzbdC5+y4wnZB
T1jG3gEGL0YhLul3j8NH2osbm0OTOJlgm9pqcND8gsGWo6c+xZr/2mO2Ss6h+JLF6wGas+nB
i0SuIwr0etwcyJeQ6EcsncBHHgdlH1uBzje+MRHR+Qm0QMfD1BQsaEY0JLlNhqiCu4PZ9r5m
Rkhod8CIElWFU546ZW2dXYlaBufpMgSX++1rcMUh+8RaxGBWqdUVh313ZA/OMqiJhGqX1suX
quvQ02eXNh2/8CcP/Qom/f832vo1ONmxTPfYSWwNWtRkUfWX4TDz0FnL+Mb+pcrRDPriLRvn
H1XW3YsinUNEEVCSgttklzSNBUJMQcLSzzONV5twNs0Vu+F9M7BL453Q0nN4d/uECrXuh318
fISYW42ZFPmtUALlvM7Z343fd50VGNjO5d2Gj+2cVmQInuEeeoesEScZwWFPWMu5aF96OSrj
17C911BwCRC275ypjOPwVl8yNfKbC01adI9ZyS4Mixmvboac+pM7/7zjU9eIN+Xf6DpSHJYK
gVjpPBoO95sK7aX4BPnw1y13h0d/vDRjbuLovLPJfDNCcoAYm156oMTPm9QRH3B8AkAfKm1d
jc4JOz4aKn1XpWwAk4JQSVQI8+htzx6B2cXFIReR6mc1eX/u4+e0x2ew+cZKucVgc6wDIhGi
e0JzQVbxqmcHWs2DcdO4SwKxsuVCuk5ee6FZgs2iFwVkBTBoi8rcl7uwYeMLlzzsWt6Bn/nP
sp3IyiTnNq08Y14ExKaPmfyuPuOi/sGhk5JaIsfg8T2GP8E9Eq9CUZEVjP3B7MGFJ2rXrE5t
qHov/MvXYecoCSvYqUL0UG5vFwWBlhVYVCbH+CTutgT7B9zDqfr8McWExZ9fnfj2H008Yldi
jinXuvxyoNC3c8p6BhVbBHPwwMwsql22ym6xsaSBS9O2ObLuIvi88qFxsCLRTQ0GUz3XMtZo
ifW+Bw3I7hS4QICkkNzXuCuXxtURCHgwUZnY1PWCpQ1KS5vgoK2cC0Drw5HtSqW/m3qmyzGP
j455LnJwTD97ds09wJU1hBYcn4IW23GbHkjkn6FnJ9+fzsrxWbIdRg/cRXh69LJEB9Mlx3p7
qyzpAYyJ2/s733vt77af+l4S2hO+tEBBxfAWp/b+wFSOP/ZmfLcRlF2wDGsMDwfu+8uuflck
zIJ4+PTblmHQ2DQc/LDcqY2GnzeRV9za6HUAWgovq9qWy56lW/DWwBCney5vhRRtamt2qb6a
CHCp4xie75gzrc4z+PF1sYpSJeFRur3kyMr5ovDHO4w2lH2WgvTilcq3QjsizmqtrunzLnW0
ldbq36sK7XkU2qa4FozqtFABVjs/qt39YnrUPZdT3EBoaCHkTFMd25rAGgKmz3Z1DO7OnMlv
xRr1BVR3vn5Gg6aZPa1LBauStmwQdKEbAEfOVCYbLd46+yE4+95jfwQQ6c2RGAnQD5vOcxbV
EM0aFg9dKwvyCWrmRl/K/idzLfy76D7SjMYEVrWOwFqbbbMsn5Y0c4jN/vmeD88D4L6Acvii
J/UJgpd8qR6lyuF5+fmo7I6llUO/UKv59geYWPJRnyWpXJrEuOCcJCNoWbHGaPmRPRBuh0Zf
xpnySckZtXkz5avMxCyBCWbO3NeM94im3WK0TpHsC7+AOfXOdGDUDltIDF293D3+PN7zGR5G
4uQnVKZXY1Ih1Oyu2OeEqLLos9stjTJsa/te3Agzqx8gTs9Ci+OI7s0aGZEDzhpT1pEKnbHC
ptHv9P3t308Oh2zerl8oqC8yDkbqPDRage9R/a41F0CBizujm95bcwtM+YJyhN7/PCKVNsbu
pZBhfN0fCfnEhPa2cdP1RQmvjT5oNORktucjA+yrwepxaSS574qJSLTlFUPSSQAQ6+VxJbzi
UJZYwj3zDmvNHhZiwDhXdAxRVZ8QuHhp84WnG1o+Q2HTIEB+XdPJXc6sTLWx9gS/oGMCgAQ0
nSHsQOTZrV8EPW8ZHy2f8hshjrEiO2XCMoOXs5vfTHp3aIIBSPPvtMwrj++J/mD2Vlug2oPM
9LmOlaDNSJJIzg10XwAl7jmB7yoOCTA+Kfz9LP61mnd58lgjN6gKQvKELt1V4hI1J+wnpu3R
t/aHfVD1u/T/2dqxZANGwERdmu6t3sOOSwbfzNP0grKn4JChm7HVVMnKGvCXX4QMHyEMWzPU
fykvDsGrXcnAkEannF2nIsrvGEFQuId9bNnZl8ebf2wNDI4wV7VtfaLysoFBdzljxqmI768f
wRKBQmwMZmthkBHnrj/CVQLJCOxsyyZ6Y8GlgiGSJGu0eGmtvSELqNB49bvxV0WItEKFwJn8
8sdkZ0J5BD2O4K3HFBvCHxd0kpX4CZTxawGLPkX+JdtFSkqqnme/QFO0nGTkW1E27u341gji
IYlDf3LoX+z4xHVloa898yxSUQcwdBIpVG7PTUFyAlx1mXRnpjDcasraufL2VxF18Dwfh36l
f++/A43PpRQWlX+XtkzaN2uftgR7eezURtNqbA0aUgkZsFTFJ90AHlwVzW1+j5DAbJ/Ae04D
y/qS07Yazobz7mip+z0aRsLNtOFqhbnDJXhPIPYGu4xYOeiQ3bO1P3pD32cobH4VeD3P+n5A
bjX/e18GNuvyyLwaj0BmghtKKWotGsZVi6Tsx/KULOEE6Rht/YHcgCrWmdQnM75WgRQsUIjR
4xg7MQZiOjf/fFrn0Ib5m6XLOsZVl5wi2rk/Rv3A1Pm3J/PXFLFkTLKZ1bS71fS1M9TdXAQi
X8npCPOoY7xyZckY1FpUjtyAfQLFJQEkihcqL2woey98bZAn9fN6GH9L3eKqa6P69ttTCEHP
HByZxRNwe8d30nBRD7vra8c8gBLx6Etd/+Rbz83XhlG72hzwXYXAsT5dag5V5pEO9c5kuqKN
q+2+WRQ4UsXGkVsDA75GSnlPP2NQRGfcSBL2HedXUGKqQyjnpix19k9YeqWy3jraw1tYdB69
uzneoKoKMe/5Vmhh+pr/shFMZX7iG3EfCEs7StsA9yPLe2LM2tShSiA7GP59du8tz/c+YBf+
EB/S0WorSGdBcrvhcPVQ2bVyl6M7WOEaQ2swvSk53us9/376/ui/237qWpjQVvDcy9cCB3ap
SZ6ZRv+Jx3PlDtlcAisk2DQqCXd7f+DrUev8H/sCY4xtZ/nUBP0SbWvNwdhs6/pJ6ykrrdry
j6Dmt0vaGj0q9ym9OzzlSDezHY2b904THGIPZjeBBVebkSL+2mkJ+/dh2xCJYRjcL3SUmILU
i3mkwZYLj//OkP/679yibPLgQfCzelfhnaYd9Bze68ewRktvUnVOL8vZRKZMNW7B4LpY2UGv
O+Ojhq684A6crI56wg1oH3NAgCgvGyUorf/Ea67a8REpzZdWLHZgS/6v9eA2kE5E542Hw6nm
xUA9OLlL0WazZ6lYiU9H+Jfd481UTe0hR7vvmFDMbGNHVTEctRp0jfonj/2x/MNpbmuxWWYm
j2QFz2zR10Hb1domwD0Fjf/sotlmg7D28XN64UIdB348xgAqzcezdb6Jp4UI3Lu7CBVTY1WQ
ZHjE+tMX/Nx0lHvQvU72xHCLhL9cvB7WiMaCiGqiE91qINq1LAQ1Jiypc6z58W5V4aoI45Lb
V8igUusHSMycRcyMi0eESQubfBnIgJ3e8vWp3wzf9MZ3jR1ToKPY1yWd+DJLzNd7PzZvObsF
TJP0odk0V5te2xnmKLhC72jqfNmQrpHsblqcC11KtTMawHq/oJtJrBT2kzuWThvf/5Mb/2LH
pw8fdZb5MK694dfdTWPp/rpa/LrkbGs7X7OTesVOABDIOblDqpmJtJ/mC+st4Bgkw+I6bW73
LpeoNoj7AYXKjkuQ6S36TzfaF6Yvs2NiMs5OnzghaFI3TqhBQxA43SthwTlU0ArTt2gFeEhs
HPw5Cpvk6N5z9ZOhl7nSR+5hKC65dA1Cv6gJsaM45q5N1UqyEwcXeUhGPW5Z5hHcBUnumTY+
wPlpmhqn3YiYciy4kQgxXjWzG11cufbtR06rCF91oVfBw0Nirj4AOb1ksCdnDYwbwaPnF4H4
bFPXhStiUJakmpUHHyB4B1mDUFainE3zf/LeH8eJ/0HYiK1ngp/z9TCoiRsolYTbTRapD6AO
D+sNlno6nUd1hnBJfqSlw5KkNBJrLBPDo/hN6Dc6MHictvwymmmEBAnpu6SfzZ92uHHrAsAe
1C786uBRjqRexAuZXx4X4N2auK/8tBIiBssX/aeGimUGO+9LnHpnqcZgjs70+sVQzR5ygTgD
cnkIp4FPA5L4zF0oMZpTZ0wbV5IPoTPjHPUHfqmhvxWq9EB1tOgw6OregrdC+zGpZvXQxdzn
ZJOyW6ALf3LdX+34xPUwoWeRBSsB45R6HeNcuIeC7zjf4Acqt4NAst/Hz+59md0X7bgei/q5
zW5nSGqRfB+Yr+nXMwIBwAHE+3pD9XBJ/ipLm458aH+La8XDZRiD0nzsK5UXhAGT23XM4F26
yhMghp3Wqk+qHZDn0QR2iYIfFpvKgiK08+S2n68mqhTiEn0U+VZDWB+CStzSYZmnHxR+fpKo
NVvOhdrbLdxenKJhDvMxXkvDaTXPykgScajZIXTk6ZQI5aAD+iaH0zV1Elx2YZvgeThkOQJL
vLnS5hb5nCEndeFy+wez2S/OTvqSH7Qdc3e8lyBdK71mrWGJo8fPVcpYT5gBF1j0xxCr73/2
xxAHF7cyk8xkpqJSLGNKkh+0cEeDUEHrpy5R/smh3um752VY7n4zcckP7Mkq+VdgeZrf00SX
OaRpTERFrTpm8RmjtWxOkF8SCntDdjZ6UoLcNRlwwkOhWBMln45QFay1bbOeeqrheNXAUSzc
vzKGdgyA4a1mL9imEFx/LSiBrzuTgk1XMoi3rrz53czjBo/I4y9fhdowEeNqHO8MBu344+lv
MDMsNJSxGpe2QLYvnL6WOJRQpPG41KjKeQUUZepz4E5NstPCmoesmq73Sijr2tmn7332d9tP
HvMJH50zen3M52DSlGKnNk4VKZmoqa7AIXQ+TIAEh9uYBew2Ggp85FBAXaTdB1iIA/20rtR7
z3uk657IwSz5MqevOXzoxdbDwZgWteF77d4OiSRNS0YE5mpqQEUnlGydcteTOdZoDUUX7XDp
V3Ik+QdQnzu7jJt20VGXh2Y7aZqdPrQzR8rUQSsV+tBtHR9Ufn7Spp0ZXnOjWLTWAeS3WSo+
BQ/GGs+mO6+2TTg3NJBzFwbQCkC9mVSKmnAbp1/33w6X0zV9qoFJa9kQFgW8iWrxaxG93Ckn
Uumx4xu26y8t3SlaPXhzNR6ffr6NRHdqLgBraJpAN+W/FQKv6i9YGhlq51uTffnUHKh+Imd0
hmEHu3DZdcqS1oM/fGDrhp4N4Y8vrv9gcrz0UmBDCjLBaXlqC+jVCKE8wzywR9Agy75bAK/Z
61tYfHwnjWTRl2U/qGT/Cmat4Qv1CrNAmyJmzDTR+52zeOvx2w4wfc1qeAfHJ2nbVVjaLT4m
mvrKaROiLsbCZstKPUQWkKOrI/q7YaImbDGEdaBtt3FNAUZDb3GZnJeKFhtIo9oakbQbUZnn
5BW6cvbbv66FnmH3ZV1ypcbodegL1s7ZVkqYe+fXYhAJkFUEzCENWE5V2/DV3wmffJNtyxiU
A1FI07ia3eeKQvCJqY8uVSHWggH8De+VoFPyTPxAtl44Ey5jTGKC968o6MRmVWJJtz26IWIT
1RquDYew76MzAJeRmLN/kaqO7t4vKNqSleDG521+6naiy1ztHrYpaGVhFFhbVi9zHqVod54N
CR25iamMssyw3EzFzDAl53ajlSyr4bBaevt+27+z67/9uy2u44Qy1lpLs9SXgl5naqrFEYEu
qIYCCiFgKFfRYNthoA6ubclSl3JixyQXq6PD43I8Op/jv6l9PTl20YFgJGpWJh/v3kfYNBT9
3tTNnBnN/EuCSKeQ7NJJsll5hq6Hj73enGUB4p5qofkEbfPX+vpeksGZvnCorlc88VUJ4WGO
I2YNBnEqQHf1vSQCTKvfvNf1YfvHhCrV/xw25aZ85E6ft0IICzxHsTirer+k7nZJJde42erz
BbmsuwFRAYTc7SmtW4Ls+av9U+62ha7x6dJzDk7N8+2IvB6WnHh72rb+oV7KVHEm/In2AQBJ
clbmYc6IpIf7kA9x3NiwMSow2Sb8wr1D70zbtG3NlZJkPDgodcysoKu2qGQAk8WfkKmILKVi
BubXkSdugTzVUSYKMatC3RV1jRTw/jDF1tePn+DTBLIuNx39EZH6q9ZT13o+OOpvpE9e6dq7
K9JLEulSy3N0lY8ltxU86H9jB1pWIQiwOWlLKlslZonsAC04ssT4CLYn3aFGPe9qVPmy1xIu
ck5jHuG1dTF6oxNfjI164t1d+1fc4frDaJsLE9LH81gAkqDr8zpyzpL/0NKm0Vkn1nQh1ZHn
AAdzSFngzo47Uz0R4o75e0Uqd0chIYFrrzQnN/R9hoIwva3c0G7EAGxjFrqYfv2myzHiRIxt
QdeYd6HckUPtph9Mcve04jegoAFW1WrnZA3Yydnu3hm0+SVeecM+VuT8nPXUlm1hX8MS7MN/
6PGYwRrwXxftNlLH0okBTxT7amv1glaj7354um2o/SPJhF3Ev5QJmbiDJDMNUTmNIO8ZVCDe
Yfwfhc3f8rwLhZbzHIt4QXsybiapBVY9ZgXECLDYox3Evua6s4eyH8I769gnee0dtnkA2faV
CLsf6iaWOQqb14ieC+fanl0IGSx95Cui478d0cOLHxtFZdu2wlhiA8T0DiQcyF3dYrIsKygP
z5urdu76FZ/SI4XgXQQBrqpLnfRf8Sm/AlBu+n63X1swsBM+9VYox3jw1QnSJJOql+wL5ZL5
zivtWSdu7gJGlSUC5qH2M79xfbjJyxuYmj/e+xde3HDnhvCp2RZCwvTVJ6Z+gTnGza9gTBvr
rKmv6IWiY1XOdfnbm6ec/kAguyma7zU50TedS8nnZNH10ic2z3XM5947uGywlhq0en+y7MhA
S2A0bcIiviKyZiKdKdtqdwMtukD9vDErjNVZbyjOESsh3hjhShlt/6HWpb7umx7W/QOB2gcB
2MlyRpB3B6Ta2pgHAVlWCrV/9Hq4KHVejXkgKqVh2RKg2tuBVMc8XKosmqa6RC0DNMA5AI7p
oNgF/3NhzZEcQkG2t78g6l/ttICo3cDw+UMB6sYp3XpkDjfHHsJtmjTZzdgW2qo0HB5AWtmB
Xz9ctPvWP0gssbluppDczi3P8kf98JKsjB9/1frYDeCEvMJCg8KDnWO32s9G44OSdKd2xe6X
zGp1dI/B/mTWUDhECQjQIGb341kTt/bJ7rg2FFdytMcvJe5AU7q/VDC4NvEhC0CdZCYkSimj
4wNVlk4ffvrOtCGf5SZJ3qtitRc5vIQQrMuRMe5c43w8jIv3IXr2EE5vMjKYdSIrBTIfawaP
qDZTpcnwbgYdYrTiWoCOUkwvRrlmM32bBY1bLvyw4au/Ez55NAcwffuX5XYrWYHr8kZ05fl0
ufjkUo/cGTMdn1bvxuw+fKnwszcbLW3ZW1bgNQsNT4HzOLkT+meyHgxYG7c2wUgmAbPXDy4f
8JEiPeuVBDBqDVMTymQvE41wEv7pZnVLatythOgNLZ+fYJjHyuG2zFcUkPhE5aztWxQUc3Fu
31Ag1iZeX+q+bt687mlYbkCH8lhnZOhua8PL2MjLl63E5iFMuX1K75+DgNVnah3pLZ5i/+bp
dATbccZJpU+Cv/eeH66umQ62rD55e/V+fpmugLQsp7zfoXjCEC7DzYFKlndNBdnX1gjmz8+t
3m+69Wff/fHtYntv3YW8YKkOGaUaDWhlqKDjM2Rj0cVf7k77B++eLaLLpFHJooqzyBo1pKHE
CMbhjEyliTc264cChPsYzGb31uFeaJ5C6rjvQkQQywM25hC0eiV2BkEN3Gs1Id5MkQBjFt/s
E99RP7RUovwq1KiQWBu5khIIdbi3sN6m5rZUOVIZtL/8nam79jRHTtW0l2dOeTrWE93uJVKS
H1hryEYpZ3BF0F2XfvyCN5RbOK1tcWHhpzkiQ7vHy+DHckvxZa+X9fWFfQMmQ2Ou0aA3f/ba
X+z55KC30BfCI6n4rtcn3/Rs494Jz8j4vjM13S2SjGEW5BDz+d9Q5b5UQnuPIpDqrBaKrJG/
c56dZS2DYhOmmF4yTFbqy5F9vNH8UXMjlPWB0ABUNV1BPZZ4M6IglVhlyeo2vfwr/IDyrTPN
ZkZsFHhALgS2k8y00KEUkS+HeITPddXUF7yJXe9ZG168qnl/Q93nJ+yyZGQW23b2IxPC6OWY
AkRNfZsb4yXOSJf4ggamooE6hkNx4zeXtaXv6jhkRjRErF8a460SVQQDhLIn/kdXKw4URzwG
v/xgd2xTqWNSje1Kt0sLoQ8s0D3bWqwyPDEYH+BrTwGtBsbZvdzdNpxFeYLoOhx+4kUjXpme
mpCRY+nrcfPmakLb4IL+kLBF9Ad1v0v/X0UZtkbO5bBIVf1on2HbfIYE9ABX0gevNHcOMVmo
6BbRLM4FFgj2kRrWGtJ9H1COO+L2Fu93yByteq1CatF2wM6WqaAL6mjzz6IvtEsRdFKSs6YN
Xhjsty2X8uW0Tq+ggpxbp0kAGZ7K/f1n3hm2W2p0f/mEoOLHRzCeN8ETAb+5R39N0857WieH
nqptijIiuzugx6/66n89Vn+81LWq4usQgk9b8Cr4QNGy/PGpgYn0rjkkrjP6u/N/ctlf7fg/
uMUsRk8/PLNX20HyFzMMIePcpTd84m/hNwwG7l5JEWeaNwilqlsGO2iTbRZPZ4A7aCaNFolu
ZQOoRrbPV/yylWZKD/70hyrwTYPjMmLbA72kM7ksNTOemp3IvIiZmEwPyc4LC6xk9uRu3Rog
lu8xaZ3JTyTAoeSLXZT8yzCjMwxNI7pVshlPH8biMkWTnakLw3Hzmx5/KKT4KzP/u/dtES0j
+u5ytP45rzdmpMv6MtyQrmteDQCZUCH2iAknvFHF/BWXXyuJ1YMMOMGsjOrEuaidOQRWhup3
1S/TZiDaFmbcWdOVzN2hOHL0928+GAvgXkjPG+czmnRwHqVE+l6v4XYpNyCB2e5JgIHlwq/k
wzuAqOu/KktOQrstrt51f9n3Zowu2WRWmUvfZ1v+IOJurJThB23vpS8ftqXLkpxaBQ30cnaJ
7B4ro+z25mZ03fybfakV813HHSSfce3DzZnIJp36VsH5Oi5F2xUS3kg37ZhyIEn7rKnOSZd3
ypn8FHH/HPsfDLmL+rIVHOsKs/yiYNz8ZbljSo5NNMsoNidLJCFw2qV0l2v6CCyrJWrLC1E4
XVA+MhU1qkrJcVqKRG42rhLt3HNr6QRTMHzv4WSUNEsDZPdk9l4cGjGuLaUY6dAndfud7aJm
7L3IxTlZ8SsHw4fRCu42bSem8O5FiyMF0OpA2cGUutiFEeEfZ/M6ZmEW35fAIeetE1NKnxSr
ucsrZjKdgFAJizjInfBgYNCBj0+8ee/Pv91+8pRqKyi4puVRO69cnifeIuuou93+BTnfw7sw
8Ksy9/6XpH5h16DKNvioIXpy4NHNOBpKRNtQnxDlCKafU1RjTjlOnjrx4ENHfNaa216zSnc0
G0+0lQho7RJdbQUUAjrFtTmE3AfeD+FnN89q9YeGuZnMRdBlrhqmi4V4G/6r4wAqckibEQbv
ez0VfEWfYADqeFkM5hhULSu9cAq9Oh79oYHPTfri2WhE1f4azr0T3ZD4PJb0T1nppQFZ1TPz
a5bwdEklSrEd8YnhW6HlylvH5M6q3TA4d/ugcy0iX4IxnD8iXYXMLmqB8226mZb0rq+IWaPP
0i9sOGCLa2TWSYouzij8bPEDq5O65BGHyFQPvlgnlO6z/YCsF/DCNa2t2BOttaqqDxfWyUgE
WXtKMiRhVSigZtDUvE5obEPVhrD53z2+m0NO1oTNNtyDdJdcLfNpIUMChennRNKLz0+BwDZV
zbhndj/hJMRmikPcyy29hHfMFdTUvnhTuUdD46hjgVtNDx3OIgVVa1mZ6aWaAgiJWHngc0gC
WJ/95wDXvlxpm/Dn1vew98zfBKjjNeF9I9aWxftPasKVeucOr0bPnMS+VuZEHDmJ4rIgxob8
ujP5osaYbPm23OT1FDkv0fY9aUt+r9Vh6y56zvc7J/q1+Bi8m10Xs4dy3QOz4rcr/p0/vjg6
Mlc+Np7kPzPraNNo0QKEaxOdVsQgQWzMwGKhG5AUDbp7zFFTISZcuLutqpGADSiSyXv45nKI
exF4JaRtmGZE5/QAyNB+pzb8+3fCp4JDA1iSUo4RNHela04m/FQrMRSYDxlu/TVk09fjTLUJ
D0ywfLmTlKX+po5FtWIVPUpP1sD7Hh1zFF8DE6cKfKNEBE890z50JJ5MMVQSrA+GBz6vxivQ
13JzO7GD1ZozHXpB1cZxaJ2gxjXf7Pbd14bVqod6LFX2HbA2UCGVZe+d27UsM6EcoEJ+5JDd
0GvHbcd/Q9PxngDAX5uLdjM/6P/spC9VWXJxEH/3e/So71rKT5boJBkrvn4xp4tKdab5VAes
yWTNzfYBDGAcg+YwhY6ZzVcW5V6QnBTeDNR3J5blsW3bXz0uamCrMbsJglGEN0HQ1MVlS0Am
WnfyPrjCp+vqmx7dH1WRR5m2HjrUmig1bmVChbYDO95z1K0rKn7T4+gPB29Im3X1+VHfrR9c
PVK5qHaK/E8iCPw7stAhsXz8StEjqEpchsll70XWSspJ+7uR/e3bzrVaGs/H1CG/WVHpJ+ZB
7haPDfLx4Z0H7mg1Snso8SdS7bhbETx6gEAyj23Uw5DdadgZOwV2ReQKv0b5bM5QhXs7OIvP
Z+/dWWNoXizuGB91yOjQO5t82DV73wrts/hFfyAhhz/dziXFtcI4cAfMTHdNhJ4tQdFkTstq
UPi5v6goR6HolMmpDVf8nfDpN9JFXztYvqdfgDdxhP3NFKSkWHDMhmJiDbHzlKqsSwXo0Otm
DXjABAMnqRMc6aOPyHoIRayuY5+oXXLMZ4yfUZP75vDih57YqwfpqbrKLXl1HdR7Xkscz4uy
vLcmqxwfHpjjDpEasxKzw+KUIZVHNOd0VWY3Ky+b+ddk7g9UdRWZc8o/kjWlumvAsxms1WKR
5V6N/IpI8KzMVFzDuhk0spPPKol/aOZzk8RxkiEJD/zQPxlkxy0LNF1E2K8Dis+V4HMIJCYQ
ZwETPTwUqp2txK0HZxg/fKHeJ3bBx+llIJVSTG92ZvzLLxiUOJffZ+mFHS1ANpgFm+PdysvG
rG1QdofFPkKT0Hdoy0XjvTqW25ytwIkmkuOQ3+CZTFma06cOKRGS7iIDZxpexM94UVP6ngSr
nVmrrwhzI4VFgut9iFGD8mgTCpC9//QvXCtKbRtdtpwc7FZ7K/QMug3Z8qItIWWSZrXSdPz/
7WR967Y5a1b+iNPkRKNjMZJCcB/edyei3hNcQzOpoJ0/Vmtv6OOgiG5Yf1UsCvLiiDyEf4Nu
Y3Y/pciFrpxKLA8/ePMed594C5CoR+aLm9Zm13JfmMiFCDOnRIG3O97w6dpv1mzqnshjXS3Q
OdPduZxX7/Wcy7F1IaVAXOJh5wshnIFIlcNfmjHlfDx8K5AIY/hlYiFsWBsqPR7MTQ0hxlES
kHU8DA60jKcZR8FR1yJP/YWH/mKXz3DpOsYidyXUdTXqUPvRvzji3a5NaKPT8498ZUEheQ+a
o4YixAby098KFeVzG9YPiS60KASxYmoyv75CZnazSuh5lpUFXVLq/FJ01PKJyO+2Vn+k9pBq
jtL2uSY76tNWpOSr9DIX4eIMnzDYzQaNt0LbaZAu5QBsJPIF2PZJDrUbbzCfVQdak7oA9lR3
8np98t9v7rzuGUeDaVb5w7NOjTX43LRqBt6jE+DxEtUUd8H3a9hUheDlc2ZAm/uiP2rz8xKT
ZAvLQ4tLQhwpS1GvNb2XssqfeLOKUTYsEEMaruavk0vGgcwa0whEKHpNsm/L3ay9WwZ9/ND+
/mxIrQBToRnp6R0MEW+OsXxBJvqQMbO1aHk40wZIQ+tpPXv40gdfOBj7ajcPBKYmqY209oET
7sx75EMZ9QA6LWLgSANiQIk7xba8YGZyxkgk0RLLcLehuUGzz3ZgOsSdJpdyaC62R3KS1qsY
uurhVofST31QuyFthQeXraesnlw8FzXpcNX5H+Qk2ZR/16jTOvbgkv8u0LP8aqRJgNtQG0Ar
TcIzbsK7xF/tWmhj2iWUI9sdw1RmLsLkIIsR+WqYSHSP8avjtO+ra5t6JRueU6BplORAmAMx
bd7jUfhZUj8GSNgq3Peu+0Bp1Z056uOl4z1JeW7yJOoyWFpNq3F+Yj9b0MPmduLngsNPPYXH
rqgEyx73F4uF2BnL7IK7D4uaewl6GHUJyXaVotdtooIPpV3YcMffCp/+IvyBF8xh6zZvLb3+
JA+ixWPPl5AIVhrD8fluThQx2Ymw+19WvtYMZlJCGS2z8QTUeMRem9dZRSitjjlX3HrOjo9T
oy6ybVwcob216lTHu77D6zn8cIP0sk6c5NCUc2VcN9rWncktb47na/Hi3QxYzvHK6LPHZ7Jw
muJjgjViQFeZZrm07TQ579wpInWJq59HiyJwZkPLi9P9jQZyYkmyWDdFUnRa9N+a/V/85XZX
q9bjQYkmShDWibGei932+QryayM96Yg8AEkQEgwx9iLIK3p4tkf7dNeAe2nUhUH1iRk18AiA
TibwaIqhwJwJudl7QRS7a/z64RmGOBOu+pImOoQlv1Rix6CkTnX/9IK7qs9pn/E8yw2DG2Ni
wNaduRRoLF6FGIHNpoRlA2VX86etPnhot8XIXfJqVV9MlAMlRccXigwq3xUoxoFOQffNAaFu
eEKy8aCfW8y3iTsTyiqlKGoNYr01NS1+MGdsOFNKpYHcr2Eyazvgzo8+90HnB+k/OGBl11rj
M+paKfLVHEI/3TxJ03MwuzJMlV2uIbvgHbutZ9TSyY5hwSGY2D9+7A0wkULFlk7HocSaa43l
FmYABm2U76Le/Y7od30VnWjDha7W9jOhY43hw4XJpRQIjX2lqnZ4sbSdTSQrGuXQAqUjFqP9
Zm06ELOZrgtJi7QbOk+QIsOkr9ILLX3VEhMSfZ5pGDeaNSyJTlSfuvXmgw/+Tvr0GzScbab7
DTG+RxGLd3OLALA8nO45U5+RI+fVE3N4ONUHEwZcl37n8pmAWf7TlWDnj1f6hPbWxRKB3ykq
MTQORXdGhga1hRoNOLT1tmuiznHLxj1nwEUnplasRna1jQMkj9oyeHlMLU0rRKGZw7dFNTb7
gZSUnOqGeEw/XbMe46MdhXkO2QOR3c8oA3OKD+Fp0wXiC5iE4CpmANpwtb/ezbNawnTbxN9Z
/d/8negMqwurH+L9vDFSCAb+9hlVdw1LYkGLnUKmtBygk2wxjptbgGocRdY7juIrr1S0eBpW
pjXdoHMFymsZzzM26ErgKLISbletjlnGaKpnAmF1jT5lolJlurwS4/gOy49MN691yEO1OpUI
1Cp9FWF8lm5GQrGVGABSWBiT2hM336NKhQJXXHiQ9SvvF/21yHHpqYGEssxpupsqFhV6ztZv
KlxTDKhRQfShpg59xGb0oYX/6JvyWJBV5XKsAPYvzPTtgSmdPA9FI5xSugvIcsLg2khwWqVu
aBFTbWHN/PLwbNTtftbS0+qMhJl7gd0ApAeDa80NBCqqxQ8ci/6tt5vlwvi+DsEiRyd7Y263
GM2qVaaSWK4FXboKdSERize/wI3f39/NvHvZpf3e3claUH28x/ovBH7bKBGLCsllvKSl+FbS
JMnc7MrS3T9/MP/vpE+OjQpJL0z1lJWqtpoE+izfAIiTpcR6AxZiBd2FLhEnW8Nv253V+fKj
hja5L9X040wHsq/pU0QKFZt0KO5rU9yOBYC9ModLCMfFuymGZwAkmfkMEwOnRvN4rMfmgyc1
BnQR07qNtvDkSr8Tk0EHyyvTDLq+p8KhNHQfGQLWHSZkro2fJxMHDELKbSAIbPhc9Q9iww+g
HJfKhxdHyxR/QeOyoXrz01MnpshmDXZjPIIKvl/CHEuEEtzc3Bkax0XaP+riZyTuNLh50JZj
+GU3ubLaaCZ9JELO1w2SEqacNn13dNaxAK7opthfP4BVjkubgFgNos8esoR7G1qPHGG01gSv
FI0ceGFFUtVf02I06Msm+1BCklpExe0LxblZ1dxapxYxY9WMPh2hdpoSbJLr4ZW+xXN46joe
NnZAHyFsCNEGS8KsxJmduTMsmyokNrucpQl8TuwN+uC+TWJr/sXL6lCePKdtWqkajX40IpVn
5uKdkOpmBc9FL6sWiI2/PEF7mHl1ZtfPajGIAa0OOpHP0t5VoAG8Xj27CPEVBkGOv2b1Ho3+
oHVD+s/NOzfNOFuZSdgZx7tdkl4Oais4uTrl9zw9RRsywlthag5OaHl3aC+sDanbne/ADdIK
x2FqBhNUoZrEhYCMjBqZXVaCvuFnT7nSd7NaxAjdLhPzK9cv33/X7VMm1nkdmMpQXmf7eSSU
UZxlgbv/xrEYwEgGl/tYB/BMwzxZUsdC6dSxHZx2A8vtF684UwuCyuTvGVEfdA/rzdYW+Mgy
dHLRP8duL3+n8X/6++mrkEKHrIkDPIDX1TPEkxHEkB4XSQVuSYUh+eN559NwCGiBzVuhoB21
3eQeEnJyEDpen4P1dGw5HryfEKGh+8gqsGjtlsqpj7ojWsBC/Xwufca8srFrVxFWhSeteGxd
8kI7ZWb5pz1lbsqN2ZQW50IzI9KEzEixqFFvnZn2tpJhy2bzGe30uHoAcCK43vu1JryanpF7
ic1tpUqwjGZXUhvnp5EqmfO0tT2BWsg0cuz9I08/avPzETctQWyYwHmvMjUPxcyabhYpw8xk
2J1wMit4Hrl/xCr9hSD7Lqea5zJXU0xEEOOfeANoIzbVEMdi7lA5hN2ZQ057cFiBMKHk37B9
R7afr4x+QrhpJ0LQN2o0MtWES5QZqNmjORRHUJlyEgwDOLxhuRTT67+/Td456V9K9s7VnucH
GixfX3HFVlwQ7N5tUBRCq5byqUyJavkVbK2ruv2runoEn1p88mL3matRkv5PNBDw5BGAcjTs
GCsOTiswnkgiXg3+qxPwH7w5W9gnjM7hofudV0IPOlIMVlpB17aEOTMlZlgvvsH5nselmDNu
2a255xAz4QUDERIwGX33zmmq6NKmpHuv3vCqes6gk3Wg+KbI5x32CADDRV+FGxYEtlrj/8q4
2z4BGykp5tMejqbNmdkWH1TdHwQCMllum1mZHL7e8pvjIiEQLaY2RENUtNMjIlaYfu8rAtlN
/7qXdJsEWiKRVUVKv9NPKlr2V2bk6ws05Wa07ITaPy2PTUjo00e7m7bz3ac85dIfoZhyk3lZ
2c7o+HEzubQdgf2oE3nf3kn6apAtQ6xrL9szvDACVPCsvXJ68+60//ZXLtVawpRpY1pV6x03
f3pnBGhpZ9I2H2Rp73OwpFf3QGGKaO4Fd8clxpYT/c54+bTl3Y6pllATR7NAydUWSOmtuias
zOkr/q7fMxe31CQiSxaZY9WJe20baJ3BXHFzLKt+ZPkoURkNWhpnygzS/W1av5L/qPHPR1QQ
I7qaiMN4ztap4yIjmWp26q298DV32cF0EYYVJ8+4tZYgsFkn2eEBiBuZEWKlojjye5czx3wc
kqS0wp1eeSdq7izzvUI3UEmaSUkGAkFLZ8oUDVutNGTNKzOJPXBTUys48bnjx/7YlN9sfS9+
OrS/JziY1elNf8hFh2Uc+yptJRo3tvucdKSwjrAaAGyqjT3KJZg4grWqTMNviTz9WMPv8n9u
XqncdPhyWEwMKltHiZI76zRKXy+pDlzatN1IadK7YdDXyzVtQs8BALY1qrt3oO2t0M1tl9vg
PCvGnRS7OXBKNmvdDiN3S7IwM0MkiLO4ndTiRoSNHhTh6BKp3UuccW6BMzGrslADLLmykiKE
bfpBdw+dWV+5Ixh7gm7tjNL9riBsInIGMnq+yIHWxZ++bdfF3/YOdstR1hOZt35weriKLohJ
PWPskVwcrLpopzprnToSNlwwzccq9G79VxCqQ0fXXPc2/GACpBG2h5IzUuITC1D9UPsmexQj
ZAZu0gpFjVubH++o+wuf/tWuT889FfpXlwNdU0EOk5FNAufeDGegE6HYdWJ/+VgH2VgF7rh0
Wsnp9khbMflHvW8xQEpJOsoEVIVBEwvc0rXNq3UGNn2ECQtUE7WwtYwOBHp1cJH+3iFld+7m
9vKqGC/qi8Hck5Lq1lpseJnKhIQ1RFNDw9g7bqts4MTLM0P9JkHmEiEQ/SRLkROBXrS4u9D+
4MuwxlyyIj+dIh/uslfKqzjSszKy1c7YZI/dluNh4XPqr0sL3UFvKHLBCdKRi2hhxZS8LqJa
O9uTAZYkW2LV+i2xCi3gjhlz6IByzuFTf+Wi//J9wpvm9o0oXH9KN9C9trqfdaXfX0qnldMa
vEvbLAi2AjGnDN3LjVviRNmLSUAGJ5lf/yRjRBVhL+H5rf6+8SUBAj8uiEGcN2uYg/RTZJ21
kcTqssHmPnw+Kz/MsxmOmWJAODuqnj9/wfQb8+YgjtxzcnK06ShwY4ia0YB6p3gvQtqMNcjU
1BTIA9jU9LGv9oSHzuDz+pujRLV4+uWQgfGjzifi0CbNTLfqpC61P9CGf/jZf25KC7BR191T
/8J/7wkjHR1CHnLMb7y5b6vm7PXaBF7vGx5uMZGWy0MX4HFN2yzbCI0tDB02rRu3h3HjxuC8
ovsPrfKRbN/bB8sXYSfZJ+X7zeMXdY/aoR/CGg64nyCGz4G5aTqqxZYhyzirvgU0PD98f8rr
vbFpK5W3nZwfzhT1X4kINPmejCErEgUu1JF6dcS8vKdKmcI69HR69K/W7z4+0kt/JLAAByd+
RSWrj6/5gFquMIxWmeAuW0gXb/IiS07O95Kk3C/zdZWepj3ZotNHrXQCpov4Yl8N+mbGP2pB
zC1HDCcsMqc2Wz39VeH//Pn0KbLoObbcaeK9ii/hqPMssDa37fGxztgZa62mI4hhzEK4nYfR
sLAVUOUk8HFKHrvpEKAoEMipQp5WdpJnwC75lQhspCoybx7t8/gE7w/dCgpm7D3D4+gAKIgO
torZD0dC5noGLl7uIAhuJmgzf3sGxMXnpmHi4pKYX33hOsgmeFCfprWGUJ6uXmH4xNxmhJ5c
DmLYFWrtNNIGNS4Q59VMWEr0IGs5AjI2/WcgI0V+zfbEfJ/3PfmB61Z0zENrsF4ZfJqq7VSZ
wC2y8tU3nHPOoqQ31IYNC2T1iIo+94+kfM8KoiNB1W1F4HNSPzBnHrUkJ9xNCEsv8eWQDZjO
EkxNsE0jCPhUVV0v+YMtn8M/X3AHZ4giuBecYuNdAf1E+2a+ePX5sorBQoiuRhGxfApyz36m
mhe7Fhx1Gh7e0pNfLflCnLqnTwwR6E414dvFB4/oOekVYpx5j7hslZv06hSJRl6xB3VpYju6
Wsp3YXYxh+BRKc7d8ZRLQ/6Loy8pzOZKn1G/+8D7/KzbxYtunASE/1iLTC4+3p0hKio0e+pj
nwlXSBe1lC+n9DnQkA0drNIOIKgWviawI4coo8O+EcjObrkw+fHx7+X/4EAdRr1L0znp35O3
CMS0OvT7oxS3DW89HYTIqmXMQSLOsFqJa2uxq/epdN/5uXK4wmRlcBWktzUItKbvWW1Ec3fF
9yGS1vBR+Oxm0c5w/ppou8JIOVlRkHfD1+JlYtQWD9+dI/W1xZEsTpDAYly7HU9qC7fqG6XC
yzx4vKzB3AmImIYEBPST+SxnYNSs3zVh+UbeUnJATW1nSMnk3M0EWyjNVmJU0/l8h8tOZewo
AUNFxOcSDBZ9wVZiWtUnxGgUXXV+p7SibD8nbFy48MGIZM+8OkLYTGrMFR8hYeUspsWSnb3+
+ldHinqyd6FcKNl++TH7lrRCjyZw7lAwnnOdqkEdhWg7OmcctOVQ2PdXEg6cSzHadR7Prz82
LnC3bpuojugJt0K13gaZLsvDehzT5pUqoy7tv/P+3PwP208usBQSetr5hKur5BeQT4BfMRBn
GbgGX+zvYxtjNfLt6Wgj+grlyuakITRdo3DRpMpCthpiYRFHPeojgYwT9M345xZbei+PSa/U
0sb/VxADYCIBDmJoW4sB5BeKhkyhxEjE8g/eBwbGkeIn3aqetwR3EGhLXMvBKxehEsvh51NB
1fvYSs2yFigHoocBmMzs3a3SX5mh7hYqww812GX3emYmaPfBeMFIuoJL/FS2tMBaAgLBEgk+
VUCBR3grQyJkgJhDDNc+BbqrVv5m0gDrLMUq1+HNtjw6T+nXLFn/pbsg9+KyQSNnwvhHHthK
9kceyzxU0Kky8aXUhyqE/8Gr/yVfhxj0Rl5pkoaFC0ar9jCyYWu7wHjVuubmSjDJdqUZ6l6+
DCXmxnsTDFgQa1FRTQ2hGDIyLBueqeHY3B0jpD5ywP0yG4LQDMZgCnNGddbEwEbli+1zESDL
2+TMFpsWMWfqXp9k2TvYri+PXfR3x8DkVM9yWhePDad7jLF8NCFokFNdrACSIJvUGkq2G1ze
iQJfPMaxSHk4pO+iGPfLcGlZZMZVt5tXQCBHLU4h2iPeDavWYqYhzgQDE2NRGfwhmT84fFMr
K/io84FzjawZoEb7ykEURpcEMA62mGlCrKdNrwmVhQ0vHTQfpMRQsa2Q1Mj5ggxyv9PkAlrN
U0pBURXnM8tRXhzY9PjUX52cL3ijwWtKi4GTd94KvSneTPsHa39KnF6FcUKKJ6VcVl1DRMVa
GthI1JvMrAWe3yVPJ7UCF9vqbpeZOJwIhgR1cHZpbYKk6ypMfrd0SWrXw0zhhl4lBZvJhQhY
xDF/r2X13tai8nt7LL+6mSDB0nZsIIRLVNWGzNmAILIhOEMQaHP0gEmWTivbyLp0yYPv2jh+
afWt0MxJsgs1Sjj/l6S2gIqwuXwtiBHZrEsCYhqSxxR6ZqQaEJjCnIhYbcYNpFy83EX9lVsv
qHpNyTbeDX2wCpl/QFFeEevRT8XmTHBUCKe/Di8Jju9OWpxT5AxIfbt+sZiUecBVxy83X+Fs
pdN80hxzkJ7Y6dli/GNsLIbYf+gWuLK0ZF3QUqAr28Y+rp2oZMxzqW56WpelILtGnYWY1St6
E43ab4UdEhI69II0vlBYRn3e8OoKw7kkspMZhMpY/wluJzEAql04ebtqzdf3gphYw08v6S/g
Qn6DF/s78G0uMcWzPMMyr6SWEaz/0DRzijfVXLPr5l+d4r/Y93/w8HtiKPCb1ntYHyWuE6HH
DjjGpkyM6N2BIad49S8Ed93iUWEe8PN4A5TRyubj+pr+shkFjeTixydmhgoT6DqCkaP2OPDq
2PfDdF8K3Z2Vwl079RGqw7uenW/yoOq8idF2OJZbGkNZA5N7OQkhBxIs4mFQvQIxTfHQ7+IS
Smgsu2GkPDEyzMNQG0HcLBca26eJSbIoftlFC1vPeiQQqA8Sjy8kdQCDpQvzQMXtmuRIemmw
qXlmxQzc0Eo0wAO1eXG6oU03XKCiUUI5gZVg8AlWM7fHZU7wAZoiIqp5pC0S0WRq3lQbMh1s
atrIqH/wVdSziouLao3CifpdX5TeeAjfhRiKn9Z4xEsPTSvQ1JB1lC4lCMgzwGo2QR4VSnBv
ep/Y+xcO/2/c9aLCu+zepNxdYqBOG5tRXLVH4AYt1ndJTQH1XOTHYT1OPMGr4ONzsdA4inlS
HwhBxBosXpU40BBnyJnb25NknDACkIiNyKL+H+bePCzJde0bplwt127Qyqksta0rTU3L2Ryw
Vg6tclimSKloaWlO4Dwh2rDLKWW1GlRQKS1UUMwUERGpnHLOEFFBcJ4RZ1QUX9bzPO9x7OPZ
69nf2t/x7u/9+AvOG7iv+7qu+7rP6zx/5++XbZ70MzZYDMKs4cuEnyHQNPyA8Cou1ZNhOYMN
wuTd/zlLHaJbE/fRbLHmQdPge5PqnUpQ3dNAdWa6fc8CfdAn2NkzhhqNqluKr8mky3bKOuuN
Fhv8Heb/977blzpVlOC7uPJCVxt6QgD1QLMi1H6uBNWLtGD+0Q1EPVa3Ev4LFi5UoggBGY7p
5hpqNye1o2Dp2VXgx9XrxI4kbSA67uZN+QIuLJGRm/3d1/t/NCIZXSTvb0nJVn+BiQ78ol2f
qVzliXk8iOSEPcj7o6//edsBRIexZV09YMlAnqdsdi54x2/IVRhmCva5dXiuZ5nntvm50sYo
Op3i71JQvD5GLeEtNybc7+p6jzZbmJjYO0kJ9LPKsWzHzjLN4Yaey9mIIvaSuOpPdi8j8iIn
LKtBpLG4XJydp33jU19xTjYPjJsH+xF6Zlbi0/J3ARDA84uxcLpvcJdayHxeEa2a8LKmKrie
4yHh0lio2hRhL8CW7wvTG01NycbTZY7o6Z3/YUy8mur29yGcazbvDHmf1y+aouVQo3faN0CI
g9EVWYP4vroe13WKQgIIdGSMZC+xbxXB6HJy6lxbMU5CQR5nJY4PkbGTPQqreW6aaRZRNpZz
za08GQeZ6N5O1xieHP3Ur2Jlh6bFloT45yERB94knd/qTDyRZBwa8L8XU5ffF9OSVacXBarq
geQrP8pAFxyolCpPhxai0ZDVzW8RvCa25/xBlL5YegyYVky27jSyoxyVvgIIojcez7xj9nA2
HhoyWLkYkywT0DND6LAX0BHejka1dZwm014XAyDDAHjv+88VYtjvKZXXf3IY/yxRG0Aa/YrH
IYHQVS7iLZshw8GZo65BP3ooLvLE5snsCJYvw2j89vCiMAGcET8xaBGje4/hhY5iDlqsmJwn
dDrPb2/HUe8Hmzi4Mu3BNs4gI7vY7Pyl8//Ac5AIcjByMWSIx2vQByEDaIDeqXVf5re4L5O+
723IV4LiRVpT5jYt2NByNobp/ZnvIDPFNzCeHHIx4JQUH3nTJLp04dOELyRj7PX0IBb/+B3T
pMLEsZ0WP9FxjwfuZjjQpBwtmsRwBQc961iKTdTe2uEkcP2d2CCbPO1UU5T/0Sq086CGVbV8
oYOevbWLI+h3GZhOTiAlcCLCYPVit+7hKJ8Jg9T8y5LhQbX5Hxm6DIfiiho9jV4G2FCQU6TV
wYSi1LqVtSuDeqZXJXSMsasDrJWfSeXzCGaheFHmz8ah3KJKKXJwBgsXgHmh/Hd1m39yvP4v
fc30w4eK92GESb9x95YKv1RyNG9wNO0M1mLFyH6zQI31622Billx+KdPlOOKiQxmUeqJh2n+
rbd5rCpmstyGX8Aymc7pcDZQwobEuRfS8u/bYpTNHq04d0a/M5e+SMt6PY2itja1DAqvDw2W
T7mAY9PBBBeOyL7TYBCn1gAlDG3n7l0Ib+oRpMLXSx3oHbb4GN9p0DpZUffHnpgbrQU+CYyO
jTKflvyczWmyNzanIHXlIbjm8idd+VCVQI+BXI0BlNj/0MwmzPv2GMSoj9vBNBN5kDmqN8wk
rRYLj07hHTm8f/i/de2RmT5kqjPJdA9xIyAdbfxB8Gr4aXpfgZXb588kI3bqOsWbmmp12NRM
O5QTKbUPJnV64rZn5XMKaZ9ptC7Iyhwu/T0zULuIvTxw3LWbYkcGPDv1307wHx//jXtth6Vz
e428TkLLdAOWbP1S85As1lI/AdP2g9mMFc4W09X3tRFFSfhGX0u4gYRVH2JRaU2I1/ZTBhZa
RRlsADdXJ12eMD63pW6Te4yyKjvlrOwiTxZo0mxw9acuJ18FnncfsTOOTxTn8Xd+xvLZ2izo
vBdlnNeTY+QSIe+Xs8oEsZx9slcFX7LXL5nfB0gfiA+G5DQiqM+rBCLGN5J8RtYg7FZg7Is7
Nwg+cDr4YU32kvV6Ns5iSU9G5ugPk5PmheqMPqp4sb47hOlYd90WiD1fzv/2fIWgeCZKK5/p
I0jDFVhEz9y/VZ1TQ26bEdRTL1t16n5u/0Ke0P7YjtU3/I/F2uUIpy44v8eQbqLTwbBL7AHp
/+WHCVKp90EBqcSYeX5QeuVIKXOEtBK0F52j6LA1VRVDwOT/ved7/uAA18KdZabxXYyVonEX
8QFhest4qJsZ9mF1HqV/9q6zrzKlYnzB2cABMpnZM4g49Rj4gqIsWp6yC5oFKmq3DNYoZpJf
Ooh1GPSQbpZkZKDPugOKIryf//qPJsUf2P58ZBHwE/8m4fAuQN8z4Wss8UG6wzEPwZX0myA6
x6/ssmRDIBnfn5Ibv6RqSdvn9fVH2K/K+s7NItdo48kvnU8zPH7+nEHDbxA2rz3LSj4iLtxJ
JEzUEOPhQoXXx6X+oVl7m5fwv0Fvmu5Athf+Glp+DX+DZgBx70LLPMCAElUOgiFzBvacbKQ1
ZIk+iTTJPnauiZCyaegwv7Av7Lf0Z4PZRCy0DnZwKzHe30AxJ3UlXq13aQppsbn9KY2CeeYY
v5nImGW7a0jFuHo1EkL6+4y9gieGcDmrDGsf0AVZlwWmDRBpegJWbGexrdRZBA20ADEJbDqe
9wy7UGbWd3dT9I0XZzylamkFlll4KAjRrT4Jp5c3wrzk50NgipopKR+flh6gAzs6oyBUp1br
vdPTlmFVJ5h1JzBZFtvmzke2/L6fLBQTXfhPaTeTjqxfLFsy61/mQY5cYJ8bNUJRs4m+348n
VD6/YrlD6vN4wQsC5up42Ix+zyW6xqx5RT9DhncCt33HPcnLzqfqKObFMPUTo7iymZOJrI2X
dEtchk/6lqu18OVdFsleuGQAqEPbpbKNuetq2j5hB0Kg1wwm01G2Zcgc++1oPG6Pyz/0/f/f
DGcQvBbggdC+co1GZZ3gHXK0jx/aLJ+UkRFdz8EckhMXcwHHrR+diE1loJ+XZdi0x+vO9Amw
EPxzKF5R6nlElT0cCNb+wsJhotNwYmLto7FlfQ2pqCaT0NgLn/NkQgZR+ILcnSB1qp3qvZ2Q
SFaBjgfJuwAOmghYtxhuPpiRlK8ct5b0i6Pb9qgRmeZQO+/LQrsDdfqxgVioC1RnZIwxmJhW
XEiLXdna89Jz/3RFXVR2S9+FJ6NyGdR0T5uoaUp0QGsnz3DnUJxR4wDRE7Qm64X1sfj2l78O
J2lv75+gO+RKHV1ccezhswtbxwNBLiYry760uPQcE3Wog+W2SGrJGi77Uff1fx8WMYiDFuYV
wzVcqni/vAAuWhTXdLbQ/bix6MQymnIJLTyfk7hi0wGPilkP3n5zdrswFBt7uh0sbRqUdDSs
MrJTvpNn28sYXfQfj/nSlinqsBGSfCy/3IcM//cT/f753/gw+YRGOnopbbsX1nkRIWRkuM8t
xV3A6pe2wgP5XscgFPATLRru5oowaiYu0jqBeNFY8rvTUdrjFHioSVp8+fk6s4Z2agVJucis
jJ17jKDL27nK+0KohToYcNKjODkERj/PwcDTY3MgTX0Yku9q1tCMefC4YrOIHh5u8dTFp2uB
fjZ2wUEcRbpQ07s5m73Swa6UMZhEaoi9vr+cH+mWj/Vv4h3Na2o4JCiAIqw6xyjYSef4YIae
zDDF3imNgcCa93jaOM9/1PoIkEytq7btGlXntg7CV4ICPJJtO3gTi0YWV/XPgvUsZ3IKarL5
YrwqQk9PRuntkc6OJFtIESG+MGy5s5aWwxYH5icjPKnhokPel5VKJ6Jx/xWA4f9XAAapw6ve
LJ4wM+pS4J8MGfhguEPPiJH+5SNutSsHP4gKSJtMK0ZVLKtronyCCgLFWveUlvw9KIh0dKaU
1+ooYZviv2Vw9dtqp5ryeMu2F4TFhDY60ZL9eXs9Pv7RgP+B7V/IPu9JHXLcOO19nOzIjlll
e+uUBafNDJkeEW/9C5VRhVpIQ/vuhEB+h8s80wbwWZReF1UEC5OJDJVw71V96jCAXAmyIYXX
pInVtYuIwkg7bCAZOUhe2SyU4X738f4ftMyirIkYXc+nz32L8WN9Wys9UWHIzCgeYbUSXZ2w
6unP9KxOna1fGFd7nsEL+jJnQQ05GwgX8N/6gt6B1m9EuWOqD/gTVl+MV4ILcJE7OeXTz4Fp
702+d4hQFuC0KIAC/HRZGzWKATLnp0Vad8di88BOPOXxmE85+y7UbqmFwgyk7vWz/TjxtuCK
GLfmpt6Qnce4sCnBx8oTLQVWx89rF20+GFPv6pvmr3CNKj5UDVLgz6C5KWKxb8vFm1Tmt6w8
BPE5qFTqZAAlrUnP4IKZIzV5WFCAFuh4YtLuu+i9N0tfhKKqygx+GutjNzVizbdb8KCnZppI
H11f+8FswVslqnkxzdLjqKAjONMwyBDSiNOkZJQGHIszKSTNBeWmy3lmiradag+8ex2Fniy/
VsAo84CGCtyxOUjNCLWrrcTomnW4Q2navVRBgozysG7zI6aKs3gVZG/XjHFystNJ700s3Sh2
lYasckWCaJWpvKFLSO4rfzX/hWhLa6hXDSAFZafNVqY+fh7IpRjFY1FYy1lz4f3aeA2Q7pWo
eJ34wvTj8RBW5RH5yuj1NzL23QwQtDPSjjbKW3g4PV03EZ5Xo+Mc4zhpkhy56chR1CdJGeu0
5qzaPVyLZHDZ8wcwBdCycnLFTBsL/vwaoxSsNEN+lAPdkVEe7zEArF38g/nwf9skOQFysTGA
RNkYtuT7+VddPKPDbBF9N39N9I5T598/KGUXkF1RvHDQHl7Jog+KoVQuSxd1pGZmwa3Ab1/K
pU0yTS8wpzNFSuccOrsKyuN5aCOPncWzC1NzNu3KL8NFQPZA7kVmEGkrbzY0LKxiQcjwpE2o
WgpvfRAWEdTHaH5rZS/bOejHMXVNuRkuoZ5tRaQKI3eST69wSQF4/qblGIOfi+j2bb1XS/g2
CIrhmxiGSKFf2sO9e15ykUS27GnOO/aiFzagHHmhR2ZNEZhnv12BBGzjczLfeDoWnPkWm9HU
eVV7pXHa+EOpWD0g1UZfGp0rO3u6Oa3oCnPd+8TaHFhV3TfcsdDW0nltk+gCTfzFDa39NvkC
hYArvDkojLjXo3LZi0gYIGgjoWrS7QyVk9aPVDdier7vNNH7sFHZ4j5X+GnnyANSZDE2wQv2
uo3mukkFopWTQo97fO5CncwL/YBW4IV+aJ7r1fFYjvJbwNNLHLjRpfEFehRh1cD9O5PfYx68
uz1Ar6o7m2BhH686hD62PkOCDulNY1EBKSnI8D3/iMDeMwKjThSEzt2ZE+4Cwrm4rufVqx15
YOPaABQuXV6HEV7foxyX39t9D2nRfe/+RZi2uZX7pCD/0AnzyNGe57YUcrhJ4hjytMlZWyMK
8a4XydV+s4wJftIYsxrnfuvvpd/+bm7++2BTAGbL35SB8mvHvxrmmmmSHJ81pX6dNBez4oFK
GOnerTZREreGQydGfQKPkd5HLIXcGbvjgWPMmRSnTZNtnAfFSPUEuoyMGMzz6y2wvuVfa841
CsXVYw8Hs4S5c0wsFPQI2sHt4TMsp6pu8uV8BTkpfKg4J2PR90CFwv9VN4Yc1ecbPo0W87bk
AWvWjKkVlbp3PVOzVxg2xhYX3EYtZUBiVcMUpXrlKMMpp0ebrtO11Zt57UGOqc1k7MIOUB/q
AjEYTCibXo5z8YzmAbXruUmm+swnCGj1K/AjhacWsozIAWyaT+kQOQ+mj34pqkU4JbU61CJk
tsoiluMadGtud3PP1LnjOMDBMb/Hj/PCcTrN8mSQO2iG7I1CR9raOzsMUjrsgiLAmI6D94nR
DGEkpyIc/WouBYeayV9yhYfpzUj2W+jwKqJhR437/MSMAb4OYkAxQs/R9vs3GQ5zRuv5q91P
ildA9uuowEy6faMYY2D9qHXE6fsN7487leZWfxNqO7LcHcC4VrLv0VR+/JrzERNdT5wf5WV0
mm8TxEVPtjFezMKR/XeT4Z++/dOxNADw3E3iM786+HoJOZBnYBMpXi1xOZni0ZxJvR800KL0
svbCkSljcbJHw4YlG+IQ3jzMAjEhYY6OOZDE6wwcnj9KwEgilccFmzMF83sTamC0db6csRR3
FEhvXd6yHaeXBt546QSTdQ5PwX9yhYsxFuLEdJNrBxxQ8j9egaSL87cqqq9yqaW3Q1NXhWs0
rs8BBe3RW2hyPn8AUr6c3NY1tcwIsqgLXeaxU1EEDpEUFuxF8KcbhA/JMrlDfLY8BjLj3SpP
VAis+JxQprU2kIOuURS9cXriP3uPsOZqR5VdF+wJJHalJZAmXaKpEilsazqUaWBos116Fu22
U5yGcLBxObIg/q99ZX1bJ6acJ6AhXXfOQsQRvtKpkDjSoGUKbuI4KEYwmiJ4EESsT8/tuQWK
pqrFhU65Vtp3/5YWdbLdJAgZjVqqM+wmj2ES5Bs8Z8K6ROnxPOMNc9t3fswCkRS1COyQ5GED
niEv0wHLMyNFzl1yDDO/59UbwoLBCpUdmzy3sBlkeF0AOunHB/55UMSGHYSq7TY6uU0/56JU
QiSfH1OfX1/fgQTWFo3tCyBu1URgSGPVZbXVkxMrgl0AwvCAvOjc9I0PB5Aks4GllaNi08Dn
vEcl/SvRRXsNzuM3Zglr0+JKAeN0ptp+yjpvQdcDNlApltmAH4iyGSzkkLx09Kz8DmRgo8om
CDuGtmUN+T+OsHE+WsumsSbFRUP8C64dLQLLnY+eCBm89I+DZTiof5gMuAeHs1hfiV4IAbnw
Nw/EqI3/6nmI2M1Xp3xgmETW3zYuSwtatS2KnswDtxx39cje+OTNE/mY7qGc20IHhbUnb4lV
P0xmbphn7d8J2+lUUL/k5TN5e5KV3n/TLVynO1+b6AmWWfp44f7/OH3+Pz0QOj4xOuKO3swx
LvUo6jYaImhigRf21bMtWpf5VR8CP7O3Y0YWxCmfmNwEavvjQH4/KFxLeLHaA10sOH3i+i6g
hKhrGXDcRIMGy8m+iXpssMMxQs0gMy8FmzjdyPyleucL6a0LVXDWfn1pBqUjP4OMRoCiO9YF
BZeCBGBPKeVRe9svw7qjDF9afhTEpxkzaFnfV/yFz9/bt1BP8vTuyGSpPBRaXVnZivKsK7Pr
FG/5TEWh7mUDjPbcoRalqozO6nUapm679Wswm6/MXPXO2icDNrK8uMEND7l30mH0FREiF43L
wPuJTALWsYZbZ9Z3ju47WbS2Z+zxYLjRwrEwK3cylLDKHopZGLN3IskUexayVj9qdxZ+U8nN
aw1qC1LUZQxWcnw/4eeqPPFc0SPsNuI9hFfydReQcjO7l1lvKiBFPk1F5pPeTgvWFFURbQR2
S47w2L5RlpJM7F8e+zBXvJscNvF3nPWMur4bvTVYTsJayLlTXa13kpIiFcSpd8o4OhiMfGah
Wg5ubclfinHti4A1RexQiynyOAE28yMVbpWVvzdUqJo7hPwUgnxz18XeZTb3kIR852bKagzZ
4YjndviBR+L9nBgWYNFz+B/SAP85mcRyQb6m/BMyD+L9v49M4H5f1mjxBa+P8ktwDYgluoRP
5aur5xBW+7HmgrRi7Cr8VmH82UV16gl/aNftqNIzRWphkAzaGyaknmErl1ZQh3/B4HbbtC9B
M4cKiTfEMa2HDn84Z/ecyIPS3u4CpBKPcrflX4MRJy3vka0OEFXqxiTM/vAXf94YNNKlg2bL
Ta0kzLkjyIT159SzC3hXAY8zsVUWeERJVDttfJAYPTTn6kV0FWfTxSr0ljIy078i7gM0pf4a
mvTY4mZDoURqnSkLXtBJEF2bJKD91fEGeoN+QyC6kUc+HRjv9+OxrMYuJLsYZiXv2FEUPm9f
fshLMbLTNrwCR0DIgWFaumA9FRebNjWexOGNop4kJMWdMc9RgOUR6yt47qiSZqpcwAVm0Bbq
DBkUDTQr/3ZgHzx4ZaS1aY5UNrxkdevWLU66oPw2M7FMmfJ8kg+JxtaZc1pQJfh+wR74hkOf
S/ZQ3vj5Ggwpmn/4fFmT1/U1t/q7swrq/lNJDhX2/SkpfJXFxJXJlS34k+BQf7yddu71XsMd
Wg0/CC59o5saJD9k1mUITgYJn8s26T33C0y7t2RvzYxGu7Zg4Xa5x3F/urP//NMYgCS8P1kN
bkw8PBzGDJ7hgL1G+GmcIvlivpdtRnTxUsc6NhD/BZJNVo7FonTvgE6R8hTjsgs1HBibkCGz
v9nMX6CU8WCannZpDJfR9qaiIWzJ8mpjTM4SF2Nz6sX9f95icWGZrCf2HiEbl7Nibx+Tuu94
renpTxl8oM7UZ8us8u4kBYTTxca2fBF35tW4/FhEuFxrF68SkuGSlffGBzVW1ZWT7oYGN7np
uE0CNffV9m05hTvgBnAcSam1EEVcYWeEZJgfEwQUZJHDgTf21TDMNMMHElFTV0atjoYugAwM
N4M7Tqy6LEQ/dffzFRJE0zp9lV+530/atKPhOdrrZ5OaBjoHK6JrBAvOWfZO/Xs5C46pFhFN
5CPiuqCKKHPE9koxPecRGBY/hO9Z/3RxQRnJHpmuxpGxI/O8RJxvp20eIVYLz1kTE4Usd+x9
1D5D7rZlEXI3hqOLbFgGYwWTUsQirljeLHLzZBqOz5dIyyvsRfsw3JSlkB1eL22QJgk/9BV0
wBkDm60bb1WedXKt2KexaEWm7MbLd7H+DUdqlha8cf6DOWJ62e5m6Qib2ZIu0ctnDux67ZHZ
6plMzmUT6EyPtXAlsElOLNgrkry5ELTIazp+wvsJmWEdvTQecPyZgTAforf+wOueJWwjAwnN
HjopyYp//GVL670RfCMMuAq2WeCefVjZYzY2rcDfMNHQNXsihzGZyTbPf4qicnPLFdmJG3KT
0u4iD12P1N6aoEaK3PoK3Vd672qMYLa9cGEv+Wt8bfhdPAtLvRwODZEKXO3BvOYQAgQ7ThO+
47+6KTq5ONoR0atjvmFM+c422ipV4Xoz1nJrwZfuxNoXh13JafPDW3s2TV5ONrTxQrounPWM
29Rl2n/U2qE1cw5CB33K8E1DL0ubvFLpa9v2KZj35FOlessVH6aXa8jy5c5WBJInSOWsxIt/
PhH/XUejVoyUrBxJJsSD8wkeYUqTFGZAgdpYzr59hBWV9i7mlzX1iTGatGFpJh1oZxIxcpM8
ubrNA6smfj3j0No9pc66zgATHcX+y9a9zBXFEBYqw1vW1zncf/T+L+40EOfKKgvk+XnUqwgP
OjJZKA2dorsKOe6MGuEtkjvGPf9GRSAZZt/vebUTl5qNJdMXQzzKh1JzyTg17lv5Fe+5jNc3
vqDh3lmWl41bAngxVhHO6Z5OFSsvfCFIrniuJ5IsfNuR2weHmzu/TYm1w12XP1Ruc1ejbuyj
siG34z71lTKCHMgfqvbjMnsiHHu0CDgE33WIonL2io4I7JwZL0C0ReI9oX0wb9pKlTvdMOEk
nOhEdCpZmsHT6qSkXaPUudGTtdAIldKx8e45INSzwnLny+YX5G97OtPpLflDK9FlvmoPUeuO
NruAfMJ6Of72GAc/R3VJRNX/4qlD7hnLPRTepBBlFu3IwRXzjYk6UNxsEXfNCN+zbP9wMgSa
YuHYXungwcyEe1+lWNk4ZmHvBMq2UE00VGitADLLpUD6UOjMLqAh02whxJ0gytO+2kIfI+3o
3ATUngAXTmmw4v2iniKmyMLf2etJ8qOW3dPXohM+1sJdipJOU4zJ5LeLkhdbcSV8KyMxnWAY
l9NGDhdrdM8fKCGanvgESQ6HzmceDi6jhYuRt/FeD1LTQS68DhZJxmDhYXVKmo8mVlXVoufI
vMTq/zz5JJvm+ip44MSdQZ1Bkj0TEsU4Iq5xisnJwVhbS3hL+cdmkcljUzLq0ZZyUzf7iPYI
fNVZkIws/ZFNK8lvwttcztkmihmjSpO175kI4luWfLe4CH9yIunhti7rpNagWAKPSvF1qCxi
kQ1dHMBzWAz9HFO20S5zIgLShlXrBkVd0T78h42znfIon7FqwPyNtAvYVyz3f1K49nBcn8ad
nuq46sLw/mZx0Q8l5FagCXRDXZOwU0JOd41ZtW+qg1vuFOMwwUe5bdVb4hpcgkesP5Vwt+f5
85IQBDBCt2c6t/YsHaYK1O71zOQM/2deYjs7TcyD8R+MFhUn3cf9XzoaMmPOxS/CLhdep0LA
Qb2rKC16+BxZj9USPmnYY1IkimlRFuftDnsUhBYFLdQHL8VqVy1HrEQ3Fzb+wMq+KQdW0Nem
a/yybMjB4TRTUHXJ3QxXlyOTObzDh367/4e99gfGP1/gCAAoQcDX6FGd5wys+0KD/YYDjwn0
wivKe+RYNL8JA4dIsP0mFlUirm1YbXzkDb1Vc7d+c98kR3tgE7xU+FOvDlSnEBNeIiac3MLn
kGy6DzkbNUaTkdE52UsbunF1Ri2hecp7wvCBEQc+Q6hNZXnhvgc8m5eGWnBwdkMrNsFkaW41
YU1BFQdf57lag5RGi3MO/O0PrucPTBKNfevANnb1bGXN+pNUHKu8E3ShFoFfAm6D7R9yp5bT
26rfyW2VvxId72DnoHAk4vsyMZYnZ8kZqkGjsGXVqfSI3xxa4O1TiwrXKj3jLS8VT912WTc+
1+M0uO94mTgmTnIjgY6dMPHuwZbbxJo/UicXcZbXPJGv9lzyj7w+gZoHmSUdMc1Bugqyl3P6
FQKQaXqamOr9Kl7TUUR9XWteoo9RCJCbZHlBGM650wFfvXNTeP+tUWIyvLlTzvFRh25Gjvec
rwFsqDlVMJkuME+4/3qlVnvFxqd2ShKx2K7FduqK6a3kMV3hFaaIwvm3stDhGaWuxAwbUADL
O2SO7lSQZ+VdYc3gxxe22rXttzuHzbIYtGh2SDjQlVbWnYaqiKIarzkD2XEWOfmiRdOiv0Hs
TBEQ03ho91gfRjaucNIiMCuEzhIGB+CyNy8JLaxnf/4Aja/8hV3XcMumZhcwmxffJA5YDcIE
RTyJ2RZnQrzx0MAnSsshH8acV2DZVMAxk6Ai7nL/itUZLR1pvKS5u0OihUgtwL03hj/Sxaox
tKNu2eAj1j+5j0TlTzbIp2BF/SOEOy1z5TNi72D9eORHrbwDZS2KFTNFm9jhhdZuDNNx33yd
KQbeEs6/Bdqghq8UF1bHnK3WZfAGOTJQ4M+fi+X8ksWVjk82Zenmzx+cyPq+ZOvMJ0bp3UY4
HSJPeYhvnvNoP+0qaB9hyvBAPI+P9DnkqwjNfTcL1hLHp0BYVCVRiVvYsRXQ+VVMXcRdlmML
L+L0aovC9RIxchwDrxZMCbmaeBPDGbuiVaZQ7KSuuGPIeNQhxSbKxVt6OIiJvkZ3as0TbuEq
4mgT1/SzcUz9BH2sxhZh9jPR6nTMKTnl1JZEyYUb2DJyMyQD1+R92dQjXWoXkAT/FH4JfHvO
DFh4xA2DG5mw8UqtTEQJt3+TGv6Def1/1jRKe56Rbvei9QvRD4Mje7qoBMsSKM3KR0Pitcjk
mndVhmn3trQqiXXBscikFs+9v3ZMSbw8qahOYbeGdhWn8LccZz5TrU6LQxc2c0N2FzTEXHxR
UsBpgT8NNn3wbMf0Zth8337w9Vlyq/whGbdzMmI+Q98eR2N2r2bOTl/n4f0yrnOX2vIPbZXe
DnE8HWjYKEbZKzoqyc/u0HVRtPj9Tp5zUZ+247XySJ8QYxhPxEH/u6OjYsfSBgxPuP9mJX5i
CmzfjGk3SgfB5byGVsKBVxqKFh4mM7cGw/jq447MEeAnOk+w0pzgNwlicQvWMDX7rW7Oneic
LILizlesqz8zmC6XtqG4tlAnytnIqv2SVjhpC/KKJ6h5a97Zs6NJ3liUBWtQ7rX3ja2/uSCF
XPkkhquWOj8vhIkMZl+AV3oZpJKuShvvNbOA1PsIp4Nmv4YdnSo2sixr2XFEV0xtVigS5QNT
1+daswt5j9AHsDCLwTpHh/rv/azZGDnQ3SDUXRRWHMtT0PeBP6z/Gm8Z8aDUAzv5Bnb3XhRo
ptDKA0cWOxaW+IrlK9p55B7tzBywuglMwVgdDaOhImcjDAJ5fE+iH7Bfe0fjDTEN5kEmRGiG
TxTvXO9Tp6dpYeInbkYcWT96IBUb6TjxjVGc4Z+6bddGZnW76dpKWRoA124wgdO6ytwZjVZo
RiA6PrOLrbjm2pI/+aZG/x6uPKl3zV3sFYUadzvpXqvO2gX8Rk5iMbd3dgFc8xzFrBGw7t7R
EJHHZtxgjl5OtemRhiENdVW19hFerrZJApdFh2oJb9Ucq4nNNi5oltfJhYdNFzCO2OgtXfx/
jmjteaR0YzO38BH7YP5RXtlPOguEH1nkR94Pi5dGp5cm28hipKJFqf2NlPyh0YnBkvz1T0iI
IvleuStzLdOf5JgHfPfNgpBebVEmo2yBm+G9fOkUu+oMLa50cDaQMYHZYe9fu/XHt9G/DbYL
UPMuyzoImzt5vt/Co4EYTma5V9sic+R5gpQKNBQ1TYZ4l2HR2RXWcCV+Y7zfHrfV4FFGBrf9
SdHn+Vx0RHHoLuAmxQFv2NjY/H0w41kgGePntwvAq3VOp/myvhfHKsSvMwv6/OwR5A8k0hEs
90VeBYl4yCsdMao+Ea03Jw7/cAdysKqWA9+dXs3vJ8VkXWDBXHg2N4TX7Huj2GlaRbS07ArT
3uh1rO6EO562/jr/lz/uon+0/gvZbwDgGL7X6UVbXOFw3gAr1tlra0AEdmExXEbSPohiVueP
4xBH4lEBi5tjxPZorJ/mUswPwzPpnTzPmiX3XcD+mlSMqfmJuAm6r3ppCUrzm9ENHpRjA9nu
dQbfI0b7qVXZ1GJ9dOyvOF75x1b+U4t0+qsyTsE9ChQ1g7EHKQ3LLhAbdE8sXNUi1dQgqolX
A7e0IiLRCqOIXYDS0f3ntF9kglZUi2ntsIPmYr4d0Ilre9Ow/kPY3iuaDhFFU+oeT9KKuydW
ggfTqMA36f0uSw5p09kbD65MRL4f91fNwTIlz405MdzZtaXd/OXA+9fd+XYEJ2J8YJETkRr5
M77HTYok1wkU4HQgyBey1d42yu5BWF/J1JMOleAKk4hI4bNl29On3hK7klkHVFGFIWFC74+4
xCcRVdcuhClvO0czk6r2+2q/wSJkO0YiDJDR5T66vP1lLe3HiXtf9NWqhWU2GTkOjQE7u3DA
JwZh4RU+iM0CNPXBtfFIj0lCE1Dbo/3JcRmeB6OyIAmRDMASE39lj89UMdzkU4lRAUjr23N9
4nLZOqLxp5+9Z+DdtlZx+AdE8BGDKVLNKoqy7fySy5N4Z6eauzmPwtGwoTGxwwwx1fu3Sh4Y
nCSaohqc2in0W9NiZWmckIat/DV1fCfX3H28R3nNTUhfvmKlxUFcjZ748qWdfbJlNM7KV3+B
ZGhHc+ha3X6/rytuc3XARZ4IPM+3UCzJHyJ6ngB1J23BDfSlJvKLT67eKPpkp6RrnwQjRaKm
JvDyl5xnlNw3v9EDsAYmrx7gOsSYN9iYiwF/UzHkYXHjnEnnK0NrLxbbtJ03z+lZLqT1370u
7SFZFqO/zrdxzzq0cTeRWenwVOknhvfdC1Etg/tuFkV9Gt1XjESxJVgDBvNdwMrElqQPpBuW
FKUI/RnkdP4NnieGZ/K0RxD6VpnznKkQ5MVbiciCgGVYa+rjpOfbZ+G3cKG1g6FHx+06lWVg
Qpn5zR8+UwSw69JuXPcusHr2cp3VaJ4R3HUGFdnSPtsvSXu3ljIh8UtKLm2S68CfeVp2NI2S
OBH93rUmDxyn1pqCZtv3LomRgtULCevCAyCJb4U4O1Vio/3S53s561ossxb0dtZ7S55BcdZp
VJX1qFgS71Jh0/Saw9NSWP1g0XstC8eouCudKWiL5sUtMcKfQWTJ05JdJb6ROsu1mAFLLh3l
B1StqjmKCINlh69wRf/zdXv7CjRsx5DSK6PldiUkYznOLsA3/NL12/yy58WNjpi6SItijN2z
3rNMrlhziPi0w6J8wxiCpq3EqJbXSN36p3fhnzq459MzdHKq0vKH+YEUUUm4pvD1kpGUWqjg
51Q8iAuP2a+52mVb4sOFfcDtueofYdXulgXv3cKcZxs0UtYUBNB9tfVXCY2P2tumFF5sX0ER
VtQaAilJ19n9MVYPwi85BlIvXdDvGQ1snzwQzE5DAN+hB7zjCwjD7/hRV8bdmbGZJp2tqbzB
DCK+m7V27lacYrKb49Xzo/4qSUEX6MrNQE5H5i6g1vmK5iGnUq5mv0JCvi571PadE2N05tgL
ushEK1V4cSnCrD98zNqpQ3Q8TH1VqOyhsJeZ9Fzr9XVUt6dOug+qCBYq4dX5+70Z1W5aAdwF
PGRwPmKXzSb9QPZbz19dM57qR6Obg5DEx1c0qd5lfFm+i+s9C+nB7KjEarF0Xm42MlEzHfHp
5ztRRZP58/Y3+7d1K5Wmqujv/DsaE+IqVe7Jrpf1SeY62KJKGjoHBl27C8IMrcQRigmC234T
bdw5i00jkNUCdzwAB2+Sr558bu+yYL2VRWNJ/pQZS17j0t2AL5t2eMUgg8GAnsUQFk5jF0Au
s/5oFRKUd42kAM+uxegPrA7l71QsBDF6xFvmos5lieXM79bkRlXSugoraoby5LoDC93zfuo0
4G/hcLdO9ucZkCd6dwGOpI+lX36n9H9WNvPKz39oOUfvFM5Q+bfcmbkjMsXBnRKXc1abE4eb
y0k7XvjXpXrxuhE3n9mD4LGhLYqJYvxpnoHK7WS99U83pxGHYzHPbAzIplPERW1MwVMlAzVd
NQ5qkpn02x63W5GGlQ6D2owLOQRKmJUVTOWejZE9/CUDbVnffAkSADlac8gvJSMi3UOoS/ML
s7RDyiyB/KZgL+T8HvdUvshT5b/oNXI8FRRmwP2UV9pfkC2wutJCsgqWq1e4yrFdupd2bjFJ
Q993jUlSL5Gxuv3MHvEarCj914RcXpsmqWh5pUq3CYgEj3ZFbkc8A0VYHdPWUXvl5bEusrkQ
r3Ju25S+fCazB34icJhFVhlyCaKx9sGL7qF0kVCdADNbeTnZlntFJ5TTw1Tk9AB/Xm3EQklA
Xe8+FO1HpAnyi2wxb3jb2rVPEh2cjWLFDDaB+b0t+bgiUmCAuODQT1XVz2cPwJzmPRrjLAXT
3ET7TBxnNVwvkrzWTPCjuBs/C6prZCgJY0Nupi2wF9eXmBPqatQwQL5IZrEhMNT3iRD+mKW2
Xy8yhPzYVtkSqOiDf640OTG7rSdO9ION2AQCJ34Oh/gV9PoPb/d/I/KDZNEUGuMwJviOlPwD
0fzVfPMoPagi41l4Di43uE1d19crOzU1u2BNfi6brzSag7xzGNF6ToXoeI38Gr/zlXd3plYn
Ztm4euXzIii67gqW/wS6cSZnCeyzU5OD8sHVHYlGqfq9d6p/UBOpxCwYWbCsKB2eHXQr9Mt9
as/WXuVWJDKcOahpQqq4Cg7p96Py/d8vvxGIY61nPGt9Mvu50KzUs5OJLpo2rRRjJyYpqxyq
HdUNaLmBCb9zjCpOI962iUfKxr55WbSONjbckZDU8rEQmRG8W0nK3dteP3bTAC+//mGP/oHx
X/LYAJf5bonXcAPmj9RQyicDXk2zBhdsZBdKzeUptvKFYvQPenIlznwNZA+ezGSKmW2xgsCf
hJEVUw+5cuvVJudO/sJUp/JJFVhDiw6cKOkGvaxlNvEcc/wG1txpDk+0B6/QbQYf/PX+HzTz
z5rMyO5+aLSMIxST8UxmJr26pJzWDigy8jq8iIGkFnmMJH7rVS23v3svmwnfeXl0v7tAs650
PBbL18nVycHBO707nmBkDPhNhOFlA/LpiRPOqUVqWZaPrJ3WDsl3IqlNp96ueaG2nwUZxVaa
HsCy8sUboDdGDpflgddMZiSRz741PEMvDTK/Lx8TVgt08VafW3+NdUdeWbCP8PE9EbTgYEUr
CFsTrkXv0Jv3gw0KprTiTLC8jJHG+av+It2uskeGLQMjDKtgZT8na5GnVuqaiozp80AEUvvl
g4gFn2/SEtenH39mVVjpm47VVhT1rznmZSSR+jsBWH2z4wO4CZDPijlEfhfg4dCZI2cPXzne
I9gzNb5q3Bcg/if9WLB//zL6OiUpQvd1rFmyNVDLPXXzZcuhkufAFpzhNtpS1NK831+tIMug
dyi7cVTjwILHuha5eFYWZCV7GyS49PXL9KdORHYOqTY2IIlNwk/aLVacUjaOsVsIXVL1V5H2
91tfPxuURxHNQH91MUu+Wh/7fm5xLPS5DNB8Rx44Tle1avbGXprizDzqtkEWDoMGtjob3jIF
+m+VTGdGuo2Tw2FjoVZeFeFW3qkltxngduj2lwtaEw3FrwaKthRuhSUrn1m13TdPyaPy1Twf
TXYNzkIeuPakv1nR82+Y3NFQ8U7ZwGbPS+PWpLA1R/QiTHLmY5H2oIhQ581LS0HpCLtofv76
4tgERlqU54aP4Fec2iJ3kazg4VaFNZU0PR+kE/59QL7YgXlJPLVd0UvKPwgzOhnbnc9lGGaY
0UZ8v5hXRV2ewg0BFWNnXFvWWbArOcLY1/xba6Cp9KPw8bAgaRM2rXr1i3Ao7RJ/NCpuSuME
6VVfNNYbNjsod4Q7r/VWudrqpmNIaWOcg3YycxcwZRicIpKylqD5l50ziq5H3l2s5zNnLixt
n+yXNFIK3HybVhAkJp7dP4nxU7vW65PoDZZgNswFtcSbJ3wdUf9M5W0e7yAKYK7S/icIkkfu
8Wa7JELa67m/MfgsYZWr9NVuT0ST07ZalpIZrZQt0BTWfJOaIJBzwvQmyL5EVzhQacxwh60p
aTI9lTRP2QWE0DYB8cfywg33C+Npr3Z+6iaNx9goABd0Tq0t1XJDmwmc0mGvaSJv09JJmUZx
OLVaGlU9HOW9mH+YjwN+qDMT8fol45keyhCNNeixMGVMWcsn/I76nkFiH+nVX3Y8knOdC+ci
ecByChowvqNY72ZVqqy1C4iv4k98nGqes2l7ubljcm/JREUU8/NnzPDkFUvPxArP1xzexBmu
sdWU4VWNDZO3yhmZBDYKsuMSCk238n49hBnueEQJwpucNgEiE4Pc6mkwv8SrPypREG7kU+XT
NYXFzmusCOftV3dOrkY5jweWOx0L1xSs95Vs6n3qdnLNtNHCqseOGHYTzf1v8NcrLq1tndlO
3QX4WwkNSpN+lBwiFHumQ/ANTkpnUkUsaOBqS7vpa/7NWZfWQ7uA12N9eUqi8qu9Z0TyFhKU
oGLk6az6R8itgwjEU1wir1gSyrWqQw1tKd82LkVEsV7sDO4ZIHXDNEjA5OyMHBVI3ojwvVTT
ycXwZO+vKwoVvlxGWcvQrxEuXeWaclsXMsQD30LoR1J+uRAwZfKijXqyZXFujH2jZ3NYmBlG
dsL3dCAP1Vu2p6rkS9dMSb48vgvouvYkacRWQXgRYWfCLukWhSeIRST2LyYNSsxeoExcT1p5
MZK8cfORqPdkRWeWtrggt4O0f1vEWaYXbgwn7gIskdoqy69GwBt3i5KqJTbn427sAl6Q9tMa
dMx33qt0+7a1bL+rAYmOB3B590VwZTerCZ3P5YvtjruAYMmV/uWKXYAmVC7piXuM8JZVfstL
5Oa1UPy2Pp3GkhidMmbjPXijk+DHldzZmEQMmF0rdWFy5aWpuNFOT1RGvKSFvyR0m54ssROF
e+qLGx1KG5SYjGuc+AnjpG9htEECnhSr7UiZkdsmjMWWk6YbJOWzoljT2alrL1AIi5ZQwShz
aWrBVUpxkz1xFOmkh5ZC8Hx6d1ol93XFx1mRVj0b50u2hmxR9cNmzAub4xxmT8SBqqk5GBPM
fqtkTr0cp1u5mvAxZGarPU4O0R4u9VL0lv1sTFTSQtWHI2xzMN6LwVcshNRf4uQrwU/qzTxy
RHRo4Jpd+7EP0sgeu3En4YVdwECe7+YpoG7U1XF35JuxkBggKVhMf58lv4dZjsOovUBIK4Tj
t4ZIJSLPWEk3Pkj0s86O5NGoaxgPUsQuQKdY8uouwE10jZdYRDGR45d+1VfbcAashMd/Dkf4
0n6jUvXNk1y+joolwL9IIrP6kl4eTOqNLj+6TJusemoqUoacmkvM8NZW6ZOWS6K6xywPh0Lm
IO1n7TelTi6Z1axb3FBEWEXoX6JT+7qzZpOGt7VG5ZK8YfuR5GenVvTjhxbTMkWFwwQ+hRfn
2eGRFB4omY5mKgSy+CvmWSFuuwDiBOk0xTtC+XWcC9PMfJMMWUkQQyPH9zApzHNA+KbUzVJn
XizpMQjRcUYSI97oxoBkZh29DNMTmS/Y4CDhK03JDHTfXLpANdE/1MP/xnpdvReISwadWtSP
71u5AOraSDAfQeCA2ElMMdjqrJ+LYA+D2peFotAufdjw9p8zzN0UyQc/6myb+2tnl7W9+8d+
0yExguwes4g0wC1WlnrDIOWd/JLdMiSES9IqkaSlKdLCs18sDlCvX5glg0AuzVshTd5lRcEz
SoUcfrrB+ic6rZeeb5GdTW5JqOHvOFnTz4ikDCUymeYJ2wu1SZwFXVjul/Ies8RDhgJBXUax
5ETCtdnLNXPpNcLy7GsrwNi1Q0M+bKemoCqJVwGzsJKWbjuDzTC9+V2AoYLFx1HSZ2ghC+vH
sf06tmCXZLj9tRBElBFWNe6J+JUAF7g2DV1+ZF6pX7LSOKv4OM1/O2paMrDFXjluWY1avw+C
LGebOah8brsPVwRfBcZEHedlNeiY2K9shQuU93nHUW5olSpnWgzdbXS09fr8mT/v3UfohrHn
XaW9mDaJgdpYrXJEaDWXJBdY+7eOhGwXQPFqfgr7LlV2mz1m3N6I8dPT+/DBHM7R0hHsc0j9
ynInqDG2W0duYvy/8NwXEOzaS3MzO4ci22Pq3Mv1N2/KJxap3KP7lX/A69cIL+JXF1JPHiYe
WfFIF06pI3KaScm+tAGPUuWhzLRcQs8gbEkizURdo269t2rLJ+kLNrFfq0zjrYb6Vohhs98z
itFNpP3EHJH+nxEXbNPM7S9dlpaERajIfn11SBz+cuLrB+yzKVidGcdfTPOVvG92mitdyCDf
jMOcy6J4h4L6E3KXMQ/sXXxfLZwAHdnxCB71wnBZv7oqnjtnsYcVFbvOl6hJesfg0hJ0Kh/7
wHcBYdA9N29Nmyln2btg7/WbPnMqOOvbA1Wb99nD/bPe5N997zuztYAprfxT0ECy30gfXsF4
ktWGXZhsb6EBT+44sjtsNbo2cSSfhDXrjkbOumpw45c73VfrnQiLl5+sLWESZ0D9HOGcPNJl
bNwjhfxuxgBoHi2MDyDH+6QTG7tj04LpeuLa/KPHR//ulH//9t8XjQZ8JCBq/UcjTpR5jXJ/
MNKxuszNKi7IuCZjFlgoCU5T1cSOMx2MHPBL1jbAcwfpni72Tk/gzL+euJBrPEV5npubYduV
3Fj2OB0JuhAXh3IQEmei7OMKYF7NuDqPfKSlEQMIHRp7r7sLOBDfuGJTqaEikzQSQt15bBNh
QvC73SwV5QqX7Yk50RCYz4FZugVhYN1T30NCaaVcXRa+dyPh2qBHoe9dNtZvbYPoWPQgEFGu
6U/coghfWd6/Szuw+WpYWvFM5cnzowv9zA8wVnrvcH93wdPBe+tzTeQRqp3A9aLuDcBe3a1h
WHu1eNU6UOOLjE8loXOKgwaihdtrRjcLhnLjeDwnnH5io0LLW6+mwnvLEe/muFYTMa/IJUGg
prDBgDRdWyU95XF6spwd0154qvP83w/MP3v/r+2t4ljpsHtw0qXe6PrJbxVESw23ZvLjvOTn
1uAg1aY2P9S0uPS2sbFj7z7yp4mYlLq0sAbJqOCQa79UVJdPbdMHKE+aXCbCCM7gTD0oYzp9
naqcZNRmLlZYhMh+Vxau1kUYmhxLfu747tig/+HoHZzO3BZILho7H1eQy47N4RsHYRyA6ChB
AbzlYW3DmX92Vf/6sahzAe5edmg1hyYKd3aeDh66H0f2kPGdFDwdQr8Zj1ndhJh1JkX/Gkuu
Ozic/45jpCwd/JQgwpwjVWjzl1mSyTEvHcHlTBNY+NBn1stuLK46Os/A6uSA5D6OM9mVuppA
XKwHkgJuuQh0LpqBN89NaKutOXqaximJCi+2FG4YfrSoI1y+YNbOn4iLG1gViN6limfCg/PS
Jwywu4AfyUPbNMAqSrxgOPcalO4C9m5LtOLfMVVf2jMsDiKtiGRiyi7gmqQS51VCOntLaj+b
uIbOctsmX5fKW3jB/tVzS0p+Vr6+MmzWQAC7YnZc6fQFHSq3dX4osWWbM9yKGQGdWl6OB4bD
k2i/NXNif390BT2zrG9jP2ppn/7U9sQuSa02Nit9F2CEH+mGVTYWK3l/dZ3w3RKNlguYjqKf
pLTzZMk+OZjTjY5nXJRb0n+hix2Ly/ejCL/n8ZKcR2OOzGzN5yrSel4rmQ8djZUDz5705EYi
EKZRiPZfpDJEKQkaeNGh5iEWbG5RDy/MezB1J9JiQC5m7dx5swlaUNs9tyBh1mvxjvMyxIwg
ejvpq84lThhnGO10tF3q25FQ2SmmzTvtAoDSbbXHGIMJFl8buytkPlCSih49JDzJWVo92THW
TavSQq5+DWV+5Xoiezd/E+Oeq8vCRC9PzbGno2rH1nR9DFH1FKgncjVV0m3qMk+oUhImuCgG
R18TB/qOn5odmn7cdGzHLtPcvZxAD9fc/iD1jpOy7Y/sjW39MLs1n1CbOHFUbEpNQIhN5Q1b
otrSwcSJVMnrfBupO2NryqdDv9EIHd1FCz5XzIiRrpNZtC6+SK4DXostVJk+lfiwyHAXwBTs
p9XXIpcPW11yQSXNCR97cyF2mz+ovC7ptFrb+VzOJxRu/036q+skZks0AhYwnUU/SaO2tCOc
bSxnuJ5nCQhcFOQyjfXpfpjoIdcIw0QetKof4H75tLl1ILcvCbKtJxL6J6lJTk3rrnjsxIS2
C3l520+lv0ImSVu8kSwBy2TzmMprSidsbajhHL8atnze6lIMijtHe2LFDeaP39rZ2dcVZFUu
dUxcrVBJe/ZoNj/dk9HR6Lg6grDcyWGIQW/jFyd29jmKRYHKF+SSEFEq4//vL0wqCCJLRmMY
NekN+4Ekq1/wCyMfzV/Vqq9IWuGXnJJfIO6yZ+sXLCRIQQV2JzTWEs/PpwE/9EG8o9kS5KAC
FbmiNagJzwxIcmrFL6xLQpmXF045zbITWL070IzE8rFTSniEFOmOCN9h+8ypj8ciJr29aG4Y
adI3teZ4533A1hDecxfw7uMF3qpBRw5Su2MI5TuwOD+DWe2XtJoWdwBPDLbzSdpcTOz52ibW
AJoylAM5VcrOE+jLW/WXZsYiLwyuRq/567m/48JaQyjRogWbi2t6W38Nrc/n4MdezZDFe1QT
ZSTFSOJbRY/Gg6pdwOdYaj1+q+38tLD6rRILIrMZjmRs5DWmiSo19mIo6ad4HtNFbduJZY26
mqC12ld5Tluyj15lprHxPZ4gt63RvDCVMjyILnRqfXRU2le6MOtM9lBdtdt2O2/Hw52oJPrc
dGo9rNZu+bYv6eUgBalBWoMkbscIj9+PjzZzCb8UtOYoP6tQTwub1ds+8VWKV/+qLt0jkxF6
lZLP80CDt3N+keo6Zw+01dONu+a5v9JVCI75Hh8OvLqM3cMfidwcb5GoujEhCAGxtkivqNvm
v0kHnfgt0blCVZWp67GXwGVEXjOxemz/6Gtl2zmtV8BHr+oVumH4wRtyO6zrUpPntBM+3GIv
93vWhjYojyfW932lT2Ne6ewt+DQi/ZfVmhS66e2qClVL5cvWzSTW/L378FgWDDpibav8oOgG
b3r5RvWM8Ffpn9LOkOydoWJmQ8sj9tH3Ef/6A+C//+Kz7ruEJef2J627gAjlk4Fus6O2M83i
elwoLf/rYmAqtrREvOZm4rsdcAlDRWISjIeapeeRWIUfmTUr9dNjTjKGAZQGXtlLubGbrcjc
vjUzdS0s80liZhOZB2rF5OHKD9UzrNlpP0Ev/vcT/9fnfyN4UMwqhh7FaHhWhOXDOKMq+6o5
0VCQM4Rnp6AYGkEAKafiNRRDhvAccf1vaubHRqhG5PXhdYpJ+IZzk1IL8RybbNRsXOTDKUm3
sazrdR4Ua6dZVeMoz/mPjtSgv11GlyWPtbLigY/q38/gyGmrlldR5+hQ83Uc5YJzoF9JJtcc
Co2bIsWtPnzQQ86eangZYtucXALz+isvDqV6dsa88ihPaBCYuupegbFxdgAm0o1HLfWmViU0
TCF9zBTFKLfFjZbPhxQ8Kk00sRHRIlDHgT6emIbQAV3vlk4U8IGBPDsMCf3tIG3E25XjFIs2
FkfauvzaesO1UGoyESOORnqsAbwqm92M1ehfgqQKVBM+ZnjhtiGsXI9J3MTQG8KtOUVjNqsW
+jIdUzTR8zz95Ri2jkwOFBMiBiKna7B+GnTrlvd/wUwwbw+NJO+JhTfMo1092r4a9+U9zpK1
C/RXR8vGBRZyxdVlTxUO/w+j+w/mf4G8RfzbX+qCh+sbJiWeDNIOxKZjHb2ei+MXCjrrWNHp
jR0nMbeZmNXAenMUbu+UryUmsiv59SHw9CITuWO6mfKpS8xJ5et/C4I/B5vbWMc91QmSpAWW
4FJ/Ly6U9fpf1L13XFPZuv9vOcg5FhwGgREEvDiCgIBIlRJ0huIogUEIQQjggIK0RFqABIJl
lCZkGAfpxAENkFBEShJCiEqJlBAxhJIC0msILbQA893Oua/fvd/vaTPn3vu79/7DK6y9s5Os
tfZez/Os5/m8q1272IYz2bl6rnI67cNmefvz0h441hVBgx0EHrcazvSvHlxYpyYj44auAcmA
nfKshCMJfA63NPvAxbt/8Zv+lzYwVJGx7VxY8eIo7QqlrXe9vgZO9Yy2razcvTYeW6K+bdPq
OkAylAPF5JbUHetyYLp+f2mZ1TmsgLoXtn6Nsw7/2Bt+buGWS5lIl4VSD66DU1Y8SJOLttzR
nCIOGSt1rGdIa9Fz8T5qTaaZG3duMNf6aL1eWsCV95Enrpx7GaYbnU2CZ68yXYYIszkiCIRj
CIGAIZBPkKS4v9Gh/3Xq7cAHYhxaDT5xS1Rjc6QahuIYy0AuOHX93DpDac0uOQuOk3fPyV0w
bkwfmsipYljLn3yJZhGlT/OutW6tCtaJC/mpckbdJmk/j28Qs7dylwNrgqoSGNz4l34iuYae
xSr317SfQ5s8xUfY+Fs9EGDVwVkrK3Fcu1Da1baNKcFYuEbpH+KXcOkS/ZStdDgytdP+iIlV
rFGrAuL2sdkv1kNcVDkN58tachtXpsRGaNX3ut2cQQtWfEB31itkeh05AtgibPvwUm9CkISz
2dB1cd15dhO7xzw24usWvZPChEnsfe7kg3odjsEcp8Z4O+YNvltFMTCPbYIAmwbnFGkn4bVE
QEWsyuS+hIt/o+//svm3Mnr//E5PxxubcSOM83wz5gjp81q6fnLC6rxlp1VZB/tVkcaZd9Ww
lo3gdKAYig0U4nDkHLouXyqRI/t02Tt6g0YCPs4OKmHgxlHjoTutifB42/KRlhaoA9tqBmfE
BvNREqahwQyeGNX7+Ui7KSjOepKHsMvIdAQJRjXyAlrLpo0Fm/wUP3ZmIsQb/TRgEI/B8DcJ
ItVDmY/+54sJ/WXH/7WWw+gpufwm1XBs9ZRLX6UHJxpeEkR+Xy+m0ionoNPLJHSscACPSaGs
ri2yh+L3Hmm0GhGdK7DfTOzqZvUu+AdM8otPwfr1ATffXFUaUCsOLNKsBZTC8ty0snMnNVm8
DthdICP8jmJiHOlOv+NI4pFIukvgRgJ+fFwgdHP8OdPVBtbxrlLdMlp7kVEHyBwbuRzrARu9
hn37177sp7b/smV/L1gEeCFTidmFVcMSCTy0HL6k6unOCfmuZyhezQpJuKFgiIr6l3GSnw9R
7tux9Kyym4DKstFtco55pjGATViwahDaSMSvz2qszHm9Bmt329JSm1WE5PMVDq1lTLEJLg3N
zaYo6vHxmoK6Yb5U8hAtdKO1lONwZ/0B+utLxayxAk8dTZcq0loNPGxUcxgf/9Fd0NPLKtjZ
yYmQPpSSVdtgSEhFvjRSUVNodXYFMryi1QVQCWt7/J2l+8eqb9O/0xg6QKqN6WwImxOGC9BP
F6LMnkytgE0jCPj+9m/19Lpm9nerTldPiJnWt4XHRbz2YCW+VxWJtCNtu4W5jk1SFPmvWiZR
sBktqjeoPbytU0ft3qMdWHV2trxh5Hv9po7pnfbdgVwi/4s8ajTTq6SZGOzinxLf4SeTKscb
zsFFKg77h9/qePq6Dms3OPHLnpuelGQDk/AIo7zYQSMHlHbqpqxX964olax/QE9D40iKwZ2w
UL8BkkrpJ0psrh83CWu0/zfLBPweptOfZ5Kzpe9HlkzMSnUEOar1CMUP2rOCQamTFwVtNFkD
sETx1FSFoKRxjWCVDIhqGn7+WQLT53Rj6HhCvPsw9aoLJ3ztKeiW6aruCJ4DyduA+mPC+xx4
hWv69kXaW4cyDIxYsQTB3rz8DLE7L86uGDwSfT6W3CAzl6vepjFFOFNdEpTJuJ30TsjNDxaj
0Gupxg5OCE1D8OefG4KdXW0/sRuik7E31Z79+bv+7/57+NIUuhT5eiL4aueg5NqCzORo6JxX
eaBBBMPvam6ZCDw/g/cNTGfL22ZnV5JzMfdzi17aOh2IOd4V8G23YUBw7qOavFJoRoatoJ1a
d0WjPBTUu6WFz40z4vgkMoOVhh9ZyW55yRp/kMt6LeNDDu30kXlJDm22OtU74GYN7uykccsr
7DV81Rsfp4yeYnh5FffIAtrpYAPgz97wi3+rZ/8rLIS9nN46sKFdS5U1tDfsTlgFAyW6OYTn
NPjxcgnZSVJPh+KWw5NfVi/cDN5+G8JrulKGp3p4xwVllRE0a1u4LZ9s9YV9rQjH6vwXQuIu
npfNYyMB2xO8Y3G5qDUpe9XWJTOcEzbML7r0HSkLphskPG62bQXceIcUSnMeh9ACYJXbDmg5
r1S3UqHIdnD9zXfrVVC98HWYi2Maea2vB685VWz7vgI6hg0KOI/oinMBBP4e7CLMH678Cezx
KK8ijIS8MatSwVGyVXo8I7ZhIZ4xkqodYrdXuKd4Ut/UbF1fqWp8VUq0fjRARbXZxEwZevZV
307K2SIiiRSU5nD9oaka839Z+hrUxWlRNRPGfz6VUFBszw43NhMuMAfbhNbHJB/pnqZFw7pb
xu6Dys1xogIGqr9QSDgftliNcKLaKhCoDuh+tOQZXVmnJFHDQoZCfb4od7GbAkXIA+uU2D0H
G/Amy6vj1Ch+bxyynjHoqexU/M2ghbUNb8NkrNnOJLOE21LngHa2bQhM2twrvPu3xv6vtxuv
8hMcSlx3Gqt2rX8IUfjrJ/1b6/7iymkPjameGuTC+IdzYrDOtWpvE3+FWykI93c1MCQh9SeI
HMBocQoEHMbk7kjzb2Z5mPLd0+HVqWiXD2V4xMT87Bxh0tsaYeXyMLwsh26PsM4gxD1H4g7z
c4tSvupczurFPuZX3BocYX32coUEf8eudHnonYaDcXuN3IvK8A1hlVDVM4v2eb3roIgp9Vz/
fhThDy2Lyjnwwyua9QDFGySHsPRyDOEVNQpNxlvLd0BBIllHO0tWChDet4FMFVUd3ggiWH5s
+Lef9L/2lXkDnvhiGgV3q6mYdW/A4B74Nz4ubyT2cmt8OQZDhLnKT4AHgHbuj7bZp3eBPcuz
PTa12JlpScnLgLgP8ronSnPRSCHEPF4eFbeL0IchVyAf8ege5P4Tm2Yzc60guHEuGdviIPSE
zzs8Jrw6L+5q8C/fgU9AYipRTzpaNibLcpZuQuWd5R3WUjNdIOfkAppVFedBR+YrLBIbTXgx
DaoPXvAW3duq5aZw/TCK6zphoqMEKJMEsJWbkzfl/6bps+c/O5nuaHs2XoOAVz/FMgS91m1b
mbya1a3qQ0mkbfCqV2FUow1iS2d/WGm7cOH60uY3G2VSD4a83Df1uOR1Itu0raYh/CznV9/l
ZisEWM8KqjTyTPBWA1W1khvV6P7KA+9aKOMbUa9DI1xJBtYlwR60/D/h47Ef5nsSWtfuHDrS
iGJG2FZu4ds4PLRyyBg/Z1lRN3D91atyBsKf2u/PcVnYPIO9o5Coma+aYLaSuaJmO4qTjSon
xhOIyoG+nOTo2nXhaIkjCV6WvLIV93qcfUFhqjPtuA9To+QteCwvE+ObmpNXYv7YEns0Aexc
gEytkf2EYfio78icrumCV2FamVN0pImgubJw3bfbzhEJoaw1FpiUkkCsomn9+s7ph80ntIEE
l0hHM3iaf1nhaltqid9MtQPaZaJEk06fXL+HMUFc1btS/9jPi958uOJNVqqBQUb53IXouOdr
q/1BgsjrxKG8eNprn4Ks15g/Lo6KCEjpP5r4C+gGspAdw6/bGDRX++LW8BR1QtMFKeQ/cbv9
DljDv179sP8k9Qe9P0a4JGcQZxviQguE4/j8UBb+ekknBCg7dbjlITo24axSls5xgMqqlFUm
5fzhcljJT7tBFHlBH2nytMBJ2fE1fXddBK5Dzfux5SGAyT5bJnSzgsSU4UMFSXhKDgD8URk/
btvpdD3N0/ExuKJrd4DoUqOq7NwQaWHUk+H0noHVlGPaYnIJBKqhTYuNrQnhh28SD8Zw3haa
hXKjnf60PvmEErmZ4j/hHk0FKkdLRcd8aqDBT4OFBqBDP7Gh5IN/qWn2T/Tdf+dbvuB1/bLH
Om7vBKrNMZNsPM23eCuQG6/vxobnUVz7uRpWLj7vfdkrvayZJ2O5/v4pOsIBWXkGHH4hf6oq
djTkrANskB11uKz48qAnMjXzOsUAmpJbZRO3Bu4IxGvnZa4V4Y5AXMDk3Hu5jXmr6T3I2o9L
crnBMQ19FbKIU4q3PSr1vvuuX2509zHFYSM8KFkoF4T70MixYc4GCfeeHthYMzjr2dpaDWfm
GdlSkUL2MbatgUpRdtKKjU1s0ckTd/92152KqOhfxY2w3noCWe69B0XFiRWKmiPI4vX8GwEX
//bb/voRrYKJliHlxTmARXRxVIbHM1sxkI3+1SEzBCWJkAQ/8ln/1dlv2v0ZdG/VBOVVwVWA
ylJKKhoZnzXi8AZS63U5wXQ6bN9bhGPdtvSH+ZvO1WZetOgDXmUEXVRTWO18MFs1efknPi0c
wDAPJ9xR0EGJ68f0il3tj5ItalaVI4ZbV6Cami6UnS5ePso3fuumgmlElP7Ug6QLWUbzetrj
gbVTHAXhjdvmdropRQFAeCI8zyWBvvPlO8ugGLVetewrFR/n0BaP8/BdLTBSRMQQs0Qhvgy/
EOXK3dSWYgzGq22+FXyxlOD1lqv8VZwXvru6opVXQN3y6430KREIR7HRAM+OOR0blEfePHFp
8iBBuLZjDThlccbRu2x14YwEeS9+DXpZxglJT6lIkI5GHCQW7tTFw4lGPZOrLl+4DhQObXdJ
njVJDJ/AIUipxiAkQ1+izuFfSK5+kvXcg9le5NdjkKCuQxkWLEVLDbe1tr6tttNTNSYqhDKC
dLlFWvjstaJTzD0Tf314/mHr7ylK/9eLhY37jU0AxM3Oarg4tRdMfbrgAhDBAM17QNnawSGW
evlcRPbCj/n7RieuWzx4mMk6TJIfxuUazcdQnw8TmavuAGrQ+7ZQ1Y6glb7i2gO7b2pWAGxP
XIjLnQOIH0pupIdYPBviuiDMK0AtWBHDHMBRUGSvC6pVtWUzSLdlbe2GYtY9wU2zueqZ6udL
T+CB+V+xSze5NbcXZ7gFBsYof2okMy8DbCWx4eIJjYK51XeG/Q92nGK/GuWYhFUt7UM6loVr
E8pVBoPOBeK1ACkhQgqhdWVdJGvqW4btYwQmHS5hR1mZXn9TUzaj9MgEqWorG95tZ8yFcykO
Wxqfqu6xyC9VfviHPfs/+IQveIzdZ9vV4SuzaaZhiFzTA6PVQznvkaJEU73cUV+NvDpb5yAA
0JSDF0ZyePRHuVTkH/wi5DkB2RgTDjrkTl/OSPdQB/EdO+AyDSKAAjoLx/qzuIDXCEqqAVNW
1nIIe1md9lcwlkvUU2pRS/7hZtH153VS+3V6y5moplBDq9nlGI4DuEoRNyUCGwL6AkXj+zwo
6ImA+43VoaxsS20usjoc4VE0hKnO5K4Vl4KtK2kJtQ4MzMpHvBbJoWvjdglZ7/3f69//pCQe
GXwJMdBD7zTqUU3Z6A1fXrp4uIMGJkYySEAs+bNDOo2bUxOHvvPrz6ha+VNN5aZ5ozHvQ02x
K1U+WmhgsjgqjJdI7laj2eUIrTz49lhoo9UcVSMwB7+Le96D9WtEqZd1UIPGo9d1332KRz2s
8iY9wTYP7bnhC5UzSMsqn8sct2FUGw/UBQ0jUHqspkOyNBQ5Iqdh26AYHkqqDUzenI0EH+Rg
zITTOV15K2r8LqeGgwqmVd82fXcmf8caOoYUvu71P4PLiZw1LIHITW4dkv1ilT21AoiGhsjr
dc/4dNcvtRdFbIQlksJE9ukRxoAmVYpvwGwFt3JiGocZ0Md3TT9smZfI+XwWM1FvdJW23Xt7
y9+uRIXGreSkcTFaUluDNMXYkJ5gRrtAwotbsOijQ2qOu2/EkEoERakuyOz1yu0bnxxDnIan
TBnl+Z2jiEk+kZRSEUTk1jrswL2itUpGk+76HKl6hfRnsKc/IN16epC7Rwi+uQaRjYfcn5Yl
rQKY6OwkbJLq3x3uvzcVgGO/3wLbs2f/4hdTbbs4GDFstrHAPuIOT822/7w6pSAYzlHCwPph
LZxwcpFl2qyE0eNNgm3FUw4cDIsuwux+WPBmfUyUj6yIVmyFuAby7jPdrxs585hgU6EtcqHf
cJ5p4td9+AbrIwKUX3JrqHcRiZMzuSUrm5GJI51HeL3NvY0zfUp/4IX0BxJioIUWm9RoqdiX
5qSItFfTeebdozxqd3/umTS0XZE2SVY1qerzEAiUDuOcfFeR1y/TCj3rt3Qoa+7p9OIuLqc4
uAe2Qa9jUP0th3Dgj97xVX1f/1SBXP+hL3JnnWRhE03FPfegIuiU2eD+oM3AuzBda4L0KVRa
x9metq2zsCoxRTnBlSQr4pgNfbEJiCWsTLT3xct6pX+3Fm9gzanR6NrObLmsnVbDtNa16NQY
khkcm3zN6qSBlGPq12XO+lQm1JGMWyOWLupFpa6dD3VJUBIrhvarzFSmFAFqb+13w//BqP2P
PLx/VDxntkakZyBT3aax8pB+VxewgbCL9UxBMzluLfzJ25jKobmxp3xaJryhApJYPFTgop6X
MUyT57WmPoHHCZoSmlV2zh82GxV5gknJ8F3pfRu2BaXDuTr4oRLKshajBj7uFBT02BNAP3I1
ASZdUJV9HmvysMHwNn+FyNytRt/yW9DtJF7v1aIY1CExRzrdtKsNjvXbIqtH4cOkqZXNoEqb
6NX7K4uniktUojldoT6PtyZxzQL1shRiM54QIb76Uwsj9wwJmlE3WkIPIlAgriz42hRrz4/d
3puqE6ynRKShyQFGXVYVt6TOM9E9u7M3qFCAv00xODbwSS2eaWQjMThJv/F3B+c/w8C01ibk
AlrHwL1v2bV1UoEXu6LbyTqqL2ge4iMGtkBeuXGQkfE5cu94S0LXxvbzbdf7bxGg8sasUBia
ZFQxV7FAXAvKDVC2e/9KnYDXJHX3ZyqEdqGrfQLXvgRMyKjXgzGkuCwZ8qGKoKd4zdWdYPe6
exDDeUyWP5A3pjj4+qzJ8pwBU4N23EzigwgJrfYdZ/1A9XOkZWb6W6CNh6gQQolg2Vn1o66q
vWnc7pJIZ9IxuVX11FysCRXiZvKhterzqUCR7GixI8mmywnHNBg40eCjbrmxlKVtCji+VoKs
J08MwF0CNg5x9FTzMNs1wKtoHtB6WnWQfHuIXYM6GyFPHK6JQIXt9wudN58RRfSuv4p4VcGq
Gx/lKEwNrnpJrQ3Gf7bh9RCeIDiaJim5XhnQGNfKXlp9h7eqYtNchodX0K/pFhYvqk572oVV
eY/A7ej/6vgej2781fFN/en/c3wzX1cevDM0PgwUQ/yxHs7/5PkK9b9ua6NCEfYpDWdSCBvj
8v9hgNPvUCn8d5PrzJGd1zLSYVfmx5eUv7f4OmwCLAc/X6eirLpme4yF16IZbV6Jl50m7MVa
dD4fPs0jtM4a0Z5UCIPX8UH5acpe7wBzrfCXPRZ2rkMk1fUHteiLNVRikeafInQhyqfS8qjf
ULa4dbAToXbZ66O9fuubly4GecmYqhD8IzF+kXwCLamdp3jWvtMRfOP5ytbpMAC/peSjUC9j
C2oZFofmbGrVuGsdYfcw8tL2fz7phs2qNtWNtGGaceE1SA53hzVNNClNXp8DdOUHxsPDWMP7
lzWhPWSXFqtTGpW9nISgW45eg2vU7oLwBqp9+x6Pyf5S6f36barUVhmN26RKyEo9yd+qi4CP
Ly1xJsG2vz30sHbr9UoyyWCmptw/RMiGoRBBXLUnlfG/7LkGqwYUkoZ4XnfWK/V0jyFUfSLB
ThqnphYCc8XzBzXiO/Su0w3Wrh2ikFCDd6T1WikCmPYw19/WqzHyIzsxB56zNSvyyMEuYE56
pe0nsL7M5eRFTYZZfNsD5wtV7a0RAUzXLokcJA96BpvQyhNI9b8HikSsw7ikaIdJ/cTqCX/1
lPN12yFXnxhOY6Vmy4h0Co+sVwhEsNfGGCWGiGAussy3VATmnyXo9xgIWwCh/NWL/26U/2e/
POa9OBZwgIyGmKyLFJBwfiVFCFaqp6YmQ1xmhLLh5Bxc+F7/aMQ1zBUk0jYmlh/GFh9O8fU/
8+EcgNEk8gEXFwK4uO5nn87POXc+zZzNU76aKFnxpgf568Ko2NTET3uOlQhIePa6cH19b0hA
ZeTaSjj1z5VisVuJsPjmcH5bZmd6Adan+oJyIbVHTd6sN/69pwBRYW14naTHLgoBnZip195x
YjzIw4jVBI4OLtY3DjmTG7JXmpvOwwM3+J7vXpeYl5KCj9r2LM5D5EC38YJIbp5gamBz84dY
E/L+XumcE6kmdbQnrRUccFN/uY8AulwxZo9ZGhIIv2oIXRcOTwetXtZPOGJ+bkWWQmB0jNot
c/N0ZIR0eZ7bArRs6jqRyc2pQzT7xxeuKE71zD/QjwH3rGcKkk0iSBPCNy0ntrSKgku+7cy3
/ILisL7k7Kfc7BOIA5vq8UtqkWuSR37z6aohekq3e4ULqiE0uZCZnzhjYo0n94IVejnzHCMe
Xj0I5x/AAr3T/uzvT5b/sKiti3JnygmjkT5TotmDFqu6+hCHFlumn1t1okPXlrqGMHL9B3fm
VG/ej8wMTKPlgmngViH4GNMZYfu2o1er6tNg/zme8UYEqrc8yD7rU/LdYhVqbtNtMrBu5avy
UAtVEcKmtSOYBrOR1H9yDzz7K6qOi5VGzeLfHil4xi1cgjJhjwscpygjBIH7aotk9d1Z+MQs
hHX0sxW9wGwYtPP1463GAkBi+HJbtZchCHGEMF1nKvllzweHB+0l96wubX5fOaRKqTFrbdBF
pj5dgKcO1vo51RkJWJV5EUuuhzJebYFW7lGWZt71V9djenKIdW5R8cEdgiTRDNa5B4NLbVX7
7NeABhY8d/xTQGOi04vu1NxT+0VR5S97uONeNNe4+nvx9dDLqk4mjRDz3QKqaTzEKWF92JPQ
5bLwbxENurLpk0rI2hGz4S7GHhOrvIEIOT8dzct1OU/gQEQDsw2NoFNHFw5R09LSEv0BljIa
eZaX3utJsvlkUNnY5+7t+PsD/duO/nOrzq/XPpor7EEmk5ApwUWlQiOOyqjfkFSjwJISvtN0
Pog5dOLoAKobEmZw4QI1+nPhAlsIIwyngL71UOlka/4IZmVEAxV2UgaL5/UYgVVgzkr1mZK5
UE+aQvH83kDTo7bd7lEWpFdGulMtVkrEQtRZNi4Z00pH6TCWn6ju3KjlApnnqU3XxIKqrihD
GxbabFPiV9uChngVa7JEreT1e0FRQ6mNPYEc7yrbIUtzTjnbcLyowF6vdXZMgG9ESBkuxEwN
A9ryKN+IVlIVjGp/AO7vySDSjithKCWCpbWVVlcXxdGpTofLlgDmp0z6iFbVIUWnSbWvGS0r
DiOONXbGBqocZEl7F5p9TibE+2fYeohyTdH4Usmd0XF37BFkVIGOnMaOtdcsUR66fH9UOFQN
G5p+eqamzHOAuxPJCKSWTpPOEKqQ8WAUx/rLi3r+A3MJLXFXj7k0bsjWi6/2qFl7ZxF9XuMD
+PgJxUnQdalOrgBBDsiycVz76Db1gSCaStNxZfSeItHD8+/ACmr69H+yQo3zOOWiAoqsVSPq
aSp8wnCBAeRbAuGzi3qO93pJP1oxMhw11FTuhFUCQglBSm4YFVkRn+abax13CPs8wqvzAC2c
k6aZna487k23qhhM63kI5k5xUzTGIcOjUowPYoGcZ81xJb3qB7igUpH86LgzMgeLycmWjvlt
M+2/6azIKK8Im/fVU/qwvnORc8cYsdSsDNtcdasmscNFXQyFua7NQ+ptcyZ1EiOhvv56HjXk
JYQA78eWgwuiIJ9wNtBKMXg80Ta19vrokF0ZqqsLXH5k/7fEVgOxcb9/ruZwChX9rE5p3aMb
dq5IqIxOhH3du9BjeAyCVjyqxGEF+Va5Ql3t6fZAZDYPUJmt8CIhh/omWIcUmlYUqoKUn1KX
DObBbtNtxeMpu+c8wK19Tnlg/9ZOJbfMl5HHiY3OaGl7erhQdj7hrT6/KEBSOPRR9xECxN9Y
cgSqIh+0efUXZGJyUsLW1gr85DRKd/vulPdEDAKql48qD4iPjL3wMYzayWwraA0ip4xGG8eu
+nGEDrBuQl7E8v3awZ0vKSy+mKPU9IHHu5aNK6hy7y+HytuTZJNNJ0FmyVITXKvPzDLysPKI
bgshTfWXPTV2Gc+He0slOnVjLK6UkBsvfwHF1mJQG80ymsRdqS5yyPxgMtl9PZ6ca5nZMarJ
B6KyUh+qP+T9eMiVrWjmWeqd66vuT2OUtnAWWI9W45+h3OP1KV80U+DiEzJFE8ipRrCwlQhL
Xp/JrzosYe+pWoVf2bz8PtQ2XxUWE4/M9at1hD/E5kAHffAU3E+KTohQXWJttRZ7rXLwQ2SI
x6lmcJr1wSFjMjZIiyS7R3z3H865/0DGhIqVi/uHSEtz8RGEawt7KdQeJZrw+bfEiJ+G8sXL
915Wz77rp3w/uD6a0mjs+SECEyRIFvFqec2pdfY4/sq+VpFj9XZJaKfYL7TxiJCq2WwI3j6i
/RitspOU8+9jXw/IVdx31c3de2YGoOr+BsviCvgkxFC1pd+XSfSiTVOX7reIvCv4k3BKySRo
mke1SxKNFtu8L+//lBdhCCB7+F2Xz9wW0L7a/L4o4k6UoylcYO2SjccEuJR258Gc8qZDWgCN
aZJVkdVLV4npiwBzKl0DC12c2x86JsCqEcQVwQq5cbsCqrGAJid6/2tSRJiOOQObBIvgeegu
AKVE01yvHcfCYS9kOZy95NR2aL0GpR/OLoJin1Cjn27ys0LtZ+rjodjEVCSmXlD2KSniEhD3
d/J2qD/G8ca+1qXmecXjCXV0XWI0Ljy/Y8HFiSb72aGReqQ/a9AjXsmRyc0FPXgQlI1/HGp4
oE+X4Gsle8wT2PQdlX71D0f5N57wz4TB/p9Lj3Q0t3TXmG2S68N1IZO5ej3ybOtjm/fg69Jn
+RR4Y+5KtOZes9iyCVg65+ZNQJIwq2T3x9CNpgHd9PGZuna96Xf5tK/vbvkbD7FlV0ydu18X
WQCipksiZ/vOy7r46WlhhwI9XOdD0LAyXB29YcQMSv2JRQER6lDouBv1vOIixcPnp7MH4yIE
ShBMy2yuP+hn2SXPPLVIhbE7q1bD2X1BxMAlyaVeOCBpaZ6ejD6Yg0MSoxEOcT8eQhBXb0/2
g2sgfN3gRFSFs8rokGr1E7CLKDYkOGztDdzYMTtuaUaeXxmjGaGR6rJCCjMWmohSSTVgg4yx
zcBkacfC41GqIwUJhrUVNQyheqrB5GbaigfxGIPibcRU+/LB5IXa2b1vNlLNp47FFDzvgnBP
RbhTM6x2qqbnorruF703r4igFN+MhS1oBnIF5KSkahzppTr2aSsxandD8ZDD3FWmxmm3mV4T
6JGICrbBWA7bMJRPsGov0W+W2+mSvCbnWsNCmUBmRNXyzItJGLaIeBRwCvDx01VKn0SSJnlz
6LfbxMhu0Uf4DFvPqccFP+u+2aO6yk9V2b0sFf2zOGfCAvIuVSn9XgtYqbBnaM0/I82LvnTB
VHtnWmfHmpBwKraWbUpuzngI2BhvMkjGjkug+R6sK6BiC5giU09+UmmG55FPtIagXTlTSd2c
M29x6fobGqBzblQ0dltaQNLo44x5v+0LThYaBUqeHFUvxQXXAQqlMD9/X38ArhLrhuDhbN2I
KcUTdyP+n0n13/zvUVN3Pi8C4UE85cNXgucFZYsgsTnIebbsAjNiT/1Wlcl2+XRNeIF9drey
J8UfWEKLI0b4FAcGXiNFD+y10/2apDTl4njZ6HDK0vmYidQnqCQRT9q+N7wUkAKlytns/KDb
PTGn0mGSiG4PdEev3GlZx2qV3O6r6AEWHAKCSxTu48ELSdumLSVASSRZlmLsQd0yBnu04VTo
09NNh0IpW8NLp/RaI+e7/xBaobfK6IaWzfavzCSvB5Jsk3FP94aaHnVvQkQR5a+zQ+a99jUU
13qxVz0zOU602bz+wE3fS/DwhsQVXhPcpdhvqcr73TtAof36B6N8SzQnHlFW7uKTEHPC2mAr
I0w1N6xqNEK+YmyCdVvsMAcZc0qAE4CKTLzVZpJ09DczeSyNcaojBKbQUX3ceKPSp9eYBmI6
G4JQRDx112V4c/AHryNHixWNPTJNKmepuESUrbxD7BX92RwovEeVdbsuDWIImko5JZDivG84
EZSlVRcREaGS6luanVd/B9kKLfIbTIFDn9gjMLc37kXVqqbkk0ZsiXkPkvI/WRwGxuwAnU8W
B1wD58IBEEs+AKDFD7FaN556Kc8UfidloQzT0gIU/Xv16sWUSIIjh/AC71X2gCICvvyiU4NN
DTiFWN5p5js8TrAqz+ZlZw4XxZOpEDmfhGiyHlJDQRXnmw87fNWs73Z6L68GfgZvNY09d+H1
b5yb/9w6u3cT4toDKL07gw1UJj/lOXERev4U5IhQMoDuT7dQvtxV7ZQyqWpHTTtuoLZiAOPj
bLa0pL4fir++qQ+k9+gFWrBggmghxKgblPbzTReIixyP6eZ6nQSQrOJLBqRShgrumGB0Raeb
m/YFmxfk4BOc+ury3I1dQIwZt9DhlGIJWerRkNctSkn/TDuDu6XA4K7BHTYPkbdC+eV5zgv9
GKHbLC663QZ9tzbnBC9ih9FVldOgJkfOrLzpITT2Cz0RnF23uT1sZVcAT87GWef6vbxQC9T/
Lo4puMLBV79H12ie0vbNy6EWf1uXmMGj48lMqu1Mkshw1RDUe1nfmzld0QWqwHDQ/UloNYQv
1Am1A47WtNbgS7wdAeittfx7n9CcnqMPY9zwZoltwv5yQY5IruijX+BPLWivKlTJn7N7kIir
6Vfqvx/zobwlcte8TQMfpwVAO+kTmrxKpqlWDZRmIkHfpVvo3GtUHKG105p3P58XklClSYS1
rCI/PxiRVNzq1fBrcg/8Nw72bzvtP+B5/l8fYL3XaUFGBaDpIrmEttkBKvp6HZCpmPa1Q3UG
2BuQVV+XovVumkyYutWZhFMQI60NAAHOjIpQVKp6VWdrqHZGd7KCfShD4C3uymuUJaUhp/Bh
xgJHpoHI2dHGWU3+5LNoNXvHb8UN2x63hGLSGD1BpqDCs9JKNJ1nGiC8/6gf9eUdJ3WBc31M
K21Rz+k9pyBATu/UcIouV7T8Wnf35/f9zkUphA+Up2006FzgOy7EA5tOiNCW3H0W1ZS83ep3
0yF0SGNxzlpVHQ3NyihIDU+glCiNYzaO2Y3M/KkblAonrAo0A4MB6fQ0a6+i5E8AFZPiiR+c
L8Qbx069nzw/dS/3e2hQnCsnuWKGRMTHk5evGzsBTyzn5vTnnvumSiOFdV2qeeDSlbiOEiiB
Y7AAxRra86SnJPSoz0cSsJruw41BbC18HARS1RY/C6BIroOd9whHoqymsg5o4YdPLAgA7qjx
zv6rlCGrstxqQExDh6ZYbmqmBDnWU+Dd3qdhZew/nelijN79SkjePCkPT+1jZOejd9alD5tF
FfgxV8hPDauDJdqv4PaiS14fo9r7dHtkCeH9iRk+NWaSV0QDa3n3zJ33bhYJFb/sObJ8Gx8N
3WeqVwDbORa4VQ+6aU8z7gkAEBXExYbecCqmQXcyxFHTl+nCJez6f4TagubXukTLF3UKThHt
T3tkHuPkNRkztQPYjv7DnQS/4WUj2F2IuZOLqn0dcSktmRFnAWEhNrzTynzZagIBAw9I3085
ArpGtGu5wW2T1omuv1JVToTEboxORK5JOf8c9sueu5KiKmDrzv8tZ4oOH7AAlm60xOdC+KXr
I4CBVewALZk1owBqlSFDeDLux0vc/2tu/v/8j6o3scGk+yEcPodOdWBPAzy0W7d4dbJLnHMH
pa9Nljy1UhV2xTtlFyr5eddZEWu8594A9iPVPnMp/pmzMrY04DTPQ6PCKfsIDaWOTqD1LRsf
fVPBl5Ijin3Gn4BJkJi4bziAeIrtF+ho8xwcutODpHb2/nCQV+CmdyslvA9XHZOVZ+QUBLcr
eAAXYObB1zFnsJhsKWlyw2jIdnCGslNWRYBzMb2wwv6Ox9tsLKKOqtg0fSY+oVLmlz3v6lxD
MXtDd0DjjG4OrsKnC2+1USQAtibO7gM+ISD2ZTfJZAnZf6R2E2cbs2XnBbFfyPkkfkvrM8ev
NBOGKeEMxfnAeuKqezOPGwI4DxCkdtX666Xi7N2f47xTwo301MMSofgykYOwwfCsC3TnSq7v
JQn0D1upYd6E2p3gW2EMaNE4kmD6h1mTCojcTv0t1x7rM1ZWp16wLD0qeK6cN7l3QmE4q3la
Argo14pb9ji5ahx/Kay28nH+QJDCDCWPvBGGd9i63c5ZniVYh7dWggb07B68X4kdv46v6OnS
SC0RZG/O3jE6RPmpRfLEa87Q+st9o8L0pDgtIL0bATJdYF4bj5f38Mal3XOQ9ER0rm3eVDwV
vBozsf8iIYhTNsR70ri+OIsSAGWyrGlPN+DRMxHalJf/JDQECwkEEsOW4WvpgPBP3WH+liZp
LUeRWDx+F8bc/9QbhqwHH6dG3I2zYIdXMILOG9R3yysW7/6oC7gdenrAwi6VzXjTUoMNwhk5
B/GdHeKcJ6XP/b6J+/uzSQ76xIZdfQS7UH0cdmlUb5Bn4u+rPllN9BthG87bgLkzopPVaFaZ
02m0+k6XZbfJjdkck5klW5qitM63eHq4/nUSpHB3584h6catwTum4GpMQeLbtLmqW545eH6Q
8ehMn94azqg1EoohJ6+HAnsGvutVno7GQVB1s4S3unnPBrOziZMvtgscRRQjjq37KoPhcL9t
AfS8cWlJ+fxk5sPWx/NnenUWr7/mbTmaWHX4+02HQuG9w6IdPqvhqHb6XvGByc+FjeDom0sP
InpkFXUFAtMa3TFWgg07GtQQymr9Vs+ta3qduTbFKD7lXVNTj0U1oborKmKDq50SHFDpgi1N
5nxM8aiUZJB29Nw0ze9UkuUbb1pA8xZGNe1ZawOwtRGcgRQ789gztYeEr7YuLUfVzRCMhTpR
C1sAKFwcH041cKLIPgRjTelD8e990vLa13U8DxiUBC9K+/kNN2fnHb+uZJVfToxQhS8BgeTo
XwPJFCwWm+yfH+epMM8tsnCxbQDK3LBB6pbvZS7+vtH+x2f/Ezlz/+Ci0i7W33youxoR7MI2
OD8NlD1imKbqGO2iS18Fx5GWlyiILWLYHeVE1AsgIxW4F30OiBNuQcp+uObBOmX5LLgXgrDI
8soI0l7dSnUolsFoVX/MlvpTzgdeRj5dxXXRoxFFzMkhdI9x/GolGRcMZUVIKWWyueVyQnlL
W4Hd2nu0xBxDAsfT5xQq72f0ojTD55DJaZrJ23ZtxIH8x4+Vlz5tOO17xNlSniZVMVHS5y+Q
n8btVEyGepzXlmifr2CILl2dFRw1rcgF8CHZunLn6b7nV5UHekDbbNQU4odjJghb+O0QflWv
5/qjCyZFmPCgP0NUarfSfUEdl64Gx5/cZHwoBXLy9AODDVVT7tRxA3NpIn1b8uYlu4nIt1O4
z3Mqp/Yt9MvuXL0TCNXAaIfjL7F3ozDPGo3qeJdHcPJGXF373IKDYomAinZO9vK5rQbxmv3u
Z242YcoQFU/GWsfyFcqSJBe3iXlDz06YFddXtep9OVPLW3GYy+YIhKJuSEPTgEWMwGlzqjUJ
n36BX3lqgEKqBXggUb5d91/2NDSuPHnBBl/gdvdyJj9ZBK6fBM0PVtzHM+bATHB2EvUV2SeB
l7tavpEjOTEAUC1IdnOxrZ7H2MoP7iu7mFT1O6r+/CRVTmSLgb7UDsFQclx7ePpPLaDaa0KR
VhHomzc/QDxMPXdP+OBz+JbS/GwIpuFcXfBxZ9XVftvKj4QwVH84y8u6p9FsNJRAI7qbx7+T
xEbeL+pBtYUnEloco9LExeurbfBUeOUw2Zt8kHqIQDo16CyXkHqcHL+TykNcKxz+zvcZGgW9
NmQvzmu6Koc1U5hNFg7rX+4NC9xE+LH3lN+5MDChdg2vzZg0veEs98ue58HIEKf2cMKl+dEV
SOeBqI6QkRWVt5J+nRUXeJqghOkiss9cOEi6OhogY9zgW6GYpIwAaa866hF9550G+k+uz98a
nXAZbW2vQ1lZCfvl7bm/97H7D+6Zv3F4P7PXVEPwAdj49kpwbMbjHMZveZJk11z2AMSZm7HR
vPW4RzRGpUogCVOsH/lxkDhOmL+sJbAv0LsW2eDfWOhHRsPsd7FVY+NO7XDC82OOxF5GhlAJ
iAAub4gSkXTrbTm73leBEh13scvaG/BsgTtF43VRUMuoQlWZA0qrlUep7dqdgydJyZZGFU9A
ZcTIMJMEOcMi3M/UgCtv8SlNrF8hK37uc2FvUo9BLBIeeLJN6H1t/nYaZ53oRtBo0ruDp/Qr
vdpzy15P/JgbtzJSubYkGrJKX207hty8dHluB05+88TWuY6sW1O7NTUd8G1nR1cSEH8tX9+8
cQwTfX0o5Px0bhigO30Hn+DldxkQfhGcn7377dYwpDI6ynPI5VDyFhJrj1st16WWcJw6UcyO
pgHLg5TtKXq8d4HF/seSYpOdsK2nGfgxLmVqrViJaWzfcrTDOP1FHl6bllbQVfkCLkJR/TiV
fBJIbBQ3b0/bs7Eb2f3M0o0kPwfTG0WWgbvZvDvDVF+0pDonPAf7WLU+7wO7EPyVuEFvMWhI
vmHH9FW0QtYxtojtaAvZ/ul+04ct44jQUs+UZXG6auATUO75uvwUvHV4G2Bj6HhRepQfx7q2
LAx9Sp2r8jeah5VPYwVarw6OXZkOTbbd0guO6xBQ/UHpfXrs1Cgnmtf1KJv4JL0DWT0WWcFu
o8aVZ8KUtZuGUNWIj2MtLJqbMavhoAgemTjeb0MC05y+FnjeJ8Qbz5qLOzQA+EpPEOjyXaiH
Ihh+uX7B5taNRTUnekSt/SqmDJdjs7b7YWdrRnKRrBR9Zrs8EPSnNxOMRz9x4L4EPWjdy0qo
A6PIlyBkeu2eg1kp3xZaUYLylNEhgeZeDX51Rt995wFUpfTYnjsK+xsz9+83/74Qg/RVt77a
eGkZmj2M83J1/mrYEHUzeroGnr02CZQS7b25XmLFx4WcjX3XH/s9V3E0t9HQLiPHvO5d4Q4V
/EUYsnTTcujdWe/VuX/peMSnu+lx2dH1c8RmQ9ttFb0hkCWrzvAJUvBup/vSd6YlMBVmRoA6
46iZFP6Gl8gAm1kRHH1+JntNu7I1DwmEUf41eJ8/udBQPGk3x+NdGca1Imzfl3PkGXWjncti
+1aDk0VafMFXmw9Js1269mkSqhNH41TTH4IM8f3yCcFBp1RT4od69hBMAq6kR64jPxWCrTjy
zNa1Uop1PPqWykpY82AFHSpSc/iZIvvW6qVRENISNqqmghxKQ7duPU174dNbli0SRwe1Ca3o
dYVD0582uN90miRHqOkgF3ZWKHAelh0CyfGTU5jfCSV6u+FSpoFS6hlRe+HbXEIPeT/JMLjS
N4jokdpAihXO292KDiwZAnoxzqSPxfU0/FTQKPG5/P5lqI2LnUneg2AFjoFqUoouW1Z2aX//
3x/Vf/Lof74F8u++SJShUYW+M/52rxEfRghgK5azYU6de4rF3fsWDSPWdwNjDKqN4buxYqSg
mT48L3yn1djtdOFbFj4QQLMc0UreLa5bnGd12pKl/qUycnaceMemLWFPpIW3vlNpePhi0xIy
/TX+VQM03DTDobXw6Phol8SEpFdmqBaQ8a0WOBhgMTa8MHZ5gG1cjcXZjARnuLJFseho0IDW
4/QU2CuIU4i3+hJI4C1gfu1UCaCn7rqg6DYgeW98VbYlQhAD0BjCV7dDsrEJzeOS+z/S33eT
lxxNDWtZhXFG/MECqj3VoGBz78is19FoASFg0lpt9cSnLK/3IvdkiXLdfSxzurirlcqxK2iB
H/epUU2pCghSIOIW/GRKJTeWahqMVoKTHZhpfok5NaqtaX7qGgmRbc+PpVd/SCioOB/QC7vw
oQ7O/mVP8sJZJfSuEDlgebYwu3HFt4U59IdhIklslXCFsn0iR1qqCby5O9CbQINpj6pKmezI
Pp9gxtOmGVTr24c8g8vgqcYerT2xT1tTMYH5aPNVF9VVtkrTRQykcesnoSQjI4sc+0PbMqbN
Sxh+G4vJKwAeSTtAWrC1sp6leYmiad9h50lA3excGXFiee25ymNMSdyKn41tk4XPJ5HtI9pT
i9XPVdsyOYgCgTl6YskC3Lu9+5hGKWGvE432Ed/MqTCHvrS56RtiOTTE3FGYj97p3jkprogq
ncQLrIgD27oUkMDD7edhof9rK6FOBelESEscb0SmtRMX0Fs36bcu0SFZ7MM3z6VRSpPECXq5
XjNrcekTlOCFMdejjumUOhsbrwkMIGtaglqTeD/bfra+2k32/Hzenlm4J3igZn4rC1aTQBr0
qD+IlavA6YtbUNSHsEs1IFZG8cEpAf2ylbZ5XzjFqIUPZCsemyEOpkQyzf0mxJH7eWzztuVk
nOwFd+qKI0BtKVDgeNHD6e7alqDyuCfjLeCFk8FfFADGENoEHf+w4d7s9dmcd7QBkY9SpcfW
Th3Rid/6A8ojwUXGvs680Ywf87YoXq1HyeQFVk23C3Xp2kjEcPvkz7ImFxIHa9d3qwrGExI/
O+rLMMsvGbcBN92MCVYBwvnwOHPrh+F7+cW5u24LkGO8SZeHmRBorrppesEQRv/s0Winsaw/
iG8nf9hofmWoDrBc1g+c7v6V5SLyFVnhCmTNPKvs3iWvxp6dg6xvaku/CDA9dIpUtjwvEE0v
wlKaPv7miPS/u5//4qWKZVqAfXNyPg0q02KPh/vgcdSTi3Uy2ov0b5ILoMnKnr/yXKqxCNIg
FJC8p7yYwB6YH5tcOd58GF09U7QgYk8TQFoNR6018x1dDSyYQ8CvhyJmPXEyU4vwy5ZHruKa
wLWlOR2TikFQ3i977Oje9kNlRLJWXHrpidQxGIHTbe5JICSUCQUeZByKEOavOSGdl8UJ+PHw
7ZyaVsvtyqHWCkopI6Gm5rJWAbRcX5Mb6TDqNdTwnFFkYHS5hL7Qf1vqQnRFgE4tQNJN5F+r
rAqqMHTEg3zcWHxpbCmgl36LjMuJUx+OlZu3s41BonfSuG8uz8aHRwZD0be36/0nPLfKC/pt
U5quhOkAKJvlrfFZTstW4tPyq4bzsV6DkO5hjdMn8cYAFPcmDexzLsaw5tyUuCbnSeYTWdGG
Nol/jLlQy+cA6hp27SNROVsEQDkZN+zftf81x/xNRGKpi0FyZo3RIM5mdBqjhRXA3Q5+rU+A
Wm5CdSrTjZ2xtt6pyPqhJ1wcKqgtFzC+BmePsrznqGYxcSH861BgxyWVXdvlGbXt7N9yWW0B
2wsstY8bVXq6TGCc6c2CCPei5N1JVhDmvbxQ5oVFLrmt6z3lh67UJvjm0zqWJmgHCoqe+EF7
XB93RBieX2H/wLPGZHxzlAb9thpO/mVPuXfyXZRZvC5lspNiK7/o9jhIG2fVycNeSSoZTmrP
bbosFfgiMgZ4fjjjtbvSMl4AaMbOvlmC37oy5H7x2+myLiGvFkVPghkw6qztTcSHJZnsHVbp
qOb8PY8ZL8AFnPWNarpR63CFlt36HnHTJi7Km8SX18h73+9IwuSK02+9On92t2HI5AOe6SMf
5Q9Vo0mF4SOvfjxCUDdO11nar13lH0Z4Ww3AX3xfunL17QqvrVKbXKw9RlWrncSWTD+llIQW
P08grjm8/4XTqYFI2wsnNJnd2TtRO+1lNqyF6Jm7kAZpJ9WrSI4RuyT8lz0kkS0Im6sYHlEy
JrblSu5Xt0ycyoz7oqSXT7rTppGcjCesFR6JsmEUxUE8cqTCihZXboQ2aJFISJPhD9Ml04Fv
2Wfdk9aLUm7ISxmxHWyNWoDMNHWru5i7f3FT/Z6G354gv3+ZUFaUU9lQlBuYvmJoVXRSoTM2
wqoTdxQx3DwUFzHAdfO3AumQo8V8BMRFbUX23/aIPGLP/bpHpNzsLciqAErAgT0iH3xZ4U4j
51ZraoTqPARAihySp5l/FFoGrwQkxu3niHUMHdbe9dUR3SEu0OotSF50USngB951D53oc8kt
eGPnaDLQgwT11YX7n/VuZeuNj3OxfrTrisEkVwZpvMjqtUdIegig0T62Bi01AmmEGXrR/dH9
2NqwylHOVLqAWAwm2cesayffjZix/D5iuO0wIVqj+K0uG1jRIAbRphGzCi+X1S125CMnBXgA
Ky/iNRsKbe6vhXSnNL4N6hdCaRtp1WtrpyPXq3pJ5yOWb+OCQjctkFOjDYfmaszV7xQf7GJ8
Rh6kGuexQYE9L8NqO3ytKvv9NAKGRaqL+n3Mmeh2NxZRWb3yGKw/fImmKC7w1FfXcyIBvHtw
Lm2GNKA4duuO/QNL00r4ouR7iXXop1qlhcwiP19+FakGgpxOIeCQN+Vf/p6R/q3nqvfnq5Y1
Ij9WnUOXfL9tPSBxUrvCUwz1jfVCHNXYdYN0VDiHI+ImJJFseGmlpSzXP1DoymIh79ZYF5sy
o8VVzT4iu4Dll9Z2iFzRnM8j+tBj1sQNzONh4+E++pEE2nFcx+ud403B9AoM4MqiDK0z720Z
xvUneGwb7676J+jsX/XfrNyt2wjeme7adTv8NXN0cqp7zGvXcqiNXRx2E55LikIG1sF8UfXl
lI5cX6xianvsN8KRpfXFzUav7Y+dLIBHQ93qH6laLzbcdFf7T/lOUqyJLKLmuROOY02dI/Ub
A572FpcFHvWgDPSk3gFIfmMsDeasOEoQ8UvewAMYMLD1JbB3zOp994u/tc9/z3nSR7YdYKWL
E34eNNX0/jMpTdOW4K8T46w5o4EcpN4QM3m1zS7HdyrhFf7SlYDl5k63MjRHCadvadhJFUev
PZXqaPKocHjQ2T6+knmYnE39ZCiLdq6GfMfbPUKWvle6fKS9qUzuuCUt1BzIiJnu02FIOK5r
UgZP2Psz4oh13pTX1EgOVKzbSvTEW80GdiRhf1BFOl0ptK9qaa2UmwQgOCSNF4DW8faD172o
r5YReXJfcE3m2BKJ2ZYwCrnzIfeNw3jk9QkPcUelxxDfuVpuuigNui8Q++ptjuTG9M1Ip4mm
Uty1MMNkt6mB5ZwY+Z0uj0ujAas2I6ffAQtpiGBgZR5VfEhpfdH3rssF2hEjSRZ6ht817k4S
m9Y/NA3a9DPBkWUe7j7KqV0Xmxq66aG9XQKYahEml8YnI62GjWy2WZP7v6KBGE/fV3lIsoKk
TMsiHcbEpbjsbbeRXQeJalmVCSOhutrd8q8qAUeeRxmuBPpqtgfnm78T7ji5twNbAbfS9ixF
NHwd8SRZzsTIi5jH23pEg1vszoBPlkSYQ1c6UyPe+D0gb4aJkdF6WbKS7ZQAAJCIxktbKcSJ
F/XGd/xHPwRLcgBtaa8LsWMfFmKDYYf6QvklPW6gkocQZxFYcfwEvbukVwduv6p5hPwCewwY
lwtQ4qZlZrv0sXnQ8wbjsKDugcnzvYzi3nrjhuIJ0tBeJripxEwVpbtyKY3HTXtjf+MOX2B1
ZTEoNQe468734XFA8NZ8HZGuXfh6vCTbu6jhDxhc0wYzoPmXPXgPZtXEcu1lkN7KFOvRPbUe
/i0BuUnNiXjurBMioeO6tKAQb7nkviVj6e+EIPZ8yhB+iD254MJRLGzQSvFLj+Ba0eqKu7Zr
kmS6NSGqsWGEJe8xGZArGlrfB/x8wIJd8I0Km7IAYDl8CUIHkM7d1xItOfpHqxBMddzQdeHE
2XnPX/as5Oq+E62ZPlORfNqTIq2iAx71Y+iXu7Zz7shwVIJiS/EWkOqY6z5Ut8xSjMPH8MG5
6107xuvvRqYOEYu5xY69WrinEQEL+wda50IZShYo6vcWCiLSOLGLtA7vPQpVA/ZAZWeEs037
hdTC4Secqp712z+gFFBj8JQE6ET/1ao509MdmAXLBxREpdsLNcIyKw3atzBbvCNzieUEmy0C
JWRO56yNodZ+2XNR+nQTpX6yNLWxigMGdbFpFqz22T9Kv0jrVw6G8jj5DbP1NPppii5fQl59
0FvdJ3lkjBRD95va0jdpn8A6n8nsFNZvf07clX0jFNn3ebUQF/h3o3XFryYWEtxGAj6b2eK5
G3/SUz4WVTVRmeA6QpLT2uKf/ROQD3MXeWbuegefvRVwdKNMHu2MD2SrJV4E0e2qMrFz0in0
oQqLzTsXQqJeTFybX6O82vg5QFD1zWuAtfPO6pDKTYo9ldcRyL9YI94yTga4RA/oAeVHNaNB
WMMY7tbOUTqfcnLBY3aiPY1VzOc9He6/rUjXvIOsEAeM4+lFwx4CeiVvMOHHZGnfdGJjBmcV
drV3ektIxW3q7s8tJPCxkJnRtlDQLq+XfvpuOJvzdUbZ6lKqOi4hNAjX/qYTQYCqc3YUlXWK
5+q7qzYNbqolFGHf4dYANkqNOWP5orWtWob1/NQve/yjsON3MSnW6gmDrN2uObX2vRInV0fb
4MIehtnGWl+1WvRnJ1ajLowH0X8eq7dEb8mUqUV/caJXrDeOodur3sFYqV3DUtNlrqCehNtD
i7GoAAY+gLG0Zzy9ePsJZHps8snSR3/G0klJejHsJ6dibIPpjpPhThKouJR+2hDAuQjldolZ
uy1q9CLddugaBgCxzQ4mzN/b3FLnZyYECI/uVmTtvvvTrH67Q8KExAZwvABFrWrpLrEyYIVY
xvfQZ2Nx85eWrC5fOF3CZjA1R18zcaOXGNBr8MtAd8yBN2q7NndPnoBE6Y+jsE6q55p01a7h
KOkySlsF4Yb2PWHcFgn3ANE64osTchzFjCsBtUvdIN2acqetk2q/tbtafVy7bWdyUmLYyP/D
3puHNZWs6+JB2ma3A7SNSqtAeku3KCiKTDIk0VakuwVpGiLKqKAg8xBmSKLSCogQbUVmoqCE
MUgDhikEBUSZYgxhSggyBgIhQBICIQm37H32uXfvPvfs4e7ffp7fc8xfqVpfrVrrW1VffVX1
1ftSInJrSjEuF0OQjDP36tHq7m9K2cwYwmS70g70OVMogdZmLSHz6orkzgDHndvy5hD0ZKur
E6WcWTfykKVYHlnq/c1zeULU/GZAYrOEPXQEwOFXuGQPSbZ6RrhKujfVynf8CGxvZc7jQdnZ
V2uUdYhJPhM36gag/zWuRv9UJcl7NxZoJWXfvwl92XUtHMzH/s92Cqh0yiYjtIREaMgPxXKm
Nb1AZnyiv66P8nBaduZWzg+ls5VHtGQ6J3rJffRrYfLHL8FpM/d++k1bFuWr6cvh9aNbYbIz
L1xHUUNLmRnV6Dd3oy+4Bi/baMgsO+dJkUNL9aJsbGj38aXDoq72wqYBVqVLnRXJTXBbe+LO
rrVHoxXEABT06RLF2pZk3k+RfAJel3iuHFG0xEiy6g/sKFnLuKt8y8oFxnHE/rQkzmcuNxZS
Iih1XgoTk6L6MRFadvKFK957aGkw0xE+8U5lswHgkWUwRhRvSY9W2dbEbv6xAXHwyjvlcjSw
XURze2C7rBrOAtvlMqN0FrA7N/kT5QRSVAggv4mrk+90iO/snFXq2XnK9t7rwQzyB/IbFKyp
Z/L4AkryDFWTqcrFaM2ch61DhOiGeBglrOZHi0xuCtWltXWRSucF5EJXvzJLl2Si2u5pEEPG
j5rLTicX2knVryq1EaNWl1k0uXgRGzPZhsH9eJGZKhf/UgORNrTJC7Ifmg+wLWLIY+uQtzqM
Q3F5p79Sf+CrYYOaXqBldy1bGsxZdr9wQb8NYQ2hfxD9MNZzbmTqJymgNnviOdsETfVLbV6T
h6c+ji3ET/eoh9jr6ApfPb6PSZWvQx7WQVZq6Ki8Qz/UkS0+Y+gQKRYMLLI5v1gsjd72Fd/u
HT+v9MFK8fsrdlBmoM1ebd6k4jDdzBpVCpZRnNVO0WMlnrrBY0imWGd24/cJNFL2nYwkcjHg
xValVMZeoMCaWjQfxURIwJaQK4w7YnGIBGc4EcHS0KXvYLLDANOefyqOOSZ/1QqWhp4Ljpqj
0xrQL+wvCU1ZNa1xb6cMrD8s6zBN9GSsrBMzg9NXNGZyUr2lw/KYLGP3ynlrDua4g8T9lOYu
p8TVmnYbahqcWhzWGIcBgz+y2eE8WXU1KF+L0Wg9hhxcjnvotpHSkPwjDG1eoHJgxTGu8Cxn
7NxjMGlMcVfOwraN2QGy0Aj8O/dfyvYnvhmQTGGDvLWCJ+kjYrNppSrvp6S9ffkWLl8Q59qr
3CYZ65B9Dsd10FoE6j6zbwzpCZ3zQ3XbJTDHyV8J40v9OvOb8Gr32Q5HxvZSDzUagoU914qE
yJWICc15XCfpMDOmQvN6c5PmTFokf0TF/9IFEObBcrp27ktz70CfsDYzrxF6yF7YNs8vhmtx
lYlKBdOC44h/mdP6920TbH8OmIQ3r6C8joJDbujK5wFIWD7Z07G9JQnva1EeJsYDnJ1o0cGJ
issjDQnpr8pgjjrD8P2kgotXvOnudTaz56ao2PkXF8V4Z/gffAbEBZeC02P86hyQhrTdaSxX
47Ye+sztaaIsRHVGwOTzWsE5ALfncQG9xOUB9a8H67cmJd1u8mG/6SW214AAhXMHcKlJG1NY
rt9FT4ydvtKttTnZLFW7e7d05xFj+f2UlNDMDMlm5FANF3h9wwArR7B/cq3o8JH0ovb+CBM1
kpFhRF3gPJec7tuOpxkO9+oWsqTIDVP+PTgXdqB/bLSZbI+JT1QJTiPF8UJ2fzGBkuehf4id
702qHMdhFDDPg052bY6cmwhRylBPXo5DEDyuDm01LlnEfohRCPlzjMK3S6ia6ZLcWKth56YS
AiX5fL9uzah475H89uwRPnz6cE/PpFJadzzXd5kEiTA2kgL4nvTY01X30wJjI/hqfHtX9gdQ
VT1G8k79AHtcitdwqYOV79X8jMLfMFWPm/4jc5F/RHbjtsYVjRduWr7Vs43fvpe/Gd6dttMH
HMm9wFzJJM3UqBpst+x8zi05kJSZkSprFPDiX8jDlc9RJhgvKQsmwEJ6KAmKQmtAdyDuAEwu
9ZFrnyNyT6ZVrBoFV0i30ikD16Vc9XLsm9Kb2PeBufJWFc6Pk35yGxfddYhiGH/5K6xZgq77
ku+o+8oeArZScbXX1Gkdct8RxJQ3D5vLEqE9jzv6pVm1jvJPZ0bmjv9Lq15eTlBY0WjheeW2
Pas1qIzoK7esL6PjnwSwLCwSSY40e7VDzoVE+lw75t2m6X9Epf9PstA0exu70ZK9HugkJaf5
tKcjMnebtroPXD2ICEAh6l+enQ6I+YacjOYBL/iRQ0ixj9L99Bc927zFoshNyxhbrG3a20W/
tWrFlq5J3MPu07FcdXIwfR+6gWm7gdJwVePCpHlakgBrbruJ8puGzcSm8MnTfFoos+WYZLgc
DNvPldPmfzC1ei2Buzz/JFKSotwGfVGoMDWxpPqmxxGr29lDI1BEFr7AU/+0SOl+Gj35F/8e
ufO1GEsw7BV7ew3JN04rpaGecvaS/LK47131DUTm9x0L4d91zKncrndeOqCvr66c5YXOYA0B
GvQyDb9c3eg9FdNRJ9Ks+uZt7JcmvjNLj/kx9HvU9LGAEidJdxt+NfC1maPku1D3SBGMUFsm
86LcQ7zMVMq9RxPcZw5L8+ACQHpoQgRe3iYWmEFPd3YEyOVngkOgUHnQ+Tb8qMdrMwOafRow
DjLYWBmW72q++geEdj5BF6zPUlaKVeciGYYzgIJdaSN6e7Q3/tEYQrVgpIfOkW1RVzMDsS6I
4hBEYq8s4vSWdUjBcbN+s2+CNQHdT5+MMEu2clw88oEjh6WO742iNhZJ5lycmiaBB8ZOtDDE
9x6brSuSyA5rVtQ5KBbEPmb3lMpVuvSqrPp5a0h054Jyyvytelf3BcyVX4HYUxt31FEFRt4t
eL+h+zLg78YrCrdgl/OB54qQrkAfeQICQDVZEiAsfdHieNKiNnMBZerlOcCvKkTQge960tVW
1Ng5BiiAfHHC5hAGIJWTBR09b8DnOY3LDqqHhx1jYcunzG3wWH/A/3MXCMyGY0gZufvQsrpQ
xDsFcAfypIR9yfCCeFk2ID8GSsBGEOVgXo7HniRDX8WPxUBDFEWNcUwBf5o0vtIcRz0p37um
Hs28D8jVD69DRpRahcfHbCvbA2pk3NfrkEYV6luwSFDZ7lopm/3PdNByGBPKbsStNWNuqKhi
qwoH5KIJLFtpLuzEmHtVu2vVf8gWTV8HXkHqmt8a/d46JApqB3z8xDyqZsRE7JDlOmQN8G8m
MNchIsB2s8i/SuKsNKPpb8VxmIaMrZtgvE3CdchuMLvQ4EP7UZsLrMikeeri+wnC474ZfP6U
9g+42AAWXngt1P7teLC8IYNnBuNVAi6cJ/G/5N0aos7W3X+Ji/V1RMxcBEUKCyTzXvoF7CEj
W8lF0wDh0deZMpPM2bD25YajvoAf/Voo5jpO3vv7TwbnhR2t2oHJ7ZKFW9Wc7bztvTCjFNN+
MqXBVqqdwTtNKWPunF6rOwommgksBEG+rb27xb3vat+BNdLXGrOwbce+t+VK/YZFMq+dRgiA
KMZ0/SJKDVoaEonuF1WP0sUB35mfk2iH8qEliycTGegA6W4s7YlGltn+pW5oScieJAY6MAIP
nQ5Vxv4FjZVKA2yn6TmS+20yv023UmQEACSthl4mKZUm09ofWGPYjocxl5flpeVOoMNc8rgb
UyvbW2dQxewI4FHBhzCtcMW9b1WkVb2L/cXZ3aqF7CTunz84IN/6WiliBDCtT0v0Pr/iIuG9
KcFYJyp5mbmEHtjGlLXErlG6jStBd885m6mecgk5VtWc4wvOs7gSuemeExX7wOLDB4KdzaR7
gGCHAQh20hs+EOy4Q3/RtNOPjdZzNf7GlVLis5OI3fS15k2ibbRdlVD9+cI7DMVvFCkOeG3u
3pMLmFGzopC/jRQnZt6H8jqX04YMezYuiFVIBa8D7uiim171Ko60jpKUq+W0688ipkyCrO69
K7NjTjzRLE9RsWxLvBMA3UQN4kYJ7cVfaXRczb8dB4DsW2O3aTyCHv9/sur/beG/GT1qZtZU
l8+T6ogOxTq+pIccAictpy7beQ3r87qRXac2vOGfjYu2GDinreUypXp14pRtwouCyZ5yFAUz
ciJBzReX+luohmD2m46HwxQ3vaF3pKbZkgOZBVqbz5BwOAOe9cQwKRSBunsexulXCr98/sM5
SwUfJ/S84MtVp74a1NFMnEfJ3CDJy3M4EcRqtAW5lbtwAjvGwlKYjwJ0MVEl7OTHgyU6OCII
1Whvc9iQRHDjqnUdoiA9OCGUSJ+hstbIlpTTYR1jFaGs07Dta+R8BaR/04PGmUCmkFYUvGbN
/FJE33H6bE35OIhbNvRkRMzZUk5tkPg3JVqc6m4v5Hy+wiOFxbIPw8r3/EAptjcUSxpqPJfz
RoaoQWEf8O4vTd4/2eAJokO7QaSGM4jUcMz+EKmxhtlzrrEszvEEACOwJdoYq90OC4QElHWU
5omQ5faRjnxYQ3TB0YbKPx20JBk/ZAwObPdxtvKfMdu3o+j21Vf0Z+XjToVatG2W4DzeyvXZ
//Yrfrz4r9LAf7/5tUqsP0Q3YpUAXEu+gcHQXgX/yHRDi9pgiUhqM9luk/J0ctx+rCEh0rU9
p8RT7pE1xalElIMzUbnOpvpDtSIWDTDXDKcXlbYYGwZsku2wFvOmSvUO2oEjUW7i4PPkmX4l
P0/3bAvz9ztLiwazvJ+DZun8siSLjHvnzyTvsJJ9DZBI4b+69AXuiT7G9P5+cM+54TcZlbEq
1nX37/vCUkWXXYnD9pojvySKFXyDBMhexYwtxS1va9NaeTGizFUpuiAlcnfc4jQxxWxYY5xV
Yq5YWbCkRI1UC/VhxST8QWzEXK2xn0RFwgu8Vfbu9Z4m2mdGZLODbIO2UGs3M6vMdFCKJSMk
t5Wx06+ZK2l0doVd//2iyzR4L3Mpogh/+/1hYtd08kuXPRq1N1+RmeVufLYO7VlldcfeP+90
AfQOsNOFfnOupwKqLXvj7dLZLnTvC/dvzABhGxFxTy6UiuHNAJPvRo76KBnp2DK/PWBrTWgT
2zzrbFJKsitKsxvpnL+vWOx1wulf9cE/3udvauAvMcPbz1pL7vv32JuiyS3OLIM+0un3FS6d
vTMLU0MtLUuRV2tsDLvZ/bqLmHTgk//A4+COwXgzfZ2pu3PnmUo/rxkcb8/IwGc5Hg3XpcFb
6a47BgrhZl/vNA8WqXPSk6LTpmstnBj6BDvi1crrpOoyf79KA+gJ3wbjxkZZDjgAYJbqKrkh
+AyT7LTcOjY1mYwmOpHr+VecqjhCG7XwTdP5GJ3rKGNvq9RAkh6sLPeFucGH2fUBT4c+LxH3
AJ+TcedMZFEmby5qfOSaOzn7rdi6BtNj9Xnd9Y43VaMyc9XTb4srHZPXnMWB/RpkePbxJqbB
E8S+NY9eGnE6mxDZ7yBenN3N63SDhmptOhhNlgvmb0jnAP+o+4BqCsp3QcXT4/Kl5exdkYbO
u3ad45DAEQCekQt/fqXhxtyFSu/dDGP9OZrv8LahrP2FfwLH/f/gBMDf/KD/owUUPKPrJk28
UNEtXbCU+pruk6dev6sa/4kerq5zlVhq0ph7jlvYEL5aSkIarc4kFcbSrdvshjxOaiwHnYaf
D9PtOyo+NzNinjVZH+va3gBwP34b643z534b691t2TYRO4xOp3TKB7uyOGSkn4MLY8qbJboS
6QGb5kHIa7G+PHTB9dNpNcbs9PxRp0QAqWCuzDYCkAqJ+axTVq9VHP5Hf52PL/9RAx818FED
HzXwUQMfNfBRAx818FEDHzXwUQMfNfBRAx818FEDHzXwUQMfNfBRAx818FEDHzXwUQMfNfBR
Ax818FEDHzXwUQMfNfBRA/9jNaDwnU+c++jZOrIgyqcgRNufE9htplN6+FQ7w9+lp3L78uLK
HN0x1QI23qbRODxOCXxf2vw/Vlf/ihdXmLrKxAcEmlXtZzITrBk6dP5ZY5dLV5iUY+ICeiDn
hvcLB7T18t2Yi/9cZdeUz9RsmSWfeO6GZnWKJiYCWTPkmNL7RqzsB5ctUUi3zEVLZCR/hg97
gXj/z9Xwd5ba0Ofn0rtEIxnFDVMqFtcSJBGEwgmX1q6WDtb553zPEZID3bV+uqRJyLCx09eH
R2VkbPT7lTT/eux0wtmp0WXeO5N991yH5ui5T6ecOypNDkh0PBpQhuJUeRR/Sqnxw0OYORFr
CqbPV+WWcwdiMEbw7MHImapT2HCH1g3x3VOe6VuN62qKBIot/k5jsTYmJLeNqqq8iOxHQqHy
sWDncDZhj18I9vKsWil+q7FQ9iLpHtKed8ouFISIxgs/3F5hfF5jvDoiJSvUxI1LEzojT3Wb
GKnPnu/tir0fWnTNziQ6fzKrbeSPsRnEL8GhZtKN8mFCm/vXwxu/f15b/pI3E5Ftbp5k7uxa
5/6WVuj35SoSybes59TqPPpw83/L75LVOWXDxcPxFk1XB9WPDEc3oMyD582d3NweXw8NuGKf
wvUT70t29OSUWzMCcfh8DyJtaJ/5a9jZhxZ+Yybqpt5vGCu5tYdnswqHWXVOW3Ot9hVXaGvt
Zhsf4u6ToTh1odp7S+JQnIzCPIEB+7LBlt+906e7UU97I60mVROH1LaWLzToRnj7ml3Z/Sqc
n/Vg1PlVO1HU6WAfJCy9HzrRnV2lD/9D4kI0d9H256MNHkEaWomxWkEhikGrQZmx2T+09h1p
JGtuziO8rrJhYnTiZCUL/RrjA3djH/2u1v8iI58EDtaswF6WlVnr7Qux8uW53FkLd22rKvPt
09elWBpsQzrYhxZl5e/zMG+2SKnp4uhlU11bhtbOpGarXugz2px3RlVRyb2NgpGhC+MM7WxQ
SPuhfbGnYiF110AzNGPX5QeUa+u6sWJeKacVXnLOrjOtq9t+vtIjUchw7Zg6UAgbBIDqUoEL
Cduhcosy6qW09iMiz+8hf/XEQr/0YPM6xFdJ0B06vA7ZDweQGjczoLzj8miiM2VSqcV9oUpR
VgSlGnVGSh+t+Ml3XsTWKK5O1QWuQx5At2JfdqksP8Ja9B8aWYofrVi5cF3eu0N+H9C7L2cm
l0875e0rIHgPFmipHf5CZFI2UuMQWVivW+iVVZwBfplJ1yKa/wtt/Z9ZOzuztp5EfD9JSHYi
pmXfS8hOqAyfu+OfE5vm3ODF243mFhFvz2Rk+SYlZmTkLeqrQm7Dk1dX+6Ifs5zCyzp7Pa74
l3Wml1mids47nvaC3igpFlrTxyuqJZ5tjkHWN3yP/591/d3/FSrav3GjkJMXqnRXTK4/O/Z3
F/xnBPez9RcPW73nbBI7bg8fmrkDq3k60rvvNoH0sM7GYIJntcxgZe3HRRR9WhXDrioOhPkh
gmd3GV3mAIIY1NEK5ExdzCTKNdy2wQhpsHgjOOakpCcY/jkX2/JoVwkEsoEZwskI3LE0/Gsg
P08nUMdQemHRLiEpcO+U2+MYLcov7TXsffVkDU63DWyNgdTnfGKF2syoylDWnpz0sdhXkqoe
0NHAJB3L2yN5yoWXNGYV1BTjDZdrbAB6Z7vjky+d68Sp82xJmlOPYNisiVLkKLwQUxjOKqXz
+0OLS3nxryFq7j/HMVCbm7tK1aK829CxZ9oqYeNn6+6bHtthVXPu0MiO4uWGldj2yiOffTup
UqrXNdaEUVNZkcVfr4rUQzoMtPb5OxrOmJK0u7f3j2fmOE2hNXVK8r1FvavFd++CJpaUxFed
vgtwxQ7iDV1YwdlpW5+eprRu/bYx1xGeNQ7ARaeyqgxmcdattlnDtXls3bS4uRitNoe2o9sU
2nsIOW9DCAbaqt8OmxxDkwKR+n42zPSSKuyLuWiX17yY+oZoQouhHcIO0rb1jH1vzR1m/cOK
osucKyOlbZFa+3iOgY7wYSTSwAC+YtYsS8ry0in02mcBiPs2SIKDcue9a3fd94hw3yG6k2Lc
RVd94ism/Nhckii77EQ2mBhDZ9YYIudvnDM15ga0pHoKglfQlIWQ5XPy17wgqGbpsFB2jtM7
7lJKtXyzfLCfk7e4neEinttV9s+0sH+mDE6zRk4i31/oGHlvelwYoyvpI9m2SPltQ8EGvw1e
f3HPT7RF2aL+q3iFBcSW7k/Klx7POr3nNG8lr9Q36xX9heR/ndhkkiw9P9ioMvqqrk1jrej0
PtxjT5s1ckP0GQY1azg7BNYIMAB98jOWuamygsZ411SPY4uNdffGXlW1uc7E+LzuDYy2sDDz
yyr3WQmzXlX3Q69DnK1t82KtbheXFAsYX1WYxUoEtcg1I0e2XvyltxDIl3gGFIC3GLg8CMo+
Nx91eNYkjKfXKxauCPwZLnERPNa14xc/PKriZc2zMB/pVys7CuSf+asl/teP/5+5Cr51FaLy
ENz7T0elrnHbvqfd73ctlypRpQZ/UL34n1L/0J+tGFMdkWzO/Wam+4vGrdeb/6HC/6Cwwhew
C6vUt+KnxnXeoxEN3j/Sn4UWdwxnDtS0RQROOJWSy3T8cEZ2gbWLLB57b30AfYS8o1lrv2ru
O2gf6vpCgr1cA9L9I2TjN22p2gFuW4LHg0OsYq8ABD1ScGnX66xYm8h95pY7i5Iykoj1U1kH
UhfZJfkKRPHRuFdBcu+oXHxrgCjbxc4V6fSuuiPQ5pxhF2J7906AUG9B45QQaUYMdrFw+VqN
G95Q8Whd1Ixnl7e64ZwrrZbnESwOvEK36TQ1G67ndlMC0TuGWgk16Ibo8Q5GUGNEBl+VtevS
E+Hp0fCc/SRiSEvY5ORKrA3LxhyqOZLMXECaaJPqxlZefLsIzT9NTr6JOvwzK6Cl96hPoVeO
RqxN6W7dDOEp9yokBm+Vx7Jq4H2CWUy/rn4BYOeEYY9aOA1m1iujwxhuMMdYR089lq0PsZu7
72qDbUEj3YBJ8eHBL/741cOzD1iLvs6/LJvoSi/0+XV0VXkUD+3OQ/aI9YZItjHVEi4eZm+z
zcgpUxZgZDfSfWqDbfNGpXb4EV6qwkJByKJ3JNKAwJN+T955oORAhY7Mfvtg5SnqLNGl5PZe
NE4tWnAq3lXTKCQ9blGQtJuy/djNYkZ6CZcUSz9l3VZ2ZtvIm/FBguj5NM7QqooDOA28Lu+X
mdj0huee3PM9TSjNmZvrrB541faqBskkERmw4vzbB5KySjIzEhNTBUe38N8nWBFhISq2r/qj
CmqrezQuTtB30JNiujhcO+v2qKw5O6ShM1+jkeG6aFVlbR3x6SmPsO9GNb7EbJk3ClwbdIMy
Ai55OpNGmAvWSBiZqvZqs0+bZhKzxbqZUhQcf+f8boDPF1VED2/87CWxDtdHxwwj6Qbw9tu3
PSmAcVVBs/HsqPvntUYNS8tQ1efEwJH+Iw02XS4lnpwi/OO6wHqvq3WnlvMYNADCmPduk1vb
2gqJNzHuRuyeNWrrjDzEAFAZdrAxD0+qqurcjXAzLwE2uwu/ack4da0XZkcxtjQu83YnYrA/
vSzZd3CSSkKRDSzfSIoKi3mT5se9Lv6DXeifFf93mtvfgWN+7tlLyeHW3RlDrOX62/wUGMz3
vtx/GtaJlE6V4zWm69JhjQznQgsHJ6F0juEu9b66RffTk2FiESe4dNm3otH105ZHEIgWtfwc
ZxXfOd89FDEfFehn/uudkgIKzam9jaKqKb4tqlt59PnbLa/eE87AL0XxXvIUk50dw/23Ir5n
nQt0b21nhG9hRjvQLId4YmJ2VBpNYyqpxNwRYa4PaD02Bkk2Sd8BACWWrlzCRbw+LtuI8cFW
zANsDXQ4dOIrzA2KIaVfDOAxmupxS58jTrhnuc+u3cSOuFqt/gH6qKL7sEj2ksInFkh//oLe
DLtZFlx1w1zlVkO8toqW/dBarOL3XQ0JrsgBoih5O5NYGu5oY2RjYEj1yfKIjfFQcLv2Nz7q
IUcjeQ1RXwphIZIrbhwwOxozW0O5troOuXVpg//fKPt/ufxvdEBfsX1NBaNKB3ZPpT83kd+s
D7exP9+ce3JnHy7JY1LzBz1kEGe2IWbkVpyDbf7XXyaQ69kDt3UrW/I2uJTU8d939IkyEnF+
5GxjDmX+2RarcYJdj0+t4Hr6Iz/zd31M5mqlodu7iMmklprQJCHNdTCrot+6PcsnO2/Xss+n
+pDPemZUZk2bV04Wr0OUr3kVQTYcNGOEkHS6/Inu1ehvSw65k9wm+3h2jtx7Y9nnw5DMgSTC
3uJCdAYJ3vrd3rIvbr6L/CVlM+oicyrhtpNRmTT2AnJwaDfGppbYxapxoaPg9d7dDvTQzHyW
bX6JbikpKv/iNz9DFIKO8ZtTNQQ7WshWt6RWNN7kqJedQUqazXYJwfY1b+jOnZgp7RehmSuF
5nQHGwP9PxLFmrUGdauYsb7xUT0eTjPwZpoxb6JN1XJXBuMU0ntvIoAqMnetKyQOc6q76PCo
uz9lO6Jms3VRPuYt/hzWC4bQmml2S9mGkl+DYYS47rAiI49sfbhyuLXc/E7cviGXn95NFw6n
UJ94+hr4alPu1bluMzkUuTxd0XZqrfpG9SeO4c/GlS13+Osp+gyibEofuAybldfiCwQMXJLq
/KlXDl22VaP4i9ucPnswY97x6fVfj4XEd6UK3x26EjjcH9iQpVZySLyaXtjVbcgiqU43xFYz
xnGIX0oSU9k6Y9+ebIZ8OUL11smCGsbt6K1u2H2lmJ2N1VzGDHQn3g48bWMozvEpleROF+7P
wBsi35fSrRXdhopLbhfensnyLYwF5j7j7uV+m/kDk8EV2bJkTE4mKb7+KMHfmzZS7VpgULMz
Hz2X2F66dtf/8/9LW/9XZ2u1l2PL+ZelR0kryj/CNG/La8rpgAfQfDEiZ4vsd5UpfCbzkoUP
aTfHqbQYnNCNK4rpqzVdUAzC6D3bDOZPf/OXSiyNm8bWPe9v6EzYKgr6dIaVQRbvRN6Wx9rQ
A6242/SFJkF0ONYr296AKezw2qDOY4IJm3G5HTK8X9/GkK4xVYw/dSr2qAqzL8jTrQK6lxFB
HCq5Cia9QL1FeXRV1ekM/MVdSvSR/tyXFYMlTYthe5SvQSBJgaS1AsYe0k1nveRc8gmCb8zT
jr1ouBsvO8x6jV1YQaJ8dedH/4KOV/1yj1W/0YiBkpEb88q0d8UU28ARAiPF0hGLRR6vP/43
XxAI1Lj0S/pq2xcUg+V6TX94Mv1mltgnV+TId/382bO/p/zvZT6lqKfFyJcPv+yqeM/+tPn9
7yX+VTkbvjZ7M2ezWL/CqPx1+Xl3f3j2zohqZl2kLb3isp0lppQM35V1ICOJpw8jMD/BYGv7
1QCwzNlF+eIVLEtR9qqWIrsdiRMn68rfW+S+qBQT6TVecu6ghJ0StLc4vzvmFj5SMzvtVGRG
oV+heZdVtcrnf+0NfwIJN2Lv4CuHrVx3Neo+LzGKioEl4vva7jjbhSLCs6sW49XKBhvuxdyJ
3cmtC+XZWW631wBkI7GnjhuHjCo3N486bjZO31o9tL/w1RCt0vB1lla1I7IUrG2i5hkOSAdq
lZH1jQqwmPgFOvD5zk+Vl0bTVfX9lzv7DOdkakeLUmmGY6yaCCo2EJtfYUW23nBUwVzjGxNA
jvomL4kw4Wh0+noZNyagScD2SCJzE3Hpe09kXryuWbxWuDzJcY7xYET4VT4a98k6h8D20c9q
lNa0z5OIiqqVlfwrE05t7QXtEaIwZj4+sDiPBt1vfGsw21vpir9ss9dMmP1pzfjCsZkMIX26
kJHswCzUGitUmLsGgfQRMnmKqn4orTZYA2Ewv28fvrEm+8u+acnug6+ujGzU59sPKbwPxppo
2YyxX/eG7CuiJNcKmcuAksjxrE1dKpsfdc2f+69qHn/jPv9WW3Iw6FjcW16TQ605nmJ0WCud
OBX17Pl8uqtbHGuGwImz08R+EwjHTKw20oa025D6f6yAL7L33E/cU3qOzWw5RymedWK7drHm
GujsUpJfnsi2ZtvcKaurib/9PrkRhp9oWW1iPaxLH4OnjTGzY/f5MI+lT6+yZKdZq0te2vTA
NjtBU+swznYG9cW2VTJF4l0h77iCXn7k1pMnb5zfgelGipMfDYRBIJ9ohN9gAXCpOnLFd8m5
44EBueZns2JlW5HdLHz6c2v0o0uF/W9/NTk9+S6iD4o9XOp9/kXNkDk1lddxFUdyULyac9AC
ba78Cp8UeGjgVY1ltoNVftaBxETcL1+pv/8bH+S3y/9/tkfgBVL0SNh3I7egVZkjUY+2ffF7
H+jzaPyEVY6mFkqttVxAOqZbxPHZ3cPpDa2WloRv0fGQHxwpfeOSWCJEbkNus17OSBKsjinY
BOMJJiYDFvaDdcyCGxdWYozh7+lErqma0ZbdxVXJZ21UI+puB1l3WW5zWE7MFEQ/Un0FHuUP
T2axjUcCuRY6AzsPn5ryPN8rupONlgqZDcjsc96kBuMKWeJelmrlO/vAiem4zOnM1Z37WH71
PYQiJl+jsH6v+O7tJmfVJcWjL+JzgmasXrJNF91DQ7zdxm7NNVNZdSHpsXt29hkO1ehbGloa
djtYL/OsYy5vf4ijoW5ITpffLLVrI3Niyg5mR28LbDjWtHvqdn7FluUCGqxhwynwdOHhNra2
tLAusve5rpqk+OseU2fPWg41Gl4ADL3IcAa81VLfwIB33OjBmFxESLI4z845mX+7qAA1v/Xk
+fysgmr62dOWkR6Z4vxaXOIO3P49qgZJFm+D26+ODhDn3Fm1Fy7oA8Pd1l63S427Uu5Uh/jc
+EOt/47ftvE+Sp/4V8wuZ6nSfk2cJdapb2YFm7vScPZTsJb517+f5VWYep7qe7jSaOajtCYH
mJ+L+ooCiaJ2fiPjr2V/l1a632Dixh5gejuwnauQlYVXh/S++WAlRBH53dlh3UgkvGu1gKYZ
nQemXCcqHE3j6IGafrVt2eQqi6Z9w3TpeXOUNbHCeN92pBB5Krqx/E0isU6wumbP9sm/Gxca
0jE1NkW6c95cTalz7OqXcHVeezHNNltlk46gzQAepBuKCU0UrE75ZmRdLX3mf7g6Im94INv9
h8HsMz/86VEaD6qf0R9KNg6gb6dbxxpM4Syoed6N1Oi7fnv+OxP0aUPjOmQeO9WQk6fr22Tf
PmE0VN0kk2kW1ASpkdomzBXfTBT4rUOMLYaC8aeyMT8lDh8z7T/AY+sU7J647Kg6H+VPxQbv
2TUxMT46zursek3yaMvaN9lJ0r0N0CVTBQ5dq/l7YZkbH7Bd+KFpz37lNrNy0EOGEzS2bk18
JlcynSFss0tRszCYt/XZ+Edcb+e9uVJ5Iand38lvMSqWRTMyDxNLuJX5eWx+sGsqFPXHZriu
W4FqQtylIad51ze8s5p6pV6hBPkNLz2MUE39dx/tdxlORD+Zn4vnikItVs39k5/CLov6/bAK
gnXIlpefDPxO+u/KUHSVO0Y+7B/lm8U6xgTZ+EG/pxnmUtOwJsbrEKy2x4gfbay02nqZr6+J
u6x60hbhkt0/PaXiK40kWg0/Ua8WjL+ZxKReikhoT9cXXwRpWsdGt9RLy+7tRafQA0qHLBZC
ExwLMnJTFrnP36s/EFR1wNxSPZbV2ssGcR3KP0S/m9SpsNJvhK+ImNtWm9dSUaY2pbSuSGU5
rCUFmqdSy9nzQEJWb18YH2dl3FsFuHbB0XZ4q6MWRitiuDr2S5XaKXGaqRD1TcvhhdLNskfw
guw8pDetK30L4mUXdPmRLDWgzhEvnVhxl6uBHS2lXpRPRysACTzwcmSBYgs2xFRGOL9Oest/
yjkIlGi4Dllulsljlc9hJ3UBhmf72XWIv5Jg4AOG5wE3sM5wyyly7SLarttdtx9hP2V1syaW
2XIWP359oCCzx1kPQ+g6vFVHMjx4HfEqPivVsy66ToLXPBbpSK4/4r3yFkXrUlIgYgivuuMd
yXVHACgfyq4d/hlLonxk7jaZ15KEeAVQyA2CMZRHY009pez+EG/Bi27bnSv27m9DTHwYfL/z
9NX3k4Tb6oYV08eSnvuKa+KipQuh9NZAqKNwDz8Iyfd9qC243nlWOsCQKQveEti9/usQttI3
5lRvhtC8wgofa9Yvex9qX79Mdj9ZZ1gsrjoEOG3U79Uui9xPVvjQ+Vfs5M/QrxrykUKzV1vW
Brdjy6AhpTPIGCOL78UV9uDa6QICtQChiZ3xWYechxeYKKN3RXjLf1EQ7TommKYEYhuuoS1n
7acbrAaPI+LCbPPrMT9ixLhAiNL039UY/xuhDYb1YOPyDOZLTI83euzaqe+0zZ8gyjiKo8oE
qZlC1qM/FV0g9YiHWMZDu5+vsYe6U3RP0vT9uro7ybBiEmDv06Ij7WH5WZ6NDIfWU9Zdx436
pkgZW50z80wD9XS9h+pSEjIj9MPumN/ntNJ5kYVtdTy2hb3GbAUpux1gO/lsrGHuCXJiO98/
M+QctGEqsLTc60Lzy1ckDS4Zwwux3N5OQdpBBoNuNBrQa41euj592a0351r53DAHDQ86FbEk
vppv8ZTNbu13T6XMX3e6BvYVnuaWTw+51pGLfVfOPxynI6W3D7XGhVtv6A9RzO45X3spOVY7
erHTe6zfw7w/OaXYuatzpXLOJtJ77Mm2JKq7w56cUGamVON9IL7o6tpJuEVqRenUKacuxqFI
wQApcF9cyu2GOHH0Yj/UXP9UVHGRVu8XvHfm92Xul2dWLbpC1L6vULXrD+ao+Hm45/s0eG+q
40fqlXhPe/F9fUjTeO1xvIXLky/+XUBW/04f+w/RXEpPggBdyw+ltaCd20jGcuuzU52V7j3c
3TfrAONce+Hw7QIOOalBE/du7LLWuA/PtaUp0ji96nleGta+L7ysIer8sYda5MgKlw9Ya8ta
VHim4FRkJu/zrTfrDCeDgkILXrA07iVMHBUrPx7tYcXkbl9dEnjhYYZdq9K02tUOre6ppNJq
pKvry7V4xwDeOoQOwy7b6/JrNiz/1YqqypuMxMxM3raZu35KrTyqOTPJuSq6G2PaX9Mls20T
ubnvbchdh8RtoqflHRtdGn0VcPhO+nLr7KrTp/vCfFYMsK+ZpTpyo87tyNAmur6lfkQJodqa
ejWRN9KohMI1joSsZR46s3cd8kUk+0oMsjPP3Ex5Y7inT8biCMcjezvVdwp2e94mHJjBzUch
CJ+SEp3b0yU+JZl8VdUhD/SzK5GHhr9fvQP2QA6rWfdGbuWJqnnW9ijL/lCdBtedsrK4Yn5E
V2t0vnZbIPyRqkFnkKG6zlT65dOLo8RyB/arBSbDMIfY6zVDKjRvU7ualCek+iz0W3cbReTR
2TqJm5//zh5I+dvmmhH7JmuF/bYdKpkUD5hJEW7+EdQgPUkzp9SO3w9ZzbWyJUxXVY6PNNhK
XiyaNd23pflG3eOzCbKL46Vub2ckh/w2wKRZiD5lMxKcWTBNUs7UlLtSRPGp5aPVRRIY/Yk9
n+OE61Ha4Tx72U4Y236SMNJ7sJ2jeIuoFSzBFYzExuCxDpXQHOXdK09bdLFWra6VtpTS8XZO
/K2mwwsPR7g5dkOGaxK2ISbqmO545KeH5MVtw2m2/X4r96QXQQ5/Q4C8+FV5AoDotzgmP6IR
s5oyye3n5kSNDkNd6494rrwNJ6IQnTYVjOiE0Vyoa0Ow1srbYFsjVjkdVjJlezME3svXMJc9
QyDyKABM+oeFCulROoWpIBVJy7Edjjexow9z5QMqnAoAJv1TIwCT3lLNX25+zupGGXVGkDsj
dwgPbc7Q2801e1jwqxHL2sLCpv96jNxmLUOtmOQ7XB/YjexH2m9v01c1MNgGSWXfyavnBb2H
Y0czjmf/7nv8fRl+F54dsy9ebM9wCVS9OlSol51dF87KMTe94MBAliKjiEh2EYGqL2hqNjja
lORyFfdoXLMDj3nlgrl4zG86u/07mW1y7BdoCUprpVhpK3q76XVc70pxyxB5LbNSjvvqfUU+
Xp8mwX+xEuBISQOgrr8qb5LookyhxYsqN0XoiIIiK4l6fLJwx+pTOaXWUSbqxd69LtmsTse6
N/5pJ+HEqmSzBUjmHPxtY+HEKmxnHUHeVOsMZBH3FJcAJ40dVBa7UI8VEx9LE6EGtMisjHXI
LPWW6jqEXLUOuac4FXME5aiZMtJyAIy4gyOvXwhgX9aV405zR5+sQ/j+IxPXVvLuNPa3F4Qu
sNE898OrX8G1C2yN9af7a8Phy5Vp0gdQVcAQ8J3QVwrDx55/LbdWNqs/JgjSTDl5kUouY8vP
grQ5KlwzeW1nRaxTnbxVHRkWOyXBW5rvq4h1Ll0aUtJw/Sr6JYGWUFUirqGKmEo7XP+4+opA
e8IzI/MicJ3fHfOd2dODhKeQn+uIa2bdHyq0OX5/FjUjDDhEdiRXjMsvAIznfau9BFpl2A8y
3oukVT+g7P2rg4TpqKCn/fzAg9DOMPUdwlIOBv949OxWzPI4HXtoIdjxHTXvB0xCfISfZLjz
KcblbjD1DDHGI9ZKsQEgEdsUrEN0lTjTrgKGLB7LM8ZJy1TeNnIIa59SV878xzV3FE0Wr7MO
+cwQN3lcmpehLmiXnwTt9g9CkF7Ny4gTWMm/ncf+bGa79CiOah0YDcCe/+hIoUgcl+6CNDFq
nN5chufPp0ufQA3o5nlfChe0D4/1Vb9Zh3yvpC7s5cTALJR6VmrQZth3CouONsTIA8KFPXYr
NTZwLE6pfToEVRMY265QcxXPC1eHvomDhtCZeWegJ15sfWEbVNyrj/3mPbr9j43iCxLlrYEd
GNKPlauHFbmmWpwx6tvg+7F0UZ0Qcwb4jai8RzsxCTdZ3xJmURRGGJTSg+/VpL5dYCb1ygKv
UN8Eq3CucDW8p6PQbRk8kampqlhPUbDKrr99QaKR/Oq8hDl4X6yrNLFwsqgbf7pz/Gd0QMzP
so7rAot9XFNvWnWUGOp8thQRemLRwpyL8KbVRCfgyqvKAGtj15z8iTGhOiDvcsFsiNHg2l2V
Iqbr9zMSDcXMKHElsN4iRa6h3tNqiWGglye7HXBf9KrUvqvPoE/To3NwEo0X8kcYSXLxU8QK
waByHWJVq7A2UZ9tvw7Z0SXEomohi+HGBBGLatVeCxE52jthF/O8C9bIzSqZvfWZ9jPUqVDE
TKSS5IXArP8nCdqMZGDHHwF19Klkslx/KJYcisxMFC8BF1oUPxbp+JMZPDlEcEBT7kWWP8O8
knJPeNPrTZNxxNd9nPnX8PHbMKsySaT3kW0iBpcuvgi1e4UpOIc270y9J6IV2w4/gbrPr/Y6
UQlxIYXwpr4w2dCJNemS66mDsp3rkDEhOgLuIBuCyGNSH5/DJCeyfsIRW8mrAdelYvJxsBKq
WouzDSp5+aG3dAkI1GF8/liTlDD77ID0+fVVCxFq0nt65UXjAQkP3j/5q0oSV4FqiS8Yd5sk
zFZLgzovQ1V7nXOZCKt2wAdE/LCbcOgaht6Lyy1Bq8f0ymEmG7CJSqzwA5wIvJWmgRymfRYv
DEa3/zQfdUAYMmIwTqseBMoFEgac2zD1iA754gz2zXWRhs3qBM5KIwgAeYdVTDRLUgHjrJXc
VW8dEj9ku/Qj2sp+Pnp8HaIXiXgxrL26H+FZogTbBmh+zCgvyFqr++EUy815+LlJxPs+nPSu
Cu0k6Fym2MEPdCoIrKVqXsUcGJ69wrAT19YKSqwshDK13eX9Iqbf99KMR5yCEpyFoUxt56Ku
hEcqxFgHo2gM79x6THJSfQBGPkxfh3xzF2Ql5PqizcGzV4wwB7C/DJgWcWk9KfDcyUcMPk8a
9OY702LuSM8VeG73c65YuBlxF3AZRXD24s/W1PiKhbrYXx4BMiVBjhna7Nbb0pG340vnlJ1i
mgXXbQuXO0tHaNpLrkrfwC6tNuJsyDhHSn6/fED9gejO1BjsWOymCuxpspwF0nen+mBm7iqE
EVoFCGBU+jr8wVQPzAyqzBmhLWEfxM+bdaEuaeY2tCSJhXcok8fXUqvi+q0Ifgt9aJkWoNWD
F5SJje7NDLkY4LHfd8vPqxTNnux2wIqyWz4DxBimI50KIo2rq0U4+a+17oi1UsTqVYRn+WEw
I+xDbPZeh4T7QjtPiCSGLDr2PBgmRCB5TbYb40Mpg+8AnIA10MlmmWx3qg+2TO/PaUlBuRWI
G0O0yHdSyYW++vIs5RgzhuAAtCR45FYaOnBnHPbpa9PpWdcuQ0zxS7kGg3++ByfMVIJp+EcJ
gBAeGP5dldIwMJV8nhOAK3gvf42PmXfBfqnsG8MMuQXHxe8xQ8+VFUnfo+z7xm/ThHFfDKH4
3hPNpj6zka2AomAjL0lcY50ofRtK7xMn2gnjPmVW8f3Uxleehdr3AZ+xnRYM8OtjXcjQNkUt
Uy2unbuR1LpnNJDykmvchyYfnS9OSE8qYqR58YxL87N4rMLSsG7VodqM0sbW5Yw8OrPW+8s/
jf9aZ8pHhKTRhLmpSPb+T07dAMxyfxF+CKQ29C3yM/O2hvY/54QsOkeOz4hc8n1b6Ae7XKnU
DFlA8ja4TqPcpyTWzjZqEWn75HN8TwLc5dQU80LK3oP9pAjlXEzgzNDW0iadCkdN39Cjszij
TnLDcuLq0F6vA3zYbJF+1Bekd0G/5Mh05kH0tA1dpzJUdHt6UIKxbGK07Wi/Rf62CG91O7Mk
2W3YCOmeH/D6m6/AU315ou8LrPRH79Gz2dI9zfHPIJ88EU5PjD/YOhq7GePX6Pq29mlD8HSB
Xm6lTf1iiHBohmeAZDkv2swVFRJpOxiWxpSa0u6v0jISC/dmeezV6t6m2fwXZDQKvtGPx9n4
TsQnJKUva7ZukJMEmgedKgmDDTsbyWv9RTWBWURr2/sFbS42yIg8muqHaN+fw6guW2fmQtfy
2ykVYMrroZI5i22CpUKuuo8wR+auL8KCSPzK5kOKa6JYWQbcu5z/OTp1A28acAyATavB+KkY
dsiegfenmTjsOUBnFQxV7eMnYdo3LHfFSgqtZG/jbJ3z9q+pqwzR+FxTKFepVVQ7RpqN+qZ6
fIT6BqRIY5zKF66PgYF2BCYdFlDbJmFvmRsQL/1KEIDKA6KoErayf5GYP0nlxKfGDC42iBq/
Gljkszrx4wqLMP/aGQn7C//vxNwu/DhgEfOPEknY2/2/FI8bY1OBj+K3el0WtPlYrKasEVjD
70CFxCktUeOR0d7YZQOC7Gv18PCyKYSo0XC0OnYlUyB/AIgxGIJDErZ6cAdMqvEt9t2Ldken
PG+KcwtbrZ1C8FWVZ6kkzdp1a1c+i3KUzfZi0xUFQl/Tp/IPSS5IKkgMP4SNnHfRBd0W8edu
+5/dVPpX3RiTYmI40qe9GUF2wi29x3xIAiNw+EM6Yek94nR6FnZ2z03AU3cSmAjE6ftZuFno
zZE/J3EgqQ2SZeuQyUfg1nq+2LIm8F1iUIBP6rrEEDBIXWg8IhdysAcB49qjqQoJdfQOdj6H
P3lNmlclZaxDnCyOyoWAQvig0oQod6pK0juaA66PTF4E13N+Ix3FyWiZ0jKoQZ9fFnBCvW/R
AMXE0XVIWvxSDLCBCFngwhhCfNr9g7N0IdAfGK8idVOcjJomLYLe77PPNgV8cFBlMKKgJsCy
FniKX6beYSW4lgFAtLQK7TghgF02rcHLny7IEWIj8BqQ1bxKFpO6DrFf3oKd9xvpUBDAPFbr
8FLbS+3yyQY5CzyJdnbxOqRt+SB23hnPuy6AXaprxFvu0USID2F5oNFcMm3CWzrvg/G+qFh+
tJr3zOK9bb68Cyd7g+CBm7nXvcSf9urBxZ5ch0iBn1wRN2Zb8NOQPv9q2G/EGaIozm707iY6
LvbbAvkC3LuUYGow3R9RHTu0FUzbxmJqBenwlPbnnuy3/iBFQmXDU+gkLfbbg4pjMTWox/CU
EdI4+63+B68nidvd80ACaDc1l0fagNqUTbntPWUSk6lkzWV2yzqkFkhQelolxxKetJNJzyiD
4Iblghp46jc+9/gBLJXl4+OlJRTzqumxh3jNZRbg8IkfI5a4LNgWJB8L4QeQTWTXjnG5uVR1
ybEWnOYyE7S7+/GpxGIXgW1Bys4CNtPJdulinK2DW4w3rf0PuFh/0G3fgOnH/hwR1vvwmkHB
OuRrRaGdKVfe477sbSX/ToVKO/W/B3RofgLVdjkUv+AHLilNP0bRZTkE6W7QAH4Bjf7Huhl5
DxIbH2O19CPCUjEPN8dxXDF5gv0G+N94AU2WM7sOUTLETYB2qTofDUgLc6kLkd/LfwB1WHCy
18wAx4dSNf63y03R2KqnIwuxf7pqyklfM3OTL/i4f3jWfdIlW7nrn90VaV5h4yJV7hqKbXRy
X7qIsbWHRwHuCr1BdzbMYPUI3Ls4wcIAeCtxFL5epjQDer+3IXd1HdLZFCTOtpGfVcnkOvYI
QSsbN1+jEbDaoNHv50RglxaLsDHV65CJ96t5Txp5VLlb+GG+m9IaJI76k14EuP9hJ4KYpCi7
htAq4pgjJccEpbZkwij2mVJv+DbODcCrmFcHX8YnABbEyl61PCd5QgrzNpqHUAM0iRT8bF69
TP3qsCrfZ2UdMgccSBlrxXF6XHMeH2tb9YE4kdpOLcek6vG/F1evYYGA+qxA5F6QvIeLntuE
HVQUrwpM5RW0Npt1CBz0iV+V+IL3og0VtFb5Xir5JmLumjw28BFDciy9tU78DCj9spKAEb4J
XMfsp5KTImUZUCqi15hi9flKBXwZLMEuX8RaEOw2yfYA9vIqvifolizF1TGzpP7pkThPfMwr
b1kzBtvAt/OV7RlPUeU79XxoqFRxKFfffR3i1hi4UtSLmI8XyAYlKY7TbJcwfIzR4TffIRDD
qKJJTMpIe7GY4ABcwzdjODvuOkQyN6U4VnHutwwTOwnI4E7tGSOXtYOJBL/pCXBfRLQu77b7
5e2su3E9C9yToBIX1mvphRi+5MXaHkLx1xIT6NEq4DVliSUvRHvSiy0kJkpHBSAjBtwMiCQU
O0iMery0QQcL/+D2c43YT6um+6Kz8PLp3yYGA30x6dQC5FQgdkb0QUA8VWG/C5ildIP76xCb
WkSfUrdmIWodgkOZIoQN8bKLMlGQ/ffrkFeruXiJTbPKiIPICL8i9yaslTcrpXEDEIs5VFsw
O+H3DqHzvAnSrxRf9A5hL3QJpc7XVP7Y24cdi87Dz0dCEDCr3nfYRTdv77WU5k2KdzJYrAtv
g0umVKDJvVfvZ25LMO9IOauPBgFOpPsi955oWyUcTcCGqlWyvrhHc++rqcdAORg9+nX8I+A8
/OXvjyZl3WH93RgcOEJB+zX4AN6kits4KH2mgrqlcYmE31LrXV0bkPBCQ82sh/72maF5dGR4
cjXy3lk92E6PCfrONXsjS421yLzhF3aOfYLE+0J1JWYlnyvmCBRa3J2J2mCmaeLXTim+bDsB
ZuUBKyRE8YLj1XZK9n3EA/UdoprxU3LCi+40WwpWDwtXeOHurGdG5cZ9MxAmC5uyXXwLVkT6
BZ+BMqSEB7LwnBkw8l4Ln5117MqRE1owu+1FAxcE8nTI+1LgstojTJ8du7BtfibrzjqEoMgR
+oCFk2dg4eTDYArMjM9qofzZyn8kl2LeCWxlHgvPEeJzj6W1YIC5n5UERiWtmx9GJdBIHgKH
5K0ALDtktvzhg6MNuj4w+d6rpfjTtNEHsUNng5aa42wvNPkRaIBBW3P5Hhja1FF9ntmfCQPm
1a3IT65gdZTaXC+vVuFPJ7d0oHlQ7dXvjnFnod2NEkPedVtygbv8R2Wd+lZBuGMB1IMO6I4Q
h96HIPtUsrnkHf5ZaDDmgHULZDiao1xxOoJKYIP5Rx8gK21A4RwLnIaq14Z2QB8+Cu5nUHI6
yHvwATT+1Z2I/cd0udSeNPeT5DAdGI+SvOoDFkcc6wZKp6OSntBEDbGbl5hKbk0lLL6j0MK+
uWA2Yip31f+1mdisEPXG/e3iL21Q5+fVFZ0pX43mFTUKu9Yhtpoj8q4P1l7hg7UHFu9/m3tg
t/HSOtsVow/WH4zHxzn52KU/m+4JEYyTB5IoqcY77C9AmbmoTniemRuw1cKKiUcrv5lfQmod
dOfNp+2SIwbip1hD9Q7U1nvkxZX2XFTI1d2WjTHPwplZ6JwLNekO0uWvbbLD7CLJGkTbLN+C
6sg8Bh1y9+Kf2vKl9J9SUQFLgy3uU2qXfcNora7jONfG3eUMgeTcdnHhlP8aUsy3JK5DKhaR
nCXUF587hk5G+pXwhrggkt+3pITQ2EUt9DpxREM7+oj8UgSP6BV178lKpDIlxZAXd0YYt/wp
PtQcmaYPT06fyetdO0egS/xbP7l7basribQOsQamYNC6oql38+Bfhbntx5iCTV7tG9lgitxG
3eikOcAw2uTLl8yeJ+mCSKCYi7s7IFtGJ7FPTXatjD8d5Z/dyzVc4PtN2dvMXe1syx7Ku1Is
aAvzjCS8sdOfLpm0g0eV7C/Zt++ksTHHStNeeMfp0KzTw5X+UHOrBw33SoaqrKlVo4XdWbFW
dQYG8/HF9WaGoQ2lY24pdXUmffHpDpj7rrtv3sl2sF3udakaK4G9JmoPf6qG0n13PzVn27tf
SZgWalUrmpRg6RjqS1/0rSwad8ZZ9LsdZLinZuCsmcQ6YRfd2ir40ud6todz4kZyni+aW49F
NPdkHQ3mLkVnhDP0Pe1aSzw7PN0ShXQHqyy0IWM7Q6Mw466/zYumgzy4aXBn0KLj5YnuYe1g
j9OW9X6Af9olKSsQxHx072ASs4pKB/hgx1bjyY5H/2GjFMf4D7LD2zILdReot3xxhraVrM8N
WvW+DDcriPM7R9LMfMVztBNdGfrVwLCh/tbpHdxColx3xzj13hJqhONTUGPY7utxgDek2Jyq
ItpDmRmURuErVgnQiBMi9Y3cQ9jp51a7CbPz3lbDRWDRq7/323UIzV9ZDyla3aUv9gPEhTE/
u0v09izCQdNxzIxcYilNLAVQZYAxbjToc1+JlC8aVupaMqUSrWgLCTGgGKCoPvQ+DvlaDWay
DnF4T5wqpTC4X448XIBrExDmJKloQetC6axoy+HOOKiDcIgTWGGlUHMYZ9+MG3/xxtYGHlki
DIaajzOEoMN9p8QK6+bcqrDaECqHBVkDdjd0u3VqtDatuQyHc3tXIPsarPep5vmsQ167jvyv
9r4ErqmjWzyKSlurlCLggkC1BUVB2VEh0U8QqyxiiFFWBQXDToCwBIhLLYtCtLiwKCjUAKFA
kSVAwIDIpiAihH3HsIcdwhrfTCKttfWz73vfe//3fz+T303unTlzzplzzpw5M3fu3NGA77nG
Qgn9F6s0QfChxBglHwbXDf1+VdrwOnU0DF63/3EGc+Td2U0pwpypW5VltcsJMJuf4x5Tfkt6
qLn/VNVKks4T371IOh7H+GnhcpruESSYMFWQwLn7EboKF+6c3Ry8V98t3rLawW8tOaVlPeOn
HDAR8K13ZVJfVlZLXHv9kP9+N6NXO+4G5++VYYJrR+6RA1W6hxVcBiY7hub8FvGo7xCs+Lhe
daYPrhHcfmi1/OnlnsS+wUqmxd17QYaMZPOF28vKDXXXOsbXJI5yY0inGAt3JW5O2ve88Nvb
vrafM3Ut5jV4sXqcuppIf4uvOpmEfQ5Cw+y+0kqHOU/smq3tzAnUTwJF7Yvf7bndWfKk5a52
Pc1w7XA/3fRwRV26Y9eA9622lBLVyBEzSquqVY1evUq1orCqNlw60C+Y87/lGahls01a9zVV
qijhs8smXidXUVpR0ihZyadzDs0xw6ellIOCkHft0YtPBXpcdsvWXLEi9YG+8hjS9miN3GR/
Q/pIY/zi/pl74oeS+jLubucMGXHv+xq0vZSbkxcyjCFtJE8JdCWnZtnNydMphowg50UwXLBl
yz2+ao8TGeloggOOvVnIZ6l9Wf5BSG6MPbdPg9o5XJjaN41sT2qv2VnVczk4ZcNoFyOuk9uc
1P7qF8MegeCUdaO5ICGrDkyVjYF4oBgr6KVrWT2afh4z0ueVPnuhM+mS5vrUvhmdR1TO5Jff
c3dKqI6KXAQvRb80/3UqyelM1djpjtQ7/pbD/ongxbpgyu7adu42CdHxmuchVcw9pM58C25t
QUzXxULLHWZpLYvoO0hx5lTzQUOQVPz+G0oNwWIJ/htKwU0l6QWu+/AJ0uv6J1Wj+wzgVEVV
rx7LijRh3+k8IwWi9Eegod96Btbo9DQ+GRnVNQShsFAES+oWaGyV6T9KddwWnJf2rdrmSzWM
v922gXQpGzVUOKEZM/4QGW2ajRtz9N3G3SklUt4uJ9LPYvz4BiHW9JRcIfh03P6Zh0W0mYbH
mGPLyYUCX0w5abuHjze+c6T4vnVpDxhwHfE+nFTzPLpwJuOo4uz97qSfFIzsJscH0/zlt7T4
73dlltVvU/Xx9mxEiUXp+RW4YsruyGb6eHs3touJO+dIdyVdjzawnxznZHB3+nQPG4PwgjRu
bxl/pzVtDE1Ask53psanyojOeZOa20UrAufvgBjNIOXI4OToau2ZR4+6h81BjKY+K5Pal736
oW5+Qq9uy2MQgeHGD7j1ZQtdlpxOSyhtKVtZ1FEld/cxfjbmXpIL6ceNTu21qpss4ssqKeyh
u5G/cCiJmeLO9ebuzZEJsTbBNtsjKBHhEYHXzS/wnfqhO6aMfuciocaKkbxjnwWt6HUPmLrb
4ftN7RtEwH5l3lta0M2cQFOpK822O7xdhTxwdKLOk1BOuttIjV2LYZqe5wTTbHoCraePRp4P
un5IXMXcWjldC5vhbVo9UJSO3IFxyreUlGFblF4VF0sZ06WJtgXFoKJblXtX4JzY3bmc6Y7n
rcRm14G9w+kxlmTZfcfKUxYHw8By5IppsrZu7NbKzfclCatWERKjrPVrdqeyWCwzSiVY39wD
FljJRdfWgIcK+E+XTZR9J3XD/9apm+f675r3XD1KaaWjDU5Epe9Cd1Fz81XMarUCAycMExcm
kOdzmjNPvP7OoJVOSK6xY66r1hFeV6Ov2LQ9cFJbNw0xBySzkty7+jap99dOwfmbYOUXo4I2
3x+S6MPocU5iHA/uLny9kJxqSK7pmiBMHt5txzloX9sckVYxJVo/pENUwgXNdO/179jm2F99
NGTuhBZ2epeo2o8d1MCIqD1Zj1Tmb83fnKawlVHmGMXhy6u9yp/3bvAm1SX3+Zo3bLzdlu9v
d82ek3g1PMdCyvAGw8mO5kbzGlnHVN7cnafrYrRXgfYLO99U3KI597HTncSOlqsNOeHYgXT/
4rJJjM4zGTmKdXPQinz3/oGD94qTj66+KEGs3UlS9ZQvTha0TMrMZg5QUB2cLiRBaZ/ui/rN
sb24oMDUjJbP/7BuTDAkj+DE7FrbWKtmw2me2dsWQG0a3xO+IcuKFVXLCQqdrEoX1caISHqB
Z6aDAq9bV7hXvCZoSXxePDNVaUB6dYBjqK9wePuky9bV3XWq22Hv+Z2WmvfW+OoCR9Cfqn7O
1QS9JeknOz+Jla+4Wrp7wQ20b91ZrykxuohJElkdzvG1uA+8TgHXGYbkHQqkEHA9+joXXLtL
hXL1wAYJQtn9g+VXkKGW05xSC9CtgkVc/Zzyuz57/JtJUrfBJCJH4gLeXjLUklBaqtO4MOpX
Kp0XVRp3pzJprCkHBdaEvd4RljCJ52Q81rQDU5JTEgF4b8lQi6yAxeOkOpBrGNY3iZ9I99eU
hHsXGJUxtgn3sbrPvUEQO6Rcy9q3Gb1BRD0u404fE0p4TbqpMYlnpzHyTxROSdwYvyo1mztk
OKKTCm6Y7ZFlSaIm3Bss20xRA4K1eMwzPVJP76+oPAIYaw/sUWDJoSbwnRxOgBS3DxkXJone
CtZCS0qSLs+0c0BcFImPkprNHh1ckCyBo/WG1+03QTBSWRSA6ujZtVjgpytrlqDLdVwAAc6q
NNSwwPQeTdYh1IRzJ21GOYBbIWVUzpGDnHquQRX6oqZPL4Ye80aTF8CkO3f1GVI6mHJ4MJ4o
NZs1+nxBtBDc4AEL2XRYJ1ATjp3kme2XuWUgECM/yyD1NBYJjRoKLF5Hke5tveU8q+bCWPga
7ARxFsAfYVly9e8qvEGscEHBSY1XsyfBdJXlalLhGtTidakXEfCloTOmXEHQBQ5dnF/ozwOz
muWpV2I6/GPg26oNYF/guxO8rRr2BYtcdy7oC+C7r3l9geBE/DgY//Hffd3Ee/c16sPvvpYy
Ho9/xkYdfO68emtbIwTHo5+177y5KKRwdzeZeB70GEMXOYY7zbLQk5r5Lq+02PEXuWUSN8eZ
z++hDhZIbirNz4S1+GmPK2sg5kEHam13W9MMCpSRyBtdDhKchcDsm4blUGG5BKJDC3WwUAvM
ATaDKT8boewOdQHcnOSXQyc5WcNS87v9SgW8thu+HCWdBa/GHUM1Xh7W2F5I9Q/4IUpBiy0o
Dibduy+bSYPb4uj0uLaXaaRhgWGNA09MwK3f5kNabJFN3A5k9w8tO+Kri7QSJadDQuAkvNGT
x+vRfZ0l9WSibik0iOxO8prESReOQ2n+z91gwkewxaU9wH1OTayFTDySBh4qljIqeixV09fQ
7K/FVipdfOlXUtBwo6/RBMzBNqOAhW0SP1saZ3ve9Q2CPgQG1oK14PXXkiEPYwF2FxMQaQgl
NAJ2NpkeJnM7M3n4MrJ+8VF7cUtqsRgEJnMhyVnW1TT3bLCAdh8JGLhjco5kiIA+mcuice/7
HWp7ubX6Qf8Y4KyWlCCVdr/Pta/6V+s3iBxgxceQcTrVcdU/d+ourgR3EIZwG/V8VPIOv0Hc
B9HRXMguPfKhe1fnQ0CzGalo3au1fn17DhreYr68XGv9CZQbAFqcEpPwUdzJ7UUsTsnsJHXV
PX6ybH7AwQtMIrMXfxDglJ0k60SRrBGL42qMRKPp3ULtss5z91DSkl8gY2OuSz3e6E9B7t+n
m4kgkM9L3ed3iH/5u1zTp36ubdoQLNS5wBKo7ksdNGlFCU0wxHEFVS//VOKrmDrQ48b6ChYs
KKtsSHqeaphi6ElGaNjm0Xat/DU98x7Rtq8p+sEti8QYvfZyxhU7VnOYvnpX+BgW7NQSHhjK
PR+4siwuXujbaW7AhUi9RYK/+2JzQW9cvOd3GX5CCPftnHGl+OFWENkjc5Tiqp9PN8f4O1e1
Zq+127PydRtZd1cUtjsd78/e3xN/nWu4DboxruaeGLo0K/5G9LHzk/iRR4+19kbM32fFg3f/
4ibxIKLR2tKyCBfa3sLfMIy7o3VxrA8sAj1QbiijSUH3sUoDYiTbS2IqBb/TjBqPAQBrJXyJ
bmKk3VKu5SNyin0grGJINhTFdAH/9wAfLxlq6mU7xjbbDuIu12fqcsAQo2y/RBVqgpnvudDj
3ljggTTMuZ91gEnPIXzEs6eknnqwlBbFi+za/8ojMH73CEJU7+MsfNCIrvzdnRS/ynvxumPS
vbTn4vIExnHW4I/ufk6vCshdYDHtHQWLZP948GwmmGmxXIUKFtSSWN6hz6id2fFr/1wrLUCq
+HJ06GcuFu0Dvt80Gs83rfqWJLbWR0PryT4SmOE6jx4571U9e6En7orv7rg+DdfMfk6Gr9dC
gRu6yH9z9eSm1U7oEdyJrRMHnhs8acjwW/X8JY6TMQjiRFa8jcMc8jKur3a+QSwOCNGA2TTp
t7b5VXdbEWgUeDSNsIg6+AA3NmJVDS4PBcWhJ/carCM2TIIm4vqw/+bi2ntXJaciSWB5RWEh
+dDmQDDEveB3SEHFR5Gty/lKKCHdRksMLFgDyxqEhZu2ZgjwN9FYmdsjEGqqfgcpam92oo0z
f6afkKfRkFEv7IlSSBmz3VhP0vdgDs1tp8hRfWsrLpv7K7sSvV2bg3x619F6PKmqjs5bnJj6
ysijG2u9kxsyRSbV+mLBssTJ6dCJNhubg9/udcLbu0WEypLUNtUYUFM2Dw1ODw9Y7PV3Qz+f
wDivkm2MrzZvawveh+6Julmxgm2S6VSZu7ORpk8n9MOF8Ox1T322bG244PfRiRp5T+UWtda8
Mx1iU53+JbUqLZvt3XDp8dav7dQVTEtiIwcpCl4DNB0PXaK/RmhtVbR1w8QlsNDnADaCMRRU
JDTy44OFaxuEy8lH5LxUGXZdurtNKM2t3nP67tj7uMhz2NQzJvmSJOP28brkSo8aRckvNJX1
DKv0KoqRX924jkAICzFjwrTEz5xt6rH80Uc/b/OuU5XX9Ksvkp2L7ErOvZhwVgq2rtRXt5GJ
ig4cD9Oe7WHtD9l/RFwnVON1Qx0tYJfJ47PMq3esZx9WJ6Sk3s/XrraXa9XiUiN/qReWJH9n
Nq/0+Zk/eYz3Ev47Fuhbhh7JJxHFO22wo84Cp13eo/jvvfz4oGK97Qvs8ZQN4/UD+TceyXc5
I7+pbmv1EhshHcB5EL09t01Uui4eChqbfezjyAm6HrBWY0KkmGvF0TJNurqpdBc2X5s5oHc4
Rjbgsjb3UXGwP77FZ4stLRjs66GP7l1JW3VyvLzGOlzBKv/71J7+sLRpcP9gDUktM0kU7bal
hUvftKnSfEQ9Wi5mZc70jull8i2PxpULnE6MJfcMsZd7OFZjGCsXy5N01NPtRjZTKfWR29O0
Z7mEFu0KQjA1ieZyVvqtuB563XuyGFSidScBrOIJnHcTMQEPa6Cd2FcntStFCeEUVm6+2jC6
PV+1polqW/X1Gu/ZR6z2kyxSyFzvF1ObOI9GHfT35Kr5NW2JqKwZ5kRhZWlRxSKipklgpbjT
4zangsy9h5IT+zZmidFjey2e1KoMXfX2ilCzG21J92k1wojWIIuNmcKKyBaBs49PZec4h7as
aFjABsUxN3LDnHrcjTYnxqm1VP5CxZHtdjXThYe1l/dc+Pcq+gPY/gvd5de0ZwHJ9pdjEGqc
rkFE7v0PUFhK/kx0QKsyK7kiYAN+uiTMc6v4WQffpDnCrSCsjx8mTB+ts/D85iIGrVejbfiy
OXBCm2np8mve5x0pEz1CwSayX2Sp7SIfY44Q6Dcwymq/piVOtJbRFftig4kV88paiaFTGOFv
0gxXaKina6ws2ix0hSgiVNYfKR8Y61QvzMKPVEUP6zSS9Z8NRFD9AkeEN8dukd7xK2JVSnPz
GwQF3MQaomDb7VYO9Y8MvujEgs0uvHLXBOznc75yZWnKho6xsEvzNT9umKkbKemqxv86pFM2
YVoeKeNgRiZcTXPK5uAu2KsTmM/F7YG+TwybUnEp8EE0xZ7w8OlvNwjV1HtZNmqyXBjHM4mF
Bv5pE5JDnhNYg3PUMbohbaIeF86xWvbrn6OTJdHx/5cz3SwHTbqlCtYUzeTObAmLk02hm84I
xczYfCVT8EfQv3u1cQGPGZxvYKxWYlz22iRw4e+W+1fgPv48x5behPrjDq1C+4zBArY7IXgH
m+5KL2KYW1f9xPSOSWxQgJnfGtdeCj2tF7wEVxcXRF2+XcEsh8DCOtWDp+qVMRiMVo+Nn7LS
asZzspyETQ8ZbxBUtJmuerobq783lBahbG9YEMRN9MzgJNGi5atFsYq9o9NB4Z9fYREpnsv2
EGkB2Z6rYpz9nY8iN4Ul2TWMaTTUWzeWFEdEyk9H14jWd+eIbO6iEqdXWQBBCaTGxFx+ePq1
XSTF8Zqm5j5Me1kZAy/flG4XGElNyaWy19UIgwXVWrFbs7ft6iWzuuc1wdhwGxi52QlZ27sS
f5jvRt8TP+d6EOe05h9RGMu7+rtMS57ni/WHB6UWOuUkFYkothEJEwVy0Cx0PE3Z967ouaQG
ijnMuO2YfRh31ow9Segua02XWsckDf0MNoEo7ptNeW23cB8d307vjtNu3Xh7TfhcsBzlhXZp
41kMar2y17+itf98mf+5ZxztVxdb9j/IQ9lmCj3ZIXjlob1JScCNExZBSTY4zmCsI9NNbJGQ
FEl8OmODC49u7QK7PSGmSK0igVL1dZ3c2fY3iDzB+VhXgbm5FlQ7WOzIuQAGTQbSJEvTgPle
EndUajjoqdDgoAtYODcC1nivRJl7mFHtUxL5t728I6YLn1+5F0Vhmb6oeTRi9boxRpRe56Qv
Wo1swUh6CdK4fXf3cx/ThDgv3iAWO7AL+c6tU2GlbRutz47oE9hR9KJDsazcqU1MtLlylJ2M
jExKjYhkgdpBvsBX/bpgUpQWP4b17rBiip4qadkYEuUmGUS5G3VDRGrdcioLGcV0+75wwMHQ
DgTsrQIZ85YjV8BuJOc3yX5MY/9/b1sDNhz6yNrDIoN4zQbWeH8hnXj03IBySD7ntcWTwnyn
lPrduxMDr91NCJ+osbTrpzn51ohiVXUH3BCXgsDWWFSKjW2VMrJMaeK6wUGPFHuaaGUjPeUc
TlPt5fiWOoJ56j1wL15bx+Ln0ohQsJ1pREpvTJGotq5PfIUIOU1NrLIztLZmGlnQHG4iGfCw
6erJ7JO3F9YZSVZUpWPQSB8qj4CNjc1ZyRmooFGNi7RegoNWeaZVYIrHva3KhqNVsb6ZkX3s
+Q67eXzrc6xcJiE4ISUI7gbCVlTsD7pwLvXIYmtIpnd1k5iy0pbKe0TxY69kwK6M9RaqHs0U
/1wWdTuZcFqkAWD/rHCQlNrd1CyxvanaP4IRFkO1EzUNmigWYzfEysXYyThV6NKa/O5rv5Th
xEWTiXosqa1qbMmNHo6tCT2mMVTKzu5TI9Mn7MiBGyo+Zk3/nvzPxgYtB4mNqC+TuQI3hXRj
Gcn27guoFwvm8QJ/WF7Jp/YPcCvLnBA0KiUwWvHySLucZGbKWl9Ec/vVX5YPXPgIQ98895l0
7XF2HZEnunSMpKw3CqHaeZ/KwtETB4TNVczoGPdio/VoYS1q6CLFmvFIaNN7T5H86xtS7VY2
rhnBbYy2uBWGEbV4wnCTZBnrVSpjRMFOQ21biJ7k86K6ghrYbK/Wp62MJ/cSI+Kt7JrD5FwV
ne3Ed9BCdPy/oI7gk9yxxrp2ttV684gKxktsz505bqclp96I+48vkq5slva+1ZB3vLG5Hdu2
oJx/mZa5iMI8o4Uk9jIJ9BNK2+jmKjonjZ8y4X06ZeF2mjf58Hej6yMqScfYYc8Mvxr18svT
cMxRJebeDrM/UVpZQLfaCfYRoslXSqGMDYMjkw29wG4cDmLYSUcvxcUA9dThmRhOYbSmbJfB
xRLJjY4p29jk7QYRORnNe0OuetpoPozZrDWQaek01h2bKipKiAidLJMrQCAkbXpb9hJeNZtk
DdYpzGquEV/FfXDLsrYx3SnpVlWxvtIaS4/KE9P5yQMbe/SRm5pCMS30GyLtmdgdkfFVI2VK
QvGHKhn5ORWd0WvoyH0mTg/dTuUbl0a2atxWsKTYzuduo2g13d/0+UfMAPF/3QvW1yfUrx8Z
uxOl1RvlrODUb2q5dTb8VX8wvUb/lyPU2KEaZFDwSOVcl3VDyrLTWTIv6jQC8jPWXKGxi32i
u2vHMn7Za1vNSm2ltG5efDGl6z198VHpZzOWmTO7ihzzn7Cjroqp3KNfdl5bMWMll2/sPWyR
SqPQb1VimMhKzGG5UZ70N3ZNRD0ZXNjcczmQLklXdt5YRyOiBHqJ2mDhhvbJwGnZTHGw1aJW
pG3TysxO7lSdl/PjLM5XBLBbCFOtLT6E2qVveVDdwZzCUjQmqlTUNFk3BoWvepa3tcu/oVt3
DWFkHcEfoz6ZXHzZWalWxxVzwj6cja/0ywcLIuRiE6blKKdFvRACPbl9NB2sAgbsMqBXUTEd
SHY6gGg9nHO1Jieo56hRZfOGrPGsx69KQxg/nzVJKnaWk6/HYB9tj9Eu9rRP2U7VrNERe70+
VRiEcfsqLlu/0PdC3yg0OJlNLKpYIH2T0Ilbd85OrSeaaRQRhjkl3hfjhMvxoaJyVvZ+zPz+
PfkrvKZSp/KHYn488Qax7Jlg3MdWrKF+aU+ha88IXZyxOf+d8y0hk3pBJMJxpLhumcf+v8HR
sqQssE6jP5oxv/0Wp+ki8b3dVVfgplI6Ma2mAc0i18LFZKhZ03Ek7VqZ8BHkQbnwHLvcfCou
x4rqN//ys8AVWZNuPW4Cx5uaAnbuS0JT2h7+3JpPZQfSsc67gvA2eXd9tHKTWyJTnvrYRNFk
q7Uv6V9AIE7bnvC3deeKj5r0riAMJ+s5vZBuHt9zIhk7MROJItWAp7ZfzuLIW4VROnpt7Enp
H0aPGOpYfPYaG5M3e5mZpqkm3xSSFoc1R+mao3WGcvtHphQNtISN/czLpr/9OuNj1f8/vvfM
GO0262lj1EGztg2L+Ucf4HJMbg1PNE/S1ag52CbKgaTp+ATWwNxti+QE86icU7Ths5Y5yMhh
rDHTeMFNScg6gD7v7kLz6Zf4R+OputHM1tUySqNKCtbNDP2kNBFhbFiOvjFGsb2yTbaqye/C
2Tt9CW5Fi3cUSYX5yrMaUrEPqoSmzcDi7FWTVa87/IMDNFGNbuILm2pQYRfn5CTAfM25CstR
Zz2ugeDfLnjJPEes6zanGytH3xSUp8vsq+WIZRrE7clx7zYpvRp99Fh5um4/IZESTDSlaXvH
7pseQXpHrJxb4eRxmeWp7uO4WT1iTUx8JVsXZ71Q1XIi2aiNnnu2XtW0bMLHN8Sjvov7aiTY
ZkvLJanCm2a3J3qfShplms7pJsTjHcyPc25XvUxpG/c4RVcU3rM+s0LPNKdpixzFCpeyZQtR
T8f4hwyXmIT2bXmnCkvo5GJHlP2AeJcmJSqnR2UQLCSJyMH7XkFP3ZGb9S3Iq9NgFlbc9a4o
6aqroFuFj6ifr0+zi0Vq5DSsE/zKu4O178eTma+dLPY5HqVto9hdM9+hpqoZFGOlGb3rJlWG
lBVIdhd+8IKE0SovqRTZ96PE2hrl6ZTqKpqFWnziuUrFRDuC3YR+QrAMrhRs4D6mjcF4aE9H
UGSoZ7dObrhXI3vzLhc1RhYPNI3SSyFIFj3PjIrAs1APe3urFc2v7SXOUgNj1jy/0RsYuyWC
zdq+4qOx18fa2N/M/58LFiFDAv/8af0vpELyZJpb3DsP9Xaq9c+2rCm/aLGzLXgLNS1llpru
DzZPZDqxVLDC7BpEvdQ1s2/b7n7ZhaQ9WVykMIOS+iJET6UQDcPKaP00/9qqatOUaCYaWTs7
r6e332uTpbuT/K3sDHZzRubdZNlTr/Dbnj2pLM5RMU8jRIyIohXBsxNgi+OeFTnjhXUCAfvi
jhQ1SzyzNmtqvtSCtkn2FNpIb3I6O81mKRjpEsOnKuastlPbKb7Gui8KbLKaelB32J1BzuoO
YzRrO7Vhny0vGFdVn85jjFRnEmPwVt9KEO9EhJpPE+SH8p+Xygdd1AkcwYirLpyiI1lq/Sn2
VL+yoOtnUhVbz8xgMlyU3BUsVOj0GrMcHWOjpJ4G+lWKVX1fcGxwV1R9j+xU2jo0Ehfc+/Kz
sC6przgxorTb8YyZy9lKmcnEk/nqj8bH5WYH4qvBfElPbLDVlsjz4NkqHNy9TJBW8PgLZ//T
M1Fxo7TTHRiSEVOh9BZDpaLxSUkQeUeYj3WfY7VIm19EdG2pDzXwegPj0sJ3TS2rOwmtnQaV
6So4InHtXTsFjJ6Ot7iNTRJtkN0z1pIDdpBqrmxLZPcMfQHHSv/s89+wr/eXYh1gUxOtpCcG
57d1D+8SwU9k+O079oypcm+5e18sK6o+NptyNQd53Peh2MLPFYTYiKRMrd5KpPSL6/+M0f9y
3sduA5wKdZuKCdekuHqiSjsjp/3jr4qw9edFT5FpLhs7L/DILyflnp4r0Tg3Fcnodig4t03j
UZqrW5rzGZtuk7LSMhomqc6pWrQaHxyXaczUm6XIyFhZ+UkHtHn5nHSqDKMOSBiwknTK67Me
63gqpavVaXpNuCdGjCApcX2Pds4bo9tYyPNsM0/q8j2pp/JDfHqQOlS2eaZxtblojQp40YsW
RUYWbvQs0IFArLIeD6oxvLrw1LZjOGTi4r1HGiRVNKHnQYSNY8+AWD5SYp9qqXdwHM2e+dRI
WKv7mZ7XATVfxc7Qso6e0lfZHkX5q0puPDg/7XsbqZUwooyMTMEazw7mGHOo1N68ioqKS4n/
ZWn/PQTrrZlHL0oYdNMQ7o6oK0T8cH4im11sjymvGRsgG5uVTKnOYzB2EeFjTFGzuN6tvZR9
00HsBsk7R4dXuEpd0MxinZcwqrbVrVNdLL+VahRvlhKZan0yVWpj8brWYBuryN7aGssAhldw
fxAb63XhecGfmPrqQR0hMrGHdhC81SM4C7niaYWPNTOnmmN1YEce1STH9taw0Kl8pyRP+aHN
DH13zGZKRMjep3p6hrEH3C/8CdmfEz4STSLWd76w/LYF2TNoZxpnlGMQlDd5VdUodnA6eYZK
E9FauDJnTbuVptzLbi/WrmDqlfrE3v9BATlOL0kxoa3xkVo3TTCQ1MLatEmmkvWx7kN9k08b
GcKdEezeUUxnCspcb3ktYCkvLxcfVtJmC57zfbyRbZ9OMaWvs7XPSVNzH9o27etJ9J0Cuy/K
amPMFg2dJpZp3P0Z713kdFwNYyJZF99D6apNpCQ7u5w1CcYr25PBdkDe4ydw0dxNrsrsCrAo
7tKfd519XwqUmbBHLl4RRck1RSGGSlwZycFqtwy9a1eFRQiVvySJNlJzNc27i4XNKjxDWzvW
u5XZGviVPrMV4Yh/zQn4KqOSwD0RRdR+NTbZQryJ1qjfZULHzNfgt+By5vQVxfrH0JsHZmcn
BPZeeJ/s/77rlVHdKNmFbFcuyzvPsNPmVoKdh65zZHabpuaIW7H/02pzV8mnWFX0sIAIh6Sj
sMoO62TRaIZu81lXr6xor3bNYZ6w+MxqWybW2T8xxn2dzosfZ5SJxfYRUZNNc5FZvhjs84EG
csYXSfbuRzrXig56jCCVhtkWwbb5xrgGrwbJXW75rj5WyPbcLx909H6Tl+Syb0tJfHo2Jp41
uH6RGoeps0s69oySPYnVbouIZVqwc8+v2v//UoZf7ArUFOsUF3PGzUoYdEY3tmLdI6guSXUq
9D1u1sXNxfrK+Ai2vsVGYk1fdHWbbMbyR7HBYKM9Iz00WDq5ZWuGNnE/XDn59z7LXtarrFnt
1n9q41pWtYuqo7ISWfZGwL0QnXnxxLlIdr2IvtGwnsDXMw9e3bmpsNWSEfOQ7Wd6zqY9IiUp
yg1VbjJGvL0LjWcKLyavq5Ec3YlMfzmPs2SYmxLDHS2/qFhcuYFOqMMYjTB15o1Q3wr0Huoj
Zg5ZUpILKwwSo2yQwde0aM5iiRxq6pYh3XJphu/OfqNnsmse7RzYSKlnqmd5gIjJDW8za4/c
5Vw7DfazSeDsoDDIr77MeqXit9W5P7xJ4fLDzv5c/83ZmeSgIKsoNYdqSbjGIRhHxktvLvh7
MvgE9UkCnyTwSQKfJPBJAp8k8EkCnyTwSQKfJPBJAp8k8EkCnyTwSQKfJPBJAp8k8EkCnyTw
f1kCpDeN/OpdYLz9R8H/N+9/uG9AKoS5wPjynXwICz/LwPFuEQAH8FxgvOGV44H86eezt2V+
y/gWnvHKwbIoiBMe76b9fs7L+MCPIQLQFUQj3BHnEDiEE/h1gCnwWGOMwCM8QIo04hg4O4dw
A4cTwhr8gtxVuxGqCHXEHoQiQm2pxGY0D8IN4Qzg5QG8J8DpDkqcB+lnAR5ngM8dnDnzIKQB
LRzCFuS6QwxvolYZI7wRLgB271/QlAblzvH4tAa/kMI+AKUNMDi+pYoDqU6AqjRiG0IP/HqB
A/v2/zBiOw+rCuCan6OIUEIov3fuCHBBrPqIMzxpQFwuAKsnoIAH526AfxfwdQB8Qh6VwHc3
+BeRhucqvPMT4HoXOFR/y1HjnR1G+PBwH3sHn/Vbjj0AXRdQK34NIGZFcGB58O/KVBphDDiB
8nQCJR3AYfuWk8NvJSmNsOHpypWnOagtbx6WA2/5xoGUM79R2gmowNqcAal8qX8PMC/px+0j
JfGAvjPgHPJrzcPiBiS0lApxO/C4dQe8QPuRBnyfAWkOCJgHdXUOWAnUNx6Ug9cw1QZ8IZfn
3kLBfCceHOTzr2DOv627PMIKQHgDLJ7gH1I8D/B5ANx8XC483s6CFGhBfFlDecHa4wBX0FZx
ANaNR5mvGxtwDTHx7V6ahwHWma9jaHnQJmHLsQVp79Yd0oatyuG9dCh/vjTehYZcufN4fzcV
wlnzoH/X2R+pnOXRXqK/JF8+d24A4xmePGEZWC94DXUB5ej+tpawDOR+Cce79O1B6lL7hdpy
B1++LN2A3mAbdAdY/6hXPs/nQP7vMobtAVqrFfh68+hiEQdBGkyHunIDmnqX7l/r78+2CVP4
tYJW9a6M3Hic820a2hJfv7CesH1/qBy0ZDRPQnyrgDYLfRgeHEtlDyMO8XybN4/yubf2rw5q
pQSgdRFL7VwHcAS1586rmRPAYA3y3cAvbANngCSWbI7vS04BaH6L0+eV4+uF316hDX24pAGQ
LN9rQWuHmuVzC/UCa873sHx/xfdV0PdJA85hKcO3mnIEZaFdOwJsH8OyE6HxW3ltQANaxbtt
im9RsP6QqjLoIaCX/PWtP4GShHn81i4NZMH3AUt+4s9l0KBW5wCcPZA8tCBpgMEDXOOBr4LQ
v8vuIA/bH6W7RMcR5LkBHEvS4fdG0rxr2I4I4IDtEOoHyvscoMLvW6CVQzpLkj7O4wb6YejJ
YHuC5WE5CNUADkVePwPluQ2cq4MvlOwj0AtBmf+xPGyVUCbQy0Dd/at4oH97t5f+e7x8uJfn
ew3oHc//Vq89vHrAWqmB/u7dOhnzWsrvPTpfgtBjLMnbGKGDOADa/eH3dPaxkrAe0F5hL6sI
LAl+oT/x4snSGOCHWnqfHiylzIOEmrQGV7A8P8WRxxPUBJrHNd/HLfHJtwsXYAnuAELxrY6h
ZHHggPUhAIx8rpa4Weqrf494/hk2J4DbEVgyP6qAfZ40iFh0QDQDvSn0ijagfh48DwvpQg8G
bQPW+gwo6QLSIH3YCl1ArhtCgSeLv1sbiN0ZYFrSDcS1ZNsHQc6SV4U05QHskg9ZqhO/b+R7
Nr7NL5X+B8AK5QTl/Xs5eH6OJzXYsmxAzWB/CqlDWu9SP/ReHr+eujwfCmMvWF/Y7qEU+H4H
+mY3cL2EDbZIGDNBHcsDWUJqsHeAXgP2fjB2hJ4AwlvzdKsHzvg+cql+SxKHlCCPECeMCaHe
+N7BEMiLryl4Jg+86CHwhXAGgDYfnxUoCXtbPlZ5QAP2cfxavC8DfknYo0LeHN7ihn4VWhzf
K8P4l2+z/J6YjxdaDPRcZ3hy/AcoC2N2WEsYf5znlcCCfHjOb9HQw0PMMGqD8v8rPX7PS4f2
yYeB/vePGvvd534PxgfyAPKP9gRTVYGPgBxD2UGKUBZL3u0Y4BTaCl8PEOoAqDvsFZdsHZaA
tg7LwfL8KBJaizzwB0txNz/O/hX4FYgDWi+0bQgLIT1BrWHd+ZJ7NxdK/DigqceD28PzKsq/
cQs1zY8BlujiEbKAWxiVQ6uAHEHJ8ftuOKbwBjRgDr8PP8HjGraEJQs/CGxEH3gTyD30VZDD
d6OMd/k8hsC89TvQYxrwOISji92gH9EAMoVe8E+jLziGWnsQwGsjLP+Qr4CwA1K0hfkicCTn
zOvl7AH3ih+GXBrTvf+/8ncPBPC9mytI4NUf1hjG3O/l/k9ef8mPCeFIBmrkLPCOVjxL+gBP
AhD+t3Hvv43TZTxMQgiBt2PvZe/9f2BIzkvmwS5HIMTfA5oB4/2/8xn9m3B/B9e/BrMTFPv6
P1E0HMAeAAdc6b6SV27//h94//y5FDCfwXAH1x/Q4QfTeSje/sCyH/t89UEA4b/O+fKDpAG5
FbuB8cGGC84F+OfvV4CPtRdYCdA34j8AMXCSyw==
    SensorDataFile = <blob elided: 365386 chars, md5=6bdf4b68>
    Type Image = RLX_057916.jpg
    URL = http://relux.com
    VarID = var1
    Voltage = 0 V
    Weight = 0.00 kg
    Width = 100 mm  [stored 0.328084 ft]

note: [stored X ft] marks values corroborated as IEEE doubles in the binary element streams (Revit-internal decimal feet)

## geometry (parser evidence)
native form markers: Blend x4, Sweep x23
no freeform markers — native parametric forms only
